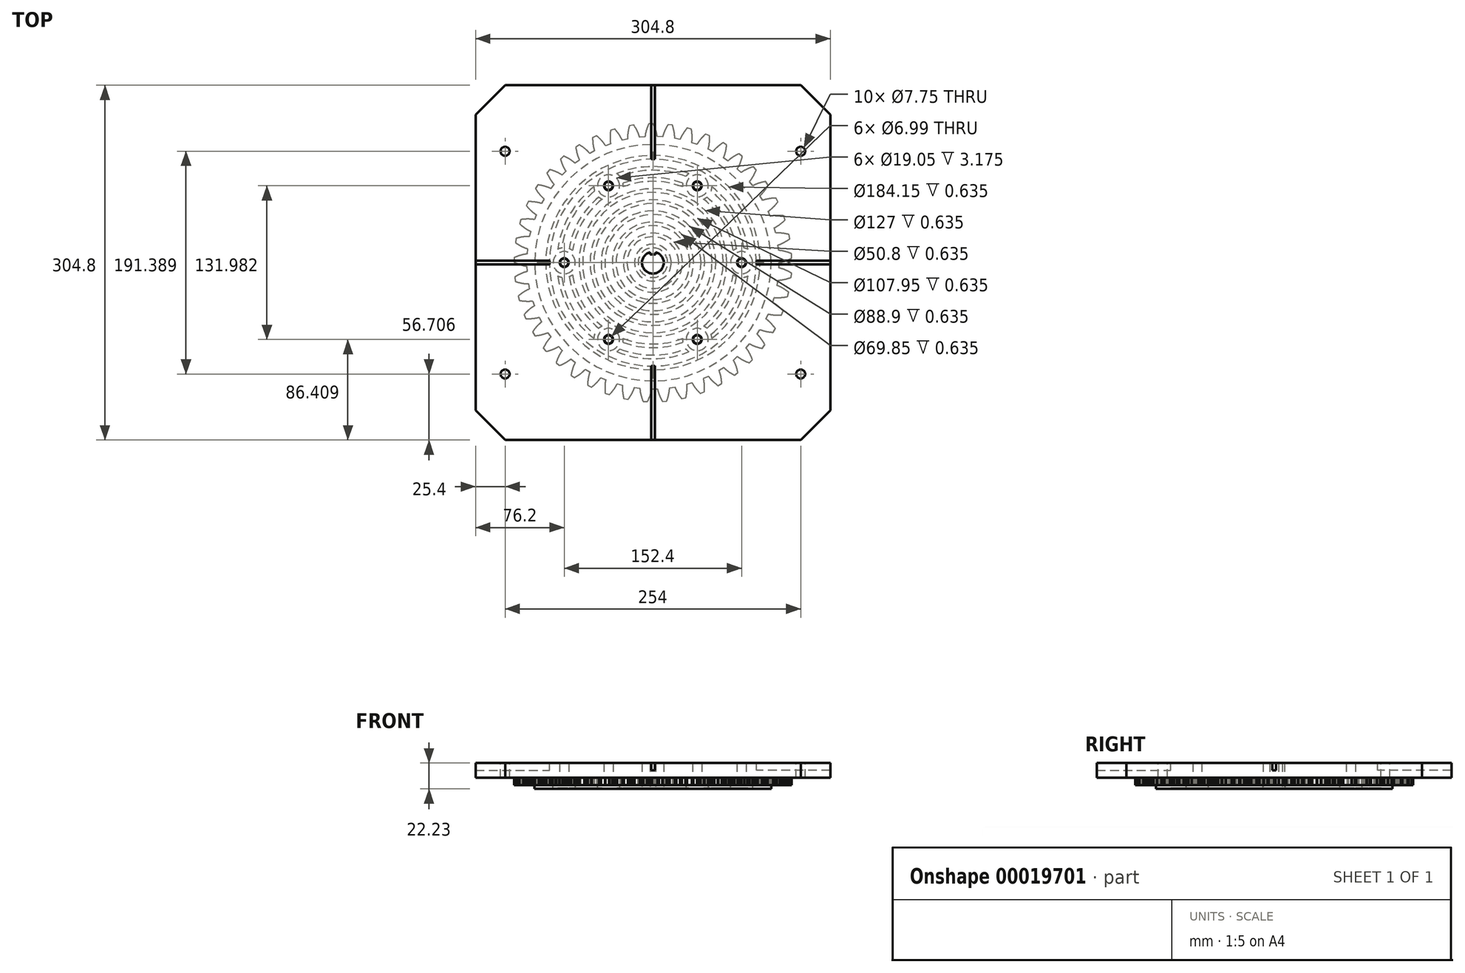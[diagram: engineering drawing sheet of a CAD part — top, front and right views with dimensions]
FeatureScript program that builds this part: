
annotation { "Feature Type Name" : "Feature", "Feature Type Description" : "" }
export const myFeature = defineFeature(function(context is Context, id is Id, definition is map)
    precondition{}
    {
        {
            var Q0;
            Q0=qCreatedBy(makeId("Top.planeOp"),FACE);
            var sketch = newSketch(context, id + "F0", { "sketchPlane" : qUnion([Q0])});
            skLineSegment(sketch, "E0", {"start": v(108.5, -0.05) * mm, "end": v(108.76, 0.09) * mm});
            skLineSegment(sketch, "E1", {"start": v(108.76, 0.09) * mm, "end": v(108.9, 0.11) * mm});
            skLineSegment(sketch, "E2", {"start": v(108.9, 0.11) * mm, "end": v(109.03, 0.13) * mm});
            skLineSegment(sketch, "E3", {"start": v(109.03, 0.13) * mm, "end": v(109.17, 0.16) * mm});
            skLineSegment(sketch, "E4", {"start": v(109.17, 0.16) * mm, "end": v(109.32, 0.19) * mm});
            skLineSegment(sketch, "E5", {"start": v(109.32, 0.19) * mm, "end": v(109.48, 0.22) * mm});
            skLineSegment(sketch, "E6", {"start": v(109.48, 0.22) * mm, "end": v(109.64, 0.25) * mm});
            skLineSegment(sketch, "E7", {"start": v(109.64, 0.25) * mm, "end": v(109.81, 0.29) * mm});
            skLineSegment(sketch, "E8", {"start": v(109.81, 0.29) * mm, "end": v(109.99, 0.33) * mm});
            skLineSegment(sketch, "E9", {"start": v(109.99, 0.33) * mm, "end": v(110.17, 0.37) * mm});
            skLineSegment(sketch, "E10", {"start": v(110.17, 0.37) * mm, "end": v(110.36, 0.41) * mm});
            skLineSegment(sketch, "E11", {"start": v(110.36, 0.41) * mm, "end": v(110.55, 0.46) * mm});
            skLineSegment(sketch, "E12", {"start": v(110.55, 0.46) * mm, "end": v(110.75, 0.5) * mm});
            skLineSegment(sketch, "E13", {"start": v(110.75, 0.5) * mm, "end": v(110.95, 0.56) * mm});
            skLineSegment(sketch, "E14", {"start": v(110.95, 0.56) * mm, "end": v(111.17, 0.62) * mm});
            skLineSegment(sketch, "E15", {"start": v(111.17, 0.62) * mm, "end": v(111.38, 0.68) * mm});
            skLineSegment(sketch, "E16", {"start": v(111.38, 0.68) * mm, "end": v(111.6, 0.74) * mm});
            skLineSegment(sketch, "E17", {"start": v(111.6, 0.74) * mm, "end": v(111.83, 0.8) * mm});
            skLineSegment(sketch, "E18", {"start": v(111.83, 0.8) * mm, "end": v(112.07, 0.88) * mm});
            skLineSegment(sketch, "E19", {"start": v(112.07, 0.88) * mm, "end": v(112.3, 0.95) * mm});
            skLineSegment(sketch, "E20", {"start": v(112.3, 0.95) * mm, "end": v(112.55, 1.03) * mm});
            skLineSegment(sketch, "E21", {"start": v(112.55, 1.03) * mm, "end": v(112.8, 1.11) * mm});
            skLineSegment(sketch, "E22", {"start": v(112.8, 1.11) * mm, "end": v(113.06, 1.2) * mm});
            skLineSegment(sketch, "E23", {"start": v(113.06, 1.2) * mm, "end": v(113.32, 1.29) * mm});
            skLineSegment(sketch, "E24", {"start": v(113.32, 1.29) * mm, "end": v(113.58, 1.38) * mm});
            skLineSegment(sketch, "E25", {"start": v(113.58, 1.38) * mm, "end": v(113.86, 1.48) * mm});
            skLineSegment(sketch, "E26", {"start": v(113.86, 1.48) * mm, "end": v(114.13, 1.58) * mm});
            skLineSegment(sketch, "E27", {"start": v(114.13, 1.58) * mm, "end": v(114.42, 1.69) * mm});
            skLineSegment(sketch, "E28", {"start": v(114.42, 1.69) * mm, "end": v(114.7, 1.8) * mm});
            skLineSegment(sketch, "E29", {"start": v(114.7, 1.8) * mm, "end": v(115, 1.92) * mm});
            skLineSegment(sketch, "E30", {"start": v(115, 1.92) * mm, "end": v(115.3, 2.04) * mm});
            skLineSegment(sketch, "E31", {"start": v(115.3, 2.04) * mm, "end": v(115.6, 2.16) * mm});
            skLineSegment(sketch, "E32", {"start": v(115.6, 2.16) * mm, "end": v(115.9, 2.3) * mm});
            skLineSegment(sketch, "E33", {"start": v(115.9, 2.3) * mm, "end": v(116.22, 2.43) * mm});
            skLineSegment(sketch, "E34", {"start": v(116.22, 2.43) * mm, "end": v(116.54, 2.57) * mm});
            skLineSegment(sketch, "E35", {"start": v(116.54, 2.57) * mm, "end": v(116.86, 2.72) * mm});
            skLineSegment(sketch, "E36", {"start": v(116.86, 2.72) * mm, "end": v(117.18, 2.87) * mm});
            skLineSegment(sketch, "E37", {"start": v(117.18, 2.87) * mm, "end": v(117.52, 3.03) * mm});
            skLineSegment(sketch, "E38", {"start": v(117.52, 3.03) * mm, "end": v(117.85, 3.19) * mm});
            skLineSegment(sketch, "E39", {"start": v(117.85, 3.19) * mm, "end": v(118.2, 3.35) * mm});
            skLineSegment(sketch, "E40", {"start": v(118.2, 3.35) * mm, "end": v(118.54, 3.53) * mm});
            skLineSegment(sketch, "E41", {"start": v(118.54, 3.53) * mm, "end": v(118.89, 3.7) * mm});
            skLineSegment(sketch, "E42", {"start": v(118.89, 3.7) * mm, "end": v(119.24, 3.89) * mm});
            skLineSegment(sketch, "E43", {"start": v(119.24, 3.89) * mm, "end": v(119.34, 4.07) * mm});
            skLineSegment(sketch, "E44", {"start": v(119.34, 4.07) * mm, "end": v(119.17, 7.58) * mm});
            skLineSegment(sketch, "E45", {"start": v(119.17, 7.58) * mm, "end": v(119.05, 7.75) * mm});
            skLineSegment(sketch, "E46", {"start": v(119.05, 7.75) * mm, "end": v(118.68, 7.9) * mm});
            skLineSegment(sketch, "E47", {"start": v(118.68, 7.9) * mm, "end": v(118.32, 8.04) * mm});
            skLineSegment(sketch, "E48", {"start": v(118.32, 8.04) * mm, "end": v(117.96, 8.17) * mm});
            skLineSegment(sketch, "E49", {"start": v(117.96, 8.17) * mm, "end": v(117.6, 8.3) * mm});
            skLineSegment(sketch, "E50", {"start": v(117.6, 8.3) * mm, "end": v(117.25, 8.43) * mm});
            skLineSegment(sketch, "E51", {"start": v(117.25, 8.43) * mm, "end": v(116.9, 8.56) * mm});
            skLineSegment(sketch, "E52", {"start": v(116.9, 8.56) * mm, "end": v(116.56, 8.68) * mm});
            skLineSegment(sketch, "E53", {"start": v(116.56, 8.68) * mm, "end": v(116.23, 8.79) * mm});
            skLineSegment(sketch, "E54", {"start": v(116.23, 8.79) * mm, "end": v(115.9, 8.9) * mm});
            skLineSegment(sketch, "E55", {"start": v(115.9, 8.9) * mm, "end": v(115.57, 9) * mm});
            skLineSegment(sketch, "E56", {"start": v(115.57, 9) * mm, "end": v(115.25, 9.1) * mm});
            skLineSegment(sketch, "E57", {"start": v(115.25, 9.1) * mm, "end": v(114.94, 9.2) * mm});
            skLineSegment(sketch, "E58", {"start": v(114.94, 9.2) * mm, "end": v(114.63, 9.29) * mm});
            skLineSegment(sketch, "E59", {"start": v(114.63, 9.29) * mm, "end": v(114.33, 9.38) * mm});
            skLineSegment(sketch, "E60", {"start": v(114.33, 9.38) * mm, "end": v(114.03, 9.46) * mm});
            skLineSegment(sketch, "E61", {"start": v(114.03, 9.46) * mm, "end": v(113.74, 9.54) * mm});
            skLineSegment(sketch, "E62", {"start": v(113.74, 9.54) * mm, "end": v(113.46, 9.61) * mm});
            skLineSegment(sketch, "E63", {"start": v(113.46, 9.61) * mm, "end": v(113.17, 9.68) * mm});
            skLineSegment(sketch, "E64", {"start": v(113.17, 9.68) * mm, "end": v(112.9, 9.75) * mm});
            skLineSegment(sketch, "E65", {"start": v(112.9, 9.75) * mm, "end": v(112.63, 9.82) * mm});
            skLineSegment(sketch, "E66", {"start": v(112.63, 9.82) * mm, "end": v(112.37, 9.88) * mm});
            skLineSegment(sketch, "E67", {"start": v(112.37, 9.88) * mm, "end": v(112.11, 9.93) * mm});
            skLineSegment(sketch, "E68", {"start": v(112.11, 9.93) * mm, "end": v(111.86, 9.99) * mm});
            skLineSegment(sketch, "E69", {"start": v(111.86, 9.99) * mm, "end": v(111.61, 10.04) * mm});
            skLineSegment(sketch, "E70", {"start": v(111.61, 10.04) * mm, "end": v(111.38, 10.08) * mm});
            skLineSegment(sketch, "E71", {"start": v(111.38, 10.08) * mm, "end": v(111.14, 10.13) * mm});
            skLineSegment(sketch, "E72", {"start": v(111.14, 10.13) * mm, "end": v(110.91, 10.17) * mm});
            skLineSegment(sketch, "E73", {"start": v(110.91, 10.17) * mm, "end": v(110.7, 10.2) * mm});
            skLineSegment(sketch, "E74", {"start": v(110.7, 10.2) * mm, "end": v(110.48, 10.24) * mm});
            skLineSegment(sketch, "E75", {"start": v(110.48, 10.24) * mm, "end": v(110.27, 10.28) * mm});
            skLineSegment(sketch, "E76", {"start": v(110.27, 10.28) * mm, "end": v(110.07, 10.3) * mm});
            skLineSegment(sketch, "E77", {"start": v(110.07, 10.3) * mm, "end": v(109.87, 10.33) * mm});
            skLineSegment(sketch, "E78", {"start": v(109.87, 10.33) * mm, "end": v(109.68, 10.36) * mm});
            skLineSegment(sketch, "E79", {"start": v(109.68, 10.36) * mm, "end": v(109.5, 10.38) * mm});
            skLineSegment(sketch, "E80", {"start": v(109.5, 10.38) * mm, "end": v(109.32, 10.4) * mm});
            skLineSegment(sketch, "E81", {"start": v(109.32, 10.4) * mm, "end": v(109.14, 10.42) * mm});
            skLineSegment(sketch, "E82", {"start": v(109.14, 10.42) * mm, "end": v(108.98, 10.44) * mm});
            skLineSegment(sketch, "E83", {"start": v(108.98, 10.44) * mm, "end": v(108.82, 10.45) * mm});
            skLineSegment(sketch, "E84", {"start": v(108.82, 10.45) * mm, "end": v(108.67, 10.47) * mm});
            skLineSegment(sketch, "E85", {"start": v(108.67, 10.47) * mm, "end": v(108.52, 10.48) * mm});
            skLineSegment(sketch, "E86", {"start": v(108.52, 10.48) * mm, "end": v(108.38, 10.49) * mm});
            skLineSegment(sketch, "E87", {"start": v(108.38, 10.49) * mm, "end": v(108.25, 10.5) * mm});
            skLineSegment(sketch, "E88", {"start": v(108.25, 10.5) * mm, "end": v(107.97, 10.6) * mm});
            skLineSegment(sketch, "E89", {"start": v(107.97, 10.6) * mm, "end": v(107.44, 15.05) * mm});
            skLineSegment(sketch, "E90", {"start": v(107.44, 15.05) * mm, "end": v(107.68, 15.22) * mm});
            skLineSegment(sketch, "E91", {"start": v(107.68, 15.22) * mm, "end": v(107.8, 15.26) * mm});
            skLineSegment(sketch, "E92", {"start": v(107.8, 15.26) * mm, "end": v(107.94, 15.3) * mm});
            skLineSegment(sketch, "E93", {"start": v(107.94, 15.3) * mm, "end": v(108.08, 15.35) * mm});
            skLineSegment(sketch, "E94", {"start": v(108.08, 15.35) * mm, "end": v(108.23, 15.4) * mm});
            skLineSegment(sketch, "E95", {"start": v(108.23, 15.4) * mm, "end": v(108.38, 15.45) * mm});
            skLineSegment(sketch, "E96", {"start": v(108.38, 15.45) * mm, "end": v(108.54, 15.5) * mm});
            skLineSegment(sketch, "E97", {"start": v(108.54, 15.5) * mm, "end": v(108.7, 15.56) * mm});
            skLineSegment(sketch, "E98", {"start": v(108.7, 15.56) * mm, "end": v(108.87, 15.62) * mm});
            skLineSegment(sketch, "E99", {"start": v(108.87, 15.62) * mm, "end": v(109.04, 15.7) * mm});
            skLineSegment(sketch, "E100", {"start": v(109.04, 15.7) * mm, "end": v(109.22, 15.76) * mm});
            skLineSegment(sketch, "E101", {"start": v(109.22, 15.76) * mm, "end": v(109.4, 15.83) * mm});
            skLineSegment(sketch, "E102", {"start": v(109.4, 15.83) * mm, "end": v(109.6, 15.91) * mm});
            skLineSegment(sketch, "E103", {"start": v(109.6, 15.91) * mm, "end": v(109.8, 16) * mm});
            skLineSegment(sketch, "E104", {"start": v(109.8, 16) * mm, "end": v(110, 16.08) * mm});
            skLineSegment(sketch, "E105", {"start": v(110, 16.08) * mm, "end": v(110.2, 16.17) * mm});
            skLineSegment(sketch, "E106", {"start": v(110.2, 16.17) * mm, "end": v(110.4, 16.26) * mm});
            skLineSegment(sketch, "E107", {"start": v(110.4, 16.26) * mm, "end": v(110.63, 16.36) * mm});
            skLineSegment(sketch, "E108", {"start": v(110.63, 16.36) * mm, "end": v(110.85, 16.46) * mm});
            skLineSegment(sketch, "E109", {"start": v(110.85, 16.46) * mm, "end": v(111.07, 16.57) * mm});
            skLineSegment(sketch, "E110", {"start": v(111.07, 16.57) * mm, "end": v(111.3, 16.68) * mm});
            skLineSegment(sketch, "E111", {"start": v(111.3, 16.68) * mm, "end": v(111.54, 16.8) * mm});
            skLineSegment(sketch, "E112", {"start": v(111.54, 16.8) * mm, "end": v(111.78, 16.91) * mm});
            skLineSegment(sketch, "E113", {"start": v(111.78, 16.91) * mm, "end": v(112.03, 17.04) * mm});
            skLineSegment(sketch, "E114", {"start": v(112.03, 17.04) * mm, "end": v(112.28, 17.17) * mm});
            skLineSegment(sketch, "E115", {"start": v(112.28, 17.17) * mm, "end": v(112.54, 17.3) * mm});
            skLineSegment(sketch, "E116", {"start": v(112.54, 17.3) * mm, "end": v(112.8, 17.45) * mm});
            skLineSegment(sketch, "E117", {"start": v(112.8, 17.45) * mm, "end": v(113.06, 17.6) * mm});
            skLineSegment(sketch, "E118", {"start": v(113.06, 17.6) * mm, "end": v(113.33, 17.74) * mm});
            skLineSegment(sketch, "E119", {"start": v(113.33, 17.74) * mm, "end": v(113.6, 17.9) * mm});
            skLineSegment(sketch, "E120", {"start": v(113.6, 17.9) * mm, "end": v(113.88, 18.06) * mm});
            skLineSegment(sketch, "E121", {"start": v(113.88, 18.06) * mm, "end": v(114.16, 18.23) * mm});
            skLineSegment(sketch, "E122", {"start": v(114.16, 18.23) * mm, "end": v(114.45, 18.4) * mm});
            skLineSegment(sketch, "E123", {"start": v(114.45, 18.4) * mm, "end": v(114.74, 18.58) * mm});
            skLineSegment(sketch, "E124", {"start": v(114.74, 18.58) * mm, "end": v(115.04, 18.76) * mm});
            skLineSegment(sketch, "E125", {"start": v(115.04, 18.76) * mm, "end": v(115.34, 18.95) * mm});
            skLineSegment(sketch, "E126", {"start": v(115.34, 18.95) * mm, "end": v(115.64, 19.14) * mm});
            skLineSegment(sketch, "E127", {"start": v(115.64, 19.14) * mm, "end": v(115.95, 19.34) * mm});
            skLineSegment(sketch, "E128", {"start": v(115.95, 19.34) * mm, "end": v(116.26, 19.55) * mm});
            skLineSegment(sketch, "E129", {"start": v(116.26, 19.55) * mm, "end": v(116.57, 19.77) * mm});
            skLineSegment(sketch, "E130", {"start": v(116.57, 19.77) * mm, "end": v(116.89, 19.98) * mm});
            skLineSegment(sketch, "E131", {"start": v(116.89, 19.98) * mm, "end": v(117.2, 20.2) * mm});
            skLineSegment(sketch, "E132", {"start": v(117.2, 20.2) * mm, "end": v(117.53, 20.44) * mm});
            skLineSegment(sketch, "E133", {"start": v(117.53, 20.44) * mm, "end": v(117.6, 20.63) * mm});
            skLineSegment(sketch, "E134", {"start": v(117.6, 20.63) * mm, "end": v(116.95, 24.08) * mm});
            skLineSegment(sketch, "E135", {"start": v(116.95, 24.08) * mm, "end": v(116.8, 24.23) * mm});
            skLineSegment(sketch, "E136", {"start": v(116.8, 24.23) * mm, "end": v(116.42, 24.33) * mm});
            skLineSegment(sketch, "E137", {"start": v(116.42, 24.33) * mm, "end": v(116.04, 24.42) * mm});
            skLineSegment(sketch, "E138", {"start": v(116.04, 24.42) * mm, "end": v(115.66, 24.5) * mm});
            skLineSegment(sketch, "E139", {"start": v(115.66, 24.5) * mm, "end": v(115.3, 24.59) * mm});
            skLineSegment(sketch, "E140", {"start": v(115.3, 24.59) * mm, "end": v(114.93, 24.67) * mm});
            skLineSegment(sketch, "E141", {"start": v(114.93, 24.67) * mm, "end": v(114.57, 24.74) * mm});
            skLineSegment(sketch, "E142", {"start": v(114.57, 24.74) * mm, "end": v(114.21, 24.8) * mm});
            skLineSegment(sketch, "E143", {"start": v(114.21, 24.8) * mm, "end": v(113.87, 24.87) * mm});
            skLineSegment(sketch, "E144", {"start": v(113.87, 24.87) * mm, "end": v(113.53, 24.94) * mm});
            skLineSegment(sketch, "E145", {"start": v(113.53, 24.94) * mm, "end": v(113.19, 25) * mm});
            skLineSegment(sketch, "E146", {"start": v(113.19, 25) * mm, "end": v(112.86, 25.05) * mm});
            skLineSegment(sketch, "E147", {"start": v(112.86, 25.05) * mm, "end": v(112.54, 25.1) * mm});
            skLineSegment(sketch, "E148", {"start": v(112.54, 25.1) * mm, "end": v(112.22, 25.15) * mm});
            skLineSegment(sketch, "E149", {"start": v(112.22, 25.15) * mm, "end": v(111.9, 25.2) * mm});
            skLineSegment(sketch, "E150", {"start": v(111.9, 25.2) * mm, "end": v(111.6, 25.23) * mm});
            skLineSegment(sketch, "E151", {"start": v(111.6, 25.23) * mm, "end": v(111.3, 25.27) * mm});
            skLineSegment(sketch, "E152", {"start": v(111.3, 25.27) * mm, "end": v(111, 25.3) * mm});
            skLineSegment(sketch, "E153", {"start": v(111, 25.3) * mm, "end": v(110.72, 25.34) * mm});
            skLineSegment(sketch, "E154", {"start": v(110.72, 25.34) * mm, "end": v(110.44, 25.36) * mm});
            skLineSegment(sketch, "E155", {"start": v(110.44, 25.36) * mm, "end": v(110.16, 25.39) * mm});
            skLineSegment(sketch, "E156", {"start": v(110.16, 25.39) * mm, "end": v(109.9, 25.41) * mm});
            skLineSegment(sketch, "E157", {"start": v(109.9, 25.41) * mm, "end": v(109.63, 25.43) * mm});
            skLineSegment(sketch, "E158", {"start": v(109.63, 25.43) * mm, "end": v(109.37, 25.45) * mm});
            skLineSegment(sketch, "E159", {"start": v(109.37, 25.45) * mm, "end": v(109.13, 25.47) * mm});
            skLineSegment(sketch, "E160", {"start": v(109.13, 25.47) * mm, "end": v(108.88, 25.48) * mm});
            skLineSegment(sketch, "E161", {"start": v(108.88, 25.48) * mm, "end": v(108.64, 25.5) * mm});
            skLineSegment(sketch, "E162", {"start": v(108.64, 25.5) * mm, "end": v(108.41, 25.5) * mm});
            skLineSegment(sketch, "E163", {"start": v(108.41, 25.5) * mm, "end": v(108.19, 25.5) * mm});
            skLineSegment(sketch, "E164", {"start": v(108.19, 25.5) * mm, "end": v(107.97, 25.51) * mm});
            skLineSegment(sketch, "E165", {"start": v(107.97, 25.51) * mm, "end": v(107.76, 25.52) * mm});
            skLineSegment(sketch, "E166", {"start": v(107.76, 25.52) * mm, "end": v(107.55, 25.52) * mm});
            skLineSegment(sketch, "E167", {"start": v(107.55, 25.52) * mm, "end": v(107.36, 25.52) * mm});
            skLineSegment(sketch, "E168", {"start": v(107.36, 25.52) * mm, "end": v(107.16, 25.52) * mm});
            skLineSegment(sketch, "E169", {"start": v(107.16, 25.52) * mm, "end": v(106.98, 25.51) * mm});
            skLineSegment(sketch, "E170", {"start": v(106.98, 25.51) * mm, "end": v(106.8, 25.5) * mm});
            skLineSegment(sketch, "E171", {"start": v(106.8, 25.5) * mm, "end": v(106.62, 25.5) * mm});
            skLineSegment(sketch, "E172", {"start": v(106.62, 25.5) * mm, "end": v(106.46, 25.5) * mm});
            skLineSegment(sketch, "E173", {"start": v(106.46, 25.5) * mm, "end": v(106.3, 25.5) * mm});
            skLineSegment(sketch, "E174", {"start": v(106.3, 25.5) * mm, "end": v(106.15, 25.48) * mm});
            skLineSegment(sketch, "E175", {"start": v(106.15, 25.48) * mm, "end": v(106, 25.47) * mm});
            skLineSegment(sketch, "E176", {"start": v(106, 25.47) * mm, "end": v(105.86, 25.46) * mm});
            skLineSegment(sketch, "E177", {"start": v(105.86, 25.46) * mm, "end": v(105.72, 25.45) * mm});
            skLineSegment(sketch, "E178", {"start": v(105.72, 25.45) * mm, "end": v(105.43, 25.53) * mm});
            skLineSegment(sketch, "E179", {"start": v(105.43, 25.53) * mm, "end": v(104.3, 29.85) * mm});
            skLineSegment(sketch, "E180", {"start": v(104.3, 29.85) * mm, "end": v(104.5, 30.05) * mm});
            skLineSegment(sketch, "E181", {"start": v(104.5, 30.05) * mm, "end": v(104.63, 30.1) * mm});
            skLineSegment(sketch, "E182", {"start": v(104.63, 30.1) * mm, "end": v(104.76, 30.17) * mm});
            skLineSegment(sketch, "E183", {"start": v(104.76, 30.17) * mm, "end": v(104.89, 30.23) * mm});
            skLineSegment(sketch, "E184", {"start": v(104.89, 30.23) * mm, "end": v(105.03, 30.3) * mm});
            skLineSegment(sketch, "E185", {"start": v(105.03, 30.3) * mm, "end": v(105.17, 30.38) * mm});
            skLineSegment(sketch, "E186", {"start": v(105.17, 30.38) * mm, "end": v(105.32, 30.45) * mm});
            skLineSegment(sketch, "E187", {"start": v(105.32, 30.45) * mm, "end": v(105.47, 30.53) * mm});
            skLineSegment(sketch, "E188", {"start": v(105.47, 30.53) * mm, "end": v(105.63, 30.62) * mm});
            skLineSegment(sketch, "E189", {"start": v(105.63, 30.62) * mm, "end": v(105.79, 30.7) * mm});
            skLineSegment(sketch, "E190", {"start": v(105.79, 30.7) * mm, "end": v(105.96, 30.8) * mm});
            skLineSegment(sketch, "E191", {"start": v(105.96, 30.8) * mm, "end": v(106.13, 30.9) * mm});
            skLineSegment(sketch, "E192", {"start": v(106.13, 30.9) * mm, "end": v(106.3, 31) * mm});
            skLineSegment(sketch, "E193", {"start": v(106.3, 31) * mm, "end": v(106.49, 31.11) * mm});
            skLineSegment(sketch, "E194", {"start": v(106.49, 31.11) * mm, "end": v(106.68, 31.22) * mm});
            skLineSegment(sketch, "E195", {"start": v(106.68, 31.22) * mm, "end": v(106.87, 31.34) * mm});
            skLineSegment(sketch, "E196", {"start": v(106.87, 31.34) * mm, "end": v(107.06, 31.46) * mm});
            skLineSegment(sketch, "E197", {"start": v(107.06, 31.46) * mm, "end": v(107.27, 31.59) * mm});
            skLineSegment(sketch, "E198", {"start": v(107.27, 31.59) * mm, "end": v(107.47, 31.72) * mm});
            skLineSegment(sketch, "E199", {"start": v(107.47, 31.72) * mm, "end": v(107.68, 31.86) * mm});
            skLineSegment(sketch, "E200", {"start": v(107.68, 31.86) * mm, "end": v(107.9, 32) * mm});
            skLineSegment(sketch, "E201", {"start": v(107.9, 32) * mm, "end": v(108.11, 32.15) * mm});
            skLineSegment(sketch, "E202", {"start": v(108.11, 32.15) * mm, "end": v(108.33, 32.3) * mm});
            skLineSegment(sketch, "E203", {"start": v(108.33, 32.3) * mm, "end": v(108.56, 32.46) * mm});
            skLineSegment(sketch, "E204", {"start": v(108.56, 32.46) * mm, "end": v(108.79, 32.62) * mm});
            skLineSegment(sketch, "E205", {"start": v(108.79, 32.62) * mm, "end": v(109.02, 32.8) * mm});
            skLineSegment(sketch, "E206", {"start": v(109.02, 32.8) * mm, "end": v(109.26, 32.97) * mm});
            skLineSegment(sketch, "E207", {"start": v(109.26, 32.97) * mm, "end": v(109.5, 33.15) * mm});
            skLineSegment(sketch, "E208", {"start": v(109.5, 33.15) * mm, "end": v(109.75, 33.34) * mm});
            skLineSegment(sketch, "E209", {"start": v(109.75, 33.34) * mm, "end": v(110, 33.53) * mm});
            skLineSegment(sketch, "E210", {"start": v(110, 33.53) * mm, "end": v(110.25, 33.73) * mm});
            skLineSegment(sketch, "E211", {"start": v(110.25, 33.73) * mm, "end": v(110.5, 33.93) * mm});
            skLineSegment(sketch, "E212", {"start": v(110.5, 33.93) * mm, "end": v(110.77, 34.14) * mm});
            skLineSegment(sketch, "E213", {"start": v(110.77, 34.14) * mm, "end": v(111.03, 34.36) * mm});
            skLineSegment(sketch, "E214", {"start": v(111.03, 34.36) * mm, "end": v(111.3, 34.58) * mm});
            skLineSegment(sketch, "E215", {"start": v(111.3, 34.58) * mm, "end": v(111.57, 34.81) * mm});
            skLineSegment(sketch, "E216", {"start": v(111.57, 34.81) * mm, "end": v(111.84, 35.05) * mm});
            skLineSegment(sketch, "E217", {"start": v(111.84, 35.05) * mm, "end": v(112.12, 35.29) * mm});
            skLineSegment(sketch, "E218", {"start": v(112.12, 35.29) * mm, "end": v(112.4, 35.54) * mm});
            skLineSegment(sketch, "E219", {"start": v(112.4, 35.54) * mm, "end": v(112.68, 35.8) * mm});
            skLineSegment(sketch, "E220", {"start": v(112.68, 35.8) * mm, "end": v(112.96, 36.05) * mm});
            skLineSegment(sketch, "E221", {"start": v(112.96, 36.05) * mm, "end": v(113.25, 36.32) * mm});
            skLineSegment(sketch, "E222", {"start": v(113.25, 36.32) * mm, "end": v(113.54, 36.6) * mm});
            skLineSegment(sketch, "E223", {"start": v(113.54, 36.6) * mm, "end": v(113.59, 36.8) * mm});
            skLineSegment(sketch, "E224", {"start": v(113.59, 36.8) * mm, "end": v(112.45, 40.12) * mm});
            skLineSegment(sketch, "E225", {"start": v(112.45, 40.12) * mm, "end": v(112.3, 40.25) * mm});
            skLineSegment(sketch, "E226", {"start": v(112.3, 40.25) * mm, "end": v(111.9, 40.29) * mm});
            skLineSegment(sketch, "E227", {"start": v(111.9, 40.29) * mm, "end": v(111.5, 40.33) * mm});
            skLineSegment(sketch, "E228", {"start": v(111.5, 40.33) * mm, "end": v(111.12, 40.36) * mm});
            skLineSegment(sketch, "E229", {"start": v(111.12, 40.36) * mm, "end": v(110.74, 40.39) * mm});
            skLineSegment(sketch, "E230", {"start": v(110.74, 40.39) * mm, "end": v(110.37, 40.42) * mm});
            skLineSegment(sketch, "E231", {"start": v(110.37, 40.42) * mm, "end": v(110, 40.44) * mm});
            skLineSegment(sketch, "E232", {"start": v(110, 40.44) * mm, "end": v(109.64, 40.46) * mm});
            skLineSegment(sketch, "E233", {"start": v(109.64, 40.46) * mm, "end": v(109.3, 40.47) * mm});
            skLineSegment(sketch, "E234", {"start": v(109.3, 40.47) * mm, "end": v(108.94, 40.49) * mm});
            skLineSegment(sketch, "E235", {"start": v(108.94, 40.49) * mm, "end": v(108.6, 40.5) * mm});
            skLineSegment(sketch, "E236", {"start": v(108.6, 40.5) * mm, "end": v(108.27, 40.5) * mm});
            skLineSegment(sketch, "E237", {"start": v(108.27, 40.5) * mm, "end": v(107.94, 40.51) * mm});
            skLineSegment(sketch, "E238", {"start": v(107.94, 40.51) * mm, "end": v(107.62, 40.51) * mm});
            skLineSegment(sketch, "E239", {"start": v(107.62, 40.51) * mm, "end": v(107.3, 40.51) * mm});
            skLineSegment(sketch, "E240", {"start": v(107.3, 40.51) * mm, "end": v(107, 40.51) * mm});
            skLineSegment(sketch, "E241", {"start": v(107, 40.51) * mm, "end": v(106.7, 40.5) * mm});
            skLineSegment(sketch, "E242", {"start": v(106.7, 40.5) * mm, "end": v(106.4, 40.5) * mm});
            skLineSegment(sketch, "E243", {"start": v(106.4, 40.5) * mm, "end": v(106.1, 40.5) * mm});
            skLineSegment(sketch, "E244", {"start": v(106.1, 40.5) * mm, "end": v(105.83, 40.48) * mm});
            skLineSegment(sketch, "E245", {"start": v(105.83, 40.48) * mm, "end": v(105.55, 40.47) * mm});
            skLineSegment(sketch, "E246", {"start": v(105.55, 40.47) * mm, "end": v(105.28, 40.45) * mm});
            skLineSegment(sketch, "E247", {"start": v(105.28, 40.45) * mm, "end": v(105.02, 40.44) * mm});
            skLineSegment(sketch, "E248", {"start": v(105.02, 40.44) * mm, "end": v(104.76, 40.42) * mm});
            skLineSegment(sketch, "E249", {"start": v(104.76, 40.42) * mm, "end": v(104.51, 40.4) * mm});
            skLineSegment(sketch, "E250", {"start": v(104.51, 40.4) * mm, "end": v(104.27, 40.38) * mm});
            skLineSegment(sketch, "E251", {"start": v(104.27, 40.38) * mm, "end": v(104.03, 40.36) * mm});
            skLineSegment(sketch, "E252", {"start": v(104.03, 40.36) * mm, "end": v(103.8, 40.34) * mm});
            skLineSegment(sketch, "E253", {"start": v(103.8, 40.34) * mm, "end": v(103.58, 40.31) * mm});
            skLineSegment(sketch, "E254", {"start": v(103.58, 40.31) * mm, "end": v(103.36, 40.29) * mm});
            skLineSegment(sketch, "E255", {"start": v(103.36, 40.29) * mm, "end": v(103.15, 40.26) * mm});
            skLineSegment(sketch, "E256", {"start": v(103.15, 40.26) * mm, "end": v(102.95, 40.23) * mm});
            skLineSegment(sketch, "E257", {"start": v(102.95, 40.23) * mm, "end": v(102.75, 40.2) * mm});
            skLineSegment(sketch, "E258", {"start": v(102.75, 40.2) * mm, "end": v(102.56, 40.18) * mm});
            skLineSegment(sketch, "E259", {"start": v(102.56, 40.18) * mm, "end": v(102.38, 40.15) * mm});
            skLineSegment(sketch, "E260", {"start": v(102.38, 40.15) * mm, "end": v(102.2, 40.12) * mm});
            skLineSegment(sketch, "E261", {"start": v(102.2, 40.12) * mm, "end": v(102.03, 40.1) * mm});
            skLineSegment(sketch, "E262", {"start": v(102.03, 40.1) * mm, "end": v(101.87, 40.06) * mm});
            skLineSegment(sketch, "E263", {"start": v(101.87, 40.06) * mm, "end": v(101.71, 40.03) * mm});
            skLineSegment(sketch, "E264", {"start": v(101.71, 40.03) * mm, "end": v(101.56, 40) * mm});
            skLineSegment(sketch, "E265", {"start": v(101.56, 40) * mm, "end": v(101.42, 39.97) * mm});
            skLineSegment(sketch, "E266", {"start": v(101.42, 39.97) * mm, "end": v(101.28, 39.94) * mm});
            skLineSegment(sketch, "E267", {"start": v(101.28, 39.94) * mm, "end": v(101.15, 39.91) * mm});
            skLineSegment(sketch, "E268", {"start": v(101.15, 39.91) * mm, "end": v(100.85, 39.95) * mm});
            skLineSegment(sketch, "E269", {"start": v(100.85, 39.95) * mm, "end": v(99.12, 44.06) * mm});
            skLineSegment(sketch, "E270", {"start": v(99.12, 44.06) * mm, "end": v(99.3, 44.3) * mm});
            skLineSegment(sketch, "E271", {"start": v(99.3, 44.3) * mm, "end": v(99.41, 44.37) * mm});
            skLineSegment(sketch, "E272", {"start": v(99.41, 44.37) * mm, "end": v(99.53, 44.45) * mm});
            skLineSegment(sketch, "E273", {"start": v(99.53, 44.45) * mm, "end": v(99.65, 44.53) * mm});
            skLineSegment(sketch, "E274", {"start": v(99.65, 44.53) * mm, "end": v(99.78, 44.62) * mm});
            skLineSegment(sketch, "E275", {"start": v(99.78, 44.62) * mm, "end": v(99.91, 44.71) * mm});
            skLineSegment(sketch, "E276", {"start": v(99.91, 44.71) * mm, "end": v(100.05, 44.8) * mm});
            skLineSegment(sketch, "E277", {"start": v(100.05, 44.8) * mm, "end": v(100.19, 44.9) * mm});
            skLineSegment(sketch, "E278", {"start": v(100.19, 44.9) * mm, "end": v(100.33, 45.02) * mm});
            skLineSegment(sketch, "E279", {"start": v(100.33, 45.02) * mm, "end": v(100.48, 45.13) * mm});
            skLineSegment(sketch, "E280", {"start": v(100.48, 45.13) * mm, "end": v(100.63, 45.24) * mm});
            skLineSegment(sketch, "E281", {"start": v(100.63, 45.24) * mm, "end": v(100.79, 45.36) * mm});
            skLineSegment(sketch, "E282", {"start": v(100.79, 45.36) * mm, "end": v(100.95, 45.5) * mm});
            skLineSegment(sketch, "E283", {"start": v(100.95, 45.5) * mm, "end": v(101.12, 45.62) * mm});
            skLineSegment(sketch, "E284", {"start": v(101.12, 45.62) * mm, "end": v(101.29, 45.76) * mm});
            skLineSegment(sketch, "E285", {"start": v(101.29, 45.76) * mm, "end": v(101.46, 45.9) * mm});
            skLineSegment(sketch, "E286", {"start": v(101.46, 45.9) * mm, "end": v(101.64, 46.05) * mm});
            skLineSegment(sketch, "E287", {"start": v(101.64, 46.05) * mm, "end": v(101.82, 46.2) * mm});
            skLineSegment(sketch, "E288", {"start": v(101.82, 46.2) * mm, "end": v(102, 46.36) * mm});
            skLineSegment(sketch, "E289", {"start": v(102, 46.36) * mm, "end": v(102.2, 46.53) * mm});
            skLineSegment(sketch, "E290", {"start": v(102.2, 46.53) * mm, "end": v(102.38, 46.7) * mm});
            skLineSegment(sketch, "E291", {"start": v(102.38, 46.7) * mm, "end": v(102.58, 46.88) * mm});
            skLineSegment(sketch, "E292", {"start": v(102.58, 46.88) * mm, "end": v(102.78, 47.06) * mm});
            skLineSegment(sketch, "E293", {"start": v(102.78, 47.06) * mm, "end": v(102.98, 47.25) * mm});
            skLineSegment(sketch, "E294", {"start": v(102.98, 47.25) * mm, "end": v(103.18, 47.44) * mm});
            skLineSegment(sketch, "E295", {"start": v(103.18, 47.44) * mm, "end": v(103.4, 47.64) * mm});
            skLineSegment(sketch, "E296", {"start": v(103.4, 47.64) * mm, "end": v(103.6, 47.85) * mm});
            skLineSegment(sketch, "E297", {"start": v(103.6, 47.85) * mm, "end": v(103.82, 48.06) * mm});
            skLineSegment(sketch, "E298", {"start": v(103.82, 48.06) * mm, "end": v(104.04, 48.28) * mm});
            skLineSegment(sketch, "E299", {"start": v(104.04, 48.28) * mm, "end": v(104.26, 48.5) * mm});
            skLineSegment(sketch, "E300", {"start": v(104.26, 48.5) * mm, "end": v(104.48, 48.74) * mm});
            skLineSegment(sketch, "E301", {"start": v(104.48, 48.74) * mm, "end": v(104.7, 48.98) * mm});
            skLineSegment(sketch, "E302", {"start": v(104.7, 48.98) * mm, "end": v(104.93, 49.22) * mm});
            skLineSegment(sketch, "E303", {"start": v(104.93, 49.22) * mm, "end": v(105.16, 49.47) * mm});
            skLineSegment(sketch, "E304", {"start": v(105.16, 49.47) * mm, "end": v(105.4, 49.73) * mm});
            skLineSegment(sketch, "E305", {"start": v(105.4, 49.73) * mm, "end": v(105.63, 50) * mm});
            skLineSegment(sketch, "E306", {"start": v(105.63, 50) * mm, "end": v(105.87, 50.27) * mm});
            skLineSegment(sketch, "E307", {"start": v(105.87, 50.27) * mm, "end": v(106.1, 50.54) * mm});
            skLineSegment(sketch, "E308", {"start": v(106.1, 50.54) * mm, "end": v(106.35, 50.83) * mm});
            skLineSegment(sketch, "E309", {"start": v(106.35, 50.83) * mm, "end": v(106.6, 51.12) * mm});
            skLineSegment(sketch, "E310", {"start": v(106.6, 51.12) * mm, "end": v(106.84, 51.42) * mm});
            skLineSegment(sketch, "E311", {"start": v(106.84, 51.42) * mm, "end": v(107.09, 51.72) * mm});
            skLineSegment(sketch, "E312", {"start": v(107.09, 51.72) * mm, "end": v(107.34, 52.03) * mm});
            skLineSegment(sketch, "E313", {"start": v(107.34, 52.03) * mm, "end": v(107.35, 52.24) * mm});
            skLineSegment(sketch, "E314", {"start": v(107.35, 52.24) * mm, "end": v(105.77, 55.37) * mm});
            skLineSegment(sketch, "E315", {"start": v(105.77, 55.37) * mm, "end": v(105.6, 55.48) * mm});
            skLineSegment(sketch, "E316", {"start": v(105.6, 55.48) * mm, "end": v(105.2, 55.47) * mm});
            skLineSegment(sketch, "E317", {"start": v(105.2, 55.47) * mm, "end": v(104.8, 55.45) * mm});
            skLineSegment(sketch, "E318", {"start": v(104.8, 55.45) * mm, "end": v(104.42, 55.43) * mm});
            skLineSegment(sketch, "E319", {"start": v(104.42, 55.43) * mm, "end": v(104.04, 55.4) * mm});
            skLineSegment(sketch, "E320", {"start": v(104.04, 55.4) * mm, "end": v(103.66, 55.38) * mm});
            skLineSegment(sketch, "E321", {"start": v(103.66, 55.38) * mm, "end": v(103.3, 55.35) * mm});
            skLineSegment(sketch, "E322", {"start": v(103.3, 55.35) * mm, "end": v(102.94, 55.32) * mm});
            skLineSegment(sketch, "E323", {"start": v(102.94, 55.32) * mm, "end": v(102.59, 55.29) * mm});
            skLineSegment(sketch, "E324", {"start": v(102.59, 55.29) * mm, "end": v(102.24, 55.25) * mm});
            skLineSegment(sketch, "E325", {"start": v(102.24, 55.25) * mm, "end": v(101.9, 55.21) * mm});
            skLineSegment(sketch, "E326", {"start": v(101.9, 55.21) * mm, "end": v(101.57, 55.18) * mm});
            skLineSegment(sketch, "E327", {"start": v(101.57, 55.18) * mm, "end": v(101.25, 55.14) * mm});
            skLineSegment(sketch, "E328", {"start": v(101.25, 55.14) * mm, "end": v(100.93, 55.1) * mm});
            skLineSegment(sketch, "E329", {"start": v(100.93, 55.1) * mm, "end": v(100.61, 55.05) * mm});
            skLineSegment(sketch, "E330", {"start": v(100.61, 55.05) * mm, "end": v(100.3, 55) * mm});
            skLineSegment(sketch, "E331", {"start": v(100.3, 55) * mm, "end": v(100.01, 54.96) * mm});
            skLineSegment(sketch, "E332", {"start": v(100.01, 54.96) * mm, "end": v(99.72, 54.9) * mm});
            skLineSegment(sketch, "E333", {"start": v(99.72, 54.9) * mm, "end": v(99.43, 54.86) * mm});
            skLineSegment(sketch, "E334", {"start": v(99.43, 54.86) * mm, "end": v(99.16, 54.81) * mm});
            skLineSegment(sketch, "E335", {"start": v(99.16, 54.81) * mm, "end": v(98.88, 54.76) * mm});
            skLineSegment(sketch, "E336", {"start": v(98.88, 54.76) * mm, "end": v(98.62, 54.7) * mm});
            skLineSegment(sketch, "E337", {"start": v(98.62, 54.7) * mm, "end": v(98.36, 54.66) * mm});
            skLineSegment(sketch, "E338", {"start": v(98.36, 54.66) * mm, "end": v(98.11, 54.6) * mm});
            skLineSegment(sketch, "E339", {"start": v(98.11, 54.6) * mm, "end": v(97.87, 54.55) * mm});
            skLineSegment(sketch, "E340", {"start": v(97.87, 54.55) * mm, "end": v(97.63, 54.5) * mm});
            skLineSegment(sketch, "E341", {"start": v(97.63, 54.5) * mm, "end": v(97.4, 54.44) * mm});
            skLineSegment(sketch, "E342", {"start": v(97.4, 54.44) * mm, "end": v(97.17, 54.38) * mm});
            skLineSegment(sketch, "E343", {"start": v(97.17, 54.38) * mm, "end": v(96.95, 54.33) * mm});
            skLineSegment(sketch, "E344", {"start": v(96.95, 54.33) * mm, "end": v(96.74, 54.27) * mm});
            skLineSegment(sketch, "E345", {"start": v(96.74, 54.27) * mm, "end": v(96.54, 54.22) * mm});
            skLineSegment(sketch, "E346", {"start": v(96.54, 54.22) * mm, "end": v(96.34, 54.16) * mm});
            skLineSegment(sketch, "E347", {"start": v(96.34, 54.16) * mm, "end": v(96.15, 54.1) * mm});
            skLineSegment(sketch, "E348", {"start": v(96.15, 54.1) * mm, "end": v(95.97, 54.05) * mm});
            skLineSegment(sketch, "E349", {"start": v(95.97, 54.05) * mm, "end": v(95.79, 54) * mm});
            skLineSegment(sketch, "E350", {"start": v(95.79, 54) * mm, "end": v(95.62, 53.95) * mm});
            skLineSegment(sketch, "E351", {"start": v(95.62, 53.95) * mm, "end": v(95.45, 53.9) * mm});
            skLineSegment(sketch, "E352", {"start": v(95.45, 53.9) * mm, "end": v(95.3, 53.84) * mm});
            skLineSegment(sketch, "E353", {"start": v(95.3, 53.84) * mm, "end": v(95.14, 53.8) * mm});
            skLineSegment(sketch, "E354", {"start": v(95.14, 53.8) * mm, "end": v(95, 53.74) * mm});
            skLineSegment(sketch, "E355", {"start": v(95, 53.74) * mm, "end": v(94.86, 53.7) * mm});
            skLineSegment(sketch, "E356", {"start": v(94.86, 53.7) * mm, "end": v(94.73, 53.64) * mm});
            skLineSegment(sketch, "E357", {"start": v(94.73, 53.64) * mm, "end": v(94.6, 53.6) * mm});
            skLineSegment(sketch, "E358", {"start": v(94.6, 53.6) * mm, "end": v(94.3, 53.59) * mm});
            skLineSegment(sketch, "E359", {"start": v(94.3, 53.59) * mm, "end": v(92.01, 57.42) * mm});
            skLineSegment(sketch, "E360", {"start": v(92.01, 57.42) * mm, "end": v(92.16, 57.68) * mm});
            skLineSegment(sketch, "E361", {"start": v(92.16, 57.68) * mm, "end": v(92.26, 57.77) * mm});
            skLineSegment(sketch, "E362", {"start": v(92.26, 57.77) * mm, "end": v(92.37, 57.86) * mm});
            skLineSegment(sketch, "E363", {"start": v(92.37, 57.86) * mm, "end": v(92.48, 57.96) * mm});
            skLineSegment(sketch, "E364", {"start": v(92.48, 57.96) * mm, "end": v(92.6, 58.07) * mm});
            skLineSegment(sketch, "E365", {"start": v(92.6, 58.07) * mm, "end": v(92.7, 58.18) * mm});
            skLineSegment(sketch, "E366", {"start": v(92.7, 58.18) * mm, "end": v(92.83, 58.3) * mm});
            skLineSegment(sketch, "E367", {"start": v(92.83, 58.3) * mm, "end": v(92.95, 58.41) * mm});
            skLineSegment(sketch, "E368", {"start": v(92.95, 58.41) * mm, "end": v(93.08, 58.54) * mm});
            skLineSegment(sketch, "E369", {"start": v(93.08, 58.54) * mm, "end": v(93.21, 58.67) * mm});
            skLineSegment(sketch, "E370", {"start": v(93.21, 58.67) * mm, "end": v(93.35, 58.8) * mm});
            skLineSegment(sketch, "E371", {"start": v(93.35, 58.8) * mm, "end": v(93.49, 58.95) * mm});
            skLineSegment(sketch, "E372", {"start": v(93.49, 58.95) * mm, "end": v(93.63, 59.1) * mm});
            skLineSegment(sketch, "E373", {"start": v(93.63, 59.1) * mm, "end": v(93.78, 59.25) * mm});
            skLineSegment(sketch, "E374", {"start": v(93.78, 59.25) * mm, "end": v(93.93, 59.4) * mm});
            skLineSegment(sketch, "E375", {"start": v(93.93, 59.4) * mm, "end": v(94.08, 59.57) * mm});
            skLineSegment(sketch, "E376", {"start": v(94.08, 59.57) * mm, "end": v(94.23, 59.74) * mm});
            skLineSegment(sketch, "E377", {"start": v(94.23, 59.74) * mm, "end": v(94.4, 59.92) * mm});
            skLineSegment(sketch, "E378", {"start": v(94.4, 59.92) * mm, "end": v(94.55, 60.1) * mm});
            skLineSegment(sketch, "E379", {"start": v(94.55, 60.1) * mm, "end": v(94.71, 60.3) * mm});
            skLineSegment(sketch, "E380", {"start": v(94.71, 60.3) * mm, "end": v(94.88, 60.49) * mm});
            skLineSegment(sketch, "E381", {"start": v(94.88, 60.49) * mm, "end": v(95.05, 60.7) * mm});
            skLineSegment(sketch, "E382", {"start": v(95.05, 60.7) * mm, "end": v(95.22, 60.9) * mm});
            skLineSegment(sketch, "E383", {"start": v(95.22, 60.9) * mm, "end": v(95.4, 61.11) * mm});
            skLineSegment(sketch, "E384", {"start": v(95.4, 61.11) * mm, "end": v(95.57, 61.34) * mm});
            skLineSegment(sketch, "E385", {"start": v(95.57, 61.34) * mm, "end": v(95.75, 61.56) * mm});
            skLineSegment(sketch, "E386", {"start": v(95.75, 61.56) * mm, "end": v(95.93, 61.8) * mm});
            skLineSegment(sketch, "E387", {"start": v(95.93, 61.8) * mm, "end": v(96.11, 62.04) * mm});
            skLineSegment(sketch, "E388", {"start": v(96.11, 62.04) * mm, "end": v(96.3, 62.29) * mm});
            skLineSegment(sketch, "E389", {"start": v(96.3, 62.29) * mm, "end": v(96.48, 62.54) * mm});
            skLineSegment(sketch, "E390", {"start": v(96.48, 62.54) * mm, "end": v(96.67, 62.8) * mm});
            skLineSegment(sketch, "E391", {"start": v(96.67, 62.8) * mm, "end": v(96.86, 63.07) * mm});
            skLineSegment(sketch, "E392", {"start": v(96.86, 63.07) * mm, "end": v(97.06, 63.34) * mm});
            skLineSegment(sketch, "E393", {"start": v(97.06, 63.34) * mm, "end": v(97.25, 63.62) * mm});
            skLineSegment(sketch, "E394", {"start": v(97.25, 63.62) * mm, "end": v(97.44, 63.9) * mm});
            skLineSegment(sketch, "E395", {"start": v(97.44, 63.9) * mm, "end": v(97.64, 64.2) * mm});
            skLineSegment(sketch, "E396", {"start": v(97.64, 64.2) * mm, "end": v(97.84, 64.5) * mm});
            skLineSegment(sketch, "E397", {"start": v(97.84, 64.5) * mm, "end": v(98.04, 64.81) * mm});
            skLineSegment(sketch, "E398", {"start": v(98.04, 64.81) * mm, "end": v(98.23, 65.13) * mm});
            skLineSegment(sketch, "E399", {"start": v(98.23, 65.13) * mm, "end": v(98.44, 65.45) * mm});
            skLineSegment(sketch, "E400", {"start": v(98.44, 65.45) * mm, "end": v(98.64, 65.78) * mm});
            skLineSegment(sketch, "E401", {"start": v(98.64, 65.78) * mm, "end": v(98.84, 66.12) * mm});
            skLineSegment(sketch, "E402", {"start": v(98.84, 66.12) * mm, "end": v(99.04, 66.46) * mm});
            skLineSegment(sketch, "E403", {"start": v(99.04, 66.46) * mm, "end": v(99.03, 66.67) * mm});
            skLineSegment(sketch, "E404", {"start": v(99.03, 66.67) * mm, "end": v(97.03, 69.55) * mm});
            skLineSegment(sketch, "E405", {"start": v(97.03, 69.55) * mm, "end": v(96.84, 69.63) * mm});
            skLineSegment(sketch, "E406", {"start": v(96.84, 69.63) * mm, "end": v(96.44, 69.56) * mm});
            skLineSegment(sketch, "E407", {"start": v(96.44, 69.56) * mm, "end": v(96.06, 69.49) * mm});
            skLineSegment(sketch, "E408", {"start": v(96.06, 69.49) * mm, "end": v(95.68, 69.41) * mm});
            skLineSegment(sketch, "E409", {"start": v(95.68, 69.41) * mm, "end": v(95.3, 69.34) * mm});
            skLineSegment(sketch, "E410", {"start": v(95.3, 69.34) * mm, "end": v(94.94, 69.26) * mm});
            skLineSegment(sketch, "E411", {"start": v(94.94, 69.26) * mm, "end": v(94.58, 69.18) * mm});
            skLineSegment(sketch, "E412", {"start": v(94.58, 69.18) * mm, "end": v(94.23, 69.1) * mm});
            skLineSegment(sketch, "E413", {"start": v(94.23, 69.1) * mm, "end": v(93.89, 69.02) * mm});
            skLineSegment(sketch, "E414", {"start": v(93.89, 69.02) * mm, "end": v(93.55, 68.94) * mm});
            skLineSegment(sketch, "E415", {"start": v(93.55, 68.94) * mm, "end": v(93.22, 68.85) * mm});
            skLineSegment(sketch, "E416", {"start": v(93.22, 68.85) * mm, "end": v(92.9, 68.77) * mm});
            skLineSegment(sketch, "E417", {"start": v(92.9, 68.77) * mm, "end": v(92.58, 68.68) * mm});
            skLineSegment(sketch, "E418", {"start": v(92.58, 68.68) * mm, "end": v(92.27, 68.6) * mm});
            skLineSegment(sketch, "E419", {"start": v(92.27, 68.6) * mm, "end": v(91.97, 68.51) * mm});
            skLineSegment(sketch, "E420", {"start": v(91.97, 68.51) * mm, "end": v(91.67, 68.42) * mm});
            skLineSegment(sketch, "E421", {"start": v(91.67, 68.42) * mm, "end": v(91.38, 68.34) * mm});
            skLineSegment(sketch, "E422", {"start": v(91.38, 68.34) * mm, "end": v(91.1, 68.25) * mm});
            skLineSegment(sketch, "E423", {"start": v(91.1, 68.25) * mm, "end": v(90.82, 68.16) * mm});
            skLineSegment(sketch, "E424", {"start": v(90.82, 68.16) * mm, "end": v(90.56, 68.07) * mm});
            skLineSegment(sketch, "E425", {"start": v(90.56, 68.07) * mm, "end": v(90.3, 67.98) * mm});
            skLineSegment(sketch, "E426", {"start": v(90.3, 67.98) * mm, "end": v(90.04, 67.9) * mm});
            skLineSegment(sketch, "E427", {"start": v(90.04, 67.9) * mm, "end": v(89.8, 67.8) * mm});
            skLineSegment(sketch, "E428", {"start": v(89.8, 67.8) * mm, "end": v(89.55, 67.72) * mm});
            skLineSegment(sketch, "E429", {"start": v(89.55, 67.72) * mm, "end": v(89.32, 67.63) * mm});
            skLineSegment(sketch, "E430", {"start": v(89.32, 67.63) * mm, "end": v(89.09, 67.55) * mm});
            skLineSegment(sketch, "E431", {"start": v(89.09, 67.55) * mm, "end": v(88.87, 67.46) * mm});
            skLineSegment(sketch, "E432", {"start": v(88.87, 67.46) * mm, "end": v(88.65, 67.37) * mm});
            skLineSegment(sketch, "E433", {"start": v(88.65, 67.37) * mm, "end": v(88.44, 67.29) * mm});
            skLineSegment(sketch, "E434", {"start": v(88.44, 67.29) * mm, "end": v(88.24, 67.2) * mm});
            skLineSegment(sketch, "E435", {"start": v(88.24, 67.2) * mm, "end": v(88.05, 67.12) * mm});
            skLineSegment(sketch, "E436", {"start": v(88.05, 67.12) * mm, "end": v(87.86, 67.04) * mm});
            skLineSegment(sketch, "E437", {"start": v(87.86, 67.04) * mm, "end": v(87.68, 66.96) * mm});
            skLineSegment(sketch, "E438", {"start": v(87.68, 66.96) * mm, "end": v(87.5, 66.88) * mm});
            skLineSegment(sketch, "E439", {"start": v(87.5, 66.88) * mm, "end": v(87.33, 66.8) * mm});
            skLineSegment(sketch, "E440", {"start": v(87.33, 66.8) * mm, "end": v(87.17, 66.72) * mm});
            skLineSegment(sketch, "E441", {"start": v(87.17, 66.72) * mm, "end": v(87.02, 66.65) * mm});
            skLineSegment(sketch, "E442", {"start": v(87.02, 66.65) * mm, "end": v(86.87, 66.58) * mm});
            skLineSegment(sketch, "E443", {"start": v(86.87, 66.58) * mm, "end": v(86.72, 66.5) * mm});
            skLineSegment(sketch, "E444", {"start": v(86.72, 66.5) * mm, "end": v(86.59, 66.43) * mm});
            skLineSegment(sketch, "E445", {"start": v(86.59, 66.43) * mm, "end": v(86.46, 66.37) * mm});
            skLineSegment(sketch, "E446", {"start": v(86.46, 66.37) * mm, "end": v(86.33, 66.3) * mm});
            skLineSegment(sketch, "E447", {"start": v(86.33, 66.3) * mm, "end": v(86.21, 66.24) * mm});
            skLineSegment(sketch, "E448", {"start": v(86.21, 66.24) * mm, "end": v(85.92, 66.18) * mm});
            skLineSegment(sketch, "E449", {"start": v(85.92, 66.18) * mm, "end": v(83.12, 69.67) * mm});
            skLineSegment(sketch, "E450", {"start": v(83.12, 69.67) * mm, "end": v(83.23, 69.94) * mm});
            skLineSegment(sketch, "E451", {"start": v(83.23, 69.94) * mm, "end": v(83.32, 70.04) * mm});
            skLineSegment(sketch, "E452", {"start": v(83.32, 70.04) * mm, "end": v(83.41, 70.15) * mm});
            skLineSegment(sketch, "E453", {"start": v(83.41, 70.15) * mm, "end": v(83.5, 70.26) * mm});
            skLineSegment(sketch, "E454", {"start": v(83.5, 70.26) * mm, "end": v(83.6, 70.38) * mm});
            skLineSegment(sketch, "E455", {"start": v(83.6, 70.38) * mm, "end": v(83.7, 70.5) * mm});
            skLineSegment(sketch, "E456", {"start": v(83.7, 70.5) * mm, "end": v(83.8, 70.64) * mm});
            skLineSegment(sketch, "E457", {"start": v(83.8, 70.64) * mm, "end": v(83.91, 70.77) * mm});
            skLineSegment(sketch, "E458", {"start": v(83.91, 70.77) * mm, "end": v(84.02, 70.92) * mm});
            skLineSegment(sketch, "E459", {"start": v(84.02, 70.92) * mm, "end": v(84.14, 71.06) * mm});
            skLineSegment(sketch, "E460", {"start": v(84.14, 71.06) * mm, "end": v(84.25, 71.22) * mm});
            skLineSegment(sketch, "E461", {"start": v(84.25, 71.22) * mm, "end": v(84.37, 71.38) * mm});
            skLineSegment(sketch, "E462", {"start": v(84.37, 71.38) * mm, "end": v(84.49, 71.54) * mm});
            skLineSegment(sketch, "E463", {"start": v(84.49, 71.54) * mm, "end": v(84.61, 71.72) * mm});
            skLineSegment(sketch, "E464", {"start": v(84.61, 71.72) * mm, "end": v(84.74, 71.9) * mm});
            skLineSegment(sketch, "E465", {"start": v(84.74, 71.9) * mm, "end": v(84.86, 72.08) * mm});
            skLineSegment(sketch, "E466", {"start": v(84.86, 72.08) * mm, "end": v(85, 72.27) * mm});
            skLineSegment(sketch, "E467", {"start": v(85, 72.27) * mm, "end": v(85.13, 72.47) * mm});
            skLineSegment(sketch, "E468", {"start": v(85.13, 72.47) * mm, "end": v(85.26, 72.67) * mm});
            skLineSegment(sketch, "E469", {"start": v(85.26, 72.67) * mm, "end": v(85.4, 72.88) * mm});
            skLineSegment(sketch, "E470", {"start": v(85.4, 72.88) * mm, "end": v(85.53, 73.1) * mm});
            skLineSegment(sketch, "E471", {"start": v(85.53, 73.1) * mm, "end": v(85.67, 73.32) * mm});
            skLineSegment(sketch, "E472", {"start": v(85.67, 73.32) * mm, "end": v(85.81, 73.55) * mm});
            skLineSegment(sketch, "E473", {"start": v(85.81, 73.55) * mm, "end": v(85.95, 73.8) * mm});
            skLineSegment(sketch, "E474", {"start": v(85.95, 73.8) * mm, "end": v(86.1, 74.03) * mm});
            skLineSegment(sketch, "E475", {"start": v(86.1, 74.03) * mm, "end": v(86.24, 74.28) * mm});
            skLineSegment(sketch, "E476", {"start": v(86.24, 74.28) * mm, "end": v(86.39, 74.54) * mm});
            skLineSegment(sketch, "E477", {"start": v(86.39, 74.54) * mm, "end": v(86.54, 74.8) * mm});
            skLineSegment(sketch, "E478", {"start": v(86.54, 74.8) * mm, "end": v(86.69, 75.08) * mm});
            skLineSegment(sketch, "E479", {"start": v(86.69, 75.08) * mm, "end": v(86.84, 75.35) * mm});
            skLineSegment(sketch, "E480", {"start": v(86.84, 75.35) * mm, "end": v(86.99, 75.64) * mm});
            skLineSegment(sketch, "E481", {"start": v(86.99, 75.64) * mm, "end": v(87.14, 75.93) * mm});
            skLineSegment(sketch, "E482", {"start": v(87.14, 75.93) * mm, "end": v(87.29, 76.23) * mm});
            skLineSegment(sketch, "E483", {"start": v(87.29, 76.23) * mm, "end": v(87.44, 76.53) * mm});
            skLineSegment(sketch, "E484", {"start": v(87.44, 76.53) * mm, "end": v(87.6, 76.84) * mm});
            skLineSegment(sketch, "E485", {"start": v(87.6, 76.84) * mm, "end": v(87.75, 77.16) * mm});
            skLineSegment(sketch, "E486", {"start": v(87.75, 77.16) * mm, "end": v(87.9, 77.49) * mm});
            skLineSegment(sketch, "E487", {"start": v(87.9, 77.49) * mm, "end": v(88.05, 77.82) * mm});
            skLineSegment(sketch, "E488", {"start": v(88.05, 77.82) * mm, "end": v(88.2, 78.16) * mm});
            skLineSegment(sketch, "E489", {"start": v(88.2, 78.16) * mm, "end": v(88.36, 78.5) * mm});
            skLineSegment(sketch, "E490", {"start": v(88.36, 78.5) * mm, "end": v(88.52, 78.86) * mm});
            skLineSegment(sketch, "E491", {"start": v(88.52, 78.86) * mm, "end": v(88.67, 79.22) * mm});
            skLineSegment(sketch, "E492", {"start": v(88.67, 79.22) * mm, "end": v(88.82, 79.6) * mm});
            skLineSegment(sketch, "E493", {"start": v(88.82, 79.6) * mm, "end": v(88.78, 79.8) * mm});
            skLineSegment(sketch, "E494", {"start": v(88.78, 79.8) * mm, "end": v(86.4, 82.37) * mm});
            skLineSegment(sketch, "E495", {"start": v(86.4, 82.37) * mm, "end": v(86.2, 82.43) * mm});
            skLineSegment(sketch, "E496", {"start": v(86.2, 82.43) * mm, "end": v(85.82, 82.3) * mm});
            skLineSegment(sketch, "E497", {"start": v(85.82, 82.3) * mm, "end": v(85.45, 82.18) * mm});
            skLineSegment(sketch, "E498", {"start": v(85.45, 82.18) * mm, "end": v(85.08, 82.05) * mm});
            skLineSegment(sketch, "E499", {"start": v(85.08, 82.05) * mm, "end": v(84.72, 81.92) * mm});
            skLineSegment(sketch, "E500", {"start": v(84.72, 81.92) * mm, "end": v(84.37, 81.8) * mm});
            skLineSegment(sketch, "E501", {"start": v(84.37, 81.8) * mm, "end": v(84.03, 81.67) * mm});
            skLineSegment(sketch, "E502", {"start": v(84.03, 81.67) * mm, "end": v(83.7, 81.54) * mm});
            skLineSegment(sketch, "E503", {"start": v(83.7, 81.54) * mm, "end": v(83.36, 81.4) * mm});
            skLineSegment(sketch, "E504", {"start": v(83.36, 81.4) * mm, "end": v(83.04, 81.28) * mm});
            skLineSegment(sketch, "E505", {"start": v(83.04, 81.28) * mm, "end": v(82.72, 81.15) * mm});
            skLineSegment(sketch, "E506", {"start": v(82.72, 81.15) * mm, "end": v(82.42, 81.02) * mm});
            skLineSegment(sketch, "E507", {"start": v(82.42, 81.02) * mm, "end": v(82.11, 80.9) * mm});
            skLineSegment(sketch, "E508", {"start": v(82.11, 80.9) * mm, "end": v(81.82, 80.77) * mm});
            skLineSegment(sketch, "E509", {"start": v(81.82, 80.77) * mm, "end": v(81.53, 80.64) * mm});
            skLineSegment(sketch, "E510", {"start": v(81.53, 80.64) * mm, "end": v(81.25, 80.51) * mm});
            skLineSegment(sketch, "E511", {"start": v(81.25, 80.51) * mm, "end": v(80.98, 80.38) * mm});
            skLineSegment(sketch, "E512", {"start": v(80.98, 80.38) * mm, "end": v(80.7, 80.26) * mm});
            skLineSegment(sketch, "E513", {"start": v(80.7, 80.26) * mm, "end": v(80.45, 80.13) * mm});
            skLineSegment(sketch, "E514", {"start": v(80.45, 80.13) * mm, "end": v(80.2, 80) * mm});
            skLineSegment(sketch, "E515", {"start": v(80.2, 80) * mm, "end": v(79.95, 79.88) * mm});
            skLineSegment(sketch, "E516", {"start": v(79.95, 79.88) * mm, "end": v(79.7, 79.76) * mm});
            skLineSegment(sketch, "E517", {"start": v(79.7, 79.76) * mm, "end": v(79.47, 79.64) * mm});
            skLineSegment(sketch, "E518", {"start": v(79.47, 79.64) * mm, "end": v(79.25, 79.52) * mm});
            skLineSegment(sketch, "E519", {"start": v(79.25, 79.52) * mm, "end": v(79.03, 79.4) * mm});
            skLineSegment(sketch, "E520", {"start": v(79.03, 79.4) * mm, "end": v(78.81, 79.28) * mm});
            skLineSegment(sketch, "E521", {"start": v(78.81, 79.28) * mm, "end": v(78.6, 79.16) * mm});
            skLineSegment(sketch, "E522", {"start": v(78.6, 79.16) * mm, "end": v(78.4, 79.05) * mm});
            skLineSegment(sketch, "E523", {"start": v(78.4, 79.05) * mm, "end": v(78.21, 78.94) * mm});
            skLineSegment(sketch, "E524", {"start": v(78.21, 78.94) * mm, "end": v(78.02, 78.83) * mm});
            skLineSegment(sketch, "E525", {"start": v(78.02, 78.83) * mm, "end": v(77.84, 78.72) * mm});
            skLineSegment(sketch, "E526", {"start": v(77.84, 78.72) * mm, "end": v(77.67, 78.6) * mm});
            skLineSegment(sketch, "E527", {"start": v(77.67, 78.6) * mm, "end": v(77.5, 78.5) * mm});
            skLineSegment(sketch, "E528", {"start": v(77.5, 78.5) * mm, "end": v(77.34, 78.4) * mm});
            skLineSegment(sketch, "E529", {"start": v(77.34, 78.4) * mm, "end": v(77.18, 78.3) * mm});
            skLineSegment(sketch, "E530", {"start": v(77.18, 78.3) * mm, "end": v(77.03, 78.2) * mm});
            skLineSegment(sketch, "E531", {"start": v(77.03, 78.2) * mm, "end": v(76.89, 78.1) * mm});
            skLineSegment(sketch, "E532", {"start": v(76.89, 78.1) * mm, "end": v(76.75, 78.01) * mm});
            skLineSegment(sketch, "E533", {"start": v(76.75, 78.01) * mm, "end": v(76.62, 77.92) * mm});
            skLineSegment(sketch, "E534", {"start": v(76.62, 77.92) * mm, "end": v(76.5, 77.83) * mm});
            skLineSegment(sketch, "E535", {"start": v(76.5, 77.83) * mm, "end": v(76.37, 77.75) * mm});
            skLineSegment(sketch, "E536", {"start": v(76.37, 77.75) * mm, "end": v(76.26, 77.67) * mm});
            skLineSegment(sketch, "E537", {"start": v(76.26, 77.67) * mm, "end": v(76.15, 77.59) * mm});
            skLineSegment(sketch, "E538", {"start": v(76.15, 77.59) * mm, "end": v(75.87, 77.5) * mm});
            skLineSegment(sketch, "E539", {"start": v(75.87, 77.5) * mm, "end": v(72.6, 80.55) * mm});
            skLineSegment(sketch, "E540", {"start": v(72.6, 80.55) * mm, "end": v(72.68, 80.84) * mm});
            skLineSegment(sketch, "E541", {"start": v(72.68, 80.84) * mm, "end": v(72.75, 80.95) * mm});
            skLineSegment(sketch, "E542", {"start": v(72.75, 80.95) * mm, "end": v(72.83, 81.07) * mm});
            skLineSegment(sketch, "E543", {"start": v(72.83, 81.07) * mm, "end": v(72.9, 81.2) * mm});
            skLineSegment(sketch, "E544", {"start": v(72.9, 81.2) * mm, "end": v(72.99, 81.33) * mm});
            skLineSegment(sketch, "E545", {"start": v(72.99, 81.33) * mm, "end": v(73.07, 81.46) * mm});
            skLineSegment(sketch, "E546", {"start": v(73.07, 81.46) * mm, "end": v(73.15, 81.6) * mm});
            skLineSegment(sketch, "E547", {"start": v(73.15, 81.6) * mm, "end": v(73.24, 81.76) * mm});
            skLineSegment(sketch, "E548", {"start": v(73.24, 81.76) * mm, "end": v(73.33, 81.91) * mm});
            skLineSegment(sketch, "E549", {"start": v(73.33, 81.91) * mm, "end": v(73.42, 82.08) * mm});
            skLineSegment(sketch, "E550", {"start": v(73.42, 82.08) * mm, "end": v(73.51, 82.24) * mm});
            skLineSegment(sketch, "E551", {"start": v(73.51, 82.24) * mm, "end": v(73.6, 82.42) * mm});
            skLineSegment(sketch, "E552", {"start": v(73.6, 82.42) * mm, "end": v(73.7, 82.6) * mm});
            skLineSegment(sketch, "E553", {"start": v(73.7, 82.6) * mm, "end": v(73.8, 82.79) * mm});
            skLineSegment(sketch, "E554", {"start": v(73.8, 82.79) * mm, "end": v(73.9, 82.98) * mm});
            skLineSegment(sketch, "E555", {"start": v(73.9, 82.98) * mm, "end": v(74, 83.18) * mm});
            skLineSegment(sketch, "E556", {"start": v(74, 83.18) * mm, "end": v(74.1, 83.4) * mm});
            skLineSegment(sketch, "E557", {"start": v(74.1, 83.4) * mm, "end": v(74.2, 83.6) * mm});
            skLineSegment(sketch, "E558", {"start": v(74.2, 83.6) * mm, "end": v(74.3, 83.83) * mm});
            skLineSegment(sketch, "E559", {"start": v(74.3, 83.83) * mm, "end": v(74.41, 84.05) * mm});
            skLineSegment(sketch, "E560", {"start": v(74.41, 84.05) * mm, "end": v(74.52, 84.29) * mm});
            skLineSegment(sketch, "E561", {"start": v(74.52, 84.29) * mm, "end": v(74.63, 84.53) * mm});
            skLineSegment(sketch, "E562", {"start": v(74.63, 84.53) * mm, "end": v(74.73, 84.78) * mm});
            skLineSegment(sketch, "E563", {"start": v(74.73, 84.78) * mm, "end": v(74.84, 85.03) * mm});
            skLineSegment(sketch, "E564", {"start": v(74.84, 85.03) * mm, "end": v(74.95, 85.3) * mm});
            skLineSegment(sketch, "E565", {"start": v(74.95, 85.3) * mm, "end": v(75.06, 85.56) * mm});
            skLineSegment(sketch, "E566", {"start": v(75.06, 85.56) * mm, "end": v(75.17, 85.83) * mm});
            skLineSegment(sketch, "E567", {"start": v(75.17, 85.83) * mm, "end": v(75.28, 86.12) * mm});
            skLineSegment(sketch, "E568", {"start": v(75.28, 86.12) * mm, "end": v(75.39, 86.4) * mm});
            skLineSegment(sketch, "E569", {"start": v(75.39, 86.4) * mm, "end": v(75.5, 86.7) * mm});
            skLineSegment(sketch, "E570", {"start": v(75.5, 86.7) * mm, "end": v(75.6, 87) * mm});
            skLineSegment(sketch, "E571", {"start": v(75.6, 87) * mm, "end": v(75.72, 87.31) * mm});
            skLineSegment(sketch, "E572", {"start": v(75.72, 87.31) * mm, "end": v(75.82, 87.63) * mm});
            skLineSegment(sketch, "E573", {"start": v(75.82, 87.63) * mm, "end": v(75.93, 87.95) * mm});
            skLineSegment(sketch, "E574", {"start": v(75.93, 87.95) * mm, "end": v(76.04, 88.28) * mm});
            skLineSegment(sketch, "E575", {"start": v(76.04, 88.28) * mm, "end": v(76.15, 88.62) * mm});
            skLineSegment(sketch, "E576", {"start": v(76.15, 88.62) * mm, "end": v(76.25, 88.96) * mm});
            skLineSegment(sketch, "E577", {"start": v(76.25, 88.96) * mm, "end": v(76.36, 89.31) * mm});
            skLineSegment(sketch, "E578", {"start": v(76.36, 89.31) * mm, "end": v(76.47, 89.67) * mm});
            skLineSegment(sketch, "E579", {"start": v(76.47, 89.67) * mm, "end": v(76.57, 90.04) * mm});
            skLineSegment(sketch, "E580", {"start": v(76.57, 90.04) * mm, "end": v(76.67, 90.4) * mm});
            skLineSegment(sketch, "E581", {"start": v(76.67, 90.4) * mm, "end": v(76.77, 90.79) * mm});
            skLineSegment(sketch, "E582", {"start": v(76.77, 90.79) * mm, "end": v(76.87, 91.17) * mm});
            skLineSegment(sketch, "E583", {"start": v(76.87, 91.17) * mm, "end": v(76.8, 91.37) * mm});
            skLineSegment(sketch, "E584", {"start": v(76.8, 91.37) * mm, "end": v(74.09, 93.59) * mm});
            skLineSegment(sketch, "E585", {"start": v(74.09, 93.59) * mm, "end": v(73.88, 93.61) * mm});
            skLineSegment(sketch, "E586", {"start": v(73.88, 93.61) * mm, "end": v(73.52, 93.44) * mm});
            skLineSegment(sketch, "E587", {"start": v(73.52, 93.44) * mm, "end": v(73.17, 93.26) * mm});
            skLineSegment(sketch, "E588", {"start": v(73.17, 93.26) * mm, "end": v(72.83, 93.09) * mm});
            skLineSegment(sketch, "E589", {"start": v(72.83, 93.09) * mm, "end": v(72.5, 92.91) * mm});
            skLineSegment(sketch, "E590", {"start": v(72.5, 92.91) * mm, "end": v(72.16, 92.74) * mm});
            skLineSegment(sketch, "E591", {"start": v(72.16, 92.74) * mm, "end": v(71.84, 92.56) * mm});
            skLineSegment(sketch, "E592", {"start": v(71.84, 92.56) * mm, "end": v(71.52, 92.39) * mm});
            skLineSegment(sketch, "E593", {"start": v(71.52, 92.39) * mm, "end": v(71.21, 92.21) * mm});
            skLineSegment(sketch, "E594", {"start": v(71.21, 92.21) * mm, "end": v(70.91, 92.04) * mm});
            skLineSegment(sketch, "E595", {"start": v(70.91, 92.04) * mm, "end": v(70.62, 91.87) * mm});
            skLineSegment(sketch, "E596", {"start": v(70.62, 91.87) * mm, "end": v(70.33, 91.7) * mm});
            skLineSegment(sketch, "E597", {"start": v(70.33, 91.7) * mm, "end": v(70.05, 91.53) * mm});
            skLineSegment(sketch, "E598", {"start": v(70.05, 91.53) * mm, "end": v(69.78, 91.36) * mm});
            skLineSegment(sketch, "E599", {"start": v(69.78, 91.36) * mm, "end": v(69.5, 91.2) * mm});
            skLineSegment(sketch, "E600", {"start": v(69.5, 91.2) * mm, "end": v(69.25, 91.03) * mm});
            skLineSegment(sketch, "E601", {"start": v(69.25, 91.03) * mm, "end": v(69, 90.87) * mm});
            skLineSegment(sketch, "E602", {"start": v(69, 90.87) * mm, "end": v(68.75, 90.7) * mm});
            skLineSegment(sketch, "E603", {"start": v(68.75, 90.7) * mm, "end": v(68.5, 90.54) * mm});
            skLineSegment(sketch, "E604", {"start": v(68.5, 90.54) * mm, "end": v(68.27, 90.38) * mm});
            skLineSegment(sketch, "E605", {"start": v(68.27, 90.38) * mm, "end": v(68.05, 90.23) * mm});
            skLineSegment(sketch, "E606", {"start": v(68.05, 90.23) * mm, "end": v(67.82, 90.07) * mm});
            skLineSegment(sketch, "E607", {"start": v(67.82, 90.07) * mm, "end": v(67.61, 89.92) * mm});
            skLineSegment(sketch, "E608", {"start": v(67.61, 89.92) * mm, "end": v(67.4, 89.77) * mm});
            skLineSegment(sketch, "E609", {"start": v(67.4, 89.77) * mm, "end": v(67.2, 89.62) * mm});
            skLineSegment(sketch, "E610", {"start": v(67.2, 89.62) * mm, "end": v(67, 89.47) * mm});
            skLineSegment(sketch, "E611", {"start": v(67, 89.47) * mm, "end": v(66.82, 89.33) * mm});
            skLineSegment(sketch, "E612", {"start": v(66.82, 89.33) * mm, "end": v(66.63, 89.19) * mm});
            skLineSegment(sketch, "E613", {"start": v(66.63, 89.19) * mm, "end": v(66.46, 89.05) * mm});
            skLineSegment(sketch, "E614", {"start": v(66.46, 89.05) * mm, "end": v(66.29, 88.91) * mm});
            skLineSegment(sketch, "E615", {"start": v(66.29, 88.91) * mm, "end": v(66.12, 88.78) * mm});
            skLineSegment(sketch, "E616", {"start": v(66.12, 88.78) * mm, "end": v(65.96, 88.65) * mm});
            skLineSegment(sketch, "E617", {"start": v(65.96, 88.65) * mm, "end": v(65.81, 88.52) * mm});
            skLineSegment(sketch, "E618", {"start": v(65.81, 88.52) * mm, "end": v(65.67, 88.4) * mm});
            skLineSegment(sketch, "E619", {"start": v(65.67, 88.4) * mm, "end": v(65.53, 88.27) * mm});
            skLineSegment(sketch, "E620", {"start": v(65.53, 88.27) * mm, "end": v(65.4, 88.16) * mm});
            skLineSegment(sketch, "E621", {"start": v(65.4, 88.16) * mm, "end": v(65.26, 88.04) * mm});
            skLineSegment(sketch, "E622", {"start": v(65.26, 88.04) * mm, "end": v(65.14, 87.93) * mm});
            skLineSegment(sketch, "E623", {"start": v(65.14, 87.93) * mm, "end": v(65.02, 87.82) * mm});
            skLineSegment(sketch, "E624", {"start": v(65.02, 87.82) * mm, "end": v(64.9, 87.72) * mm});
            skLineSegment(sketch, "E625", {"start": v(64.9, 87.72) * mm, "end": v(64.8, 87.61) * mm});
            skLineSegment(sketch, "E626", {"start": v(64.8, 87.61) * mm, "end": v(64.7, 87.52) * mm});
            skLineSegment(sketch, "E627", {"start": v(64.7, 87.52) * mm, "end": v(64.6, 87.42) * mm});
            skLineSegment(sketch, "E628", {"start": v(64.6, 87.42) * mm, "end": v(64.34, 87.3) * mm});
            skLineSegment(sketch, "E629", {"start": v(64.34, 87.3) * mm, "end": v(60.68, 89.87) * mm});
            skLineSegment(sketch, "E630", {"start": v(60.68, 89.87) * mm, "end": v(60.72, 90.16) * mm});
            skLineSegment(sketch, "E631", {"start": v(60.72, 90.16) * mm, "end": v(60.77, 90.29) * mm});
            skLineSegment(sketch, "E632", {"start": v(60.77, 90.29) * mm, "end": v(60.83, 90.41) * mm});
            skLineSegment(sketch, "E633", {"start": v(60.83, 90.41) * mm, "end": v(60.9, 90.55) * mm});
            skLineSegment(sketch, "E634", {"start": v(60.9, 90.55) * mm, "end": v(60.95, 90.69) * mm});
            skLineSegment(sketch, "E635", {"start": v(60.95, 90.69) * mm, "end": v(61.01, 90.84) * mm});
            skLineSegment(sketch, "E636", {"start": v(61.01, 90.84) * mm, "end": v(61.08, 90.99) * mm});
            skLineSegment(sketch, "E637", {"start": v(61.08, 90.99) * mm, "end": v(61.14, 91.15) * mm});
            skLineSegment(sketch, "E638", {"start": v(61.14, 91.15) * mm, "end": v(61.2, 91.32) * mm});
            skLineSegment(sketch, "E639", {"start": v(61.2, 91.32) * mm, "end": v(61.28, 91.49) * mm});
            skLineSegment(sketch, "E640", {"start": v(61.28, 91.49) * mm, "end": v(61.34, 91.67) * mm});
            skLineSegment(sketch, "E641", {"start": v(61.34, 91.67) * mm, "end": v(61.41, 91.86) * mm});
            skLineSegment(sketch, "E642", {"start": v(61.41, 91.86) * mm, "end": v(61.48, 92.05) * mm});
            skLineSegment(sketch, "E643", {"start": v(61.48, 92.05) * mm, "end": v(61.55, 92.25) * mm});
            skLineSegment(sketch, "E644", {"start": v(61.55, 92.25) * mm, "end": v(61.63, 92.45) * mm});
            skLineSegment(sketch, "E645", {"start": v(61.63, 92.45) * mm, "end": v(61.7, 92.67) * mm});
            skLineSegment(sketch, "E646", {"start": v(61.7, 92.67) * mm, "end": v(61.77, 92.89) * mm});
            skLineSegment(sketch, "E647", {"start": v(61.77, 92.89) * mm, "end": v(61.84, 93.11) * mm});
            skLineSegment(sketch, "E648", {"start": v(61.84, 93.11) * mm, "end": v(61.91, 93.35) * mm});
            skLineSegment(sketch, "E649", {"start": v(61.91, 93.35) * mm, "end": v(61.99, 93.59) * mm});
            skLineSegment(sketch, "E650", {"start": v(61.99, 93.59) * mm, "end": v(62.06, 93.83) * mm});
            skLineSegment(sketch, "E651", {"start": v(62.06, 93.83) * mm, "end": v(62.13, 94.09) * mm});
            skLineSegment(sketch, "E652", {"start": v(62.13, 94.09) * mm, "end": v(62.2, 94.35) * mm});
            skLineSegment(sketch, "E653", {"start": v(62.2, 94.35) * mm, "end": v(62.27, 94.61) * mm});
            skLineSegment(sketch, "E654", {"start": v(62.27, 94.61) * mm, "end": v(62.34, 94.89) * mm});
            skLineSegment(sketch, "E655", {"start": v(62.34, 94.89) * mm, "end": v(62.41, 95.17) * mm});
            skLineSegment(sketch, "E656", {"start": v(62.41, 95.17) * mm, "end": v(62.48, 95.45) * mm});
            skLineSegment(sketch, "E657", {"start": v(62.48, 95.45) * mm, "end": v(62.55, 95.75) * mm});
            skLineSegment(sketch, "E658", {"start": v(62.55, 95.75) * mm, "end": v(62.62, 96.05) * mm});
            skLineSegment(sketch, "E659", {"start": v(62.62, 96.05) * mm, "end": v(62.69, 96.36) * mm});
            skLineSegment(sketch, "E660", {"start": v(62.69, 96.36) * mm, "end": v(62.76, 96.67) * mm});
            skLineSegment(sketch, "E661", {"start": v(62.76, 96.67) * mm, "end": v(62.82, 97) * mm});
            skLineSegment(sketch, "E662", {"start": v(62.82, 97) * mm, "end": v(62.88, 97.32) * mm});
            skLineSegment(sketch, "E663", {"start": v(62.88, 97.32) * mm, "end": v(62.95, 97.66) * mm});
            skLineSegment(sketch, "E664", {"start": v(62.95, 97.66) * mm, "end": v(63, 98) * mm});
            skLineSegment(sketch, "E665", {"start": v(63, 98) * mm, "end": v(63.07, 98.35) * mm});
            skLineSegment(sketch, "E666", {"start": v(63.07, 98.35) * mm, "end": v(63.12, 98.7) * mm});
            skLineSegment(sketch, "E667", {"start": v(63.12, 98.7) * mm, "end": v(63.18, 99.07) * mm});
            skLineSegment(sketch, "E668", {"start": v(63.18, 99.07) * mm, "end": v(63.24, 99.44) * mm});
            skLineSegment(sketch, "E669", {"start": v(63.24, 99.44) * mm, "end": v(63.29, 99.81) * mm});
            skLineSegment(sketch, "E670", {"start": v(63.29, 99.81) * mm, "end": v(63.34, 100.2) * mm});
            skLineSegment(sketch, "E671", {"start": v(63.34, 100.2) * mm, "end": v(63.38, 100.58) * mm});
            skLineSegment(sketch, "E672", {"start": v(63.38, 100.58) * mm, "end": v(63.43, 100.98) * mm});
            skLineSegment(sketch, "E673", {"start": v(63.43, 100.98) * mm, "end": v(63.34, 101.17) * mm});
            skLineSegment(sketch, "E674", {"start": v(63.34, 101.17) * mm, "end": v(60.33, 102.98) * mm});
            skLineSegment(sketch, "E675", {"start": v(60.33, 102.98) * mm, "end": v(60.13, 102.98) * mm});
            skLineSegment(sketch, "E676", {"start": v(60.13, 102.98) * mm, "end": v(59.8, 102.76) * mm});
            skLineSegment(sketch, "E677", {"start": v(59.8, 102.76) * mm, "end": v(59.47, 102.53) * mm});
            skLineSegment(sketch, "E678", {"start": v(59.47, 102.53) * mm, "end": v(59.16, 102.31) * mm});
            skLineSegment(sketch, "E679", {"start": v(59.16, 102.31) * mm, "end": v(58.85, 102.09) * mm});
            skLineSegment(sketch, "E680", {"start": v(58.85, 102.09) * mm, "end": v(58.55, 101.87) * mm});
            skLineSegment(sketch, "E681", {"start": v(58.55, 101.87) * mm, "end": v(58.25, 101.65) * mm});
            skLineSegment(sketch, "E682", {"start": v(58.25, 101.65) * mm, "end": v(57.96, 101.44) * mm});
            skLineSegment(sketch, "E683", {"start": v(57.96, 101.44) * mm, "end": v(57.68, 101.22) * mm});
            skLineSegment(sketch, "E684", {"start": v(57.68, 101.22) * mm, "end": v(57.4, 101) * mm});
            skLineSegment(sketch, "E685", {"start": v(57.4, 101) * mm, "end": v(57.14, 100.8) * mm});
            skLineSegment(sketch, "E686", {"start": v(57.14, 100.8) * mm, "end": v(56.88, 100.59) * mm});
            skLineSegment(sketch, "E687", {"start": v(56.88, 100.59) * mm, "end": v(56.62, 100.38) * mm});
            skLineSegment(sketch, "E688", {"start": v(56.62, 100.38) * mm, "end": v(56.37, 100.18) * mm});
            skLineSegment(sketch, "E689", {"start": v(56.37, 100.18) * mm, "end": v(56.13, 99.98) * mm});
            skLineSegment(sketch, "E690", {"start": v(56.13, 99.98) * mm, "end": v(55.9, 99.78) * mm});
            skLineSegment(sketch, "E691", {"start": v(55.9, 99.78) * mm, "end": v(55.67, 99.58) * mm});
            skLineSegment(sketch, "E692", {"start": v(55.67, 99.58) * mm, "end": v(55.45, 99.38) * mm});
            skLineSegment(sketch, "E693", {"start": v(55.45, 99.38) * mm, "end": v(55.23, 99.2) * mm});
            skLineSegment(sketch, "E694", {"start": v(55.23, 99.2) * mm, "end": v(55.02, 99) * mm});
            skLineSegment(sketch, "E695", {"start": v(55.02, 99) * mm, "end": v(54.82, 98.81) * mm});
            skLineSegment(sketch, "E696", {"start": v(54.82, 98.81) * mm, "end": v(54.62, 98.63) * mm});
            skLineSegment(sketch, "E697", {"start": v(54.62, 98.63) * mm, "end": v(54.43, 98.45) * mm});
            skLineSegment(sketch, "E698", {"start": v(54.43, 98.45) * mm, "end": v(54.25, 98.27) * mm});
            skLineSegment(sketch, "E699", {"start": v(54.25, 98.27) * mm, "end": v(54.07, 98.1) * mm});
            skLineSegment(sketch, "E700", {"start": v(54.07, 98.1) * mm, "end": v(53.9, 97.92) * mm});
            skLineSegment(sketch, "E701", {"start": v(53.9, 97.92) * mm, "end": v(53.73, 97.75) * mm});
            skLineSegment(sketch, "E702", {"start": v(53.73, 97.75) * mm, "end": v(53.57, 97.59) * mm});
            skLineSegment(sketch, "E703", {"start": v(53.57, 97.59) * mm, "end": v(53.41, 97.43) * mm});
            skLineSegment(sketch, "E704", {"start": v(53.41, 97.43) * mm, "end": v(53.26, 97.27) * mm});
            skLineSegment(sketch, "E705", {"start": v(53.26, 97.27) * mm, "end": v(53.12, 97.11) * mm});
            skLineSegment(sketch, "E706", {"start": v(53.12, 97.11) * mm, "end": v(52.98, 96.96) * mm});
            skLineSegment(sketch, "E707", {"start": v(52.98, 96.96) * mm, "end": v(52.85, 96.81) * mm});
            skLineSegment(sketch, "E708", {"start": v(52.85, 96.81) * mm, "end": v(52.72, 96.67) * mm});
            skLineSegment(sketch, "E709", {"start": v(52.72, 96.67) * mm, "end": v(52.6, 96.53) * mm});
            skLineSegment(sketch, "E710", {"start": v(52.6, 96.53) * mm, "end": v(52.48, 96.4) * mm});
            skLineSegment(sketch, "E711", {"start": v(52.48, 96.4) * mm, "end": v(52.37, 96.26) * mm});
            skLineSegment(sketch, "E712", {"start": v(52.37, 96.26) * mm, "end": v(52.26, 96.13) * mm});
            skLineSegment(sketch, "E713", {"start": v(52.26, 96.13) * mm, "end": v(52.16, 96.01) * mm});
            skLineSegment(sketch, "E714", {"start": v(52.16, 96.01) * mm, "end": v(52.06, 95.9) * mm});
            skLineSegment(sketch, "E715", {"start": v(52.06, 95.9) * mm, "end": v(51.97, 95.78) * mm});
            skLineSegment(sketch, "E716", {"start": v(51.97, 95.78) * mm, "end": v(51.88, 95.66) * mm});
            skLineSegment(sketch, "E717", {"start": v(51.88, 95.66) * mm, "end": v(51.8, 95.56) * mm});
            skLineSegment(sketch, "E718", {"start": v(51.8, 95.56) * mm, "end": v(51.56, 95.4) * mm});
            skLineSegment(sketch, "E719", {"start": v(51.56, 95.4) * mm, "end": v(47.58, 97.43) * mm});
            skLineSegment(sketch, "E720", {"start": v(47.58, 97.43) * mm, "end": v(47.57, 97.73) * mm});
            skLineSegment(sketch, "E721", {"start": v(47.57, 97.73) * mm, "end": v(47.6, 97.86) * mm});
            skLineSegment(sketch, "E722", {"start": v(47.6, 97.86) * mm, "end": v(47.65, 98) * mm});
            skLineSegment(sketch, "E723", {"start": v(47.65, 98) * mm, "end": v(47.69, 98.14) * mm});
            skLineSegment(sketch, "E724", {"start": v(47.69, 98.14) * mm, "end": v(47.73, 98.28) * mm});
            skLineSegment(sketch, "E725", {"start": v(47.73, 98.28) * mm, "end": v(47.77, 98.44) * mm});
            skLineSegment(sketch, "E726", {"start": v(47.77, 98.44) * mm, "end": v(47.81, 98.6) * mm});
            skLineSegment(sketch, "E727", {"start": v(47.81, 98.6) * mm, "end": v(47.86, 98.77) * mm});
            skLineSegment(sketch, "E728", {"start": v(47.86, 98.77) * mm, "end": v(47.9, 98.94) * mm});
            skLineSegment(sketch, "E729", {"start": v(47.9, 98.94) * mm, "end": v(47.94, 99.12) * mm});
            skLineSegment(sketch, "E730", {"start": v(47.94, 99.12) * mm, "end": v(47.98, 99.3) * mm});
            skLineSegment(sketch, "E731", {"start": v(47.98, 99.3) * mm, "end": v(48.03, 99.5) * mm});
            skLineSegment(sketch, "E732", {"start": v(48.03, 99.5) * mm, "end": v(48.07, 99.7) * mm});
            skLineSegment(sketch, "E733", {"start": v(48.07, 99.7) * mm, "end": v(48.11, 99.91) * mm});
            skLineSegment(sketch, "E734", {"start": v(48.11, 99.91) * mm, "end": v(48.15, 100.13) * mm});
            skLineSegment(sketch, "E735", {"start": v(48.15, 100.13) * mm, "end": v(48.2, 100.35) * mm});
            skLineSegment(sketch, "E736", {"start": v(48.2, 100.35) * mm, "end": v(48.23, 100.57) * mm});
            skLineSegment(sketch, "E737", {"start": v(48.23, 100.57) * mm, "end": v(48.27, 100.8) * mm});
            skLineSegment(sketch, "E738", {"start": v(48.27, 100.8) * mm, "end": v(48.31, 101.05) * mm});
            skLineSegment(sketch, "E739", {"start": v(48.31, 101.05) * mm, "end": v(48.35, 101.3) * mm});
            skLineSegment(sketch, "E740", {"start": v(48.35, 101.3) * mm, "end": v(48.39, 101.55) * mm});
            skLineSegment(sketch, "E741", {"start": v(48.39, 101.55) * mm, "end": v(48.42, 101.81) * mm});
            skLineSegment(sketch, "E742", {"start": v(48.42, 101.81) * mm, "end": v(48.46, 102.08) * mm});
            skLineSegment(sketch, "E743", {"start": v(48.46, 102.08) * mm, "end": v(48.5, 102.35) * mm});
            skLineSegment(sketch, "E744", {"start": v(48.5, 102.35) * mm, "end": v(48.52, 102.64) * mm});
            skLineSegment(sketch, "E745", {"start": v(48.52, 102.64) * mm, "end": v(48.56, 102.92) * mm});
            skLineSegment(sketch, "E746", {"start": v(48.56, 102.92) * mm, "end": v(48.58, 103.22) * mm});
            skLineSegment(sketch, "E747", {"start": v(48.58, 103.22) * mm, "end": v(48.61, 103.52) * mm});
            skLineSegment(sketch, "E748", {"start": v(48.61, 103.52) * mm, "end": v(48.64, 103.83) * mm});
            skLineSegment(sketch, "E749", {"start": v(48.64, 103.83) * mm, "end": v(48.66, 104.14) * mm});
            skLineSegment(sketch, "E750", {"start": v(48.66, 104.14) * mm, "end": v(48.68, 104.46) * mm});
            skLineSegment(sketch, "E751", {"start": v(48.68, 104.46) * mm, "end": v(48.7, 104.79) * mm});
            skLineSegment(sketch, "E752", {"start": v(48.7, 104.79) * mm, "end": v(48.72, 105.12) * mm});
            skLineSegment(sketch, "E753", {"start": v(48.72, 105.12) * mm, "end": v(48.74, 105.46) * mm});
            skLineSegment(sketch, "E754", {"start": v(48.74, 105.46) * mm, "end": v(48.75, 105.8) * mm});
            skLineSegment(sketch, "E755", {"start": v(48.75, 105.8) * mm, "end": v(48.76, 106.16) * mm});
            skLineSegment(sketch, "E756", {"start": v(48.76, 106.16) * mm, "end": v(48.77, 106.52) * mm});
            skLineSegment(sketch, "E757", {"start": v(48.77, 106.52) * mm, "end": v(48.77, 106.89) * mm});
            skLineSegment(sketch, "E758", {"start": v(48.77, 106.89) * mm, "end": v(48.77, 107.26) * mm});
            skLineSegment(sketch, "E759", {"start": v(48.77, 107.26) * mm, "end": v(48.77, 107.64) * mm});
            skLineSegment(sketch, "E760", {"start": v(48.77, 107.64) * mm, "end": v(48.77, 108.03) * mm});
            skLineSegment(sketch, "E761", {"start": v(48.77, 108.03) * mm, "end": v(48.76, 108.42) * mm});
            skLineSegment(sketch, "E762", {"start": v(48.76, 108.42) * mm, "end": v(48.75, 108.82) * mm});
            skLineSegment(sketch, "E763", {"start": v(48.75, 108.82) * mm, "end": v(48.63, 109) * mm});
            skLineSegment(sketch, "E764", {"start": v(48.63, 109) * mm, "end": v(45.4, 110.37) * mm});
            skLineSegment(sketch, "E765", {"start": v(45.4, 110.37) * mm, "end": v(45.2, 110.34) * mm});
            skLineSegment(sketch, "E766", {"start": v(45.2, 110.34) * mm, "end": v(44.9, 110.07) * mm});
            skLineSegment(sketch, "E767", {"start": v(44.9, 110.07) * mm, "end": v(44.62, 109.8) * mm});
            skLineSegment(sketch, "E768", {"start": v(44.62, 109.8) * mm, "end": v(44.34, 109.54) * mm});
            skLineSegment(sketch, "E769", {"start": v(44.34, 109.54) * mm, "end": v(44.06, 109.28) * mm});
            skLineSegment(sketch, "E770", {"start": v(44.06, 109.28) * mm, "end": v(43.8, 109.02) * mm});
            skLineSegment(sketch, "E771", {"start": v(43.8, 109.02) * mm, "end": v(43.53, 108.77) * mm});
            skLineSegment(sketch, "E772", {"start": v(43.53, 108.77) * mm, "end": v(43.28, 108.51) * mm});
            skLineSegment(sketch, "E773", {"start": v(43.28, 108.51) * mm, "end": v(43.03, 108.26) * mm});
            skLineSegment(sketch, "E774", {"start": v(43.03, 108.26) * mm, "end": v(42.78, 108.01) * mm});
            skLineSegment(sketch, "E775", {"start": v(42.78, 108.01) * mm, "end": v(42.55, 107.76) * mm});
            skLineSegment(sketch, "E776", {"start": v(42.55, 107.76) * mm, "end": v(42.32, 107.52) * mm});
            skLineSegment(sketch, "E777", {"start": v(42.32, 107.52) * mm, "end": v(42.1, 107.28) * mm});
            skLineSegment(sketch, "E778", {"start": v(42.1, 107.28) * mm, "end": v(41.88, 107.04) * mm});
            skLineSegment(sketch, "E779", {"start": v(41.88, 107.04) * mm, "end": v(41.67, 106.81) * mm});
            skLineSegment(sketch, "E780", {"start": v(41.67, 106.81) * mm, "end": v(41.46, 106.58) * mm});
            skLineSegment(sketch, "E781", {"start": v(41.46, 106.58) * mm, "end": v(41.26, 106.35) * mm});
            skLineSegment(sketch, "E782", {"start": v(41.26, 106.35) * mm, "end": v(41.07, 106.13) * mm});
            skLineSegment(sketch, "E783", {"start": v(41.07, 106.13) * mm, "end": v(40.88, 105.9) * mm});
            skLineSegment(sketch, "E784", {"start": v(40.88, 105.9) * mm, "end": v(40.7, 105.69) * mm});
            skLineSegment(sketch, "E785", {"start": v(40.7, 105.69) * mm, "end": v(40.53, 105.48) * mm});
            skLineSegment(sketch, "E786", {"start": v(40.53, 105.48) * mm, "end": v(40.36, 105.27) * mm});
            skLineSegment(sketch, "E787", {"start": v(40.36, 105.27) * mm, "end": v(40.2, 105.06) * mm});
            skLineSegment(sketch, "E788", {"start": v(40.2, 105.06) * mm, "end": v(40.04, 104.86) * mm});
            skLineSegment(sketch, "E789", {"start": v(40.04, 104.86) * mm, "end": v(39.88, 104.66) * mm});
            skLineSegment(sketch, "E790", {"start": v(39.88, 104.66) * mm, "end": v(39.74, 104.46) * mm});
            skLineSegment(sketch, "E791", {"start": v(39.74, 104.46) * mm, "end": v(39.6, 104.27) * mm});
            skLineSegment(sketch, "E792", {"start": v(39.6, 104.27) * mm, "end": v(39.46, 104.09) * mm});
            skLineSegment(sketch, "E793", {"start": v(39.46, 104.09) * mm, "end": v(39.33, 103.9) * mm});
            skLineSegment(sketch, "E794", {"start": v(39.33, 103.9) * mm, "end": v(39.2, 103.73) * mm});
            skLineSegment(sketch, "E795", {"start": v(39.2, 103.73) * mm, "end": v(39.08, 103.55) * mm});
            skLineSegment(sketch, "E796", {"start": v(39.08, 103.55) * mm, "end": v(38.96, 103.39) * mm});
            skLineSegment(sketch, "E797", {"start": v(38.96, 103.39) * mm, "end": v(38.85, 103.22) * mm});
            skLineSegment(sketch, "E798", {"start": v(38.85, 103.22) * mm, "end": v(38.74, 103.06) * mm});
            skLineSegment(sketch, "E799", {"start": v(38.74, 103.06) * mm, "end": v(38.64, 102.9) * mm});
            skLineSegment(sketch, "E800", {"start": v(38.64, 102.9) * mm, "end": v(38.55, 102.75) * mm});
            skLineSegment(sketch, "E801", {"start": v(38.55, 102.75) * mm, "end": v(38.45, 102.6) * mm});
            skLineSegment(sketch, "E802", {"start": v(38.45, 102.6) * mm, "end": v(38.37, 102.47) * mm});
            skLineSegment(sketch, "E803", {"start": v(38.37, 102.47) * mm, "end": v(38.28, 102.33) * mm});
            skLineSegment(sketch, "E804", {"start": v(38.28, 102.33) * mm, "end": v(38.2, 102.2) * mm});
            skLineSegment(sketch, "E805", {"start": v(38.2, 102.2) * mm, "end": v(38.13, 102.07) * mm});
            skLineSegment(sketch, "E806", {"start": v(38.13, 102.07) * mm, "end": v(38.06, 101.95) * mm});
            skLineSegment(sketch, "E807", {"start": v(38.06, 101.95) * mm, "end": v(38, 101.83) * mm});
            skLineSegment(sketch, "E808", {"start": v(38, 101.83) * mm, "end": v(37.77, 101.63) * mm});
            skLineSegment(sketch, "E809", {"start": v(37.77, 101.63) * mm, "end": v(33.55, 103.1) * mm});
            skLineSegment(sketch, "E810", {"start": v(33.55, 103.1) * mm, "end": v(33.5, 103.4) * mm});
            skLineSegment(sketch, "E811", {"start": v(33.5, 103.4) * mm, "end": v(33.52, 103.53) * mm});
            skLineSegment(sketch, "E812", {"start": v(33.52, 103.53) * mm, "end": v(33.54, 103.67) * mm});
            skLineSegment(sketch, "E813", {"start": v(33.54, 103.67) * mm, "end": v(33.56, 103.81) * mm});
            skLineSegment(sketch, "E814", {"start": v(33.56, 103.81) * mm, "end": v(33.58, 103.97) * mm});
            skLineSegment(sketch, "E815", {"start": v(33.58, 103.97) * mm, "end": v(33.6, 104.12) * mm});
            skLineSegment(sketch, "E816", {"start": v(33.6, 104.12) * mm, "end": v(33.62, 104.29) * mm});
            skLineSegment(sketch, "E817", {"start": v(33.62, 104.29) * mm, "end": v(33.64, 104.46) * mm});
            skLineSegment(sketch, "E818", {"start": v(33.64, 104.46) * mm, "end": v(33.66, 104.64) * mm});
            skLineSegment(sketch, "E819", {"start": v(33.66, 104.64) * mm, "end": v(33.67, 104.82) * mm});
            skLineSegment(sketch, "E820", {"start": v(33.67, 104.82) * mm, "end": v(33.69, 105.02) * mm});
            skLineSegment(sketch, "E821", {"start": v(33.69, 105.02) * mm, "end": v(33.7, 105.21) * mm});
            skLineSegment(sketch, "E822", {"start": v(33.7, 105.21) * mm, "end": v(33.72, 105.42) * mm});
            skLineSegment(sketch, "E823", {"start": v(33.72, 105.42) * mm, "end": v(33.73, 105.63) * mm});
            skLineSegment(sketch, "E824", {"start": v(33.73, 105.63) * mm, "end": v(33.74, 105.85) * mm});
            skLineSegment(sketch, "E825", {"start": v(33.74, 105.85) * mm, "end": v(33.75, 106.07) * mm});
            skLineSegment(sketch, "E826", {"start": v(33.75, 106.07) * mm, "end": v(33.76, 106.3) * mm});
            skLineSegment(sketch, "E827", {"start": v(33.76, 106.3) * mm, "end": v(33.77, 106.54) * mm});
            skLineSegment(sketch, "E828", {"start": v(33.77, 106.54) * mm, "end": v(33.77, 106.78) * mm});
            skLineSegment(sketch, "E829", {"start": v(33.77, 106.78) * mm, "end": v(33.78, 107.04) * mm});
            skLineSegment(sketch, "E830", {"start": v(33.78, 107.04) * mm, "end": v(33.78, 107.3) * mm});
            skLineSegment(sketch, "E831", {"start": v(33.78, 107.3) * mm, "end": v(33.78, 107.55) * mm});
            skLineSegment(sketch, "E832", {"start": v(33.78, 107.55) * mm, "end": v(33.77, 107.82) * mm});
            skLineSegment(sketch, "E833", {"start": v(33.77, 107.82) * mm, "end": v(33.77, 108.1) * mm});
            skLineSegment(sketch, "E834", {"start": v(33.77, 108.1) * mm, "end": v(33.76, 108.38) * mm});
            skLineSegment(sketch, "E835", {"start": v(33.76, 108.38) * mm, "end": v(33.75, 108.67) * mm});
            skLineSegment(sketch, "E836", {"start": v(33.75, 108.67) * mm, "end": v(33.74, 108.97) * mm});
            skLineSegment(sketch, "E837", {"start": v(33.74, 108.97) * mm, "end": v(33.73, 109.27) * mm});
            skLineSegment(sketch, "E838", {"start": v(33.73, 109.27) * mm, "end": v(33.7, 109.58) * mm});
            skLineSegment(sketch, "E839", {"start": v(33.7, 109.58) * mm, "end": v(33.69, 109.9) * mm});
            skLineSegment(sketch, "E840", {"start": v(33.69, 109.9) * mm, "end": v(33.67, 110.21) * mm});
            skLineSegment(sketch, "E841", {"start": v(33.67, 110.21) * mm, "end": v(33.64, 110.54) * mm});
            skLineSegment(sketch, "E842", {"start": v(33.64, 110.54) * mm, "end": v(33.61, 110.87) * mm});
            skLineSegment(sketch, "E843", {"start": v(33.61, 110.87) * mm, "end": v(33.58, 111.21) * mm});
            skLineSegment(sketch, "E844", {"start": v(33.58, 111.21) * mm, "end": v(33.54, 111.56) * mm});
            skLineSegment(sketch, "E845", {"start": v(33.54, 111.56) * mm, "end": v(33.5, 111.91) * mm});
            skLineSegment(sketch, "E846", {"start": v(33.5, 111.91) * mm, "end": v(33.46, 112.27) * mm});
            skLineSegment(sketch, "E847", {"start": v(33.46, 112.27) * mm, "end": v(33.41, 112.63) * mm});
            skLineSegment(sketch, "E848", {"start": v(33.41, 112.63) * mm, "end": v(33.36, 113) * mm});
            skLineSegment(sketch, "E849", {"start": v(33.36, 113) * mm, "end": v(33.31, 113.38) * mm});
            skLineSegment(sketch, "E850", {"start": v(33.31, 113.38) * mm, "end": v(33.25, 113.76) * mm});
            skLineSegment(sketch, "E851", {"start": v(33.25, 113.76) * mm, "end": v(33.2, 114.15) * mm});
            skLineSegment(sketch, "E852", {"start": v(33.2, 114.15) * mm, "end": v(33.13, 114.54) * mm});
            skLineSegment(sketch, "E853", {"start": v(33.13, 114.54) * mm, "end": v(32.99, 114.7) * mm});
            skLineSegment(sketch, "E854", {"start": v(32.99, 114.7) * mm, "end": v(29.6, 115.61) * mm});
            skLineSegment(sketch, "E855", {"start": v(29.6, 115.61) * mm, "end": v(29.4, 115.55) * mm});
            skLineSegment(sketch, "E856", {"start": v(29.4, 115.55) * mm, "end": v(29.14, 115.25) * mm});
            skLineSegment(sketch, "E857", {"start": v(29.14, 115.25) * mm, "end": v(28.9, 114.94) * mm});
            skLineSegment(sketch, "E858", {"start": v(28.9, 114.94) * mm, "end": v(28.65, 114.64) * mm});
            skLineSegment(sketch, "E859", {"start": v(28.65, 114.64) * mm, "end": v(28.42, 114.34) * mm});
            skLineSegment(sketch, "E860", {"start": v(28.42, 114.34) * mm, "end": v(28.19, 114.05) * mm});
            skLineSegment(sketch, "E861", {"start": v(28.19, 114.05) * mm, "end": v(27.96, 113.76) * mm});
            skLineSegment(sketch, "E862", {"start": v(27.96, 113.76) * mm, "end": v(27.75, 113.47) * mm});
            skLineSegment(sketch, "E863", {"start": v(27.75, 113.47) * mm, "end": v(27.53, 113.19) * mm});
            skLineSegment(sketch, "E864", {"start": v(27.53, 113.19) * mm, "end": v(27.33, 112.9) * mm});
            skLineSegment(sketch, "E865", {"start": v(27.33, 112.9) * mm, "end": v(27.13, 112.63) * mm});
            skLineSegment(sketch, "E866", {"start": v(27.13, 112.63) * mm, "end": v(26.94, 112.36) * mm});
            skLineSegment(sketch, "E867", {"start": v(26.94, 112.36) * mm, "end": v(26.75, 112.1) * mm});
            skLineSegment(sketch, "E868", {"start": v(26.75, 112.1) * mm, "end": v(26.57, 111.83) * mm});
            skLineSegment(sketch, "E869", {"start": v(26.57, 111.83) * mm, "end": v(26.39, 111.56) * mm});
            skLineSegment(sketch, "E870", {"start": v(26.39, 111.56) * mm, "end": v(26.22, 111.3) * mm});
            skLineSegment(sketch, "E871", {"start": v(26.22, 111.3) * mm, "end": v(26.05, 111.05) * mm});
            skLineSegment(sketch, "E872", {"start": v(26.05, 111.05) * mm, "end": v(25.9, 110.8) * mm});
            skLineSegment(sketch, "E873", {"start": v(25.9, 110.8) * mm, "end": v(25.74, 110.56) * mm});
            skLineSegment(sketch, "E874", {"start": v(25.74, 110.56) * mm, "end": v(25.6, 110.32) * mm});
            skLineSegment(sketch, "E875", {"start": v(25.6, 110.32) * mm, "end": v(25.45, 110.08) * mm});
            skLineSegment(sketch, "E876", {"start": v(25.45, 110.08) * mm, "end": v(25.3, 109.85) * mm});
            skLineSegment(sketch, "E877", {"start": v(25.3, 109.85) * mm, "end": v(25.17, 109.63) * mm});
            skLineSegment(sketch, "E878", {"start": v(25.17, 109.63) * mm, "end": v(25.05, 109.4) * mm});
            skLineSegment(sketch, "E879", {"start": v(25.05, 109.4) * mm, "end": v(24.92, 109.19) * mm});
            skLineSegment(sketch, "E880", {"start": v(24.92, 109.19) * mm, "end": v(24.8, 108.97) * mm});
            skLineSegment(sketch, "E881", {"start": v(24.8, 108.97) * mm, "end": v(24.69, 108.76) * mm});
            skLineSegment(sketch, "E882", {"start": v(24.69, 108.76) * mm, "end": v(24.58, 108.56) * mm});
            skLineSegment(sketch, "E883", {"start": v(24.58, 108.56) * mm, "end": v(24.48, 108.36) * mm});
            skLineSegment(sketch, "E884", {"start": v(24.48, 108.36) * mm, "end": v(24.38, 108.17) * mm});
            skLineSegment(sketch, "E885", {"start": v(24.38, 108.17) * mm, "end": v(24.28, 107.98) * mm});
            skLineSegment(sketch, "E886", {"start": v(24.28, 107.98) * mm, "end": v(24.19, 107.8) * mm});
            skLineSegment(sketch, "E887", {"start": v(24.19, 107.8) * mm, "end": v(24.1, 107.62) * mm});
            skLineSegment(sketch, "E888", {"start": v(24.1, 107.62) * mm, "end": v(24.02, 107.44) * mm});
            skLineSegment(sketch, "E889", {"start": v(24.02, 107.44) * mm, "end": v(23.94, 107.28) * mm});
            skLineSegment(sketch, "E890", {"start": v(23.94, 107.28) * mm, "end": v(23.86, 107.11) * mm});
            skLineSegment(sketch, "E891", {"start": v(23.86, 107.11) * mm, "end": v(23.8, 106.96) * mm});
            skLineSegment(sketch, "E892", {"start": v(23.8, 106.96) * mm, "end": v(23.73, 106.8) * mm});
            skLineSegment(sketch, "E893", {"start": v(23.73, 106.8) * mm, "end": v(23.66, 106.66) * mm});
            skLineSegment(sketch, "E894", {"start": v(23.66, 106.66) * mm, "end": v(23.6, 106.51) * mm});
            skLineSegment(sketch, "E895", {"start": v(23.6, 106.51) * mm, "end": v(23.55, 106.38) * mm});
            skLineSegment(sketch, "E896", {"start": v(23.55, 106.38) * mm, "end": v(23.5, 106.25) * mm});
            skLineSegment(sketch, "E897", {"start": v(23.5, 106.25) * mm, "end": v(23.44, 106.12) * mm});
            skLineSegment(sketch, "E898", {"start": v(23.44, 106.12) * mm, "end": v(23.25, 105.9) * mm});
            skLineSegment(sketch, "E899", {"start": v(23.25, 105.9) * mm, "end": v(18.87, 106.76) * mm});
            skLineSegment(sketch, "E900", {"start": v(18.87, 106.76) * mm, "end": v(18.78, 107.05) * mm});
            skLineSegment(sketch, "E901", {"start": v(18.78, 107.05) * mm, "end": v(18.78, 107.18) * mm});
            skLineSegment(sketch, "E902", {"start": v(18.78, 107.18) * mm, "end": v(18.78, 107.32) * mm});
            skLineSegment(sketch, "E903", {"start": v(18.78, 107.32) * mm, "end": v(18.78, 107.47) * mm});
            skLineSegment(sketch, "E904", {"start": v(18.78, 107.47) * mm, "end": v(18.78, 107.62) * mm});
            skLineSegment(sketch, "E905", {"start": v(18.78, 107.62) * mm, "end": v(18.78, 107.78) * mm});
            skLineSegment(sketch, "E906", {"start": v(18.78, 107.78) * mm, "end": v(18.77, 107.95) * mm});
            skLineSegment(sketch, "E907", {"start": v(18.77, 107.95) * mm, "end": v(18.77, 108.12) * mm});
            skLineSegment(sketch, "E908", {"start": v(18.77, 108.12) * mm, "end": v(18.76, 108.3) * mm});
            skLineSegment(sketch, "E909", {"start": v(18.76, 108.3) * mm, "end": v(18.75, 108.49) * mm});
            skLineSegment(sketch, "E910", {"start": v(18.75, 108.49) * mm, "end": v(18.74, 108.68) * mm});
            skLineSegment(sketch, "E911", {"start": v(18.74, 108.68) * mm, "end": v(18.73, 108.88) * mm});
            skLineSegment(sketch, "E912", {"start": v(18.73, 108.88) * mm, "end": v(18.71, 109.08) * mm});
            skLineSegment(sketch, "E913", {"start": v(18.71, 109.08) * mm, "end": v(18.7, 109.3) * mm});
            skLineSegment(sketch, "E914", {"start": v(18.7, 109.3) * mm, "end": v(18.68, 109.5) * mm});
            skLineSegment(sketch, "E915", {"start": v(18.68, 109.5) * mm, "end": v(18.65, 109.73) * mm});
            skLineSegment(sketch, "E916", {"start": v(18.65, 109.73) * mm, "end": v(18.63, 109.96) * mm});
            skLineSegment(sketch, "E917", {"start": v(18.63, 109.96) * mm, "end": v(18.6, 110.2) * mm});
            skLineSegment(sketch, "E918", {"start": v(18.6, 110.2) * mm, "end": v(18.58, 110.44) * mm});
            skLineSegment(sketch, "E919", {"start": v(18.58, 110.44) * mm, "end": v(18.54, 110.69) * mm});
            skLineSegment(sketch, "E920", {"start": v(18.54, 110.69) * mm, "end": v(18.5, 110.94) * mm});
            skLineSegment(sketch, "E921", {"start": v(18.5, 110.94) * mm, "end": v(18.47, 111.2) * mm});
            skLineSegment(sketch, "E922", {"start": v(18.47, 111.2) * mm, "end": v(18.43, 111.47) * mm});
            skLineSegment(sketch, "E923", {"start": v(18.43, 111.47) * mm, "end": v(18.39, 111.74) * mm});
            skLineSegment(sketch, "E924", {"start": v(18.39, 111.74) * mm, "end": v(18.34, 112.02) * mm});
            skLineSegment(sketch, "E925", {"start": v(18.34, 112.02) * mm, "end": v(18.3, 112.3) * mm});
            skLineSegment(sketch, "E926", {"start": v(18.3, 112.3) * mm, "end": v(18.24, 112.6) * mm});
            skLineSegment(sketch, "E927", {"start": v(18.24, 112.6) * mm, "end": v(18.18, 112.9) * mm});
            skLineSegment(sketch, "E928", {"start": v(18.18, 112.9) * mm, "end": v(18.12, 113.2) * mm});
            skLineSegment(sketch, "E929", {"start": v(18.12, 113.2) * mm, "end": v(18.06, 113.5) * mm});
            skLineSegment(sketch, "E930", {"start": v(18.06, 113.5) * mm, "end": v(18, 113.82) * mm});
            skLineSegment(sketch, "E931", {"start": v(18, 113.82) * mm, "end": v(17.92, 114.14) * mm});
            skLineSegment(sketch, "E932", {"start": v(17.92, 114.14) * mm, "end": v(17.85, 114.47) * mm});
            skLineSegment(sketch, "E933", {"start": v(17.85, 114.47) * mm, "end": v(17.77, 114.8) * mm});
            skLineSegment(sketch, "E934", {"start": v(17.77, 114.8) * mm, "end": v(17.68, 115.14) * mm});
            skLineSegment(sketch, "E935", {"start": v(17.68, 115.14) * mm, "end": v(17.6, 115.48) * mm});
            skLineSegment(sketch, "E936", {"start": v(17.6, 115.48) * mm, "end": v(17.5, 115.83) * mm});
            skLineSegment(sketch, "E937", {"start": v(17.5, 115.83) * mm, "end": v(17.4, 116.18) * mm});
            skLineSegment(sketch, "E938", {"start": v(17.4, 116.18) * mm, "end": v(17.3, 116.54) * mm});
            skLineSegment(sketch, "E939", {"start": v(17.3, 116.54) * mm, "end": v(17.2, 116.9) * mm});
            skLineSegment(sketch, "E940", {"start": v(17.2, 116.9) * mm, "end": v(17.1, 117.28) * mm});
            skLineSegment(sketch, "E941", {"start": v(17.1, 117.28) * mm, "end": v(16.98, 117.65) * mm});
            skLineSegment(sketch, "E942", {"start": v(16.98, 117.65) * mm, "end": v(16.86, 118.03) * mm});
            skLineSegment(sketch, "E943", {"start": v(16.86, 118.03) * mm, "end": v(16.7, 118.16) * mm});
            skLineSegment(sketch, "E944", {"start": v(16.7, 118.16) * mm, "end": v(13.21, 118.6) * mm});
            skLineSegment(sketch, "E945", {"start": v(13.21, 118.6) * mm, "end": v(13.03, 118.51) * mm});
            skLineSegment(sketch, "E946", {"start": v(13.03, 118.51) * mm, "end": v(12.82, 118.18) * mm});
            skLineSegment(sketch, "E947", {"start": v(12.82, 118.18) * mm, "end": v(12.61, 117.84) * mm});
            skLineSegment(sketch, "E948", {"start": v(12.61, 117.84) * mm, "end": v(12.41, 117.5) * mm});
            skLineSegment(sketch, "E949", {"start": v(12.41, 117.5) * mm, "end": v(12.22, 117.18) * mm});
            skLineSegment(sketch, "E950", {"start": v(12.22, 117.18) * mm, "end": v(12.03, 116.86) * mm});
            skLineSegment(sketch, "E951", {"start": v(12.03, 116.86) * mm, "end": v(11.85, 116.54) * mm});
            skLineSegment(sketch, "E952", {"start": v(11.85, 116.54) * mm, "end": v(11.68, 116.22) * mm});
            skLineSegment(sketch, "E953", {"start": v(11.68, 116.22) * mm, "end": v(11.5, 115.91) * mm});
            skLineSegment(sketch, "E954", {"start": v(11.5, 115.91) * mm, "end": v(11.34, 115.6) * mm});
            skLineSegment(sketch, "E955", {"start": v(11.34, 115.6) * mm, "end": v(11.18, 115.3) * mm});
            skLineSegment(sketch, "E956", {"start": v(11.18, 115.3) * mm, "end": v(11.03, 115) * mm});
            skLineSegment(sketch, "E957", {"start": v(11.03, 115) * mm, "end": v(10.88, 114.72) * mm});
            skLineSegment(sketch, "E958", {"start": v(10.88, 114.72) * mm, "end": v(10.74, 114.43) * mm});
            skLineSegment(sketch, "E959", {"start": v(10.74, 114.43) * mm, "end": v(10.6, 114.15) * mm});
            skLineSegment(sketch, "E960", {"start": v(10.6, 114.15) * mm, "end": v(10.47, 113.87) * mm});
            skLineSegment(sketch, "E961", {"start": v(10.47, 113.87) * mm, "end": v(10.34, 113.6) * mm});
            skLineSegment(sketch, "E962", {"start": v(10.34, 113.6) * mm, "end": v(10.21, 113.33) * mm});
            skLineSegment(sketch, "E963", {"start": v(10.21, 113.33) * mm, "end": v(10.1, 113.06) * mm});
            skLineSegment(sketch, "E964", {"start": v(10.1, 113.06) * mm, "end": v(9.98, 112.8) * mm});
            skLineSegment(sketch, "E965", {"start": v(9.98, 112.8) * mm, "end": v(9.87, 112.55) * mm});
            skLineSegment(sketch, "E966", {"start": v(9.87, 112.55) * mm, "end": v(9.77, 112.3) * mm});
            skLineSegment(sketch, "E967", {"start": v(9.77, 112.3) * mm, "end": v(9.67, 112.06) * mm});
            skLineSegment(sketch, "E968", {"start": v(9.67, 112.06) * mm, "end": v(9.57, 111.82) * mm});
            skLineSegment(sketch, "E969", {"start": v(9.57, 111.82) * mm, "end": v(9.48, 111.59) * mm});
            skLineSegment(sketch, "E970", {"start": v(9.48, 111.59) * mm, "end": v(9.39, 111.36) * mm});
            skLineSegment(sketch, "E971", {"start": v(9.39, 111.36) * mm, "end": v(9.3, 111.14) * mm});
            skLineSegment(sketch, "E972", {"start": v(9.3, 111.14) * mm, "end": v(9.23, 110.92) * mm});
            skLineSegment(sketch, "E973", {"start": v(9.23, 110.92) * mm, "end": v(9.15, 110.7) * mm});
            skLineSegment(sketch, "E974", {"start": v(9.15, 110.7) * mm, "end": v(9.08, 110.5) * mm});
            skLineSegment(sketch, "E975", {"start": v(9.08, 110.5) * mm, "end": v(9, 110.3) * mm});
            skLineSegment(sketch, "E976", {"start": v(9, 110.3) * mm, "end": v(8.94, 110.1) * mm});
            skLineSegment(sketch, "E977", {"start": v(8.94, 110.1) * mm, "end": v(8.88, 109.92) * mm});
            skLineSegment(sketch, "E978", {"start": v(8.88, 109.92) * mm, "end": v(8.82, 109.74) * mm});
            skLineSegment(sketch, "E979", {"start": v(8.82, 109.74) * mm, "end": v(8.77, 109.56) * mm});
            skLineSegment(sketch, "E980", {"start": v(8.77, 109.56) * mm, "end": v(8.72, 109.39) * mm});
            skLineSegment(sketch, "E981", {"start": v(8.72, 109.39) * mm, "end": v(8.67, 109.22) * mm});
            skLineSegment(sketch, "E982", {"start": v(8.67, 109.22) * mm, "end": v(8.62, 109.06) * mm});
            skLineSegment(sketch, "E983", {"start": v(8.62, 109.06) * mm, "end": v(8.58, 108.9) * mm});
            skLineSegment(sketch, "E984", {"start": v(8.58, 108.9) * mm, "end": v(8.54, 108.76) * mm});
            skLineSegment(sketch, "E985", {"start": v(8.54, 108.76) * mm, "end": v(8.5, 108.62) * mm});
            skLineSegment(sketch, "E986", {"start": v(8.5, 108.62) * mm, "end": v(8.47, 108.48) * mm});
            skLineSegment(sketch, "E987", {"start": v(8.47, 108.48) * mm, "end": v(8.44, 108.35) * mm});
            skLineSegment(sketch, "E988", {"start": v(8.44, 108.35) * mm, "end": v(8.28, 108.1) * mm});
            skLineSegment(sketch, "E989", {"start": v(8.28, 108.1) * mm, "end": v(3.82, 108.34) * mm});
            skLineSegment(sketch, "E990", {"start": v(3.82, 108.34) * mm, "end": v(3.7, 108.61) * mm});
            skLineSegment(sketch, "E991", {"start": v(3.7, 108.61) * mm, "end": v(3.67, 108.75) * mm});
            skLineSegment(sketch, "E992", {"start": v(3.67, 108.75) * mm, "end": v(3.66, 108.89) * mm});
            skLineSegment(sketch, "E993", {"start": v(3.66, 108.89) * mm, "end": v(3.63, 109.03) * mm});
            skLineSegment(sketch, "E994", {"start": v(3.63, 109.03) * mm, "end": v(3.61, 109.18) * mm});
            skLineSegment(sketch, "E995", {"start": v(3.61, 109.18) * mm, "end": v(3.59, 109.34) * mm});
            skLineSegment(sketch, "E996", {"start": v(3.59, 109.34) * mm, "end": v(3.56, 109.5) * mm});
            skLineSegment(sketch, "E997", {"start": v(3.56, 109.5) * mm, "end": v(3.53, 109.67) * mm});
            skLineSegment(sketch, "E998", {"start": v(3.53, 109.67) * mm, "end": v(3.5, 109.85) * mm});
            skLineSegment(sketch, "E999", {"start": v(3.5, 109.85) * mm, "end": v(3.46, 110.03) * mm});
            skLineSegment(sketch, "E1000", {"start": v(3.46, 110.03) * mm, "end": v(3.43, 110.22) * mm});
            skLineSegment(sketch, "E1001", {"start": v(3.43, 110.22) * mm, "end": v(3.39, 110.42) * mm});
            skLineSegment(sketch, "E1002", {"start": v(3.39, 110.42) * mm, "end": v(3.34, 110.62) * mm});
            skLineSegment(sketch, "E1003", {"start": v(3.34, 110.62) * mm, "end": v(3.3, 110.82) * mm});
            skLineSegment(sketch, "E1004", {"start": v(3.3, 110.82) * mm, "end": v(3.25, 111.04) * mm});
            skLineSegment(sketch, "E1005", {"start": v(3.25, 111.04) * mm, "end": v(3.2, 111.26) * mm});
            skLineSegment(sketch, "E1006", {"start": v(3.2, 111.26) * mm, "end": v(3.14, 111.48) * mm});
            skLineSegment(sketch, "E1007", {"start": v(3.14, 111.48) * mm, "end": v(3.08, 111.7) * mm});
            skLineSegment(sketch, "E1008", {"start": v(3.08, 111.7) * mm, "end": v(3.02, 111.95) * mm});
            skLineSegment(sketch, "E1009", {"start": v(3.02, 111.95) * mm, "end": v(2.95, 112.19) * mm});
            skLineSegment(sketch, "E1010", {"start": v(2.95, 112.19) * mm, "end": v(2.88, 112.43) * mm});
            skLineSegment(sketch, "E1011", {"start": v(2.88, 112.43) * mm, "end": v(2.81, 112.69) * mm});
            skLineSegment(sketch, "E1012", {"start": v(2.81, 112.69) * mm, "end": v(2.73, 112.95) * mm});
            skLineSegment(sketch, "E1013", {"start": v(2.73, 112.95) * mm, "end": v(2.65, 113.21) * mm});
            skLineSegment(sketch, "E1014", {"start": v(2.65, 113.21) * mm, "end": v(2.57, 113.48) * mm});
            skLineSegment(sketch, "E1015", {"start": v(2.57, 113.48) * mm, "end": v(2.48, 113.76) * mm});
            skLineSegment(sketch, "E1016", {"start": v(2.48, 113.76) * mm, "end": v(2.39, 114.04) * mm});
            skLineSegment(sketch, "E1017", {"start": v(2.39, 114.04) * mm, "end": v(2.29, 114.32) * mm});
            skLineSegment(sketch, "E1018", {"start": v(2.29, 114.32) * mm, "end": v(2.19, 114.61) * mm});
            skLineSegment(sketch, "E1019", {"start": v(2.19, 114.61) * mm, "end": v(2.08, 114.91) * mm});
            skLineSegment(sketch, "E1020", {"start": v(2.08, 114.91) * mm, "end": v(1.97, 115.21) * mm});
            skLineSegment(sketch, "E1021", {"start": v(1.97, 115.21) * mm, "end": v(1.86, 115.52) * mm});
            skLineSegment(sketch, "E1022", {"start": v(1.86, 115.52) * mm, "end": v(1.73, 115.83) * mm});
            skLineSegment(sketch, "E1023", {"start": v(1.73, 115.83) * mm, "end": v(1.61, 116.15) * mm});
            skLineSegment(sketch, "E1024", {"start": v(1.61, 116.15) * mm, "end": v(1.48, 116.47) * mm});
            skLineSegment(sketch, "E1025", {"start": v(1.48, 116.47) * mm, "end": v(1.35, 116.8) * mm});
            skLineSegment(sketch, "E1026", {"start": v(1.35, 116.8) * mm, "end": v(1.2, 117.13) * mm});
            skLineSegment(sketch, "E1027", {"start": v(1.2, 117.13) * mm, "end": v(1.06, 117.47) * mm});
            skLineSegment(sketch, "E1028", {"start": v(1.06, 117.47) * mm, "end": v(0.91, 117.8) * mm});
            skLineSegment(sketch, "E1029", {"start": v(0.91, 117.8) * mm, "end": v(0.76, 118.16) * mm});
            skLineSegment(sketch, "E1030", {"start": v(0.76, 118.16) * mm, "end": v(0.6, 118.5) * mm});
            skLineSegment(sketch, "E1031", {"start": v(0.6, 118.5) * mm, "end": v(0.43, 118.86) * mm});
            skLineSegment(sketch, "E1032", {"start": v(0.43, 118.86) * mm, "end": v(0.26, 119.22) * mm});
            skLineSegment(sketch, "E1033", {"start": v(0.26, 119.22) * mm, "end": v(0.08, 119.33) * mm});
            skLineSegment(sketch, "E1034", {"start": v(0.08, 119.33) * mm, "end": v(-3.43, 119.28) * mm});
            skLineSegment(sketch, "E1035", {"start": v(-3.43, 119.28) * mm, "end": v(-3.6, 119.17) * mm});
            skLineSegment(sketch, "E1036", {"start": v(-3.6, 119.17) * mm, "end": v(-3.76, 118.8) * mm});
            skLineSegment(sketch, "E1037", {"start": v(-3.76, 118.8) * mm, "end": v(-3.92, 118.44) * mm});
            skLineSegment(sketch, "E1038", {"start": v(-3.92, 118.44) * mm, "end": v(-4.07, 118.09) * mm});
            skLineSegment(sketch, "E1039", {"start": v(-4.07, 118.09) * mm, "end": v(-4.21, 117.74) * mm});
            skLineSegment(sketch, "E1040", {"start": v(-4.21, 117.74) * mm, "end": v(-4.35, 117.4) * mm});
            skLineSegment(sketch, "E1041", {"start": v(-4.35, 117.4) * mm, "end": v(-4.49, 117.05) * mm});
            skLineSegment(sketch, "E1042", {"start": v(-4.49, 117.05) * mm, "end": v(-4.62, 116.71) * mm});
            skLineSegment(sketch, "E1043", {"start": v(-4.62, 116.71) * mm, "end": v(-4.74, 116.38) * mm});
            skLineSegment(sketch, "E1044", {"start": v(-4.74, 116.38) * mm, "end": v(-4.86, 116.06) * mm});
            skLineSegment(sketch, "E1045", {"start": v(-4.86, 116.06) * mm, "end": v(-4.98, 115.74) * mm});
            skLineSegment(sketch, "E1046", {"start": v(-4.98, 115.74) * mm, "end": v(-5.1, 115.42) * mm});
            skLineSegment(sketch, "E1047", {"start": v(-5.1, 115.42) * mm, "end": v(-5.2, 115.1) * mm});
            skLineSegment(sketch, "E1048", {"start": v(-5.2, 115.1) * mm, "end": v(-5.3, 114.8) * mm});
            skLineSegment(sketch, "E1049", {"start": v(-5.3, 114.8) * mm, "end": v(-5.4, 114.5) * mm});
            skLineSegment(sketch, "E1050", {"start": v(-5.4, 114.5) * mm, "end": v(-5.49, 114.21) * mm});
            skLineSegment(sketch, "E1051", {"start": v(-5.49, 114.21) * mm, "end": v(-5.58, 113.92) * mm});
            skLineSegment(sketch, "E1052", {"start": v(-5.58, 113.92) * mm, "end": v(-5.66, 113.64) * mm});
            skLineSegment(sketch, "E1053", {"start": v(-5.66, 113.64) * mm, "end": v(-5.74, 113.36) * mm});
            skLineSegment(sketch, "E1054", {"start": v(-5.74, 113.36) * mm, "end": v(-5.82, 113.09) * mm});
            skLineSegment(sketch, "E1055", {"start": v(-5.82, 113.09) * mm, "end": v(-5.9, 112.82) * mm});
            skLineSegment(sketch, "E1056", {"start": v(-5.9, 112.82) * mm, "end": v(-5.96, 112.56) * mm});
            skLineSegment(sketch, "E1057", {"start": v(-5.96, 112.56) * mm, "end": v(-6.03, 112.3) * mm});
            skLineSegment(sketch, "E1058", {"start": v(-6.03, 112.3) * mm, "end": v(-6.1, 112.06) * mm});
            skLineSegment(sketch, "E1059", {"start": v(-6.1, 112.06) * mm, "end": v(-6.15, 111.81) * mm});
            skLineSegment(sketch, "E1060", {"start": v(-6.15, 111.81) * mm, "end": v(-6.2, 111.58) * mm});
            skLineSegment(sketch, "E1061", {"start": v(-6.2, 111.58) * mm, "end": v(-6.26, 111.34) * mm});
            skLineSegment(sketch, "E1062", {"start": v(-6.26, 111.34) * mm, "end": v(-6.3, 111.12) * mm});
            skLineSegment(sketch, "E1063", {"start": v(-6.3, 111.12) * mm, "end": v(-6.35, 110.9) * mm});
            skLineSegment(sketch, "E1064", {"start": v(-6.35, 110.9) * mm, "end": v(-6.4, 110.69) * mm});
            skLineSegment(sketch, "E1065", {"start": v(-6.4, 110.69) * mm, "end": v(-6.44, 110.48) * mm});
            skLineSegment(sketch, "E1066", {"start": v(-6.44, 110.48) * mm, "end": v(-6.47, 110.28) * mm});
            skLineSegment(sketch, "E1067", {"start": v(-6.47, 110.28) * mm, "end": v(-6.5, 110.08) * mm});
            skLineSegment(sketch, "E1068", {"start": v(-6.5, 110.08) * mm, "end": v(-6.54, 109.9) * mm});
            skLineSegment(sketch, "E1069", {"start": v(-6.54, 109.9) * mm, "end": v(-6.57, 109.7) * mm});
            skLineSegment(sketch, "E1070", {"start": v(-6.57, 109.7) * mm, "end": v(-6.6, 109.53) * mm});
            skLineSegment(sketch, "E1071", {"start": v(-6.6, 109.53) * mm, "end": v(-6.62, 109.36) * mm});
            skLineSegment(sketch, "E1072", {"start": v(-6.62, 109.36) * mm, "end": v(-6.64, 109.2) * mm});
            skLineSegment(sketch, "E1073", {"start": v(-6.64, 109.2) * mm, "end": v(-6.66, 109.04) * mm});
            skLineSegment(sketch, "E1074", {"start": v(-6.66, 109.04) * mm, "end": v(-6.68, 108.88) * mm});
            skLineSegment(sketch, "E1075", {"start": v(-6.68, 108.88) * mm, "end": v(-6.7, 108.74) * mm});
            skLineSegment(sketch, "E1076", {"start": v(-6.7, 108.74) * mm, "end": v(-6.71, 108.6) * mm});
            skLineSegment(sketch, "E1077", {"start": v(-6.71, 108.6) * mm, "end": v(-6.73, 108.46) * mm});
            skLineSegment(sketch, "E1078", {"start": v(-6.73, 108.46) * mm, "end": v(-6.85, 108.19) * mm});
            skLineSegment(sketch, "E1079", {"start": v(-6.85, 108.19) * mm, "end": v(-11.3, 107.81) * mm});
            skLineSegment(sketch, "E1080", {"start": v(-11.3, 107.81) * mm, "end": v(-11.47, 108.06) * mm});
            skLineSegment(sketch, "E1081", {"start": v(-11.47, 108.06) * mm, "end": v(-11.5, 108.2) * mm});
            skLineSegment(sketch, "E1082", {"start": v(-11.5, 108.2) * mm, "end": v(-11.54, 108.33) * mm});
            skLineSegment(sketch, "E1083", {"start": v(-11.54, 108.33) * mm, "end": v(-11.58, 108.47) * mm});
            skLineSegment(sketch, "E1084", {"start": v(-11.58, 108.47) * mm, "end": v(-11.63, 108.62) * mm});
            skLineSegment(sketch, "E1085", {"start": v(-11.63, 108.62) * mm, "end": v(-11.67, 108.77) * mm});
            skLineSegment(sketch, "E1086", {"start": v(-11.67, 108.77) * mm, "end": v(-11.72, 108.93) * mm});
            skLineSegment(sketch, "E1087", {"start": v(-11.72, 108.93) * mm, "end": v(-11.78, 109.1) * mm});
            skLineSegment(sketch, "E1088", {"start": v(-11.78, 109.1) * mm, "end": v(-11.83, 109.26) * mm});
            skLineSegment(sketch, "E1089", {"start": v(-11.83, 109.26) * mm, "end": v(-11.9, 109.44) * mm});
            skLineSegment(sketch, "E1090", {"start": v(-11.9, 109.44) * mm, "end": v(-11.95, 109.62) * mm});
            skLineSegment(sketch, "E1091", {"start": v(-11.95, 109.62) * mm, "end": v(-12.02, 109.8) * mm});
            skLineSegment(sketch, "E1092", {"start": v(-12.02, 109.8) * mm, "end": v(-12.1, 110) * mm});
            skLineSegment(sketch, "E1093", {"start": v(-12.1, 110) * mm, "end": v(-12.17, 110.2) * mm});
            skLineSegment(sketch, "E1094", {"start": v(-12.17, 110.2) * mm, "end": v(-12.24, 110.4) * mm});
            skLineSegment(sketch, "E1095", {"start": v(-12.24, 110.4) * mm, "end": v(-12.33, 110.61) * mm});
            skLineSegment(sketch, "E1096", {"start": v(-12.33, 110.61) * mm, "end": v(-12.41, 110.83) * mm});
            skLineSegment(sketch, "E1097", {"start": v(-12.41, 110.83) * mm, "end": v(-12.5, 111.05) * mm});
            skLineSegment(sketch, "E1098", {"start": v(-12.5, 111.05) * mm, "end": v(-12.6, 111.27) * mm});
            skLineSegment(sketch, "E1099", {"start": v(-12.6, 111.27) * mm, "end": v(-12.7, 111.5) * mm});
            skLineSegment(sketch, "E1100", {"start": v(-12.7, 111.5) * mm, "end": v(-12.8, 111.74) * mm});
            skLineSegment(sketch, "E1101", {"start": v(-12.8, 111.74) * mm, "end": v(-12.9, 111.98) * mm});
            skLineSegment(sketch, "E1102", {"start": v(-12.9, 111.98) * mm, "end": v(-13.02, 112.22) * mm});
            skLineSegment(sketch, "E1103", {"start": v(-13.02, 112.22) * mm, "end": v(-13.14, 112.47) * mm});
            skLineSegment(sketch, "E1104", {"start": v(-13.14, 112.47) * mm, "end": v(-13.26, 112.73) * mm});
            skLineSegment(sketch, "E1105", {"start": v(-13.26, 112.73) * mm, "end": v(-13.38, 112.99) * mm});
            skLineSegment(sketch, "E1106", {"start": v(-13.38, 112.99) * mm, "end": v(-13.51, 113.25) * mm});
            skLineSegment(sketch, "E1107", {"start": v(-13.51, 113.25) * mm, "end": v(-13.65, 113.52) * mm});
            skLineSegment(sketch, "E1108", {"start": v(-13.65, 113.52) * mm, "end": v(-13.8, 113.8) * mm});
            skLineSegment(sketch, "E1109", {"start": v(-13.8, 113.8) * mm, "end": v(-13.94, 114.08) * mm});
            skLineSegment(sketch, "E1110", {"start": v(-13.94, 114.08) * mm, "end": v(-14.09, 114.36) * mm});
            skLineSegment(sketch, "E1111", {"start": v(-14.09, 114.36) * mm, "end": v(-14.25, 114.65) * mm});
            skLineSegment(sketch, "E1112", {"start": v(-14.25, 114.65) * mm, "end": v(-14.4, 114.94) * mm});
            skLineSegment(sketch, "E1113", {"start": v(-14.4, 114.94) * mm, "end": v(-14.58, 115.24) * mm});
            skLineSegment(sketch, "E1114", {"start": v(-14.58, 115.24) * mm, "end": v(-14.75, 115.54) * mm});
            skLineSegment(sketch, "E1115", {"start": v(-14.75, 115.54) * mm, "end": v(-14.93, 115.84) * mm});
            skLineSegment(sketch, "E1116", {"start": v(-14.93, 115.84) * mm, "end": v(-15.11, 116.15) * mm});
            skLineSegment(sketch, "E1117", {"start": v(-15.11, 116.15) * mm, "end": v(-15.3, 116.47) * mm});
            skLineSegment(sketch, "E1118", {"start": v(-15.3, 116.47) * mm, "end": v(-15.5, 116.78) * mm});
            skLineSegment(sketch, "E1119", {"start": v(-15.5, 116.78) * mm, "end": v(-15.7, 117.1) * mm});
            skLineSegment(sketch, "E1120", {"start": v(-15.7, 117.1) * mm, "end": v(-15.9, 117.43) * mm});
            skLineSegment(sketch, "E1121", {"start": v(-15.9, 117.43) * mm, "end": v(-16.12, 117.76) * mm});
            skLineSegment(sketch, "E1122", {"start": v(-16.12, 117.76) * mm, "end": v(-16.34, 118.1) * mm});
            skLineSegment(sketch, "E1123", {"start": v(-16.34, 118.1) * mm, "end": v(-16.53, 118.18) * mm});
            skLineSegment(sketch, "E1124", {"start": v(-16.53, 118.18) * mm, "end": v(-20, 117.64) * mm});
            skLineSegment(sketch, "E1125", {"start": v(-20, 117.64) * mm, "end": v(-20.16, 117.5) * mm});
            skLineSegment(sketch, "E1126", {"start": v(-20.16, 117.5) * mm, "end": v(-20.27, 117.12) * mm});
            skLineSegment(sketch, "E1127", {"start": v(-20.27, 117.12) * mm, "end": v(-20.37, 116.74) * mm});
            skLineSegment(sketch, "E1128", {"start": v(-20.37, 116.74) * mm, "end": v(-20.47, 116.37) * mm});
            skLineSegment(sketch, "E1129", {"start": v(-20.47, 116.37) * mm, "end": v(-20.56, 116) * mm});
            skLineSegment(sketch, "E1130", {"start": v(-20.56, 116) * mm, "end": v(-20.66, 115.64) * mm});
            skLineSegment(sketch, "E1131", {"start": v(-20.66, 115.64) * mm, "end": v(-20.74, 115.28) * mm});
            skLineSegment(sketch, "E1132", {"start": v(-20.74, 115.28) * mm, "end": v(-20.82, 114.93) * mm});
            skLineSegment(sketch, "E1133", {"start": v(-20.82, 114.93) * mm, "end": v(-20.9, 114.58) * mm});
            skLineSegment(sketch, "E1134", {"start": v(-20.9, 114.58) * mm, "end": v(-20.98, 114.24) * mm});
            skLineSegment(sketch, "E1135", {"start": v(-20.98, 114.24) * mm, "end": v(-21.04, 113.91) * mm});
            skLineSegment(sketch, "E1136", {"start": v(-21.04, 113.91) * mm, "end": v(-21.11, 113.58) * mm});
            skLineSegment(sketch, "E1137", {"start": v(-21.11, 113.58) * mm, "end": v(-21.17, 113.26) * mm});
            skLineSegment(sketch, "E1138", {"start": v(-21.17, 113.26) * mm, "end": v(-21.23, 112.95) * mm});
            skLineSegment(sketch, "E1139", {"start": v(-21.23, 112.95) * mm, "end": v(-21.29, 112.63) * mm});
            skLineSegment(sketch, "E1140", {"start": v(-21.29, 112.63) * mm, "end": v(-21.34, 112.33) * mm});
            skLineSegment(sketch, "E1141", {"start": v(-21.34, 112.33) * mm, "end": v(-21.39, 112.03) * mm});
            skLineSegment(sketch, "E1142", {"start": v(-21.39, 112.03) * mm, "end": v(-21.43, 111.74) * mm});
            skLineSegment(sketch, "E1143", {"start": v(-21.43, 111.74) * mm, "end": v(-21.47, 111.45) * mm});
            skLineSegment(sketch, "E1144", {"start": v(-21.47, 111.45) * mm, "end": v(-21.5, 111.17) * mm});
            skLineSegment(sketch, "E1145", {"start": v(-21.5, 111.17) * mm, "end": v(-21.55, 110.9) * mm});
            skLineSegment(sketch, "E1146", {"start": v(-21.55, 110.9) * mm, "end": v(-21.58, 110.63) * mm});
            skLineSegment(sketch, "E1147", {"start": v(-21.58, 110.63) * mm, "end": v(-21.6, 110.37) * mm});
            skLineSegment(sketch, "E1148", {"start": v(-21.6, 110.37) * mm, "end": v(-21.63, 110.11) * mm});
            skLineSegment(sketch, "E1149", {"start": v(-21.63, 110.11) * mm, "end": v(-21.66, 109.86) * mm});
            skLineSegment(sketch, "E1150", {"start": v(-21.66, 109.86) * mm, "end": v(-21.68, 109.62) * mm});
            skLineSegment(sketch, "E1151", {"start": v(-21.68, 109.62) * mm, "end": v(-21.7, 109.39) * mm});
            skLineSegment(sketch, "E1152", {"start": v(-21.7, 109.39) * mm, "end": v(-21.72, 109.15) * mm});
            skLineSegment(sketch, "E1153", {"start": v(-21.72, 109.15) * mm, "end": v(-21.73, 108.93) * mm});
            skLineSegment(sketch, "E1154", {"start": v(-21.73, 108.93) * mm, "end": v(-21.75, 108.71) * mm});
            skLineSegment(sketch, "E1155", {"start": v(-21.75, 108.71) * mm, "end": v(-21.76, 108.5) * mm});
            skLineSegment(sketch, "E1156", {"start": v(-21.76, 108.5) * mm, "end": v(-21.77, 108.3) * mm});
            skLineSegment(sketch, "E1157", {"start": v(-21.77, 108.3) * mm, "end": v(-21.77, 108.1) * mm});
            skLineSegment(sketch, "E1158", {"start": v(-21.77, 108.1) * mm, "end": v(-21.78, 107.9) * mm});
            skLineSegment(sketch, "E1159", {"start": v(-21.78, 107.9) * mm, "end": v(-21.78, 107.72) * mm});
            skLineSegment(sketch, "E1160", {"start": v(-21.78, 107.72) * mm, "end": v(-21.78, 107.54) * mm});
            skLineSegment(sketch, "E1161", {"start": v(-21.78, 107.54) * mm, "end": v(-21.78, 107.37) * mm});
            skLineSegment(sketch, "E1162", {"start": v(-21.78, 107.37) * mm, "end": v(-21.78, 107.2) * mm});
            skLineSegment(sketch, "E1163", {"start": v(-21.78, 107.2) * mm, "end": v(-21.78, 107.04) * mm});
            skLineSegment(sketch, "E1164", {"start": v(-21.78, 107.04) * mm, "end": v(-21.78, 106.89) * mm});
            skLineSegment(sketch, "E1165", {"start": v(-21.78, 106.89) * mm, "end": v(-21.77, 106.74) * mm});
            skLineSegment(sketch, "E1166", {"start": v(-21.77, 106.74) * mm, "end": v(-21.77, 106.6) * mm});
            skLineSegment(sketch, "E1167", {"start": v(-21.77, 106.6) * mm, "end": v(-21.76, 106.47) * mm});
            skLineSegment(sketch, "E1168", {"start": v(-21.76, 106.47) * mm, "end": v(-21.85, 106.18) * mm});
            skLineSegment(sketch, "E1169", {"start": v(-21.85, 106.18) * mm, "end": v(-26.2, 105.19) * mm});
            skLineSegment(sketch, "E1170", {"start": v(-26.2, 105.19) * mm, "end": v(-26.4, 105.41) * mm});
            skLineSegment(sketch, "E1171", {"start": v(-26.4, 105.41) * mm, "end": v(-26.45, 105.53) * mm});
            skLineSegment(sketch, "E1172", {"start": v(-26.45, 105.53) * mm, "end": v(-26.51, 105.66) * mm});
            skLineSegment(sketch, "E1173", {"start": v(-26.51, 105.66) * mm, "end": v(-26.57, 105.8) * mm});
            skLineSegment(sketch, "E1174", {"start": v(-26.57, 105.8) * mm, "end": v(-26.64, 105.94) * mm});
            skLineSegment(sketch, "E1175", {"start": v(-26.64, 105.94) * mm, "end": v(-26.7, 106.08) * mm});
            skLineSegment(sketch, "E1176", {"start": v(-26.7, 106.08) * mm, "end": v(-26.77, 106.23) * mm});
            skLineSegment(sketch, "E1177", {"start": v(-26.77, 106.23) * mm, "end": v(-26.85, 106.39) * mm});
            skLineSegment(sketch, "E1178", {"start": v(-26.85, 106.39) * mm, "end": v(-26.93, 106.55) * mm});
            skLineSegment(sketch, "E1179", {"start": v(-26.93, 106.55) * mm, "end": v(-27.01, 106.71) * mm});
            skLineSegment(sketch, "E1180", {"start": v(-27.01, 106.71) * mm, "end": v(-27.1, 106.89) * mm});
            skLineSegment(sketch, "E1181", {"start": v(-27.1, 106.89) * mm, "end": v(-27.2, 107.06) * mm});
            skLineSegment(sketch, "E1182", {"start": v(-27.2, 107.06) * mm, "end": v(-27.29, 107.24) * mm});
            skLineSegment(sketch, "E1183", {"start": v(-27.29, 107.24) * mm, "end": v(-27.4, 107.43) * mm});
            skLineSegment(sketch, "E1184", {"start": v(-27.4, 107.43) * mm, "end": v(-27.5, 107.62) * mm});
            skLineSegment(sketch, "E1185", {"start": v(-27.5, 107.62) * mm, "end": v(-27.6, 107.81) * mm});
            skLineSegment(sketch, "E1186", {"start": v(-27.6, 107.81) * mm, "end": v(-27.72, 108.01) * mm});
            skLineSegment(sketch, "E1187", {"start": v(-27.72, 108.01) * mm, "end": v(-27.84, 108.22) * mm});
            skLineSegment(sketch, "E1188", {"start": v(-27.84, 108.22) * mm, "end": v(-27.97, 108.43) * mm});
            skLineSegment(sketch, "E1189", {"start": v(-27.97, 108.43) * mm, "end": v(-28.1, 108.64) * mm});
            skLineSegment(sketch, "E1190", {"start": v(-28.1, 108.64) * mm, "end": v(-28.23, 108.86) * mm});
            skLineSegment(sketch, "E1191", {"start": v(-28.23, 108.86) * mm, "end": v(-28.37, 109.08) * mm});
            skLineSegment(sketch, "E1192", {"start": v(-28.37, 109.08) * mm, "end": v(-28.52, 109.31) * mm});
            skLineSegment(sketch, "E1193", {"start": v(-28.52, 109.31) * mm, "end": v(-28.67, 109.54) * mm});
            skLineSegment(sketch, "E1194", {"start": v(-28.67, 109.54) * mm, "end": v(-28.82, 109.78) * mm});
            skLineSegment(sketch, "E1195", {"start": v(-28.82, 109.78) * mm, "end": v(-28.98, 110.02) * mm});
            skLineSegment(sketch, "E1196", {"start": v(-28.98, 110.02) * mm, "end": v(-29.15, 110.26) * mm});
            skLineSegment(sketch, "E1197", {"start": v(-29.15, 110.26) * mm, "end": v(-29.32, 110.51) * mm});
            skLineSegment(sketch, "E1198", {"start": v(-29.32, 110.51) * mm, "end": v(-29.5, 110.77) * mm});
            skLineSegment(sketch, "E1199", {"start": v(-29.5, 110.77) * mm, "end": v(-29.69, 111.02) * mm});
            skLineSegment(sketch, "E1200", {"start": v(-29.69, 111.02) * mm, "end": v(-29.87, 111.28) * mm});
            skLineSegment(sketch, "E1201", {"start": v(-29.87, 111.28) * mm, "end": v(-30.07, 111.54) * mm});
            skLineSegment(sketch, "E1202", {"start": v(-30.07, 111.54) * mm, "end": v(-30.27, 111.81) * mm});
            skLineSegment(sketch, "E1203", {"start": v(-30.27, 111.81) * mm, "end": v(-30.48, 112.08) * mm});
            skLineSegment(sketch, "E1204", {"start": v(-30.48, 112.08) * mm, "end": v(-30.7, 112.36) * mm});
            skLineSegment(sketch, "E1205", {"start": v(-30.7, 112.36) * mm, "end": v(-30.91, 112.63) * mm});
            skLineSegment(sketch, "E1206", {"start": v(-30.91, 112.63) * mm, "end": v(-31.14, 112.91) * mm});
            skLineSegment(sketch, "E1207", {"start": v(-31.14, 112.91) * mm, "end": v(-31.37, 113.2) * mm});
            skLineSegment(sketch, "E1208", {"start": v(-31.37, 113.2) * mm, "end": v(-31.6, 113.49) * mm});
            skLineSegment(sketch, "E1209", {"start": v(-31.6, 113.49) * mm, "end": v(-31.85, 113.78) * mm});
            skLineSegment(sketch, "E1210", {"start": v(-31.85, 113.78) * mm, "end": v(-32.1, 114.07) * mm});
            skLineSegment(sketch, "E1211", {"start": v(-32.1, 114.07) * mm, "end": v(-32.36, 114.37) * mm});
            skLineSegment(sketch, "E1212", {"start": v(-32.36, 114.37) * mm, "end": v(-32.62, 114.66) * mm});
            skLineSegment(sketch, "E1213", {"start": v(-32.62, 114.66) * mm, "end": v(-32.82, 114.72) * mm});
            skLineSegment(sketch, "E1214", {"start": v(-32.82, 114.72) * mm, "end": v(-36.18, 113.7) * mm});
            skLineSegment(sketch, "E1215", {"start": v(-36.18, 113.7) * mm, "end": v(-36.32, 113.55) * mm});
            skLineSegment(sketch, "E1216", {"start": v(-36.32, 113.55) * mm, "end": v(-36.38, 113.15) * mm});
            skLineSegment(sketch, "E1217", {"start": v(-36.38, 113.15) * mm, "end": v(-36.43, 112.76) * mm});
            skLineSegment(sketch, "E1218", {"start": v(-36.43, 112.76) * mm, "end": v(-36.47, 112.38) * mm});
            skLineSegment(sketch, "E1219", {"start": v(-36.47, 112.38) * mm, "end": v(-36.52, 112) * mm});
            skLineSegment(sketch, "E1220", {"start": v(-36.52, 112) * mm, "end": v(-36.55, 111.63) * mm});
            skLineSegment(sketch, "E1221", {"start": v(-36.55, 111.63) * mm, "end": v(-36.6, 111.27) * mm});
            skLineSegment(sketch, "E1222", {"start": v(-36.6, 111.27) * mm, "end": v(-36.62, 110.9) * mm});
            skLineSegment(sketch, "E1223", {"start": v(-36.62, 110.9) * mm, "end": v(-36.65, 110.55) * mm});
            skLineSegment(sketch, "E1224", {"start": v(-36.65, 110.55) * mm, "end": v(-36.68, 110.2) * mm});
            skLineSegment(sketch, "E1225", {"start": v(-36.68, 110.2) * mm, "end": v(-36.7, 109.87) * mm});
            skLineSegment(sketch, "E1226", {"start": v(-36.7, 109.87) * mm, "end": v(-36.72, 109.53) * mm});
            skLineSegment(sketch, "E1227", {"start": v(-36.72, 109.53) * mm, "end": v(-36.74, 109.2) * mm});
            skLineSegment(sketch, "E1228", {"start": v(-36.74, 109.2) * mm, "end": v(-36.75, 108.89) * mm});
            skLineSegment(sketch, "E1229", {"start": v(-36.75, 108.89) * mm, "end": v(-36.76, 108.57) * mm});
            skLineSegment(sketch, "E1230", {"start": v(-36.76, 108.57) * mm, "end": v(-36.77, 108.26) * mm});
            skLineSegment(sketch, "E1231", {"start": v(-36.77, 108.26) * mm, "end": v(-36.78, 107.96) * mm});
            skLineSegment(sketch, "E1232", {"start": v(-36.78, 107.96) * mm, "end": v(-36.78, 107.66) * mm});
            skLineSegment(sketch, "E1233", {"start": v(-36.78, 107.66) * mm, "end": v(-36.78, 107.38) * mm});
            skLineSegment(sketch, "E1234", {"start": v(-36.78, 107.38) * mm, "end": v(-36.78, 107.1) * mm});
            skLineSegment(sketch, "E1235", {"start": v(-36.78, 107.1) * mm, "end": v(-36.78, 106.82) * mm});
            skLineSegment(sketch, "E1236", {"start": v(-36.78, 106.82) * mm, "end": v(-36.77, 106.55) * mm});
            skLineSegment(sketch, "E1237", {"start": v(-36.77, 106.55) * mm, "end": v(-36.76, 106.28) * mm});
            skLineSegment(sketch, "E1238", {"start": v(-36.76, 106.28) * mm, "end": v(-36.76, 106.03) * mm});
            skLineSegment(sketch, "E1239", {"start": v(-36.76, 106.03) * mm, "end": v(-36.74, 105.78) * mm});
            skLineSegment(sketch, "E1240", {"start": v(-36.74, 105.78) * mm, "end": v(-36.73, 105.53) * mm});
            skLineSegment(sketch, "E1241", {"start": v(-36.73, 105.53) * mm, "end": v(-36.72, 105.3) * mm});
            skLineSegment(sketch, "E1242", {"start": v(-36.72, 105.3) * mm, "end": v(-36.7, 105.07) * mm});
            skLineSegment(sketch, "E1243", {"start": v(-36.7, 105.07) * mm, "end": v(-36.69, 104.84) * mm});
            skLineSegment(sketch, "E1244", {"start": v(-36.69, 104.84) * mm, "end": v(-36.67, 104.62) * mm});
            skLineSegment(sketch, "E1245", {"start": v(-36.67, 104.62) * mm, "end": v(-36.65, 104.41) * mm});
            skLineSegment(sketch, "E1246", {"start": v(-36.65, 104.41) * mm, "end": v(-36.63, 104.2) * mm});
            skLineSegment(sketch, "E1247", {"start": v(-36.63, 104.2) * mm, "end": v(-36.61, 104.01) * mm});
            skLineSegment(sketch, "E1248", {"start": v(-36.61, 104.01) * mm, "end": v(-36.59, 103.82) * mm});
            skLineSegment(sketch, "E1249", {"start": v(-36.59, 103.82) * mm, "end": v(-36.57, 103.64) * mm});
            skLineSegment(sketch, "E1250", {"start": v(-36.57, 103.64) * mm, "end": v(-36.54, 103.46) * mm});
            skLineSegment(sketch, "E1251", {"start": v(-36.54, 103.46) * mm, "end": v(-36.52, 103.29) * mm});
            skLineSegment(sketch, "E1252", {"start": v(-36.52, 103.29) * mm, "end": v(-36.5, 103.12) * mm});
            skLineSegment(sketch, "E1253", {"start": v(-36.5, 103.12) * mm, "end": v(-36.47, 102.96) * mm});
            skLineSegment(sketch, "E1254", {"start": v(-36.47, 102.96) * mm, "end": v(-36.45, 102.81) * mm});
            skLineSegment(sketch, "E1255", {"start": v(-36.45, 102.81) * mm, "end": v(-36.42, 102.67) * mm});
            skLineSegment(sketch, "E1256", {"start": v(-36.42, 102.67) * mm, "end": v(-36.4, 102.53) * mm});
            skLineSegment(sketch, "E1257", {"start": v(-36.4, 102.53) * mm, "end": v(-36.38, 102.4) * mm});
            skLineSegment(sketch, "E1258", {"start": v(-36.38, 102.4) * mm, "end": v(-36.42, 102.1) * mm});
            skLineSegment(sketch, "E1259", {"start": v(-36.42, 102.1) * mm, "end": v(-40.6, 100.51) * mm});
            skLineSegment(sketch, "E1260", {"start": v(-40.6, 100.51) * mm, "end": v(-40.82, 100.7) * mm});
            skLineSegment(sketch, "E1261", {"start": v(-40.82, 100.7) * mm, "end": v(-40.9, 100.82) * mm});
            skLineSegment(sketch, "E1262", {"start": v(-40.9, 100.82) * mm, "end": v(-40.97, 100.94) * mm});
            skLineSegment(sketch, "E1263", {"start": v(-40.97, 100.94) * mm, "end": v(-41.04, 101.06) * mm});
            skLineSegment(sketch, "E1264", {"start": v(-41.04, 101.06) * mm, "end": v(-41.13, 101.2) * mm});
            skLineSegment(sketch, "E1265", {"start": v(-41.13, 101.2) * mm, "end": v(-41.21, 101.33) * mm});
            skLineSegment(sketch, "E1266", {"start": v(-41.21, 101.33) * mm, "end": v(-41.3, 101.47) * mm});
            skLineSegment(sketch, "E1267", {"start": v(-41.3, 101.47) * mm, "end": v(-41.4, 101.61) * mm});
            skLineSegment(sketch, "E1268", {"start": v(-41.4, 101.61) * mm, "end": v(-41.5, 101.76) * mm});
            skLineSegment(sketch, "E1269", {"start": v(-41.5, 101.76) * mm, "end": v(-41.6, 101.91) * mm});
            skLineSegment(sketch, "E1270", {"start": v(-41.6, 101.91) * mm, "end": v(-41.72, 102.07) * mm});
            skLineSegment(sketch, "E1271", {"start": v(-41.72, 102.07) * mm, "end": v(-41.84, 102.23) * mm});
            skLineSegment(sketch, "E1272", {"start": v(-41.84, 102.23) * mm, "end": v(-41.96, 102.4) * mm});
            skLineSegment(sketch, "E1273", {"start": v(-41.96, 102.4) * mm, "end": v(-42.08, 102.57) * mm});
            skLineSegment(sketch, "E1274", {"start": v(-42.08, 102.57) * mm, "end": v(-42.21, 102.74) * mm});
            skLineSegment(sketch, "E1275", {"start": v(-42.21, 102.74) * mm, "end": v(-42.35, 102.92) * mm});
            skLineSegment(sketch, "E1276", {"start": v(-42.35, 102.92) * mm, "end": v(-42.5, 103.1) * mm});
            skLineSegment(sketch, "E1277", {"start": v(-42.5, 103.1) * mm, "end": v(-42.64, 103.29) * mm});
            skLineSegment(sketch, "E1278", {"start": v(-42.64, 103.29) * mm, "end": v(-42.8, 103.48) * mm});
            skLineSegment(sketch, "E1279", {"start": v(-42.8, 103.48) * mm, "end": v(-42.95, 103.67) * mm});
            skLineSegment(sketch, "E1280", {"start": v(-42.95, 103.67) * mm, "end": v(-43.12, 103.87) * mm});
            skLineSegment(sketch, "E1281", {"start": v(-43.12, 103.87) * mm, "end": v(-43.28, 104.07) * mm});
            skLineSegment(sketch, "E1282", {"start": v(-43.28, 104.07) * mm, "end": v(-43.46, 104.27) * mm});
            skLineSegment(sketch, "E1283", {"start": v(-43.46, 104.27) * mm, "end": v(-43.64, 104.48) * mm});
            skLineSegment(sketch, "E1284", {"start": v(-43.64, 104.48) * mm, "end": v(-43.83, 104.7) * mm});
            skLineSegment(sketch, "E1285", {"start": v(-43.83, 104.7) * mm, "end": v(-44.02, 104.91) * mm});
            skLineSegment(sketch, "E1286", {"start": v(-44.02, 104.91) * mm, "end": v(-44.22, 105.13) * mm});
            skLineSegment(sketch, "E1287", {"start": v(-44.22, 105.13) * mm, "end": v(-44.43, 105.35) * mm});
            skLineSegment(sketch, "E1288", {"start": v(-44.43, 105.35) * mm, "end": v(-44.64, 105.58) * mm});
            skLineSegment(sketch, "E1289", {"start": v(-44.64, 105.58) * mm, "end": v(-44.85, 105.8) * mm});
            skLineSegment(sketch, "E1290", {"start": v(-44.85, 105.8) * mm, "end": v(-45.08, 106.03) * mm});
            skLineSegment(sketch, "E1291", {"start": v(-45.08, 106.03) * mm, "end": v(-45.3, 106.27) * mm});
            skLineSegment(sketch, "E1292", {"start": v(-45.3, 106.27) * mm, "end": v(-45.54, 106.5) * mm});
            skLineSegment(sketch, "E1293", {"start": v(-45.54, 106.5) * mm, "end": v(-45.79, 106.74) * mm});
            skLineSegment(sketch, "E1294", {"start": v(-45.79, 106.74) * mm, "end": v(-46.04, 106.99) * mm});
            skLineSegment(sketch, "E1295", {"start": v(-46.04, 106.99) * mm, "end": v(-46.3, 107.23) * mm});
            skLineSegment(sketch, "E1296", {"start": v(-46.3, 107.23) * mm, "end": v(-46.56, 107.48) * mm});
            skLineSegment(sketch, "E1297", {"start": v(-46.56, 107.48) * mm, "end": v(-46.83, 107.73) * mm});
            skLineSegment(sketch, "E1298", {"start": v(-46.83, 107.73) * mm, "end": v(-47.1, 107.98) * mm});
            skLineSegment(sketch, "E1299", {"start": v(-47.1, 107.98) * mm, "end": v(-47.38, 108.23) * mm});
            skLineSegment(sketch, "E1300", {"start": v(-47.38, 108.23) * mm, "end": v(-47.67, 108.49) * mm});
            skLineSegment(sketch, "E1301", {"start": v(-47.67, 108.49) * mm, "end": v(-47.97, 108.74) * mm});
            skLineSegment(sketch, "E1302", {"start": v(-47.97, 108.74) * mm, "end": v(-48.27, 109) * mm});
            skLineSegment(sketch, "E1303", {"start": v(-48.27, 109) * mm, "end": v(-48.48, 109.03) * mm});
            skLineSegment(sketch, "E1304", {"start": v(-48.48, 109.03) * mm, "end": v(-51.66, 107.55) * mm});
            skLineSegment(sketch, "E1305", {"start": v(-51.66, 107.55) * mm, "end": v(-51.78, 107.38) * mm});
            skLineSegment(sketch, "E1306", {"start": v(-51.78, 107.38) * mm, "end": v(-51.78, 106.98) * mm});
            skLineSegment(sketch, "E1307", {"start": v(-51.78, 106.98) * mm, "end": v(-51.77, 106.6) * mm});
            skLineSegment(sketch, "E1308", {"start": v(-51.77, 106.6) * mm, "end": v(-51.76, 106.2) * mm});
            skLineSegment(sketch, "E1309", {"start": v(-51.76, 106.2) * mm, "end": v(-51.75, 105.82) * mm});
            skLineSegment(sketch, "E1310", {"start": v(-51.75, 105.82) * mm, "end": v(-51.74, 105.45) * mm});
            skLineSegment(sketch, "E1311", {"start": v(-51.74, 105.45) * mm, "end": v(-51.73, 105.09) * mm});
            skLineSegment(sketch, "E1312", {"start": v(-51.73, 105.09) * mm, "end": v(-51.7, 104.73) * mm});
            skLineSegment(sketch, "E1313", {"start": v(-51.7, 104.73) * mm, "end": v(-51.69, 104.37) * mm});
            skLineSegment(sketch, "E1314", {"start": v(-51.69, 104.37) * mm, "end": v(-51.67, 104.03) * mm});
            skLineSegment(sketch, "E1315", {"start": v(-51.67, 104.03) * mm, "end": v(-51.64, 103.69) * mm});
            skLineSegment(sketch, "E1316", {"start": v(-51.64, 103.69) * mm, "end": v(-51.61, 103.35) * mm});
            skLineSegment(sketch, "E1317", {"start": v(-51.61, 103.35) * mm, "end": v(-51.58, 103.03) * mm});
            skLineSegment(sketch, "E1318", {"start": v(-51.58, 103.03) * mm, "end": v(-51.55, 102.7) * mm});
            skLineSegment(sketch, "E1319", {"start": v(-51.55, 102.7) * mm, "end": v(-51.52, 102.4) * mm});
            skLineSegment(sketch, "E1320", {"start": v(-51.52, 102.4) * mm, "end": v(-51.49, 102.09) * mm});
            skLineSegment(sketch, "E1321", {"start": v(-51.49, 102.09) * mm, "end": v(-51.45, 101.79) * mm});
            skLineSegment(sketch, "E1322", {"start": v(-51.45, 101.79) * mm, "end": v(-51.41, 101.5) * mm});
            skLineSegment(sketch, "E1323", {"start": v(-51.41, 101.5) * mm, "end": v(-51.37, 101.2) * mm});
            skLineSegment(sketch, "E1324", {"start": v(-51.37, 101.2) * mm, "end": v(-51.33, 100.93) * mm});
            skLineSegment(sketch, "E1325", {"start": v(-51.33, 100.93) * mm, "end": v(-51.3, 100.65) * mm});
            skLineSegment(sketch, "E1326", {"start": v(-51.3, 100.65) * mm, "end": v(-51.25, 100.39) * mm});
            skLineSegment(sketch, "E1327", {"start": v(-51.25, 100.39) * mm, "end": v(-51.2, 100.13) * mm});
            skLineSegment(sketch, "E1328", {"start": v(-51.2, 100.13) * mm, "end": v(-51.16, 99.87) * mm});
            skLineSegment(sketch, "E1329", {"start": v(-51.16, 99.87) * mm, "end": v(-51.12, 99.63) * mm});
            skLineSegment(sketch, "E1330", {"start": v(-51.12, 99.63) * mm, "end": v(-51.07, 99.39) * mm});
            skLineSegment(sketch, "E1331", {"start": v(-51.07, 99.39) * mm, "end": v(-51.02, 99.16) * mm});
            skLineSegment(sketch, "E1332", {"start": v(-51.02, 99.16) * mm, "end": v(-50.98, 98.93) * mm});
            skLineSegment(sketch, "E1333", {"start": v(-50.98, 98.93) * mm, "end": v(-50.93, 98.7) * mm});
            skLineSegment(sketch, "E1334", {"start": v(-50.93, 98.7) * mm, "end": v(-50.88, 98.5) * mm});
            skLineSegment(sketch, "E1335", {"start": v(-50.88, 98.5) * mm, "end": v(-50.83, 98.3) * mm});
            skLineSegment(sketch, "E1336", {"start": v(-50.83, 98.3) * mm, "end": v(-50.78, 98.1) * mm});
            skLineSegment(sketch, "E1337", {"start": v(-50.78, 98.1) * mm, "end": v(-50.74, 97.9) * mm});
            skLineSegment(sketch, "E1338", {"start": v(-50.74, 97.9) * mm, "end": v(-50.69, 97.71) * mm});
            skLineSegment(sketch, "E1339", {"start": v(-50.69, 97.71) * mm, "end": v(-50.64, 97.53) * mm});
            skLineSegment(sketch, "E1340", {"start": v(-50.64, 97.53) * mm, "end": v(-50.6, 97.36) * mm});
            skLineSegment(sketch, "E1341", {"start": v(-50.6, 97.36) * mm, "end": v(-50.55, 97.2) * mm});
            skLineSegment(sketch, "E1342", {"start": v(-50.55, 97.2) * mm, "end": v(-50.5, 97.03) * mm});
            skLineSegment(sketch, "E1343", {"start": v(-50.5, 97.03) * mm, "end": v(-50.45, 96.88) * mm});
            skLineSegment(sketch, "E1344", {"start": v(-50.45, 96.88) * mm, "end": v(-50.4, 96.73) * mm});
            skLineSegment(sketch, "E1345", {"start": v(-50.4, 96.73) * mm, "end": v(-50.37, 96.6) * mm});
            skLineSegment(sketch, "E1346", {"start": v(-50.37, 96.6) * mm, "end": v(-50.32, 96.46) * mm});
            skLineSegment(sketch, "E1347", {"start": v(-50.32, 96.46) * mm, "end": v(-50.28, 96.33) * mm});
            skLineSegment(sketch, "E1348", {"start": v(-50.28, 96.33) * mm, "end": v(-50.28, 96.03) * mm});
            skLineSegment(sketch, "E1349", {"start": v(-50.28, 96.03) * mm, "end": v(-54.2, 93.88) * mm});
            skLineSegment(sketch, "E1350", {"start": v(-54.2, 93.88) * mm, "end": v(-54.45, 94.04) * mm});
            skLineSegment(sketch, "E1351", {"start": v(-54.45, 94.04) * mm, "end": v(-54.53, 94.14) * mm});
            skLineSegment(sketch, "E1352", {"start": v(-54.53, 94.14) * mm, "end": v(-54.62, 94.25) * mm});
            skLineSegment(sketch, "E1353", {"start": v(-54.62, 94.25) * mm, "end": v(-54.72, 94.36) * mm});
            skLineSegment(sketch, "E1354", {"start": v(-54.72, 94.36) * mm, "end": v(-54.82, 94.48) * mm});
            skLineSegment(sketch, "E1355", {"start": v(-54.82, 94.48) * mm, "end": v(-54.92, 94.6) * mm});
            skLineSegment(sketch, "E1356", {"start": v(-54.92, 94.6) * mm, "end": v(-55.03, 94.73) * mm});
            skLineSegment(sketch, "E1357", {"start": v(-55.03, 94.73) * mm, "end": v(-55.15, 94.85) * mm});
            skLineSegment(sketch, "E1358", {"start": v(-55.15, 94.85) * mm, "end": v(-55.27, 94.99) * mm});
            skLineSegment(sketch, "E1359", {"start": v(-55.27, 94.99) * mm, "end": v(-55.4, 95.12) * mm});
            skLineSegment(sketch, "E1360", {"start": v(-55.4, 95.12) * mm, "end": v(-55.53, 95.26) * mm});
            skLineSegment(sketch, "E1361", {"start": v(-55.53, 95.26) * mm, "end": v(-55.66, 95.4) * mm});
            skLineSegment(sketch, "E1362", {"start": v(-55.66, 95.4) * mm, "end": v(-55.8, 95.55) * mm});
            skLineSegment(sketch, "E1363", {"start": v(-55.8, 95.55) * mm, "end": v(-55.95, 95.7) * mm});
            skLineSegment(sketch, "E1364", {"start": v(-55.95, 95.7) * mm, "end": v(-56.1, 95.86) * mm});
            skLineSegment(sketch, "E1365", {"start": v(-56.1, 95.86) * mm, "end": v(-56.27, 96.02) * mm});
            skLineSegment(sketch, "E1366", {"start": v(-56.27, 96.02) * mm, "end": v(-56.43, 96.18) * mm});
            skLineSegment(sketch, "E1367", {"start": v(-56.43, 96.18) * mm, "end": v(-56.6, 96.34) * mm});
            skLineSegment(sketch, "E1368", {"start": v(-56.6, 96.34) * mm, "end": v(-56.78, 96.5) * mm});
            skLineSegment(sketch, "E1369", {"start": v(-56.78, 96.5) * mm, "end": v(-56.97, 96.68) * mm});
            skLineSegment(sketch, "E1370", {"start": v(-56.97, 96.68) * mm, "end": v(-57.16, 96.85) * mm});
            skLineSegment(sketch, "E1371", {"start": v(-57.16, 96.85) * mm, "end": v(-57.35, 97.03) * mm});
            skLineSegment(sketch, "E1372", {"start": v(-57.35, 97.03) * mm, "end": v(-57.56, 97.2) * mm});
            skLineSegment(sketch, "E1373", {"start": v(-57.56, 97.2) * mm, "end": v(-57.76, 97.39) * mm});
            skLineSegment(sketch, "E1374", {"start": v(-57.76, 97.39) * mm, "end": v(-57.98, 97.57) * mm});
            skLineSegment(sketch, "E1375", {"start": v(-57.98, 97.57) * mm, "end": v(-58.2, 97.76) * mm});
            skLineSegment(sketch, "E1376", {"start": v(-58.2, 97.76) * mm, "end": v(-58.43, 97.95) * mm});
            skLineSegment(sketch, "E1377", {"start": v(-58.43, 97.95) * mm, "end": v(-58.66, 98.14) * mm});
            skLineSegment(sketch, "E1378", {"start": v(-58.66, 98.14) * mm, "end": v(-58.9, 98.33) * mm});
            skLineSegment(sketch, "E1379", {"start": v(-58.9, 98.33) * mm, "end": v(-59.15, 98.53) * mm});
            skLineSegment(sketch, "E1380", {"start": v(-59.15, 98.53) * mm, "end": v(-59.4, 98.72) * mm});
            skLineSegment(sketch, "E1381", {"start": v(-59.4, 98.72) * mm, "end": v(-59.66, 98.92) * mm});
            skLineSegment(sketch, "E1382", {"start": v(-59.66, 98.92) * mm, "end": v(-59.93, 99.12) * mm});
            skLineSegment(sketch, "E1383", {"start": v(-59.93, 99.12) * mm, "end": v(-60.2, 99.33) * mm});
            skLineSegment(sketch, "E1384", {"start": v(-60.2, 99.33) * mm, "end": v(-60.49, 99.53) * mm});
            skLineSegment(sketch, "E1385", {"start": v(-60.49, 99.53) * mm, "end": v(-60.77, 99.74) * mm});
            skLineSegment(sketch, "E1386", {"start": v(-60.77, 99.74) * mm, "end": v(-61.07, 99.95) * mm});
            skLineSegment(sketch, "E1387", {"start": v(-61.07, 99.95) * mm, "end": v(-61.37, 100.16) * mm});
            skLineSegment(sketch, "E1388", {"start": v(-61.37, 100.16) * mm, "end": v(-61.68, 100.37) * mm});
            skLineSegment(sketch, "E1389", {"start": v(-61.68, 100.37) * mm, "end": v(-62, 100.58) * mm});
            skLineSegment(sketch, "E1390", {"start": v(-62, 100.58) * mm, "end": v(-62.31, 100.8) * mm});
            skLineSegment(sketch, "E1391", {"start": v(-62.31, 100.8) * mm, "end": v(-62.64, 101) * mm});
            skLineSegment(sketch, "E1392", {"start": v(-62.64, 101) * mm, "end": v(-62.98, 101.22) * mm});
            skLineSegment(sketch, "E1393", {"start": v(-62.98, 101.22) * mm, "end": v(-63.19, 101.22) * mm});
            skLineSegment(sketch, "E1394", {"start": v(-63.19, 101.22) * mm, "end": v(-66.14, 99.31) * mm});
            skLineSegment(sketch, "E1395", {"start": v(-66.14, 99.31) * mm, "end": v(-66.23, 99.13) * mm});
            skLineSegment(sketch, "E1396", {"start": v(-66.23, 99.13) * mm, "end": v(-66.17, 98.73) * mm});
            skLineSegment(sketch, "E1397", {"start": v(-66.17, 98.73) * mm, "end": v(-66.1, 98.34) * mm});
            skLineSegment(sketch, "E1398", {"start": v(-66.1, 98.34) * mm, "end": v(-66.05, 97.96) * mm});
            skLineSegment(sketch, "E1399", {"start": v(-66.05, 97.96) * mm, "end": v(-65.99, 97.59) * mm});
            skLineSegment(sketch, "E1400", {"start": v(-65.99, 97.59) * mm, "end": v(-65.92, 97.22) * mm});
            skLineSegment(sketch, "E1401", {"start": v(-65.92, 97.22) * mm, "end": v(-65.85, 96.86) * mm});
            skLineSegment(sketch, "E1402", {"start": v(-65.85, 96.86) * mm, "end": v(-65.79, 96.5) * mm});
            skLineSegment(sketch, "E1403", {"start": v(-65.79, 96.5) * mm, "end": v(-65.72, 96.16) * mm});
            skLineSegment(sketch, "E1404", {"start": v(-65.72, 96.16) * mm, "end": v(-65.65, 95.82) * mm});
            skLineSegment(sketch, "E1405", {"start": v(-65.65, 95.82) * mm, "end": v(-65.57, 95.48) * mm});
            skLineSegment(sketch, "E1406", {"start": v(-65.57, 95.48) * mm, "end": v(-65.5, 95.16) * mm});
            skLineSegment(sketch, "E1407", {"start": v(-65.5, 95.16) * mm, "end": v(-65.43, 94.84) * mm});
            skLineSegment(sketch, "E1408", {"start": v(-65.43, 94.84) * mm, "end": v(-65.35, 94.53) * mm});
            skLineSegment(sketch, "E1409", {"start": v(-65.35, 94.53) * mm, "end": v(-65.28, 94.22) * mm});
            skLineSegment(sketch, "E1410", {"start": v(-65.28, 94.22) * mm, "end": v(-65.2, 93.92) * mm});
            skLineSegment(sketch, "E1411", {"start": v(-65.2, 93.92) * mm, "end": v(-65.12, 93.63) * mm});
            skLineSegment(sketch, "E1412", {"start": v(-65.12, 93.63) * mm, "end": v(-65.04, 93.34) * mm});
            skLineSegment(sketch, "E1413", {"start": v(-65.04, 93.34) * mm, "end": v(-64.96, 93.07) * mm});
            skLineSegment(sketch, "E1414", {"start": v(-64.96, 93.07) * mm, "end": v(-64.89, 92.8) * mm});
            skLineSegment(sketch, "E1415", {"start": v(-64.89, 92.8) * mm, "end": v(-64.8, 92.53) * mm});
            skLineSegment(sketch, "E1416", {"start": v(-64.8, 92.53) * mm, "end": v(-64.73, 92.27) * mm});
            skLineSegment(sketch, "E1417", {"start": v(-64.73, 92.27) * mm, "end": v(-64.65, 92.02) * mm});
            skLineSegment(sketch, "E1418", {"start": v(-64.65, 92.02) * mm, "end": v(-64.57, 91.78) * mm});
            skLineSegment(sketch, "E1419", {"start": v(-64.57, 91.78) * mm, "end": v(-64.49, 91.54) * mm});
            skLineSegment(sketch, "E1420", {"start": v(-64.49, 91.54) * mm, "end": v(-64.41, 91.3) * mm});
            skLineSegment(sketch, "E1421", {"start": v(-64.41, 91.3) * mm, "end": v(-64.33, 91.08) * mm});
            skLineSegment(sketch, "E1422", {"start": v(-64.33, 91.08) * mm, "end": v(-64.25, 90.87) * mm});
            skLineSegment(sketch, "E1423", {"start": v(-64.25, 90.87) * mm, "end": v(-64.18, 90.65) * mm});
            skLineSegment(sketch, "E1424", {"start": v(-64.18, 90.65) * mm, "end": v(-64.1, 90.45) * mm});
            skLineSegment(sketch, "E1425", {"start": v(-64.1, 90.45) * mm, "end": v(-64.02, 90.25) * mm});
            skLineSegment(sketch, "E1426", {"start": v(-64.02, 90.25) * mm, "end": v(-63.95, 90.06) * mm});
            skLineSegment(sketch, "E1427", {"start": v(-63.95, 90.06) * mm, "end": v(-63.87, 89.88) * mm});
            skLineSegment(sketch, "E1428", {"start": v(-63.87, 89.88) * mm, "end": v(-63.8, 89.7) * mm});
            skLineSegment(sketch, "E1429", {"start": v(-63.8, 89.7) * mm, "end": v(-63.73, 89.53) * mm});
            skLineSegment(sketch, "E1430", {"start": v(-63.73, 89.53) * mm, "end": v(-63.66, 89.37) * mm});
            skLineSegment(sketch, "E1431", {"start": v(-63.66, 89.37) * mm, "end": v(-63.59, 89.2) * mm});
            skLineSegment(sketch, "E1432", {"start": v(-63.59, 89.2) * mm, "end": v(-63.52, 89.06) * mm});
            skLineSegment(sketch, "E1433", {"start": v(-63.52, 89.06) * mm, "end": v(-63.45, 88.9) * mm});
            skLineSegment(sketch, "E1434", {"start": v(-63.45, 88.9) * mm, "end": v(-63.39, 88.77) * mm});
            skLineSegment(sketch, "E1435", {"start": v(-63.39, 88.77) * mm, "end": v(-63.32, 88.64) * mm});
            skLineSegment(sketch, "E1436", {"start": v(-63.32, 88.64) * mm, "end": v(-63.26, 88.51) * mm});
            skLineSegment(sketch, "E1437", {"start": v(-63.26, 88.51) * mm, "end": v(-63.2, 88.4) * mm});
            skLineSegment(sketch, "E1438", {"start": v(-63.2, 88.4) * mm, "end": v(-63.16, 88.1) * mm});
            skLineSegment(sketch, "E1439", {"start": v(-63.16, 88.1) * mm, "end": v(-66.74, 85.42) * mm});
            skLineSegment(sketch, "E1440", {"start": v(-66.74, 85.42) * mm, "end": v(-67.01, 85.54) * mm});
            skLineSegment(sketch, "E1441", {"start": v(-67.01, 85.54) * mm, "end": v(-67.1, 85.63) * mm});
            skLineSegment(sketch, "E1442", {"start": v(-67.1, 85.63) * mm, "end": v(-67.21, 85.73) * mm});
            skLineSegment(sketch, "E1443", {"start": v(-67.21, 85.73) * mm, "end": v(-67.32, 85.82) * mm});
            skLineSegment(sketch, "E1444", {"start": v(-67.32, 85.82) * mm, "end": v(-67.44, 85.93) * mm});
            skLineSegment(sketch, "E1445", {"start": v(-67.44, 85.93) * mm, "end": v(-67.56, 86.03) * mm});
            skLineSegment(sketch, "E1446", {"start": v(-67.56, 86.03) * mm, "end": v(-67.69, 86.14) * mm});
            skLineSegment(sketch, "E1447", {"start": v(-67.69, 86.14) * mm, "end": v(-67.82, 86.25) * mm});
            skLineSegment(sketch, "E1448", {"start": v(-67.82, 86.25) * mm, "end": v(-67.96, 86.37) * mm});
            skLineSegment(sketch, "E1449", {"start": v(-67.96, 86.37) * mm, "end": v(-68.1, 86.48) * mm});
            skLineSegment(sketch, "E1450", {"start": v(-68.1, 86.48) * mm, "end": v(-68.25, 86.6) * mm});
            skLineSegment(sketch, "E1451", {"start": v(-68.25, 86.6) * mm, "end": v(-68.4, 86.73) * mm});
            skLineSegment(sketch, "E1452", {"start": v(-68.4, 86.73) * mm, "end": v(-68.57, 86.85) * mm});
            skLineSegment(sketch, "E1453", {"start": v(-68.57, 86.85) * mm, "end": v(-68.74, 86.98) * mm});
            skLineSegment(sketch, "E1454", {"start": v(-68.74, 86.98) * mm, "end": v(-68.9, 87.11) * mm});
            skLineSegment(sketch, "E1455", {"start": v(-68.9, 87.11) * mm, "end": v(-69.1, 87.25) * mm});
            skLineSegment(sketch, "E1456", {"start": v(-69.1, 87.25) * mm, "end": v(-69.28, 87.38) * mm});
            skLineSegment(sketch, "E1457", {"start": v(-69.28, 87.38) * mm, "end": v(-69.47, 87.52) * mm});
            skLineSegment(sketch, "E1458", {"start": v(-69.47, 87.52) * mm, "end": v(-69.67, 87.66) * mm});
            skLineSegment(sketch, "E1459", {"start": v(-69.67, 87.66) * mm, "end": v(-69.87, 87.8) * mm});
            skLineSegment(sketch, "E1460", {"start": v(-69.87, 87.8) * mm, "end": v(-70.09, 87.95) * mm});
            skLineSegment(sketch, "E1461", {"start": v(-70.09, 87.95) * mm, "end": v(-70.3, 88.1) * mm});
            skLineSegment(sketch, "E1462", {"start": v(-70.3, 88.1) * mm, "end": v(-70.53, 88.25) * mm});
            skLineSegment(sketch, "E1463", {"start": v(-70.53, 88.25) * mm, "end": v(-70.76, 88.4) * mm});
            skLineSegment(sketch, "E1464", {"start": v(-70.76, 88.4) * mm, "end": v(-71, 88.55) * mm});
            skLineSegment(sketch, "E1465", {"start": v(-71, 88.55) * mm, "end": v(-71.25, 88.7) * mm});
            skLineSegment(sketch, "E1466", {"start": v(-71.25, 88.7) * mm, "end": v(-71.5, 88.86) * mm});
            skLineSegment(sketch, "E1467", {"start": v(-71.5, 88.86) * mm, "end": v(-71.76, 89.01) * mm});
            skLineSegment(sketch, "E1468", {"start": v(-71.76, 89.01) * mm, "end": v(-72.02, 89.17) * mm});
            skLineSegment(sketch, "E1469", {"start": v(-72.02, 89.17) * mm, "end": v(-72.3, 89.33) * mm});
            skLineSegment(sketch, "E1470", {"start": v(-72.3, 89.33) * mm, "end": v(-72.57, 89.49) * mm});
            skLineSegment(sketch, "E1471", {"start": v(-72.57, 89.49) * mm, "end": v(-72.86, 89.65) * mm});
            skLineSegment(sketch, "E1472", {"start": v(-72.86, 89.65) * mm, "end": v(-73.15, 89.81) * mm});
            skLineSegment(sketch, "E1473", {"start": v(-73.15, 89.81) * mm, "end": v(-73.45, 89.98) * mm});
            skLineSegment(sketch, "E1474", {"start": v(-73.45, 89.98) * mm, "end": v(-73.76, 90.14) * mm});
            skLineSegment(sketch, "E1475", {"start": v(-73.76, 90.14) * mm, "end": v(-74.07, 90.3) * mm});
            skLineSegment(sketch, "E1476", {"start": v(-74.07, 90.3) * mm, "end": v(-74.39, 90.47) * mm});
            skLineSegment(sketch, "E1477", {"start": v(-74.39, 90.47) * mm, "end": v(-74.72, 90.63) * mm});
            skLineSegment(sketch, "E1478", {"start": v(-74.72, 90.63) * mm, "end": v(-75.05, 90.8) * mm});
            skLineSegment(sketch, "E1479", {"start": v(-75.05, 90.8) * mm, "end": v(-75.4, 90.97) * mm});
            skLineSegment(sketch, "E1480", {"start": v(-75.4, 90.97) * mm, "end": v(-75.74, 91.13) * mm});
            skLineSegment(sketch, "E1481", {"start": v(-75.74, 91.13) * mm, "end": v(-76.1, 91.3) * mm});
            skLineSegment(sketch, "E1482", {"start": v(-76.1, 91.3) * mm, "end": v(-76.46, 91.46) * mm});
            skLineSegment(sketch, "E1483", {"start": v(-76.46, 91.46) * mm, "end": v(-76.66, 91.43) * mm});
            skLineSegment(sketch, "E1484", {"start": v(-76.66, 91.43) * mm, "end": v(-79.32, 89.14) * mm});
            skLineSegment(sketch, "E1485", {"start": v(-79.32, 89.14) * mm, "end": v(-79.38, 88.94) * mm});
            skLineSegment(sketch, "E1486", {"start": v(-79.38, 88.94) * mm, "end": v(-79.27, 88.56) * mm});
            skLineSegment(sketch, "E1487", {"start": v(-79.27, 88.56) * mm, "end": v(-79.16, 88.18) * mm});
            skLineSegment(sketch, "E1488", {"start": v(-79.16, 88.18) * mm, "end": v(-79.05, 87.81) * mm});
            skLineSegment(sketch, "E1489", {"start": v(-79.05, 87.81) * mm, "end": v(-78.93, 87.45) * mm});
            skLineSegment(sketch, "E1490", {"start": v(-78.93, 87.45) * mm, "end": v(-78.82, 87.1) * mm});
            skLineSegment(sketch, "E1491", {"start": v(-78.82, 87.1) * mm, "end": v(-78.7, 86.75) * mm});
            skLineSegment(sketch, "E1492", {"start": v(-78.7, 86.75) * mm, "end": v(-78.58, 86.4) * mm});
            skLineSegment(sketch, "E1493", {"start": v(-78.58, 86.4) * mm, "end": v(-78.47, 86.07) * mm});
            skLineSegment(sketch, "E1494", {"start": v(-78.47, 86.07) * mm, "end": v(-78.35, 85.74) * mm});
            skLineSegment(sketch, "E1495", {"start": v(-78.35, 85.74) * mm, "end": v(-78.23, 85.42) * mm});
            skLineSegment(sketch, "E1496", {"start": v(-78.23, 85.42) * mm, "end": v(-78.11, 85.11) * mm});
            skLineSegment(sketch, "E1497", {"start": v(-78.11, 85.11) * mm, "end": v(-78, 84.8) * mm});
            skLineSegment(sketch, "E1498", {"start": v(-78, 84.8) * mm, "end": v(-77.88, 84.5) * mm});
            skLineSegment(sketch, "E1499", {"start": v(-77.88, 84.5) * mm, "end": v(-77.76, 84.21) * mm});
            skLineSegment(sketch, "E1500", {"start": v(-77.76, 84.21) * mm, "end": v(-77.64, 83.93) * mm});
            skLineSegment(sketch, "E1501", {"start": v(-77.64, 83.93) * mm, "end": v(-77.52, 83.65) * mm});
            skLineSegment(sketch, "E1502", {"start": v(-77.52, 83.65) * mm, "end": v(-77.4, 83.38) * mm});
            skLineSegment(sketch, "E1503", {"start": v(-77.4, 83.38) * mm, "end": v(-77.3, 83.11) * mm});
            skLineSegment(sketch, "E1504", {"start": v(-77.3, 83.11) * mm, "end": v(-77.18, 82.86) * mm});
            skLineSegment(sketch, "E1505", {"start": v(-77.18, 82.86) * mm, "end": v(-77.06, 82.6) * mm});
            skLineSegment(sketch, "E1506", {"start": v(-77.06, 82.6) * mm, "end": v(-76.95, 82.36) * mm});
            skLineSegment(sketch, "E1507", {"start": v(-76.95, 82.36) * mm, "end": v(-76.83, 82.12) * mm});
            skLineSegment(sketch, "E1508", {"start": v(-76.83, 82.12) * mm, "end": v(-76.72, 81.9) * mm});
            skLineSegment(sketch, "E1509", {"start": v(-76.72, 81.9) * mm, "end": v(-76.6, 81.67) * mm});
            skLineSegment(sketch, "E1510", {"start": v(-76.6, 81.67) * mm, "end": v(-76.5, 81.45) * mm});
            skLineSegment(sketch, "E1511", {"start": v(-76.5, 81.45) * mm, "end": v(-76.39, 81.24) * mm});
            skLineSegment(sketch, "E1512", {"start": v(-76.39, 81.24) * mm, "end": v(-76.28, 81.03) * mm});
            skLineSegment(sketch, "E1513", {"start": v(-76.28, 81.03) * mm, "end": v(-76.18, 80.84) * mm});
            skLineSegment(sketch, "E1514", {"start": v(-76.18, 80.84) * mm, "end": v(-76.07, 80.64) * mm});
            skLineSegment(sketch, "E1515", {"start": v(-76.07, 80.64) * mm, "end": v(-75.97, 80.46) * mm});
            skLineSegment(sketch, "E1516", {"start": v(-75.97, 80.46) * mm, "end": v(-75.87, 80.28) * mm});
            skLineSegment(sketch, "E1517", {"start": v(-75.87, 80.28) * mm, "end": v(-75.77, 80.1) * mm});
            skLineSegment(sketch, "E1518", {"start": v(-75.77, 80.1) * mm, "end": v(-75.67, 79.94) * mm});
            skLineSegment(sketch, "E1519", {"start": v(-75.67, 79.94) * mm, "end": v(-75.58, 79.78) * mm});
            skLineSegment(sketch, "E1520", {"start": v(-75.58, 79.78) * mm, "end": v(-75.48, 79.63) * mm});
            skLineSegment(sketch, "E1521", {"start": v(-75.48, 79.63) * mm, "end": v(-75.4, 79.48) * mm});
            skLineSegment(sketch, "E1522", {"start": v(-75.4, 79.48) * mm, "end": v(-75.3, 79.34) * mm});
            skLineSegment(sketch, "E1523", {"start": v(-75.3, 79.34) * mm, "end": v(-75.22, 79.2) * mm});
            skLineSegment(sketch, "E1524", {"start": v(-75.22, 79.2) * mm, "end": v(-75.13, 79.08) * mm});
            skLineSegment(sketch, "E1525", {"start": v(-75.13, 79.08) * mm, "end": v(-75.05, 78.96) * mm});
            skLineSegment(sketch, "E1526", {"start": v(-75.05, 78.96) * mm, "end": v(-74.97, 78.84) * mm});
            skLineSegment(sketch, "E1527", {"start": v(-74.97, 78.84) * mm, "end": v(-74.9, 78.73) * mm});
            skLineSegment(sketch, "E1528", {"start": v(-74.9, 78.73) * mm, "end": v(-74.81, 78.44) * mm});
            skLineSegment(sketch, "E1529", {"start": v(-74.81, 78.44) * mm, "end": v(-77.98, 75.3) * mm});
            skLineSegment(sketch, "E1530", {"start": v(-77.98, 75.3) * mm, "end": v(-78.27, 75.38) * mm});
            skLineSegment(sketch, "E1531", {"start": v(-78.27, 75.38) * mm, "end": v(-78.38, 75.45) * mm});
            skLineSegment(sketch, "E1532", {"start": v(-78.38, 75.45) * mm, "end": v(-78.5, 75.53) * mm});
            skLineSegment(sketch, "E1533", {"start": v(-78.5, 75.53) * mm, "end": v(-78.62, 75.61) * mm});
            skLineSegment(sketch, "E1534", {"start": v(-78.62, 75.61) * mm, "end": v(-78.75, 75.7) * mm});
            skLineSegment(sketch, "E1535", {"start": v(-78.75, 75.7) * mm, "end": v(-78.88, 75.79) * mm});
            skLineSegment(sketch, "E1536", {"start": v(-78.88, 75.79) * mm, "end": v(-79.02, 75.88) * mm});
            skLineSegment(sketch, "E1537", {"start": v(-79.02, 75.88) * mm, "end": v(-79.17, 75.97) * mm});
            skLineSegment(sketch, "E1538", {"start": v(-79.17, 75.97) * mm, "end": v(-79.32, 76.06) * mm});
            skLineSegment(sketch, "E1539", {"start": v(-79.32, 76.06) * mm, "end": v(-79.48, 76.16) * mm});
            skLineSegment(sketch, "E1540", {"start": v(-79.48, 76.16) * mm, "end": v(-79.64, 76.26) * mm});
            skLineSegment(sketch, "E1541", {"start": v(-79.64, 76.26) * mm, "end": v(-79.82, 76.36) * mm});
            skLineSegment(sketch, "E1542", {"start": v(-79.82, 76.36) * mm, "end": v(-80, 76.46) * mm});
            skLineSegment(sketch, "E1543", {"start": v(-80, 76.46) * mm, "end": v(-80.18, 76.56) * mm});
            skLineSegment(sketch, "E1544", {"start": v(-80.18, 76.56) * mm, "end": v(-80.37, 76.67) * mm});
            skLineSegment(sketch, "E1545", {"start": v(-80.37, 76.67) * mm, "end": v(-80.57, 76.78) * mm});
            skLineSegment(sketch, "E1546", {"start": v(-80.57, 76.78) * mm, "end": v(-80.77, 76.89) * mm});
            skLineSegment(sketch, "E1547", {"start": v(-80.77, 76.89) * mm, "end": v(-80.98, 77) * mm});
            skLineSegment(sketch, "E1548", {"start": v(-80.98, 77) * mm, "end": v(-81.2, 77.1) * mm});
            skLineSegment(sketch, "E1549", {"start": v(-81.2, 77.1) * mm, "end": v(-81.42, 77.22) * mm});
            skLineSegment(sketch, "E1550", {"start": v(-81.42, 77.22) * mm, "end": v(-81.65, 77.33) * mm});
            skLineSegment(sketch, "E1551", {"start": v(-81.65, 77.33) * mm, "end": v(-81.89, 77.45) * mm});
            skLineSegment(sketch, "E1552", {"start": v(-81.89, 77.45) * mm, "end": v(-82.13, 77.56) * mm});
            skLineSegment(sketch, "E1553", {"start": v(-82.13, 77.56) * mm, "end": v(-82.38, 77.68) * mm});
            skLineSegment(sketch, "E1554", {"start": v(-82.38, 77.68) * mm, "end": v(-82.64, 77.8) * mm});
            skLineSegment(sketch, "E1555", {"start": v(-82.64, 77.8) * mm, "end": v(-82.9, 77.92) * mm});
            skLineSegment(sketch, "E1556", {"start": v(-82.9, 77.92) * mm, "end": v(-83.17, 78.04) * mm});
            skLineSegment(sketch, "E1557", {"start": v(-83.17, 78.04) * mm, "end": v(-83.45, 78.15) * mm});
            skLineSegment(sketch, "E1558", {"start": v(-83.45, 78.15) * mm, "end": v(-83.74, 78.27) * mm});
            skLineSegment(sketch, "E1559", {"start": v(-83.74, 78.27) * mm, "end": v(-84.03, 78.4) * mm});
            skLineSegment(sketch, "E1560", {"start": v(-84.03, 78.4) * mm, "end": v(-84.33, 78.51) * mm});
            skLineSegment(sketch, "E1561", {"start": v(-84.33, 78.51) * mm, "end": v(-84.63, 78.63) * mm});
            skLineSegment(sketch, "E1562", {"start": v(-84.63, 78.63) * mm, "end": v(-84.94, 78.75) * mm});
            skLineSegment(sketch, "E1563", {"start": v(-84.94, 78.75) * mm, "end": v(-85.26, 78.87) * mm});
            skLineSegment(sketch, "E1564", {"start": v(-85.26, 78.87) * mm, "end": v(-85.59, 79) * mm});
            skLineSegment(sketch, "E1565", {"start": v(-85.59, 79) * mm, "end": v(-85.92, 79.11) * mm});
            skLineSegment(sketch, "E1566", {"start": v(-85.92, 79.11) * mm, "end": v(-86.26, 79.23) * mm});
            skLineSegment(sketch, "E1567", {"start": v(-86.26, 79.23) * mm, "end": v(-86.61, 79.35) * mm});
            skLineSegment(sketch, "E1568", {"start": v(-86.61, 79.35) * mm, "end": v(-86.96, 79.47) * mm});
            skLineSegment(sketch, "E1569", {"start": v(-86.96, 79.47) * mm, "end": v(-87.33, 79.58) * mm});
            skLineSegment(sketch, "E1570", {"start": v(-87.33, 79.58) * mm, "end": v(-87.7, 79.7) * mm});
            skLineSegment(sketch, "E1571", {"start": v(-87.7, 79.7) * mm, "end": v(-88.07, 79.81) * mm});
            skLineSegment(sketch, "E1572", {"start": v(-88.07, 79.81) * mm, "end": v(-88.45, 79.93) * mm});
            skLineSegment(sketch, "E1573", {"start": v(-88.45, 79.93) * mm, "end": v(-88.65, 79.87) * mm});
            skLineSegment(sketch, "E1574", {"start": v(-88.65, 79.87) * mm, "end": v(-90.96, 77.22) * mm});
            skLineSegment(sketch, "E1575", {"start": v(-90.96, 77.22) * mm, "end": v(-91, 77.02) * mm});
            skLineSegment(sketch, "E1576", {"start": v(-91, 77.02) * mm, "end": v(-90.83, 76.66) * mm});
            skLineSegment(sketch, "E1577", {"start": v(-90.83, 76.66) * mm, "end": v(-90.67, 76.3) * mm});
            skLineSegment(sketch, "E1578", {"start": v(-90.67, 76.3) * mm, "end": v(-90.5, 75.95) * mm});
            skLineSegment(sketch, "E1579", {"start": v(-90.5, 75.95) * mm, "end": v(-90.34, 75.6) * mm});
            skLineSegment(sketch, "E1580", {"start": v(-90.34, 75.6) * mm, "end": v(-90.18, 75.27) * mm});
            skLineSegment(sketch, "E1581", {"start": v(-90.18, 75.27) * mm, "end": v(-90.01, 74.94) * mm});
            skLineSegment(sketch, "E1582", {"start": v(-90.01, 74.94) * mm, "end": v(-89.85, 74.62) * mm});
            skLineSegment(sketch, "E1583", {"start": v(-89.85, 74.62) * mm, "end": v(-89.69, 74.3) * mm});
            skLineSegment(sketch, "E1584", {"start": v(-89.69, 74.3) * mm, "end": v(-89.53, 74) * mm});
            skLineSegment(sketch, "E1585", {"start": v(-89.53, 74) * mm, "end": v(-89.37, 73.7) * mm});
            skLineSegment(sketch, "E1586", {"start": v(-89.37, 73.7) * mm, "end": v(-89.2, 73.4) * mm});
            skLineSegment(sketch, "E1587", {"start": v(-89.2, 73.4) * mm, "end": v(-89.05, 73.12) * mm});
            skLineSegment(sketch, "E1588", {"start": v(-89.05, 73.12) * mm, "end": v(-88.89, 72.84) * mm});
            skLineSegment(sketch, "E1589", {"start": v(-88.89, 72.84) * mm, "end": v(-88.73, 72.57) * mm});
            skLineSegment(sketch, "E1590", {"start": v(-88.73, 72.57) * mm, "end": v(-88.57, 72.3) * mm});
            skLineSegment(sketch, "E1591", {"start": v(-88.57, 72.3) * mm, "end": v(-88.42, 72.04) * mm});
            skLineSegment(sketch, "E1592", {"start": v(-88.42, 72.04) * mm, "end": v(-88.26, 71.79) * mm});
            skLineSegment(sketch, "E1593", {"start": v(-88.26, 71.79) * mm, "end": v(-88.11, 71.54) * mm});
            skLineSegment(sketch, "E1594", {"start": v(-88.11, 71.54) * mm, "end": v(-87.96, 71.3) * mm});
            skLineSegment(sketch, "E1595", {"start": v(-87.96, 71.3) * mm, "end": v(-87.81, 71.07) * mm});
            skLineSegment(sketch, "E1596", {"start": v(-87.81, 71.07) * mm, "end": v(-87.67, 70.84) * mm});
            skLineSegment(sketch, "E1597", {"start": v(-87.67, 70.84) * mm, "end": v(-87.52, 70.63) * mm});
            skLineSegment(sketch, "E1598", {"start": v(-87.52, 70.63) * mm, "end": v(-87.38, 70.41) * mm});
            skLineSegment(sketch, "E1599", {"start": v(-87.38, 70.41) * mm, "end": v(-87.24, 70.2) * mm});
            skLineSegment(sketch, "E1600", {"start": v(-87.24, 70.2) * mm, "end": v(-87.1, 70) * mm});
            skLineSegment(sketch, "E1601", {"start": v(-87.1, 70) * mm, "end": v(-86.96, 69.81) * mm});
            skLineSegment(sketch, "E1602", {"start": v(-86.96, 69.81) * mm, "end": v(-86.82, 69.62) * mm});
            skLineSegment(sketch, "E1603", {"start": v(-86.82, 69.62) * mm, "end": v(-86.7, 69.44) * mm});
            skLineSegment(sketch, "E1604", {"start": v(-86.7, 69.44) * mm, "end": v(-86.56, 69.27) * mm});
            skLineSegment(sketch, "E1605", {"start": v(-86.56, 69.27) * mm, "end": v(-86.43, 69.1) * mm});
            skLineSegment(sketch, "E1606", {"start": v(-86.43, 69.1) * mm, "end": v(-86.3, 68.94) * mm});
            skLineSegment(sketch, "E1607", {"start": v(-86.3, 68.94) * mm, "end": v(-86.19, 68.78) * mm});
            skLineSegment(sketch, "E1608", {"start": v(-86.19, 68.78) * mm, "end": v(-86.07, 68.63) * mm});
            skLineSegment(sketch, "E1609", {"start": v(-86.07, 68.63) * mm, "end": v(-85.95, 68.48) * mm});
            skLineSegment(sketch, "E1610", {"start": v(-85.95, 68.48) * mm, "end": v(-85.84, 68.35) * mm});
            skLineSegment(sketch, "E1611", {"start": v(-85.84, 68.35) * mm, "end": v(-85.73, 68.21) * mm});
            skLineSegment(sketch, "E1612", {"start": v(-85.73, 68.21) * mm, "end": v(-85.62, 68.09) * mm});
            skLineSegment(sketch, "E1613", {"start": v(-85.62, 68.09) * mm, "end": v(-85.51, 67.96) * mm});
            skLineSegment(sketch, "E1614", {"start": v(-85.51, 67.96) * mm, "end": v(-85.41, 67.85) * mm});
            skLineSegment(sketch, "E1615", {"start": v(-85.41, 67.85) * mm, "end": v(-85.32, 67.74) * mm});
            skLineSegment(sketch, "E1616", {"start": v(-85.32, 67.74) * mm, "end": v(-85.22, 67.63) * mm});
            skLineSegment(sketch, "E1617", {"start": v(-85.22, 67.63) * mm, "end": v(-85.13, 67.53) * mm});
            skLineSegment(sketch, "E1618", {"start": v(-85.13, 67.53) * mm, "end": v(-85, 67.26) * mm});
            skLineSegment(sketch, "E1619", {"start": v(-85, 67.26) * mm, "end": v(-87.7, 63.7) * mm});
            skLineSegment(sketch, "E1620", {"start": v(-87.7, 63.7) * mm, "end": v(-88, 63.74) * mm});
            skLineSegment(sketch, "E1621", {"start": v(-88, 63.74) * mm, "end": v(-88.13, 63.8) * mm});
            skLineSegment(sketch, "E1622", {"start": v(-88.13, 63.8) * mm, "end": v(-88.25, 63.87) * mm});
            skLineSegment(sketch, "E1623", {"start": v(-88.25, 63.87) * mm, "end": v(-88.38, 63.93) * mm});
            skLineSegment(sketch, "E1624", {"start": v(-88.38, 63.93) * mm, "end": v(-88.52, 64) * mm});
            skLineSegment(sketch, "E1625", {"start": v(-88.52, 64) * mm, "end": v(-88.67, 64.07) * mm});
            skLineSegment(sketch, "E1626", {"start": v(-88.67, 64.07) * mm, "end": v(-88.82, 64.13) * mm});
            skLineSegment(sketch, "E1627", {"start": v(-88.82, 64.13) * mm, "end": v(-88.98, 64.2) * mm});
            skLineSegment(sketch, "E1628", {"start": v(-88.98, 64.2) * mm, "end": v(-89.14, 64.28) * mm});
            skLineSegment(sketch, "E1629", {"start": v(-89.14, 64.28) * mm, "end": v(-89.31, 64.35) * mm});
            skLineSegment(sketch, "E1630", {"start": v(-89.31, 64.35) * mm, "end": v(-89.49, 64.42) * mm});
            skLineSegment(sketch, "E1631", {"start": v(-89.49, 64.42) * mm, "end": v(-89.67, 64.5) * mm});
            skLineSegment(sketch, "E1632", {"start": v(-89.67, 64.5) * mm, "end": v(-89.86, 64.58) * mm});
            skLineSegment(sketch, "E1633", {"start": v(-89.86, 64.58) * mm, "end": v(-90.06, 64.65) * mm});
            skLineSegment(sketch, "E1634", {"start": v(-90.06, 64.65) * mm, "end": v(-90.26, 64.73) * mm});
            skLineSegment(sketch, "E1635", {"start": v(-90.26, 64.73) * mm, "end": v(-90.47, 64.81) * mm});
            skLineSegment(sketch, "E1636", {"start": v(-90.47, 64.81) * mm, "end": v(-90.7, 64.9) * mm});
            skLineSegment(sketch, "E1637", {"start": v(-90.7, 64.9) * mm, "end": v(-90.92, 64.97) * mm});
            skLineSegment(sketch, "E1638", {"start": v(-90.92, 64.97) * mm, "end": v(-91.15, 65.05) * mm});
            skLineSegment(sketch, "E1639", {"start": v(-91.15, 65.05) * mm, "end": v(-91.38, 65.13) * mm});
            skLineSegment(sketch, "E1640", {"start": v(-91.38, 65.13) * mm, "end": v(-91.63, 65.21) * mm});
            skLineSegment(sketch, "E1641", {"start": v(-91.63, 65.21) * mm, "end": v(-91.88, 65.3) * mm});
            skLineSegment(sketch, "E1642", {"start": v(-91.88, 65.3) * mm, "end": v(-92.13, 65.37) * mm});
            skLineSegment(sketch, "E1643", {"start": v(-92.13, 65.37) * mm, "end": v(-92.4, 65.45) * mm});
            skLineSegment(sketch, "E1644", {"start": v(-92.4, 65.45) * mm, "end": v(-92.67, 65.54) * mm});
            skLineSegment(sketch, "E1645", {"start": v(-92.67, 65.54) * mm, "end": v(-92.95, 65.62) * mm});
            skLineSegment(sketch, "E1646", {"start": v(-92.95, 65.62) * mm, "end": v(-93.23, 65.7) * mm});
            skLineSegment(sketch, "E1647", {"start": v(-93.23, 65.7) * mm, "end": v(-93.52, 65.77) * mm});
            skLineSegment(sketch, "E1648", {"start": v(-93.52, 65.77) * mm, "end": v(-93.82, 65.85) * mm});
            skLineSegment(sketch, "E1649", {"start": v(-93.82, 65.85) * mm, "end": v(-94.13, 65.93) * mm});
            skLineSegment(sketch, "E1650", {"start": v(-94.13, 65.93) * mm, "end": v(-94.44, 66) * mm});
            skLineSegment(sketch, "E1651", {"start": v(-94.44, 66) * mm, "end": v(-94.76, 66.08) * mm});
            skLineSegment(sketch, "E1652", {"start": v(-94.76, 66.08) * mm, "end": v(-95.08, 66.16) * mm});
            skLineSegment(sketch, "E1653", {"start": v(-95.08, 66.16) * mm, "end": v(-95.42, 66.23) * mm});
            skLineSegment(sketch, "E1654", {"start": v(-95.42, 66.23) * mm, "end": v(-95.76, 66.3) * mm});
            skLineSegment(sketch, "E1655", {"start": v(-95.76, 66.3) * mm, "end": v(-96.1, 66.38) * mm});
            skLineSegment(sketch, "E1656", {"start": v(-96.1, 66.38) * mm, "end": v(-96.46, 66.45) * mm});
            skLineSegment(sketch, "E1657", {"start": v(-96.46, 66.45) * mm, "end": v(-96.82, 66.52) * mm});
            skLineSegment(sketch, "E1658", {"start": v(-96.82, 66.52) * mm, "end": v(-97.18, 66.58) * mm});
            skLineSegment(sketch, "E1659", {"start": v(-97.18, 66.58) * mm, "end": v(-97.56, 66.65) * mm});
            skLineSegment(sketch, "E1660", {"start": v(-97.56, 66.65) * mm, "end": v(-97.94, 66.71) * mm});
            skLineSegment(sketch, "E1661", {"start": v(-97.94, 66.71) * mm, "end": v(-98.33, 66.77) * mm});
            skLineSegment(sketch, "E1662", {"start": v(-98.33, 66.77) * mm, "end": v(-98.72, 66.83) * mm});
            skLineSegment(sketch, "E1663", {"start": v(-98.72, 66.83) * mm, "end": v(-98.9, 66.75) * mm});
            skLineSegment(sketch, "E1664", {"start": v(-98.9, 66.75) * mm, "end": v(-100.83, 63.8) * mm});
            skLineSegment(sketch, "E1665", {"start": v(-100.83, 63.8) * mm, "end": v(-100.83, 63.6) * mm});
            skLineSegment(sketch, "E1666", {"start": v(-100.83, 63.6) * mm, "end": v(-100.62, 63.26) * mm});
            skLineSegment(sketch, "E1667", {"start": v(-100.62, 63.26) * mm, "end": v(-100.41, 62.93) * mm});
            skLineSegment(sketch, "E1668", {"start": v(-100.41, 62.93) * mm, "end": v(-100.2, 62.6) * mm});
            skLineSegment(sketch, "E1669", {"start": v(-100.2, 62.6) * mm, "end": v(-99.99, 62.3) * mm});
            skLineSegment(sketch, "E1670", {"start": v(-99.99, 62.3) * mm, "end": v(-99.78, 61.98) * mm});
            skLineSegment(sketch, "E1671", {"start": v(-99.78, 61.98) * mm, "end": v(-99.57, 61.68) * mm});
            skLineSegment(sketch, "E1672", {"start": v(-99.57, 61.68) * mm, "end": v(-99.37, 61.39) * mm});
            skLineSegment(sketch, "E1673", {"start": v(-99.37, 61.39) * mm, "end": v(-99.16, 61.1) * mm});
            skLineSegment(sketch, "E1674", {"start": v(-99.16, 61.1) * mm, "end": v(-98.96, 60.81) * mm});
            skLineSegment(sketch, "E1675", {"start": v(-98.96, 60.81) * mm, "end": v(-98.76, 60.54) * mm});
            skLineSegment(sketch, "E1676", {"start": v(-98.76, 60.54) * mm, "end": v(-98.56, 60.27) * mm});
            skLineSegment(sketch, "E1677", {"start": v(-98.56, 60.27) * mm, "end": v(-98.36, 60.01) * mm});
            skLineSegment(sketch, "E1678", {"start": v(-98.36, 60.01) * mm, "end": v(-98.17, 59.75) * mm});
            skLineSegment(sketch, "E1679", {"start": v(-98.17, 59.75) * mm, "end": v(-97.97, 59.5) * mm});
            skLineSegment(sketch, "E1680", {"start": v(-97.97, 59.5) * mm, "end": v(-97.78, 59.26) * mm});
            skLineSegment(sketch, "E1681", {"start": v(-97.78, 59.26) * mm, "end": v(-97.6, 59.03) * mm});
            skLineSegment(sketch, "E1682", {"start": v(-97.6, 59.03) * mm, "end": v(-97.4, 58.8) * mm});
            skLineSegment(sketch, "E1683", {"start": v(-97.4, 58.8) * mm, "end": v(-97.22, 58.58) * mm});
            skLineSegment(sketch, "E1684", {"start": v(-97.22, 58.58) * mm, "end": v(-97.04, 58.36) * mm});
            skLineSegment(sketch, "E1685", {"start": v(-97.04, 58.36) * mm, "end": v(-96.86, 58.15) * mm});
            skLineSegment(sketch, "E1686", {"start": v(-96.86, 58.15) * mm, "end": v(-96.68, 57.95) * mm});
            skLineSegment(sketch, "E1687", {"start": v(-96.68, 57.95) * mm, "end": v(-96.5, 57.75) * mm});
            skLineSegment(sketch, "E1688", {"start": v(-96.5, 57.75) * mm, "end": v(-96.33, 57.56) * mm});
            skLineSegment(sketch, "E1689", {"start": v(-96.33, 57.56) * mm, "end": v(-96.16, 57.38) * mm});
            skLineSegment(sketch, "E1690", {"start": v(-96.16, 57.38) * mm, "end": v(-96, 57.2) * mm});
            skLineSegment(sketch, "E1691", {"start": v(-96, 57.2) * mm, "end": v(-95.83, 57.02) * mm});
            skLineSegment(sketch, "E1692", {"start": v(-95.83, 57.02) * mm, "end": v(-95.68, 56.86) * mm});
            skLineSegment(sketch, "E1693", {"start": v(-95.68, 56.86) * mm, "end": v(-95.52, 56.7) * mm});
            skLineSegment(sketch, "E1694", {"start": v(-95.52, 56.7) * mm, "end": v(-95.36, 56.54) * mm});
            skLineSegment(sketch, "E1695", {"start": v(-95.36, 56.54) * mm, "end": v(-95.21, 56.4) * mm});
            skLineSegment(sketch, "E1696", {"start": v(-95.21, 56.4) * mm, "end": v(-95.07, 56.25) * mm});
            skLineSegment(sketch, "E1697", {"start": v(-95.07, 56.25) * mm, "end": v(-94.93, 56.1) * mm});
            skLineSegment(sketch, "E1698", {"start": v(-94.93, 56.1) * mm, "end": v(-94.79, 55.98) * mm});
            skLineSegment(sketch, "E1699", {"start": v(-94.79, 55.98) * mm, "end": v(-94.65, 55.85) * mm});
            skLineSegment(sketch, "E1700", {"start": v(-94.65, 55.85) * mm, "end": v(-94.52, 55.73) * mm});
            skLineSegment(sketch, "E1701", {"start": v(-94.52, 55.73) * mm, "end": v(-94.4, 55.61) * mm});
            skLineSegment(sketch, "E1702", {"start": v(-94.4, 55.61) * mm, "end": v(-94.27, 55.5) * mm});
            skLineSegment(sketch, "E1703", {"start": v(-94.27, 55.5) * mm, "end": v(-94.15, 55.4) * mm});
            skLineSegment(sketch, "E1704", {"start": v(-94.15, 55.4) * mm, "end": v(-94.03, 55.3) * mm});
            skLineSegment(sketch, "E1705", {"start": v(-94.03, 55.3) * mm, "end": v(-93.92, 55.2) * mm});
            skLineSegment(sketch, "E1706", {"start": v(-93.92, 55.2) * mm, "end": v(-93.81, 55.1) * mm});
            skLineSegment(sketch, "E1707", {"start": v(-93.81, 55.1) * mm, "end": v(-93.7, 55.02) * mm});
            skLineSegment(sketch, "E1708", {"start": v(-93.7, 55.02) * mm, "end": v(-93.55, 54.77) * mm});
            skLineSegment(sketch, "E1709", {"start": v(-93.55, 54.77) * mm, "end": v(-95.73, 50.87) * mm});
            skLineSegment(sketch, "E1710", {"start": v(-95.73, 50.87) * mm, "end": v(-96.03, 50.87) * mm});
            skLineSegment(sketch, "E1711", {"start": v(-96.03, 50.87) * mm, "end": v(-96.15, 50.91) * mm});
            skLineSegment(sketch, "E1712", {"start": v(-96.15, 50.91) * mm, "end": v(-96.29, 50.96) * mm});
            skLineSegment(sketch, "E1713", {"start": v(-96.29, 50.96) * mm, "end": v(-96.43, 51) * mm});
            skLineSegment(sketch, "E1714", {"start": v(-96.43, 51) * mm, "end": v(-96.57, 51.05) * mm});
            skLineSegment(sketch, "E1715", {"start": v(-96.57, 51.05) * mm, "end": v(-96.73, 51.1) * mm});
            skLineSegment(sketch, "E1716", {"start": v(-96.73, 51.1) * mm, "end": v(-96.89, 51.14) * mm});
            skLineSegment(sketch, "E1717", {"start": v(-96.89, 51.14) * mm, "end": v(-97.05, 51.2) * mm});
            skLineSegment(sketch, "E1718", {"start": v(-97.05, 51.2) * mm, "end": v(-97.23, 51.24) * mm});
            skLineSegment(sketch, "E1719", {"start": v(-97.23, 51.24) * mm, "end": v(-97.4, 51.29) * mm});
            skLineSegment(sketch, "E1720", {"start": v(-97.4, 51.29) * mm, "end": v(-97.6, 51.34) * mm});
            skLineSegment(sketch, "E1721", {"start": v(-97.6, 51.34) * mm, "end": v(-97.78, 51.39) * mm});
            skLineSegment(sketch, "E1722", {"start": v(-97.78, 51.39) * mm, "end": v(-97.98, 51.44) * mm});
            skLineSegment(sketch, "E1723", {"start": v(-97.98, 51.44) * mm, "end": v(-98.19, 51.49) * mm});
            skLineSegment(sketch, "E1724", {"start": v(-98.19, 51.49) * mm, "end": v(-98.4, 51.53) * mm});
            skLineSegment(sketch, "E1725", {"start": v(-98.4, 51.53) * mm, "end": v(-98.62, 51.58) * mm});
            skLineSegment(sketch, "E1726", {"start": v(-98.62, 51.58) * mm, "end": v(-98.85, 51.63) * mm});
            skLineSegment(sketch, "E1727", {"start": v(-98.85, 51.63) * mm, "end": v(-99.08, 51.68) * mm});
            skLineSegment(sketch, "E1728", {"start": v(-99.08, 51.68) * mm, "end": v(-99.32, 51.73) * mm});
            skLineSegment(sketch, "E1729", {"start": v(-99.32, 51.73) * mm, "end": v(-99.56, 51.77) * mm});
            skLineSegment(sketch, "E1730", {"start": v(-99.56, 51.77) * mm, "end": v(-99.82, 51.82) * mm});
            skLineSegment(sketch, "E1731", {"start": v(-99.82, 51.82) * mm, "end": v(-100.08, 51.87) * mm});
            skLineSegment(sketch, "E1732", {"start": v(-100.08, 51.87) * mm, "end": v(-100.34, 51.91) * mm});
            skLineSegment(sketch, "E1733", {"start": v(-100.34, 51.91) * mm, "end": v(-100.62, 51.95) * mm});
            skLineSegment(sketch, "E1734", {"start": v(-100.62, 51.95) * mm, "end": v(-100.9, 52) * mm});
            skLineSegment(sketch, "E1735", {"start": v(-100.9, 52) * mm, "end": v(-101.18, 52.04) * mm});
            skLineSegment(sketch, "E1736", {"start": v(-101.18, 52.04) * mm, "end": v(-101.47, 52.08) * mm});
            skLineSegment(sketch, "E1737", {"start": v(-101.47, 52.08) * mm, "end": v(-101.77, 52.11) * mm});
            skLineSegment(sketch, "E1738", {"start": v(-101.77, 52.11) * mm, "end": v(-102.08, 52.15) * mm});
            skLineSegment(sketch, "E1739", {"start": v(-102.08, 52.15) * mm, "end": v(-102.4, 52.18) * mm});
            skLineSegment(sketch, "E1740", {"start": v(-102.4, 52.18) * mm, "end": v(-102.71, 52.22) * mm});
            skLineSegment(sketch, "E1741", {"start": v(-102.71, 52.22) * mm, "end": v(-103.04, 52.25) * mm});
            skLineSegment(sketch, "E1742", {"start": v(-103.04, 52.25) * mm, "end": v(-103.37, 52.28) * mm});
            skLineSegment(sketch, "E1743", {"start": v(-103.37, 52.28) * mm, "end": v(-103.71, 52.3) * mm});
            skLineSegment(sketch, "E1744", {"start": v(-103.71, 52.3) * mm, "end": v(-104.06, 52.33) * mm});
            skLineSegment(sketch, "E1745", {"start": v(-104.06, 52.33) * mm, "end": v(-104.41, 52.35) * mm});
            skLineSegment(sketch, "E1746", {"start": v(-104.41, 52.35) * mm, "end": v(-104.77, 52.37) * mm});
            skLineSegment(sketch, "E1747", {"start": v(-104.77, 52.37) * mm, "end": v(-105.14, 52.4) * mm});
            skLineSegment(sketch, "E1748", {"start": v(-105.14, 52.4) * mm, "end": v(-105.51, 52.4) * mm});
            skLineSegment(sketch, "E1749", {"start": v(-105.51, 52.4) * mm, "end": v(-105.9, 52.42) * mm});
            skLineSegment(sketch, "E1750", {"start": v(-105.9, 52.42) * mm, "end": v(-106.28, 52.43) * mm});
            skLineSegment(sketch, "E1751", {"start": v(-106.28, 52.43) * mm, "end": v(-106.67, 52.44) * mm});
            skLineSegment(sketch, "E1752", {"start": v(-106.67, 52.44) * mm, "end": v(-107.07, 52.44) * mm});
            skLineSegment(sketch, "E1753", {"start": v(-107.07, 52.44) * mm, "end": v(-107.24, 52.33) * mm});
            skLineSegment(sketch, "E1754", {"start": v(-107.24, 52.33) * mm, "end": v(-108.74, 49.15) * mm});
            skLineSegment(sketch, "E1755", {"start": v(-108.74, 49.15) * mm, "end": v(-108.71, 48.94) * mm});
            skLineSegment(sketch, "E1756", {"start": v(-108.71, 48.94) * mm, "end": v(-108.45, 48.64) * mm});
            skLineSegment(sketch, "E1757", {"start": v(-108.45, 48.64) * mm, "end": v(-108.2, 48.34) * mm});
            skLineSegment(sketch, "E1758", {"start": v(-108.2, 48.34) * mm, "end": v(-107.94, 48.05) * mm});
            skLineSegment(sketch, "E1759", {"start": v(-107.94, 48.05) * mm, "end": v(-107.7, 47.77) * mm});
            skLineSegment(sketch, "E1760", {"start": v(-107.7, 47.77) * mm, "end": v(-107.44, 47.49) * mm});
            skLineSegment(sketch, "E1761", {"start": v(-107.44, 47.49) * mm, "end": v(-107.2, 47.22) * mm});
            skLineSegment(sketch, "E1762", {"start": v(-107.2, 47.22) * mm, "end": v(-106.95, 46.95) * mm});
            skLineSegment(sketch, "E1763", {"start": v(-106.95, 46.95) * mm, "end": v(-106.7, 46.7) * mm});
            skLineSegment(sketch, "E1764", {"start": v(-106.7, 46.7) * mm, "end": v(-106.47, 46.45) * mm});
            skLineSegment(sketch, "E1765", {"start": v(-106.47, 46.45) * mm, "end": v(-106.23, 46.2) * mm});
            skLineSegment(sketch, "E1766", {"start": v(-106.23, 46.2) * mm, "end": v(-106, 45.96) * mm});
            skLineSegment(sketch, "E1767", {"start": v(-106, 45.96) * mm, "end": v(-105.76, 45.73) * mm});
            skLineSegment(sketch, "E1768", {"start": v(-105.76, 45.73) * mm, "end": v(-105.53, 45.5) * mm});
            skLineSegment(sketch, "E1769", {"start": v(-105.53, 45.5) * mm, "end": v(-105.3, 45.29) * mm});
            skLineSegment(sketch, "E1770", {"start": v(-105.3, 45.29) * mm, "end": v(-105.08, 45.07) * mm});
            skLineSegment(sketch, "E1771", {"start": v(-105.08, 45.07) * mm, "end": v(-104.86, 44.87) * mm});
            skLineSegment(sketch, "E1772", {"start": v(-104.86, 44.87) * mm, "end": v(-104.65, 44.67) * mm});
            skLineSegment(sketch, "E1773", {"start": v(-104.65, 44.67) * mm, "end": v(-104.43, 44.47) * mm});
            skLineSegment(sketch, "E1774", {"start": v(-104.43, 44.47) * mm, "end": v(-104.22, 44.28) * mm});
            skLineSegment(sketch, "E1775", {"start": v(-104.22, 44.28) * mm, "end": v(-104.01, 44.1) * mm});
            skLineSegment(sketch, "E1776", {"start": v(-104.01, 44.1) * mm, "end": v(-103.8, 43.92) * mm});
            skLineSegment(sketch, "E1777", {"start": v(-103.8, 43.92) * mm, "end": v(-103.6, 43.75) * mm});
            skLineSegment(sketch, "E1778", {"start": v(-103.6, 43.75) * mm, "end": v(-103.41, 43.59) * mm});
            skLineSegment(sketch, "E1779", {"start": v(-103.41, 43.59) * mm, "end": v(-103.22, 43.43) * mm});
            skLineSegment(sketch, "E1780", {"start": v(-103.22, 43.43) * mm, "end": v(-103.03, 43.28) * mm});
            skLineSegment(sketch, "E1781", {"start": v(-103.03, 43.28) * mm, "end": v(-102.84, 43.13) * mm});
            skLineSegment(sketch, "E1782", {"start": v(-102.84, 43.13) * mm, "end": v(-102.66, 42.98) * mm});
            skLineSegment(sketch, "E1783", {"start": v(-102.66, 42.98) * mm, "end": v(-102.49, 42.85) * mm});
            skLineSegment(sketch, "E1784", {"start": v(-102.49, 42.85) * mm, "end": v(-102.31, 42.71) * mm});
            skLineSegment(sketch, "E1785", {"start": v(-102.31, 42.71) * mm, "end": v(-102.14, 42.59) * mm});
            skLineSegment(sketch, "E1786", {"start": v(-102.14, 42.59) * mm, "end": v(-101.98, 42.46) * mm});
            skLineSegment(sketch, "E1787", {"start": v(-101.98, 42.46) * mm, "end": v(-101.82, 42.35) * mm});
            skLineSegment(sketch, "E1788", {"start": v(-101.82, 42.35) * mm, "end": v(-101.66, 42.24) * mm});
            skLineSegment(sketch, "E1789", {"start": v(-101.66, 42.24) * mm, "end": v(-101.5, 42.13) * mm});
            skLineSegment(sketch, "E1790", {"start": v(-101.5, 42.13) * mm, "end": v(-101.36, 42.03) * mm});
            skLineSegment(sketch, "E1791", {"start": v(-101.36, 42.03) * mm, "end": v(-101.22, 41.93) * mm});
            skLineSegment(sketch, "E1792", {"start": v(-101.22, 41.93) * mm, "end": v(-101.08, 41.84) * mm});
            skLineSegment(sketch, "E1793", {"start": v(-101.08, 41.84) * mm, "end": v(-100.95, 41.75) * mm});
            skLineSegment(sketch, "E1794", {"start": v(-100.95, 41.75) * mm, "end": v(-100.82, 41.67) * mm});
            skLineSegment(sketch, "E1795", {"start": v(-100.82, 41.67) * mm, "end": v(-100.7, 41.59) * mm});
            skLineSegment(sketch, "E1796", {"start": v(-100.7, 41.59) * mm, "end": v(-100.58, 41.51) * mm});
            skLineSegment(sketch, "E1797", {"start": v(-100.58, 41.51) * mm, "end": v(-100.46, 41.44) * mm});
            skLineSegment(sketch, "E1798", {"start": v(-100.46, 41.44) * mm, "end": v(-100.27, 41.21) * mm});
            skLineSegment(sketch, "E1799", {"start": v(-100.27, 41.21) * mm, "end": v(-101.88, 37.05) * mm});
            skLineSegment(sketch, "E1800", {"start": v(-101.88, 37.05) * mm, "end": v(-102.18, 37) * mm});
            skLineSegment(sketch, "E1801", {"start": v(-102.18, 37) * mm, "end": v(-102.31, 37.03) * mm});
            skLineSegment(sketch, "E1802", {"start": v(-102.31, 37.03) * mm, "end": v(-102.45, 37.06) * mm});
            skLineSegment(sketch, "E1803", {"start": v(-102.45, 37.06) * mm, "end": v(-102.6, 37.08) * mm});
            skLineSegment(sketch, "E1804", {"start": v(-102.6, 37.08) * mm, "end": v(-102.75, 37.1) * mm});
            skLineSegment(sketch, "E1805", {"start": v(-102.75, 37.1) * mm, "end": v(-102.9, 37.13) * mm});
            skLineSegment(sketch, "E1806", {"start": v(-102.9, 37.13) * mm, "end": v(-103.07, 37.16) * mm});
            skLineSegment(sketch, "E1807", {"start": v(-103.07, 37.16) * mm, "end": v(-103.24, 37.18) * mm});
            skLineSegment(sketch, "E1808", {"start": v(-103.24, 37.18) * mm, "end": v(-103.42, 37.2) * mm});
            skLineSegment(sketch, "E1809", {"start": v(-103.42, 37.2) * mm, "end": v(-103.6, 37.23) * mm});
            skLineSegment(sketch, "E1810", {"start": v(-103.6, 37.23) * mm, "end": v(-103.8, 37.25) * mm});
            skLineSegment(sketch, "E1811", {"start": v(-103.8, 37.25) * mm, "end": v(-103.99, 37.27) * mm});
            skLineSegment(sketch, "E1812", {"start": v(-103.99, 37.27) * mm, "end": v(-104.2, 37.3) * mm});
            skLineSegment(sketch, "E1813", {"start": v(-104.2, 37.3) * mm, "end": v(-104.4, 37.31) * mm});
            skLineSegment(sketch, "E1814", {"start": v(-104.4, 37.31) * mm, "end": v(-104.62, 37.33) * mm});
            skLineSegment(sketch, "E1815", {"start": v(-104.62, 37.33) * mm, "end": v(-104.85, 37.35) * mm});
            skLineSegment(sketch, "E1816", {"start": v(-104.85, 37.35) * mm, "end": v(-105.08, 37.37) * mm});
            skLineSegment(sketch, "E1817", {"start": v(-105.08, 37.37) * mm, "end": v(-105.31, 37.38) * mm});
            skLineSegment(sketch, "E1818", {"start": v(-105.31, 37.38) * mm, "end": v(-105.56, 37.4) * mm});
            skLineSegment(sketch, "E1819", {"start": v(-105.56, 37.4) * mm, "end": v(-105.8, 37.4) * mm});
            skLineSegment(sketch, "E1820", {"start": v(-105.8, 37.4) * mm, "end": v(-106.06, 37.42) * mm});
            skLineSegment(sketch, "E1821", {"start": v(-106.06, 37.42) * mm, "end": v(-106.33, 37.43) * mm});
            skLineSegment(sketch, "E1822", {"start": v(-106.33, 37.43) * mm, "end": v(-106.6, 37.43) * mm});
            skLineSegment(sketch, "E1823", {"start": v(-106.6, 37.43) * mm, "end": v(-106.87, 37.44) * mm});
            skLineSegment(sketch, "E1824", {"start": v(-106.87, 37.44) * mm, "end": v(-107.16, 37.44) * mm});
            skLineSegment(sketch, "E1825", {"start": v(-107.16, 37.44) * mm, "end": v(-107.44, 37.44) * mm});
            skLineSegment(sketch, "E1826", {"start": v(-107.44, 37.44) * mm, "end": v(-107.74, 37.44) * mm});
            skLineSegment(sketch, "E1827", {"start": v(-107.74, 37.44) * mm, "end": v(-108.04, 37.44) * mm});
            skLineSegment(sketch, "E1828", {"start": v(-108.04, 37.44) * mm, "end": v(-108.35, 37.43) * mm});
            skLineSegment(sketch, "E1829", {"start": v(-108.35, 37.43) * mm, "end": v(-108.67, 37.42) * mm});
            skLineSegment(sketch, "E1830", {"start": v(-108.67, 37.42) * mm, "end": v(-108.99, 37.4) * mm});
            skLineSegment(sketch, "E1831", {"start": v(-108.99, 37.4) * mm, "end": v(-109.31, 37.4) * mm});
            skLineSegment(sketch, "E1832", {"start": v(-109.31, 37.4) * mm, "end": v(-109.65, 37.38) * mm});
            skLineSegment(sketch, "E1833", {"start": v(-109.65, 37.38) * mm, "end": v(-109.99, 37.36) * mm});
            skLineSegment(sketch, "E1834", {"start": v(-109.99, 37.36) * mm, "end": v(-110.34, 37.33) * mm});
            skLineSegment(sketch, "E1835", {"start": v(-110.34, 37.33) * mm, "end": v(-110.69, 37.3) * mm});
            skLineSegment(sketch, "E1836", {"start": v(-110.69, 37.3) * mm, "end": v(-111.05, 37.28) * mm});
            skLineSegment(sketch, "E1837", {"start": v(-111.05, 37.28) * mm, "end": v(-111.41, 37.24) * mm});
            skLineSegment(sketch, "E1838", {"start": v(-111.41, 37.24) * mm, "end": v(-111.78, 37.2) * mm});
            skLineSegment(sketch, "E1839", {"start": v(-111.78, 37.2) * mm, "end": v(-112.16, 37.17) * mm});
            skLineSegment(sketch, "E1840", {"start": v(-112.16, 37.17) * mm, "end": v(-112.55, 37.12) * mm});
            skLineSegment(sketch, "E1841", {"start": v(-112.55, 37.12) * mm, "end": v(-112.94, 37.07) * mm});
            skLineSegment(sketch, "E1842", {"start": v(-112.94, 37.07) * mm, "end": v(-113.33, 37.02) * mm});
            skLineSegment(sketch, "E1843", {"start": v(-113.33, 37.02) * mm, "end": v(-113.49, 36.89) * mm});
            skLineSegment(sketch, "E1844", {"start": v(-113.49, 36.89) * mm, "end": v(-114.52, 33.53) * mm});
            skLineSegment(sketch, "E1845", {"start": v(-114.52, 33.53) * mm, "end": v(-114.47, 33.33) * mm});
            skLineSegment(sketch, "E1846", {"start": v(-114.47, 33.33) * mm, "end": v(-114.17, 33.07) * mm});
            skLineSegment(sketch, "E1847", {"start": v(-114.17, 33.07) * mm, "end": v(-113.88, 32.8) * mm});
            skLineSegment(sketch, "E1848", {"start": v(-113.88, 32.8) * mm, "end": v(-113.59, 32.55) * mm});
            skLineSegment(sketch, "E1849", {"start": v(-113.59, 32.55) * mm, "end": v(-113.3, 32.3) * mm});
            skLineSegment(sketch, "E1850", {"start": v(-113.3, 32.3) * mm, "end": v(-113.01, 32.07) * mm});
            skLineSegment(sketch, "E1851", {"start": v(-113.01, 32.07) * mm, "end": v(-112.73, 31.83) * mm});
            skLineSegment(sketch, "E1852", {"start": v(-112.73, 31.83) * mm, "end": v(-112.45, 31.6) * mm});
            skLineSegment(sketch, "E1853", {"start": v(-112.45, 31.6) * mm, "end": v(-112.18, 31.38) * mm});
            skLineSegment(sketch, "E1854", {"start": v(-112.18, 31.38) * mm, "end": v(-111.9, 31.17) * mm});
            skLineSegment(sketch, "E1855", {"start": v(-111.9, 31.17) * mm, "end": v(-111.63, 30.96) * mm});
            skLineSegment(sketch, "E1856", {"start": v(-111.63, 30.96) * mm, "end": v(-111.37, 30.76) * mm});
            skLineSegment(sketch, "E1857", {"start": v(-111.37, 30.76) * mm, "end": v(-111.1, 30.56) * mm});
            skLineSegment(sketch, "E1858", {"start": v(-111.1, 30.56) * mm, "end": v(-110.85, 30.37) * mm});
            skLineSegment(sketch, "E1859", {"start": v(-110.85, 30.37) * mm, "end": v(-110.6, 30.18) * mm});
            skLineSegment(sketch, "E1860", {"start": v(-110.6, 30.18) * mm, "end": v(-110.34, 30) * mm});
            skLineSegment(sketch, "E1861", {"start": v(-110.34, 30) * mm, "end": v(-110.1, 29.83) * mm});
            skLineSegment(sketch, "E1862", {"start": v(-110.1, 29.83) * mm, "end": v(-109.85, 29.66) * mm});
            skLineSegment(sketch, "E1863", {"start": v(-109.85, 29.66) * mm, "end": v(-109.61, 29.5) * mm});
            skLineSegment(sketch, "E1864", {"start": v(-109.61, 29.5) * mm, "end": v(-109.38, 29.34) * mm});
            skLineSegment(sketch, "E1865", {"start": v(-109.38, 29.34) * mm, "end": v(-109.15, 29.2) * mm});
            skLineSegment(sketch, "E1866", {"start": v(-109.15, 29.2) * mm, "end": v(-108.92, 29.04) * mm});
            skLineSegment(sketch, "E1867", {"start": v(-108.92, 29.04) * mm, "end": v(-108.7, 28.9) * mm});
            skLineSegment(sketch, "E1868", {"start": v(-108.7, 28.9) * mm, "end": v(-108.48, 28.77) * mm});
            skLineSegment(sketch, "E1869", {"start": v(-108.48, 28.77) * mm, "end": v(-108.27, 28.64) * mm});
            skLineSegment(sketch, "E1870", {"start": v(-108.27, 28.64) * mm, "end": v(-108.06, 28.5) * mm});
            skLineSegment(sketch, "E1871", {"start": v(-108.06, 28.5) * mm, "end": v(-107.85, 28.39) * mm});
            skLineSegment(sketch, "E1872", {"start": v(-107.85, 28.39) * mm, "end": v(-107.65, 28.27) * mm});
            skLineSegment(sketch, "E1873", {"start": v(-107.65, 28.27) * mm, "end": v(-107.46, 28.16) * mm});
            skLineSegment(sketch, "E1874", {"start": v(-107.46, 28.16) * mm, "end": v(-107.27, 28.05) * mm});
            skLineSegment(sketch, "E1875", {"start": v(-107.27, 28.05) * mm, "end": v(-107.08, 27.95) * mm});
            skLineSegment(sketch, "E1876", {"start": v(-107.08, 27.95) * mm, "end": v(-106.9, 27.85) * mm});
            skLineSegment(sketch, "E1877", {"start": v(-106.9, 27.85) * mm, "end": v(-106.73, 27.76) * mm});
            skLineSegment(sketch, "E1878", {"start": v(-106.73, 27.76) * mm, "end": v(-106.56, 27.67) * mm});
            skLineSegment(sketch, "E1879", {"start": v(-106.56, 27.67) * mm, "end": v(-106.4, 27.59) * mm});
            skLineSegment(sketch, "E1880", {"start": v(-106.4, 27.59) * mm, "end": v(-106.23, 27.5) * mm});
            skLineSegment(sketch, "E1881", {"start": v(-106.23, 27.5) * mm, "end": v(-106.08, 27.43) * mm});
            skLineSegment(sketch, "E1882", {"start": v(-106.08, 27.43) * mm, "end": v(-105.93, 27.36) * mm});
            skLineSegment(sketch, "E1883", {"start": v(-105.93, 27.36) * mm, "end": v(-105.78, 27.29) * mm});
            skLineSegment(sketch, "E1884", {"start": v(-105.78, 27.29) * mm, "end": v(-105.64, 27.22) * mm});
            skLineSegment(sketch, "E1885", {"start": v(-105.64, 27.22) * mm, "end": v(-105.5, 27.16) * mm});
            skLineSegment(sketch, "E1886", {"start": v(-105.5, 27.16) * mm, "end": v(-105.38, 27.1) * mm});
            skLineSegment(sketch, "E1887", {"start": v(-105.38, 27.1) * mm, "end": v(-105.26, 27.05) * mm});
            skLineSegment(sketch, "E1888", {"start": v(-105.26, 27.05) * mm, "end": v(-105.03, 26.85) * mm});
            skLineSegment(sketch, "E1889", {"start": v(-105.03, 26.85) * mm, "end": v(-106.05, 22.5) * mm});
            skLineSegment(sketch, "E1890", {"start": v(-106.05, 22.5) * mm, "end": v(-106.34, 22.42) * mm});
            skLineSegment(sketch, "E1891", {"start": v(-106.34, 22.42) * mm, "end": v(-106.48, 22.43) * mm});
            skLineSegment(sketch, "E1892", {"start": v(-106.48, 22.43) * mm, "end": v(-106.62, 22.43) * mm});
            skLineSegment(sketch, "E1893", {"start": v(-106.62, 22.43) * mm, "end": v(-106.76, 22.44) * mm});
            skLineSegment(sketch, "E1894", {"start": v(-106.76, 22.44) * mm, "end": v(-106.92, 22.44) * mm});
            skLineSegment(sketch, "E1895", {"start": v(-106.92, 22.44) * mm, "end": v(-107.08, 22.44) * mm});
            skLineSegment(sketch, "E1896", {"start": v(-107.08, 22.44) * mm, "end": v(-107.24, 22.45) * mm});
            skLineSegment(sketch, "E1897", {"start": v(-107.24, 22.45) * mm, "end": v(-107.42, 22.45) * mm});
            skLineSegment(sketch, "E1898", {"start": v(-107.42, 22.45) * mm, "end": v(-107.6, 22.44) * mm});
            skLineSegment(sketch, "E1899", {"start": v(-107.6, 22.44) * mm, "end": v(-107.78, 22.44) * mm});
            skLineSegment(sketch, "E1900", {"start": v(-107.78, 22.44) * mm, "end": v(-107.97, 22.44) * mm});
            skLineSegment(sketch, "E1901", {"start": v(-107.97, 22.44) * mm, "end": v(-108.17, 22.43) * mm});
            skLineSegment(sketch, "E1902", {"start": v(-108.17, 22.43) * mm, "end": v(-108.38, 22.42) * mm});
            skLineSegment(sketch, "E1903", {"start": v(-108.38, 22.42) * mm, "end": v(-108.59, 22.42) * mm});
            skLineSegment(sketch, "E1904", {"start": v(-108.59, 22.42) * mm, "end": v(-108.8, 22.4) * mm});
            skLineSegment(sketch, "E1905", {"start": v(-108.8, 22.4) * mm, "end": v(-109.03, 22.4) * mm});
            skLineSegment(sketch, "E1906", {"start": v(-109.03, 22.4) * mm, "end": v(-109.26, 22.37) * mm});
            skLineSegment(sketch, "E1907", {"start": v(-109.26, 22.37) * mm, "end": v(-109.5, 22.36) * mm});
            skLineSegment(sketch, "E1908", {"start": v(-109.5, 22.36) * mm, "end": v(-109.74, 22.34) * mm});
            skLineSegment(sketch, "E1909", {"start": v(-109.74, 22.34) * mm, "end": v(-109.99, 22.31) * mm});
            skLineSegment(sketch, "E1910", {"start": v(-109.99, 22.31) * mm, "end": v(-110.25, 22.29) * mm});
            skLineSegment(sketch, "E1911", {"start": v(-110.25, 22.29) * mm, "end": v(-110.5, 22.26) * mm});
            skLineSegment(sketch, "E1912", {"start": v(-110.5, 22.26) * mm, "end": v(-110.78, 22.23) * mm});
            skLineSegment(sketch, "E1913", {"start": v(-110.78, 22.23) * mm, "end": v(-111.05, 22.2) * mm});
            skLineSegment(sketch, "E1914", {"start": v(-111.05, 22.2) * mm, "end": v(-111.33, 22.16) * mm});
            skLineSegment(sketch, "E1915", {"start": v(-111.33, 22.16) * mm, "end": v(-111.62, 22.12) * mm});
            skLineSegment(sketch, "E1916", {"start": v(-111.62, 22.12) * mm, "end": v(-111.9, 22.08) * mm});
            skLineSegment(sketch, "E1917", {"start": v(-111.9, 22.08) * mm, "end": v(-112.2, 22.03) * mm});
            skLineSegment(sketch, "E1918", {"start": v(-112.2, 22.03) * mm, "end": v(-112.51, 21.98) * mm});
            skLineSegment(sketch, "E1919", {"start": v(-112.51, 21.98) * mm, "end": v(-112.82, 21.93) * mm});
            skLineSegment(sketch, "E1920", {"start": v(-112.82, 21.93) * mm, "end": v(-113.14, 21.87) * mm});
            skLineSegment(sketch, "E1921", {"start": v(-113.14, 21.87) * mm, "end": v(-113.46, 21.81) * mm});
            skLineSegment(sketch, "E1922", {"start": v(-113.46, 21.81) * mm, "end": v(-113.8, 21.75) * mm});
            skLineSegment(sketch, "E1923", {"start": v(-113.8, 21.75) * mm, "end": v(-114.12, 21.68) * mm});
            skLineSegment(sketch, "E1924", {"start": v(-114.12, 21.68) * mm, "end": v(-114.46, 21.6) * mm});
            skLineSegment(sketch, "E1925", {"start": v(-114.46, 21.6) * mm, "end": v(-114.81, 21.53) * mm});
            skLineSegment(sketch, "E1926", {"start": v(-114.81, 21.53) * mm, "end": v(-115.16, 21.45) * mm});
            skLineSegment(sketch, "E1927", {"start": v(-115.16, 21.45) * mm, "end": v(-115.52, 21.37) * mm});
            skLineSegment(sketch, "E1928", {"start": v(-115.52, 21.37) * mm, "end": v(-115.88, 21.28) * mm});
            skLineSegment(sketch, "E1929", {"start": v(-115.88, 21.28) * mm, "end": v(-116.25, 21.19) * mm});
            skLineSegment(sketch, "E1930", {"start": v(-116.25, 21.19) * mm, "end": v(-116.62, 21.1) * mm});
            skLineSegment(sketch, "E1931", {"start": v(-116.62, 21.1) * mm, "end": v(-117, 20.99) * mm});
            skLineSegment(sketch, "E1932", {"start": v(-117, 20.99) * mm, "end": v(-117.39, 20.88) * mm});
            skLineSegment(sketch, "E1933", {"start": v(-117.39, 20.88) * mm, "end": v(-117.52, 20.73) * mm});
            skLineSegment(sketch, "E1934", {"start": v(-117.52, 20.73) * mm, "end": v(-118.08, 17.26) * mm});
            skLineSegment(sketch, "E1935", {"start": v(-118.08, 17.26) * mm, "end": v(-118, 17.07) * mm});
            skLineSegment(sketch, "E1936", {"start": v(-118, 17.07) * mm, "end": v(-117.67, 16.85) * mm});
            skLineSegment(sketch, "E1937", {"start": v(-117.67, 16.85) * mm, "end": v(-117.34, 16.63) * mm});
            skLineSegment(sketch, "E1938", {"start": v(-117.34, 16.63) * mm, "end": v(-117.02, 16.42) * mm});
            skLineSegment(sketch, "E1939", {"start": v(-117.02, 16.42) * mm, "end": v(-116.7, 16.22) * mm});
            skLineSegment(sketch, "E1940", {"start": v(-116.7, 16.22) * mm, "end": v(-116.38, 16.02) * mm});
            skLineSegment(sketch, "E1941", {"start": v(-116.38, 16.02) * mm, "end": v(-116.07, 15.83) * mm});
            skLineSegment(sketch, "E1942", {"start": v(-116.07, 15.83) * mm, "end": v(-115.76, 15.64) * mm});
            skLineSegment(sketch, "E1943", {"start": v(-115.76, 15.64) * mm, "end": v(-115.46, 15.46) * mm});
            skLineSegment(sketch, "E1944", {"start": v(-115.46, 15.46) * mm, "end": v(-115.16, 15.29) * mm});
            skLineSegment(sketch, "E1945", {"start": v(-115.16, 15.29) * mm, "end": v(-114.86, 15.12) * mm});
            skLineSegment(sketch, "E1946", {"start": v(-114.86, 15.12) * mm, "end": v(-114.57, 14.95) * mm});
            skLineSegment(sketch, "E1947", {"start": v(-114.57, 14.95) * mm, "end": v(-114.28, 14.8) * mm});
            skLineSegment(sketch, "E1948", {"start": v(-114.28, 14.8) * mm, "end": v(-114, 14.64) * mm});
            skLineSegment(sketch, "E1949", {"start": v(-114, 14.64) * mm, "end": v(-113.72, 14.5) * mm});
            skLineSegment(sketch, "E1950", {"start": v(-113.72, 14.5) * mm, "end": v(-113.45, 14.35) * mm});
            skLineSegment(sketch, "E1951", {"start": v(-113.45, 14.35) * mm, "end": v(-113.18, 14.21) * mm});
            skLineSegment(sketch, "E1952", {"start": v(-113.18, 14.21) * mm, "end": v(-112.92, 14.08) * mm});
            skLineSegment(sketch, "E1953", {"start": v(-112.92, 14.08) * mm, "end": v(-112.66, 13.95) * mm});
            skLineSegment(sketch, "E1954", {"start": v(-112.66, 13.95) * mm, "end": v(-112.4, 13.83) * mm});
            skLineSegment(sketch, "E1955", {"start": v(-112.4, 13.83) * mm, "end": v(-112.15, 13.71) * mm});
            skLineSegment(sketch, "E1956", {"start": v(-112.15, 13.71) * mm, "end": v(-111.9, 13.6) * mm});
            skLineSegment(sketch, "E1957", {"start": v(-111.9, 13.6) * mm, "end": v(-111.67, 13.49) * mm});
            skLineSegment(sketch, "E1958", {"start": v(-111.67, 13.49) * mm, "end": v(-111.43, 13.38) * mm});
            skLineSegment(sketch, "E1959", {"start": v(-111.43, 13.38) * mm, "end": v(-111.2, 13.28) * mm});
            skLineSegment(sketch, "E1960", {"start": v(-111.2, 13.28) * mm, "end": v(-110.98, 13.19) * mm});
            skLineSegment(sketch, "E1961", {"start": v(-110.98, 13.19) * mm, "end": v(-110.76, 13.1) * mm});
            skLineSegment(sketch, "E1962", {"start": v(-110.76, 13.1) * mm, "end": v(-110.55, 13) * mm});
            skLineSegment(sketch, "E1963", {"start": v(-110.55, 13) * mm, "end": v(-110.34, 12.93) * mm});
            skLineSegment(sketch, "E1964", {"start": v(-110.34, 12.93) * mm, "end": v(-110.13, 12.85) * mm});
            skLineSegment(sketch, "E1965", {"start": v(-110.13, 12.85) * mm, "end": v(-109.94, 12.77) * mm});
            skLineSegment(sketch, "E1966", {"start": v(-109.94, 12.77) * mm, "end": v(-109.74, 12.7) * mm});
            skLineSegment(sketch, "E1967", {"start": v(-109.74, 12.7) * mm, "end": v(-109.56, 12.63) * mm});
            skLineSegment(sketch, "E1968", {"start": v(-109.56, 12.63) * mm, "end": v(-109.38, 12.57) * mm});
            skLineSegment(sketch, "E1969", {"start": v(-109.38, 12.57) * mm, "end": v(-109.2, 12.5) * mm});
            skLineSegment(sketch, "E1970", {"start": v(-109.2, 12.5) * mm, "end": v(-109.03, 12.45) * mm});
            skLineSegment(sketch, "E1971", {"start": v(-109.03, 12.45) * mm, "end": v(-108.87, 12.4) * mm});
            skLineSegment(sketch, "E1972", {"start": v(-108.87, 12.4) * mm, "end": v(-108.7, 12.34) * mm});
            skLineSegment(sketch, "E1973", {"start": v(-108.7, 12.34) * mm, "end": v(-108.56, 12.3) * mm});
            skLineSegment(sketch, "E1974", {"start": v(-108.56, 12.3) * mm, "end": v(-108.4, 12.25) * mm});
            skLineSegment(sketch, "E1975", {"start": v(-108.4, 12.25) * mm, "end": v(-108.27, 12.2) * mm});
            skLineSegment(sketch, "E1976", {"start": v(-108.27, 12.2) * mm, "end": v(-108.13, 12.17) * mm});
            skLineSegment(sketch, "E1977", {"start": v(-108.13, 12.17) * mm, "end": v(-108, 12.13) * mm});
            skLineSegment(sketch, "E1978", {"start": v(-108, 12.13) * mm, "end": v(-107.76, 11.97) * mm});
            skLineSegment(sketch, "E1979", {"start": v(-107.76, 11.97) * mm, "end": v(-108.16, 7.52) * mm});
            skLineSegment(sketch, "E1980", {"start": v(-108.16, 7.52) * mm, "end": v(-108.43, 7.4) * mm});
            skLineSegment(sketch, "E1981", {"start": v(-108.43, 7.4) * mm, "end": v(-108.57, 7.38) * mm});
            skLineSegment(sketch, "E1982", {"start": v(-108.57, 7.38) * mm, "end": v(-108.7, 7.37) * mm});
            skLineSegment(sketch, "E1983", {"start": v(-108.7, 7.37) * mm, "end": v(-108.85, 7.35) * mm});
            skLineSegment(sketch, "E1984", {"start": v(-108.85, 7.35) * mm, "end": v(-109, 7.34) * mm});
            skLineSegment(sketch, "E1985", {"start": v(-109, 7.34) * mm, "end": v(-109.16, 7.32) * mm});
            skLineSegment(sketch, "E1986", {"start": v(-109.16, 7.32) * mm, "end": v(-109.33, 7.3) * mm});
            skLineSegment(sketch, "E1987", {"start": v(-109.33, 7.3) * mm, "end": v(-109.5, 7.27) * mm});
            skLineSegment(sketch, "E1988", {"start": v(-109.5, 7.27) * mm, "end": v(-109.68, 7.25) * mm});
            skLineSegment(sketch, "E1989", {"start": v(-109.68, 7.25) * mm, "end": v(-109.86, 7.22) * mm});
            skLineSegment(sketch, "E1990", {"start": v(-109.86, 7.22) * mm, "end": v(-110.05, 7.19) * mm});
            skLineSegment(sketch, "E1991", {"start": v(-110.05, 7.19) * mm, "end": v(-110.25, 7.15) * mm});
            skLineSegment(sketch, "E1992", {"start": v(-110.25, 7.15) * mm, "end": v(-110.45, 7.12) * mm});
            skLineSegment(sketch, "E1993", {"start": v(-110.45, 7.12) * mm, "end": v(-110.66, 7.08) * mm});
            skLineSegment(sketch, "E1994", {"start": v(-110.66, 7.08) * mm, "end": v(-110.87, 7.04) * mm});
            skLineSegment(sketch, "E1995", {"start": v(-110.87, 7.04) * mm, "end": v(-111.1, 7) * mm});
            skLineSegment(sketch, "E1996", {"start": v(-111.1, 7) * mm, "end": v(-111.32, 6.95) * mm});
            skLineSegment(sketch, "E1997", {"start": v(-111.32, 6.95) * mm, "end": v(-111.55, 6.9) * mm});
            skLineSegment(sketch, "E1998", {"start": v(-111.55, 6.9) * mm, "end": v(-111.79, 6.84) * mm});
            skLineSegment(sketch, "E1999", {"start": v(-111.79, 6.84) * mm, "end": v(-112.03, 6.78) * mm});
            skLineSegment(sketch, "E2000", {"start": v(-112.03, 6.78) * mm, "end": v(-112.28, 6.72) * mm});
            skLineSegment(sketch, "E2001", {"start": v(-112.28, 6.72) * mm, "end": v(-112.54, 6.66) * mm});
            skLineSegment(sketch, "E2002", {"start": v(-112.54, 6.66) * mm, "end": v(-112.8, 6.6) * mm});
            skLineSegment(sketch, "E2003", {"start": v(-112.8, 6.6) * mm, "end": v(-113.07, 6.52) * mm});
            skLineSegment(sketch, "E2004", {"start": v(-113.07, 6.52) * mm, "end": v(-113.34, 6.44) * mm});
            skLineSegment(sketch, "E2005", {"start": v(-113.34, 6.44) * mm, "end": v(-113.62, 6.36) * mm});
            skLineSegment(sketch, "E2006", {"start": v(-113.62, 6.36) * mm, "end": v(-113.9, 6.28) * mm});
            skLineSegment(sketch, "E2007", {"start": v(-113.9, 6.28) * mm, "end": v(-114.19, 6.2) * mm});
            skLineSegment(sketch, "E2008", {"start": v(-114.19, 6.2) * mm, "end": v(-114.48, 6.1) * mm});
            skLineSegment(sketch, "E2009", {"start": v(-114.48, 6.1) * mm, "end": v(-114.78, 6) * mm});
            skLineSegment(sketch, "E2010", {"start": v(-114.78, 6) * mm, "end": v(-115.09, 5.9) * mm});
            skLineSegment(sketch, "E2011", {"start": v(-115.09, 5.9) * mm, "end": v(-115.4, 5.8) * mm});
            skLineSegment(sketch, "E2012", {"start": v(-115.4, 5.8) * mm, "end": v(-115.72, 5.7) * mm});
            skLineSegment(sketch, "E2013", {"start": v(-115.72, 5.7) * mm, "end": v(-116.04, 5.58) * mm});
            skLineSegment(sketch, "E2014", {"start": v(-116.04, 5.58) * mm, "end": v(-116.36, 5.46) * mm});
            skLineSegment(sketch, "E2015", {"start": v(-116.36, 5.46) * mm, "end": v(-116.7, 5.34) * mm});
            skLineSegment(sketch, "E2016", {"start": v(-116.7, 5.34) * mm, "end": v(-117.03, 5.21) * mm});
            skLineSegment(sketch, "E2017", {"start": v(-117.03, 5.21) * mm, "end": v(-117.38, 5.08) * mm});
            skLineSegment(sketch, "E2018", {"start": v(-117.38, 5.08) * mm, "end": v(-117.72, 4.94) * mm});
            skLineSegment(sketch, "E2019", {"start": v(-117.72, 4.94) * mm, "end": v(-118.07, 4.8) * mm});
            skLineSegment(sketch, "E2020", {"start": v(-118.07, 4.8) * mm, "end": v(-118.43, 4.65) * mm});
            skLineSegment(sketch, "E2021", {"start": v(-118.43, 4.65) * mm, "end": v(-118.8, 4.5) * mm});
            skLineSegment(sketch, "E2022", {"start": v(-118.8, 4.5) * mm, "end": v(-119.16, 4.34) * mm});
            skLineSegment(sketch, "E2023", {"start": v(-119.16, 4.34) * mm, "end": v(-119.27, 4.16) * mm});
            skLineSegment(sketch, "E2024", {"start": v(-119.27, 4.16) * mm, "end": v(-119.34, 0.66) * mm});
            skLineSegment(sketch, "E2025", {"start": v(-119.34, 0.66) * mm, "end": v(-119.24, 0.48) * mm});
            skLineSegment(sketch, "E2026", {"start": v(-119.24, 0.48) * mm, "end": v(-118.88, 0.3) * mm});
            skLineSegment(sketch, "E2027", {"start": v(-118.88, 0.3) * mm, "end": v(-118.52, 0.14) * mm});
            skLineSegment(sketch, "E2028", {"start": v(-118.52, 0.14) * mm, "end": v(-118.17, -0.03) * mm});
            skLineSegment(sketch, "E2029", {"start": v(-118.17, -0.03) * mm, "end": v(-117.83, -0.18) * mm});
            skLineSegment(sketch, "E2030", {"start": v(-117.83, -0.18) * mm, "end": v(-117.49, -0.34) * mm});
            skLineSegment(sketch, "E2031", {"start": v(-117.49, -0.34) * mm, "end": v(-117.15, -0.48) * mm});
            skLineSegment(sketch, "E2032", {"start": v(-117.15, -0.48) * mm, "end": v(-116.82, -0.62) * mm});
            skLineSegment(sketch, "E2033", {"start": v(-116.82, -0.62) * mm, "end": v(-116.5, -0.76) * mm});
            skLineSegment(sketch, "E2034", {"start": v(-116.5, -0.76) * mm, "end": v(-116.17, -0.9) * mm});
            skLineSegment(sketch, "E2035", {"start": v(-116.17, -0.9) * mm, "end": v(-115.85, -1.02) * mm});
            skLineSegment(sketch, "E2036", {"start": v(-115.85, -1.02) * mm, "end": v(-115.54, -1.14) * mm});
            skLineSegment(sketch, "E2037", {"start": v(-115.54, -1.14) * mm, "end": v(-115.24, -1.26) * mm});
            skLineSegment(sketch, "E2038", {"start": v(-115.24, -1.26) * mm, "end": v(-114.94, -1.37) * mm});
            skLineSegment(sketch, "E2039", {"start": v(-114.94, -1.37) * mm, "end": v(-114.64, -1.48) * mm});
            skLineSegment(sketch, "E2040", {"start": v(-114.64, -1.48) * mm, "end": v(-114.35, -1.58) * mm});
            skLineSegment(sketch, "E2041", {"start": v(-114.35, -1.58) * mm, "end": v(-114.06, -1.68) * mm});
            skLineSegment(sketch, "E2042", {"start": v(-114.06, -1.68) * mm, "end": v(-113.78, -1.78) * mm});
            skLineSegment(sketch, "E2043", {"start": v(-113.78, -1.78) * mm, "end": v(-113.5, -1.87) * mm});
            skLineSegment(sketch, "E2044", {"start": v(-113.5, -1.87) * mm, "end": v(-113.24, -1.95) * mm});
            skLineSegment(sketch, "E2045", {"start": v(-113.24, -1.95) * mm, "end": v(-112.98, -2.04) * mm});
            skLineSegment(sketch, "E2046", {"start": v(-112.98, -2.04) * mm, "end": v(-112.72, -2.11) * mm});
            skLineSegment(sketch, "E2047", {"start": v(-112.72, -2.11) * mm, "end": v(-112.47, -2.19) * mm});
            skLineSegment(sketch, "E2048", {"start": v(-112.47, -2.19) * mm, "end": v(-112.22, -2.26) * mm});
            skLineSegment(sketch, "E2049", {"start": v(-112.22, -2.26) * mm, "end": v(-111.98, -2.33) * mm});
            skLineSegment(sketch, "E2050", {"start": v(-111.98, -2.33) * mm, "end": v(-111.74, -2.4) * mm});
            skLineSegment(sketch, "E2051", {"start": v(-111.74, -2.4) * mm, "end": v(-111.51, -2.45) * mm});
            skLineSegment(sketch, "E2052", {"start": v(-111.51, -2.45) * mm, "end": v(-111.29, -2.5) * mm});
            skLineSegment(sketch, "E2053", {"start": v(-111.29, -2.5) * mm, "end": v(-111.07, -2.56) * mm});
            skLineSegment(sketch, "E2054", {"start": v(-111.07, -2.56) * mm, "end": v(-110.86, -2.61) * mm});
            skLineSegment(sketch, "E2055", {"start": v(-110.86, -2.61) * mm, "end": v(-110.65, -2.66) * mm});
            skLineSegment(sketch, "E2056", {"start": v(-110.65, -2.66) * mm, "end": v(-110.45, -2.7) * mm});
            skLineSegment(sketch, "E2057", {"start": v(-110.45, -2.7) * mm, "end": v(-110.26, -2.75) * mm});
            skLineSegment(sketch, "E2058", {"start": v(-110.26, -2.75) * mm, "end": v(-110.07, -2.78) * mm});
            skLineSegment(sketch, "E2059", {"start": v(-110.07, -2.78) * mm, "end": v(-109.89, -2.82) * mm});
            skLineSegment(sketch, "E2060", {"start": v(-109.89, -2.82) * mm, "end": v(-109.7, -2.85) * mm});
            skLineSegment(sketch, "E2061", {"start": v(-109.7, -2.85) * mm, "end": v(-109.54, -2.88) * mm});
            skLineSegment(sketch, "E2062", {"start": v(-109.54, -2.88) * mm, "end": v(-109.38, -2.91) * mm});
            skLineSegment(sketch, "E2063", {"start": v(-109.38, -2.91) * mm, "end": v(-109.22, -2.94) * mm});
            skLineSegment(sketch, "E2064", {"start": v(-109.22, -2.94) * mm, "end": v(-109.07, -2.96) * mm});
            skLineSegment(sketch, "E2065", {"start": v(-109.07, -2.96) * mm, "end": v(-108.92, -2.98) * mm});
            skLineSegment(sketch, "E2066", {"start": v(-108.92, -2.98) * mm, "end": v(-108.78, -3) * mm});
            skLineSegment(sketch, "E2067", {"start": v(-108.78, -3) * mm, "end": v(-108.65, -3.02) * mm});
            skLineSegment(sketch, "E2068", {"start": v(-108.65, -3.02) * mm, "end": v(-108.38, -3.15) * mm});
            skLineSegment(sketch, "E2069", {"start": v(-108.38, -3.15) * mm, "end": v(-108.16, -7.62) * mm});
            skLineSegment(sketch, "E2070", {"start": v(-108.16, -7.62) * mm, "end": v(-108.41, -7.77) * mm});
            skLineSegment(sketch, "E2071", {"start": v(-108.41, -7.77) * mm, "end": v(-108.54, -7.8) * mm});
            skLineSegment(sketch, "E2072", {"start": v(-108.54, -7.8) * mm, "end": v(-108.68, -7.84) * mm});
            skLineSegment(sketch, "E2073", {"start": v(-108.68, -7.84) * mm, "end": v(-108.82, -7.87) * mm});
            skLineSegment(sketch, "E2074", {"start": v(-108.82, -7.87) * mm, "end": v(-108.97, -7.9) * mm});
            skLineSegment(sketch, "E2075", {"start": v(-108.97, -7.9) * mm, "end": v(-109.13, -7.95) * mm});
            skLineSegment(sketch, "E2076", {"start": v(-109.13, -7.95) * mm, "end": v(-109.29, -8) * mm});
            skLineSegment(sketch, "E2077", {"start": v(-109.29, -8) * mm, "end": v(-109.45, -8.04) * mm});
            skLineSegment(sketch, "E2078", {"start": v(-109.45, -8.04) * mm, "end": v(-109.63, -8.1) * mm});
            skLineSegment(sketch, "E2079", {"start": v(-109.63, -8.1) * mm, "end": v(-109.8, -8.15) * mm});
            skLineSegment(sketch, "E2080", {"start": v(-109.8, -8.15) * mm, "end": v(-109.99, -8.2) * mm});
            skLineSegment(sketch, "E2081", {"start": v(-109.99, -8.2) * mm, "end": v(-110.18, -8.26) * mm});
            skLineSegment(sketch, "E2082", {"start": v(-110.18, -8.26) * mm, "end": v(-110.37, -8.33) * mm});
            skLineSegment(sketch, "E2083", {"start": v(-110.37, -8.33) * mm, "end": v(-110.57, -8.4) * mm});
            skLineSegment(sketch, "E2084", {"start": v(-110.57, -8.4) * mm, "end": v(-110.78, -8.47) * mm});
            skLineSegment(sketch, "E2085", {"start": v(-110.78, -8.47) * mm, "end": v(-111, -8.54) * mm});
            skLineSegment(sketch, "E2086", {"start": v(-111, -8.54) * mm, "end": v(-111.2, -8.62) * mm});
            skLineSegment(sketch, "E2087", {"start": v(-111.2, -8.62) * mm, "end": v(-111.43, -8.7) * mm});
            skLineSegment(sketch, "E2088", {"start": v(-111.43, -8.7) * mm, "end": v(-111.66, -8.79) * mm});
            skLineSegment(sketch, "E2089", {"start": v(-111.66, -8.79) * mm, "end": v(-111.9, -8.88) * mm});
            skLineSegment(sketch, "E2090", {"start": v(-111.9, -8.88) * mm, "end": v(-112.13, -8.97) * mm});
            skLineSegment(sketch, "E2091", {"start": v(-112.13, -8.97) * mm, "end": v(-112.38, -9.07) * mm});
            skLineSegment(sketch, "E2092", {"start": v(-112.38, -9.07) * mm, "end": v(-112.62, -9.18) * mm});
            skLineSegment(sketch, "E2093", {"start": v(-112.62, -9.18) * mm, "end": v(-112.88, -9.28) * mm});
            skLineSegment(sketch, "E2094", {"start": v(-112.88, -9.28) * mm, "end": v(-113.14, -9.4) * mm});
            skLineSegment(sketch, "E2095", {"start": v(-113.14, -9.4) * mm, "end": v(-113.4, -9.51) * mm});
            skLineSegment(sketch, "E2096", {"start": v(-113.4, -9.51) * mm, "end": v(-113.67, -9.64) * mm});
            skLineSegment(sketch, "E2097", {"start": v(-113.67, -9.64) * mm, "end": v(-113.95, -9.76) * mm});
            skLineSegment(sketch, "E2098", {"start": v(-113.95, -9.76) * mm, "end": v(-114.22, -9.9) * mm});
            skLineSegment(sketch, "E2099", {"start": v(-114.22, -9.9) * mm, "end": v(-114.5, -10.03) * mm});
            skLineSegment(sketch, "E2100", {"start": v(-114.5, -10.03) * mm, "end": v(-114.8, -10.17) * mm});
            skLineSegment(sketch, "E2101", {"start": v(-114.8, -10.17) * mm, "end": v(-115.1, -10.32) * mm});
            skLineSegment(sketch, "E2102", {"start": v(-115.1, -10.32) * mm, "end": v(-115.39, -10.47) * mm});
            skLineSegment(sketch, "E2103", {"start": v(-115.39, -10.47) * mm, "end": v(-115.7, -10.63) * mm});
            skLineSegment(sketch, "E2104", {"start": v(-115.7, -10.63) * mm, "end": v(-116, -10.8) * mm});
            skLineSegment(sketch, "E2105", {"start": v(-116, -10.8) * mm, "end": v(-116.3, -10.96) * mm});
            skLineSegment(sketch, "E2106", {"start": v(-116.3, -10.96) * mm, "end": v(-116.63, -11.13) * mm});
            skLineSegment(sketch, "E2107", {"start": v(-116.63, -11.13) * mm, "end": v(-116.95, -11.31) * mm});
            skLineSegment(sketch, "E2108", {"start": v(-116.95, -11.31) * mm, "end": v(-117.27, -11.5) * mm});
            skLineSegment(sketch, "E2109", {"start": v(-117.27, -11.5) * mm, "end": v(-117.6, -11.69) * mm});
            skLineSegment(sketch, "E2110", {"start": v(-117.6, -11.69) * mm, "end": v(-117.93, -11.88) * mm});
            skLineSegment(sketch, "E2111", {"start": v(-117.93, -11.88) * mm, "end": v(-118.27, -12.09) * mm});
            skLineSegment(sketch, "E2112", {"start": v(-118.27, -12.09) * mm, "end": v(-118.6, -12.3) * mm});
            skLineSegment(sketch, "E2113", {"start": v(-118.6, -12.3) * mm, "end": v(-118.7, -12.48) * mm});
            skLineSegment(sketch, "E2114", {"start": v(-118.7, -12.48) * mm, "end": v(-118.28, -15.97) * mm});
            skLineSegment(sketch, "E2115", {"start": v(-118.28, -15.97) * mm, "end": v(-118.15, -16.13) * mm});
            skLineSegment(sketch, "E2116", {"start": v(-118.15, -16.13) * mm, "end": v(-117.77, -16.25) * mm});
            skLineSegment(sketch, "E2117", {"start": v(-117.77, -16.25) * mm, "end": v(-117.4, -16.37) * mm});
            skLineSegment(sketch, "E2118", {"start": v(-117.4, -16.37) * mm, "end": v(-117.03, -16.48) * mm});
            skLineSegment(sketch, "E2119", {"start": v(-117.03, -16.48) * mm, "end": v(-116.66, -16.59) * mm});
            skLineSegment(sketch, "E2120", {"start": v(-116.66, -16.59) * mm, "end": v(-116.3, -16.7) * mm});
            skLineSegment(sketch, "E2121", {"start": v(-116.3, -16.7) * mm, "end": v(-115.95, -16.79) * mm});
            skLineSegment(sketch, "E2122", {"start": v(-115.95, -16.79) * mm, "end": v(-115.6, -16.88) * mm});
            skLineSegment(sketch, "E2123", {"start": v(-115.6, -16.88) * mm, "end": v(-115.26, -16.97) * mm});
            skLineSegment(sketch, "E2124", {"start": v(-115.26, -16.97) * mm, "end": v(-114.92, -17.06) * mm});
            skLineSegment(sketch, "E2125", {"start": v(-114.92, -17.06) * mm, "end": v(-114.6, -17.14) * mm});
            skLineSegment(sketch, "E2126", {"start": v(-114.6, -17.14) * mm, "end": v(-114.27, -17.22) * mm});
            skLineSegment(sketch, "E2127", {"start": v(-114.27, -17.22) * mm, "end": v(-113.95, -17.29) * mm});
            skLineSegment(sketch, "E2128", {"start": v(-113.95, -17.29) * mm, "end": v(-113.63, -17.36) * mm});
            skLineSegment(sketch, "E2129", {"start": v(-113.63, -17.36) * mm, "end": v(-113.32, -17.42) * mm});
            skLineSegment(sketch, "E2130", {"start": v(-113.32, -17.42) * mm, "end": v(-113.02, -17.49) * mm});
            skLineSegment(sketch, "E2131", {"start": v(-113.02, -17.49) * mm, "end": v(-112.73, -17.55) * mm});
            skLineSegment(sketch, "E2132", {"start": v(-112.73, -17.55) * mm, "end": v(-112.44, -17.6) * mm});
            skLineSegment(sketch, "E2133", {"start": v(-112.44, -17.6) * mm, "end": v(-112.15, -17.65) * mm});
            skLineSegment(sketch, "E2134", {"start": v(-112.15, -17.65) * mm, "end": v(-111.87, -17.7) * mm});
            skLineSegment(sketch, "E2135", {"start": v(-111.87, -17.7) * mm, "end": v(-111.6, -17.74) * mm});
            skLineSegment(sketch, "E2136", {"start": v(-111.6, -17.74) * mm, "end": v(-111.33, -17.79) * mm});
            skLineSegment(sketch, "E2137", {"start": v(-111.33, -17.79) * mm, "end": v(-111.07, -17.82) * mm});
            skLineSegment(sketch, "E2138", {"start": v(-111.07, -17.82) * mm, "end": v(-110.82, -17.86) * mm});
            skLineSegment(sketch, "E2139", {"start": v(-110.82, -17.86) * mm, "end": v(-110.57, -17.9) * mm});
            skLineSegment(sketch, "E2140", {"start": v(-110.57, -17.9) * mm, "end": v(-110.33, -17.92) * mm});
            skLineSegment(sketch, "E2141", {"start": v(-110.33, -17.92) * mm, "end": v(-110.1, -17.95) * mm});
            skLineSegment(sketch, "E2142", {"start": v(-110.1, -17.95) * mm, "end": v(-109.86, -17.98) * mm});
            skLineSegment(sketch, "E2143", {"start": v(-109.86, -17.98) * mm, "end": v(-109.64, -18) * mm});
            skLineSegment(sketch, "E2144", {"start": v(-109.64, -18) * mm, "end": v(-109.42, -18.02) * mm});
            skLineSegment(sketch, "E2145", {"start": v(-109.42, -18.02) * mm, "end": v(-109.21, -18.04) * mm});
            skLineSegment(sketch, "E2146", {"start": v(-109.21, -18.04) * mm, "end": v(-109, -18.05) * mm});
            skLineSegment(sketch, "E2147", {"start": v(-109, -18.05) * mm, "end": v(-108.8, -18.07) * mm});
            skLineSegment(sketch, "E2148", {"start": v(-108.8, -18.07) * mm, "end": v(-108.62, -18.08) * mm});
            skLineSegment(sketch, "E2149", {"start": v(-108.62, -18.08) * mm, "end": v(-108.43, -18.1) * mm});
            skLineSegment(sketch, "E2150", {"start": v(-108.43, -18.1) * mm, "end": v(-108.25, -18.1) * mm});
            skLineSegment(sketch, "E2151", {"start": v(-108.25, -18.1) * mm, "end": v(-108.08, -18.1) * mm});
            skLineSegment(sketch, "E2152", {"start": v(-108.08, -18.1) * mm, "end": v(-107.91, -18.11) * mm});
            skLineSegment(sketch, "E2153", {"start": v(-107.91, -18.11) * mm, "end": v(-107.75, -18.12) * mm});
            skLineSegment(sketch, "E2154", {"start": v(-107.75, -18.12) * mm, "end": v(-107.6, -18.12) * mm});
            skLineSegment(sketch, "E2155", {"start": v(-107.6, -18.12) * mm, "end": v(-107.45, -18.12) * mm});
            skLineSegment(sketch, "E2156", {"start": v(-107.45, -18.12) * mm, "end": v(-107.31, -18.12) * mm});
            skLineSegment(sketch, "E2157", {"start": v(-107.31, -18.12) * mm, "end": v(-107.18, -18.12) * mm});
            skLineSegment(sketch, "E2158", {"start": v(-107.18, -18.12) * mm, "end": v(-106.9, -18.2) * mm});
            skLineSegment(sketch, "E2159", {"start": v(-106.9, -18.2) * mm, "end": v(-106.05, -22.6) * mm});
            skLineSegment(sketch, "E2160", {"start": v(-106.05, -22.6) * mm, "end": v(-106.28, -22.79) * mm});
            skLineSegment(sketch, "E2161", {"start": v(-106.28, -22.79) * mm, "end": v(-106.4, -22.84) * mm});
            skLineSegment(sketch, "E2162", {"start": v(-106.4, -22.84) * mm, "end": v(-106.54, -22.9) * mm});
            skLineSegment(sketch, "E2163", {"start": v(-106.54, -22.9) * mm, "end": v(-106.68, -22.95) * mm});
            skLineSegment(sketch, "E2164", {"start": v(-106.68, -22.95) * mm, "end": v(-106.82, -23) * mm});
            skLineSegment(sketch, "E2165", {"start": v(-106.82, -23) * mm, "end": v(-106.97, -23.07) * mm});
            skLineSegment(sketch, "E2166", {"start": v(-106.97, -23.07) * mm, "end": v(-107.12, -23.13) * mm});
            skLineSegment(sketch, "E2167", {"start": v(-107.12, -23.13) * mm, "end": v(-107.28, -23.2) * mm});
            skLineSegment(sketch, "E2168", {"start": v(-107.28, -23.2) * mm, "end": v(-107.44, -23.28) * mm});
            skLineSegment(sketch, "E2169", {"start": v(-107.44, -23.28) * mm, "end": v(-107.6, -23.35) * mm});
            skLineSegment(sketch, "E2170", {"start": v(-107.6, -23.35) * mm, "end": v(-107.78, -23.44) * mm});
            skLineSegment(sketch, "E2171", {"start": v(-107.78, -23.44) * mm, "end": v(-107.96, -23.52) * mm});
            skLineSegment(sketch, "E2172", {"start": v(-107.96, -23.52) * mm, "end": v(-108.14, -23.61) * mm});
            skLineSegment(sketch, "E2173", {"start": v(-108.14, -23.61) * mm, "end": v(-108.33, -23.7) * mm});
            skLineSegment(sketch, "E2174", {"start": v(-108.33, -23.7) * mm, "end": v(-108.53, -23.8) * mm});
            skLineSegment(sketch, "E2175", {"start": v(-108.53, -23.8) * mm, "end": v(-108.73, -23.91) * mm});
            skLineSegment(sketch, "E2176", {"start": v(-108.73, -23.91) * mm, "end": v(-108.93, -24.02) * mm});
            skLineSegment(sketch, "E2177", {"start": v(-108.93, -24.02) * mm, "end": v(-109.14, -24.13) * mm});
            skLineSegment(sketch, "E2178", {"start": v(-109.14, -24.13) * mm, "end": v(-109.35, -24.25) * mm});
            skLineSegment(sketch, "E2179", {"start": v(-109.35, -24.25) * mm, "end": v(-109.57, -24.37) * mm});
            skLineSegment(sketch, "E2180", {"start": v(-109.57, -24.37) * mm, "end": v(-109.8, -24.5) * mm});
            skLineSegment(sketch, "E2181", {"start": v(-109.8, -24.5) * mm, "end": v(-110.02, -24.63) * mm});
            skLineSegment(sketch, "E2182", {"start": v(-110.02, -24.63) * mm, "end": v(-110.26, -24.77) * mm});
            skLineSegment(sketch, "E2183", {"start": v(-110.26, -24.77) * mm, "end": v(-110.5, -24.9) * mm});
            skLineSegment(sketch, "E2184", {"start": v(-110.5, -24.9) * mm, "end": v(-110.74, -25.06) * mm});
            skLineSegment(sketch, "E2185", {"start": v(-110.74, -25.06) * mm, "end": v(-110.98, -25.21) * mm});
            skLineSegment(sketch, "E2186", {"start": v(-110.98, -25.21) * mm, "end": v(-111.23, -25.37) * mm});
            skLineSegment(sketch, "E2187", {"start": v(-111.23, -25.37) * mm, "end": v(-111.49, -25.53) * mm});
            skLineSegment(sketch, "E2188", {"start": v(-111.49, -25.53) * mm, "end": v(-111.74, -25.7) * mm});
            skLineSegment(sketch, "E2189", {"start": v(-111.74, -25.7) * mm, "end": v(-112, -25.88) * mm});
            skLineSegment(sketch, "E2190", {"start": v(-112, -25.88) * mm, "end": v(-112.27, -26.06) * mm});
            skLineSegment(sketch, "E2191", {"start": v(-112.27, -26.06) * mm, "end": v(-112.54, -26.24) * mm});
            skLineSegment(sketch, "E2192", {"start": v(-112.54, -26.24) * mm, "end": v(-112.82, -26.43) * mm});
            skLineSegment(sketch, "E2193", {"start": v(-112.82, -26.43) * mm, "end": v(-113.1, -26.63) * mm});
            skLineSegment(sketch, "E2194", {"start": v(-113.1, -26.63) * mm, "end": v(-113.37, -26.84) * mm});
            skLineSegment(sketch, "E2195", {"start": v(-113.37, -26.84) * mm, "end": v(-113.66, -27.04) * mm});
            skLineSegment(sketch, "E2196", {"start": v(-113.66, -27.04) * mm, "end": v(-113.95, -27.26) * mm});
            skLineSegment(sketch, "E2197", {"start": v(-113.95, -27.26) * mm, "end": v(-114.24, -27.48) * mm});
            skLineSegment(sketch, "E2198", {"start": v(-114.24, -27.48) * mm, "end": v(-114.54, -27.71) * mm});
            skLineSegment(sketch, "E2199", {"start": v(-114.54, -27.71) * mm, "end": v(-114.83, -27.94) * mm});
            skLineSegment(sketch, "E2200", {"start": v(-114.83, -27.94) * mm, "end": v(-115.14, -28.19) * mm});
            skLineSegment(sketch, "E2201", {"start": v(-115.14, -28.19) * mm, "end": v(-115.44, -28.43) * mm});
            skLineSegment(sketch, "E2202", {"start": v(-115.44, -28.43) * mm, "end": v(-115.75, -28.69) * mm});
            skLineSegment(sketch, "E2203", {"start": v(-115.75, -28.69) * mm, "end": v(-115.81, -28.88) * mm});
            skLineSegment(sketch, "E2204", {"start": v(-115.81, -28.88) * mm, "end": v(-114.91, -32.28) * mm});
            skLineSegment(sketch, "E2205", {"start": v(-114.91, -32.28) * mm, "end": v(-114.76, -32.42) * mm});
            skLineSegment(sketch, "E2206", {"start": v(-114.76, -32.42) * mm, "end": v(-114.37, -32.49) * mm});
            skLineSegment(sketch, "E2207", {"start": v(-114.37, -32.49) * mm, "end": v(-113.98, -32.55) * mm});
            skLineSegment(sketch, "E2208", {"start": v(-113.98, -32.55) * mm, "end": v(-113.6, -32.61) * mm});
            skLineSegment(sketch, "E2209", {"start": v(-113.6, -32.61) * mm, "end": v(-113.22, -32.67) * mm});
            skLineSegment(sketch, "E2210", {"start": v(-113.22, -32.67) * mm, "end": v(-112.85, -32.72) * mm});
            skLineSegment(sketch, "E2211", {"start": v(-112.85, -32.72) * mm, "end": v(-112.5, -32.77) * mm});
            skLineSegment(sketch, "E2212", {"start": v(-112.5, -32.77) * mm, "end": v(-112.13, -32.81) * mm});
            skLineSegment(sketch, "E2213", {"start": v(-112.13, -32.81) * mm, "end": v(-111.78, -32.85) * mm});
            skLineSegment(sketch, "E2214", {"start": v(-111.78, -32.85) * mm, "end": v(-111.44, -32.9) * mm});
            skLineSegment(sketch, "E2215", {"start": v(-111.44, -32.9) * mm, "end": v(-111.1, -32.93) * mm});
            skLineSegment(sketch, "E2216", {"start": v(-111.1, -32.93) * mm, "end": v(-110.76, -32.96) * mm});
            skLineSegment(sketch, "E2217", {"start": v(-110.76, -32.96) * mm, "end": v(-110.44, -32.99) * mm});
            skLineSegment(sketch, "E2218", {"start": v(-110.44, -32.99) * mm, "end": v(-110.12, -33.01) * mm});
            skLineSegment(sketch, "E2219", {"start": v(-110.12, -33.01) * mm, "end": v(-109.8, -33.03) * mm});
            skLineSegment(sketch, "E2220", {"start": v(-109.8, -33.03) * mm, "end": v(-109.5, -33.05) * mm});
            skLineSegment(sketch, "E2221", {"start": v(-109.5, -33.05) * mm, "end": v(-109.2, -33.07) * mm});
            skLineSegment(sketch, "E2222", {"start": v(-109.2, -33.07) * mm, "end": v(-108.9, -33.08) * mm});
            skLineSegment(sketch, "E2223", {"start": v(-108.9, -33.08) * mm, "end": v(-108.6, -33.1) * mm});
            skLineSegment(sketch, "E2224", {"start": v(-108.6, -33.1) * mm, "end": v(-108.33, -33.1) * mm});
            skLineSegment(sketch, "E2225", {"start": v(-108.33, -33.1) * mm, "end": v(-108.05, -33.1) * mm});
            skLineSegment(sketch, "E2226", {"start": v(-108.05, -33.1) * mm, "end": v(-107.78, -33.11) * mm});
            skLineSegment(sketch, "E2227", {"start": v(-107.78, -33.11) * mm, "end": v(-107.52, -33.12) * mm});
            skLineSegment(sketch, "E2228", {"start": v(-107.52, -33.12) * mm, "end": v(-107.26, -33.12) * mm});
            skLineSegment(sketch, "E2229", {"start": v(-107.26, -33.12) * mm, "end": v(-107.01, -33.11) * mm});
            skLineSegment(sketch, "E2230", {"start": v(-107.01, -33.11) * mm, "end": v(-106.77, -33.11) * mm});
            skLineSegment(sketch, "E2231", {"start": v(-106.77, -33.11) * mm, "end": v(-106.53, -33.1) * mm});
            skLineSegment(sketch, "E2232", {"start": v(-106.53, -33.1) * mm, "end": v(-106.3, -33.1) * mm});
            skLineSegment(sketch, "E2233", {"start": v(-106.3, -33.1) * mm, "end": v(-106.07, -33.09) * mm});
            skLineSegment(sketch, "E2234", {"start": v(-106.07, -33.09) * mm, "end": v(-105.86, -33.08) * mm});
            skLineSegment(sketch, "E2235", {"start": v(-105.86, -33.08) * mm, "end": v(-105.64, -33.07) * mm});
            skLineSegment(sketch, "E2236", {"start": v(-105.64, -33.07) * mm, "end": v(-105.44, -33.06) * mm});
            skLineSegment(sketch, "E2237", {"start": v(-105.44, -33.06) * mm, "end": v(-105.24, -33.04) * mm});
            skLineSegment(sketch, "E2238", {"start": v(-105.24, -33.04) * mm, "end": v(-105.05, -33.03) * mm});
            skLineSegment(sketch, "E2239", {"start": v(-105.05, -33.03) * mm, "end": v(-104.86, -33.01) * mm});
            skLineSegment(sketch, "E2240", {"start": v(-104.86, -33.01) * mm, "end": v(-104.69, -33) * mm});
            skLineSegment(sketch, "E2241", {"start": v(-104.69, -33) * mm, "end": v(-104.51, -32.98) * mm});
            skLineSegment(sketch, "E2242", {"start": v(-104.51, -32.98) * mm, "end": v(-104.35, -32.96) * mm});
            skLineSegment(sketch, "E2243", {"start": v(-104.35, -32.96) * mm, "end": v(-104.19, -32.94) * mm});
            skLineSegment(sketch, "E2244", {"start": v(-104.19, -32.94) * mm, "end": v(-104.04, -32.92) * mm});
            skLineSegment(sketch, "E2245", {"start": v(-104.04, -32.92) * mm, "end": v(-103.9, -32.9) * mm});
            skLineSegment(sketch, "E2246", {"start": v(-103.9, -32.9) * mm, "end": v(-103.75, -32.88) * mm});
            skLineSegment(sketch, "E2247", {"start": v(-103.75, -32.88) * mm, "end": v(-103.62, -32.86) * mm});
            skLineSegment(sketch, "E2248", {"start": v(-103.62, -32.86) * mm, "end": v(-103.32, -32.91) * mm});
            skLineSegment(sketch, "E2249", {"start": v(-103.32, -32.91) * mm, "end": v(-101.88, -37.14) * mm});
            skLineSegment(sketch, "E2250", {"start": v(-101.88, -37.14) * mm, "end": v(-102.09, -37.37) * mm});
            skLineSegment(sketch, "E2251", {"start": v(-102.09, -37.37) * mm, "end": v(-102.2, -37.43) * mm});
            skLineSegment(sketch, "E2252", {"start": v(-102.2, -37.43) * mm, "end": v(-102.32, -37.5) * mm});
            skLineSegment(sketch, "E2253", {"start": v(-102.32, -37.5) * mm, "end": v(-102.45, -37.57) * mm});
            skLineSegment(sketch, "E2254", {"start": v(-102.45, -37.57) * mm, "end": v(-102.58, -37.65) * mm});
            skLineSegment(sketch, "E2255", {"start": v(-102.58, -37.65) * mm, "end": v(-102.72, -37.73) * mm});
            skLineSegment(sketch, "E2256", {"start": v(-102.72, -37.73) * mm, "end": v(-102.86, -37.82) * mm});
            skLineSegment(sketch, "E2257", {"start": v(-102.86, -37.82) * mm, "end": v(-103, -37.91) * mm});
            skLineSegment(sketch, "E2258", {"start": v(-103, -37.91) * mm, "end": v(-103.16, -38) * mm});
            skLineSegment(sketch, "E2259", {"start": v(-103.16, -38) * mm, "end": v(-103.32, -38.1) * mm});
            skLineSegment(sketch, "E2260", {"start": v(-103.32, -38.1) * mm, "end": v(-103.48, -38.22) * mm});
            skLineSegment(sketch, "E2261", {"start": v(-103.48, -38.22) * mm, "end": v(-103.64, -38.32) * mm});
            skLineSegment(sketch, "E2262", {"start": v(-103.64, -38.32) * mm, "end": v(-103.81, -38.44) * mm});
            skLineSegment(sketch, "E2263", {"start": v(-103.81, -38.44) * mm, "end": v(-103.99, -38.56) * mm});
            skLineSegment(sketch, "E2264", {"start": v(-103.99, -38.56) * mm, "end": v(-104.17, -38.69) * mm});
            skLineSegment(sketch, "E2265", {"start": v(-104.17, -38.69) * mm, "end": v(-104.35, -38.82) * mm});
            skLineSegment(sketch, "E2266", {"start": v(-104.35, -38.82) * mm, "end": v(-104.54, -38.95) * mm});
            skLineSegment(sketch, "E2267", {"start": v(-104.54, -38.95) * mm, "end": v(-104.73, -39.1) * mm});
            skLineSegment(sketch, "E2268", {"start": v(-104.73, -39.1) * mm, "end": v(-104.92, -39.24) * mm});
            skLineSegment(sketch, "E2269", {"start": v(-104.92, -39.24) * mm, "end": v(-105.12, -39.39) * mm});
            skLineSegment(sketch, "E2270", {"start": v(-105.12, -39.39) * mm, "end": v(-105.33, -39.55) * mm});
            skLineSegment(sketch, "E2271", {"start": v(-105.33, -39.55) * mm, "end": v(-105.53, -39.7) * mm});
            skLineSegment(sketch, "E2272", {"start": v(-105.53, -39.7) * mm, "end": v(-105.74, -39.88) * mm});
            skLineSegment(sketch, "E2273", {"start": v(-105.74, -39.88) * mm, "end": v(-105.96, -40.05) * mm});
            skLineSegment(sketch, "E2274", {"start": v(-105.96, -40.05) * mm, "end": v(-106.18, -40.23) * mm});
            skLineSegment(sketch, "E2275", {"start": v(-106.18, -40.23) * mm, "end": v(-106.4, -40.42) * mm});
            skLineSegment(sketch, "E2276", {"start": v(-106.4, -40.42) * mm, "end": v(-106.62, -40.6) * mm});
            skLineSegment(sketch, "E2277", {"start": v(-106.62, -40.6) * mm, "end": v(-106.85, -40.8) * mm});
            skLineSegment(sketch, "E2278", {"start": v(-106.85, -40.8) * mm, "end": v(-107.08, -41) * mm});
            skLineSegment(sketch, "E2279", {"start": v(-107.08, -41) * mm, "end": v(-107.32, -41.22) * mm});
            skLineSegment(sketch, "E2280", {"start": v(-107.32, -41.22) * mm, "end": v(-107.56, -41.43) * mm});
            skLineSegment(sketch, "E2281", {"start": v(-107.56, -41.43) * mm, "end": v(-107.8, -41.66) * mm});
            skLineSegment(sketch, "E2282", {"start": v(-107.8, -41.66) * mm, "end": v(-108.04, -41.88) * mm});
            skLineSegment(sketch, "E2283", {"start": v(-108.04, -41.88) * mm, "end": v(-108.3, -42.12) * mm});
            skLineSegment(sketch, "E2284", {"start": v(-108.3, -42.12) * mm, "end": v(-108.54, -42.36) * mm});
            skLineSegment(sketch, "E2285", {"start": v(-108.54, -42.36) * mm, "end": v(-108.8, -42.6) * mm});
            skLineSegment(sketch, "E2286", {"start": v(-108.8, -42.6) * mm, "end": v(-109.05, -42.86) * mm});
            skLineSegment(sketch, "E2287", {"start": v(-109.05, -42.86) * mm, "end": v(-109.3, -43.12) * mm});
            skLineSegment(sketch, "E2288", {"start": v(-109.3, -43.12) * mm, "end": v(-109.57, -43.39) * mm});
            skLineSegment(sketch, "E2289", {"start": v(-109.57, -43.39) * mm, "end": v(-109.83, -43.66) * mm});
            skLineSegment(sketch, "E2290", {"start": v(-109.83, -43.66) * mm, "end": v(-110.1, -43.94) * mm});
            skLineSegment(sketch, "E2291", {"start": v(-110.1, -43.94) * mm, "end": v(-110.37, -44.23) * mm});
            skLineSegment(sketch, "E2292", {"start": v(-110.37, -44.23) * mm, "end": v(-110.64, -44.52) * mm});
            skLineSegment(sketch, "E2293", {"start": v(-110.64, -44.52) * mm, "end": v(-110.67, -44.73) * mm});
            skLineSegment(sketch, "E2294", {"start": v(-110.67, -44.73) * mm, "end": v(-109.3, -47.96) * mm});
            skLineSegment(sketch, "E2295", {"start": v(-109.3, -47.96) * mm, "end": v(-109.14, -48.08) * mm});
            skLineSegment(sketch, "E2296", {"start": v(-109.14, -48.08) * mm, "end": v(-108.74, -48.1) * mm});
            skLineSegment(sketch, "E2297", {"start": v(-108.74, -48.1) * mm, "end": v(-108.35, -48.1) * mm});
            skLineSegment(sketch, "E2298", {"start": v(-108.35, -48.1) * mm, "end": v(-107.96, -48.1) * mm});
            skLineSegment(sketch, "E2299", {"start": v(-107.96, -48.1) * mm, "end": v(-107.58, -48.11) * mm});
            skLineSegment(sketch, "E2300", {"start": v(-107.58, -48.11) * mm, "end": v(-107.2, -48.11) * mm});
            skLineSegment(sketch, "E2301", {"start": v(-107.2, -48.11) * mm, "end": v(-106.84, -48.1) * mm});
            skLineSegment(sketch, "E2302", {"start": v(-106.84, -48.1) * mm, "end": v(-106.48, -48.1) * mm});
            skLineSegment(sketch, "E2303", {"start": v(-106.48, -48.1) * mm, "end": v(-106.13, -48.1) * mm});
            skLineSegment(sketch, "E2304", {"start": v(-106.13, -48.1) * mm, "end": v(-105.78, -48.09) * mm});
            skLineSegment(sketch, "E2305", {"start": v(-105.78, -48.09) * mm, "end": v(-105.44, -48.07) * mm});
            skLineSegment(sketch, "E2306", {"start": v(-105.44, -48.07) * mm, "end": v(-105.1, -48.06) * mm});
            skLineSegment(sketch, "E2307", {"start": v(-105.1, -48.06) * mm, "end": v(-104.78, -48.04) * mm});
            skLineSegment(sketch, "E2308", {"start": v(-104.78, -48.04) * mm, "end": v(-104.46, -48.02) * mm});
            skLineSegment(sketch, "E2309", {"start": v(-104.46, -48.02) * mm, "end": v(-104.14, -48) * mm});
            skLineSegment(sketch, "E2310", {"start": v(-104.14, -48) * mm, "end": v(-103.84, -47.97) * mm});
            skLineSegment(sketch, "E2311", {"start": v(-103.84, -47.97) * mm, "end": v(-103.54, -47.95) * mm});
            skLineSegment(sketch, "E2312", {"start": v(-103.54, -47.95) * mm, "end": v(-103.24, -47.92) * mm});
            skLineSegment(sketch, "E2313", {"start": v(-103.24, -47.92) * mm, "end": v(-102.95, -47.9) * mm});
            skLineSegment(sketch, "E2314", {"start": v(-102.95, -47.9) * mm, "end": v(-102.67, -47.86) * mm});
            skLineSegment(sketch, "E2315", {"start": v(-102.67, -47.86) * mm, "end": v(-102.4, -47.83) * mm});
            skLineSegment(sketch, "E2316", {"start": v(-102.4, -47.83) * mm, "end": v(-102.13, -47.8) * mm});
            skLineSegment(sketch, "E2317", {"start": v(-102.13, -47.8) * mm, "end": v(-101.87, -47.76) * mm});
            skLineSegment(sketch, "E2318", {"start": v(-101.87, -47.76) * mm, "end": v(-101.61, -47.73) * mm});
            skLineSegment(sketch, "E2319", {"start": v(-101.61, -47.73) * mm, "end": v(-101.37, -47.7) * mm});
            skLineSegment(sketch, "E2320", {"start": v(-101.37, -47.7) * mm, "end": v(-101.13, -47.65) * mm});
            skLineSegment(sketch, "E2321", {"start": v(-101.13, -47.65) * mm, "end": v(-100.9, -47.61) * mm});
            skLineSegment(sketch, "E2322", {"start": v(-100.9, -47.61) * mm, "end": v(-100.66, -47.57) * mm});
            skLineSegment(sketch, "E2323", {"start": v(-100.66, -47.57) * mm, "end": v(-100.44, -47.53) * mm});
            skLineSegment(sketch, "E2324", {"start": v(-100.44, -47.53) * mm, "end": v(-100.23, -47.5) * mm});
            skLineSegment(sketch, "E2325", {"start": v(-100.23, -47.5) * mm, "end": v(-100.02, -47.45) * mm});
            skLineSegment(sketch, "E2326", {"start": v(-100.02, -47.45) * mm, "end": v(-99.82, -47.41) * mm});
            skLineSegment(sketch, "E2327", {"start": v(-99.82, -47.41) * mm, "end": v(-99.62, -47.37) * mm});
            skLineSegment(sketch, "E2328", {"start": v(-99.62, -47.37) * mm, "end": v(-99.44, -47.33) * mm});
            skLineSegment(sketch, "E2329", {"start": v(-99.44, -47.33) * mm, "end": v(-99.26, -47.29) * mm});
            skLineSegment(sketch, "E2330", {"start": v(-99.26, -47.29) * mm, "end": v(-99.08, -47.25) * mm});
            skLineSegment(sketch, "E2331", {"start": v(-99.08, -47.25) * mm, "end": v(-98.91, -47.2) * mm});
            skLineSegment(sketch, "E2332", {"start": v(-98.91, -47.2) * mm, "end": v(-98.75, -47.17) * mm});
            skLineSegment(sketch, "E2333", {"start": v(-98.75, -47.17) * mm, "end": v(-98.6, -47.12) * mm});
            skLineSegment(sketch, "E2334", {"start": v(-98.6, -47.12) * mm, "end": v(-98.45, -47.09) * mm});
            skLineSegment(sketch, "E2335", {"start": v(-98.45, -47.09) * mm, "end": v(-98.3, -47.05) * mm});
            skLineSegment(sketch, "E2336", {"start": v(-98.3, -47.05) * mm, "end": v(-98.17, -47) * mm});
            skLineSegment(sketch, "E2337", {"start": v(-98.17, -47) * mm, "end": v(-98.04, -46.97) * mm});
            skLineSegment(sketch, "E2338", {"start": v(-98.04, -46.97) * mm, "end": v(-97.74, -46.98) * mm});
            skLineSegment(sketch, "E2339", {"start": v(-97.74, -46.98) * mm, "end": v(-95.73, -50.97) * mm});
            skLineSegment(sketch, "E2340", {"start": v(-95.73, -50.97) * mm, "end": v(-95.9, -51.21) * mm});
            skLineSegment(sketch, "E2341", {"start": v(-95.9, -51.21) * mm, "end": v(-96, -51.3) * mm});
            skLineSegment(sketch, "E2342", {"start": v(-96, -51.3) * mm, "end": v(-96.12, -51.38) * mm});
            skLineSegment(sketch, "E2343", {"start": v(-96.12, -51.38) * mm, "end": v(-96.23, -51.47) * mm});
            skLineSegment(sketch, "E2344", {"start": v(-96.23, -51.47) * mm, "end": v(-96.35, -51.57) * mm});
            skLineSegment(sketch, "E2345", {"start": v(-96.35, -51.57) * mm, "end": v(-96.48, -51.67) * mm});
            skLineSegment(sketch, "E2346", {"start": v(-96.48, -51.67) * mm, "end": v(-96.6, -51.77) * mm});
            skLineSegment(sketch, "E2347", {"start": v(-96.6, -51.77) * mm, "end": v(-96.74, -51.89) * mm});
            skLineSegment(sketch, "E2348", {"start": v(-96.74, -51.89) * mm, "end": v(-96.87, -52) * mm});
            skLineSegment(sketch, "E2349", {"start": v(-96.87, -52) * mm, "end": v(-97.01, -52.12) * mm});
            skLineSegment(sketch, "E2350", {"start": v(-97.01, -52.12) * mm, "end": v(-97.16, -52.25) * mm});
            skLineSegment(sketch, "E2351", {"start": v(-97.16, -52.25) * mm, "end": v(-97.3, -52.38) * mm});
            skLineSegment(sketch, "E2352", {"start": v(-97.3, -52.38) * mm, "end": v(-97.46, -52.52) * mm});
            skLineSegment(sketch, "E2353", {"start": v(-97.46, -52.52) * mm, "end": v(-97.62, -52.66) * mm});
            skLineSegment(sketch, "E2354", {"start": v(-97.62, -52.66) * mm, "end": v(-97.77, -52.81) * mm});
            skLineSegment(sketch, "E2355", {"start": v(-97.77, -52.81) * mm, "end": v(-97.94, -52.96) * mm});
            skLineSegment(sketch, "E2356", {"start": v(-97.94, -52.96) * mm, "end": v(-98.1, -53.13) * mm});
            skLineSegment(sketch, "E2357", {"start": v(-98.1, -53.13) * mm, "end": v(-98.27, -53.3) * mm});
            skLineSegment(sketch, "E2358", {"start": v(-98.27, -53.3) * mm, "end": v(-98.45, -53.46) * mm});
            skLineSegment(sketch, "E2359", {"start": v(-98.45, -53.46) * mm, "end": v(-98.62, -53.64) * mm});
            skLineSegment(sketch, "E2360", {"start": v(-98.62, -53.64) * mm, "end": v(-98.8, -53.82) * mm});
            skLineSegment(sketch, "E2361", {"start": v(-98.8, -53.82) * mm, "end": v(-98.99, -54.01) * mm});
            skLineSegment(sketch, "E2362", {"start": v(-98.99, -54.01) * mm, "end": v(-99.17, -54.2) * mm});
            skLineSegment(sketch, "E2363", {"start": v(-99.17, -54.2) * mm, "end": v(-99.36, -54.41) * mm});
            skLineSegment(sketch, "E2364", {"start": v(-99.36, -54.41) * mm, "end": v(-99.55, -54.62) * mm});
            skLineSegment(sketch, "E2365", {"start": v(-99.55, -54.62) * mm, "end": v(-99.75, -54.84) * mm});
            skLineSegment(sketch, "E2366", {"start": v(-99.75, -54.84) * mm, "end": v(-99.94, -55.06) * mm});
            skLineSegment(sketch, "E2367", {"start": v(-99.94, -55.06) * mm, "end": v(-100.14, -55.28) * mm});
            skLineSegment(sketch, "E2368", {"start": v(-100.14, -55.28) * mm, "end": v(-100.34, -55.52) * mm});
            skLineSegment(sketch, "E2369", {"start": v(-100.34, -55.52) * mm, "end": v(-100.55, -55.76) * mm});
            skLineSegment(sketch, "E2370", {"start": v(-100.55, -55.76) * mm, "end": v(-100.75, -56) * mm});
            skLineSegment(sketch, "E2371", {"start": v(-100.75, -56) * mm, "end": v(-100.96, -56.26) * mm});
            skLineSegment(sketch, "E2372", {"start": v(-100.96, -56.26) * mm, "end": v(-101.17, -56.52) * mm});
            skLineSegment(sketch, "E2373", {"start": v(-101.17, -56.52) * mm, "end": v(-101.38, -56.78) * mm});
            skLineSegment(sketch, "E2374", {"start": v(-101.38, -56.78) * mm, "end": v(-101.6, -57.06) * mm});
            skLineSegment(sketch, "E2375", {"start": v(-101.6, -57.06) * mm, "end": v(-101.81, -57.34) * mm});
            skLineSegment(sketch, "E2376", {"start": v(-101.81, -57.34) * mm, "end": v(-102.03, -57.62) * mm});
            skLineSegment(sketch, "E2377", {"start": v(-102.03, -57.62) * mm, "end": v(-102.25, -57.92) * mm});
            skLineSegment(sketch, "E2378", {"start": v(-102.25, -57.92) * mm, "end": v(-102.47, -58.22) * mm});
            skLineSegment(sketch, "E2379", {"start": v(-102.47, -58.22) * mm, "end": v(-102.7, -58.53) * mm});
            skLineSegment(sketch, "E2380", {"start": v(-102.7, -58.53) * mm, "end": v(-102.92, -58.84) * mm});
            skLineSegment(sketch, "E2381", {"start": v(-102.92, -58.84) * mm, "end": v(-103.14, -59.16) * mm});
            skLineSegment(sketch, "E2382", {"start": v(-103.14, -59.16) * mm, "end": v(-103.37, -59.5) * mm});
            skLineSegment(sketch, "E2383", {"start": v(-103.37, -59.5) * mm, "end": v(-103.38, -59.7) * mm});
            skLineSegment(sketch, "E2384", {"start": v(-103.38, -59.7) * mm, "end": v(-101.58, -62.71) * mm});
            skLineSegment(sketch, "E2385", {"start": v(-101.58, -62.71) * mm, "end": v(-101.4, -62.8) * mm});
            skLineSegment(sketch, "E2386", {"start": v(-101.4, -62.8) * mm, "end": v(-101, -62.76) * mm});
            skLineSegment(sketch, "E2387", {"start": v(-101, -62.76) * mm, "end": v(-100.6, -62.72) * mm});
            skLineSegment(sketch, "E2388", {"start": v(-100.6, -62.72) * mm, "end": v(-100.22, -62.67) * mm});
            skLineSegment(sketch, "E2389", {"start": v(-100.22, -62.67) * mm, "end": v(-99.85, -62.62) * mm});
            skLineSegment(sketch, "E2390", {"start": v(-99.85, -62.62) * mm, "end": v(-99.48, -62.57) * mm});
            skLineSegment(sketch, "E2391", {"start": v(-99.48, -62.57) * mm, "end": v(-99.11, -62.52) * mm});
            skLineSegment(sketch, "E2392", {"start": v(-99.11, -62.52) * mm, "end": v(-98.76, -62.46) * mm});
            skLineSegment(sketch, "E2393", {"start": v(-98.76, -62.46) * mm, "end": v(-98.4, -62.4) * mm});
            skLineSegment(sketch, "E2394", {"start": v(-98.4, -62.4) * mm, "end": v(-98.07, -62.35) * mm});
            skLineSegment(sketch, "E2395", {"start": v(-98.07, -62.35) * mm, "end": v(-97.73, -62.28) * mm});
            skLineSegment(sketch, "E2396", {"start": v(-97.73, -62.28) * mm, "end": v(-97.4, -62.22) * mm});
            skLineSegment(sketch, "E2397", {"start": v(-97.4, -62.22) * mm, "end": v(-97.08, -62.16) * mm});
            skLineSegment(sketch, "E2398", {"start": v(-97.08, -62.16) * mm, "end": v(-96.77, -62.1) * mm});
            skLineSegment(sketch, "E2399", {"start": v(-96.77, -62.1) * mm, "end": v(-96.46, -62.03) * mm});
            skLineSegment(sketch, "E2400", {"start": v(-96.46, -62.03) * mm, "end": v(-96.16, -61.96) * mm});
            skLineSegment(sketch, "E2401", {"start": v(-96.16, -61.96) * mm, "end": v(-95.86, -61.9) * mm});
            skLineSegment(sketch, "E2402", {"start": v(-95.86, -61.9) * mm, "end": v(-95.57, -61.83) * mm});
            skLineSegment(sketch, "E2403", {"start": v(-95.57, -61.83) * mm, "end": v(-95.3, -61.76) * mm});
            skLineSegment(sketch, "E2404", {"start": v(-95.3, -61.76) * mm, "end": v(-95.02, -61.7) * mm});
            skLineSegment(sketch, "E2405", {"start": v(-95.02, -61.7) * mm, "end": v(-94.75, -61.62) * mm});
            skLineSegment(sketch, "E2406", {"start": v(-94.75, -61.62) * mm, "end": v(-94.5, -61.55) * mm});
            skLineSegment(sketch, "E2407", {"start": v(-94.5, -61.55) * mm, "end": v(-94.24, -61.48) * mm});
            skLineSegment(sketch, "E2408", {"start": v(-94.24, -61.48) * mm, "end": v(-93.99, -61.4) * mm});
            skLineSegment(sketch, "E2409", {"start": v(-93.99, -61.4) * mm, "end": v(-93.75, -61.34) * mm});
            skLineSegment(sketch, "E2410", {"start": v(-93.75, -61.34) * mm, "end": v(-93.52, -61.27) * mm});
            skLineSegment(sketch, "E2411", {"start": v(-93.52, -61.27) * mm, "end": v(-93.29, -61.2) * mm});
            skLineSegment(sketch, "E2412", {"start": v(-93.29, -61.2) * mm, "end": v(-93.07, -61.13) * mm});
            skLineSegment(sketch, "E2413", {"start": v(-93.07, -61.13) * mm, "end": v(-92.86, -61.06) * mm});
            skLineSegment(sketch, "E2414", {"start": v(-92.86, -61.06) * mm, "end": v(-92.65, -60.99) * mm});
            skLineSegment(sketch, "E2415", {"start": v(-92.65, -60.99) * mm, "end": v(-92.45, -60.92) * mm});
            skLineSegment(sketch, "E2416", {"start": v(-92.45, -60.92) * mm, "end": v(-92.26, -60.85) * mm});
            skLineSegment(sketch, "E2417", {"start": v(-92.26, -60.85) * mm, "end": v(-92.07, -60.78) * mm});
            skLineSegment(sketch, "E2418", {"start": v(-92.07, -60.78) * mm, "end": v(-91.89, -60.71) * mm});
            skLineSegment(sketch, "E2419", {"start": v(-91.89, -60.71) * mm, "end": v(-91.71, -60.65) * mm});
            skLineSegment(sketch, "E2420", {"start": v(-91.71, -60.65) * mm, "end": v(-91.55, -60.58) * mm});
            skLineSegment(sketch, "E2421", {"start": v(-91.55, -60.58) * mm, "end": v(-91.39, -60.52) * mm});
            skLineSegment(sketch, "E2422", {"start": v(-91.39, -60.52) * mm, "end": v(-91.23, -60.46) * mm});
            skLineSegment(sketch, "E2423", {"start": v(-91.23, -60.46) * mm, "end": v(-91.09, -60.4) * mm});
            skLineSegment(sketch, "E2424", {"start": v(-91.09, -60.4) * mm, "end": v(-90.94, -60.33) * mm});
            skLineSegment(sketch, "E2425", {"start": v(-90.94, -60.33) * mm, "end": v(-90.8, -60.28) * mm});
            skLineSegment(sketch, "E2426", {"start": v(-90.8, -60.28) * mm, "end": v(-90.68, -60.22) * mm});
            skLineSegment(sketch, "E2427", {"start": v(-90.68, -60.22) * mm, "end": v(-90.56, -60.16) * mm});
            skLineSegment(sketch, "E2428", {"start": v(-90.56, -60.16) * mm, "end": v(-90.26, -60.13) * mm});
            skLineSegment(sketch, "E2429", {"start": v(-90.26, -60.13) * mm, "end": v(-87.7, -63.8) * mm});
            skLineSegment(sketch, "E2430", {"start": v(-87.7, -63.8) * mm, "end": v(-87.84, -64.07) * mm});
            skLineSegment(sketch, "E2431", {"start": v(-87.84, -64.07) * mm, "end": v(-87.94, -64.16) * mm});
            skLineSegment(sketch, "E2432", {"start": v(-87.94, -64.16) * mm, "end": v(-88.04, -64.26) * mm});
            skLineSegment(sketch, "E2433", {"start": v(-88.04, -64.26) * mm, "end": v(-88.14, -64.37) * mm});
            skLineSegment(sketch, "E2434", {"start": v(-88.14, -64.37) * mm, "end": v(-88.24, -64.48) * mm});
            skLineSegment(sketch, "E2435", {"start": v(-88.24, -64.48) * mm, "end": v(-88.35, -64.6) * mm});
            skLineSegment(sketch, "E2436", {"start": v(-88.35, -64.6) * mm, "end": v(-88.47, -64.72) * mm});
            skLineSegment(sketch, "E2437", {"start": v(-88.47, -64.72) * mm, "end": v(-88.58, -64.85) * mm});
            skLineSegment(sketch, "E2438", {"start": v(-88.58, -64.85) * mm, "end": v(-88.7, -64.98) * mm});
            skLineSegment(sketch, "E2439", {"start": v(-88.7, -64.98) * mm, "end": v(-88.82, -65.12) * mm});
            skLineSegment(sketch, "E2440", {"start": v(-88.82, -65.12) * mm, "end": v(-88.95, -65.27) * mm});
            skLineSegment(sketch, "E2441", {"start": v(-88.95, -65.27) * mm, "end": v(-89.08, -65.42) * mm});
            skLineSegment(sketch, "E2442", {"start": v(-89.08, -65.42) * mm, "end": v(-89.2, -65.58) * mm});
            skLineSegment(sketch, "E2443", {"start": v(-89.2, -65.58) * mm, "end": v(-89.34, -65.74) * mm});
            skLineSegment(sketch, "E2444", {"start": v(-89.34, -65.74) * mm, "end": v(-89.48, -65.9) * mm});
            skLineSegment(sketch, "E2445", {"start": v(-89.48, -65.9) * mm, "end": v(-89.62, -66.09) * mm});
            skLineSegment(sketch, "E2446", {"start": v(-89.62, -66.09) * mm, "end": v(-89.76, -66.27) * mm});
            skLineSegment(sketch, "E2447", {"start": v(-89.76, -66.27) * mm, "end": v(-89.9, -66.46) * mm});
            skLineSegment(sketch, "E2448", {"start": v(-89.9, -66.46) * mm, "end": v(-90.06, -66.65) * mm});
            skLineSegment(sketch, "E2449", {"start": v(-90.06, -66.65) * mm, "end": v(-90.2, -66.85) * mm});
            skLineSegment(sketch, "E2450", {"start": v(-90.2, -66.85) * mm, "end": v(-90.36, -67.06) * mm});
            skLineSegment(sketch, "E2451", {"start": v(-90.36, -67.06) * mm, "end": v(-90.51, -67.27) * mm});
            skLineSegment(sketch, "E2452", {"start": v(-90.51, -67.27) * mm, "end": v(-90.67, -67.5) * mm});
            skLineSegment(sketch, "E2453", {"start": v(-90.67, -67.5) * mm, "end": v(-90.83, -67.72) * mm});
            skLineSegment(sketch, "E2454", {"start": v(-90.83, -67.72) * mm, "end": v(-90.99, -67.95) * mm});
            skLineSegment(sketch, "E2455", {"start": v(-90.99, -67.95) * mm, "end": v(-91.15, -68.19) * mm});
            skLineSegment(sketch, "E2456", {"start": v(-91.15, -68.19) * mm, "end": v(-91.31, -68.43) * mm});
            skLineSegment(sketch, "E2457", {"start": v(-91.31, -68.43) * mm, "end": v(-91.48, -68.69) * mm});
            skLineSegment(sketch, "E2458", {"start": v(-91.48, -68.69) * mm, "end": v(-91.65, -68.95) * mm});
            skLineSegment(sketch, "E2459", {"start": v(-91.65, -68.95) * mm, "end": v(-91.81, -69.21) * mm});
            skLineSegment(sketch, "E2460", {"start": v(-91.81, -69.21) * mm, "end": v(-91.98, -69.49) * mm});
            skLineSegment(sketch, "E2461", {"start": v(-91.98, -69.49) * mm, "end": v(-92.15, -69.77) * mm});
            skLineSegment(sketch, "E2462", {"start": v(-92.15, -69.77) * mm, "end": v(-92.33, -70.05) * mm});
            skLineSegment(sketch, "E2463", {"start": v(-92.33, -70.05) * mm, "end": v(-92.5, -70.35) * mm});
            skLineSegment(sketch, "E2464", {"start": v(-92.5, -70.35) * mm, "end": v(-92.67, -70.65) * mm});
            skLineSegment(sketch, "E2465", {"start": v(-92.67, -70.65) * mm, "end": v(-92.85, -70.95) * mm});
            skLineSegment(sketch, "E2466", {"start": v(-92.85, -70.95) * mm, "end": v(-93.03, -71.27) * mm});
            skLineSegment(sketch, "E2467", {"start": v(-93.03, -71.27) * mm, "end": v(-93.2, -71.6) * mm});
            skLineSegment(sketch, "E2468", {"start": v(-93.2, -71.6) * mm, "end": v(-93.38, -71.92) * mm});
            skLineSegment(sketch, "E2469", {"start": v(-93.38, -71.92) * mm, "end": v(-93.56, -72.26) * mm});
            skLineSegment(sketch, "E2470", {"start": v(-93.56, -72.26) * mm, "end": v(-93.74, -72.6) * mm});
            skLineSegment(sketch, "E2471", {"start": v(-93.74, -72.6) * mm, "end": v(-93.91, -72.95) * mm});
            skLineSegment(sketch, "E2472", {"start": v(-93.91, -72.95) * mm, "end": v(-94.1, -73.3) * mm});
            skLineSegment(sketch, "E2473", {"start": v(-94.1, -73.3) * mm, "end": v(-94.07, -73.5) * mm});
            skLineSegment(sketch, "E2474", {"start": v(-94.07, -73.5) * mm, "end": v(-91.87, -76.24) * mm});
            skLineSegment(sketch, "E2475", {"start": v(-91.87, -76.24) * mm, "end": v(-91.67, -76.31) * mm});
            skLineSegment(sketch, "E2476", {"start": v(-91.67, -76.31) * mm, "end": v(-91.28, -76.21) * mm});
            skLineSegment(sketch, "E2477", {"start": v(-91.28, -76.21) * mm, "end": v(-90.9, -76.12) * mm});
            skLineSegment(sketch, "E2478", {"start": v(-90.9, -76.12) * mm, "end": v(-90.53, -76.02) * mm});
            skLineSegment(sketch, "E2479", {"start": v(-90.53, -76.02) * mm, "end": v(-90.17, -75.91) * mm});
            skLineSegment(sketch, "E2480", {"start": v(-90.17, -75.91) * mm, "end": v(-89.8, -75.81) * mm});
            skLineSegment(sketch, "E2481", {"start": v(-89.8, -75.81) * mm, "end": v(-89.46, -75.7) * mm});
            skLineSegment(sketch, "E2482", {"start": v(-89.46, -75.7) * mm, "end": v(-89.11, -75.6) * mm});
            skLineSegment(sketch, "E2483", {"start": v(-89.11, -75.6) * mm, "end": v(-88.77, -75.5) * mm});
            skLineSegment(sketch, "E2484", {"start": v(-88.77, -75.5) * mm, "end": v(-88.44, -75.4) * mm});
            skLineSegment(sketch, "E2485", {"start": v(-88.44, -75.4) * mm, "end": v(-88.12, -75.28) * mm});
            skLineSegment(sketch, "E2486", {"start": v(-88.12, -75.28) * mm, "end": v(-87.8, -75.18) * mm});
            skLineSegment(sketch, "E2487", {"start": v(-87.8, -75.18) * mm, "end": v(-87.5, -75.07) * mm});
            skLineSegment(sketch, "E2488", {"start": v(-87.5, -75.07) * mm, "end": v(-87.19, -74.96) * mm});
            skLineSegment(sketch, "E2489", {"start": v(-87.19, -74.96) * mm, "end": v(-86.9, -74.86) * mm});
            skLineSegment(sketch, "E2490", {"start": v(-86.9, -74.86) * mm, "end": v(-86.6, -74.75) * mm});
            skLineSegment(sketch, "E2491", {"start": v(-86.6, -74.75) * mm, "end": v(-86.32, -74.64) * mm});
            skLineSegment(sketch, "E2492", {"start": v(-86.32, -74.64) * mm, "end": v(-86.04, -74.53) * mm});
            skLineSegment(sketch, "E2493", {"start": v(-86.04, -74.53) * mm, "end": v(-85.78, -74.43) * mm});
            skLineSegment(sketch, "E2494", {"start": v(-85.78, -74.43) * mm, "end": v(-85.51, -74.32) * mm});
            skLineSegment(sketch, "E2495", {"start": v(-85.51, -74.32) * mm, "end": v(-85.26, -74.21) * mm});
            skLineSegment(sketch, "E2496", {"start": v(-85.26, -74.21) * mm, "end": v(-85.01, -74.1) * mm});
            skLineSegment(sketch, "E2497", {"start": v(-85.01, -74.1) * mm, "end": v(-84.77, -74) * mm});
            skLineSegment(sketch, "E2498", {"start": v(-84.77, -74) * mm, "end": v(-84.54, -73.9) * mm});
            skLineSegment(sketch, "E2499", {"start": v(-84.54, -73.9) * mm, "end": v(-84.3, -73.8) * mm});
            skLineSegment(sketch, "E2500", {"start": v(-84.3, -73.8) * mm, "end": v(-84.09, -73.7) * mm});
            skLineSegment(sketch, "E2501", {"start": v(-84.09, -73.7) * mm, "end": v(-83.87, -73.59) * mm});
            skLineSegment(sketch, "E2502", {"start": v(-83.87, -73.59) * mm, "end": v(-83.66, -73.5) * mm});
            skLineSegment(sketch, "E2503", {"start": v(-83.66, -73.5) * mm, "end": v(-83.46, -73.4) * mm});
            skLineSegment(sketch, "E2504", {"start": v(-83.46, -73.4) * mm, "end": v(-83.27, -73.3) * mm});
            skLineSegment(sketch, "E2505", {"start": v(-83.27, -73.3) * mm, "end": v(-83.08, -73.2) * mm});
            skLineSegment(sketch, "E2506", {"start": v(-83.08, -73.2) * mm, "end": v(-82.9, -73.1) * mm});
            skLineSegment(sketch, "E2507", {"start": v(-82.9, -73.1) * mm, "end": v(-82.72, -73) * mm});
            skLineSegment(sketch, "E2508", {"start": v(-82.72, -73) * mm, "end": v(-82.55, -72.92) * mm});
            skLineSegment(sketch, "E2509", {"start": v(-82.55, -72.92) * mm, "end": v(-82.39, -72.83) * mm});
            skLineSegment(sketch, "E2510", {"start": v(-82.39, -72.83) * mm, "end": v(-82.23, -72.74) * mm});
            skLineSegment(sketch, "E2511", {"start": v(-82.23, -72.74) * mm, "end": v(-82.08, -72.65) * mm});
            skLineSegment(sketch, "E2512", {"start": v(-82.08, -72.65) * mm, "end": v(-81.94, -72.57) * mm});
            skLineSegment(sketch, "E2513", {"start": v(-81.94, -72.57) * mm, "end": v(-81.8, -72.49) * mm});
            skLineSegment(sketch, "E2514", {"start": v(-81.8, -72.49) * mm, "end": v(-81.67, -72.4) * mm});
            skLineSegment(sketch, "E2515", {"start": v(-81.67, -72.4) * mm, "end": v(-81.54, -72.33) * mm});
            skLineSegment(sketch, "E2516", {"start": v(-81.54, -72.33) * mm, "end": v(-81.42, -72.26) * mm});
            skLineSegment(sketch, "E2517", {"start": v(-81.42, -72.26) * mm, "end": v(-81.31, -72.19) * mm});
            skLineSegment(sketch, "E2518", {"start": v(-81.31, -72.19) * mm, "end": v(-81.02, -72.11) * mm});
            skLineSegment(sketch, "E2519", {"start": v(-81.02, -72.11) * mm, "end": v(-77.98, -75.4) * mm});
            skLineSegment(sketch, "E2520", {"start": v(-77.98, -75.4) * mm, "end": v(-78.08, -75.67) * mm});
            skLineSegment(sketch, "E2521", {"start": v(-78.08, -75.67) * mm, "end": v(-78.16, -75.78) * mm});
            skLineSegment(sketch, "E2522", {"start": v(-78.16, -75.78) * mm, "end": v(-78.24, -75.9) * mm});
            skLineSegment(sketch, "E2523", {"start": v(-78.24, -75.9) * mm, "end": v(-78.33, -76.02) * mm});
            skLineSegment(sketch, "E2524", {"start": v(-78.33, -76.02) * mm, "end": v(-78.42, -76.14) * mm});
            skLineSegment(sketch, "E2525", {"start": v(-78.42, -76.14) * mm, "end": v(-78.5, -76.27) * mm});
            skLineSegment(sketch, "E2526", {"start": v(-78.5, -76.27) * mm, "end": v(-78.6, -76.4) * mm});
            skLineSegment(sketch, "E2527", {"start": v(-78.6, -76.4) * mm, "end": v(-78.7, -76.55) * mm});
            skLineSegment(sketch, "E2528", {"start": v(-78.7, -76.55) * mm, "end": v(-78.8, -76.7) * mm});
            skLineSegment(sketch, "E2529", {"start": v(-78.8, -76.7) * mm, "end": v(-78.9, -76.86) * mm});
            skLineSegment(sketch, "E2530", {"start": v(-78.9, -76.86) * mm, "end": v(-79, -77.02) * mm});
            skLineSegment(sketch, "E2531", {"start": v(-79, -77.02) * mm, "end": v(-79.11, -77.19) * mm});
            skLineSegment(sketch, "E2532", {"start": v(-79.11, -77.19) * mm, "end": v(-79.22, -77.36) * mm});
            skLineSegment(sketch, "E2533", {"start": v(-79.22, -77.36) * mm, "end": v(-79.33, -77.54) * mm});
            skLineSegment(sketch, "E2534", {"start": v(-79.33, -77.54) * mm, "end": v(-79.44, -77.73) * mm});
            skLineSegment(sketch, "E2535", {"start": v(-79.44, -77.73) * mm, "end": v(-79.56, -77.92) * mm});
            skLineSegment(sketch, "E2536", {"start": v(-79.56, -77.92) * mm, "end": v(-79.67, -78.12) * mm});
            skLineSegment(sketch, "E2537", {"start": v(-79.67, -78.12) * mm, "end": v(-79.8, -78.33) * mm});
            skLineSegment(sketch, "E2538", {"start": v(-79.8, -78.33) * mm, "end": v(-79.9, -78.54) * mm});
            skLineSegment(sketch, "E2539", {"start": v(-79.9, -78.54) * mm, "end": v(-80.03, -78.76) * mm});
            skLineSegment(sketch, "E2540", {"start": v(-80.03, -78.76) * mm, "end": v(-80.15, -78.99) * mm});
            skLineSegment(sketch, "E2541", {"start": v(-80.15, -78.99) * mm, "end": v(-80.28, -79.22) * mm});
            skLineSegment(sketch, "E2542", {"start": v(-80.28, -79.22) * mm, "end": v(-80.4, -79.46) * mm});
            skLineSegment(sketch, "E2543", {"start": v(-80.4, -79.46) * mm, "end": v(-80.53, -79.7) * mm});
            skLineSegment(sketch, "E2544", {"start": v(-80.53, -79.7) * mm, "end": v(-80.65, -79.96) * mm});
            skLineSegment(sketch, "E2545", {"start": v(-80.65, -79.96) * mm, "end": v(-80.78, -80.22) * mm});
            skLineSegment(sketch, "E2546", {"start": v(-80.78, -80.22) * mm, "end": v(-80.9, -80.48) * mm});
            skLineSegment(sketch, "E2547", {"start": v(-80.9, -80.48) * mm, "end": v(-81.04, -80.76) * mm});
            skLineSegment(sketch, "E2548", {"start": v(-81.04, -80.76) * mm, "end": v(-81.16, -81.04) * mm});
            skLineSegment(sketch, "E2549", {"start": v(-81.16, -81.04) * mm, "end": v(-81.3, -81.32) * mm});
            skLineSegment(sketch, "E2550", {"start": v(-81.3, -81.32) * mm, "end": v(-81.43, -81.62) * mm});
            skLineSegment(sketch, "E2551", {"start": v(-81.43, -81.62) * mm, "end": v(-81.56, -81.92) * mm});
            skLineSegment(sketch, "E2552", {"start": v(-81.56, -81.92) * mm, "end": v(-81.69, -82.23) * mm});
            skLineSegment(sketch, "E2553", {"start": v(-81.69, -82.23) * mm, "end": v(-81.82, -82.54) * mm});
            skLineSegment(sketch, "E2554", {"start": v(-81.82, -82.54) * mm, "end": v(-81.95, -82.86) * mm});
            skLineSegment(sketch, "E2555", {"start": v(-81.95, -82.86) * mm, "end": v(-82.08, -83.2) * mm});
            skLineSegment(sketch, "E2556", {"start": v(-82.08, -83.2) * mm, "end": v(-82.2, -83.53) * mm});
            skLineSegment(sketch, "E2557", {"start": v(-82.2, -83.53) * mm, "end": v(-82.34, -83.87) * mm});
            skLineSegment(sketch, "E2558", {"start": v(-82.34, -83.87) * mm, "end": v(-82.47, -84.22) * mm});
            skLineSegment(sketch, "E2559", {"start": v(-82.47, -84.22) * mm, "end": v(-82.6, -84.58) * mm});
            skLineSegment(sketch, "E2560", {"start": v(-82.6, -84.58) * mm, "end": v(-82.73, -84.94) * mm});
            skLineSegment(sketch, "E2561", {"start": v(-82.73, -84.94) * mm, "end": v(-82.85, -85.31) * mm});
            skLineSegment(sketch, "E2562", {"start": v(-82.85, -85.31) * mm, "end": v(-82.98, -85.7) * mm});
            skLineSegment(sketch, "E2563", {"start": v(-82.98, -85.7) * mm, "end": v(-82.93, -85.9) * mm});
            skLineSegment(sketch, "E2564", {"start": v(-82.93, -85.9) * mm, "end": v(-80.37, -88.3) * mm});
            skLineSegment(sketch, "E2565", {"start": v(-80.37, -88.3) * mm, "end": v(-80.16, -88.33) * mm});
            skLineSegment(sketch, "E2566", {"start": v(-80.16, -88.33) * mm, "end": v(-79.8, -88.18) * mm});
            skLineSegment(sketch, "E2567", {"start": v(-79.8, -88.18) * mm, "end": v(-79.43, -88.03) * mm});
            skLineSegment(sketch, "E2568", {"start": v(-79.43, -88.03) * mm, "end": v(-79.08, -87.88) * mm});
            skLineSegment(sketch, "E2569", {"start": v(-79.08, -87.88) * mm, "end": v(-78.73, -87.73) * mm});
            skLineSegment(sketch, "E2570", {"start": v(-78.73, -87.73) * mm, "end": v(-78.39, -87.58) * mm});
            skLineSegment(sketch, "E2571", {"start": v(-78.39, -87.58) * mm, "end": v(-78.05, -87.43) * mm});
            skLineSegment(sketch, "E2572", {"start": v(-78.05, -87.43) * mm, "end": v(-77.73, -87.27) * mm});
            skLineSegment(sketch, "E2573", {"start": v(-77.73, -87.27) * mm, "end": v(-77.4, -87.12) * mm});
            skLineSegment(sketch, "E2574", {"start": v(-77.4, -87.12) * mm, "end": v(-77.1, -86.97) * mm});
            skLineSegment(sketch, "E2575", {"start": v(-77.1, -86.97) * mm, "end": v(-76.79, -86.82) * mm});
            skLineSegment(sketch, "E2576", {"start": v(-76.79, -86.82) * mm, "end": v(-76.5, -86.67) * mm});
            skLineSegment(sketch, "E2577", {"start": v(-76.5, -86.67) * mm, "end": v(-76.2, -86.52) * mm});
            skLineSegment(sketch, "E2578", {"start": v(-76.2, -86.52) * mm, "end": v(-75.91, -86.37) * mm});
            skLineSegment(sketch, "E2579", {"start": v(-75.91, -86.37) * mm, "end": v(-75.64, -86.23) * mm});
            skLineSegment(sketch, "E2580", {"start": v(-75.64, -86.23) * mm, "end": v(-75.36, -86.08) * mm});
            skLineSegment(sketch, "E2581", {"start": v(-75.36, -86.08) * mm, "end": v(-75.1, -85.93) * mm});
            skLineSegment(sketch, "E2582", {"start": v(-75.1, -85.93) * mm, "end": v(-74.84, -85.79) * mm});
            skLineSegment(sketch, "E2583", {"start": v(-74.84, -85.79) * mm, "end": v(-74.59, -85.65) * mm});
            skLineSegment(sketch, "E2584", {"start": v(-74.59, -85.65) * mm, "end": v(-74.35, -85.5) * mm});
            skLineSegment(sketch, "E2585", {"start": v(-74.35, -85.5) * mm, "end": v(-74.1, -85.36) * mm});
            skLineSegment(sketch, "E2586", {"start": v(-74.1, -85.36) * mm, "end": v(-73.88, -85.22) * mm});
            skLineSegment(sketch, "E2587", {"start": v(-73.88, -85.22) * mm, "end": v(-73.65, -85.08) * mm});
            skLineSegment(sketch, "E2588", {"start": v(-73.65, -85.08) * mm, "end": v(-73.43, -84.95) * mm});
            skLineSegment(sketch, "E2589", {"start": v(-73.43, -84.95) * mm, "end": v(-73.22, -84.81) * mm});
            skLineSegment(sketch, "E2590", {"start": v(-73.22, -84.81) * mm, "end": v(-73.02, -84.68) * mm});
            skLineSegment(sketch, "E2591", {"start": v(-73.02, -84.68) * mm, "end": v(-72.82, -84.55) * mm});
            skLineSegment(sketch, "E2592", {"start": v(-72.82, -84.55) * mm, "end": v(-72.63, -84.42) * mm});
            skLineSegment(sketch, "E2593", {"start": v(-72.63, -84.42) * mm, "end": v(-72.44, -84.3) * mm});
            skLineSegment(sketch, "E2594", {"start": v(-72.44, -84.3) * mm, "end": v(-72.26, -84.17) * mm});
            skLineSegment(sketch, "E2595", {"start": v(-72.26, -84.17) * mm, "end": v(-72.09, -84.05) * mm});
            skLineSegment(sketch, "E2596", {"start": v(-72.09, -84.05) * mm, "end": v(-71.92, -83.93) * mm});
            skLineSegment(sketch, "E2597", {"start": v(-71.92, -83.93) * mm, "end": v(-71.76, -83.82) * mm});
            skLineSegment(sketch, "E2598", {"start": v(-71.76, -83.82) * mm, "end": v(-71.6, -83.7) * mm});
            skLineSegment(sketch, "E2599", {"start": v(-71.6, -83.7) * mm, "end": v(-71.46, -83.59) * mm});
            skLineSegment(sketch, "E2600", {"start": v(-71.46, -83.59) * mm, "end": v(-71.32, -83.48) * mm});
            skLineSegment(sketch, "E2601", {"start": v(-71.32, -83.48) * mm, "end": v(-71.18, -83.38) * mm});
            skLineSegment(sketch, "E2602", {"start": v(-71.18, -83.38) * mm, "end": v(-71.05, -83.27) * mm});
            skLineSegment(sketch, "E2603", {"start": v(-71.05, -83.27) * mm, "end": v(-70.92, -83.17) * mm});
            skLineSegment(sketch, "E2604", {"start": v(-70.92, -83.17) * mm, "end": v(-70.8, -83.08) * mm});
            skLineSegment(sketch, "E2605", {"start": v(-70.8, -83.08) * mm, "end": v(-70.7, -82.98) * mm});
            skLineSegment(sketch, "E2606", {"start": v(-70.7, -82.98) * mm, "end": v(-70.58, -82.9) * mm});
            skLineSegment(sketch, "E2607", {"start": v(-70.58, -82.9) * mm, "end": v(-70.48, -82.8) * mm});
            skLineSegment(sketch, "E2608", {"start": v(-70.48, -82.8) * mm, "end": v(-70.2, -82.7) * mm});
            skLineSegment(sketch, "E2609", {"start": v(-70.2, -82.7) * mm, "end": v(-66.74, -85.52) * mm});
            skLineSegment(sketch, "E2610", {"start": v(-66.74, -85.52) * mm, "end": v(-66.8, -85.8) * mm});
            skLineSegment(sketch, "E2611", {"start": v(-66.8, -85.8) * mm, "end": v(-66.86, -85.93) * mm});
            skLineSegment(sketch, "E2612", {"start": v(-66.86, -85.93) * mm, "end": v(-66.92, -86.05) * mm});
            skLineSegment(sketch, "E2613", {"start": v(-66.92, -86.05) * mm, "end": v(-67, -86.18) * mm});
            skLineSegment(sketch, "E2614", {"start": v(-67, -86.18) * mm, "end": v(-67.06, -86.32) * mm});
            skLineSegment(sketch, "E2615", {"start": v(-67.06, -86.32) * mm, "end": v(-67.14, -86.46) * mm});
            skLineSegment(sketch, "E2616", {"start": v(-67.14, -86.46) * mm, "end": v(-67.21, -86.6) * mm});
            skLineSegment(sketch, "E2617", {"start": v(-67.21, -86.6) * mm, "end": v(-67.29, -86.76) * mm});
            skLineSegment(sketch, "E2618", {"start": v(-67.29, -86.76) * mm, "end": v(-67.37, -86.93) * mm});
            skLineSegment(sketch, "E2619", {"start": v(-67.37, -86.93) * mm, "end": v(-67.44, -87.1) * mm});
            skLineSegment(sketch, "E2620", {"start": v(-67.44, -87.1) * mm, "end": v(-67.52, -87.27) * mm});
            skLineSegment(sketch, "E2621", {"start": v(-67.52, -87.27) * mm, "end": v(-67.6, -87.45) * mm});
            skLineSegment(sketch, "E2622", {"start": v(-67.6, -87.45) * mm, "end": v(-67.69, -87.64) * mm});
            skLineSegment(sketch, "E2623", {"start": v(-67.69, -87.64) * mm, "end": v(-67.77, -87.83) * mm});
            skLineSegment(sketch, "E2624", {"start": v(-67.77, -87.83) * mm, "end": v(-67.86, -88.03) * mm});
            skLineSegment(sketch, "E2625", {"start": v(-67.86, -88.03) * mm, "end": v(-67.94, -88.24) * mm});
            skLineSegment(sketch, "E2626", {"start": v(-67.94, -88.24) * mm, "end": v(-68.03, -88.45) * mm});
            skLineSegment(sketch, "E2627", {"start": v(-68.03, -88.45) * mm, "end": v(-68.12, -88.67) * mm});
            skLineSegment(sketch, "E2628", {"start": v(-68.12, -88.67) * mm, "end": v(-68.2, -88.9) * mm});
            skLineSegment(sketch, "E2629", {"start": v(-68.2, -88.9) * mm, "end": v(-68.3, -89.14) * mm});
            skLineSegment(sketch, "E2630", {"start": v(-68.3, -89.14) * mm, "end": v(-68.39, -89.38) * mm});
            skLineSegment(sketch, "E2631", {"start": v(-68.39, -89.38) * mm, "end": v(-68.48, -89.62) * mm});
            skLineSegment(sketch, "E2632", {"start": v(-68.48, -89.62) * mm, "end": v(-68.57, -89.88) * mm});
            skLineSegment(sketch, "E2633", {"start": v(-68.57, -89.88) * mm, "end": v(-68.66, -90.14) * mm});
            skLineSegment(sketch, "E2634", {"start": v(-68.66, -90.14) * mm, "end": v(-68.75, -90.4) * mm});
            skLineSegment(sketch, "E2635", {"start": v(-68.75, -90.4) * mm, "end": v(-68.84, -90.68) * mm});
            skLineSegment(sketch, "E2636", {"start": v(-68.84, -90.68) * mm, "end": v(-68.92, -90.96) * mm});
            skLineSegment(sketch, "E2637", {"start": v(-68.92, -90.96) * mm, "end": v(-69.01, -91.25) * mm});
            skLineSegment(sketch, "E2638", {"start": v(-69.01, -91.25) * mm, "end": v(-69.1, -91.55) * mm});
            skLineSegment(sketch, "E2639", {"start": v(-69.1, -91.55) * mm, "end": v(-69.2, -91.85) * mm});
            skLineSegment(sketch, "E2640", {"start": v(-69.2, -91.85) * mm, "end": v(-69.28, -92.16) * mm});
            skLineSegment(sketch, "E2641", {"start": v(-69.28, -92.16) * mm, "end": v(-69.37, -92.48) * mm});
            skLineSegment(sketch, "E2642", {"start": v(-69.37, -92.48) * mm, "end": v(-69.45, -92.8) * mm});
            skLineSegment(sketch, "E2643", {"start": v(-69.45, -92.8) * mm, "end": v(-69.54, -93.13) * mm});
            skLineSegment(sketch, "E2644", {"start": v(-69.54, -93.13) * mm, "end": v(-69.62, -93.47) * mm});
            skLineSegment(sketch, "E2645", {"start": v(-69.62, -93.47) * mm, "end": v(-69.7, -93.81) * mm});
            skLineSegment(sketch, "E2646", {"start": v(-69.7, -93.81) * mm, "end": v(-69.8, -94.16) * mm});
            skLineSegment(sketch, "E2647", {"start": v(-69.8, -94.16) * mm, "end": v(-69.87, -94.52) * mm});
            skLineSegment(sketch, "E2648", {"start": v(-69.87, -94.52) * mm, "end": v(-69.95, -94.88) * mm});
            skLineSegment(sketch, "E2649", {"start": v(-69.95, -94.88) * mm, "end": v(-70.03, -95.26) * mm});
            skLineSegment(sketch, "E2650", {"start": v(-70.03, -95.26) * mm, "end": v(-70.1, -95.63) * mm});
            skLineSegment(sketch, "E2651", {"start": v(-70.1, -95.63) * mm, "end": v(-70.18, -96.02) * mm});
            skLineSegment(sketch, "E2652", {"start": v(-70.18, -96.02) * mm, "end": v(-70.25, -96.41) * mm});
            skLineSegment(sketch, "E2653", {"start": v(-70.25, -96.41) * mm, "end": v(-70.17, -96.6) * mm});
            skLineSegment(sketch, "E2654", {"start": v(-70.17, -96.6) * mm, "end": v(-67.3, -98.62) * mm});
            skLineSegment(sketch, "E2655", {"start": v(-67.3, -98.62) * mm, "end": v(-67.1, -98.64) * mm});
            skLineSegment(sketch, "E2656", {"start": v(-67.1, -98.64) * mm, "end": v(-66.75, -98.44) * mm});
            skLineSegment(sketch, "E2657", {"start": v(-66.75, -98.44) * mm, "end": v(-66.42, -98.23) * mm});
            skLineSegment(sketch, "E2658", {"start": v(-66.42, -98.23) * mm, "end": v(-66.08, -98.04) * mm});
            skLineSegment(sketch, "E2659", {"start": v(-66.08, -98.04) * mm, "end": v(-65.76, -97.84) * mm});
            skLineSegment(sketch, "E2660", {"start": v(-65.76, -97.84) * mm, "end": v(-65.44, -97.64) * mm});
            skLineSegment(sketch, "E2661", {"start": v(-65.44, -97.64) * mm, "end": v(-65.13, -97.44) * mm});
            skLineSegment(sketch, "E2662", {"start": v(-65.13, -97.44) * mm, "end": v(-64.83, -97.25) * mm});
            skLineSegment(sketch, "E2663", {"start": v(-64.83, -97.25) * mm, "end": v(-64.54, -97.05) * mm});
            skLineSegment(sketch, "E2664", {"start": v(-64.54, -97.05) * mm, "end": v(-64.25, -96.86) * mm});
            skLineSegment(sketch, "E2665", {"start": v(-64.25, -96.86) * mm, "end": v(-63.97, -96.67) * mm});
            skLineSegment(sketch, "E2666", {"start": v(-63.97, -96.67) * mm, "end": v(-63.7, -96.48) * mm});
            skLineSegment(sketch, "E2667", {"start": v(-63.7, -96.48) * mm, "end": v(-63.42, -96.29) * mm});
            skLineSegment(sketch, "E2668", {"start": v(-63.42, -96.29) * mm, "end": v(-63.16, -96.1) * mm});
            skLineSegment(sketch, "E2669", {"start": v(-63.16, -96.1) * mm, "end": v(-62.9, -95.92) * mm});
            skLineSegment(sketch, "E2670", {"start": v(-62.9, -95.92) * mm, "end": v(-62.66, -95.74) * mm});
            skLineSegment(sketch, "E2671", {"start": v(-62.66, -95.74) * mm, "end": v(-62.42, -95.55) * mm});
            skLineSegment(sketch, "E2672", {"start": v(-62.42, -95.55) * mm, "end": v(-62.18, -95.37) * mm});
            skLineSegment(sketch, "E2673", {"start": v(-62.18, -95.37) * mm, "end": v(-61.95, -95.2) * mm});
            skLineSegment(sketch, "E2674", {"start": v(-61.95, -95.2) * mm, "end": v(-61.73, -95.02) * mm});
            skLineSegment(sketch, "E2675", {"start": v(-61.73, -95.02) * mm, "end": v(-61.51, -94.85) * mm});
            skLineSegment(sketch, "E2676", {"start": v(-61.51, -94.85) * mm, "end": v(-61.3, -94.68) * mm});
            skLineSegment(sketch, "E2677", {"start": v(-61.3, -94.68) * mm, "end": v(-61.1, -94.51) * mm});
            skLineSegment(sketch, "E2678", {"start": v(-61.1, -94.51) * mm, "end": v(-60.9, -94.35) * mm});
            skLineSegment(sketch, "E2679", {"start": v(-60.9, -94.35) * mm, "end": v(-60.71, -94.19) * mm});
            skLineSegment(sketch, "E2680", {"start": v(-60.71, -94.19) * mm, "end": v(-60.53, -94.03) * mm});
            skLineSegment(sketch, "E2681", {"start": v(-60.53, -94.03) * mm, "end": v(-60.35, -93.87) * mm});
            skLineSegment(sketch, "E2682", {"start": v(-60.35, -93.87) * mm, "end": v(-60.18, -93.71) * mm});
            skLineSegment(sketch, "E2683", {"start": v(-60.18, -93.71) * mm, "end": v(-60.01, -93.56) * mm});
            skLineSegment(sketch, "E2684", {"start": v(-60.01, -93.56) * mm, "end": v(-59.85, -93.42) * mm});
            skLineSegment(sketch, "E2685", {"start": v(-59.85, -93.42) * mm, "end": v(-59.7, -93.27) * mm});
            skLineSegment(sketch, "E2686", {"start": v(-59.7, -93.27) * mm, "end": v(-59.55, -93.13) * mm});
            skLineSegment(sketch, "E2687", {"start": v(-59.55, -93.13) * mm, "end": v(-59.4, -93) * mm});
            skLineSegment(sketch, "E2688", {"start": v(-59.4, -93) * mm, "end": v(-59.27, -92.86) * mm});
            skLineSegment(sketch, "E2689", {"start": v(-59.27, -92.86) * mm, "end": v(-59.14, -92.73) * mm});
            skLineSegment(sketch, "E2690", {"start": v(-59.14, -92.73) * mm, "end": v(-59, -92.6) * mm});
            skLineSegment(sketch, "E2691", {"start": v(-59, -92.6) * mm, "end": v(-58.89, -92.48) * mm});
            skLineSegment(sketch, "E2692", {"start": v(-58.89, -92.48) * mm, "end": v(-58.77, -92.36) * mm});
            skLineSegment(sketch, "E2693", {"start": v(-58.77, -92.36) * mm, "end": v(-58.66, -92.24) * mm});
            skLineSegment(sketch, "E2694", {"start": v(-58.66, -92.24) * mm, "end": v(-58.56, -92.13) * mm});
            skLineSegment(sketch, "E2695", {"start": v(-58.56, -92.13) * mm, "end": v(-58.46, -92.02) * mm});
            skLineSegment(sketch, "E2696", {"start": v(-58.46, -92.02) * mm, "end": v(-58.37, -91.91) * mm});
            skLineSegment(sketch, "E2697", {"start": v(-58.37, -91.91) * mm, "end": v(-58.28, -91.81) * mm});
            skLineSegment(sketch, "E2698", {"start": v(-58.28, -91.81) * mm, "end": v(-58.02, -91.66) * mm});
            skLineSegment(sketch, "E2699", {"start": v(-58.02, -91.66) * mm, "end": v(-54.2, -93.98) * mm});
            skLineSegment(sketch, "E2700", {"start": v(-54.2, -93.98) * mm, "end": v(-54.2, -94.28) * mm});
            skLineSegment(sketch, "E2701", {"start": v(-54.2, -94.28) * mm, "end": v(-54.25, -94.4) * mm});
            skLineSegment(sketch, "E2702", {"start": v(-54.25, -94.4) * mm, "end": v(-54.3, -94.53) * mm});
            skLineSegment(sketch, "E2703", {"start": v(-54.3, -94.53) * mm, "end": v(-54.35, -94.67) * mm});
            skLineSegment(sketch, "E2704", {"start": v(-54.35, -94.67) * mm, "end": v(-54.4, -94.82) * mm});
            skLineSegment(sketch, "E2705", {"start": v(-54.4, -94.82) * mm, "end": v(-54.46, -94.97) * mm});
            skLineSegment(sketch, "E2706", {"start": v(-54.46, -94.97) * mm, "end": v(-54.5, -95.13) * mm});
            skLineSegment(sketch, "E2707", {"start": v(-54.5, -95.13) * mm, "end": v(-54.56, -95.29) * mm});
            skLineSegment(sketch, "E2708", {"start": v(-54.56, -95.29) * mm, "end": v(-54.62, -95.46) * mm});
            skLineSegment(sketch, "E2709", {"start": v(-54.62, -95.46) * mm, "end": v(-54.67, -95.64) * mm});
            skLineSegment(sketch, "E2710", {"start": v(-54.67, -95.64) * mm, "end": v(-54.73, -95.82) * mm});
            skLineSegment(sketch, "E2711", {"start": v(-54.73, -95.82) * mm, "end": v(-54.78, -96.01) * mm});
            skLineSegment(sketch, "E2712", {"start": v(-54.78, -96.01) * mm, "end": v(-54.84, -96.2) * mm});
            skLineSegment(sketch, "E2713", {"start": v(-54.84, -96.2) * mm, "end": v(-54.9, -96.41) * mm});
            skLineSegment(sketch, "E2714", {"start": v(-54.9, -96.41) * mm, "end": v(-54.95, -96.63) * mm});
            skLineSegment(sketch, "E2715", {"start": v(-54.95, -96.63) * mm, "end": v(-55, -96.84) * mm});
            skLineSegment(sketch, "E2716", {"start": v(-55, -96.84) * mm, "end": v(-55.07, -97.07) * mm});
            skLineSegment(sketch, "E2717", {"start": v(-55.07, -97.07) * mm, "end": v(-55.12, -97.3) * mm});
            skLineSegment(sketch, "E2718", {"start": v(-55.12, -97.3) * mm, "end": v(-55.18, -97.53) * mm});
            skLineSegment(sketch, "E2719", {"start": v(-55.18, -97.53) * mm, "end": v(-55.23, -97.78) * mm});
            skLineSegment(sketch, "E2720", {"start": v(-55.23, -97.78) * mm, "end": v(-55.29, -98.03) * mm});
            skLineSegment(sketch, "E2721", {"start": v(-55.29, -98.03) * mm, "end": v(-55.34, -98.29) * mm});
            skLineSegment(sketch, "E2722", {"start": v(-55.34, -98.29) * mm, "end": v(-55.4, -98.55) * mm});
            skLineSegment(sketch, "E2723", {"start": v(-55.4, -98.55) * mm, "end": v(-55.45, -98.82) * mm});
            skLineSegment(sketch, "E2724", {"start": v(-55.45, -98.82) * mm, "end": v(-55.5, -99.1) * mm});
            skLineSegment(sketch, "E2725", {"start": v(-55.5, -99.1) * mm, "end": v(-55.55, -99.39) * mm});
            skLineSegment(sketch, "E2726", {"start": v(-55.55, -99.39) * mm, "end": v(-55.6, -99.68) * mm});
            skLineSegment(sketch, "E2727", {"start": v(-55.6, -99.68) * mm, "end": v(-55.65, -99.98) * mm});
            skLineSegment(sketch, "E2728", {"start": v(-55.65, -99.98) * mm, "end": v(-55.7, -100.28) * mm});
            skLineSegment(sketch, "E2729", {"start": v(-55.7, -100.28) * mm, "end": v(-55.74, -100.6) * mm});
            skLineSegment(sketch, "E2730", {"start": v(-55.74, -100.6) * mm, "end": v(-55.79, -100.91) * mm});
            skLineSegment(sketch, "E2731", {"start": v(-55.79, -100.91) * mm, "end": v(-55.83, -101.24) * mm});
            skLineSegment(sketch, "E2732", {"start": v(-55.83, -101.24) * mm, "end": v(-55.87, -101.57) * mm});
            skLineSegment(sketch, "E2733", {"start": v(-55.87, -101.57) * mm, "end": v(-55.9, -101.9) * mm});
            skLineSegment(sketch, "E2734", {"start": v(-55.9, -101.9) * mm, "end": v(-55.95, -102.25) * mm});
            skLineSegment(sketch, "E2735", {"start": v(-55.95, -102.25) * mm, "end": v(-55.98, -102.6) * mm});
            skLineSegment(sketch, "E2736", {"start": v(-55.98, -102.6) * mm, "end": v(-56.01, -102.96) * mm});
            skLineSegment(sketch, "E2737", {"start": v(-56.01, -102.96) * mm, "end": v(-56.04, -103.33) * mm});
            skLineSegment(sketch, "E2738", {"start": v(-56.04, -103.33) * mm, "end": v(-56.07, -103.7) * mm});
            skLineSegment(sketch, "E2739", {"start": v(-56.07, -103.7) * mm, "end": v(-56.1, -104.08) * mm});
            skLineSegment(sketch, "E2740", {"start": v(-56.1, -104.08) * mm, "end": v(-56.12, -104.46) * mm});
            skLineSegment(sketch, "E2741", {"start": v(-56.12, -104.46) * mm, "end": v(-56.14, -104.86) * mm});
            skLineSegment(sketch, "E2742", {"start": v(-56.14, -104.86) * mm, "end": v(-56.16, -105.26) * mm});
            skLineSegment(sketch, "E2743", {"start": v(-56.16, -105.26) * mm, "end": v(-56.05, -105.43) * mm});
            skLineSegment(sketch, "E2744", {"start": v(-56.05, -105.43) * mm, "end": v(-52.93, -107.04) * mm});
            skLineSegment(sketch, "E2745", {"start": v(-52.93, -107.04) * mm, "end": v(-52.72, -107.02) * mm});
            skLineSegment(sketch, "E2746", {"start": v(-52.72, -107.02) * mm, "end": v(-52.41, -106.77) * mm});
            skLineSegment(sketch, "E2747", {"start": v(-52.41, -106.77) * mm, "end": v(-52.1, -106.53) * mm});
            skLineSegment(sketch, "E2748", {"start": v(-52.1, -106.53) * mm, "end": v(-51.8, -106.28) * mm});
            skLineSegment(sketch, "E2749", {"start": v(-51.8, -106.28) * mm, "end": v(-51.51, -106.04) * mm});
            skLineSegment(sketch, "E2750", {"start": v(-51.51, -106.04) * mm, "end": v(-51.23, -105.8) * mm});
            skLineSegment(sketch, "E2751", {"start": v(-51.23, -105.8) * mm, "end": v(-50.95, -105.56) * mm});
            skLineSegment(sketch, "E2752", {"start": v(-50.95, -105.56) * mm, "end": v(-50.67, -105.33) * mm});
            skLineSegment(sketch, "E2753", {"start": v(-50.67, -105.33) * mm, "end": v(-50.4, -105.1) * mm});
            skLineSegment(sketch, "E2754", {"start": v(-50.4, -105.1) * mm, "end": v(-50.15, -104.86) * mm});
            skLineSegment(sketch, "E2755", {"start": v(-50.15, -104.86) * mm, "end": v(-49.9, -104.64) * mm});
            skLineSegment(sketch, "E2756", {"start": v(-49.9, -104.64) * mm, "end": v(-49.65, -104.4) * mm});
            skLineSegment(sketch, "E2757", {"start": v(-49.65, -104.4) * mm, "end": v(-49.41, -104.18) * mm});
            skLineSegment(sketch, "E2758", {"start": v(-49.41, -104.18) * mm, "end": v(-49.18, -103.96) * mm});
            skLineSegment(sketch, "E2759", {"start": v(-49.18, -103.96) * mm, "end": v(-48.95, -103.74) * mm});
            skLineSegment(sketch, "E2760", {"start": v(-48.95, -103.74) * mm, "end": v(-48.73, -103.53) * mm});
            skLineSegment(sketch, "E2761", {"start": v(-48.73, -103.53) * mm, "end": v(-48.52, -103.32) * mm});
            skLineSegment(sketch, "E2762", {"start": v(-48.52, -103.32) * mm, "end": v(-48.3, -103.1) * mm});
            skLineSegment(sketch, "E2763", {"start": v(-48.3, -103.1) * mm, "end": v(-48.1, -102.9) * mm});
            skLineSegment(sketch, "E2764", {"start": v(-48.1, -102.9) * mm, "end": v(-47.91, -102.7) * mm});
            skLineSegment(sketch, "E2765", {"start": v(-47.91, -102.7) * mm, "end": v(-47.72, -102.5) * mm});
            skLineSegment(sketch, "E2766", {"start": v(-47.72, -102.5) * mm, "end": v(-47.54, -102.3) * mm});
            skLineSegment(sketch, "E2767", {"start": v(-47.54, -102.3) * mm, "end": v(-47.36, -102.1) * mm});
            skLineSegment(sketch, "E2768", {"start": v(-47.36, -102.1) * mm, "end": v(-47.19, -101.91) * mm});
            skLineSegment(sketch, "E2769", {"start": v(-47.19, -101.91) * mm, "end": v(-47.02, -101.72) * mm});
            skLineSegment(sketch, "E2770", {"start": v(-47.02, -101.72) * mm, "end": v(-46.86, -101.54) * mm});
            skLineSegment(sketch, "E2771", {"start": v(-46.86, -101.54) * mm, "end": v(-46.7, -101.36) * mm});
            skLineSegment(sketch, "E2772", {"start": v(-46.7, -101.36) * mm, "end": v(-46.56, -101.18) * mm});
            skLineSegment(sketch, "E2773", {"start": v(-46.56, -101.18) * mm, "end": v(-46.41, -101.01) * mm});
            skLineSegment(sketch, "E2774", {"start": v(-46.41, -101.01) * mm, "end": v(-46.27, -100.84) * mm});
            skLineSegment(sketch, "E2775", {"start": v(-46.27, -100.84) * mm, "end": v(-46.14, -100.68) * mm});
            skLineSegment(sketch, "E2776", {"start": v(-46.14, -100.68) * mm, "end": v(-46.01, -100.52) * mm});
            skLineSegment(sketch, "E2777", {"start": v(-46.01, -100.52) * mm, "end": v(-45.9, -100.36) * mm});
            skLineSegment(sketch, "E2778", {"start": v(-45.9, -100.36) * mm, "end": v(-45.77, -100.2) * mm});
            skLineSegment(sketch, "E2779", {"start": v(-45.77, -100.2) * mm, "end": v(-45.66, -100.06) * mm});
            skLineSegment(sketch, "E2780", {"start": v(-45.66, -100.06) * mm, "end": v(-45.55, -99.92) * mm});
            skLineSegment(sketch, "E2781", {"start": v(-45.55, -99.92) * mm, "end": v(-45.45, -99.78) * mm});
            skLineSegment(sketch, "E2782", {"start": v(-45.45, -99.78) * mm, "end": v(-45.35, -99.64) * mm});
            skLineSegment(sketch, "E2783", {"start": v(-45.35, -99.64) * mm, "end": v(-45.26, -99.51) * mm});
            skLineSegment(sketch, "E2784", {"start": v(-45.26, -99.51) * mm, "end": v(-45.17, -99.38) * mm});
            skLineSegment(sketch, "E2785", {"start": v(-45.17, -99.38) * mm, "end": v(-45.1, -99.26) * mm});
            skLineSegment(sketch, "E2786", {"start": v(-45.1, -99.26) * mm, "end": v(-45.01, -99.15) * mm});
            skLineSegment(sketch, "E2787", {"start": v(-45.01, -99.15) * mm, "end": v(-44.94, -99.04) * mm});
            skLineSegment(sketch, "E2788", {"start": v(-44.94, -99.04) * mm, "end": v(-44.7, -98.85) * mm});
            skLineSegment(sketch, "E2789", {"start": v(-44.7, -98.85) * mm, "end": v(-40.6, -100.6) * mm});
            skLineSegment(sketch, "E2790", {"start": v(-40.6, -100.6) * mm, "end": v(-40.57, -100.9) * mm});
            skLineSegment(sketch, "E2791", {"start": v(-40.57, -100.9) * mm, "end": v(-40.6, -101.04) * mm});
            skLineSegment(sketch, "E2792", {"start": v(-40.6, -101.04) * mm, "end": v(-40.63, -101.18) * mm});
            skLineSegment(sketch, "E2793", {"start": v(-40.63, -101.18) * mm, "end": v(-40.66, -101.32) * mm});
            skLineSegment(sketch, "E2794", {"start": v(-40.66, -101.32) * mm, "end": v(-40.69, -101.47) * mm});
            skLineSegment(sketch, "E2795", {"start": v(-40.69, -101.47) * mm, "end": v(-40.72, -101.63) * mm});
            skLineSegment(sketch, "E2796", {"start": v(-40.72, -101.63) * mm, "end": v(-40.75, -101.8) * mm});
            skLineSegment(sketch, "E2797", {"start": v(-40.75, -101.8) * mm, "end": v(-40.78, -101.96) * mm});
            skLineSegment(sketch, "E2798", {"start": v(-40.78, -101.96) * mm, "end": v(-40.8, -102.14) * mm});
            skLineSegment(sketch, "E2799", {"start": v(-40.8, -102.14) * mm, "end": v(-40.84, -102.32) * mm});
            skLineSegment(sketch, "E2800", {"start": v(-40.84, -102.32) * mm, "end": v(-40.87, -102.51) * mm});
            skLineSegment(sketch, "E2801", {"start": v(-40.87, -102.51) * mm, "end": v(-40.9, -102.7) * mm});
            skLineSegment(sketch, "E2802", {"start": v(-40.9, -102.7) * mm, "end": v(-40.92, -102.91) * mm});
            skLineSegment(sketch, "E2803", {"start": v(-40.92, -102.91) * mm, "end": v(-40.95, -103.12) * mm});
            skLineSegment(sketch, "E2804", {"start": v(-40.95, -103.12) * mm, "end": v(-40.98, -103.34) * mm});
            skLineSegment(sketch, "E2805", {"start": v(-40.98, -103.34) * mm, "end": v(-41, -103.56) * mm});
            skLineSegment(sketch, "E2806", {"start": v(-41, -103.56) * mm, "end": v(-41.03, -103.8) * mm});
            skLineSegment(sketch, "E2807", {"start": v(-41.03, -103.8) * mm, "end": v(-41.05, -104.03) * mm});
            skLineSegment(sketch, "E2808", {"start": v(-41.05, -104.03) * mm, "end": v(-41.07, -104.27) * mm});
            skLineSegment(sketch, "E2809", {"start": v(-41.07, -104.27) * mm, "end": v(-41.1, -104.52) * mm});
            skLineSegment(sketch, "E2810", {"start": v(-41.1, -104.52) * mm, "end": v(-41.11, -104.78) * mm});
            skLineSegment(sketch, "E2811", {"start": v(-41.11, -104.78) * mm, "end": v(-41.13, -105.04) * mm});
            skLineSegment(sketch, "E2812", {"start": v(-41.13, -105.04) * mm, "end": v(-41.15, -105.3) * mm});
            skLineSegment(sketch, "E2813", {"start": v(-41.15, -105.3) * mm, "end": v(-41.16, -105.58) * mm});
            skLineSegment(sketch, "E2814", {"start": v(-41.16, -105.58) * mm, "end": v(-41.17, -105.87) * mm});
            skLineSegment(sketch, "E2815", {"start": v(-41.17, -105.87) * mm, "end": v(-41.19, -106.16) * mm});
            skLineSegment(sketch, "E2816", {"start": v(-41.19, -106.16) * mm, "end": v(-41.2, -106.45) * mm});
            skLineSegment(sketch, "E2817", {"start": v(-41.2, -106.45) * mm, "end": v(-41.2, -106.75) * mm});
            skLineSegment(sketch, "E2818", {"start": v(-41.2, -106.75) * mm, "end": v(-41.2, -107.06) * mm});
            skLineSegment(sketch, "E2819", {"start": v(-41.2, -107.06) * mm, "end": v(-41.2, -107.38) * mm});
            skLineSegment(sketch, "E2820", {"start": v(-41.2, -107.38) * mm, "end": v(-41.2, -107.7) * mm});
            skLineSegment(sketch, "E2821", {"start": v(-41.2, -107.7) * mm, "end": v(-41.2, -108.03) * mm});
            skLineSegment(sketch, "E2822", {"start": v(-41.2, -108.03) * mm, "end": v(-41.2, -108.36) * mm});
            skLineSegment(sketch, "E2823", {"start": v(-41.2, -108.36) * mm, "end": v(-41.19, -108.7) * mm});
            skLineSegment(sketch, "E2824", {"start": v(-41.19, -108.7) * mm, "end": v(-41.18, -109.05) * mm});
            skLineSegment(sketch, "E2825", {"start": v(-41.18, -109.05) * mm, "end": v(-41.16, -109.4) * mm});
            skLineSegment(sketch, "E2826", {"start": v(-41.16, -109.4) * mm, "end": v(-41.15, -109.76) * mm});
            skLineSegment(sketch, "E2827", {"start": v(-41.15, -109.76) * mm, "end": v(-41.12, -110.13) * mm});
            skLineSegment(sketch, "E2828", {"start": v(-41.12, -110.13) * mm, "end": v(-41.1, -110.5) * mm});
            skLineSegment(sketch, "E2829", {"start": v(-41.1, -110.5) * mm, "end": v(-41.07, -110.88) * mm});
            skLineSegment(sketch, "E2830", {"start": v(-41.07, -110.88) * mm, "end": v(-41.04, -111.26) * mm});
            skLineSegment(sketch, "E2831", {"start": v(-41.04, -111.26) * mm, "end": v(-41, -111.66) * mm});
            skLineSegment(sketch, "E2832", {"start": v(-41, -111.66) * mm, "end": v(-40.97, -112.05) * mm});
            skLineSegment(sketch, "E2833", {"start": v(-40.97, -112.05) * mm, "end": v(-40.84, -112.21) * mm});
            skLineSegment(sketch, "E2834", {"start": v(-40.84, -112.21) * mm, "end": v(-37.52, -113.37) * mm});
            skLineSegment(sketch, "E2835", {"start": v(-37.52, -113.37) * mm, "end": v(-37.32, -113.32) * mm});
            skLineSegment(sketch, "E2836", {"start": v(-37.32, -113.32) * mm, "end": v(-37.05, -113.03) * mm});
            skLineSegment(sketch, "E2837", {"start": v(-37.05, -113.03) * mm, "end": v(-36.78, -112.75) * mm});
            skLineSegment(sketch, "E2838", {"start": v(-36.78, -112.75) * mm, "end": v(-36.51, -112.47) * mm});
            skLineSegment(sketch, "E2839", {"start": v(-36.51, -112.47) * mm, "end": v(-36.26, -112.18) * mm});
            skLineSegment(sketch, "E2840", {"start": v(-36.26, -112.18) * mm, "end": v(-36, -111.9) * mm});
            skLineSegment(sketch, "E2841", {"start": v(-36, -111.9) * mm, "end": v(-35.76, -111.63) * mm});
            skLineSegment(sketch, "E2842", {"start": v(-35.76, -111.63) * mm, "end": v(-35.53, -111.36) * mm});
            skLineSegment(sketch, "E2843", {"start": v(-35.53, -111.36) * mm, "end": v(-35.3, -111.1) * mm});
            skLineSegment(sketch, "E2844", {"start": v(-35.3, -111.1) * mm, "end": v(-35.07, -110.83) * mm});
            skLineSegment(sketch, "E2845", {"start": v(-35.07, -110.83) * mm, "end": v(-34.85, -110.57) * mm});
            skLineSegment(sketch, "E2846", {"start": v(-34.85, -110.57) * mm, "end": v(-34.64, -110.3) * mm});
            skLineSegment(sketch, "E2847", {"start": v(-34.64, -110.3) * mm, "end": v(-34.44, -110.05) * mm});
            skLineSegment(sketch, "E2848", {"start": v(-34.44, -110.05) * mm, "end": v(-34.24, -109.8) * mm});
            skLineSegment(sketch, "E2849", {"start": v(-34.24, -109.8) * mm, "end": v(-34.04, -109.55) * mm});
            skLineSegment(sketch, "E2850", {"start": v(-34.04, -109.55) * mm, "end": v(-33.85, -109.3) * mm});
            skLineSegment(sketch, "E2851", {"start": v(-33.85, -109.3) * mm, "end": v(-33.67, -109.07) * mm});
            skLineSegment(sketch, "E2852", {"start": v(-33.67, -109.07) * mm, "end": v(-33.5, -108.83) * mm});
            skLineSegment(sketch, "E2853", {"start": v(-33.5, -108.83) * mm, "end": v(-33.32, -108.6) * mm});
            skLineSegment(sketch, "E2854", {"start": v(-33.32, -108.6) * mm, "end": v(-33.16, -108.37) * mm});
            skLineSegment(sketch, "E2855", {"start": v(-33.16, -108.37) * mm, "end": v(-33, -108.14) * mm});
            skLineSegment(sketch, "E2856", {"start": v(-33, -108.14) * mm, "end": v(-32.84, -107.92) * mm});
            skLineSegment(sketch, "E2857", {"start": v(-32.84, -107.92) * mm, "end": v(-32.7, -107.7) * mm});
            skLineSegment(sketch, "E2858", {"start": v(-32.7, -107.7) * mm, "end": v(-32.55, -107.5) * mm});
            skLineSegment(sketch, "E2859", {"start": v(-32.55, -107.5) * mm, "end": v(-32.41, -107.28) * mm});
            skLineSegment(sketch, "E2860", {"start": v(-32.41, -107.28) * mm, "end": v(-32.28, -107.08) * mm});
            skLineSegment(sketch, "E2861", {"start": v(-32.28, -107.08) * mm, "end": v(-32.15, -106.88) * mm});
            skLineSegment(sketch, "E2862", {"start": v(-32.15, -106.88) * mm, "end": v(-32.03, -106.68) * mm});
            skLineSegment(sketch, "E2863", {"start": v(-32.03, -106.68) * mm, "end": v(-31.9, -106.5) * mm});
            skLineSegment(sketch, "E2864", {"start": v(-31.9, -106.5) * mm, "end": v(-31.8, -106.3) * mm});
            skLineSegment(sketch, "E2865", {"start": v(-31.8, -106.3) * mm, "end": v(-31.69, -106.12) * mm});
            skLineSegment(sketch, "E2866", {"start": v(-31.69, -106.12) * mm, "end": v(-31.58, -105.95) * mm});
            skLineSegment(sketch, "E2867", {"start": v(-31.58, -105.95) * mm, "end": v(-31.48, -105.78) * mm});
            skLineSegment(sketch, "E2868", {"start": v(-31.48, -105.78) * mm, "end": v(-31.39, -105.6) * mm});
            skLineSegment(sketch, "E2869", {"start": v(-31.39, -105.6) * mm, "end": v(-31.3, -105.45) * mm});
            skLineSegment(sketch, "E2870", {"start": v(-31.3, -105.45) * mm, "end": v(-31.21, -105.29) * mm});
            skLineSegment(sketch, "E2871", {"start": v(-31.21, -105.29) * mm, "end": v(-31.13, -105.14) * mm});
            skLineSegment(sketch, "E2872", {"start": v(-31.13, -105.14) * mm, "end": v(-31.05, -104.99) * mm});
            skLineSegment(sketch, "E2873", {"start": v(-31.05, -104.99) * mm, "end": v(-30.98, -104.85) * mm});
            skLineSegment(sketch, "E2874", {"start": v(-30.98, -104.85) * mm, "end": v(-30.9, -104.71) * mm});
            skLineSegment(sketch, "E2875", {"start": v(-30.9, -104.71) * mm, "end": v(-30.84, -104.58) * mm});
            skLineSegment(sketch, "E2876", {"start": v(-30.84, -104.58) * mm, "end": v(-30.78, -104.45) * mm});
            skLineSegment(sketch, "E2877", {"start": v(-30.78, -104.45) * mm, "end": v(-30.72, -104.33) * mm});
            skLineSegment(sketch, "E2878", {"start": v(-30.72, -104.33) * mm, "end": v(-30.52, -104.12) * mm});
            skLineSegment(sketch, "E2879", {"start": v(-30.52, -104.12) * mm, "end": v(-26.2, -105.29) * mm});
            skLineSegment(sketch, "E2880", {"start": v(-26.2, -105.29) * mm, "end": v(-26.13, -105.58) * mm});
            skLineSegment(sketch, "E2881", {"start": v(-26.13, -105.58) * mm, "end": v(-26.14, -105.71) * mm});
            skLineSegment(sketch, "E2882", {"start": v(-26.14, -105.71) * mm, "end": v(-26.16, -105.85) * mm});
            skLineSegment(sketch, "E2883", {"start": v(-26.16, -105.85) * mm, "end": v(-26.17, -106) * mm});
            skLineSegment(sketch, "E2884", {"start": v(-26.17, -106) * mm, "end": v(-26.17, -106.15) * mm});
            skLineSegment(sketch, "E2885", {"start": v(-26.17, -106.15) * mm, "end": v(-26.18, -106.31) * mm});
            skLineSegment(sketch, "E2886", {"start": v(-26.18, -106.31) * mm, "end": v(-26.19, -106.48) * mm});
            skLineSegment(sketch, "E2887", {"start": v(-26.19, -106.48) * mm, "end": v(-26.2, -106.65) * mm});
            skLineSegment(sketch, "E2888", {"start": v(-26.2, -106.65) * mm, "end": v(-26.2, -106.83) * mm});
            skLineSegment(sketch, "E2889", {"start": v(-26.2, -106.83) * mm, "end": v(-26.2, -107.02) * mm});
            skLineSegment(sketch, "E2890", {"start": v(-26.2, -107.02) * mm, "end": v(-26.2, -107.2) * mm});
            skLineSegment(sketch, "E2891", {"start": v(-26.2, -107.2) * mm, "end": v(-26.2, -107.4) * mm});
            skLineSegment(sketch, "E2892", {"start": v(-26.2, -107.4) * mm, "end": v(-26.2, -107.61) * mm});
            skLineSegment(sketch, "E2893", {"start": v(-26.2, -107.61) * mm, "end": v(-26.2, -107.82) * mm});
            skLineSegment(sketch, "E2894", {"start": v(-26.2, -107.82) * mm, "end": v(-26.2, -108.04) * mm});
            skLineSegment(sketch, "E2895", {"start": v(-26.2, -108.04) * mm, "end": v(-26.2, -108.27) * mm});
            skLineSegment(sketch, "E2896", {"start": v(-26.2, -108.27) * mm, "end": v(-26.19, -108.5) * mm});
            skLineSegment(sketch, "E2897", {"start": v(-26.19, -108.5) * mm, "end": v(-26.18, -108.73) * mm});
            skLineSegment(sketch, "E2898", {"start": v(-26.18, -108.73) * mm, "end": v(-26.17, -108.98) * mm});
            skLineSegment(sketch, "E2899", {"start": v(-26.17, -108.98) * mm, "end": v(-26.15, -109.23) * mm});
            skLineSegment(sketch, "E2900", {"start": v(-26.15, -109.23) * mm, "end": v(-26.14, -109.48) * mm});
            skLineSegment(sketch, "E2901", {"start": v(-26.14, -109.48) * mm, "end": v(-26.12, -109.75) * mm});
            skLineSegment(sketch, "E2902", {"start": v(-26.12, -109.75) * mm, "end": v(-26.1, -110.01) * mm});
            skLineSegment(sketch, "E2903", {"start": v(-26.1, -110.01) * mm, "end": v(-26.07, -110.29) * mm});
            skLineSegment(sketch, "E2904", {"start": v(-26.07, -110.29) * mm, "end": v(-26.05, -110.57) * mm});
            skLineSegment(sketch, "E2905", {"start": v(-26.05, -110.57) * mm, "end": v(-26.02, -110.86) * mm});
            skLineSegment(sketch, "E2906", {"start": v(-26.02, -110.86) * mm, "end": v(-25.98, -111.15) * mm});
            skLineSegment(sketch, "E2907", {"start": v(-25.98, -111.15) * mm, "end": v(-25.95, -111.45) * mm});
            skLineSegment(sketch, "E2908", {"start": v(-25.95, -111.45) * mm, "end": v(-25.91, -111.76) * mm});
            skLineSegment(sketch, "E2909", {"start": v(-25.91, -111.76) * mm, "end": v(-25.87, -112.07) * mm});
            skLineSegment(sketch, "E2910", {"start": v(-25.87, -112.07) * mm, "end": v(-25.82, -112.4) * mm});
            skLineSegment(sketch, "E2911", {"start": v(-25.82, -112.4) * mm, "end": v(-25.77, -112.71) * mm});
            skLineSegment(sketch, "E2912", {"start": v(-25.77, -112.71) * mm, "end": v(-25.72, -113.05) * mm});
            skLineSegment(sketch, "E2913", {"start": v(-25.72, -113.05) * mm, "end": v(-25.67, -113.38) * mm});
            skLineSegment(sketch, "E2914", {"start": v(-25.67, -113.38) * mm, "end": v(-25.6, -113.72) * mm});
            skLineSegment(sketch, "E2915", {"start": v(-25.6, -113.72) * mm, "end": v(-25.54, -114.07) * mm});
            skLineSegment(sketch, "E2916", {"start": v(-25.54, -114.07) * mm, "end": v(-25.48, -114.43) * mm});
            skLineSegment(sketch, "E2917", {"start": v(-25.48, -114.43) * mm, "end": v(-25.4, -114.79) * mm});
            skLineSegment(sketch, "E2918", {"start": v(-25.4, -114.79) * mm, "end": v(-25.33, -115.15) * mm});
            skLineSegment(sketch, "E2919", {"start": v(-25.33, -115.15) * mm, "end": v(-25.25, -115.52) * mm});
            skLineSegment(sketch, "E2920", {"start": v(-25.25, -115.52) * mm, "end": v(-25.16, -115.9) * mm});
            skLineSegment(sketch, "E2921", {"start": v(-25.16, -115.9) * mm, "end": v(-25.08, -116.28) * mm});
            skLineSegment(sketch, "E2922", {"start": v(-25.08, -116.28) * mm, "end": v(-24.98, -116.67) * mm});
            skLineSegment(sketch, "E2923", {"start": v(-24.98, -116.67) * mm, "end": v(-24.83, -116.81) * mm});
            skLineSegment(sketch, "E2924", {"start": v(-24.83, -116.81) * mm, "end": v(-21.39, -117.5) * mm});
            skLineSegment(sketch, "E2925", {"start": v(-21.39, -117.5) * mm, "end": v(-21.2, -117.42) * mm});
            skLineSegment(sketch, "E2926", {"start": v(-21.2, -117.42) * mm, "end": v(-20.96, -117.1) * mm});
            skLineSegment(sketch, "E2927", {"start": v(-20.96, -117.1) * mm, "end": v(-20.73, -116.77) * mm});
            skLineSegment(sketch, "E2928", {"start": v(-20.73, -116.77) * mm, "end": v(-20.51, -116.46) * mm});
            skLineSegment(sketch, "E2929", {"start": v(-20.51, -116.46) * mm, "end": v(-20.3, -116.15) * mm});
            skLineSegment(sketch, "E2930", {"start": v(-20.3, -116.15) * mm, "end": v(-20.09, -115.84) * mm});
            skLineSegment(sketch, "E2931", {"start": v(-20.09, -115.84) * mm, "end": v(-19.89, -115.53) * mm});
            skLineSegment(sketch, "E2932", {"start": v(-19.89, -115.53) * mm, "end": v(-19.69, -115.23) * mm});
            skLineSegment(sketch, "E2933", {"start": v(-19.69, -115.23) * mm, "end": v(-19.5, -114.93) * mm});
            skLineSegment(sketch, "E2934", {"start": v(-19.5, -114.93) * mm, "end": v(-19.31, -114.64) * mm});
            skLineSegment(sketch, "E2935", {"start": v(-19.31, -114.64) * mm, "end": v(-19.13, -114.35) * mm});
            skLineSegment(sketch, "E2936", {"start": v(-19.13, -114.35) * mm, "end": v(-18.96, -114.06) * mm});
            skLineSegment(sketch, "E2937", {"start": v(-18.96, -114.06) * mm, "end": v(-18.8, -113.78) * mm});
            skLineSegment(sketch, "E2938", {"start": v(-18.8, -113.78) * mm, "end": v(-18.63, -113.5) * mm});
            skLineSegment(sketch, "E2939", {"start": v(-18.63, -113.5) * mm, "end": v(-18.47, -113.23) * mm});
            skLineSegment(sketch, "E2940", {"start": v(-18.47, -113.23) * mm, "end": v(-18.32, -112.96) * mm});
            skLineSegment(sketch, "E2941", {"start": v(-18.32, -112.96) * mm, "end": v(-18.17, -112.7) * mm});
            skLineSegment(sketch, "E2942", {"start": v(-18.17, -112.7) * mm, "end": v(-18.03, -112.44) * mm});
            skLineSegment(sketch, "E2943", {"start": v(-18.03, -112.44) * mm, "end": v(-17.9, -112.18) * mm});
            skLineSegment(sketch, "E2944", {"start": v(-17.9, -112.18) * mm, "end": v(-17.76, -111.93) * mm});
            skLineSegment(sketch, "E2945", {"start": v(-17.76, -111.93) * mm, "end": v(-17.63, -111.69) * mm});
            skLineSegment(sketch, "E2946", {"start": v(-17.63, -111.69) * mm, "end": v(-17.51, -111.45) * mm});
            skLineSegment(sketch, "E2947", {"start": v(-17.51, -111.45) * mm, "end": v(-17.4, -111.21) * mm});
            skLineSegment(sketch, "E2948", {"start": v(-17.4, -111.21) * mm, "end": v(-17.28, -110.98) * mm});
            skLineSegment(sketch, "E2949", {"start": v(-17.28, -110.98) * mm, "end": v(-17.17, -110.75) * mm});
            skLineSegment(sketch, "E2950", {"start": v(-17.17, -110.75) * mm, "end": v(-17.07, -110.53) * mm});
            skLineSegment(sketch, "E2951", {"start": v(-17.07, -110.53) * mm, "end": v(-16.97, -110.32) * mm});
            skLineSegment(sketch, "E2952", {"start": v(-16.97, -110.32) * mm, "end": v(-16.88, -110.1) * mm});
            skLineSegment(sketch, "E2953", {"start": v(-16.88, -110.1) * mm, "end": v(-16.78, -109.9) * mm});
            skLineSegment(sketch, "E2954", {"start": v(-16.78, -109.9) * mm, "end": v(-16.7, -109.7) * mm});
            skLineSegment(sketch, "E2955", {"start": v(-16.7, -109.7) * mm, "end": v(-16.62, -109.5) * mm});
            skLineSegment(sketch, "E2956", {"start": v(-16.62, -109.5) * mm, "end": v(-16.54, -109.32) * mm});
            skLineSegment(sketch, "E2957", {"start": v(-16.54, -109.32) * mm, "end": v(-16.46, -109.13) * mm});
            skLineSegment(sketch, "E2958", {"start": v(-16.46, -109.13) * mm, "end": v(-16.4, -108.95) * mm});
            skLineSegment(sketch, "E2959", {"start": v(-16.4, -108.95) * mm, "end": v(-16.32, -108.78) * mm});
            skLineSegment(sketch, "E2960", {"start": v(-16.32, -108.78) * mm, "end": v(-16.26, -108.61) * mm});
            skLineSegment(sketch, "E2961", {"start": v(-16.26, -108.61) * mm, "end": v(-16.2, -108.45) * mm});
            skLineSegment(sketch, "E2962", {"start": v(-16.2, -108.45) * mm, "end": v(-16.15, -108.3) * mm});
            skLineSegment(sketch, "E2963", {"start": v(-16.15, -108.3) * mm, "end": v(-16.1, -108.14) * mm});
            skLineSegment(sketch, "E2964", {"start": v(-16.1, -108.14) * mm, "end": v(-16.04, -108) * mm});
            skLineSegment(sketch, "E2965", {"start": v(-16.04, -108) * mm, "end": v(-16, -107.86) * mm});
            skLineSegment(sketch, "E2966", {"start": v(-16, -107.86) * mm, "end": v(-15.95, -107.73) * mm});
            skLineSegment(sketch, "E2967", {"start": v(-15.95, -107.73) * mm, "end": v(-15.91, -107.6) * mm});
            skLineSegment(sketch, "E2968", {"start": v(-15.91, -107.6) * mm, "end": v(-15.74, -107.36) * mm});
            skLineSegment(sketch, "E2969", {"start": v(-15.74, -107.36) * mm, "end": v(-11.3, -107.91) * mm});
            skLineSegment(sketch, "E2970", {"start": v(-11.3, -107.91) * mm, "end": v(-11.2, -108.2) * mm});
            skLineSegment(sketch, "E2971", {"start": v(-11.2, -108.2) * mm, "end": v(-11.18, -108.33) * mm});
            skLineSegment(sketch, "E2972", {"start": v(-11.18, -108.33) * mm, "end": v(-11.18, -108.47) * mm});
            skLineSegment(sketch, "E2973", {"start": v(-11.18, -108.47) * mm, "end": v(-11.17, -108.61) * mm});
            skLineSegment(sketch, "E2974", {"start": v(-11.17, -108.61) * mm, "end": v(-11.15, -108.77) * mm});
            skLineSegment(sketch, "E2975", {"start": v(-11.15, -108.77) * mm, "end": v(-11.14, -108.93) * mm});
            skLineSegment(sketch, "E2976", {"start": v(-11.14, -108.93) * mm, "end": v(-11.12, -109.1) * mm});
            skLineSegment(sketch, "E2977", {"start": v(-11.12, -109.1) * mm, "end": v(-11.1, -109.26) * mm});
            skLineSegment(sketch, "E2978", {"start": v(-11.1, -109.26) * mm, "end": v(-11.09, -109.44) * mm});
            skLineSegment(sketch, "E2979", {"start": v(-11.09, -109.44) * mm, "end": v(-11.06, -109.63) * mm});
            skLineSegment(sketch, "E2980", {"start": v(-11.06, -109.63) * mm, "end": v(-11.04, -109.82) * mm});
            skLineSegment(sketch, "E2981", {"start": v(-11.04, -109.82) * mm, "end": v(-11.01, -110.01) * mm});
            skLineSegment(sketch, "E2982", {"start": v(-11.01, -110.01) * mm, "end": v(-10.98, -110.22) * mm});
            skLineSegment(sketch, "E2983", {"start": v(-10.98, -110.22) * mm, "end": v(-10.95, -110.43) * mm});
            skLineSegment(sketch, "E2984", {"start": v(-10.95, -110.43) * mm, "end": v(-10.92, -110.64) * mm});
            skLineSegment(sketch, "E2985", {"start": v(-10.92, -110.64) * mm, "end": v(-10.88, -110.86) * mm});
            skLineSegment(sketch, "E2986", {"start": v(-10.88, -110.86) * mm, "end": v(-10.84, -111.1) * mm});
            skLineSegment(sketch, "E2987", {"start": v(-10.84, -111.1) * mm, "end": v(-10.8, -111.32) * mm});
            skLineSegment(sketch, "E2988", {"start": v(-10.8, -111.32) * mm, "end": v(-10.75, -111.56) * mm});
            skLineSegment(sketch, "E2989", {"start": v(-10.75, -111.56) * mm, "end": v(-10.7, -111.8) * mm});
            skLineSegment(sketch, "E2990", {"start": v(-10.7, -111.8) * mm, "end": v(-10.65, -112.06) * mm});
            skLineSegment(sketch, "E2991", {"start": v(-10.65, -112.06) * mm, "end": v(-10.6, -112.32) * mm});
            skLineSegment(sketch, "E2992", {"start": v(-10.6, -112.32) * mm, "end": v(-10.54, -112.58) * mm});
            skLineSegment(sketch, "E2993", {"start": v(-10.54, -112.58) * mm, "end": v(-10.48, -112.85) * mm});
            skLineSegment(sketch, "E2994", {"start": v(-10.48, -112.85) * mm, "end": v(-10.41, -113.13) * mm});
            skLineSegment(sketch, "E2995", {"start": v(-10.41, -113.13) * mm, "end": v(-10.34, -113.4) * mm});
            skLineSegment(sketch, "E2996", {"start": v(-10.34, -113.4) * mm, "end": v(-10.27, -113.7) * mm});
            skLineSegment(sketch, "E2997", {"start": v(-10.27, -113.7) * mm, "end": v(-10.2, -113.99) * mm});
            skLineSegment(sketch, "E2998", {"start": v(-10.2, -113.99) * mm, "end": v(-10.11, -114.28) * mm});
            skLineSegment(sketch, "E2999", {"start": v(-10.11, -114.28) * mm, "end": v(-10.03, -114.59) * mm});
            skLineSegment(sketch, "E3000", {"start": v(-10.03, -114.59) * mm, "end": v(-9.94, -114.9) * mm});
            skLineSegment(sketch, "E3001", {"start": v(-9.94, -114.9) * mm, "end": v(-9.84, -115.2) * mm});
            skLineSegment(sketch, "E3002", {"start": v(-9.84, -115.2) * mm, "end": v(-9.75, -115.53) * mm});
            skLineSegment(sketch, "E3003", {"start": v(-9.75, -115.53) * mm, "end": v(-9.64, -115.86) * mm});
            skLineSegment(sketch, "E3004", {"start": v(-9.64, -115.86) * mm, "end": v(-9.54, -116.19) * mm});
            skLineSegment(sketch, "E3005", {"start": v(-9.54, -116.19) * mm, "end": v(-9.42, -116.52) * mm});
            skLineSegment(sketch, "E3006", {"start": v(-9.42, -116.52) * mm, "end": v(-9.3, -116.86) * mm});
            skLineSegment(sketch, "E3007", {"start": v(-9.3, -116.86) * mm, "end": v(-9.19, -117.2) * mm});
            skLineSegment(sketch, "E3008", {"start": v(-9.19, -117.2) * mm, "end": v(-9.06, -117.56) * mm});
            skLineSegment(sketch, "E3009", {"start": v(-9.06, -117.56) * mm, "end": v(-8.93, -117.92) * mm});
            skLineSegment(sketch, "E3010", {"start": v(-8.93, -117.92) * mm, "end": v(-8.8, -118.28) * mm});
            skLineSegment(sketch, "E3011", {"start": v(-8.8, -118.28) * mm, "end": v(-8.66, -118.65) * mm});
            skLineSegment(sketch, "E3012", {"start": v(-8.66, -118.65) * mm, "end": v(-8.51, -119.02) * mm});
            skLineSegment(sketch, "E3013", {"start": v(-8.51, -119.02) * mm, "end": v(-8.34, -119.14) * mm});
            skLineSegment(sketch, "E3014", {"start": v(-8.34, -119.14) * mm, "end": v(-4.84, -119.33) * mm});
            skLineSegment(sketch, "E3015", {"start": v(-4.84, -119.33) * mm, "end": v(-4.65, -119.23) * mm});
            skLineSegment(sketch, "E3016", {"start": v(-4.65, -119.23) * mm, "end": v(-4.47, -118.88) * mm});
            skLineSegment(sketch, "E3017", {"start": v(-4.47, -118.88) * mm, "end": v(-4.29, -118.53) * mm});
            skLineSegment(sketch, "E3018", {"start": v(-4.29, -118.53) * mm, "end": v(-4.11, -118.18) * mm});
            skLineSegment(sketch, "E3019", {"start": v(-4.11, -118.18) * mm, "end": v(-3.94, -117.85) * mm});
            skLineSegment(sketch, "E3020", {"start": v(-3.94, -117.85) * mm, "end": v(-3.78, -117.51) * mm});
            skLineSegment(sketch, "E3021", {"start": v(-3.78, -117.51) * mm, "end": v(-3.62, -117.18) * mm});
            skLineSegment(sketch, "E3022", {"start": v(-3.62, -117.18) * mm, "end": v(-3.47, -116.85) * mm});
            skLineSegment(sketch, "E3023", {"start": v(-3.47, -116.85) * mm, "end": v(-3.32, -116.53) * mm});
            skLineSegment(sketch, "E3024", {"start": v(-3.32, -116.53) * mm, "end": v(-3.18, -116.21) * mm});
            skLineSegment(sketch, "E3025", {"start": v(-3.18, -116.21) * mm, "end": v(-3.04, -115.9) * mm});
            skLineSegment(sketch, "E3026", {"start": v(-3.04, -115.9) * mm, "end": v(-2.9, -115.6) * mm});
            skLineSegment(sketch, "E3027", {"start": v(-2.9, -115.6) * mm, "end": v(-2.78, -115.3) * mm});
            skLineSegment(sketch, "E3028", {"start": v(-2.78, -115.3) * mm, "end": v(-2.66, -115) * mm});
            skLineSegment(sketch, "E3029", {"start": v(-2.66, -115) * mm, "end": v(-2.54, -114.7) * mm});
            skLineSegment(sketch, "E3030", {"start": v(-2.54, -114.7) * mm, "end": v(-2.43, -114.42) * mm});
            skLineSegment(sketch, "E3031", {"start": v(-2.43, -114.42) * mm, "end": v(-2.32, -114.14) * mm});
            skLineSegment(sketch, "E3032", {"start": v(-2.32, -114.14) * mm, "end": v(-2.21, -113.86) * mm});
            skLineSegment(sketch, "E3033", {"start": v(-2.21, -113.86) * mm, "end": v(-2.11, -113.59) * mm});
            skLineSegment(sketch, "E3034", {"start": v(-2.11, -113.59) * mm, "end": v(-2.02, -113.32) * mm});
            skLineSegment(sketch, "E3035", {"start": v(-2.02, -113.32) * mm, "end": v(-1.92, -113.06) * mm});
            skLineSegment(sketch, "E3036", {"start": v(-1.92, -113.06) * mm, "end": v(-1.84, -112.8) * mm});
            skLineSegment(sketch, "E3037", {"start": v(-1.84, -112.8) * mm, "end": v(-1.75, -112.56) * mm});
            skLineSegment(sketch, "E3038", {"start": v(-1.75, -112.56) * mm, "end": v(-1.67, -112.31) * mm});
            skLineSegment(sketch, "E3039", {"start": v(-1.67, -112.31) * mm, "end": v(-1.6, -112.07) * mm});
            skLineSegment(sketch, "E3040", {"start": v(-1.6, -112.07) * mm, "end": v(-1.53, -111.84) * mm});
            skLineSegment(sketch, "E3041", {"start": v(-1.53, -111.84) * mm, "end": v(-1.46, -111.61) * mm});
            skLineSegment(sketch, "E3042", {"start": v(-1.46, -111.61) * mm, "end": v(-1.4, -111.4) * mm});
            skLineSegment(sketch, "E3043", {"start": v(-1.4, -111.4) * mm, "end": v(-1.33, -111.17) * mm});
            skLineSegment(sketch, "E3044", {"start": v(-1.33, -111.17) * mm, "end": v(-1.27, -110.96) * mm});
            skLineSegment(sketch, "E3045", {"start": v(-1.27, -110.96) * mm, "end": v(-1.22, -110.76) * mm});
            skLineSegment(sketch, "E3046", {"start": v(-1.22, -110.76) * mm, "end": v(-1.17, -110.56) * mm});
            skLineSegment(sketch, "E3047", {"start": v(-1.17, -110.56) * mm, "end": v(-1.12, -110.37) * mm});
            skLineSegment(sketch, "E3048", {"start": v(-1.12, -110.37) * mm, "end": v(-1.08, -110.18) * mm});
            skLineSegment(sketch, "E3049", {"start": v(-1.08, -110.18) * mm, "end": v(-1.03, -110) * mm});
            skLineSegment(sketch, "E3050", {"start": v(-1.03, -110) * mm, "end": v(-1, -109.83) * mm});
            skLineSegment(sketch, "E3051", {"start": v(-1, -109.83) * mm, "end": v(-0.96, -109.66) * mm});
            skLineSegment(sketch, "E3052", {"start": v(-0.96, -109.66) * mm, "end": v(-0.92, -109.5) * mm});
            skLineSegment(sketch, "E3053", {"start": v(-0.92, -109.5) * mm, "end": v(-0.9, -109.34) * mm});
            skLineSegment(sketch, "E3054", {"start": v(-0.9, -109.34) * mm, "end": v(-0.86, -109.19) * mm});
            skLineSegment(sketch, "E3055", {"start": v(-0.86, -109.19) * mm, "end": v(-0.84, -109.04) * mm});
            skLineSegment(sketch, "E3056", {"start": v(-0.84, -109.04) * mm, "end": v(-0.81, -108.9) * mm});
            skLineSegment(sketch, "E3057", {"start": v(-0.81, -108.9) * mm, "end": v(-0.79, -108.77) * mm});
            skLineSegment(sketch, "E3058", {"start": v(-0.79, -108.77) * mm, "end": v(-0.65, -108.5) * mm});
            skLineSegment(sketch, "E3059", {"start": v(-0.65, -108.5) * mm, "end": v(3.82, -108.44) * mm});
            skLineSegment(sketch, "E3060", {"start": v(3.82, -108.44) * mm, "end": v(3.97, -108.7) * mm});
            skLineSegment(sketch, "E3061", {"start": v(3.97, -108.7) * mm, "end": v(4, -108.83) * mm});
            skLineSegment(sketch, "E3062", {"start": v(4, -108.83) * mm, "end": v(4.02, -108.97) * mm});
            skLineSegment(sketch, "E3063", {"start": v(4.02, -108.97) * mm, "end": v(4.05, -109.12) * mm});
            skLineSegment(sketch, "E3064", {"start": v(4.05, -109.12) * mm, "end": v(4.09, -109.27) * mm});
            skLineSegment(sketch, "E3065", {"start": v(4.09, -109.27) * mm, "end": v(4.12, -109.42) * mm});
            skLineSegment(sketch, "E3066", {"start": v(4.12, -109.42) * mm, "end": v(4.16, -109.58) * mm});
            skLineSegment(sketch, "E3067", {"start": v(4.16, -109.58) * mm, "end": v(4.2, -109.75) * mm});
            skLineSegment(sketch, "E3068", {"start": v(4.2, -109.75) * mm, "end": v(4.25, -109.92) * mm});
            skLineSegment(sketch, "E3069", {"start": v(4.25, -109.92) * mm, "end": v(4.3, -110.1) * mm});
            skLineSegment(sketch, "E3070", {"start": v(4.3, -110.1) * mm, "end": v(4.34, -110.29) * mm});
            skLineSegment(sketch, "E3071", {"start": v(4.34, -110.29) * mm, "end": v(4.4, -110.48) * mm});
            skLineSegment(sketch, "E3072", {"start": v(4.4, -110.48) * mm, "end": v(4.45, -110.68) * mm});
            skLineSegment(sketch, "E3073", {"start": v(4.45, -110.68) * mm, "end": v(4.52, -110.88) * mm});
            skLineSegment(sketch, "E3074", {"start": v(4.52, -110.88) * mm, "end": v(4.58, -111.09) * mm});
            skLineSegment(sketch, "E3075", {"start": v(4.58, -111.09) * mm, "end": v(4.65, -111.3) * mm});
            skLineSegment(sketch, "E3076", {"start": v(4.65, -111.3) * mm, "end": v(4.72, -111.52) * mm});
            skLineSegment(sketch, "E3077", {"start": v(4.72, -111.52) * mm, "end": v(4.8, -111.75) * mm});
            skLineSegment(sketch, "E3078", {"start": v(4.8, -111.75) * mm, "end": v(4.87, -111.98) * mm});
            skLineSegment(sketch, "E3079", {"start": v(4.87, -111.98) * mm, "end": v(4.95, -112.22) * mm});
            skLineSegment(sketch, "E3080", {"start": v(4.95, -112.22) * mm, "end": v(5.04, -112.46) * mm});
            skLineSegment(sketch, "E3081", {"start": v(5.04, -112.46) * mm, "end": v(5.13, -112.7) * mm});
            skLineSegment(sketch, "E3082", {"start": v(5.13, -112.7) * mm, "end": v(5.23, -112.96) * mm});
            skLineSegment(sketch, "E3083", {"start": v(5.23, -112.96) * mm, "end": v(5.32, -113.22) * mm});
            skLineSegment(sketch, "E3084", {"start": v(5.32, -113.22) * mm, "end": v(5.43, -113.48) * mm});
            skLineSegment(sketch, "E3085", {"start": v(5.43, -113.48) * mm, "end": v(5.54, -113.75) * mm});
            skLineSegment(sketch, "E3086", {"start": v(5.54, -113.75) * mm, "end": v(5.65, -114.02) * mm});
            skLineSegment(sketch, "E3087", {"start": v(5.65, -114.02) * mm, "end": v(5.76, -114.3) * mm});
            skLineSegment(sketch, "E3088", {"start": v(5.76, -114.3) * mm, "end": v(5.89, -114.58) * mm});
            skLineSegment(sketch, "E3089", {"start": v(5.89, -114.58) * mm, "end": v(6.01, -114.87) * mm});
            skLineSegment(sketch, "E3090", {"start": v(6.01, -114.87) * mm, "end": v(6.14, -115.17) * mm});
            skLineSegment(sketch, "E3091", {"start": v(6.14, -115.17) * mm, "end": v(6.28, -115.46) * mm});
            skLineSegment(sketch, "E3092", {"start": v(6.28, -115.46) * mm, "end": v(6.42, -115.77) * mm});
            skLineSegment(sketch, "E3093", {"start": v(6.42, -115.77) * mm, "end": v(6.57, -116.07) * mm});
            skLineSegment(sketch, "E3094", {"start": v(6.57, -116.07) * mm, "end": v(6.72, -116.39) * mm});
            skLineSegment(sketch, "E3095", {"start": v(6.72, -116.39) * mm, "end": v(6.88, -116.7) * mm});
            skLineSegment(sketch, "E3096", {"start": v(6.88, -116.7) * mm, "end": v(7.04, -117.03) * mm});
            skLineSegment(sketch, "E3097", {"start": v(7.04, -117.03) * mm, "end": v(7.2, -117.35) * mm});
            skLineSegment(sketch, "E3098", {"start": v(7.2, -117.35) * mm, "end": v(7.38, -117.68) * mm});
            skLineSegment(sketch, "E3099", {"start": v(7.38, -117.68) * mm, "end": v(7.56, -118.02) * mm});
            skLineSegment(sketch, "E3100", {"start": v(7.56, -118.02) * mm, "end": v(7.74, -118.36) * mm});
            skLineSegment(sketch, "E3101", {"start": v(7.74, -118.36) * mm, "end": v(7.93, -118.7) * mm});
            skLineSegment(sketch, "E3102", {"start": v(7.93, -118.7) * mm, "end": v(8.13, -119.05) * mm});
            skLineSegment(sketch, "E3103", {"start": v(8.13, -119.05) * mm, "end": v(8.31, -119.14) * mm});
            skLineSegment(sketch, "E3104", {"start": v(8.31, -119.14) * mm, "end": v(11.81, -118.85) * mm});
            skLineSegment(sketch, "E3105", {"start": v(11.81, -118.85) * mm, "end": v(11.98, -118.72) * mm});
            skLineSegment(sketch, "E3106", {"start": v(11.98, -118.72) * mm, "end": v(12.11, -118.35) * mm});
            skLineSegment(sketch, "E3107", {"start": v(12.11, -118.35) * mm, "end": v(12.24, -117.98) * mm});
            skLineSegment(sketch, "E3108", {"start": v(12.24, -117.98) * mm, "end": v(12.37, -117.61) * mm});
            skLineSegment(sketch, "E3109", {"start": v(12.37, -117.61) * mm, "end": v(12.49, -117.25) * mm});
            skLineSegment(sketch, "E3110", {"start": v(12.49, -117.25) * mm, "end": v(12.6, -116.9) * mm});
            skLineSegment(sketch, "E3111", {"start": v(12.6, -116.9) * mm, "end": v(12.72, -116.55) * mm});
            skLineSegment(sketch, "E3112", {"start": v(12.72, -116.55) * mm, "end": v(12.82, -116.2) * mm});
            skLineSegment(sketch, "E3113", {"start": v(12.82, -116.2) * mm, "end": v(12.92, -115.86) * mm});
            skLineSegment(sketch, "E3114", {"start": v(12.92, -115.86) * mm, "end": v(13.02, -115.53) * mm});
            skLineSegment(sketch, "E3115", {"start": v(13.02, -115.53) * mm, "end": v(13.11, -115.2) * mm});
            skLineSegment(sketch, "E3116", {"start": v(13.11, -115.2) * mm, "end": v(13.2, -114.88) * mm});
            skLineSegment(sketch, "E3117", {"start": v(13.2, -114.88) * mm, "end": v(13.29, -114.56) * mm});
            skLineSegment(sketch, "E3118", {"start": v(13.29, -114.56) * mm, "end": v(13.37, -114.25) * mm});
            skLineSegment(sketch, "E3119", {"start": v(13.37, -114.25) * mm, "end": v(13.44, -113.95) * mm});
            skLineSegment(sketch, "E3120", {"start": v(13.44, -113.95) * mm, "end": v(13.52, -113.65) * mm});
            skLineSegment(sketch, "E3121", {"start": v(13.52, -113.65) * mm, "end": v(13.58, -113.35) * mm});
            skLineSegment(sketch, "E3122", {"start": v(13.58, -113.35) * mm, "end": v(13.65, -113.06) * mm});
            skLineSegment(sketch, "E3123", {"start": v(13.65, -113.06) * mm, "end": v(13.71, -112.78) * mm});
            skLineSegment(sketch, "E3124", {"start": v(13.71, -112.78) * mm, "end": v(13.77, -112.5) * mm});
            skLineSegment(sketch, "E3125", {"start": v(13.77, -112.5) * mm, "end": v(13.82, -112.23) * mm});
            skLineSegment(sketch, "E3126", {"start": v(13.82, -112.23) * mm, "end": v(13.87, -111.97) * mm});
            skLineSegment(sketch, "E3127", {"start": v(13.87, -111.97) * mm, "end": v(13.92, -111.7) * mm});
            skLineSegment(sketch, "E3128", {"start": v(13.92, -111.7) * mm, "end": v(13.97, -111.46) * mm});
            skLineSegment(sketch, "E3129", {"start": v(13.97, -111.46) * mm, "end": v(14, -111.2) * mm});
            skLineSegment(sketch, "E3130", {"start": v(14, -111.2) * mm, "end": v(14.05, -110.97) * mm});
            skLineSegment(sketch, "E3131", {"start": v(14.05, -110.97) * mm, "end": v(14.08, -110.73) * mm});
            skLineSegment(sketch, "E3132", {"start": v(14.08, -110.73) * mm, "end": v(14.12, -110.5) * mm});
            skLineSegment(sketch, "E3133", {"start": v(14.12, -110.5) * mm, "end": v(14.15, -110.28) * mm});
            skLineSegment(sketch, "E3134", {"start": v(14.15, -110.28) * mm, "end": v(14.17, -110.07) * mm});
            skLineSegment(sketch, "E3135", {"start": v(14.17, -110.07) * mm, "end": v(14.2, -109.86) * mm});
            skLineSegment(sketch, "E3136", {"start": v(14.2, -109.86) * mm, "end": v(14.22, -109.65) * mm});
            skLineSegment(sketch, "E3137", {"start": v(14.22, -109.65) * mm, "end": v(14.24, -109.45) * mm});
            skLineSegment(sketch, "E3138", {"start": v(14.24, -109.45) * mm, "end": v(14.26, -109.26) * mm});
            skLineSegment(sketch, "E3139", {"start": v(14.26, -109.26) * mm, "end": v(14.28, -109.08) * mm});
            skLineSegment(sketch, "E3140", {"start": v(14.28, -109.08) * mm, "end": v(14.3, -108.9) * mm});
            skLineSegment(sketch, "E3141", {"start": v(14.3, -108.9) * mm, "end": v(14.3, -108.73) * mm});
            skLineSegment(sketch, "E3142", {"start": v(14.3, -108.73) * mm, "end": v(14.32, -108.56) * mm});
            skLineSegment(sketch, "E3143", {"start": v(14.32, -108.56) * mm, "end": v(14.33, -108.4) * mm});
            skLineSegment(sketch, "E3144", {"start": v(14.33, -108.4) * mm, "end": v(14.34, -108.25) * mm});
            skLineSegment(sketch, "E3145", {"start": v(14.34, -108.25) * mm, "end": v(14.34, -108.1) * mm});
            skLineSegment(sketch, "E3146", {"start": v(14.34, -108.1) * mm, "end": v(14.35, -107.96) * mm});
            skLineSegment(sketch, "E3147", {"start": v(14.35, -107.96) * mm, "end": v(14.35, -107.83) * mm});
            skLineSegment(sketch, "E3148", {"start": v(14.35, -107.83) * mm, "end": v(14.45, -107.54) * mm});
            skLineSegment(sketch, "E3149", {"start": v(14.45, -107.54) * mm, "end": v(18.87, -106.86) * mm});
            skLineSegment(sketch, "E3150", {"start": v(18.87, -106.86) * mm, "end": v(19.05, -107.1) * mm});
            skLineSegment(sketch, "E3151", {"start": v(19.05, -107.1) * mm, "end": v(19.1, -107.22) * mm});
            skLineSegment(sketch, "E3152", {"start": v(19.1, -107.22) * mm, "end": v(19.14, -107.36) * mm});
            skLineSegment(sketch, "E3153", {"start": v(19.14, -107.36) * mm, "end": v(19.2, -107.5) * mm});
            skLineSegment(sketch, "E3154", {"start": v(19.2, -107.5) * mm, "end": v(19.25, -107.64) * mm});
            skLineSegment(sketch, "E3155", {"start": v(19.25, -107.64) * mm, "end": v(19.3, -107.79) * mm});
            skLineSegment(sketch, "E3156", {"start": v(19.3, -107.79) * mm, "end": v(19.36, -107.94) * mm});
            skLineSegment(sketch, "E3157", {"start": v(19.36, -107.94) * mm, "end": v(19.43, -108.1) * mm});
            skLineSegment(sketch, "E3158", {"start": v(19.43, -108.1) * mm, "end": v(19.5, -108.27) * mm});
            skLineSegment(sketch, "E3159", {"start": v(19.5, -108.27) * mm, "end": v(19.57, -108.44) * mm});
            skLineSegment(sketch, "E3160", {"start": v(19.57, -108.44) * mm, "end": v(19.65, -108.62) * mm});
            skLineSegment(sketch, "E3161", {"start": v(19.65, -108.62) * mm, "end": v(19.72, -108.8) * mm});
            skLineSegment(sketch, "E3162", {"start": v(19.72, -108.8) * mm, "end": v(19.8, -108.99) * mm});
            skLineSegment(sketch, "E3163", {"start": v(19.8, -108.99) * mm, "end": v(19.9, -109.18) * mm});
            skLineSegment(sketch, "E3164", {"start": v(19.9, -109.18) * mm, "end": v(19.99, -109.38) * mm});
            skLineSegment(sketch, "E3165", {"start": v(19.99, -109.38) * mm, "end": v(20.09, -109.58) * mm});
            skLineSegment(sketch, "E3166", {"start": v(20.09, -109.58) * mm, "end": v(20.19, -109.79) * mm});
            skLineSegment(sketch, "E3167", {"start": v(20.19, -109.79) * mm, "end": v(20.3, -110) * mm});
            skLineSegment(sketch, "E3168", {"start": v(20.3, -110) * mm, "end": v(20.4, -110.22) * mm});
            skLineSegment(sketch, "E3169", {"start": v(20.4, -110.22) * mm, "end": v(20.52, -110.44) * mm});
            skLineSegment(sketch, "E3170", {"start": v(20.52, -110.44) * mm, "end": v(20.64, -110.67) * mm});
            skLineSegment(sketch, "E3171", {"start": v(20.64, -110.67) * mm, "end": v(20.76, -110.9) * mm});
            skLineSegment(sketch, "E3172", {"start": v(20.76, -110.9) * mm, "end": v(20.89, -111.14) * mm});
            skLineSegment(sketch, "E3173", {"start": v(20.89, -111.14) * mm, "end": v(21.02, -111.38) * mm});
            skLineSegment(sketch, "E3174", {"start": v(21.02, -111.38) * mm, "end": v(21.16, -111.63) * mm});
            skLineSegment(sketch, "E3175", {"start": v(21.16, -111.63) * mm, "end": v(21.3, -111.88) * mm});
            skLineSegment(sketch, "E3176", {"start": v(21.3, -111.88) * mm, "end": v(21.45, -112.13) * mm});
            skLineSegment(sketch, "E3177", {"start": v(21.45, -112.13) * mm, "end": v(21.6, -112.4) * mm});
            skLineSegment(sketch, "E3178", {"start": v(21.6, -112.4) * mm, "end": v(21.77, -112.65) * mm});
            skLineSegment(sketch, "E3179", {"start": v(21.77, -112.65) * mm, "end": v(21.93, -112.92) * mm});
            skLineSegment(sketch, "E3180", {"start": v(21.93, -112.92) * mm, "end": v(22.1, -113.2) * mm});
            skLineSegment(sketch, "E3181", {"start": v(22.1, -113.2) * mm, "end": v(22.28, -113.47) * mm});
            skLineSegment(sketch, "E3182", {"start": v(22.28, -113.47) * mm, "end": v(22.46, -113.75) * mm});
            skLineSegment(sketch, "E3183", {"start": v(22.46, -113.75) * mm, "end": v(22.65, -114.04) * mm});
            skLineSegment(sketch, "E3184", {"start": v(22.65, -114.04) * mm, "end": v(22.85, -114.32) * mm});
            skLineSegment(sketch, "E3185", {"start": v(22.85, -114.32) * mm, "end": v(23.05, -114.62) * mm});
            skLineSegment(sketch, "E3186", {"start": v(23.05, -114.62) * mm, "end": v(23.25, -114.91) * mm});
            skLineSegment(sketch, "E3187", {"start": v(23.25, -114.91) * mm, "end": v(23.46, -115.21) * mm});
            skLineSegment(sketch, "E3188", {"start": v(23.46, -115.21) * mm, "end": v(23.68, -115.52) * mm});
            skLineSegment(sketch, "E3189", {"start": v(23.68, -115.52) * mm, "end": v(23.9, -115.82) * mm});
            skLineSegment(sketch, "E3190", {"start": v(23.9, -115.82) * mm, "end": v(24.13, -116.13) * mm});
            skLineSegment(sketch, "E3191", {"start": v(24.13, -116.13) * mm, "end": v(24.37, -116.45) * mm});
            skLineSegment(sketch, "E3192", {"start": v(24.37, -116.45) * mm, "end": v(24.61, -116.76) * mm});
            skLineSegment(sketch, "E3193", {"start": v(24.61, -116.76) * mm, "end": v(24.8, -116.83) * mm});
            skLineSegment(sketch, "E3194", {"start": v(24.8, -116.83) * mm, "end": v(28.23, -116.05) * mm});
            skLineSegment(sketch, "E3195", {"start": v(28.23, -116.05) * mm, "end": v(28.38, -115.9) * mm});
            skLineSegment(sketch, "E3196", {"start": v(28.38, -115.9) * mm, "end": v(28.46, -115.52) * mm});
            skLineSegment(sketch, "E3197", {"start": v(28.46, -115.52) * mm, "end": v(28.54, -115.13) * mm});
            skLineSegment(sketch, "E3198", {"start": v(28.54, -115.13) * mm, "end": v(28.61, -114.75) * mm});
            skLineSegment(sketch, "E3199", {"start": v(28.61, -114.75) * mm, "end": v(28.68, -114.38) * mm});
            skLineSegment(sketch, "E3200", {"start": v(28.68, -114.38) * mm, "end": v(28.74, -114.01) * mm});
            skLineSegment(sketch, "E3201", {"start": v(28.74, -114.01) * mm, "end": v(28.8, -113.65) * mm});
            skLineSegment(sketch, "E3202", {"start": v(28.8, -113.65) * mm, "end": v(28.86, -113.3) * mm});
            skLineSegment(sketch, "E3203", {"start": v(28.86, -113.3) * mm, "end": v(28.92, -112.94) * mm});
            skLineSegment(sketch, "E3204", {"start": v(28.92, -112.94) * mm, "end": v(28.97, -112.6) * mm});
            skLineSegment(sketch, "E3205", {"start": v(28.97, -112.6) * mm, "end": v(29.01, -112.26) * mm});
            skLineSegment(sketch, "E3206", {"start": v(29.01, -112.26) * mm, "end": v(29.05, -111.93) * mm});
            skLineSegment(sketch, "E3207", {"start": v(29.05, -111.93) * mm, "end": v(29.1, -111.6) * mm});
            skLineSegment(sketch, "E3208", {"start": v(29.1, -111.6) * mm, "end": v(29.13, -111.28) * mm});
            skLineSegment(sketch, "E3209", {"start": v(29.13, -111.28) * mm, "end": v(29.16, -110.97) * mm});
            skLineSegment(sketch, "E3210", {"start": v(29.16, -110.97) * mm, "end": v(29.2, -110.66) * mm});
            skLineSegment(sketch, "E3211", {"start": v(29.2, -110.66) * mm, "end": v(29.22, -110.36) * mm});
            skLineSegment(sketch, "E3212", {"start": v(29.22, -110.36) * mm, "end": v(29.25, -110.07) * mm});
            skLineSegment(sketch, "E3213", {"start": v(29.25, -110.07) * mm, "end": v(29.27, -109.78) * mm});
            skLineSegment(sketch, "E3214", {"start": v(29.27, -109.78) * mm, "end": v(29.29, -109.5) * mm});
            skLineSegment(sketch, "E3215", {"start": v(29.29, -109.5) * mm, "end": v(29.3, -109.22) * mm});
            skLineSegment(sketch, "E3216", {"start": v(29.3, -109.22) * mm, "end": v(29.32, -108.95) * mm});
            skLineSegment(sketch, "E3217", {"start": v(29.32, -108.95) * mm, "end": v(29.33, -108.7) * mm});
            skLineSegment(sketch, "E3218", {"start": v(29.33, -108.7) * mm, "end": v(29.34, -108.43) * mm});
            skLineSegment(sketch, "E3219", {"start": v(29.34, -108.43) * mm, "end": v(29.34, -108.18) * mm});
            skLineSegment(sketch, "E3220", {"start": v(29.34, -108.18) * mm, "end": v(29.35, -107.94) * mm});
            skLineSegment(sketch, "E3221", {"start": v(29.35, -107.94) * mm, "end": v(29.35, -107.7) * mm});
            skLineSegment(sketch, "E3222", {"start": v(29.35, -107.7) * mm, "end": v(29.35, -107.47) * mm});
            skLineSegment(sketch, "E3223", {"start": v(29.35, -107.47) * mm, "end": v(29.35, -107.25) * mm});
            skLineSegment(sketch, "E3224", {"start": v(29.35, -107.25) * mm, "end": v(29.35, -107.03) * mm});
            skLineSegment(sketch, "E3225", {"start": v(29.35, -107.03) * mm, "end": v(29.34, -106.82) * mm});
            skLineSegment(sketch, "E3226", {"start": v(29.34, -106.82) * mm, "end": v(29.34, -106.61) * mm});
            skLineSegment(sketch, "E3227", {"start": v(29.34, -106.61) * mm, "end": v(29.33, -106.41) * mm});
            skLineSegment(sketch, "E3228", {"start": v(29.33, -106.41) * mm, "end": v(29.32, -106.22) * mm});
            skLineSegment(sketch, "E3229", {"start": v(29.32, -106.22) * mm, "end": v(29.31, -106.03) * mm});
            skLineSegment(sketch, "E3230", {"start": v(29.31, -106.03) * mm, "end": v(29.3, -105.86) * mm});
            skLineSegment(sketch, "E3231", {"start": v(29.3, -105.86) * mm, "end": v(29.3, -105.68) * mm});
            skLineSegment(sketch, "E3232", {"start": v(29.3, -105.68) * mm, "end": v(29.28, -105.52) * mm});
            skLineSegment(sketch, "E3233", {"start": v(29.28, -105.52) * mm, "end": v(29.27, -105.36) * mm});
            skLineSegment(sketch, "E3234", {"start": v(29.27, -105.36) * mm, "end": v(29.25, -105.2) * mm});
            skLineSegment(sketch, "E3235", {"start": v(29.25, -105.2) * mm, "end": v(29.24, -105.06) * mm});
            skLineSegment(sketch, "E3236", {"start": v(29.24, -105.06) * mm, "end": v(29.23, -104.92) * mm});
            skLineSegment(sketch, "E3237", {"start": v(29.23, -104.92) * mm, "end": v(29.21, -104.79) * mm});
            skLineSegment(sketch, "E3238", {"start": v(29.21, -104.79) * mm, "end": v(29.27, -104.5) * mm});
            skLineSegment(sketch, "E3239", {"start": v(29.27, -104.5) * mm, "end": v(33.55, -103.2) * mm});
            skLineSegment(sketch, "E3240", {"start": v(33.55, -103.2) * mm, "end": v(33.76, -103.4) * mm});
            skLineSegment(sketch, "E3241", {"start": v(33.76, -103.4) * mm, "end": v(33.82, -103.53) * mm});
            skLineSegment(sketch, "E3242", {"start": v(33.82, -103.53) * mm, "end": v(33.9, -103.65) * mm});
            skLineSegment(sketch, "E3243", {"start": v(33.9, -103.65) * mm, "end": v(33.96, -103.78) * mm});
            skLineSegment(sketch, "E3244", {"start": v(33.96, -103.78) * mm, "end": v(34.03, -103.92) * mm});
            skLineSegment(sketch, "E3245", {"start": v(34.03, -103.92) * mm, "end": v(34.11, -104.06) * mm});
            skLineSegment(sketch, "E3246", {"start": v(34.11, -104.06) * mm, "end": v(34.2, -104.2) * mm});
            skLineSegment(sketch, "E3247", {"start": v(34.2, -104.2) * mm, "end": v(34.28, -104.35) * mm});
            skLineSegment(sketch, "E3248", {"start": v(34.28, -104.35) * mm, "end": v(34.37, -104.5) * mm});
            skLineSegment(sketch, "E3249", {"start": v(34.37, -104.5) * mm, "end": v(34.46, -104.67) * mm});
            skLineSegment(sketch, "E3250", {"start": v(34.46, -104.67) * mm, "end": v(34.56, -104.83) * mm});
            skLineSegment(sketch, "E3251", {"start": v(34.56, -104.83) * mm, "end": v(34.67, -105) * mm});
            skLineSegment(sketch, "E3252", {"start": v(34.67, -105) * mm, "end": v(34.78, -105.17) * mm});
            skLineSegment(sketch, "E3253", {"start": v(34.78, -105.17) * mm, "end": v(34.9, -105.35) * mm});
            skLineSegment(sketch, "E3254", {"start": v(34.9, -105.35) * mm, "end": v(35, -105.53) * mm});
            skLineSegment(sketch, "E3255", {"start": v(35, -105.53) * mm, "end": v(35.13, -105.72) * mm});
            skLineSegment(sketch, "E3256", {"start": v(35.13, -105.72) * mm, "end": v(35.26, -105.91) * mm});
            skLineSegment(sketch, "E3257", {"start": v(35.26, -105.91) * mm, "end": v(35.4, -106.11) * mm});
            skLineSegment(sketch, "E3258", {"start": v(35.4, -106.11) * mm, "end": v(35.54, -106.31) * mm});
            skLineSegment(sketch, "E3259", {"start": v(35.54, -106.31) * mm, "end": v(35.68, -106.52) * mm});
            skLineSegment(sketch, "E3260", {"start": v(35.68, -106.52) * mm, "end": v(35.83, -106.72) * mm});
            skLineSegment(sketch, "E3261", {"start": v(35.83, -106.72) * mm, "end": v(35.98, -106.94) * mm});
            skLineSegment(sketch, "E3262", {"start": v(35.98, -106.94) * mm, "end": v(36.15, -107.15) * mm});
            skLineSegment(sketch, "E3263", {"start": v(36.15, -107.15) * mm, "end": v(36.31, -107.37) * mm});
            skLineSegment(sketch, "E3264", {"start": v(36.31, -107.37) * mm, "end": v(36.48, -107.6) * mm});
            skLineSegment(sketch, "E3265", {"start": v(36.48, -107.6) * mm, "end": v(36.66, -107.83) * mm});
            skLineSegment(sketch, "E3266", {"start": v(36.66, -107.83) * mm, "end": v(36.84, -108.06) * mm});
            skLineSegment(sketch, "E3267", {"start": v(36.84, -108.06) * mm, "end": v(37.03, -108.3) * mm});
            skLineSegment(sketch, "E3268", {"start": v(37.03, -108.3) * mm, "end": v(37.23, -108.53) * mm});
            skLineSegment(sketch, "E3269", {"start": v(37.23, -108.53) * mm, "end": v(37.43, -108.78) * mm});
            skLineSegment(sketch, "E3270", {"start": v(37.43, -108.78) * mm, "end": v(37.64, -109.02) * mm});
            skLineSegment(sketch, "E3271", {"start": v(37.64, -109.02) * mm, "end": v(37.85, -109.27) * mm});
            skLineSegment(sketch, "E3272", {"start": v(37.85, -109.27) * mm, "end": v(38.07, -109.52) * mm});
            skLineSegment(sketch, "E3273", {"start": v(38.07, -109.52) * mm, "end": v(38.3, -109.78) * mm});
            skLineSegment(sketch, "E3274", {"start": v(38.3, -109.78) * mm, "end": v(38.53, -110.04) * mm});
            skLineSegment(sketch, "E3275", {"start": v(38.53, -110.04) * mm, "end": v(38.77, -110.3) * mm});
            skLineSegment(sketch, "E3276", {"start": v(38.77, -110.3) * mm, "end": v(39.01, -110.56) * mm});
            skLineSegment(sketch, "E3277", {"start": v(39.01, -110.56) * mm, "end": v(39.26, -110.83) * mm});
            skLineSegment(sketch, "E3278", {"start": v(39.26, -110.83) * mm, "end": v(39.52, -111.1) * mm});
            skLineSegment(sketch, "E3279", {"start": v(39.52, -111.1) * mm, "end": v(39.78, -111.37) * mm});
            skLineSegment(sketch, "E3280", {"start": v(39.78, -111.37) * mm, "end": v(40.06, -111.65) * mm});
            skLineSegment(sketch, "E3281", {"start": v(40.06, -111.65) * mm, "end": v(40.33, -111.93) * mm});
            skLineSegment(sketch, "E3282", {"start": v(40.33, -111.93) * mm, "end": v(40.62, -112.2) * mm});
            skLineSegment(sketch, "E3283", {"start": v(40.62, -112.2) * mm, "end": v(40.82, -112.25) * mm});
            skLineSegment(sketch, "E3284", {"start": v(40.82, -112.25) * mm, "end": v(44.1, -111) * mm});
            skLineSegment(sketch, "E3285", {"start": v(44.1, -111) * mm, "end": v(44.23, -110.83) * mm});
            skLineSegment(sketch, "E3286", {"start": v(44.23, -110.83) * mm, "end": v(44.25, -110.44) * mm});
            skLineSegment(sketch, "E3287", {"start": v(44.25, -110.44) * mm, "end": v(44.28, -110.04) * mm});
            skLineSegment(sketch, "E3288", {"start": v(44.28, -110.04) * mm, "end": v(44.3, -109.66) * mm});
            skLineSegment(sketch, "E3289", {"start": v(44.3, -109.66) * mm, "end": v(44.31, -109.28) * mm});
            skLineSegment(sketch, "E3290", {"start": v(44.31, -109.28) * mm, "end": v(44.32, -108.9) * mm});
            skLineSegment(sketch, "E3291", {"start": v(44.32, -108.9) * mm, "end": v(44.34, -108.54) * mm});
            skLineSegment(sketch, "E3292", {"start": v(44.34, -108.54) * mm, "end": v(44.34, -108.18) * mm});
            skLineSegment(sketch, "E3293", {"start": v(44.34, -108.18) * mm, "end": v(44.35, -107.83) * mm});
            skLineSegment(sketch, "E3294", {"start": v(44.35, -107.83) * mm, "end": v(44.35, -107.48) * mm});
            skLineSegment(sketch, "E3295", {"start": v(44.35, -107.48) * mm, "end": v(44.35, -107.14) * mm});
            skLineSegment(sketch, "E3296", {"start": v(44.35, -107.14) * mm, "end": v(44.34, -106.8) * mm});
            skLineSegment(sketch, "E3297", {"start": v(44.34, -106.8) * mm, "end": v(44.34, -106.47) * mm});
            skLineSegment(sketch, "E3298", {"start": v(44.34, -106.47) * mm, "end": v(44.33, -106.15) * mm});
            skLineSegment(sketch, "E3299", {"start": v(44.33, -106.15) * mm, "end": v(44.32, -105.84) * mm});
            skLineSegment(sketch, "E3300", {"start": v(44.32, -105.84) * mm, "end": v(44.3, -105.53) * mm});
            skLineSegment(sketch, "E3301", {"start": v(44.3, -105.53) * mm, "end": v(44.29, -105.23) * mm});
            skLineSegment(sketch, "E3302", {"start": v(44.29, -105.23) * mm, "end": v(44.27, -104.93) * mm});
            skLineSegment(sketch, "E3303", {"start": v(44.27, -104.93) * mm, "end": v(44.25, -104.64) * mm});
            skLineSegment(sketch, "E3304", {"start": v(44.25, -104.64) * mm, "end": v(44.23, -104.36) * mm});
            skLineSegment(sketch, "E3305", {"start": v(44.23, -104.36) * mm, "end": v(44.21, -104.09) * mm});
            skLineSegment(sketch, "E3306", {"start": v(44.21, -104.09) * mm, "end": v(44.19, -103.82) * mm});
            skLineSegment(sketch, "E3307", {"start": v(44.19, -103.82) * mm, "end": v(44.16, -103.56) * mm});
            skLineSegment(sketch, "E3308", {"start": v(44.16, -103.56) * mm, "end": v(44.14, -103.3) * mm});
            skLineSegment(sketch, "E3309", {"start": v(44.14, -103.3) * mm, "end": v(44.1, -103.05) * mm});
            skLineSegment(sketch, "E3310", {"start": v(44.1, -103.05) * mm, "end": v(44.08, -102.8) * mm});
            skLineSegment(sketch, "E3311", {"start": v(44.08, -102.8) * mm, "end": v(44.05, -102.57) * mm});
            skLineSegment(sketch, "E3312", {"start": v(44.05, -102.57) * mm, "end": v(44.02, -102.34) * mm});
            skLineSegment(sketch, "E3313", {"start": v(44.02, -102.34) * mm, "end": v(43.98, -102.12) * mm});
            skLineSegment(sketch, "E3314", {"start": v(43.98, -102.12) * mm, "end": v(43.95, -101.9) * mm});
            skLineSegment(sketch, "E3315", {"start": v(43.95, -101.9) * mm, "end": v(43.92, -101.7) * mm});
            skLineSegment(sketch, "E3316", {"start": v(43.92, -101.7) * mm, "end": v(43.88, -101.5) * mm});
            skLineSegment(sketch, "E3317", {"start": v(43.88, -101.5) * mm, "end": v(43.85, -101.3) * mm});
            skLineSegment(sketch, "E3318", {"start": v(43.85, -101.3) * mm, "end": v(43.82, -101.11) * mm});
            skLineSegment(sketch, "E3319", {"start": v(43.82, -101.11) * mm, "end": v(43.78, -100.93) * mm});
            skLineSegment(sketch, "E3320", {"start": v(43.78, -100.93) * mm, "end": v(43.75, -100.75) * mm});
            skLineSegment(sketch, "E3321", {"start": v(43.75, -100.75) * mm, "end": v(43.71, -100.58) * mm});
            skLineSegment(sketch, "E3322", {"start": v(43.71, -100.58) * mm, "end": v(43.67, -100.42) * mm});
            skLineSegment(sketch, "E3323", {"start": v(43.67, -100.42) * mm, "end": v(43.64, -100.26) * mm});
            skLineSegment(sketch, "E3324", {"start": v(43.64, -100.26) * mm, "end": v(43.6, -100.12) * mm});
            skLineSegment(sketch, "E3325", {"start": v(43.6, -100.12) * mm, "end": v(43.57, -99.97) * mm});
            skLineSegment(sketch, "E3326", {"start": v(43.57, -99.97) * mm, "end": v(43.54, -99.84) * mm});
            skLineSegment(sketch, "E3327", {"start": v(43.54, -99.84) * mm, "end": v(43.5, -99.7) * mm});
            skLineSegment(sketch, "E3328", {"start": v(43.5, -99.7) * mm, "end": v(43.52, -99.4) * mm});
            skLineSegment(sketch, "E3329", {"start": v(43.52, -99.4) * mm, "end": v(47.58, -97.53) * mm});
            skLineSegment(sketch, "E3330", {"start": v(47.58, -97.53) * mm, "end": v(47.82, -97.7) * mm});
            skLineSegment(sketch, "E3331", {"start": v(47.82, -97.7) * mm, "end": v(47.9, -97.82) * mm});
            skLineSegment(sketch, "E3332", {"start": v(47.9, -97.82) * mm, "end": v(47.98, -97.93) * mm});
            skLineSegment(sketch, "E3333", {"start": v(47.98, -97.93) * mm, "end": v(48.07, -98.05) * mm});
            skLineSegment(sketch, "E3334", {"start": v(48.07, -98.05) * mm, "end": v(48.16, -98.17) * mm});
            skLineSegment(sketch, "E3335", {"start": v(48.16, -98.17) * mm, "end": v(48.25, -98.3) * mm});
            skLineSegment(sketch, "E3336", {"start": v(48.25, -98.3) * mm, "end": v(48.36, -98.43) * mm});
            skLineSegment(sketch, "E3337", {"start": v(48.36, -98.43) * mm, "end": v(48.46, -98.57) * mm});
            skLineSegment(sketch, "E3338", {"start": v(48.46, -98.57) * mm, "end": v(48.57, -98.71) * mm});
            skLineSegment(sketch, "E3339", {"start": v(48.57, -98.71) * mm, "end": v(48.69, -98.86) * mm});
            skLineSegment(sketch, "E3340", {"start": v(48.69, -98.86) * mm, "end": v(48.81, -99) * mm});
            skLineSegment(sketch, "E3341", {"start": v(48.81, -99) * mm, "end": v(48.94, -99.16) * mm});
            skLineSegment(sketch, "E3342", {"start": v(48.94, -99.16) * mm, "end": v(49.07, -99.32) * mm});
            skLineSegment(sketch, "E3343", {"start": v(49.07, -99.32) * mm, "end": v(49.2, -99.48) * mm});
            skLineSegment(sketch, "E3344", {"start": v(49.2, -99.48) * mm, "end": v(49.35, -99.64) * mm});
            skLineSegment(sketch, "E3345", {"start": v(49.35, -99.64) * mm, "end": v(49.5, -99.8) * mm});
            skLineSegment(sketch, "E3346", {"start": v(49.5, -99.8) * mm, "end": v(49.65, -99.98) * mm});
            skLineSegment(sketch, "E3347", {"start": v(49.65, -99.98) * mm, "end": v(49.81, -100.16) * mm});
            skLineSegment(sketch, "E3348", {"start": v(49.81, -100.16) * mm, "end": v(49.98, -100.34) * mm});
            skLineSegment(sketch, "E3349", {"start": v(49.98, -100.34) * mm, "end": v(50.15, -100.52) * mm});
            skLineSegment(sketch, "E3350", {"start": v(50.15, -100.52) * mm, "end": v(50.33, -100.7) * mm});
            skLineSegment(sketch, "E3351", {"start": v(50.33, -100.7) * mm, "end": v(50.51, -100.9) * mm});
            skLineSegment(sketch, "E3352", {"start": v(50.51, -100.9) * mm, "end": v(50.7, -101.09) * mm});
            skLineSegment(sketch, "E3353", {"start": v(50.7, -101.09) * mm, "end": v(50.9, -101.28) * mm});
            skLineSegment(sketch, "E3354", {"start": v(50.9, -101.28) * mm, "end": v(51.1, -101.48) * mm});
            skLineSegment(sketch, "E3355", {"start": v(51.1, -101.48) * mm, "end": v(51.3, -101.68) * mm});
            skLineSegment(sketch, "E3356", {"start": v(51.3, -101.68) * mm, "end": v(51.52, -101.89) * mm});
            skLineSegment(sketch, "E3357", {"start": v(51.52, -101.89) * mm, "end": v(51.74, -102.1) * mm});
            skLineSegment(sketch, "E3358", {"start": v(51.74, -102.1) * mm, "end": v(51.97, -102.3) * mm});
            skLineSegment(sketch, "E3359", {"start": v(51.97, -102.3) * mm, "end": v(52.2, -102.51) * mm});
            skLineSegment(sketch, "E3360", {"start": v(52.2, -102.51) * mm, "end": v(52.44, -102.73) * mm});
            skLineSegment(sketch, "E3361", {"start": v(52.44, -102.73) * mm, "end": v(52.68, -102.95) * mm});
            skLineSegment(sketch, "E3362", {"start": v(52.68, -102.95) * mm, "end": v(52.94, -103.17) * mm});
            skLineSegment(sketch, "E3363", {"start": v(52.94, -103.17) * mm, "end": v(53.2, -103.39) * mm});
            skLineSegment(sketch, "E3364", {"start": v(53.2, -103.39) * mm, "end": v(53.46, -103.6) * mm});
            skLineSegment(sketch, "E3365", {"start": v(53.46, -103.6) * mm, "end": v(53.73, -103.84) * mm});
            skLineSegment(sketch, "E3366", {"start": v(53.73, -103.84) * mm, "end": v(54.01, -104.06) * mm});
            skLineSegment(sketch, "E3367", {"start": v(54.01, -104.06) * mm, "end": v(54.3, -104.3) * mm});
            skLineSegment(sketch, "E3368", {"start": v(54.3, -104.3) * mm, "end": v(54.6, -104.52) * mm});
            skLineSegment(sketch, "E3369", {"start": v(54.6, -104.52) * mm, "end": v(54.9, -104.76) * mm});
            skLineSegment(sketch, "E3370", {"start": v(54.9, -104.76) * mm, "end": v(55.2, -105) * mm});
            skLineSegment(sketch, "E3371", {"start": v(55.2, -105) * mm, "end": v(55.51, -105.23) * mm});
            skLineSegment(sketch, "E3372", {"start": v(55.51, -105.23) * mm, "end": v(55.83, -105.47) * mm});
            skLineSegment(sketch, "E3373", {"start": v(55.83, -105.47) * mm, "end": v(56.04, -105.48) * mm});
            skLineSegment(sketch, "E3374", {"start": v(56.04, -105.48) * mm, "end": v(59.11, -103.79) * mm});
            skLineSegment(sketch, "E3375", {"start": v(59.11, -103.79) * mm, "end": v(59.21, -103.6) * mm});
            skLineSegment(sketch, "E3376", {"start": v(59.21, -103.6) * mm, "end": v(59.19, -103.2) * mm});
            skLineSegment(sketch, "E3377", {"start": v(59.19, -103.2) * mm, "end": v(59.15, -102.82) * mm});
            skLineSegment(sketch, "E3378", {"start": v(59.15, -102.82) * mm, "end": v(59.12, -102.43) * mm});
            skLineSegment(sketch, "E3379", {"start": v(59.12, -102.43) * mm, "end": v(59.08, -102.05) * mm});
            skLineSegment(sketch, "E3380", {"start": v(59.08, -102.05) * mm, "end": v(59.04, -101.68) * mm});
            skLineSegment(sketch, "E3381", {"start": v(59.04, -101.68) * mm, "end": v(59, -101.32) * mm});
            skLineSegment(sketch, "E3382", {"start": v(59, -101.32) * mm, "end": v(58.96, -100.96) * mm});
            skLineSegment(sketch, "E3383", {"start": v(58.96, -100.96) * mm, "end": v(58.92, -100.6) * mm});
            skLineSegment(sketch, "E3384", {"start": v(58.92, -100.6) * mm, "end": v(58.87, -100.27) * mm});
            skLineSegment(sketch, "E3385", {"start": v(58.87, -100.27) * mm, "end": v(58.82, -99.93) * mm});
            skLineSegment(sketch, "E3386", {"start": v(58.82, -99.93) * mm, "end": v(58.77, -99.6) * mm});
            skLineSegment(sketch, "E3387", {"start": v(58.77, -99.6) * mm, "end": v(58.72, -99.27) * mm});
            skLineSegment(sketch, "E3388", {"start": v(58.72, -99.27) * mm, "end": v(58.66, -98.96) * mm});
            skLineSegment(sketch, "E3389", {"start": v(58.66, -98.96) * mm, "end": v(58.61, -98.65) * mm});
            skLineSegment(sketch, "E3390", {"start": v(58.61, -98.65) * mm, "end": v(58.55, -98.34) * mm});
            skLineSegment(sketch, "E3391", {"start": v(58.55, -98.34) * mm, "end": v(58.5, -98.05) * mm});
            skLineSegment(sketch, "E3392", {"start": v(58.5, -98.05) * mm, "end": v(58.44, -97.76) * mm});
            skLineSegment(sketch, "E3393", {"start": v(58.44, -97.76) * mm, "end": v(58.38, -97.47) * mm});
            skLineSegment(sketch, "E3394", {"start": v(58.38, -97.47) * mm, "end": v(58.32, -97.2) * mm});
            skLineSegment(sketch, "E3395", {"start": v(58.32, -97.2) * mm, "end": v(58.26, -96.93) * mm});
            skLineSegment(sketch, "E3396", {"start": v(58.26, -96.93) * mm, "end": v(58.2, -96.66) * mm});
            skLineSegment(sketch, "E3397", {"start": v(58.2, -96.66) * mm, "end": v(58.14, -96.4) * mm});
            skLineSegment(sketch, "E3398", {"start": v(58.14, -96.4) * mm, "end": v(58.08, -96.16) * mm});
            skLineSegment(sketch, "E3399", {"start": v(58.08, -96.16) * mm, "end": v(58.01, -95.92) * mm});
            skLineSegment(sketch, "E3400", {"start": v(58.01, -95.92) * mm, "end": v(57.95, -95.68) * mm});
            skLineSegment(sketch, "E3401", {"start": v(57.95, -95.68) * mm, "end": v(57.89, -95.45) * mm});
            skLineSegment(sketch, "E3402", {"start": v(57.89, -95.45) * mm, "end": v(57.83, -95.23) * mm});
            skLineSegment(sketch, "E3403", {"start": v(57.83, -95.23) * mm, "end": v(57.76, -95.01) * mm});
            skLineSegment(sketch, "E3404", {"start": v(57.76, -95.01) * mm, "end": v(57.7, -94.8) * mm});
            skLineSegment(sketch, "E3405", {"start": v(57.7, -94.8) * mm, "end": v(57.64, -94.6) * mm});
            skLineSegment(sketch, "E3406", {"start": v(57.64, -94.6) * mm, "end": v(57.58, -94.4) * mm});
            skLineSegment(sketch, "E3407", {"start": v(57.58, -94.4) * mm, "end": v(57.51, -94.22) * mm});
            skLineSegment(sketch, "E3408", {"start": v(57.51, -94.22) * mm, "end": v(57.45, -94.03) * mm});
            skLineSegment(sketch, "E3409", {"start": v(57.45, -94.03) * mm, "end": v(57.4, -93.86) * mm});
            skLineSegment(sketch, "E3410", {"start": v(57.4, -93.86) * mm, "end": v(57.33, -93.69) * mm});
            skLineSegment(sketch, "E3411", {"start": v(57.33, -93.69) * mm, "end": v(57.28, -93.53) * mm});
            skLineSegment(sketch, "E3412", {"start": v(57.28, -93.53) * mm, "end": v(57.22, -93.37) * mm});
            skLineSegment(sketch, "E3413", {"start": v(57.22, -93.37) * mm, "end": v(57.16, -93.22) * mm});
            skLineSegment(sketch, "E3414", {"start": v(57.16, -93.22) * mm, "end": v(57.1, -93.08) * mm});
            skLineSegment(sketch, "E3415", {"start": v(57.1, -93.08) * mm, "end": v(57.05, -92.94) * mm});
            skLineSegment(sketch, "E3416", {"start": v(57.05, -92.94) * mm, "end": v(57, -92.81) * mm});
            skLineSegment(sketch, "E3417", {"start": v(57, -92.81) * mm, "end": v(56.95, -92.69) * mm});
            skLineSegment(sketch, "E3418", {"start": v(56.95, -92.69) * mm, "end": v(56.93, -92.39) * mm});
            skLineSegment(sketch, "E3419", {"start": v(56.93, -92.39) * mm, "end": v(60.68, -89.97) * mm});
            skLineSegment(sketch, "E3420", {"start": v(60.68, -89.97) * mm, "end": v(60.95, -90.1) * mm});
            skLineSegment(sketch, "E3421", {"start": v(60.95, -90.1) * mm, "end": v(61.04, -90.2) * mm});
            skLineSegment(sketch, "E3422", {"start": v(61.04, -90.2) * mm, "end": v(61.14, -90.3) * mm});
            skLineSegment(sketch, "E3423", {"start": v(61.14, -90.3) * mm, "end": v(61.24, -90.41) * mm});
            skLineSegment(sketch, "E3424", {"start": v(61.24, -90.41) * mm, "end": v(61.35, -90.52) * mm});
            skLineSegment(sketch, "E3425", {"start": v(61.35, -90.52) * mm, "end": v(61.46, -90.64) * mm});
            skLineSegment(sketch, "E3426", {"start": v(61.46, -90.64) * mm, "end": v(61.58, -90.75) * mm});
            skLineSegment(sketch, "E3427", {"start": v(61.58, -90.75) * mm, "end": v(61.7, -90.87) * mm});
            skLineSegment(sketch, "E3428", {"start": v(61.7, -90.87) * mm, "end": v(61.83, -91) * mm});
            skLineSegment(sketch, "E3429", {"start": v(61.83, -91) * mm, "end": v(61.97, -91.12) * mm});
            skLineSegment(sketch, "E3430", {"start": v(61.97, -91.12) * mm, "end": v(62.1, -91.25) * mm});
            skLineSegment(sketch, "E3431", {"start": v(62.1, -91.25) * mm, "end": v(62.25, -91.39) * mm});
            skLineSegment(sketch, "E3432", {"start": v(62.25, -91.39) * mm, "end": v(62.4, -91.53) * mm});
            skLineSegment(sketch, "E3433", {"start": v(62.4, -91.53) * mm, "end": v(62.57, -91.67) * mm});
            skLineSegment(sketch, "E3434", {"start": v(62.57, -91.67) * mm, "end": v(62.73, -91.8) * mm});
            skLineSegment(sketch, "E3435", {"start": v(62.73, -91.8) * mm, "end": v(62.9, -91.95) * mm});
            skLineSegment(sketch, "E3436", {"start": v(62.9, -91.95) * mm, "end": v(63.08, -92.1) * mm});
            skLineSegment(sketch, "E3437", {"start": v(63.08, -92.1) * mm, "end": v(63.26, -92.25) * mm});
            skLineSegment(sketch, "E3438", {"start": v(63.26, -92.25) * mm, "end": v(63.45, -92.4) * mm});
            skLineSegment(sketch, "E3439", {"start": v(63.45, -92.4) * mm, "end": v(63.65, -92.57) * mm});
            skLineSegment(sketch, "E3440", {"start": v(63.65, -92.57) * mm, "end": v(63.85, -92.72) * mm});
            skLineSegment(sketch, "E3441", {"start": v(63.85, -92.72) * mm, "end": v(64.05, -92.89) * mm});
            skLineSegment(sketch, "E3442", {"start": v(64.05, -92.89) * mm, "end": v(64.27, -93.05) * mm});
            skLineSegment(sketch, "E3443", {"start": v(64.27, -93.05) * mm, "end": v(64.49, -93.22) * mm});
            skLineSegment(sketch, "E3444", {"start": v(64.49, -93.22) * mm, "end": v(64.72, -93.39) * mm});
            skLineSegment(sketch, "E3445", {"start": v(64.72, -93.39) * mm, "end": v(64.95, -93.56) * mm});
            skLineSegment(sketch, "E3446", {"start": v(64.95, -93.56) * mm, "end": v(65.2, -93.73) * mm});
            skLineSegment(sketch, "E3447", {"start": v(65.2, -93.73) * mm, "end": v(65.44, -93.9) * mm});
            skLineSegment(sketch, "E3448", {"start": v(65.44, -93.9) * mm, "end": v(65.7, -94.08) * mm});
            skLineSegment(sketch, "E3449", {"start": v(65.7, -94.08) * mm, "end": v(65.95, -94.26) * mm});
            skLineSegment(sketch, "E3450", {"start": v(65.95, -94.26) * mm, "end": v(66.22, -94.44) * mm});
            skLineSegment(sketch, "E3451", {"start": v(66.22, -94.44) * mm, "end": v(66.5, -94.62) * mm});
            skLineSegment(sketch, "E3452", {"start": v(66.5, -94.62) * mm, "end": v(66.77, -94.8) * mm});
            skLineSegment(sketch, "E3453", {"start": v(66.77, -94.8) * mm, "end": v(67.06, -94.98) * mm});
            skLineSegment(sketch, "E3454", {"start": v(67.06, -94.98) * mm, "end": v(67.35, -95.17) * mm});
            skLineSegment(sketch, "E3455", {"start": v(67.35, -95.17) * mm, "end": v(67.65, -95.35) * mm});
            skLineSegment(sketch, "E3456", {"start": v(67.65, -95.35) * mm, "end": v(67.96, -95.54) * mm});
            skLineSegment(sketch, "E3457", {"start": v(67.96, -95.54) * mm, "end": v(68.28, -95.73) * mm});
            skLineSegment(sketch, "E3458", {"start": v(68.28, -95.73) * mm, "end": v(68.6, -95.92) * mm});
            skLineSegment(sketch, "E3459", {"start": v(68.6, -95.92) * mm, "end": v(68.93, -96.1) * mm});
            skLineSegment(sketch, "E3460", {"start": v(68.93, -96.1) * mm, "end": v(69.27, -96.3) * mm});
            skLineSegment(sketch, "E3461", {"start": v(69.27, -96.3) * mm, "end": v(69.6, -96.48) * mm});
            skLineSegment(sketch, "E3462", {"start": v(69.6, -96.48) * mm, "end": v(69.96, -96.68) * mm});
            skLineSegment(sketch, "E3463", {"start": v(69.96, -96.68) * mm, "end": v(70.17, -96.66) * mm});
            skLineSegment(sketch, "E3464", {"start": v(70.17, -96.66) * mm, "end": v(72.98, -94.55) * mm});
            skLineSegment(sketch, "E3465", {"start": v(72.98, -94.55) * mm, "end": v(73.05, -94.36) * mm});
            skLineSegment(sketch, "E3466", {"start": v(73.05, -94.36) * mm, "end": v(72.97, -93.97) * mm});
            skLineSegment(sketch, "E3467", {"start": v(72.97, -93.97) * mm, "end": v(72.88, -93.59) * mm});
            skLineSegment(sketch, "E3468", {"start": v(72.88, -93.59) * mm, "end": v(72.8, -93.21) * mm});
            skLineSegment(sketch, "E3469", {"start": v(72.8, -93.21) * mm, "end": v(72.7, -92.84) * mm});
            skLineSegment(sketch, "E3470", {"start": v(72.7, -92.84) * mm, "end": v(72.61, -92.48) * mm});
            skLineSegment(sketch, "E3471", {"start": v(72.61, -92.48) * mm, "end": v(72.52, -92.13) * mm});
            skLineSegment(sketch, "E3472", {"start": v(72.52, -92.13) * mm, "end": v(72.43, -91.78) * mm});
            skLineSegment(sketch, "E3473", {"start": v(72.43, -91.78) * mm, "end": v(72.34, -91.44) * mm});
            skLineSegment(sketch, "E3474", {"start": v(72.34, -91.44) * mm, "end": v(72.24, -91.1) * mm});
            skLineSegment(sketch, "E3475", {"start": v(72.24, -91.1) * mm, "end": v(72.15, -90.77) * mm});
            skLineSegment(sketch, "E3476", {"start": v(72.15, -90.77) * mm, "end": v(72.05, -90.45) * mm});
            skLineSegment(sketch, "E3477", {"start": v(72.05, -90.45) * mm, "end": v(71.96, -90.14) * mm});
            skLineSegment(sketch, "E3478", {"start": v(71.96, -90.14) * mm, "end": v(71.86, -89.83) * mm});
            skLineSegment(sketch, "E3479", {"start": v(71.86, -89.83) * mm, "end": v(71.76, -89.53) * mm});
            skLineSegment(sketch, "E3480", {"start": v(71.76, -89.53) * mm, "end": v(71.66, -89.24) * mm});
            skLineSegment(sketch, "E3481", {"start": v(71.66, -89.24) * mm, "end": v(71.57, -88.96) * mm});
            skLineSegment(sketch, "E3482", {"start": v(71.57, -88.96) * mm, "end": v(71.47, -88.68) * mm});
            skLineSegment(sketch, "E3483", {"start": v(71.47, -88.68) * mm, "end": v(71.37, -88.4) * mm});
            skLineSegment(sketch, "E3484", {"start": v(71.37, -88.4) * mm, "end": v(71.27, -88.14) * mm});
            skLineSegment(sketch, "E3485", {"start": v(71.27, -88.14) * mm, "end": v(71.18, -87.88) * mm});
            skLineSegment(sketch, "E3486", {"start": v(71.18, -87.88) * mm, "end": v(71.08, -87.63) * mm});
            skLineSegment(sketch, "E3487", {"start": v(71.08, -87.63) * mm, "end": v(70.98, -87.38) * mm});
            skLineSegment(sketch, "E3488", {"start": v(70.98, -87.38) * mm, "end": v(70.89, -87.15) * mm});
            skLineSegment(sketch, "E3489", {"start": v(70.89, -87.15) * mm, "end": v(70.8, -86.91) * mm});
            skLineSegment(sketch, "E3490", {"start": v(70.8, -86.91) * mm, "end": v(70.7, -86.69) * mm});
            skLineSegment(sketch, "E3491", {"start": v(70.7, -86.69) * mm, "end": v(70.6, -86.47) * mm});
            skLineSegment(sketch, "E3492", {"start": v(70.6, -86.47) * mm, "end": v(70.5, -86.26) * mm});
            skLineSegment(sketch, "E3493", {"start": v(70.5, -86.26) * mm, "end": v(70.42, -86.05) * mm});
            skLineSegment(sketch, "E3494", {"start": v(70.42, -86.05) * mm, "end": v(70.33, -85.86) * mm});
            skLineSegment(sketch, "E3495", {"start": v(70.33, -85.86) * mm, "end": v(70.24, -85.66) * mm});
            skLineSegment(sketch, "E3496", {"start": v(70.24, -85.66) * mm, "end": v(70.15, -85.48) * mm});
            skLineSegment(sketch, "E3497", {"start": v(70.15, -85.48) * mm, "end": v(70.06, -85.3) * mm});
            skLineSegment(sketch, "E3498", {"start": v(70.06, -85.3) * mm, "end": v(69.98, -85.13) * mm});
            skLineSegment(sketch, "E3499", {"start": v(69.98, -85.13) * mm, "end": v(69.9, -84.96) * mm});
            skLineSegment(sketch, "E3500", {"start": v(69.9, -84.96) * mm, "end": v(69.8, -84.8) * mm});
            skLineSegment(sketch, "E3501", {"start": v(69.8, -84.8) * mm, "end": v(69.73, -84.65) * mm});
            skLineSegment(sketch, "E3502", {"start": v(69.73, -84.65) * mm, "end": v(69.65, -84.5) * mm});
            skLineSegment(sketch, "E3503", {"start": v(69.65, -84.5) * mm, "end": v(69.57, -84.36) * mm});
            skLineSegment(sketch, "E3504", {"start": v(69.57, -84.36) * mm, "end": v(69.5, -84.23) * mm});
            skLineSegment(sketch, "E3505", {"start": v(69.5, -84.23) * mm, "end": v(69.43, -84.1) * mm});
            skLineSegment(sketch, "E3506", {"start": v(69.43, -84.1) * mm, "end": v(69.36, -83.98) * mm});
            skLineSegment(sketch, "E3507", {"start": v(69.36, -83.98) * mm, "end": v(69.29, -83.86) * mm});
            skLineSegment(sketch, "E3508", {"start": v(69.29, -83.86) * mm, "end": v(69.23, -83.57) * mm});
            skLineSegment(sketch, "E3509", {"start": v(69.23, -83.57) * mm, "end": v(72.6, -80.65) * mm});
            skLineSegment(sketch, "E3510", {"start": v(72.6, -80.65) * mm, "end": v(72.89, -80.75) * mm});
            skLineSegment(sketch, "E3511", {"start": v(72.89, -80.75) * mm, "end": v(73, -80.84) * mm});
            skLineSegment(sketch, "E3512", {"start": v(73, -80.84) * mm, "end": v(73.1, -80.93) * mm});
            skLineSegment(sketch, "E3513", {"start": v(73.1, -80.93) * mm, "end": v(73.22, -81.02) * mm});
            skLineSegment(sketch, "E3514", {"start": v(73.22, -81.02) * mm, "end": v(73.34, -81.1) * mm});
            skLineSegment(sketch, "E3515", {"start": v(73.34, -81.1) * mm, "end": v(73.47, -81.2) * mm});
            skLineSegment(sketch, "E3516", {"start": v(73.47, -81.2) * mm, "end": v(73.6, -81.3) * mm});
            skLineSegment(sketch, "E3517", {"start": v(73.6, -81.3) * mm, "end": v(73.74, -81.4) * mm});
            skLineSegment(sketch, "E3518", {"start": v(73.74, -81.4) * mm, "end": v(73.89, -81.51) * mm});
            skLineSegment(sketch, "E3519", {"start": v(73.89, -81.51) * mm, "end": v(74.04, -81.62) * mm});
            skLineSegment(sketch, "E3520", {"start": v(74.04, -81.62) * mm, "end": v(74.2, -81.73) * mm});
            skLineSegment(sketch, "E3521", {"start": v(74.2, -81.73) * mm, "end": v(74.36, -81.84) * mm});
            skLineSegment(sketch, "E3522", {"start": v(74.36, -81.84) * mm, "end": v(74.53, -81.95) * mm});
            skLineSegment(sketch, "E3523", {"start": v(74.53, -81.95) * mm, "end": v(74.7, -82.07) * mm});
            skLineSegment(sketch, "E3524", {"start": v(74.7, -82.07) * mm, "end": v(74.9, -82.19) * mm});
            skLineSegment(sketch, "E3525", {"start": v(74.9, -82.19) * mm, "end": v(75.08, -82.31) * mm});
            skLineSegment(sketch, "E3526", {"start": v(75.08, -82.31) * mm, "end": v(75.28, -82.43) * mm});
            skLineSegment(sketch, "E3527", {"start": v(75.28, -82.43) * mm, "end": v(75.48, -82.56) * mm});
            skLineSegment(sketch, "E3528", {"start": v(75.48, -82.56) * mm, "end": v(75.69, -82.68) * mm});
            skLineSegment(sketch, "E3529", {"start": v(75.69, -82.68) * mm, "end": v(75.9, -82.81) * mm});
            skLineSegment(sketch, "E3530", {"start": v(75.9, -82.81) * mm, "end": v(76.12, -82.94) * mm});
            skLineSegment(sketch, "E3531", {"start": v(76.12, -82.94) * mm, "end": v(76.35, -83.07) * mm});
            skLineSegment(sketch, "E3532", {"start": v(76.35, -83.07) * mm, "end": v(76.59, -83.2) * mm});
            skLineSegment(sketch, "E3533", {"start": v(76.59, -83.2) * mm, "end": v(76.83, -83.34) * mm});
            skLineSegment(sketch, "E3534", {"start": v(76.83, -83.34) * mm, "end": v(77.08, -83.48) * mm});
            skLineSegment(sketch, "E3535", {"start": v(77.08, -83.48) * mm, "end": v(77.33, -83.61) * mm});
            skLineSegment(sketch, "E3536", {"start": v(77.33, -83.61) * mm, "end": v(77.6, -83.75) * mm});
            skLineSegment(sketch, "E3537", {"start": v(77.6, -83.75) * mm, "end": v(77.86, -83.89) * mm});
            skLineSegment(sketch, "E3538", {"start": v(77.86, -83.89) * mm, "end": v(78.14, -84.03) * mm});
            skLineSegment(sketch, "E3539", {"start": v(78.14, -84.03) * mm, "end": v(78.42, -84.17) * mm});
            skLineSegment(sketch, "E3540", {"start": v(78.42, -84.17) * mm, "end": v(78.7, -84.3) * mm});
            skLineSegment(sketch, "E3541", {"start": v(78.7, -84.3) * mm, "end": v(79, -84.45) * mm});
            skLineSegment(sketch, "E3542", {"start": v(79, -84.45) * mm, "end": v(79.3, -84.59) * mm});
            skLineSegment(sketch, "E3543", {"start": v(79.3, -84.59) * mm, "end": v(79.62, -84.73) * mm});
            skLineSegment(sketch, "E3544", {"start": v(79.62, -84.73) * mm, "end": v(79.94, -84.87) * mm});
            skLineSegment(sketch, "E3545", {"start": v(79.94, -84.87) * mm, "end": v(80.26, -85.01) * mm});
            skLineSegment(sketch, "E3546", {"start": v(80.26, -85.01) * mm, "end": v(80.6, -85.16) * mm});
            skLineSegment(sketch, "E3547", {"start": v(80.6, -85.16) * mm, "end": v(80.93, -85.3) * mm});
            skLineSegment(sketch, "E3548", {"start": v(80.93, -85.3) * mm, "end": v(81.27, -85.44) * mm});
            skLineSegment(sketch, "E3549", {"start": v(81.27, -85.44) * mm, "end": v(81.63, -85.58) * mm});
            skLineSegment(sketch, "E3550", {"start": v(81.63, -85.58) * mm, "end": v(81.99, -85.72) * mm});
            skLineSegment(sketch, "E3551", {"start": v(81.99, -85.72) * mm, "end": v(82.35, -85.86) * mm});
            skLineSegment(sketch, "E3552", {"start": v(82.35, -85.86) * mm, "end": v(82.73, -86) * mm});
            skLineSegment(sketch, "E3553", {"start": v(82.73, -86) * mm, "end": v(82.93, -85.96) * mm});
            skLineSegment(sketch, "E3554", {"start": v(82.93, -85.96) * mm, "end": v(85.42, -83.48) * mm});
            skLineSegment(sketch, "E3555", {"start": v(85.42, -83.48) * mm, "end": v(85.47, -83.28) * mm});
            skLineSegment(sketch, "E3556", {"start": v(85.47, -83.28) * mm, "end": v(85.33, -82.9) * mm});
            skLineSegment(sketch, "E3557", {"start": v(85.33, -82.9) * mm, "end": v(85.19, -82.54) * mm});
            skLineSegment(sketch, "E3558", {"start": v(85.19, -82.54) * mm, "end": v(85.05, -82.18) * mm});
            skLineSegment(sketch, "E3559", {"start": v(85.05, -82.18) * mm, "end": v(84.91, -81.83) * mm});
            skLineSegment(sketch, "E3560", {"start": v(84.91, -81.83) * mm, "end": v(84.77, -81.48) * mm});
            skLineSegment(sketch, "E3561", {"start": v(84.77, -81.48) * mm, "end": v(84.63, -81.14) * mm});
            skLineSegment(sketch, "E3562", {"start": v(84.63, -81.14) * mm, "end": v(84.5, -80.8) * mm});
            skLineSegment(sketch, "E3563", {"start": v(84.5, -80.8) * mm, "end": v(84.35, -80.48) * mm});
            skLineSegment(sketch, "E3564", {"start": v(84.35, -80.48) * mm, "end": v(84.21, -80.17) * mm});
            skLineSegment(sketch, "E3565", {"start": v(84.21, -80.17) * mm, "end": v(84.07, -79.85) * mm});
            skLineSegment(sketch, "E3566", {"start": v(84.07, -79.85) * mm, "end": v(83.93, -79.55) * mm});
            skLineSegment(sketch, "E3567", {"start": v(83.93, -79.55) * mm, "end": v(83.8, -79.25) * mm});
            skLineSegment(sketch, "E3568", {"start": v(83.8, -79.25) * mm, "end": v(83.66, -78.96) * mm});
            skLineSegment(sketch, "E3569", {"start": v(83.66, -78.96) * mm, "end": v(83.52, -78.68) * mm});
            skLineSegment(sketch, "E3570", {"start": v(83.52, -78.68) * mm, "end": v(83.38, -78.4) * mm});
            skLineSegment(sketch, "E3571", {"start": v(83.38, -78.4) * mm, "end": v(83.24, -78.13) * mm});
            skLineSegment(sketch, "E3572", {"start": v(83.24, -78.13) * mm, "end": v(83.1, -77.87) * mm});
            skLineSegment(sketch, "E3573", {"start": v(83.1, -77.87) * mm, "end": v(82.97, -77.62) * mm});
            skLineSegment(sketch, "E3574", {"start": v(82.97, -77.62) * mm, "end": v(82.84, -77.37) * mm});
            skLineSegment(sketch, "E3575", {"start": v(82.84, -77.37) * mm, "end": v(82.7, -77.12) * mm});
            skLineSegment(sketch, "E3576", {"start": v(82.7, -77.12) * mm, "end": v(82.58, -76.89) * mm});
            skLineSegment(sketch, "E3577", {"start": v(82.58, -76.89) * mm, "end": v(82.45, -76.66) * mm});
            skLineSegment(sketch, "E3578", {"start": v(82.45, -76.66) * mm, "end": v(82.32, -76.44) * mm});
            skLineSegment(sketch, "E3579", {"start": v(82.32, -76.44) * mm, "end": v(82.2, -76.22) * mm});
            skLineSegment(sketch, "E3580", {"start": v(82.2, -76.22) * mm, "end": v(82.07, -76.01) * mm});
            skLineSegment(sketch, "E3581", {"start": v(82.07, -76.01) * mm, "end": v(81.94, -75.8) * mm});
            skLineSegment(sketch, "E3582", {"start": v(81.94, -75.8) * mm, "end": v(81.82, -75.61) * mm});
            skLineSegment(sketch, "E3583", {"start": v(81.82, -75.61) * mm, "end": v(81.7, -75.42) * mm});
            skLineSegment(sketch, "E3584", {"start": v(81.7, -75.42) * mm, "end": v(81.58, -75.24) * mm});
            skLineSegment(sketch, "E3585", {"start": v(81.58, -75.24) * mm, "end": v(81.47, -75.06) * mm});
            skLineSegment(sketch, "E3586", {"start": v(81.47, -75.06) * mm, "end": v(81.35, -74.9) * mm});
            skLineSegment(sketch, "E3587", {"start": v(81.35, -74.9) * mm, "end": v(81.24, -74.73) * mm});
            skLineSegment(sketch, "E3588", {"start": v(81.24, -74.73) * mm, "end": v(81.14, -74.57) * mm});
            skLineSegment(sketch, "E3589", {"start": v(81.14, -74.57) * mm, "end": v(81.03, -74.41) * mm});
            skLineSegment(sketch, "E3590", {"start": v(81.03, -74.41) * mm, "end": v(80.93, -74.27) * mm});
            skLineSegment(sketch, "E3591", {"start": v(80.93, -74.27) * mm, "end": v(80.82, -74.13) * mm});
            skLineSegment(sketch, "E3592", {"start": v(80.82, -74.13) * mm, "end": v(80.73, -74) * mm});
            skLineSegment(sketch, "E3593", {"start": v(80.73, -74) * mm, "end": v(80.63, -73.86) * mm});
            skLineSegment(sketch, "E3594", {"start": v(80.63, -73.86) * mm, "end": v(80.54, -73.74) * mm});
            skLineSegment(sketch, "E3595", {"start": v(80.54, -73.74) * mm, "end": v(80.45, -73.63) * mm});
            skLineSegment(sketch, "E3596", {"start": v(80.45, -73.63) * mm, "end": v(80.36, -73.51) * mm});
            skLineSegment(sketch, "E3597", {"start": v(80.36, -73.51) * mm, "end": v(80.28, -73.4) * mm});
            skLineSegment(sketch, "E3598", {"start": v(80.28, -73.4) * mm, "end": v(80.18, -73.13) * mm});
            skLineSegment(sketch, "E3599", {"start": v(80.18, -73.13) * mm, "end": v(83.12, -69.76) * mm});
            skLineSegment(sketch, "E3600", {"start": v(83.12, -69.76) * mm, "end": v(83.41, -69.83) * mm});
            skLineSegment(sketch, "E3601", {"start": v(83.41, -69.83) * mm, "end": v(83.53, -69.9) * mm});
            skLineSegment(sketch, "E3602", {"start": v(83.53, -69.9) * mm, "end": v(83.65, -69.97) * mm});
            skLineSegment(sketch, "E3603", {"start": v(83.65, -69.97) * mm, "end": v(83.77, -70.04) * mm});
            skLineSegment(sketch, "E3604", {"start": v(83.77, -70.04) * mm, "end": v(83.9, -70.12) * mm});
            skLineSegment(sketch, "E3605", {"start": v(83.9, -70.12) * mm, "end": v(84.05, -70.2) * mm});
            skLineSegment(sketch, "E3606", {"start": v(84.05, -70.2) * mm, "end": v(84.2, -70.28) * mm});
            skLineSegment(sketch, "E3607", {"start": v(84.2, -70.28) * mm, "end": v(84.35, -70.36) * mm});
            skLineSegment(sketch, "E3608", {"start": v(84.35, -70.36) * mm, "end": v(84.5, -70.44) * mm});
            skLineSegment(sketch, "E3609", {"start": v(84.5, -70.44) * mm, "end": v(84.67, -70.52) * mm});
            skLineSegment(sketch, "E3610", {"start": v(84.67, -70.52) * mm, "end": v(84.84, -70.61) * mm});
            skLineSegment(sketch, "E3611", {"start": v(84.84, -70.61) * mm, "end": v(85.02, -70.7) * mm});
            skLineSegment(sketch, "E3612", {"start": v(85.02, -70.7) * mm, "end": v(85.2, -70.79) * mm});
            skLineSegment(sketch, "E3613", {"start": v(85.2, -70.79) * mm, "end": v(85.4, -70.88) * mm});
            skLineSegment(sketch, "E3614", {"start": v(85.4, -70.88) * mm, "end": v(85.6, -70.97) * mm});
            skLineSegment(sketch, "E3615", {"start": v(85.6, -70.97) * mm, "end": v(85.8, -71.07) * mm});
            skLineSegment(sketch, "E3616", {"start": v(85.8, -71.07) * mm, "end": v(86, -71.16) * mm});
            skLineSegment(sketch, "E3617", {"start": v(86, -71.16) * mm, "end": v(86.23, -71.26) * mm});
            skLineSegment(sketch, "E3618", {"start": v(86.23, -71.26) * mm, "end": v(86.45, -71.35) * mm});
            skLineSegment(sketch, "E3619", {"start": v(86.45, -71.35) * mm, "end": v(86.68, -71.45) * mm});
            skLineSegment(sketch, "E3620", {"start": v(86.68, -71.45) * mm, "end": v(86.92, -71.55) * mm});
            skLineSegment(sketch, "E3621", {"start": v(86.92, -71.55) * mm, "end": v(87.16, -71.64) * mm});
            skLineSegment(sketch, "E3622", {"start": v(87.16, -71.64) * mm, "end": v(87.42, -71.74) * mm});
            skLineSegment(sketch, "E3623", {"start": v(87.42, -71.74) * mm, "end": v(87.67, -71.84) * mm});
            skLineSegment(sketch, "E3624", {"start": v(87.67, -71.84) * mm, "end": v(87.94, -71.94) * mm});
            skLineSegment(sketch, "E3625", {"start": v(87.94, -71.94) * mm, "end": v(88.2, -72.04) * mm});
            skLineSegment(sketch, "E3626", {"start": v(88.2, -72.04) * mm, "end": v(88.49, -72.14) * mm});
            skLineSegment(sketch, "E3627", {"start": v(88.49, -72.14) * mm, "end": v(88.77, -72.24) * mm});
            skLineSegment(sketch, "E3628", {"start": v(88.77, -72.24) * mm, "end": v(89.07, -72.34) * mm});
            skLineSegment(sketch, "E3629", {"start": v(89.07, -72.34) * mm, "end": v(89.36, -72.44) * mm});
            skLineSegment(sketch, "E3630", {"start": v(89.36, -72.44) * mm, "end": v(89.67, -72.54) * mm});
            skLineSegment(sketch, "E3631", {"start": v(89.67, -72.54) * mm, "end": v(89.98, -72.64) * mm});
            skLineSegment(sketch, "E3632", {"start": v(89.98, -72.64) * mm, "end": v(90.3, -72.73) * mm});
            skLineSegment(sketch, "E3633", {"start": v(90.3, -72.73) * mm, "end": v(90.63, -72.83) * mm});
            skLineSegment(sketch, "E3634", {"start": v(90.63, -72.83) * mm, "end": v(90.96, -72.93) * mm});
            skLineSegment(sketch, "E3635", {"start": v(90.96, -72.93) * mm, "end": v(91.3, -73.02) * mm});
            skLineSegment(sketch, "E3636", {"start": v(91.3, -73.02) * mm, "end": v(91.65, -73.12) * mm});
            skLineSegment(sketch, "E3637", {"start": v(91.65, -73.12) * mm, "end": v(92, -73.21) * mm});
            skLineSegment(sketch, "E3638", {"start": v(92, -73.21) * mm, "end": v(92.37, -73.3) * mm});
            skLineSegment(sketch, "E3639", {"start": v(92.37, -73.3) * mm, "end": v(92.74, -73.4) * mm});
            skLineSegment(sketch, "E3640", {"start": v(92.74, -73.4) * mm, "end": v(93.11, -73.48) * mm});
            skLineSegment(sketch, "E3641", {"start": v(93.11, -73.48) * mm, "end": v(93.5, -73.57) * mm});
            skLineSegment(sketch, "E3642", {"start": v(93.5, -73.57) * mm, "end": v(93.88, -73.66) * mm});
            skLineSegment(sketch, "E3643", {"start": v(93.88, -73.66) * mm, "end": v(94.08, -73.58) * mm});
            skLineSegment(sketch, "E3644", {"start": v(94.08, -73.58) * mm, "end": v(96.2, -70.79) * mm});
            skLineSegment(sketch, "E3645", {"start": v(96.2, -70.79) * mm, "end": v(96.22, -70.58) * mm});
            skLineSegment(sketch, "E3646", {"start": v(96.22, -70.58) * mm, "end": v(96.03, -70.23) * mm});
            skLineSegment(sketch, "E3647", {"start": v(96.03, -70.23) * mm, "end": v(95.84, -69.89) * mm});
            skLineSegment(sketch, "E3648", {"start": v(95.84, -69.89) * mm, "end": v(95.65, -69.55) * mm});
            skLineSegment(sketch, "E3649", {"start": v(95.65, -69.55) * mm, "end": v(95.47, -69.22) * mm});
            skLineSegment(sketch, "E3650", {"start": v(95.47, -69.22) * mm, "end": v(95.28, -68.9) * mm});
            skLineSegment(sketch, "E3651", {"start": v(95.28, -68.9) * mm, "end": v(95.1, -68.58) * mm});
            skLineSegment(sketch, "E3652", {"start": v(95.1, -68.58) * mm, "end": v(94.9, -68.27) * mm});
            skLineSegment(sketch, "E3653", {"start": v(94.9, -68.27) * mm, "end": v(94.73, -67.97) * mm});
            skLineSegment(sketch, "E3654", {"start": v(94.73, -67.97) * mm, "end": v(94.54, -67.67) * mm});
            skLineSegment(sketch, "E3655", {"start": v(94.54, -67.67) * mm, "end": v(94.36, -67.38) * mm});
            skLineSegment(sketch, "E3656", {"start": v(94.36, -67.38) * mm, "end": v(94.18, -67.1) * mm});
            skLineSegment(sketch, "E3657", {"start": v(94.18, -67.1) * mm, "end": v(94, -66.83) * mm});
            skLineSegment(sketch, "E3658", {"start": v(94, -66.83) * mm, "end": v(93.82, -66.56) * mm});
            skLineSegment(sketch, "E3659", {"start": v(93.82, -66.56) * mm, "end": v(93.65, -66.3) * mm});
            skLineSegment(sketch, "E3660", {"start": v(93.65, -66.3) * mm, "end": v(93.47, -66.04) * mm});
            skLineSegment(sketch, "E3661", {"start": v(93.47, -66.04) * mm, "end": v(93.3, -65.8) * mm});
            skLineSegment(sketch, "E3662", {"start": v(93.3, -65.8) * mm, "end": v(93.13, -65.55) * mm});
            skLineSegment(sketch, "E3663", {"start": v(93.13, -65.55) * mm, "end": v(92.96, -65.32) * mm});
            skLineSegment(sketch, "E3664", {"start": v(92.96, -65.32) * mm, "end": v(92.8, -65.1) * mm});
            skLineSegment(sketch, "E3665", {"start": v(92.8, -65.1) * mm, "end": v(92.63, -64.87) * mm});
            skLineSegment(sketch, "E3666", {"start": v(92.63, -64.87) * mm, "end": v(92.47, -64.65) * mm});
            skLineSegment(sketch, "E3667", {"start": v(92.47, -64.65) * mm, "end": v(92.3, -64.44) * mm});
            skLineSegment(sketch, "E3668", {"start": v(92.3, -64.44) * mm, "end": v(92.15, -64.24) * mm});
            skLineSegment(sketch, "E3669", {"start": v(92.15, -64.24) * mm, "end": v(92, -64.05) * mm});
            skLineSegment(sketch, "E3670", {"start": v(92, -64.05) * mm, "end": v(91.84, -63.86) * mm});
            skLineSegment(sketch, "E3671", {"start": v(91.84, -63.86) * mm, "end": v(91.69, -63.67) * mm});
            skLineSegment(sketch, "E3672", {"start": v(91.69, -63.67) * mm, "end": v(91.54, -63.5) * mm});
            skLineSegment(sketch, "E3673", {"start": v(91.54, -63.5) * mm, "end": v(91.4, -63.32) * mm});
            skLineSegment(sketch, "E3674", {"start": v(91.4, -63.32) * mm, "end": v(91.25, -63.16) * mm});
            skLineSegment(sketch, "E3675", {"start": v(91.25, -63.16) * mm, "end": v(91.12, -63) * mm});
            skLineSegment(sketch, "E3676", {"start": v(91.12, -63) * mm, "end": v(90.98, -62.84) * mm});
            skLineSegment(sketch, "E3677", {"start": v(90.98, -62.84) * mm, "end": v(90.85, -62.7) * mm});
            skLineSegment(sketch, "E3678", {"start": v(90.85, -62.7) * mm, "end": v(90.72, -62.55) * mm});
            skLineSegment(sketch, "E3679", {"start": v(90.72, -62.55) * mm, "end": v(90.6, -62.42) * mm});
            skLineSegment(sketch, "E3680", {"start": v(90.6, -62.42) * mm, "end": v(90.47, -62.29) * mm});
            skLineSegment(sketch, "E3681", {"start": v(90.47, -62.29) * mm, "end": v(90.35, -62.16) * mm});
            skLineSegment(sketch, "E3682", {"start": v(90.35, -62.16) * mm, "end": v(90.23, -62.04) * mm});
            skLineSegment(sketch, "E3683", {"start": v(90.23, -62.04) * mm, "end": v(90.12, -61.93) * mm});
            skLineSegment(sketch, "E3684", {"start": v(90.12, -61.93) * mm, "end": v(90.01, -61.82) * mm});
            skLineSegment(sketch, "E3685", {"start": v(90.01, -61.82) * mm, "end": v(89.9, -61.72) * mm});
            skLineSegment(sketch, "E3686", {"start": v(89.9, -61.72) * mm, "end": v(89.8, -61.62) * mm});
            skLineSegment(sketch, "E3687", {"start": v(89.8, -61.62) * mm, "end": v(89.7, -61.53) * mm});
            skLineSegment(sketch, "E3688", {"start": v(89.7, -61.53) * mm, "end": v(89.57, -61.26) * mm});
            skLineSegment(sketch, "E3689", {"start": v(89.57, -61.26) * mm, "end": v(92.01, -57.52) * mm});
            skLineSegment(sketch, "E3690", {"start": v(92.01, -57.52) * mm, "end": v(92.31, -57.55) * mm});
            skLineSegment(sketch, "E3691", {"start": v(92.31, -57.55) * mm, "end": v(92.43, -57.6) * mm});
            skLineSegment(sketch, "E3692", {"start": v(92.43, -57.6) * mm, "end": v(92.56, -57.65) * mm});
            skLineSegment(sketch, "E3693", {"start": v(92.56, -57.65) * mm, "end": v(92.7, -57.7) * mm});
            skLineSegment(sketch, "E3694", {"start": v(92.7, -57.7) * mm, "end": v(92.84, -57.76) * mm});
            skLineSegment(sketch, "E3695", {"start": v(92.84, -57.76) * mm, "end": v(93, -57.82) * mm});
            skLineSegment(sketch, "E3696", {"start": v(93, -57.82) * mm, "end": v(93.15, -57.88) * mm});
            skLineSegment(sketch, "E3697", {"start": v(93.15, -57.88) * mm, "end": v(93.31, -57.94) * mm});
            skLineSegment(sketch, "E3698", {"start": v(93.31, -57.94) * mm, "end": v(93.48, -58) * mm});
            skLineSegment(sketch, "E3699", {"start": v(93.48, -58) * mm, "end": v(93.66, -58.06) * mm});
            skLineSegment(sketch, "E3700", {"start": v(93.66, -58.06) * mm, "end": v(93.84, -58.12) * mm});
            skLineSegment(sketch, "E3701", {"start": v(93.84, -58.12) * mm, "end": v(94.03, -58.18) * mm});
            skLineSegment(sketch, "E3702", {"start": v(94.03, -58.18) * mm, "end": v(94.22, -58.25) * mm});
            skLineSegment(sketch, "E3703", {"start": v(94.22, -58.25) * mm, "end": v(94.42, -58.31) * mm});
            skLineSegment(sketch, "E3704", {"start": v(94.42, -58.31) * mm, "end": v(94.63, -58.37) * mm});
            skLineSegment(sketch, "E3705", {"start": v(94.63, -58.37) * mm, "end": v(94.85, -58.44) * mm});
            skLineSegment(sketch, "E3706", {"start": v(94.85, -58.44) * mm, "end": v(95.07, -58.5) * mm});
            skLineSegment(sketch, "E3707", {"start": v(95.07, -58.5) * mm, "end": v(95.3, -58.57) * mm});
            skLineSegment(sketch, "E3708", {"start": v(95.3, -58.57) * mm, "end": v(95.53, -58.63) * mm});
            skLineSegment(sketch, "E3709", {"start": v(95.53, -58.63) * mm, "end": v(95.78, -58.7) * mm});
            skLineSegment(sketch, "E3710", {"start": v(95.78, -58.7) * mm, "end": v(96.02, -58.76) * mm});
            skLineSegment(sketch, "E3711", {"start": v(96.02, -58.76) * mm, "end": v(96.28, -58.82) * mm});
            skLineSegment(sketch, "E3712", {"start": v(96.28, -58.82) * mm, "end": v(96.54, -58.88) * mm});
            skLineSegment(sketch, "E3713", {"start": v(96.54, -58.88) * mm, "end": v(96.81, -58.95) * mm});
            skLineSegment(sketch, "E3714", {"start": v(96.81, -58.95) * mm, "end": v(97.09, -59) * mm});
            skLineSegment(sketch, "E3715", {"start": v(97.09, -59) * mm, "end": v(97.37, -59.07) * mm});
            skLineSegment(sketch, "E3716", {"start": v(97.37, -59.07) * mm, "end": v(97.66, -59.13) * mm});
            skLineSegment(sketch, "E3717", {"start": v(97.66, -59.13) * mm, "end": v(97.96, -59.19) * mm});
            skLineSegment(sketch, "E3718", {"start": v(97.96, -59.19) * mm, "end": v(98.26, -59.25) * mm});
            skLineSegment(sketch, "E3719", {"start": v(98.26, -59.25) * mm, "end": v(98.57, -59.3) * mm});
            skLineSegment(sketch, "E3720", {"start": v(98.57, -59.3) * mm, "end": v(98.89, -59.36) * mm});
            skLineSegment(sketch, "E3721", {"start": v(98.89, -59.36) * mm, "end": v(99.2, -59.4) * mm});
            skLineSegment(sketch, "E3722", {"start": v(99.2, -59.4) * mm, "end": v(99.54, -59.46) * mm});
            skLineSegment(sketch, "E3723", {"start": v(99.54, -59.46) * mm, "end": v(99.88, -59.51) * mm});
            skLineSegment(sketch, "E3724", {"start": v(99.88, -59.51) * mm, "end": v(100.22, -59.56) * mm});
            skLineSegment(sketch, "E3725", {"start": v(100.22, -59.56) * mm, "end": v(100.57, -59.6) * mm});
            skLineSegment(sketch, "E3726", {"start": v(100.57, -59.6) * mm, "end": v(100.93, -59.66) * mm});
            skLineSegment(sketch, "E3727", {"start": v(100.93, -59.66) * mm, "end": v(101.3, -59.7) * mm});
            skLineSegment(sketch, "E3728", {"start": v(101.3, -59.7) * mm, "end": v(101.66, -59.74) * mm});
            skLineSegment(sketch, "E3729", {"start": v(101.66, -59.74) * mm, "end": v(102.04, -59.78) * mm});
            skLineSegment(sketch, "E3730", {"start": v(102.04, -59.78) * mm, "end": v(102.43, -59.81) * mm});
            skLineSegment(sketch, "E3731", {"start": v(102.43, -59.81) * mm, "end": v(102.82, -59.85) * mm});
            skLineSegment(sketch, "E3732", {"start": v(102.82, -59.85) * mm, "end": v(103.22, -59.88) * mm});
            skLineSegment(sketch, "E3733", {"start": v(103.22, -59.88) * mm, "end": v(103.4, -59.78) * mm});
            skLineSegment(sketch, "E3734", {"start": v(103.4, -59.78) * mm, "end": v(105.1, -56.72) * mm});
            skLineSegment(sketch, "E3735", {"start": v(105.1, -56.72) * mm, "end": v(105.1, -56.5) * mm});
            skLineSegment(sketch, "E3736", {"start": v(105.1, -56.5) * mm, "end": v(104.86, -56.19) * mm});
            skLineSegment(sketch, "E3737", {"start": v(104.86, -56.19) * mm, "end": v(104.63, -55.87) * mm});
            skLineSegment(sketch, "E3738", {"start": v(104.63, -55.87) * mm, "end": v(104.4, -55.56) * mm});
            skLineSegment(sketch, "E3739", {"start": v(104.4, -55.56) * mm, "end": v(104.16, -55.26) * mm});
            skLineSegment(sketch, "E3740", {"start": v(104.16, -55.26) * mm, "end": v(103.93, -54.97) * mm});
            skLineSegment(sketch, "E3741", {"start": v(103.93, -54.97) * mm, "end": v(103.7, -54.68) * mm});
            skLineSegment(sketch, "E3742", {"start": v(103.7, -54.68) * mm, "end": v(103.48, -54.4) * mm});
            skLineSegment(sketch, "E3743", {"start": v(103.48, -54.4) * mm, "end": v(103.26, -54.13) * mm});
            skLineSegment(sketch, "E3744", {"start": v(103.26, -54.13) * mm, "end": v(103.03, -53.86) * mm});
            skLineSegment(sketch, "E3745", {"start": v(103.03, -53.86) * mm, "end": v(102.81, -53.6) * mm});
            skLineSegment(sketch, "E3746", {"start": v(102.81, -53.6) * mm, "end": v(102.6, -53.35) * mm});
            skLineSegment(sketch, "E3747", {"start": v(102.6, -53.35) * mm, "end": v(102.38, -53.1) * mm});
            skLineSegment(sketch, "E3748", {"start": v(102.38, -53.1) * mm, "end": v(102.17, -52.86) * mm});
            skLineSegment(sketch, "E3749", {"start": v(102.17, -52.86) * mm, "end": v(101.96, -52.62) * mm});
            skLineSegment(sketch, "E3750", {"start": v(101.96, -52.62) * mm, "end": v(101.75, -52.4) * mm});
            skLineSegment(sketch, "E3751", {"start": v(101.75, -52.4) * mm, "end": v(101.54, -52.17) * mm});
            skLineSegment(sketch, "E3752", {"start": v(101.54, -52.17) * mm, "end": v(101.34, -51.96) * mm});
            skLineSegment(sketch, "E3753", {"start": v(101.34, -51.96) * mm, "end": v(101.14, -51.75) * mm});
            skLineSegment(sketch, "E3754", {"start": v(101.14, -51.75) * mm, "end": v(100.94, -51.55) * mm});
            skLineSegment(sketch, "E3755", {"start": v(100.94, -51.55) * mm, "end": v(100.75, -51.35) * mm});
            skLineSegment(sketch, "E3756", {"start": v(100.75, -51.35) * mm, "end": v(100.56, -51.16) * mm});
            skLineSegment(sketch, "E3757", {"start": v(100.56, -51.16) * mm, "end": v(100.37, -50.98) * mm});
            skLineSegment(sketch, "E3758", {"start": v(100.37, -50.98) * mm, "end": v(100.19, -50.8) * mm});
            skLineSegment(sketch, "E3759", {"start": v(100.19, -50.8) * mm, "end": v(100, -50.62) * mm});
            skLineSegment(sketch, "E3760", {"start": v(100, -50.62) * mm, "end": v(99.83, -50.46) * mm});
            skLineSegment(sketch, "E3761", {"start": v(99.83, -50.46) * mm, "end": v(99.65, -50.3) * mm});
            skLineSegment(sketch, "E3762", {"start": v(99.65, -50.3) * mm, "end": v(99.48, -50.14) * mm});
            skLineSegment(sketch, "E3763", {"start": v(99.48, -50.14) * mm, "end": v(99.31, -50) * mm});
            skLineSegment(sketch, "E3764", {"start": v(99.31, -50) * mm, "end": v(99.15, -49.85) * mm});
            skLineSegment(sketch, "E3765", {"start": v(99.15, -49.85) * mm, "end": v(98.99, -49.7) * mm});
            skLineSegment(sketch, "E3766", {"start": v(98.99, -49.7) * mm, "end": v(98.83, -49.58) * mm});
            skLineSegment(sketch, "E3767", {"start": v(98.83, -49.58) * mm, "end": v(98.68, -49.45) * mm});
            skLineSegment(sketch, "E3768", {"start": v(98.68, -49.45) * mm, "end": v(98.53, -49.33) * mm});
            skLineSegment(sketch, "E3769", {"start": v(98.53, -49.33) * mm, "end": v(98.39, -49.2) * mm});
            skLineSegment(sketch, "E3770", {"start": v(98.39, -49.2) * mm, "end": v(98.25, -49.1) * mm});
            skLineSegment(sketch, "E3771", {"start": v(98.25, -49.1) * mm, "end": v(98.11, -48.99) * mm});
            skLineSegment(sketch, "E3772", {"start": v(98.11, -48.99) * mm, "end": v(97.98, -48.89) * mm});
            skLineSegment(sketch, "E3773", {"start": v(97.98, -48.89) * mm, "end": v(97.85, -48.8) * mm});
            skLineSegment(sketch, "E3774", {"start": v(97.85, -48.8) * mm, "end": v(97.73, -48.7) * mm});
            skLineSegment(sketch, "E3775", {"start": v(97.73, -48.7) * mm, "end": v(97.61, -48.61) * mm});
            skLineSegment(sketch, "E3776", {"start": v(97.61, -48.61) * mm, "end": v(97.5, -48.53) * mm});
            skLineSegment(sketch, "E3777", {"start": v(97.5, -48.53) * mm, "end": v(97.4, -48.45) * mm});
            skLineSegment(sketch, "E3778", {"start": v(97.4, -48.45) * mm, "end": v(97.21, -48.2) * mm});
            skLineSegment(sketch, "E3779", {"start": v(97.21, -48.2) * mm, "end": v(99.12, -44.16) * mm});
            skLineSegment(sketch, "E3780", {"start": v(99.12, -44.16) * mm, "end": v(99.41, -44.15) * mm});
            skLineSegment(sketch, "E3781", {"start": v(99.41, -44.15) * mm, "end": v(99.54, -44.18) * mm});
            skLineSegment(sketch, "E3782", {"start": v(99.54, -44.18) * mm, "end": v(99.68, -44.21) * mm});
            skLineSegment(sketch, "E3783", {"start": v(99.68, -44.21) * mm, "end": v(99.82, -44.25) * mm});
            skLineSegment(sketch, "E3784", {"start": v(99.82, -44.25) * mm, "end": v(99.97, -44.29) * mm});
            skLineSegment(sketch, "E3785", {"start": v(99.97, -44.29) * mm, "end": v(100.13, -44.32) * mm});
            skLineSegment(sketch, "E3786", {"start": v(100.13, -44.32) * mm, "end": v(100.3, -44.36) * mm});
            skLineSegment(sketch, "E3787", {"start": v(100.3, -44.36) * mm, "end": v(100.46, -44.4) * mm});
            skLineSegment(sketch, "E3788", {"start": v(100.46, -44.4) * mm, "end": v(100.64, -44.43) * mm});
            skLineSegment(sketch, "E3789", {"start": v(100.64, -44.43) * mm, "end": v(100.82, -44.47) * mm});
            skLineSegment(sketch, "E3790", {"start": v(100.82, -44.47) * mm, "end": v(101, -44.5) * mm});
            skLineSegment(sketch, "E3791", {"start": v(101, -44.5) * mm, "end": v(101.2, -44.54) * mm});
            skLineSegment(sketch, "E3792", {"start": v(101.2, -44.54) * mm, "end": v(101.4, -44.57) * mm});
            skLineSegment(sketch, "E3793", {"start": v(101.4, -44.57) * mm, "end": v(101.61, -44.6) * mm});
            skLineSegment(sketch, "E3794", {"start": v(101.61, -44.6) * mm, "end": v(101.83, -44.64) * mm});
            skLineSegment(sketch, "E3795", {"start": v(101.83, -44.64) * mm, "end": v(102.05, -44.67) * mm});
            skLineSegment(sketch, "E3796", {"start": v(102.05, -44.67) * mm, "end": v(102.28, -44.7) * mm});
            skLineSegment(sketch, "E3797", {"start": v(102.28, -44.7) * mm, "end": v(102.51, -44.74) * mm});
            skLineSegment(sketch, "E3798", {"start": v(102.51, -44.74) * mm, "end": v(102.76, -44.77) * mm});
            skLineSegment(sketch, "E3799", {"start": v(102.76, -44.77) * mm, "end": v(103, -44.8) * mm});
            skLineSegment(sketch, "E3800", {"start": v(103, -44.8) * mm, "end": v(103.26, -44.83) * mm});
            skLineSegment(sketch, "E3801", {"start": v(103.26, -44.83) * mm, "end": v(103.52, -44.86) * mm});
            skLineSegment(sketch, "E3802", {"start": v(103.52, -44.86) * mm, "end": v(103.8, -44.88) * mm});
            skLineSegment(sketch, "E3803", {"start": v(103.8, -44.88) * mm, "end": v(104.07, -44.9) * mm});
            skLineSegment(sketch, "E3804", {"start": v(104.07, -44.9) * mm, "end": v(104.35, -44.93) * mm});
            skLineSegment(sketch, "E3805", {"start": v(104.35, -44.93) * mm, "end": v(104.64, -44.95) * mm});
            skLineSegment(sketch, "E3806", {"start": v(104.64, -44.95) * mm, "end": v(104.93, -44.97) * mm});
            skLineSegment(sketch, "E3807", {"start": v(104.93, -44.97) * mm, "end": v(105.23, -44.98) * mm});
            skLineSegment(sketch, "E3808", {"start": v(105.23, -44.98) * mm, "end": v(105.54, -45) * mm});
            skLineSegment(sketch, "E3809", {"start": v(105.54, -45) * mm, "end": v(105.86, -45.01) * mm});
            skLineSegment(sketch, "E3810", {"start": v(105.86, -45.01) * mm, "end": v(106.18, -45.02) * mm});
            skLineSegment(sketch, "E3811", {"start": v(106.18, -45.02) * mm, "end": v(106.5, -45.03) * mm});
            skLineSegment(sketch, "E3812", {"start": v(106.5, -45.03) * mm, "end": v(106.84, -45.04) * mm});
            skLineSegment(sketch, "E3813", {"start": v(106.84, -45.04) * mm, "end": v(107.18, -45.04) * mm});
            skLineSegment(sketch, "E3814", {"start": v(107.18, -45.04) * mm, "end": v(107.53, -45.04) * mm});
            skLineSegment(sketch, "E3815", {"start": v(107.53, -45.04) * mm, "end": v(107.88, -45.04) * mm});
            skLineSegment(sketch, "E3816", {"start": v(107.88, -45.04) * mm, "end": v(108.24, -45.03) * mm});
            skLineSegment(sketch, "E3817", {"start": v(108.24, -45.03) * mm, "end": v(108.6, -45.03) * mm});
            skLineSegment(sketch, "E3818", {"start": v(108.6, -45.03) * mm, "end": v(108.98, -45.01) * mm});
            skLineSegment(sketch, "E3819", {"start": v(108.98, -45.01) * mm, "end": v(109.36, -45) * mm});
            skLineSegment(sketch, "E3820", {"start": v(109.36, -45) * mm, "end": v(109.75, -44.98) * mm});
            skLineSegment(sketch, "E3821", {"start": v(109.75, -44.98) * mm, "end": v(110.14, -44.96) * mm});
            skLineSegment(sketch, "E3822", {"start": v(110.14, -44.96) * mm, "end": v(110.54, -44.94) * mm});
            skLineSegment(sketch, "E3823", {"start": v(110.54, -44.94) * mm, "end": v(110.7, -44.81) * mm});
            skLineSegment(sketch, "E3824", {"start": v(110.7, -44.81) * mm, "end": v(111.97, -41.54) * mm});
            skLineSegment(sketch, "E3825", {"start": v(111.97, -41.54) * mm, "end": v(111.93, -41.34) * mm});
            skLineSegment(sketch, "E3826", {"start": v(111.93, -41.34) * mm, "end": v(111.66, -41.05) * mm});
            skLineSegment(sketch, "E3827", {"start": v(111.66, -41.05) * mm, "end": v(111.38, -40.77) * mm});
            skLineSegment(sketch, "E3828", {"start": v(111.38, -40.77) * mm, "end": v(111.1, -40.5) * mm});
            skLineSegment(sketch, "E3829", {"start": v(111.1, -40.5) * mm, "end": v(110.83, -40.23) * mm});
            skLineSegment(sketch, "E3830", {"start": v(110.83, -40.23) * mm, "end": v(110.57, -39.97) * mm});
            skLineSegment(sketch, "E3831", {"start": v(110.57, -39.97) * mm, "end": v(110.3, -39.72) * mm});
            skLineSegment(sketch, "E3832", {"start": v(110.3, -39.72) * mm, "end": v(110.04, -39.48) * mm});
            skLineSegment(sketch, "E3833", {"start": v(110.04, -39.48) * mm, "end": v(109.78, -39.24) * mm});
            skLineSegment(sketch, "E3834", {"start": v(109.78, -39.24) * mm, "end": v(109.52, -39) * mm});
            skLineSegment(sketch, "E3835", {"start": v(109.52, -39) * mm, "end": v(109.27, -38.77) * mm});
            skLineSegment(sketch, "E3836", {"start": v(109.27, -38.77) * mm, "end": v(109.02, -38.55) * mm});
            skLineSegment(sketch, "E3837", {"start": v(109.02, -38.55) * mm, "end": v(108.77, -38.34) * mm});
            skLineSegment(sketch, "E3838", {"start": v(108.77, -38.34) * mm, "end": v(108.52, -38.13) * mm});
            skLineSegment(sketch, "E3839", {"start": v(108.52, -38.13) * mm, "end": v(108.28, -37.93) * mm});
            skLineSegment(sketch, "E3840", {"start": v(108.28, -37.93) * mm, "end": v(108.04, -37.73) * mm});
            skLineSegment(sketch, "E3841", {"start": v(108.04, -37.73) * mm, "end": v(107.81, -37.54) * mm});
            skLineSegment(sketch, "E3842", {"start": v(107.81, -37.54) * mm, "end": v(107.58, -37.36) * mm});
            skLineSegment(sketch, "E3843", {"start": v(107.58, -37.36) * mm, "end": v(107.35, -37.18) * mm});
            skLineSegment(sketch, "E3844", {"start": v(107.35, -37.18) * mm, "end": v(107.13, -37) * mm});
            skLineSegment(sketch, "E3845", {"start": v(107.13, -37) * mm, "end": v(106.9, -36.83) * mm});
            skLineSegment(sketch, "E3846", {"start": v(106.9, -36.83) * mm, "end": v(106.7, -36.67) * mm});
            skLineSegment(sketch, "E3847", {"start": v(106.7, -36.67) * mm, "end": v(106.48, -36.52) * mm});
            skLineSegment(sketch, "E3848", {"start": v(106.48, -36.52) * mm, "end": v(106.27, -36.37) * mm});
            skLineSegment(sketch, "E3849", {"start": v(106.27, -36.37) * mm, "end": v(106.07, -36.22) * mm});
            skLineSegment(sketch, "E3850", {"start": v(106.07, -36.22) * mm, "end": v(105.87, -36.08) * mm});
            skLineSegment(sketch, "E3851", {"start": v(105.87, -36.08) * mm, "end": v(105.67, -35.94) * mm});
            skLineSegment(sketch, "E3852", {"start": v(105.67, -35.94) * mm, "end": v(105.48, -35.81) * mm});
            skLineSegment(sketch, "E3853", {"start": v(105.48, -35.81) * mm, "end": v(105.3, -35.69) * mm});
            skLineSegment(sketch, "E3854", {"start": v(105.3, -35.69) * mm, "end": v(105.12, -35.57) * mm});
            skLineSegment(sketch, "E3855", {"start": v(105.12, -35.57) * mm, "end": v(104.94, -35.45) * mm});
            skLineSegment(sketch, "E3856", {"start": v(104.94, -35.45) * mm, "end": v(104.76, -35.34) * mm});
            skLineSegment(sketch, "E3857", {"start": v(104.76, -35.34) * mm, "end": v(104.6, -35.24) * mm});
            skLineSegment(sketch, "E3858", {"start": v(104.6, -35.24) * mm, "end": v(104.43, -35.14) * mm});
            skLineSegment(sketch, "E3859", {"start": v(104.43, -35.14) * mm, "end": v(104.27, -35.04) * mm});
            skLineSegment(sketch, "E3860", {"start": v(104.27, -35.04) * mm, "end": v(104.12, -34.95) * mm});
            skLineSegment(sketch, "E3861", {"start": v(104.12, -34.95) * mm, "end": v(103.97, -34.86) * mm});
            skLineSegment(sketch, "E3862", {"start": v(103.97, -34.86) * mm, "end": v(103.83, -34.78) * mm});
            skLineSegment(sketch, "E3863", {"start": v(103.83, -34.78) * mm, "end": v(103.69, -34.7) * mm});
            skLineSegment(sketch, "E3864", {"start": v(103.69, -34.7) * mm, "end": v(103.55, -34.63) * mm});
            skLineSegment(sketch, "E3865", {"start": v(103.55, -34.63) * mm, "end": v(103.42, -34.56) * mm});
            skLineSegment(sketch, "E3866", {"start": v(103.42, -34.56) * mm, "end": v(103.3, -34.5) * mm});
            skLineSegment(sketch, "E3867", {"start": v(103.3, -34.5) * mm, "end": v(103.18, -34.43) * mm});
            skLineSegment(sketch, "E3868", {"start": v(103.18, -34.43) * mm, "end": v(102.97, -34.21) * mm});
            skLineSegment(sketch, "E3869", {"start": v(102.97, -34.21) * mm, "end": v(104.3, -29.94) * mm});
            skLineSegment(sketch, "E3870", {"start": v(104.3, -29.94) * mm, "end": v(104.58, -29.88) * mm});
            skLineSegment(sketch, "E3871", {"start": v(104.58, -29.88) * mm, "end": v(104.72, -29.9) * mm});
            skLineSegment(sketch, "E3872", {"start": v(104.72, -29.9) * mm, "end": v(104.86, -29.92) * mm});
            skLineSegment(sketch, "E3873", {"start": v(104.86, -29.92) * mm, "end": v(105, -29.93) * mm});
            skLineSegment(sketch, "E3874", {"start": v(105, -29.93) * mm, "end": v(105.16, -29.95) * mm});
            skLineSegment(sketch, "E3875", {"start": v(105.16, -29.95) * mm, "end": v(105.32, -29.96) * mm});
            skLineSegment(sketch, "E3876", {"start": v(105.32, -29.96) * mm, "end": v(105.48, -29.97) * mm});
            skLineSegment(sketch, "E3877", {"start": v(105.48, -29.97) * mm, "end": v(105.65, -29.99) * mm});
            skLineSegment(sketch, "E3878", {"start": v(105.65, -29.99) * mm, "end": v(105.83, -30) * mm});
            skLineSegment(sketch, "E3879", {"start": v(105.83, -30) * mm, "end": v(106.02, -30) * mm});
            skLineSegment(sketch, "E3880", {"start": v(106.02, -30) * mm, "end": v(106.21, -30.02) * mm});
            skLineSegment(sketch, "E3881", {"start": v(106.21, -30.02) * mm, "end": v(106.4, -30.02) * mm});
            skLineSegment(sketch, "E3882", {"start": v(106.4, -30.02) * mm, "end": v(106.61, -30.03) * mm});
            skLineSegment(sketch, "E3883", {"start": v(106.61, -30.03) * mm, "end": v(106.83, -30.04) * mm});
            skLineSegment(sketch, "E3884", {"start": v(106.83, -30.04) * mm, "end": v(107.04, -30.04) * mm});
            skLineSegment(sketch, "E3885", {"start": v(107.04, -30.04) * mm, "end": v(107.27, -30.04) * mm});
            skLineSegment(sketch, "E3886", {"start": v(107.27, -30.04) * mm, "end": v(107.5, -30.04) * mm});
            skLineSegment(sketch, "E3887", {"start": v(107.5, -30.04) * mm, "end": v(107.74, -30.04) * mm});
            skLineSegment(sketch, "E3888", {"start": v(107.74, -30.04) * mm, "end": v(107.98, -30.04) * mm});
            skLineSegment(sketch, "E3889", {"start": v(107.98, -30.04) * mm, "end": v(108.23, -30.03) * mm});
            skLineSegment(sketch, "E3890", {"start": v(108.23, -30.03) * mm, "end": v(108.49, -30.03) * mm});
            skLineSegment(sketch, "E3891", {"start": v(108.49, -30.03) * mm, "end": v(108.75, -30.02) * mm});
            skLineSegment(sketch, "E3892", {"start": v(108.75, -30.02) * mm, "end": v(109.02, -30) * mm});
            skLineSegment(sketch, "E3893", {"start": v(109.02, -30) * mm, "end": v(109.3, -29.99) * mm});
            skLineSegment(sketch, "E3894", {"start": v(109.3, -29.99) * mm, "end": v(109.58, -29.97) * mm});
            skLineSegment(sketch, "E3895", {"start": v(109.58, -29.97) * mm, "end": v(109.87, -29.95) * mm});
            skLineSegment(sketch, "E3896", {"start": v(109.87, -29.95) * mm, "end": v(110.16, -29.93) * mm});
            skLineSegment(sketch, "E3897", {"start": v(110.16, -29.93) * mm, "end": v(110.46, -29.9) * mm});
            skLineSegment(sketch, "E3898", {"start": v(110.46, -29.9) * mm, "end": v(110.77, -29.88) * mm});
            skLineSegment(sketch, "E3899", {"start": v(110.77, -29.88) * mm, "end": v(111.08, -29.85) * mm});
            skLineSegment(sketch, "E3900", {"start": v(111.08, -29.85) * mm, "end": v(111.4, -29.81) * mm});
            skLineSegment(sketch, "E3901", {"start": v(111.4, -29.81) * mm, "end": v(111.73, -29.77) * mm});
            skLineSegment(sketch, "E3902", {"start": v(111.73, -29.77) * mm, "end": v(112.06, -29.73) * mm});
            skLineSegment(sketch, "E3903", {"start": v(112.06, -29.73) * mm, "end": v(112.4, -29.69) * mm});
            skLineSegment(sketch, "E3904", {"start": v(112.4, -29.69) * mm, "end": v(112.74, -29.64) * mm});
            skLineSegment(sketch, "E3905", {"start": v(112.74, -29.64) * mm, "end": v(113.1, -29.6) * mm});
            skLineSegment(sketch, "E3906", {"start": v(113.1, -29.6) * mm, "end": v(113.45, -29.54) * mm});
            skLineSegment(sketch, "E3907", {"start": v(113.45, -29.54) * mm, "end": v(113.81, -29.48) * mm});
            skLineSegment(sketch, "E3908", {"start": v(113.81, -29.48) * mm, "end": v(114.18, -29.41) * mm});
            skLineSegment(sketch, "E3909", {"start": v(114.18, -29.41) * mm, "end": v(114.55, -29.35) * mm});
            skLineSegment(sketch, "E3910", {"start": v(114.55, -29.35) * mm, "end": v(114.93, -29.28) * mm});
            skLineSegment(sketch, "E3911", {"start": v(114.93, -29.28) * mm, "end": v(115.32, -29.2) * mm});
            skLineSegment(sketch, "E3912", {"start": v(115.32, -29.2) * mm, "end": v(115.71, -29.12) * mm});
            skLineSegment(sketch, "E3913", {"start": v(115.71, -29.12) * mm, "end": v(115.86, -28.98) * mm});
            skLineSegment(sketch, "E3914", {"start": v(115.86, -28.98) * mm, "end": v(116.66, -25.56) * mm});
            skLineSegment(sketch, "E3915", {"start": v(116.66, -25.56) * mm, "end": v(116.6, -25.36) * mm});
            skLineSegment(sketch, "E3916", {"start": v(116.6, -25.36) * mm, "end": v(116.28, -25.12) * mm});
            skLineSegment(sketch, "E3917", {"start": v(116.28, -25.12) * mm, "end": v(115.96, -24.88) * mm});
            skLineSegment(sketch, "E3918", {"start": v(115.96, -24.88) * mm, "end": v(115.65, -24.65) * mm});
            skLineSegment(sketch, "E3919", {"start": v(115.65, -24.65) * mm, "end": v(115.35, -24.42) * mm});
            skLineSegment(sketch, "E3920", {"start": v(115.35, -24.42) * mm, "end": v(115.05, -24.2) * mm});
            skLineSegment(sketch, "E3921", {"start": v(115.05, -24.2) * mm, "end": v(114.75, -23.99) * mm});
            skLineSegment(sketch, "E3922", {"start": v(114.75, -23.99) * mm, "end": v(114.46, -23.78) * mm});
            skLineSegment(sketch, "E3923", {"start": v(114.46, -23.78) * mm, "end": v(114.16, -23.58) * mm});
            skLineSegment(sketch, "E3924", {"start": v(114.16, -23.58) * mm, "end": v(113.88, -23.38) * mm});
            skLineSegment(sketch, "E3925", {"start": v(113.88, -23.38) * mm, "end": v(113.6, -23.2) * mm});
            skLineSegment(sketch, "E3926", {"start": v(113.6, -23.2) * mm, "end": v(113.31, -23.01) * mm});
            skLineSegment(sketch, "E3927", {"start": v(113.31, -23.01) * mm, "end": v(113.04, -22.83) * mm});
            skLineSegment(sketch, "E3928", {"start": v(113.04, -22.83) * mm, "end": v(112.77, -22.66) * mm});
            skLineSegment(sketch, "E3929", {"start": v(112.77, -22.66) * mm, "end": v(112.5, -22.5) * mm});
            skLineSegment(sketch, "E3930", {"start": v(112.5, -22.5) * mm, "end": v(112.24, -22.33) * mm});
            skLineSegment(sketch, "E3931", {"start": v(112.24, -22.33) * mm, "end": v(111.98, -22.18) * mm});
            skLineSegment(sketch, "E3932", {"start": v(111.98, -22.18) * mm, "end": v(111.72, -22.02) * mm});
            skLineSegment(sketch, "E3933", {"start": v(111.72, -22.02) * mm, "end": v(111.48, -21.88) * mm});
            skLineSegment(sketch, "E3934", {"start": v(111.48, -21.88) * mm, "end": v(111.23, -21.74) * mm});
            skLineSegment(sketch, "E3935", {"start": v(111.23, -21.74) * mm, "end": v(110.99, -21.6) * mm});
            skLineSegment(sketch, "E3936", {"start": v(110.99, -21.6) * mm, "end": v(110.75, -21.47) * mm});
            skLineSegment(sketch, "E3937", {"start": v(110.75, -21.47) * mm, "end": v(110.52, -21.35) * mm});
            skLineSegment(sketch, "E3938", {"start": v(110.52, -21.35) * mm, "end": v(110.3, -21.23) * mm});
            skLineSegment(sketch, "E3939", {"start": v(110.3, -21.23) * mm, "end": v(110.07, -21.1) * mm});
            skLineSegment(sketch, "E3940", {"start": v(110.07, -21.1) * mm, "end": v(109.85, -21) * mm});
            skLineSegment(sketch, "E3941", {"start": v(109.85, -21) * mm, "end": v(109.64, -20.9) * mm});
            skLineSegment(sketch, "E3942", {"start": v(109.64, -20.9) * mm, "end": v(109.44, -20.8) * mm});
            skLineSegment(sketch, "E3943", {"start": v(109.44, -20.8) * mm, "end": v(109.23, -20.7) * mm});
            skLineSegment(sketch, "E3944", {"start": v(109.23, -20.7) * mm, "end": v(109.04, -20.6) * mm});
            skLineSegment(sketch, "E3945", {"start": v(109.04, -20.6) * mm, "end": v(108.84, -20.5) * mm});
            skLineSegment(sketch, "E3946", {"start": v(108.84, -20.5) * mm, "end": v(108.66, -20.42) * mm});
            skLineSegment(sketch, "E3947", {"start": v(108.66, -20.42) * mm, "end": v(108.48, -20.34) * mm});
            skLineSegment(sketch, "E3948", {"start": v(108.48, -20.34) * mm, "end": v(108.3, -20.27) * mm});
            skLineSegment(sketch, "E3949", {"start": v(108.3, -20.27) * mm, "end": v(108.13, -20.2) * mm});
            skLineSegment(sketch, "E3950", {"start": v(108.13, -20.2) * mm, "end": v(107.96, -20.12) * mm});
            skLineSegment(sketch, "E3951", {"start": v(107.96, -20.12) * mm, "end": v(107.8, -20.06) * mm});
            skLineSegment(sketch, "E3952", {"start": v(107.8, -20.06) * mm, "end": v(107.65, -20) * mm});
            skLineSegment(sketch, "E3953", {"start": v(107.65, -20) * mm, "end": v(107.5, -19.94) * mm});
            skLineSegment(sketch, "E3954", {"start": v(107.5, -19.94) * mm, "end": v(107.36, -19.88) * mm});
            skLineSegment(sketch, "E3955", {"start": v(107.36, -19.88) * mm, "end": v(107.22, -19.83) * mm});
            skLineSegment(sketch, "E3956", {"start": v(107.22, -19.83) * mm, "end": v(107.09, -19.78) * mm});
            skLineSegment(sketch, "E3957", {"start": v(107.09, -19.78) * mm, "end": v(106.96, -19.74) * mm});
            skLineSegment(sketch, "E3958", {"start": v(106.96, -19.74) * mm, "end": v(106.72, -19.56) * mm});
            skLineSegment(sketch, "E3959", {"start": v(106.72, -19.56) * mm, "end": v(107.44, -15.14) * mm});
            skLineSegment(sketch, "E3960", {"start": v(107.44, -15.14) * mm, "end": v(107.72, -15.04) * mm});
            skLineSegment(sketch, "E3961", {"start": v(107.72, -15.04) * mm, "end": v(107.85, -15.04) * mm});
            skLineSegment(sketch, "E3962", {"start": v(107.85, -15.04) * mm, "end": v(108, -15.04) * mm});
            skLineSegment(sketch, "E3963", {"start": v(108, -15.04) * mm, "end": v(108.14, -15.03) * mm});
            skLineSegment(sketch, "E3964", {"start": v(108.14, -15.03) * mm, "end": v(108.3, -15.02) * mm});
            skLineSegment(sketch, "E3965", {"start": v(108.3, -15.02) * mm, "end": v(108.45, -15.02) * mm});
            skLineSegment(sketch, "E3966", {"start": v(108.45, -15.02) * mm, "end": v(108.62, -15) * mm});
            skLineSegment(sketch, "E3967", {"start": v(108.62, -15) * mm, "end": v(108.8, -15) * mm});
            skLineSegment(sketch, "E3968", {"start": v(108.8, -15) * mm, "end": v(108.97, -14.98) * mm});
            skLineSegment(sketch, "E3969", {"start": v(108.97, -14.98) * mm, "end": v(109.16, -14.97) * mm});
            skLineSegment(sketch, "E3970", {"start": v(109.16, -14.97) * mm, "end": v(109.35, -14.95) * mm});
            skLineSegment(sketch, "E3971", {"start": v(109.35, -14.95) * mm, "end": v(109.55, -14.93) * mm});
            skLineSegment(sketch, "E3972", {"start": v(109.55, -14.93) * mm, "end": v(109.75, -14.9) * mm});
            skLineSegment(sketch, "E3973", {"start": v(109.75, -14.9) * mm, "end": v(109.96, -14.88) * mm});
            skLineSegment(sketch, "E3974", {"start": v(109.96, -14.88) * mm, "end": v(110.18, -14.86) * mm});
            skLineSegment(sketch, "E3975", {"start": v(110.18, -14.86) * mm, "end": v(110.4, -14.83) * mm});
            skLineSegment(sketch, "E3976", {"start": v(110.4, -14.83) * mm, "end": v(110.63, -14.8) * mm});
            skLineSegment(sketch, "E3977", {"start": v(110.63, -14.8) * mm, "end": v(110.86, -14.76) * mm});
            skLineSegment(sketch, "E3978", {"start": v(110.86, -14.76) * mm, "end": v(111.1, -14.72) * mm});
            skLineSegment(sketch, "E3979", {"start": v(111.1, -14.72) * mm, "end": v(111.35, -14.68) * mm});
            skLineSegment(sketch, "E3980", {"start": v(111.35, -14.68) * mm, "end": v(111.6, -14.64) * mm});
            skLineSegment(sketch, "E3981", {"start": v(111.6, -14.64) * mm, "end": v(111.86, -14.6) * mm});
            skLineSegment(sketch, "E3982", {"start": v(111.86, -14.6) * mm, "end": v(112.13, -14.54) * mm});
            skLineSegment(sketch, "E3983", {"start": v(112.13, -14.54) * mm, "end": v(112.4, -14.5) * mm});
            skLineSegment(sketch, "E3984", {"start": v(112.4, -14.5) * mm, "end": v(112.68, -14.44) * mm});
            skLineSegment(sketch, "E3985", {"start": v(112.68, -14.44) * mm, "end": v(112.96, -14.38) * mm});
            skLineSegment(sketch, "E3986", {"start": v(112.96, -14.38) * mm, "end": v(113.25, -14.31) * mm});
            skLineSegment(sketch, "E3987", {"start": v(113.25, -14.31) * mm, "end": v(113.54, -14.25) * mm});
            skLineSegment(sketch, "E3988", {"start": v(113.54, -14.25) * mm, "end": v(113.84, -14.17) * mm});
            skLineSegment(sketch, "E3989", {"start": v(113.84, -14.17) * mm, "end": v(114.15, -14.1) * mm});
            skLineSegment(sketch, "E3990", {"start": v(114.15, -14.1) * mm, "end": v(114.46, -14.02) * mm});
            skLineSegment(sketch, "E3991", {"start": v(114.46, -14.02) * mm, "end": v(114.78, -13.94) * mm});
            skLineSegment(sketch, "E3992", {"start": v(114.78, -13.94) * mm, "end": v(115.1, -13.85) * mm});
            skLineSegment(sketch, "E3993", {"start": v(115.1, -13.85) * mm, "end": v(115.43, -13.76) * mm});
            skLineSegment(sketch, "E3994", {"start": v(115.43, -13.76) * mm, "end": v(115.77, -13.67) * mm});
            skLineSegment(sketch, "E3995", {"start": v(115.77, -13.67) * mm, "end": v(116.1, -13.57) * mm});
            skLineSegment(sketch, "E3996", {"start": v(116.1, -13.57) * mm, "end": v(116.45, -13.46) * mm});
            skLineSegment(sketch, "E3997", {"start": v(116.45, -13.46) * mm, "end": v(116.8, -13.36) * mm});
            skLineSegment(sketch, "E3998", {"start": v(116.8, -13.36) * mm, "end": v(117.16, -13.24) * mm});
            skLineSegment(sketch, "E3999", {"start": v(117.16, -13.24) * mm, "end": v(117.52, -13.12) * mm});
            skLineSegment(sketch, "E4000", {"start": v(117.52, -13.12) * mm, "end": v(117.88, -13) * mm});
            skLineSegment(sketch, "E4001", {"start": v(117.88, -13) * mm, "end": v(118.25, -12.87) * mm});
            skLineSegment(sketch, "E4002", {"start": v(118.25, -12.87) * mm, "end": v(118.63, -12.74) * mm});
            skLineSegment(sketch, "E4003", {"start": v(118.63, -12.74) * mm, "end": v(118.76, -12.58) * mm});
            skLineSegment(sketch, "E4004", {"start": v(118.76, -12.58) * mm, "end": v(119.07, -9.08) * mm});
            skLineSegment(sketch, "E4005", {"start": v(119.07, -9.08) * mm, "end": v(118.98, -8.9) * mm});
            skLineSegment(sketch, "E4006", {"start": v(118.98, -8.9) * mm, "end": v(118.63, -8.7) * mm});
            skLineSegment(sketch, "E4007", {"start": v(118.63, -8.7) * mm, "end": v(118.3, -8.5) * mm});
            skLineSegment(sketch, "E4008", {"start": v(118.3, -8.5) * mm, "end": v(117.95, -8.32) * mm});
            skLineSegment(sketch, "E4009", {"start": v(117.95, -8.32) * mm, "end": v(117.62, -8.14) * mm});
            skLineSegment(sketch, "E4010", {"start": v(117.62, -8.14) * mm, "end": v(117.29, -7.96) * mm});
            skLineSegment(sketch, "E4011", {"start": v(117.29, -7.96) * mm, "end": v(116.96, -7.8) * mm});
            skLineSegment(sketch, "E4012", {"start": v(116.96, -7.8) * mm, "end": v(116.64, -7.63) * mm});
            skLineSegment(sketch, "E4013", {"start": v(116.64, -7.63) * mm, "end": v(116.33, -7.47) * mm});
            skLineSegment(sketch, "E4014", {"start": v(116.33, -7.47) * mm, "end": v(116.02, -7.31) * mm});
            skLineSegment(sketch, "E4015", {"start": v(116.02, -7.31) * mm, "end": v(115.7, -7.17) * mm});
            skLineSegment(sketch, "E4016", {"start": v(115.7, -7.17) * mm, "end": v(115.4, -7.02) * mm});
            skLineSegment(sketch, "E4017", {"start": v(115.4, -7.02) * mm, "end": v(115.1, -6.88) * mm});
            skLineSegment(sketch, "E4018", {"start": v(115.1, -6.88) * mm, "end": v(114.82, -6.75) * mm});
            skLineSegment(sketch, "E4019", {"start": v(114.82, -6.75) * mm, "end": v(114.53, -6.62) * mm});
            skLineSegment(sketch, "E4020", {"start": v(114.53, -6.62) * mm, "end": v(114.25, -6.5) * mm});
            skLineSegment(sketch, "E4021", {"start": v(114.25, -6.5) * mm, "end": v(113.97, -6.38) * mm});
            skLineSegment(sketch, "E4022", {"start": v(113.97, -6.38) * mm, "end": v(113.7, -6.27) * mm});
            skLineSegment(sketch, "E4023", {"start": v(113.7, -6.27) * mm, "end": v(113.43, -6.16) * mm});
            skLineSegment(sketch, "E4024", {"start": v(113.43, -6.16) * mm, "end": v(113.17, -6.05) * mm});
            skLineSegment(sketch, "E4025", {"start": v(113.17, -6.05) * mm, "end": v(112.9, -5.95) * mm});
            skLineSegment(sketch, "E4026", {"start": v(112.9, -5.95) * mm, "end": v(112.66, -5.85) * mm});
            skLineSegment(sketch, "E4027", {"start": v(112.66, -5.85) * mm, "end": v(112.41, -5.76) * mm});
            skLineSegment(sketch, "E4028", {"start": v(112.41, -5.76) * mm, "end": v(112.17, -5.68) * mm});
            skLineSegment(sketch, "E4029", {"start": v(112.17, -5.68) * mm, "end": v(111.93, -5.6) * mm});
            skLineSegment(sketch, "E4030", {"start": v(111.93, -5.6) * mm, "end": v(111.7, -5.51) * mm});
            skLineSegment(sketch, "E4031", {"start": v(111.7, -5.51) * mm, "end": v(111.48, -5.43) * mm});
            skLineSegment(sketch, "E4032", {"start": v(111.48, -5.43) * mm, "end": v(111.26, -5.36) * mm});
            skLineSegment(sketch, "E4033", {"start": v(111.26, -5.36) * mm, "end": v(111.04, -5.3) * mm});
            skLineSegment(sketch, "E4034", {"start": v(111.04, -5.3) * mm, "end": v(110.83, -5.23) * mm});
            skLineSegment(sketch, "E4035", {"start": v(110.83, -5.23) * mm, "end": v(110.63, -5.17) * mm});
            skLineSegment(sketch, "E4036", {"start": v(110.63, -5.17) * mm, "end": v(110.44, -5.1) * mm});
            skLineSegment(sketch, "E4037", {"start": v(110.44, -5.1) * mm, "end": v(110.25, -5.05) * mm});
            skLineSegment(sketch, "E4038", {"start": v(110.25, -5.05) * mm, "end": v(110.06, -5) * mm});
            skLineSegment(sketch, "E4039", {"start": v(110.06, -5) * mm, "end": v(109.88, -4.95) * mm});
            skLineSegment(sketch, "E4040", {"start": v(109.88, -4.95) * mm, "end": v(109.7, -4.9) * mm});
            skLineSegment(sketch, "E4041", {"start": v(109.7, -4.9) * mm, "end": v(109.54, -4.87) * mm});
            skLineSegment(sketch, "E4042", {"start": v(109.54, -4.87) * mm, "end": v(109.38, -4.83) * mm});
            skLineSegment(sketch, "E4043", {"start": v(109.38, -4.83) * mm, "end": v(109.22, -4.79) * mm});
            skLineSegment(sketch, "E4044", {"start": v(109.22, -4.79) * mm, "end": v(109.07, -4.75) * mm});
            skLineSegment(sketch, "E4045", {"start": v(109.07, -4.75) * mm, "end": v(108.93, -4.72) * mm});
            skLineSegment(sketch, "E4046", {"start": v(108.93, -4.72) * mm, "end": v(108.8, -4.7) * mm});
            skLineSegment(sketch, "E4047", {"start": v(108.8, -4.7) * mm, "end": v(108.66, -4.67) * mm});
            skLineSegment(sketch, "E4048", {"start": v(108.66, -4.67) * mm, "end": v(108.4, -4.52) * mm});
            skLineSegment(sketch, "E4049", {"start": v(108.4, -4.52) * mm, "end": v(108.5, -0.05) * mm});
            skSolve(sketch);
        }
        {
            var Q0;
            Q0 = qSketchRegion(id + "F0", true);
            extrude(context, id + "F1", {"entities" : qUnion([Q0]), "depth" : 6.35 * mm});
        }
        {
            var Q0;
            Q0=qCreatedBy(makeId("Top.planeOp"),FACE);
            var sketch = newSketch(context, id + "F2", { "sketchPlane" : qUnion([Q0])});
            skCircle(sketch, "E4050", {"center": v(0, 0) * mm, "radius": 9.33 * mm, "construction": true});
            skLineSegment(sketch, "E4051.bottom", {"start": v(-2.29, 9.05) * mm, "end": v(2.29, 9.05) * mm, "construction": true});
            skLineSegment(sketch, "E4051.top", {"start": v(-2.29, 7.05) * mm, "end": v(2.29, 7.05) * mm});
            skLineSegment(sketch, "E4051.left", {"start": v(-2.29, 9.05) * mm, "end": v(-2.29, 7.05) * mm});
            skLineSegment(sketch, "E4051.right", {"start": v(2.29, 9.05) * mm, "end": v(2.29, 7.05) * mm});
            skArc(sketch, "E4052", {"start": v(-2.29, 9.05) * mm, "mid": v(0, -9.33) * mm, "end": v(2.29, 9.05) * mm});
            skSolve(sketch);
        }
        {
            var Q0;
            Q0 = qSketchRegion(id + "F2", true);
            extrude(context, id + "F3", {"entities" : qUnion([Q0]), "operationType" : NewBodyOperationType.REMOVE, "endBound" : BoundingType.THROUGH_ALL, "depth" : 25.4 * mm});
        }
        {
            var Q0;
            Q0=qCreatedBy(makeId("Top.planeOp"),FACE);
            var sketch = newSketch(context, id + "F4", { "sketchPlane" : qUnion([Q0])});
            skCircle(sketch, "E4053", {"center": v(0, 0) * mm, "radius": 76.2 * mm, "construction": true});
            skCircle(sketch, "E4054", {"center": v(-76.2, 0) * mm, "radius": 3.5 * mm});
            skCircle(sketch, "E4055", {"center": v(76.2, 0) * mm, "radius": 3.5 * mm});
            skCircle(sketch, "E4056", {"center": v(-38.1, 66) * mm, "radius": 3.5 * mm});
            skCircle(sketch, "E4057", {"center": v(38.1, 66) * mm, "radius": 3.5 * mm});
            skCircle(sketch, "E4058", {"center": v(-38.1, -66) * mm, "radius": 3.5 * mm});
            skCircle(sketch, "E4059", {"center": v(38.1, -66) * mm, "radius": 3.5 * mm});
            skLineSegment(sketch, "E4060", {"start": v(-76.2, 0) * mm, "end": v(-38.1, 66) * mm, "construction": true});
            skLineSegment(sketch, "E4061", {"start": v(-38.1, 66) * mm, "end": v(38.1, 66) * mm, "construction": true});
            skLineSegment(sketch, "E4062", {"start": v(38.1, 66) * mm, "end": v(76.2, 0) * mm, "construction": true});
            skLineSegment(sketch, "E4063", {"start": v(76.2, 0) * mm, "end": v(38.1, -66) * mm, "construction": true});
            skLineSegment(sketch, "E4064", {"start": v(38.1, -66) * mm, "end": v(-38.1, -66) * mm, "construction": true});
            skLineSegment(sketch, "E4065", {"start": v(-38.1, -66) * mm, "end": v(-76.2, 0) * mm, "construction": true});
            skSolve(sketch);
        }
        {
            var Q0;
            Q0 = qSketchRegion(id + "F4", true);
            extrude(context, id + "F5", {"entities" : qUnion([Q0]), "operationType" : NewBodyOperationType.REMOVE, "endBound" : BoundingType.THROUGH_ALL, "depth" : 25.4 * mm});
        }
        {
            var Q0;
            Q0=qCreatedBy(makeId("Top.planeOp"),FACE);
            var sketch = newSketch(context, id + "F6", { "sketchPlane" : qUnion([Q0])});
            skCircle(sketch, "E4066", {"center": v(0, 0) * mm, "radius": 101.6 * mm});
            skSolve(sketch);
        }
        {
            var Q0;
            Q0 = qSketchRegion(id + "F6", true);
            extrude(context, id + "F7", {"entities" : qUnion([Q0]), "oppositeDirection" : true, "depth" : 3.17 * mm});
        }
        {
            var Q0;
            Q0 = qSketchRegion(id + "F2", true);
            extrude(context, id + "F8", {"entities" : qUnion([Q0]), "operationType" : NewBodyOperationType.REMOVE, "oppositeDirection" : true, "depth" : 25.4 * mm});
        }
        {
            var Q0;
            Q0=makeQuery(id+"F1.opExtrude","CAP_FACE",FACE,{"disambiguationData":[OSD([sQuery(id+"F0.wireOp",EDGE,"E0"),sQuery(id+"F0.wireOp",EDGE,"E1"),sQuery(id+"F0.wireOp",EDGE,"E2"),sQuery(id+"F0.wireOp",EDGE,"E3"),sQuery(id+"F0.wireOp",EDGE,"E4"),sQuery(id+"F0.wireOp",EDGE,"E5"),sQuery(id+"F0.wireOp",EDGE,"E6"),sQuery(id+"F0.wireOp",EDGE,"E7"),sQuery(id+"F0.wireOp",EDGE,"E8"),sQuery(id+"F0.wireOp",EDGE,"E9"),sQuery(id+"F0.wireOp",EDGE,"E10"),sQuery(id+"F0.wireOp",EDGE,"E11"),sQuery(id+"F0.wireOp",EDGE,"E12"),sQuery(id+"F0.wireOp",EDGE,"E13"),sQuery(id+"F0.wireOp",EDGE,"E14"),sQuery(id+"F0.wireOp",EDGE,"E15"),sQuery(id+"F0.wireOp",EDGE,"E16"),sQuery(id+"F0.wireOp",EDGE,"E17"),sQuery(id+"F0.wireOp",EDGE,"E18"),sQuery(id+"F0.wireOp",EDGE,"E19"),sQuery(id+"F0.wireOp",EDGE,"E20"),sQuery(id+"F0.wireOp",EDGE,"E21"),sQuery(id+"F0.wireOp",EDGE,"E22"),sQuery(id+"F0.wireOp",EDGE,"E23"),sQuery(id+"F0.wireOp",EDGE,"E24"),sQuery(id+"F0.wireOp",EDGE,"E25"),sQuery(id+"F0.wireOp",EDGE,"E26"),sQuery(id+"F0.wireOp",EDGE,"E27"),sQuery(id+"F0.wireOp",EDGE,"E28"),sQuery(id+"F0.wireOp",EDGE,"E29"),sQuery(id+"F0.wireOp",EDGE,"E30"),sQuery(id+"F0.wireOp",EDGE,"E31"),sQuery(id+"F0.wireOp",EDGE,"E32"),sQuery(id+"F0.wireOp",EDGE,"E33"),sQuery(id+"F0.wireOp",EDGE,"E34"),sQuery(id+"F0.wireOp",EDGE,"E35"),sQuery(id+"F0.wireOp",EDGE,"E36"),sQuery(id+"F0.wireOp",EDGE,"E37"),sQuery(id+"F0.wireOp",EDGE,"E38"),sQuery(id+"F0.wireOp",EDGE,"E39"),sQuery(id+"F0.wireOp",EDGE,"E40"),sQuery(id+"F0.wireOp",EDGE,"E41"),sQuery(id+"F0.wireOp",EDGE,"E42"),sQuery(id+"F0.wireOp",EDGE,"E43"),sQuery(id+"F0.wireOp",EDGE,"E44"),sQuery(id+"F0.wireOp",EDGE,"E45"),sQuery(id+"F0.wireOp",EDGE,"E46"),sQuery(id+"F0.wireOp",EDGE,"E47"),sQuery(id+"F0.wireOp",EDGE,"E48"),sQuery(id+"F0.wireOp",EDGE,"E49"),sQuery(id+"F0.wireOp",EDGE,"E50"),sQuery(id+"F0.wireOp",EDGE,"E51"),sQuery(id+"F0.wireOp",EDGE,"E52"),sQuery(id+"F0.wireOp",EDGE,"E53"),sQuery(id+"F0.wireOp",EDGE,"E54"),sQuery(id+"F0.wireOp",EDGE,"E55"),sQuery(id+"F0.wireOp",EDGE,"E56"),sQuery(id+"F0.wireOp",EDGE,"E57"),sQuery(id+"F0.wireOp",EDGE,"E58"),sQuery(id+"F0.wireOp",EDGE,"E59"),sQuery(id+"F0.wireOp",EDGE,"E60"),sQuery(id+"F0.wireOp",EDGE,"E61"),sQuery(id+"F0.wireOp",EDGE,"E62"),sQuery(id+"F0.wireOp",EDGE,"E63"),sQuery(id+"F0.wireOp",EDGE,"E64"),sQuery(id+"F0.wireOp",EDGE,"E65"),sQuery(id+"F0.wireOp",EDGE,"E66"),sQuery(id+"F0.wireOp",EDGE,"E67"),sQuery(id+"F0.wireOp",EDGE,"E68"),sQuery(id+"F0.wireOp",EDGE,"E69"),sQuery(id+"F0.wireOp",EDGE,"E70"),sQuery(id+"F0.wireOp",EDGE,"E71"),sQuery(id+"F0.wireOp",EDGE,"E72"),sQuery(id+"F0.wireOp",EDGE,"E73"),sQuery(id+"F0.wireOp",EDGE,"E74"),sQuery(id+"F0.wireOp",EDGE,"E75"),sQuery(id+"F0.wireOp",EDGE,"E76"),sQuery(id+"F0.wireOp",EDGE,"E77"),sQuery(id+"F0.wireOp",EDGE,"E78"),sQuery(id+"F0.wireOp",EDGE,"E79"),sQuery(id+"F0.wireOp",EDGE,"E80"),sQuery(id+"F0.wireOp",EDGE,"E81"),sQuery(id+"F0.wireOp",EDGE,"E82"),sQuery(id+"F0.wireOp",EDGE,"E83"),sQuery(id+"F0.wireOp",EDGE,"E84"),sQuery(id+"F0.wireOp",EDGE,"E85"),sQuery(id+"F0.wireOp",EDGE,"E86"),sQuery(id+"F0.wireOp",EDGE,"E87"),sQuery(id+"F0.wireOp",EDGE,"E88"),sQuery(id+"F0.wireOp",EDGE,"E89"),sQuery(id+"F0.wireOp",EDGE,"E90"),sQuery(id+"F0.wireOp",EDGE,"E91"),sQuery(id+"F0.wireOp",EDGE,"E92"),sQuery(id+"F0.wireOp",EDGE,"E93"),sQuery(id+"F0.wireOp",EDGE,"E94"),sQuery(id+"F0.wireOp",EDGE,"E95"),sQuery(id+"F0.wireOp",EDGE,"E96"),sQuery(id+"F0.wireOp",EDGE,"E97"),sQuery(id+"F0.wireOp",EDGE,"E98"),sQuery(id+"F0.wireOp",EDGE,"E99"),sQuery(id+"F0.wireOp",EDGE,"E100"),sQuery(id+"F0.wireOp",EDGE,"E101"),sQuery(id+"F0.wireOp",EDGE,"E102"),sQuery(id+"F0.wireOp",EDGE,"E103"),sQuery(id+"F0.wireOp",EDGE,"E104"),sQuery(id+"F0.wireOp",EDGE,"E105"),sQuery(id+"F0.wireOp",EDGE,"E106"),sQuery(id+"F0.wireOp",EDGE,"E107"),sQuery(id+"F0.wireOp",EDGE,"E108"),sQuery(id+"F0.wireOp",EDGE,"E109"),sQuery(id+"F0.wireOp",EDGE,"E110"),sQuery(id+"F0.wireOp",EDGE,"E111"),sQuery(id+"F0.wireOp",EDGE,"E112"),sQuery(id+"F0.wireOp",EDGE,"E113"),sQuery(id+"F0.wireOp",EDGE,"E114"),sQuery(id+"F0.wireOp",EDGE,"E115"),sQuery(id+"F0.wireOp",EDGE,"E116"),sQuery(id+"F0.wireOp",EDGE,"E117"),sQuery(id+"F0.wireOp",EDGE,"E118"),sQuery(id+"F0.wireOp",EDGE,"E119"),sQuery(id+"F0.wireOp",EDGE,"E120"),sQuery(id+"F0.wireOp",EDGE,"E121"),sQuery(id+"F0.wireOp",EDGE,"E122"),sQuery(id+"F0.wireOp",EDGE,"E123"),sQuery(id+"F0.wireOp",EDGE,"E124"),sQuery(id+"F0.wireOp",EDGE,"E125"),sQuery(id+"F0.wireOp",EDGE,"E126"),sQuery(id+"F0.wireOp",EDGE,"E127"),sQuery(id+"F0.wireOp",EDGE,"E128"),sQuery(id+"F0.wireOp",EDGE,"E129"),sQuery(id+"F0.wireOp",EDGE,"E130"),sQuery(id+"F0.wireOp",EDGE,"E131"),sQuery(id+"F0.wireOp",EDGE,"E132"),sQuery(id+"F0.wireOp",EDGE,"E133"),sQuery(id+"F0.wireOp",EDGE,"E134"),sQuery(id+"F0.wireOp",EDGE,"E135"),sQuery(id+"F0.wireOp",EDGE,"E136"),sQuery(id+"F0.wireOp",EDGE,"E137"),sQuery(id+"F0.wireOp",EDGE,"E138"),sQuery(id+"F0.wireOp",EDGE,"E139"),sQuery(id+"F0.wireOp",EDGE,"E140"),sQuery(id+"F0.wireOp",EDGE,"E141"),sQuery(id+"F0.wireOp",EDGE,"E142"),sQuery(id+"F0.wireOp",EDGE,"E143"),sQuery(id+"F0.wireOp",EDGE,"E144"),sQuery(id+"F0.wireOp",EDGE,"E145"),sQuery(id+"F0.wireOp",EDGE,"E146"),sQuery(id+"F0.wireOp",EDGE,"E147"),sQuery(id+"F0.wireOp",EDGE,"E148"),sQuery(id+"F0.wireOp",EDGE,"E149"),sQuery(id+"F0.wireOp",EDGE,"E150"),sQuery(id+"F0.wireOp",EDGE,"E151"),sQuery(id+"F0.wireOp",EDGE,"E152"),sQuery(id+"F0.wireOp",EDGE,"E153"),sQuery(id+"F0.wireOp",EDGE,"E154"),sQuery(id+"F0.wireOp",EDGE,"E155"),sQuery(id+"F0.wireOp",EDGE,"E156"),sQuery(id+"F0.wireOp",EDGE,"E157"),sQuery(id+"F0.wireOp",EDGE,"E158"),sQuery(id+"F0.wireOp",EDGE,"E159"),sQuery(id+"F0.wireOp",EDGE,"E160"),sQuery(id+"F0.wireOp",EDGE,"E161"),sQuery(id+"F0.wireOp",EDGE,"E162"),sQuery(id+"F0.wireOp",EDGE,"E163"),sQuery(id+"F0.wireOp",EDGE,"E164"),sQuery(id+"F0.wireOp",EDGE,"E165"),sQuery(id+"F0.wireOp",EDGE,"E166"),sQuery(id+"F0.wireOp",EDGE,"E167"),sQuery(id+"F0.wireOp",EDGE,"E168"),sQuery(id+"F0.wireOp",EDGE,"E169"),sQuery(id+"F0.wireOp",EDGE,"E170"),sQuery(id+"F0.wireOp",EDGE,"E171"),sQuery(id+"F0.wireOp",EDGE,"E172"),sQuery(id+"F0.wireOp",EDGE,"E173"),sQuery(id+"F0.wireOp",EDGE,"E174"),sQuery(id+"F0.wireOp",EDGE,"E175"),sQuery(id+"F0.wireOp",EDGE,"E176"),sQuery(id+"F0.wireOp",EDGE,"E177"),sQuery(id+"F0.wireOp",EDGE,"E178"),sQuery(id+"F0.wireOp",EDGE,"E179"),sQuery(id+"F0.wireOp",EDGE,"E180"),sQuery(id+"F0.wireOp",EDGE,"E181"),sQuery(id+"F0.wireOp",EDGE,"E182"),sQuery(id+"F0.wireOp",EDGE,"E183"),sQuery(id+"F0.wireOp",EDGE,"E184"),sQuery(id+"F0.wireOp",EDGE,"E185"),sQuery(id+"F0.wireOp",EDGE,"E186"),sQuery(id+"F0.wireOp",EDGE,"E187"),sQuery(id+"F0.wireOp",EDGE,"E188"),sQuery(id+"F0.wireOp",EDGE,"E189"),sQuery(id+"F0.wireOp",EDGE,"E190"),sQuery(id+"F0.wireOp",EDGE,"E191"),sQuery(id+"F0.wireOp",EDGE,"E192"),sQuery(id+"F0.wireOp",EDGE,"E193"),sQuery(id+"F0.wireOp",EDGE,"E194"),sQuery(id+"F0.wireOp",EDGE,"E195"),sQuery(id+"F0.wireOp",EDGE,"E196"),sQuery(id+"F0.wireOp",EDGE,"E197"),sQuery(id+"F0.wireOp",EDGE,"E198"),sQuery(id+"F0.wireOp",EDGE,"E199"),sQuery(id+"F0.wireOp",EDGE,"E200"),sQuery(id+"F0.wireOp",EDGE,"E201"),sQuery(id+"F0.wireOp",EDGE,"E202"),sQuery(id+"F0.wireOp",EDGE,"E203"),sQuery(id+"F0.wireOp",EDGE,"E204"),sQuery(id+"F0.wireOp",EDGE,"E205"),sQuery(id+"F0.wireOp",EDGE,"E206"),sQuery(id+"F0.wireOp",EDGE,"E207"),sQuery(id+"F0.wireOp",EDGE,"E208"),sQuery(id+"F0.wireOp",EDGE,"E209"),sQuery(id+"F0.wireOp",EDGE,"E210"),sQuery(id+"F0.wireOp",EDGE,"E211"),sQuery(id+"F0.wireOp",EDGE,"E212"),sQuery(id+"F0.wireOp",EDGE,"E213"),sQuery(id+"F0.wireOp",EDGE,"E214"),sQuery(id+"F0.wireOp",EDGE,"E215"),sQuery(id+"F0.wireOp",EDGE,"E216"),sQuery(id+"F0.wireOp",EDGE,"E217"),sQuery(id+"F0.wireOp",EDGE,"E218"),sQuery(id+"F0.wireOp",EDGE,"E219"),sQuery(id+"F0.wireOp",EDGE,"E220"),sQuery(id+"F0.wireOp",EDGE,"E221"),sQuery(id+"F0.wireOp",EDGE,"E222"),sQuery(id+"F0.wireOp",EDGE,"E223"),sQuery(id+"F0.wireOp",EDGE,"E224"),sQuery(id+"F0.wireOp",EDGE,"E225"),sQuery(id+"F0.wireOp",EDGE,"E226"),sQuery(id+"F0.wireOp",EDGE,"E227"),sQuery(id+"F0.wireOp",EDGE,"E228"),sQuery(id+"F0.wireOp",EDGE,"E229"),sQuery(id+"F0.wireOp",EDGE,"E230"),sQuery(id+"F0.wireOp",EDGE,"E231"),sQuery(id+"F0.wireOp",EDGE,"E232"),sQuery(id+"F0.wireOp",EDGE,"E233"),sQuery(id+"F0.wireOp",EDGE,"E234"),sQuery(id+"F0.wireOp",EDGE,"E235"),sQuery(id+"F0.wireOp",EDGE,"E236"),sQuery(id+"F0.wireOp",EDGE,"E237"),sQuery(id+"F0.wireOp",EDGE,"E238"),sQuery(id+"F0.wireOp",EDGE,"E239"),sQuery(id+"F0.wireOp",EDGE,"E240"),sQuery(id+"F0.wireOp",EDGE,"E241"),sQuery(id+"F0.wireOp",EDGE,"E242"),sQuery(id+"F0.wireOp",EDGE,"E243"),sQuery(id+"F0.wireOp",EDGE,"E244"),sQuery(id+"F0.wireOp",EDGE,"E245"),sQuery(id+"F0.wireOp",EDGE,"E246"),sQuery(id+"F0.wireOp",EDGE,"E247"),sQuery(id+"F0.wireOp",EDGE,"E248"),sQuery(id+"F0.wireOp",EDGE,"E249"),sQuery(id+"F0.wireOp",EDGE,"E250"),sQuery(id+"F0.wireOp",EDGE,"E251"),sQuery(id+"F0.wireOp",EDGE,"E252"),sQuery(id+"F0.wireOp",EDGE,"E253"),sQuery(id+"F0.wireOp",EDGE,"E254"),sQuery(id+"F0.wireOp",EDGE,"E255"),sQuery(id+"F0.wireOp",EDGE,"E256"),sQuery(id+"F0.wireOp",EDGE,"E257"),sQuery(id+"F0.wireOp",EDGE,"E258"),sQuery(id+"F0.wireOp",EDGE,"E259"),sQuery(id+"F0.wireOp",EDGE,"E260"),sQuery(id+"F0.wireOp",EDGE,"E261"),sQuery(id+"F0.wireOp",EDGE,"E262"),sQuery(id+"F0.wireOp",EDGE,"E263"),sQuery(id+"F0.wireOp",EDGE,"E264"),sQuery(id+"F0.wireOp",EDGE,"E265"),sQuery(id+"F0.wireOp",EDGE,"E266"),sQuery(id+"F0.wireOp",EDGE,"E267"),sQuery(id+"F0.wireOp",EDGE,"E268"),sQuery(id+"F0.wireOp",EDGE,"E269"),sQuery(id+"F0.wireOp",EDGE,"E270"),sQuery(id+"F0.wireOp",EDGE,"E271"),sQuery(id+"F0.wireOp",EDGE,"E272"),sQuery(id+"F0.wireOp",EDGE,"E273"),sQuery(id+"F0.wireOp",EDGE,"E274"),sQuery(id+"F0.wireOp",EDGE,"E275"),sQuery(id+"F0.wireOp",EDGE,"E276"),sQuery(id+"F0.wireOp",EDGE,"E277"),sQuery(id+"F0.wireOp",EDGE,"E278"),sQuery(id+"F0.wireOp",EDGE,"E279"),sQuery(id+"F0.wireOp",EDGE,"E280"),sQuery(id+"F0.wireOp",EDGE,"E281"),sQuery(id+"F0.wireOp",EDGE,"E282"),sQuery(id+"F0.wireOp",EDGE,"E283"),sQuery(id+"F0.wireOp",EDGE,"E284"),sQuery(id+"F0.wireOp",EDGE,"E285"),sQuery(id+"F0.wireOp",EDGE,"E286"),sQuery(id+"F0.wireOp",EDGE,"E287"),sQuery(id+"F0.wireOp",EDGE,"E288"),sQuery(id+"F0.wireOp",EDGE,"E289"),sQuery(id+"F0.wireOp",EDGE,"E290"),sQuery(id+"F0.wireOp",EDGE,"E291"),sQuery(id+"F0.wireOp",EDGE,"E292"),sQuery(id+"F0.wireOp",EDGE,"E293"),sQuery(id+"F0.wireOp",EDGE,"E294"),sQuery(id+"F0.wireOp",EDGE,"E295"),sQuery(id+"F0.wireOp",EDGE,"E296"),sQuery(id+"F0.wireOp",EDGE,"E297"),sQuery(id+"F0.wireOp",EDGE,"E298"),sQuery(id+"F0.wireOp",EDGE,"E299"),sQuery(id+"F0.wireOp",EDGE,"E300"),sQuery(id+"F0.wireOp",EDGE,"E301"),sQuery(id+"F0.wireOp",EDGE,"E302"),sQuery(id+"F0.wireOp",EDGE,"E303"),sQuery(id+"F0.wireOp",EDGE,"E304"),sQuery(id+"F0.wireOp",EDGE,"E305"),sQuery(id+"F0.wireOp",EDGE,"E306"),sQuery(id+"F0.wireOp",EDGE,"E307"),sQuery(id+"F0.wireOp",EDGE,"E308"),sQuery(id+"F0.wireOp",EDGE,"E309"),sQuery(id+"F0.wireOp",EDGE,"E310"),sQuery(id+"F0.wireOp",EDGE,"E311"),sQuery(id+"F0.wireOp",EDGE,"E312"),sQuery(id+"F0.wireOp",EDGE,"E313"),sQuery(id+"F0.wireOp",EDGE,"E314"),sQuery(id+"F0.wireOp",EDGE,"E315"),sQuery(id+"F0.wireOp",EDGE,"E316"),sQuery(id+"F0.wireOp",EDGE,"E317"),sQuery(id+"F0.wireOp",EDGE,"E318"),sQuery(id+"F0.wireOp",EDGE,"E319"),sQuery(id+"F0.wireOp",EDGE,"E320"),sQuery(id+"F0.wireOp",EDGE,"E321"),sQuery(id+"F0.wireOp",EDGE,"E322"),sQuery(id+"F0.wireOp",EDGE,"E323"),sQuery(id+"F0.wireOp",EDGE,"E324"),sQuery(id+"F0.wireOp",EDGE,"E325"),sQuery(id+"F0.wireOp",EDGE,"E326"),sQuery(id+"F0.wireOp",EDGE,"E327"),sQuery(id+"F0.wireOp",EDGE,"E328"),sQuery(id+"F0.wireOp",EDGE,"E329"),sQuery(id+"F0.wireOp",EDGE,"E330"),sQuery(id+"F0.wireOp",EDGE,"E331"),sQuery(id+"F0.wireOp",EDGE,"E332"),sQuery(id+"F0.wireOp",EDGE,"E333"),sQuery(id+"F0.wireOp",EDGE,"E334"),sQuery(id+"F0.wireOp",EDGE,"E335"),sQuery(id+"F0.wireOp",EDGE,"E336"),sQuery(id+"F0.wireOp",EDGE,"E337"),sQuery(id+"F0.wireOp",EDGE,"E338"),sQuery(id+"F0.wireOp",EDGE,"E339"),sQuery(id+"F0.wireOp",EDGE,"E340"),sQuery(id+"F0.wireOp",EDGE,"E341"),sQuery(id+"F0.wireOp",EDGE,"E342"),sQuery(id+"F0.wireOp",EDGE,"E343"),sQuery(id+"F0.wireOp",EDGE,"E344"),sQuery(id+"F0.wireOp",EDGE,"E345"),sQuery(id+"F0.wireOp",EDGE,"E346"),sQuery(id+"F0.wireOp",EDGE,"E347"),sQuery(id+"F0.wireOp",EDGE,"E348"),sQuery(id+"F0.wireOp",EDGE,"E349"),sQuery(id+"F0.wireOp",EDGE,"E350"),sQuery(id+"F0.wireOp",EDGE,"E351"),sQuery(id+"F0.wireOp",EDGE,"E352"),sQuery(id+"F0.wireOp",EDGE,"E353"),sQuery(id+"F0.wireOp",EDGE,"E354"),sQuery(id+"F0.wireOp",EDGE,"E355"),sQuery(id+"F0.wireOp",EDGE,"E356"),sQuery(id+"F0.wireOp",EDGE,"E357"),sQuery(id+"F0.wireOp",EDGE,"E358"),sQuery(id+"F0.wireOp",EDGE,"E359"),sQuery(id+"F0.wireOp",EDGE,"E360"),sQuery(id+"F0.wireOp",EDGE,"E361"),sQuery(id+"F0.wireOp",EDGE,"E362"),sQuery(id+"F0.wireOp",EDGE,"E363"),sQuery(id+"F0.wireOp",EDGE,"E364"),sQuery(id+"F0.wireOp",EDGE,"E365"),sQuery(id+"F0.wireOp",EDGE,"E366"),sQuery(id+"F0.wireOp",EDGE,"E367"),sQuery(id+"F0.wireOp",EDGE,"E368"),sQuery(id+"F0.wireOp",EDGE,"E369"),sQuery(id+"F0.wireOp",EDGE,"E370"),sQuery(id+"F0.wireOp",EDGE,"E371"),sQuery(id+"F0.wireOp",EDGE,"E372"),sQuery(id+"F0.wireOp",EDGE,"E373"),sQuery(id+"F0.wireOp",EDGE,"E374"),sQuery(id+"F0.wireOp",EDGE,"E375"),sQuery(id+"F0.wireOp",EDGE,"E376"),sQuery(id+"F0.wireOp",EDGE,"E377"),sQuery(id+"F0.wireOp",EDGE,"E378"),sQuery(id+"F0.wireOp",EDGE,"E379"),sQuery(id+"F0.wireOp",EDGE,"E380"),sQuery(id+"F0.wireOp",EDGE,"E381"),sQuery(id+"F0.wireOp",EDGE,"E382"),sQuery(id+"F0.wireOp",EDGE,"E383"),sQuery(id+"F0.wireOp",EDGE,"E384"),sQuery(id+"F0.wireOp",EDGE,"E385"),sQuery(id+"F0.wireOp",EDGE,"E386"),sQuery(id+"F0.wireOp",EDGE,"E387"),sQuery(id+"F0.wireOp",EDGE,"E388"),sQuery(id+"F0.wireOp",EDGE,"E389"),sQuery(id+"F0.wireOp",EDGE,"E390"),sQuery(id+"F0.wireOp",EDGE,"E391"),sQuery(id+"F0.wireOp",EDGE,"E392"),sQuery(id+"F0.wireOp",EDGE,"E393"),sQuery(id+"F0.wireOp",EDGE,"E394"),sQuery(id+"F0.wireOp",EDGE,"E395"),sQuery(id+"F0.wireOp",EDGE,"E396"),sQuery(id+"F0.wireOp",EDGE,"E397"),sQuery(id+"F0.wireOp",EDGE,"E398"),sQuery(id+"F0.wireOp",EDGE,"E399"),sQuery(id+"F0.wireOp",EDGE,"E400"),sQuery(id+"F0.wireOp",EDGE,"E401"),sQuery(id+"F0.wireOp",EDGE,"E402"),sQuery(id+"F0.wireOp",EDGE,"E403"),sQuery(id+"F0.wireOp",EDGE,"E404"),sQuery(id+"F0.wireOp",EDGE,"E405"),sQuery(id+"F0.wireOp",EDGE,"E406"),sQuery(id+"F0.wireOp",EDGE,"E407"),sQuery(id+"F0.wireOp",EDGE,"E408"),sQuery(id+"F0.wireOp",EDGE,"E409"),sQuery(id+"F0.wireOp",EDGE,"E410"),sQuery(id+"F0.wireOp",EDGE,"E411"),sQuery(id+"F0.wireOp",EDGE,"E412"),sQuery(id+"F0.wireOp",EDGE,"E413"),sQuery(id+"F0.wireOp",EDGE,"E414"),sQuery(id+"F0.wireOp",EDGE,"E415"),sQuery(id+"F0.wireOp",EDGE,"E416"),sQuery(id+"F0.wireOp",EDGE,"E417"),sQuery(id+"F0.wireOp",EDGE,"E418"),sQuery(id+"F0.wireOp",EDGE,"E419"),sQuery(id+"F0.wireOp",EDGE,"E420"),sQuery(id+"F0.wireOp",EDGE,"E421"),sQuery(id+"F0.wireOp",EDGE,"E422"),sQuery(id+"F0.wireOp",EDGE,"E423"),sQuery(id+"F0.wireOp",EDGE,"E424"),sQuery(id+"F0.wireOp",EDGE,"E425"),sQuery(id+"F0.wireOp",EDGE,"E426"),sQuery(id+"F0.wireOp",EDGE,"E427"),sQuery(id+"F0.wireOp",EDGE,"E428"),sQuery(id+"F0.wireOp",EDGE,"E429"),sQuery(id+"F0.wireOp",EDGE,"E430"),sQuery(id+"F0.wireOp",EDGE,"E431"),sQuery(id+"F0.wireOp",EDGE,"E432"),sQuery(id+"F0.wireOp",EDGE,"E433"),sQuery(id+"F0.wireOp",EDGE,"E434"),sQuery(id+"F0.wireOp",EDGE,"E435"),sQuery(id+"F0.wireOp",EDGE,"E436"),sQuery(id+"F0.wireOp",EDGE,"E437"),sQuery(id+"F0.wireOp",EDGE,"E438"),sQuery(id+"F0.wireOp",EDGE,"E439"),sQuery(id+"F0.wireOp",EDGE,"E440"),sQuery(id+"F0.wireOp",EDGE,"E441"),sQuery(id+"F0.wireOp",EDGE,"E442"),sQuery(id+"F0.wireOp",EDGE,"E443"),sQuery(id+"F0.wireOp",EDGE,"E444"),sQuery(id+"F0.wireOp",EDGE,"E445"),sQuery(id+"F0.wireOp",EDGE,"E446"),sQuery(id+"F0.wireOp",EDGE,"E447"),sQuery(id+"F0.wireOp",EDGE,"E448"),sQuery(id+"F0.wireOp",EDGE,"E449"),sQuery(id+"F0.wireOp",EDGE,"E450"),sQuery(id+"F0.wireOp",EDGE,"E451"),sQuery(id+"F0.wireOp",EDGE,"E452"),sQuery(id+"F0.wireOp",EDGE,"E453"),sQuery(id+"F0.wireOp",EDGE,"E454"),sQuery(id+"F0.wireOp",EDGE,"E455"),sQuery(id+"F0.wireOp",EDGE,"E456"),sQuery(id+"F0.wireOp",EDGE,"E457"),sQuery(id+"F0.wireOp",EDGE,"E458"),sQuery(id+"F0.wireOp",EDGE,"E459"),sQuery(id+"F0.wireOp",EDGE,"E460"),sQuery(id+"F0.wireOp",EDGE,"E461"),sQuery(id+"F0.wireOp",EDGE,"E462"),sQuery(id+"F0.wireOp",EDGE,"E463"),sQuery(id+"F0.wireOp",EDGE,"E464"),sQuery(id+"F0.wireOp",EDGE,"E465"),sQuery(id+"F0.wireOp",EDGE,"E466"),sQuery(id+"F0.wireOp",EDGE,"E467"),sQuery(id+"F0.wireOp",EDGE,"E468"),sQuery(id+"F0.wireOp",EDGE,"E469"),sQuery(id+"F0.wireOp",EDGE,"E470"),sQuery(id+"F0.wireOp",EDGE,"E471"),sQuery(id+"F0.wireOp",EDGE,"E472"),sQuery(id+"F0.wireOp",EDGE,"E473"),sQuery(id+"F0.wireOp",EDGE,"E474"),sQuery(id+"F0.wireOp",EDGE,"E475"),sQuery(id+"F0.wireOp",EDGE,"E476"),sQuery(id+"F0.wireOp",EDGE,"E477"),sQuery(id+"F0.wireOp",EDGE,"E478"),sQuery(id+"F0.wireOp",EDGE,"E479"),sQuery(id+"F0.wireOp",EDGE,"E480"),sQuery(id+"F0.wireOp",EDGE,"E481"),sQuery(id+"F0.wireOp",EDGE,"E482"),sQuery(id+"F0.wireOp",EDGE,"E483"),sQuery(id+"F0.wireOp",EDGE,"E484"),sQuery(id+"F0.wireOp",EDGE,"E485"),sQuery(id+"F0.wireOp",EDGE,"E486"),sQuery(id+"F0.wireOp",EDGE,"E487"),sQuery(id+"F0.wireOp",EDGE,"E488"),sQuery(id+"F0.wireOp",EDGE,"E489"),sQuery(id+"F0.wireOp",EDGE,"E490"),sQuery(id+"F0.wireOp",EDGE,"E491"),sQuery(id+"F0.wireOp",EDGE,"E492"),sQuery(id+"F0.wireOp",EDGE,"E493"),sQuery(id+"F0.wireOp",EDGE,"E494"),sQuery(id+"F0.wireOp",EDGE,"E495"),sQuery(id+"F0.wireOp",EDGE,"E496"),sQuery(id+"F0.wireOp",EDGE,"E497"),sQuery(id+"F0.wireOp",EDGE,"E498"),sQuery(id+"F0.wireOp",EDGE,"E499"),sQuery(id+"F0.wireOp",EDGE,"E500"),sQuery(id+"F0.wireOp",EDGE,"E501"),sQuery(id+"F0.wireOp",EDGE,"E502"),sQuery(id+"F0.wireOp",EDGE,"E503"),sQuery(id+"F0.wireOp",EDGE,"E504"),sQuery(id+"F0.wireOp",EDGE,"E505"),sQuery(id+"F0.wireOp",EDGE,"E506"),sQuery(id+"F0.wireOp",EDGE,"E507"),sQuery(id+"F0.wireOp",EDGE,"E508"),sQuery(id+"F0.wireOp",EDGE,"E509"),sQuery(id+"F0.wireOp",EDGE,"E510"),sQuery(id+"F0.wireOp",EDGE,"E511"),sQuery(id+"F0.wireOp",EDGE,"E512"),sQuery(id+"F0.wireOp",EDGE,"E513"),sQuery(id+"F0.wireOp",EDGE,"E514"),sQuery(id+"F0.wireOp",EDGE,"E515"),sQuery(id+"F0.wireOp",EDGE,"E516"),sQuery(id+"F0.wireOp",EDGE,"E517"),sQuery(id+"F0.wireOp",EDGE,"E518"),sQuery(id+"F0.wireOp",EDGE,"E519"),sQuery(id+"F0.wireOp",EDGE,"E520"),sQuery(id+"F0.wireOp",EDGE,"E521"),sQuery(id+"F0.wireOp",EDGE,"E522"),sQuery(id+"F0.wireOp",EDGE,"E523"),sQuery(id+"F0.wireOp",EDGE,"E524"),sQuery(id+"F0.wireOp",EDGE,"E525"),sQuery(id+"F0.wireOp",EDGE,"E526"),sQuery(id+"F0.wireOp",EDGE,"E527"),sQuery(id+"F0.wireOp",EDGE,"E528"),sQuery(id+"F0.wireOp",EDGE,"E529"),sQuery(id+"F0.wireOp",EDGE,"E530"),sQuery(id+"F0.wireOp",EDGE,"E531"),sQuery(id+"F0.wireOp",EDGE,"E532"),sQuery(id+"F0.wireOp",EDGE,"E533"),sQuery(id+"F0.wireOp",EDGE,"E534"),sQuery(id+"F0.wireOp",EDGE,"E535"),sQuery(id+"F0.wireOp",EDGE,"E536"),sQuery(id+"F0.wireOp",EDGE,"E537"),sQuery(id+"F0.wireOp",EDGE,"E538"),sQuery(id+"F0.wireOp",EDGE,"E539"),sQuery(id+"F0.wireOp",EDGE,"E540"),sQuery(id+"F0.wireOp",EDGE,"E541"),sQuery(id+"F0.wireOp",EDGE,"E542"),sQuery(id+"F0.wireOp",EDGE,"E543"),sQuery(id+"F0.wireOp",EDGE,"E544"),sQuery(id+"F0.wireOp",EDGE,"E545"),sQuery(id+"F0.wireOp",EDGE,"E546"),sQuery(id+"F0.wireOp",EDGE,"E547"),sQuery(id+"F0.wireOp",EDGE,"E548"),sQuery(id+"F0.wireOp",EDGE,"E549"),sQuery(id+"F0.wireOp",EDGE,"E550"),sQuery(id+"F0.wireOp",EDGE,"E551"),sQuery(id+"F0.wireOp",EDGE,"E552"),sQuery(id+"F0.wireOp",EDGE,"E553"),sQuery(id+"F0.wireOp",EDGE,"E554"),sQuery(id+"F0.wireOp",EDGE,"E555"),sQuery(id+"F0.wireOp",EDGE,"E556"),sQuery(id+"F0.wireOp",EDGE,"E557"),sQuery(id+"F0.wireOp",EDGE,"E558"),sQuery(id+"F0.wireOp",EDGE,"E559"),sQuery(id+"F0.wireOp",EDGE,"E560"),sQuery(id+"F0.wireOp",EDGE,"E561"),sQuery(id+"F0.wireOp",EDGE,"E562"),sQuery(id+"F0.wireOp",EDGE,"E563"),sQuery(id+"F0.wireOp",EDGE,"E564"),sQuery(id+"F0.wireOp",EDGE,"E565"),sQuery(id+"F0.wireOp",EDGE,"E566"),sQuery(id+"F0.wireOp",EDGE,"E567"),sQuery(id+"F0.wireOp",EDGE,"E568"),sQuery(id+"F0.wireOp",EDGE,"E569"),sQuery(id+"F0.wireOp",EDGE,"E570"),sQuery(id+"F0.wireOp",EDGE,"E571"),sQuery(id+"F0.wireOp",EDGE,"E572"),sQuery(id+"F0.wireOp",EDGE,"E573"),sQuery(id+"F0.wireOp",EDGE,"E574"),sQuery(id+"F0.wireOp",EDGE,"E575"),sQuery(id+"F0.wireOp",EDGE,"E576"),sQuery(id+"F0.wireOp",EDGE,"E577"),sQuery(id+"F0.wireOp",EDGE,"E578"),sQuery(id+"F0.wireOp",EDGE,"E579"),sQuery(id+"F0.wireOp",EDGE,"E580"),sQuery(id+"F0.wireOp",EDGE,"E581"),sQuery(id+"F0.wireOp",EDGE,"E582"),sQuery(id+"F0.wireOp",EDGE,"E583"),sQuery(id+"F0.wireOp",EDGE,"E584"),sQuery(id+"F0.wireOp",EDGE,"E585"),sQuery(id+"F0.wireOp",EDGE,"E586"),sQuery(id+"F0.wireOp",EDGE,"E587"),sQuery(id+"F0.wireOp",EDGE,"E588"),sQuery(id+"F0.wireOp",EDGE,"E589"),sQuery(id+"F0.wireOp",EDGE,"E590"),sQuery(id+"F0.wireOp",EDGE,"E591"),sQuery(id+"F0.wireOp",EDGE,"E592"),sQuery(id+"F0.wireOp",EDGE,"E593"),sQuery(id+"F0.wireOp",EDGE,"E594"),sQuery(id+"F0.wireOp",EDGE,"E595"),sQuery(id+"F0.wireOp",EDGE,"E596"),sQuery(id+"F0.wireOp",EDGE,"E597"),sQuery(id+"F0.wireOp",EDGE,"E598"),sQuery(id+"F0.wireOp",EDGE,"E599"),sQuery(id+"F0.wireOp",EDGE,"E600"),sQuery(id+"F0.wireOp",EDGE,"E601"),sQuery(id+"F0.wireOp",EDGE,"E602"),sQuery(id+"F0.wireOp",EDGE,"E603"),sQuery(id+"F0.wireOp",EDGE,"E604"),sQuery(id+"F0.wireOp",EDGE,"E605"),sQuery(id+"F0.wireOp",EDGE,"E606"),sQuery(id+"F0.wireOp",EDGE,"E607"),sQuery(id+"F0.wireOp",EDGE,"E608"),sQuery(id+"F0.wireOp",EDGE,"E609"),sQuery(id+"F0.wireOp",EDGE,"E610"),sQuery(id+"F0.wireOp",EDGE,"E611"),sQuery(id+"F0.wireOp",EDGE,"E612"),sQuery(id+"F0.wireOp",EDGE,"E613"),sQuery(id+"F0.wireOp",EDGE,"E614"),sQuery(id+"F0.wireOp",EDGE,"E615"),sQuery(id+"F0.wireOp",EDGE,"E616"),sQuery(id+"F0.wireOp",EDGE,"E617"),sQuery(id+"F0.wireOp",EDGE,"E618"),sQuery(id+"F0.wireOp",EDGE,"E619"),sQuery(id+"F0.wireOp",EDGE,"E620"),sQuery(id+"F0.wireOp",EDGE,"E621"),sQuery(id+"F0.wireOp",EDGE,"E622"),sQuery(id+"F0.wireOp",EDGE,"E623"),sQuery(id+"F0.wireOp",EDGE,"E624"),sQuery(id+"F0.wireOp",EDGE,"E625"),sQuery(id+"F0.wireOp",EDGE,"E626"),sQuery(id+"F0.wireOp",EDGE,"E627"),sQuery(id+"F0.wireOp",EDGE,"E628"),sQuery(id+"F0.wireOp",EDGE,"E629"),sQuery(id+"F0.wireOp",EDGE,"E630"),sQuery(id+"F0.wireOp",EDGE,"E631"),sQuery(id+"F0.wireOp",EDGE,"E632"),sQuery(id+"F0.wireOp",EDGE,"E633"),sQuery(id+"F0.wireOp",EDGE,"E634"),sQuery(id+"F0.wireOp",EDGE,"E635"),sQuery(id+"F0.wireOp",EDGE,"E636"),sQuery(id+"F0.wireOp",EDGE,"E637"),sQuery(id+"F0.wireOp",EDGE,"E638"),sQuery(id+"F0.wireOp",EDGE,"E639"),sQuery(id+"F0.wireOp",EDGE,"E640"),sQuery(id+"F0.wireOp",EDGE,"E641"),sQuery(id+"F0.wireOp",EDGE,"E642"),sQuery(id+"F0.wireOp",EDGE,"E643"),sQuery(id+"F0.wireOp",EDGE,"E644"),sQuery(id+"F0.wireOp",EDGE,"E645"),sQuery(id+"F0.wireOp",EDGE,"E646"),sQuery(id+"F0.wireOp",EDGE,"E647"),sQuery(id+"F0.wireOp",EDGE,"E648"),sQuery(id+"F0.wireOp",EDGE,"E649"),sQuery(id+"F0.wireOp",EDGE,"E650"),sQuery(id+"F0.wireOp",EDGE,"E651"),sQuery(id+"F0.wireOp",EDGE,"E652"),sQuery(id+"F0.wireOp",EDGE,"E653"),sQuery(id+"F0.wireOp",EDGE,"E654"),sQuery(id+"F0.wireOp",EDGE,"E655"),sQuery(id+"F0.wireOp",EDGE,"E656"),sQuery(id+"F0.wireOp",EDGE,"E657"),sQuery(id+"F0.wireOp",EDGE,"E658"),sQuery(id+"F0.wireOp",EDGE,"E659"),sQuery(id+"F0.wireOp",EDGE,"E660"),sQuery(id+"F0.wireOp",EDGE,"E661"),sQuery(id+"F0.wireOp",EDGE,"E662"),sQuery(id+"F0.wireOp",EDGE,"E663"),sQuery(id+"F0.wireOp",EDGE,"E664"),sQuery(id+"F0.wireOp",EDGE,"E665"),sQuery(id+"F0.wireOp",EDGE,"E666"),sQuery(id+"F0.wireOp",EDGE,"E667"),sQuery(id+"F0.wireOp",EDGE,"E668"),sQuery(id+"F0.wireOp",EDGE,"E669"),sQuery(id+"F0.wireOp",EDGE,"E670"),sQuery(id+"F0.wireOp",EDGE,"E671"),sQuery(id+"F0.wireOp",EDGE,"E672"),sQuery(id+"F0.wireOp",EDGE,"E673"),sQuery(id+"F0.wireOp",EDGE,"E674"),sQuery(id+"F0.wireOp",EDGE,"E675"),sQuery(id+"F0.wireOp",EDGE,"E676"),sQuery(id+"F0.wireOp",EDGE,"E677"),sQuery(id+"F0.wireOp",EDGE,"E678"),sQuery(id+"F0.wireOp",EDGE,"E679"),sQuery(id+"F0.wireOp",EDGE,"E680"),sQuery(id+"F0.wireOp",EDGE,"E681"),sQuery(id+"F0.wireOp",EDGE,"E682"),sQuery(id+"F0.wireOp",EDGE,"E683"),sQuery(id+"F0.wireOp",EDGE,"E684"),sQuery(id+"F0.wireOp",EDGE,"E685"),sQuery(id+"F0.wireOp",EDGE,"E686"),sQuery(id+"F0.wireOp",EDGE,"E687"),sQuery(id+"F0.wireOp",EDGE,"E688"),sQuery(id+"F0.wireOp",EDGE,"E689"),sQuery(id+"F0.wireOp",EDGE,"E690"),sQuery(id+"F0.wireOp",EDGE,"E691"),sQuery(id+"F0.wireOp",EDGE,"E692"),sQuery(id+"F0.wireOp",EDGE,"E693"),sQuery(id+"F0.wireOp",EDGE,"E694"),sQuery(id+"F0.wireOp",EDGE,"E695"),sQuery(id+"F0.wireOp",EDGE,"E696"),sQuery(id+"F0.wireOp",EDGE,"E697"),sQuery(id+"F0.wireOp",EDGE,"E698"),sQuery(id+"F0.wireOp",EDGE,"E699"),sQuery(id+"F0.wireOp",EDGE,"E700"),sQuery(id+"F0.wireOp",EDGE,"E701"),sQuery(id+"F0.wireOp",EDGE,"E702"),sQuery(id+"F0.wireOp",EDGE,"E703"),sQuery(id+"F0.wireOp",EDGE,"E704"),sQuery(id+"F0.wireOp",EDGE,"E705"),sQuery(id+"F0.wireOp",EDGE,"E706"),sQuery(id+"F0.wireOp",EDGE,"E707"),sQuery(id+"F0.wireOp",EDGE,"E708"),sQuery(id+"F0.wireOp",EDGE,"E709"),sQuery(id+"F0.wireOp",EDGE,"E710"),sQuery(id+"F0.wireOp",EDGE,"E711"),sQuery(id+"F0.wireOp",EDGE,"E712"),sQuery(id+"F0.wireOp",EDGE,"E713"),sQuery(id+"F0.wireOp",EDGE,"E714"),sQuery(id+"F0.wireOp",EDGE,"E715"),sQuery(id+"F0.wireOp",EDGE,"E716"),sQuery(id+"F0.wireOp",EDGE,"E717"),sQuery(id+"F0.wireOp",EDGE,"E718"),sQuery(id+"F0.wireOp",EDGE,"E719"),sQuery(id+"F0.wireOp",EDGE,"E720"),sQuery(id+"F0.wireOp",EDGE,"E721"),sQuery(id+"F0.wireOp",EDGE,"E722"),sQuery(id+"F0.wireOp",EDGE,"E723"),sQuery(id+"F0.wireOp",EDGE,"E724"),sQuery(id+"F0.wireOp",EDGE,"E725"),sQuery(id+"F0.wireOp",EDGE,"E726"),sQuery(id+"F0.wireOp",EDGE,"E727"),sQuery(id+"F0.wireOp",EDGE,"E728"),sQuery(id+"F0.wireOp",EDGE,"E729"),sQuery(id+"F0.wireOp",EDGE,"E730"),sQuery(id+"F0.wireOp",EDGE,"E731"),sQuery(id+"F0.wireOp",EDGE,"E732"),sQuery(id+"F0.wireOp",EDGE,"E733"),sQuery(id+"F0.wireOp",EDGE,"E734"),sQuery(id+"F0.wireOp",EDGE,"E735"),sQuery(id+"F0.wireOp",EDGE,"E736"),sQuery(id+"F0.wireOp",EDGE,"E737"),sQuery(id+"F0.wireOp",EDGE,"E738"),sQuery(id+"F0.wireOp",EDGE,"E739"),sQuery(id+"F0.wireOp",EDGE,"E740"),sQuery(id+"F0.wireOp",EDGE,"E741"),sQuery(id+"F0.wireOp",EDGE,"E742"),sQuery(id+"F0.wireOp",EDGE,"E743"),sQuery(id+"F0.wireOp",EDGE,"E744"),sQuery(id+"F0.wireOp",EDGE,"E745"),sQuery(id+"F0.wireOp",EDGE,"E746"),sQuery(id+"F0.wireOp",EDGE,"E747"),sQuery(id+"F0.wireOp",EDGE,"E748"),sQuery(id+"F0.wireOp",EDGE,"E749"),sQuery(id+"F0.wireOp",EDGE,"E750"),sQuery(id+"F0.wireOp",EDGE,"E751"),sQuery(id+"F0.wireOp",EDGE,"E752"),sQuery(id+"F0.wireOp",EDGE,"E753"),sQuery(id+"F0.wireOp",EDGE,"E754"),sQuery(id+"F0.wireOp",EDGE,"E755"),sQuery(id+"F0.wireOp",EDGE,"E756"),sQuery(id+"F0.wireOp",EDGE,"E757"),sQuery(id+"F0.wireOp",EDGE,"E758"),sQuery(id+"F0.wireOp",EDGE,"E759"),sQuery(id+"F0.wireOp",EDGE,"E760"),sQuery(id+"F0.wireOp",EDGE,"E761"),sQuery(id+"F0.wireOp",EDGE,"E762"),sQuery(id+"F0.wireOp",EDGE,"E763"),sQuery(id+"F0.wireOp",EDGE,"E764"),sQuery(id+"F0.wireOp",EDGE,"E765"),sQuery(id+"F0.wireOp",EDGE,"E766"),sQuery(id+"F0.wireOp",EDGE,"E767"),sQuery(id+"F0.wireOp",EDGE,"E768"),sQuery(id+"F0.wireOp",EDGE,"E769"),sQuery(id+"F0.wireOp",EDGE,"E770"),sQuery(id+"F0.wireOp",EDGE,"E771"),sQuery(id+"F0.wireOp",EDGE,"E772"),sQuery(id+"F0.wireOp",EDGE,"E773"),sQuery(id+"F0.wireOp",EDGE,"E774"),sQuery(id+"F0.wireOp",EDGE,"E775"),sQuery(id+"F0.wireOp",EDGE,"E776"),sQuery(id+"F0.wireOp",EDGE,"E777"),sQuery(id+"F0.wireOp",EDGE,"E778"),sQuery(id+"F0.wireOp",EDGE,"E779"),sQuery(id+"F0.wireOp",EDGE,"E780"),sQuery(id+"F0.wireOp",EDGE,"E781"),sQuery(id+"F0.wireOp",EDGE,"E782"),sQuery(id+"F0.wireOp",EDGE,"E783"),sQuery(id+"F0.wireOp",EDGE,"E784"),sQuery(id+"F0.wireOp",EDGE,"E785"),sQuery(id+"F0.wireOp",EDGE,"E786"),sQuery(id+"F0.wireOp",EDGE,"E787"),sQuery(id+"F0.wireOp",EDGE,"E788"),sQuery(id+"F0.wireOp",EDGE,"E789"),sQuery(id+"F0.wireOp",EDGE,"E790"),sQuery(id+"F0.wireOp",EDGE,"E791"),sQuery(id+"F0.wireOp",EDGE,"E792"),sQuery(id+"F0.wireOp",EDGE,"E793"),sQuery(id+"F0.wireOp",EDGE,"E794"),sQuery(id+"F0.wireOp",EDGE,"E795"),sQuery(id+"F0.wireOp",EDGE,"E796"),sQuery(id+"F0.wireOp",EDGE,"E797"),sQuery(id+"F0.wireOp",EDGE,"E798"),sQuery(id+"F0.wireOp",EDGE,"E799"),sQuery(id+"F0.wireOp",EDGE,"E800"),sQuery(id+"F0.wireOp",EDGE,"E801"),sQuery(id+"F0.wireOp",EDGE,"E802"),sQuery(id+"F0.wireOp",EDGE,"E803"),sQuery(id+"F0.wireOp",EDGE,"E804"),sQuery(id+"F0.wireOp",EDGE,"E805"),sQuery(id+"F0.wireOp",EDGE,"E806"),sQuery(id+"F0.wireOp",EDGE,"E807"),sQuery(id+"F0.wireOp",EDGE,"E808"),sQuery(id+"F0.wireOp",EDGE,"E809"),sQuery(id+"F0.wireOp",EDGE,"E810"),sQuery(id+"F0.wireOp",EDGE,"E811"),sQuery(id+"F0.wireOp",EDGE,"E812"),sQuery(id+"F0.wireOp",EDGE,"E813"),sQuery(id+"F0.wireOp",EDGE,"E814"),sQuery(id+"F0.wireOp",EDGE,"E815"),sQuery(id+"F0.wireOp",EDGE,"E816"),sQuery(id+"F0.wireOp",EDGE,"E817"),sQuery(id+"F0.wireOp",EDGE,"E818"),sQuery(id+"F0.wireOp",EDGE,"E819"),sQuery(id+"F0.wireOp",EDGE,"E820"),sQuery(id+"F0.wireOp",EDGE,"E821"),sQuery(id+"F0.wireOp",EDGE,"E822"),sQuery(id+"F0.wireOp",EDGE,"E823"),sQuery(id+"F0.wireOp",EDGE,"E824"),sQuery(id+"F0.wireOp",EDGE,"E825"),sQuery(id+"F0.wireOp",EDGE,"E826"),sQuery(id+"F0.wireOp",EDGE,"E827"),sQuery(id+"F0.wireOp",EDGE,"E828"),sQuery(id+"F0.wireOp",EDGE,"E829"),sQuery(id+"F0.wireOp",EDGE,"E830"),sQuery(id+"F0.wireOp",EDGE,"E831"),sQuery(id+"F0.wireOp",EDGE,"E832"),sQuery(id+"F0.wireOp",EDGE,"E833"),sQuery(id+"F0.wireOp",EDGE,"E834"),sQuery(id+"F0.wireOp",EDGE,"E835"),sQuery(id+"F0.wireOp",EDGE,"E836"),sQuery(id+"F0.wireOp",EDGE,"E837"),sQuery(id+"F0.wireOp",EDGE,"E838"),sQuery(id+"F0.wireOp",EDGE,"E839"),sQuery(id+"F0.wireOp",EDGE,"E840"),sQuery(id+"F0.wireOp",EDGE,"E841"),sQuery(id+"F0.wireOp",EDGE,"E842"),sQuery(id+"F0.wireOp",EDGE,"E843"),sQuery(id+"F0.wireOp",EDGE,"E844"),sQuery(id+"F0.wireOp",EDGE,"E845"),sQuery(id+"F0.wireOp",EDGE,"E846"),sQuery(id+"F0.wireOp",EDGE,"E847"),sQuery(id+"F0.wireOp",EDGE,"E848"),sQuery(id+"F0.wireOp",EDGE,"E849"),sQuery(id+"F0.wireOp",EDGE,"E850"),sQuery(id+"F0.wireOp",EDGE,"E851"),sQuery(id+"F0.wireOp",EDGE,"E852"),sQuery(id+"F0.wireOp",EDGE,"E853"),sQuery(id+"F0.wireOp",EDGE,"E854"),sQuery(id+"F0.wireOp",EDGE,"E855"),sQuery(id+"F0.wireOp",EDGE,"E856"),sQuery(id+"F0.wireOp",EDGE,"E857"),sQuery(id+"F0.wireOp",EDGE,"E858"),sQuery(id+"F0.wireOp",EDGE,"E859"),sQuery(id+"F0.wireOp",EDGE,"E860"),sQuery(id+"F0.wireOp",EDGE,"E861"),sQuery(id+"F0.wireOp",EDGE,"E862"),sQuery(id+"F0.wireOp",EDGE,"E863"),sQuery(id+"F0.wireOp",EDGE,"E864"),sQuery(id+"F0.wireOp",EDGE,"E865"),sQuery(id+"F0.wireOp",EDGE,"E866"),sQuery(id+"F0.wireOp",EDGE,"E867"),sQuery(id+"F0.wireOp",EDGE,"E868"),sQuery(id+"F0.wireOp",EDGE,"E869"),sQuery(id+"F0.wireOp",EDGE,"E870"),sQuery(id+"F0.wireOp",EDGE,"E871"),sQuery(id+"F0.wireOp",EDGE,"E872"),sQuery(id+"F0.wireOp",EDGE,"E873"),sQuery(id+"F0.wireOp",EDGE,"E874"),sQuery(id+"F0.wireOp",EDGE,"E875"),sQuery(id+"F0.wireOp",EDGE,"E876"),sQuery(id+"F0.wireOp",EDGE,"E877"),sQuery(id+"F0.wireOp",EDGE,"E878"),sQuery(id+"F0.wireOp",EDGE,"E879"),sQuery(id+"F0.wireOp",EDGE,"E880"),sQuery(id+"F0.wireOp",EDGE,"E881"),sQuery(id+"F0.wireOp",EDGE,"E882"),sQuery(id+"F0.wireOp",EDGE,"E883"),sQuery(id+"F0.wireOp",EDGE,"E884"),sQuery(id+"F0.wireOp",EDGE,"E885"),sQuery(id+"F0.wireOp",EDGE,"E886"),sQuery(id+"F0.wireOp",EDGE,"E887"),sQuery(id+"F0.wireOp",EDGE,"E888"),sQuery(id+"F0.wireOp",EDGE,"E889"),sQuery(id+"F0.wireOp",EDGE,"E890"),sQuery(id+"F0.wireOp",EDGE,"E891"),sQuery(id+"F0.wireOp",EDGE,"E892"),sQuery(id+"F0.wireOp",EDGE,"E893"),sQuery(id+"F0.wireOp",EDGE,"E894"),sQuery(id+"F0.wireOp",EDGE,"E895"),sQuery(id+"F0.wireOp",EDGE,"E896"),sQuery(id+"F0.wireOp",EDGE,"E897"),sQuery(id+"F0.wireOp",EDGE,"E898"),sQuery(id+"F0.wireOp",EDGE,"E899"),sQuery(id+"F0.wireOp",EDGE,"E900"),sQuery(id+"F0.wireOp",EDGE,"E901"),sQuery(id+"F0.wireOp",EDGE,"E902"),sQuery(id+"F0.wireOp",EDGE,"E903"),sQuery(id+"F0.wireOp",EDGE,"E904"),sQuery(id+"F0.wireOp",EDGE,"E905"),sQuery(id+"F0.wireOp",EDGE,"E906"),sQuery(id+"F0.wireOp",EDGE,"E907"),sQuery(id+"F0.wireOp",EDGE,"E908"),sQuery(id+"F0.wireOp",EDGE,"E909"),sQuery(id+"F0.wireOp",EDGE,"E910"),sQuery(id+"F0.wireOp",EDGE,"E911"),sQuery(id+"F0.wireOp",EDGE,"E912"),sQuery(id+"F0.wireOp",EDGE,"E913"),sQuery(id+"F0.wireOp",EDGE,"E914"),sQuery(id+"F0.wireOp",EDGE,"E915"),sQuery(id+"F0.wireOp",EDGE,"E916"),sQuery(id+"F0.wireOp",EDGE,"E917"),sQuery(id+"F0.wireOp",EDGE,"E918"),sQuery(id+"F0.wireOp",EDGE,"E919"),sQuery(id+"F0.wireOp",EDGE,"E920"),sQuery(id+"F0.wireOp",EDGE,"E921"),sQuery(id+"F0.wireOp",EDGE,"E922"),sQuery(id+"F0.wireOp",EDGE,"E923"),sQuery(id+"F0.wireOp",EDGE,"E924"),sQuery(id+"F0.wireOp",EDGE,"E925"),sQuery(id+"F0.wireOp",EDGE,"E926"),sQuery(id+"F0.wireOp",EDGE,"E927"),sQuery(id+"F0.wireOp",EDGE,"E928"),sQuery(id+"F0.wireOp",EDGE,"E929"),sQuery(id+"F0.wireOp",EDGE,"E930"),sQuery(id+"F0.wireOp",EDGE,"E931"),sQuery(id+"F0.wireOp",EDGE,"E932"),sQuery(id+"F0.wireOp",EDGE,"E933"),sQuery(id+"F0.wireOp",EDGE,"E934"),sQuery(id+"F0.wireOp",EDGE,"E935"),sQuery(id+"F0.wireOp",EDGE,"E936"),sQuery(id+"F0.wireOp",EDGE,"E937"),sQuery(id+"F0.wireOp",EDGE,"E938"),sQuery(id+"F0.wireOp",EDGE,"E939"),sQuery(id+"F0.wireOp",EDGE,"E940"),sQuery(id+"F0.wireOp",EDGE,"E941"),sQuery(id+"F0.wireOp",EDGE,"E942"),sQuery(id+"F0.wireOp",EDGE,"E943"),sQuery(id+"F0.wireOp",EDGE,"E944"),sQuery(id+"F0.wireOp",EDGE,"E945"),sQuery(id+"F0.wireOp",EDGE,"E946"),sQuery(id+"F0.wireOp",EDGE,"E947"),sQuery(id+"F0.wireOp",EDGE,"E948"),sQuery(id+"F0.wireOp",EDGE,"E949"),sQuery(id+"F0.wireOp",EDGE,"E950"),sQuery(id+"F0.wireOp",EDGE,"E951"),sQuery(id+"F0.wireOp",EDGE,"E952"),sQuery(id+"F0.wireOp",EDGE,"E953"),sQuery(id+"F0.wireOp",EDGE,"E954"),sQuery(id+"F0.wireOp",EDGE,"E955"),sQuery(id+"F0.wireOp",EDGE,"E956"),sQuery(id+"F0.wireOp",EDGE,"E957"),sQuery(id+"F0.wireOp",EDGE,"E958"),sQuery(id+"F0.wireOp",EDGE,"E959"),sQuery(id+"F0.wireOp",EDGE,"E960"),sQuery(id+"F0.wireOp",EDGE,"E961"),sQuery(id+"F0.wireOp",EDGE,"E962"),sQuery(id+"F0.wireOp",EDGE,"E963"),sQuery(id+"F0.wireOp",EDGE,"E964"),sQuery(id+"F0.wireOp",EDGE,"E965"),sQuery(id+"F0.wireOp",EDGE,"E966"),sQuery(id+"F0.wireOp",EDGE,"E967"),sQuery(id+"F0.wireOp",EDGE,"E968"),sQuery(id+"F0.wireOp",EDGE,"E969"),sQuery(id+"F0.wireOp",EDGE,"E970"),sQuery(id+"F0.wireOp",EDGE,"E971"),sQuery(id+"F0.wireOp",EDGE,"E972"),sQuery(id+"F0.wireOp",EDGE,"E973"),sQuery(id+"F0.wireOp",EDGE,"E974"),sQuery(id+"F0.wireOp",EDGE,"E975"),sQuery(id+"F0.wireOp",EDGE,"E976"),sQuery(id+"F0.wireOp",EDGE,"E977"),sQuery(id+"F0.wireOp",EDGE,"E978"),sQuery(id+"F0.wireOp",EDGE,"E979"),sQuery(id+"F0.wireOp",EDGE,"E980"),sQuery(id+"F0.wireOp",EDGE,"E981"),sQuery(id+"F0.wireOp",EDGE,"E982"),sQuery(id+"F0.wireOp",EDGE,"E983"),sQuery(id+"F0.wireOp",EDGE,"E984"),sQuery(id+"F0.wireOp",EDGE,"E985"),sQuery(id+"F0.wireOp",EDGE,"E986"),sQuery(id+"F0.wireOp",EDGE,"E987"),sQuery(id+"F0.wireOp",EDGE,"E988"),sQuery(id+"F0.wireOp",EDGE,"E989"),sQuery(id+"F0.wireOp",EDGE,"E990"),sQuery(id+"F0.wireOp",EDGE,"E991"),sQuery(id+"F0.wireOp",EDGE,"E992"),sQuery(id+"F0.wireOp",EDGE,"E993"),sQuery(id+"F0.wireOp",EDGE,"E994"),sQuery(id+"F0.wireOp",EDGE,"E995"),sQuery(id+"F0.wireOp",EDGE,"E996"),sQuery(id+"F0.wireOp",EDGE,"E997"),sQuery(id+"F0.wireOp",EDGE,"E998"),sQuery(id+"F0.wireOp",EDGE,"E999"),sQuery(id+"F0.wireOp",EDGE,"E1000"),sQuery(id+"F0.wireOp",EDGE,"E1001"),sQuery(id+"F0.wireOp",EDGE,"E1002"),sQuery(id+"F0.wireOp",EDGE,"E1003"),sQuery(id+"F0.wireOp",EDGE,"E1004"),sQuery(id+"F0.wireOp",EDGE,"E1005"),sQuery(id+"F0.wireOp",EDGE,"E1006"),sQuery(id+"F0.wireOp",EDGE,"E1007"),sQuery(id+"F0.wireOp",EDGE,"E1008"),sQuery(id+"F0.wireOp",EDGE,"E1009"),sQuery(id+"F0.wireOp",EDGE,"E1010"),sQuery(id+"F0.wireOp",EDGE,"E1011"),sQuery(id+"F0.wireOp",EDGE,"E1012"),sQuery(id+"F0.wireOp",EDGE,"E1013"),sQuery(id+"F0.wireOp",EDGE,"E1014"),sQuery(id+"F0.wireOp",EDGE,"E1015"),sQuery(id+"F0.wireOp",EDGE,"E1016"),sQuery(id+"F0.wireOp",EDGE,"E1017"),sQuery(id+"F0.wireOp",EDGE,"E1018"),sQuery(id+"F0.wireOp",EDGE,"E1019"),sQuery(id+"F0.wireOp",EDGE,"E1020"),sQuery(id+"F0.wireOp",EDGE,"E1021"),sQuery(id+"F0.wireOp",EDGE,"E1022"),sQuery(id+"F0.wireOp",EDGE,"E1023"),sQuery(id+"F0.wireOp",EDGE,"E1024"),sQuery(id+"F0.wireOp",EDGE,"E1025"),sQuery(id+"F0.wireOp",EDGE,"E1026"),sQuery(id+"F0.wireOp",EDGE,"E1027"),sQuery(id+"F0.wireOp",EDGE,"E1028"),sQuery(id+"F0.wireOp",EDGE,"E1029"),sQuery(id+"F0.wireOp",EDGE,"E1030"),sQuery(id+"F0.wireOp",EDGE,"E1031"),sQuery(id+"F0.wireOp",EDGE,"E1032"),sQuery(id+"F0.wireOp",EDGE,"E1033"),sQuery(id+"F0.wireOp",EDGE,"E1034"),sQuery(id+"F0.wireOp",EDGE,"E1035"),sQuery(id+"F0.wireOp",EDGE,"E1036"),sQuery(id+"F0.wireOp",EDGE,"E1037"),sQuery(id+"F0.wireOp",EDGE,"E1038"),sQuery(id+"F0.wireOp",EDGE,"E1039"),sQuery(id+"F0.wireOp",EDGE,"E1040"),sQuery(id+"F0.wireOp",EDGE,"E1041"),sQuery(id+"F0.wireOp",EDGE,"E1042"),sQuery(id+"F0.wireOp",EDGE,"E1043"),sQuery(id+"F0.wireOp",EDGE,"E1044"),sQuery(id+"F0.wireOp",EDGE,"E1045"),sQuery(id+"F0.wireOp",EDGE,"E1046"),sQuery(id+"F0.wireOp",EDGE,"E1047"),sQuery(id+"F0.wireOp",EDGE,"E1048"),sQuery(id+"F0.wireOp",EDGE,"E1049"),sQuery(id+"F0.wireOp",EDGE,"E1050"),sQuery(id+"F0.wireOp",EDGE,"E1051"),sQuery(id+"F0.wireOp",EDGE,"E1052"),sQuery(id+"F0.wireOp",EDGE,"E1053"),sQuery(id+"F0.wireOp",EDGE,"E1054"),sQuery(id+"F0.wireOp",EDGE,"E1055"),sQuery(id+"F0.wireOp",EDGE,"E1056"),sQuery(id+"F0.wireOp",EDGE,"E1057"),sQuery(id+"F0.wireOp",EDGE,"E1058"),sQuery(id+"F0.wireOp",EDGE,"E1059"),sQuery(id+"F0.wireOp",EDGE,"E1060"),sQuery(id+"F0.wireOp",EDGE,"E1061"),sQuery(id+"F0.wireOp",EDGE,"E1062"),sQuery(id+"F0.wireOp",EDGE,"E1063"),sQuery(id+"F0.wireOp",EDGE,"E1064"),sQuery(id+"F0.wireOp",EDGE,"E1065"),sQuery(id+"F0.wireOp",EDGE,"E1066"),sQuery(id+"F0.wireOp",EDGE,"E1067"),sQuery(id+"F0.wireOp",EDGE,"E1068"),sQuery(id+"F0.wireOp",EDGE,"E1069"),sQuery(id+"F0.wireOp",EDGE,"E1070"),sQuery(id+"F0.wireOp",EDGE,"E1071"),sQuery(id+"F0.wireOp",EDGE,"E1072"),sQuery(id+"F0.wireOp",EDGE,"E1073"),sQuery(id+"F0.wireOp",EDGE,"E1074"),sQuery(id+"F0.wireOp",EDGE,"E1075"),sQuery(id+"F0.wireOp",EDGE,"E1076"),sQuery(id+"F0.wireOp",EDGE,"E1077"),sQuery(id+"F0.wireOp",EDGE,"E1078"),sQuery(id+"F0.wireOp",EDGE,"E1079"),sQuery(id+"F0.wireOp",EDGE,"E1080"),sQuery(id+"F0.wireOp",EDGE,"E1081"),sQuery(id+"F0.wireOp",EDGE,"E1082"),sQuery(id+"F0.wireOp",EDGE,"E1083"),sQuery(id+"F0.wireOp",EDGE,"E1084"),sQuery(id+"F0.wireOp",EDGE,"E1085"),sQuery(id+"F0.wireOp",EDGE,"E1086"),sQuery(id+"F0.wireOp",EDGE,"E1087"),sQuery(id+"F0.wireOp",EDGE,"E1088"),sQuery(id+"F0.wireOp",EDGE,"E1089"),sQuery(id+"F0.wireOp",EDGE,"E1090"),sQuery(id+"F0.wireOp",EDGE,"E1091"),sQuery(id+"F0.wireOp",EDGE,"E1092"),sQuery(id+"F0.wireOp",EDGE,"E1093"),sQuery(id+"F0.wireOp",EDGE,"E1094"),sQuery(id+"F0.wireOp",EDGE,"E1095"),sQuery(id+"F0.wireOp",EDGE,"E1096"),sQuery(id+"F0.wireOp",EDGE,"E1097"),sQuery(id+"F0.wireOp",EDGE,"E1098"),sQuery(id+"F0.wireOp",EDGE,"E1099"),sQuery(id+"F0.wireOp",EDGE,"E1100"),sQuery(id+"F0.wireOp",EDGE,"E1101"),sQuery(id+"F0.wireOp",EDGE,"E1102"),sQuery(id+"F0.wireOp",EDGE,"E1103"),sQuery(id+"F0.wireOp",EDGE,"E1104"),sQuery(id+"F0.wireOp",EDGE,"E1105"),sQuery(id+"F0.wireOp",EDGE,"E1106"),sQuery(id+"F0.wireOp",EDGE,"E1107"),sQuery(id+"F0.wireOp",EDGE,"E1108"),sQuery(id+"F0.wireOp",EDGE,"E1109"),sQuery(id+"F0.wireOp",EDGE,"E1110"),sQuery(id+"F0.wireOp",EDGE,"E1111"),sQuery(id+"F0.wireOp",EDGE,"E1112"),sQuery(id+"F0.wireOp",EDGE,"E1113"),sQuery(id+"F0.wireOp",EDGE,"E1114"),sQuery(id+"F0.wireOp",EDGE,"E1115"),sQuery(id+"F0.wireOp",EDGE,"E1116"),sQuery(id+"F0.wireOp",EDGE,"E1117"),sQuery(id+"F0.wireOp",EDGE,"E1118"),sQuery(id+"F0.wireOp",EDGE,"E1119"),sQuery(id+"F0.wireOp",EDGE,"E1120"),sQuery(id+"F0.wireOp",EDGE,"E1121"),sQuery(id+"F0.wireOp",EDGE,"E1122"),sQuery(id+"F0.wireOp",EDGE,"E1123"),sQuery(id+"F0.wireOp",EDGE,"E1124"),sQuery(id+"F0.wireOp",EDGE,"E1125"),sQuery(id+"F0.wireOp",EDGE,"E1126"),sQuery(id+"F0.wireOp",EDGE,"E1127"),sQuery(id+"F0.wireOp",EDGE,"E1128"),sQuery(id+"F0.wireOp",EDGE,"E1129"),sQuery(id+"F0.wireOp",EDGE,"E1130"),sQuery(id+"F0.wireOp",EDGE,"E1131"),sQuery(id+"F0.wireOp",EDGE,"E1132"),sQuery(id+"F0.wireOp",EDGE,"E1133"),sQuery(id+"F0.wireOp",EDGE,"E1134"),sQuery(id+"F0.wireOp",EDGE,"E1135"),sQuery(id+"F0.wireOp",EDGE,"E1136"),sQuery(id+"F0.wireOp",EDGE,"E1137"),sQuery(id+"F0.wireOp",EDGE,"E1138"),sQuery(id+"F0.wireOp",EDGE,"E1139"),sQuery(id+"F0.wireOp",EDGE,"E1140"),sQuery(id+"F0.wireOp",EDGE,"E1141"),sQuery(id+"F0.wireOp",EDGE,"E1142"),sQuery(id+"F0.wireOp",EDGE,"E1143"),sQuery(id+"F0.wireOp",EDGE,"E1144"),sQuery(id+"F0.wireOp",EDGE,"E1145"),sQuery(id+"F0.wireOp",EDGE,"E1146"),sQuery(id+"F0.wireOp",EDGE,"E1147"),sQuery(id+"F0.wireOp",EDGE,"E1148"),sQuery(id+"F0.wireOp",EDGE,"E1149"),sQuery(id+"F0.wireOp",EDGE,"E1150"),sQuery(id+"F0.wireOp",EDGE,"E1151"),sQuery(id+"F0.wireOp",EDGE,"E1152"),sQuery(id+"F0.wireOp",EDGE,"E1153"),sQuery(id+"F0.wireOp",EDGE,"E1154"),sQuery(id+"F0.wireOp",EDGE,"E1155"),sQuery(id+"F0.wireOp",EDGE,"E1156"),sQuery(id+"F0.wireOp",EDGE,"E1157"),sQuery(id+"F0.wireOp",EDGE,"E1158"),sQuery(id+"F0.wireOp",EDGE,"E1159"),sQuery(id+"F0.wireOp",EDGE,"E1160"),sQuery(id+"F0.wireOp",EDGE,"E1161"),sQuery(id+"F0.wireOp",EDGE,"E1162"),sQuery(id+"F0.wireOp",EDGE,"E1163"),sQuery(id+"F0.wireOp",EDGE,"E1164"),sQuery(id+"F0.wireOp",EDGE,"E1165"),sQuery(id+"F0.wireOp",EDGE,"E1166"),sQuery(id+"F0.wireOp",EDGE,"E1167"),sQuery(id+"F0.wireOp",EDGE,"E1168"),sQuery(id+"F0.wireOp",EDGE,"E1169"),sQuery(id+"F0.wireOp",EDGE,"E1170"),sQuery(id+"F0.wireOp",EDGE,"E1171"),sQuery(id+"F0.wireOp",EDGE,"E1172"),sQuery(id+"F0.wireOp",EDGE,"E1173"),sQuery(id+"F0.wireOp",EDGE,"E1174"),sQuery(id+"F0.wireOp",EDGE,"E1175"),sQuery(id+"F0.wireOp",EDGE,"E1176"),sQuery(id+"F0.wireOp",EDGE,"E1177"),sQuery(id+"F0.wireOp",EDGE,"E1178"),sQuery(id+"F0.wireOp",EDGE,"E1179"),sQuery(id+"F0.wireOp",EDGE,"E1180"),sQuery(id+"F0.wireOp",EDGE,"E1181"),sQuery(id+"F0.wireOp",EDGE,"E1182"),sQuery(id+"F0.wireOp",EDGE,"E1183"),sQuery(id+"F0.wireOp",EDGE,"E1184"),sQuery(id+"F0.wireOp",EDGE,"E1185"),sQuery(id+"F0.wireOp",EDGE,"E1186"),sQuery(id+"F0.wireOp",EDGE,"E1187"),sQuery(id+"F0.wireOp",EDGE,"E1188"),sQuery(id+"F0.wireOp",EDGE,"E1189"),sQuery(id+"F0.wireOp",EDGE,"E1190"),sQuery(id+"F0.wireOp",EDGE,"E1191"),sQuery(id+"F0.wireOp",EDGE,"E1192"),sQuery(id+"F0.wireOp",EDGE,"E1193"),sQuery(id+"F0.wireOp",EDGE,"E1194"),sQuery(id+"F0.wireOp",EDGE,"E1195"),sQuery(id+"F0.wireOp",EDGE,"E1196"),sQuery(id+"F0.wireOp",EDGE,"E1197"),sQuery(id+"F0.wireOp",EDGE,"E1198"),sQuery(id+"F0.wireOp",EDGE,"E1199"),sQuery(id+"F0.wireOp",EDGE,"E1200"),sQuery(id+"F0.wireOp",EDGE,"E1201"),sQuery(id+"F0.wireOp",EDGE,"E1202"),sQuery(id+"F0.wireOp",EDGE,"E1203"),sQuery(id+"F0.wireOp",EDGE,"E1204"),sQuery(id+"F0.wireOp",EDGE,"E1205"),sQuery(id+"F0.wireOp",EDGE,"E1206"),sQuery(id+"F0.wireOp",EDGE,"E1207"),sQuery(id+"F0.wireOp",EDGE,"E1208"),sQuery(id+"F0.wireOp",EDGE,"E1209"),sQuery(id+"F0.wireOp",EDGE,"E1210"),sQuery(id+"F0.wireOp",EDGE,"E1211"),sQuery(id+"F0.wireOp",EDGE,"E1212"),sQuery(id+"F0.wireOp",EDGE,"E1213"),sQuery(id+"F0.wireOp",EDGE,"E1214"),sQuery(id+"F0.wireOp",EDGE,"E1215"),sQuery(id+"F0.wireOp",EDGE,"E1216"),sQuery(id+"F0.wireOp",EDGE,"E1217"),sQuery(id+"F0.wireOp",EDGE,"E1218"),sQuery(id+"F0.wireOp",EDGE,"E1219"),sQuery(id+"F0.wireOp",EDGE,"E1220"),sQuery(id+"F0.wireOp",EDGE,"E1221"),sQuery(id+"F0.wireOp",EDGE,"E1222"),sQuery(id+"F0.wireOp",EDGE,"E1223"),sQuery(id+"F0.wireOp",EDGE,"E1224"),sQuery(id+"F0.wireOp",EDGE,"E1225"),sQuery(id+"F0.wireOp",EDGE,"E1226"),sQuery(id+"F0.wireOp",EDGE,"E1227"),sQuery(id+"F0.wireOp",EDGE,"E1228"),sQuery(id+"F0.wireOp",EDGE,"E1229"),sQuery(id+"F0.wireOp",EDGE,"E1230"),sQuery(id+"F0.wireOp",EDGE,"E1231"),sQuery(id+"F0.wireOp",EDGE,"E1232"),sQuery(id+"F0.wireOp",EDGE,"E1233"),sQuery(id+"F0.wireOp",EDGE,"E1234"),sQuery(id+"F0.wireOp",EDGE,"E1235"),sQuery(id+"F0.wireOp",EDGE,"E1236"),sQuery(id+"F0.wireOp",EDGE,"E1237"),sQuery(id+"F0.wireOp",EDGE,"E1238"),sQuery(id+"F0.wireOp",EDGE,"E1239"),sQuery(id+"F0.wireOp",EDGE,"E1240"),sQuery(id+"F0.wireOp",EDGE,"E1241"),sQuery(id+"F0.wireOp",EDGE,"E1242"),sQuery(id+"F0.wireOp",EDGE,"E1243"),sQuery(id+"F0.wireOp",EDGE,"E1244"),sQuery(id+"F0.wireOp",EDGE,"E1245"),sQuery(id+"F0.wireOp",EDGE,"E1246"),sQuery(id+"F0.wireOp",EDGE,"E1247"),sQuery(id+"F0.wireOp",EDGE,"E1248"),sQuery(id+"F0.wireOp",EDGE,"E1249"),sQuery(id+"F0.wireOp",EDGE,"E1250"),sQuery(id+"F0.wireOp",EDGE,"E1251"),sQuery(id+"F0.wireOp",EDGE,"E1252"),sQuery(id+"F0.wireOp",EDGE,"E1253"),sQuery(id+"F0.wireOp",EDGE,"E1254"),sQuery(id+"F0.wireOp",EDGE,"E1255"),sQuery(id+"F0.wireOp",EDGE,"E1256"),sQuery(id+"F0.wireOp",EDGE,"E1257"),sQuery(id+"F0.wireOp",EDGE,"E1258"),sQuery(id+"F0.wireOp",EDGE,"E1259"),sQuery(id+"F0.wireOp",EDGE,"E1260"),sQuery(id+"F0.wireOp",EDGE,"E1261"),sQuery(id+"F0.wireOp",EDGE,"E1262"),sQuery(id+"F0.wireOp",EDGE,"E1263"),sQuery(id+"F0.wireOp",EDGE,"E1264"),sQuery(id+"F0.wireOp",EDGE,"E1265"),sQuery(id+"F0.wireOp",EDGE,"E1266"),sQuery(id+"F0.wireOp",EDGE,"E1267"),sQuery(id+"F0.wireOp",EDGE,"E1268"),sQuery(id+"F0.wireOp",EDGE,"E1269"),sQuery(id+"F0.wireOp",EDGE,"E1270"),sQuery(id+"F0.wireOp",EDGE,"E1271"),sQuery(id+"F0.wireOp",EDGE,"E1272"),sQuery(id+"F0.wireOp",EDGE,"E1273"),sQuery(id+"F0.wireOp",EDGE,"E1274"),sQuery(id+"F0.wireOp",EDGE,"E1275"),sQuery(id+"F0.wireOp",EDGE,"E1276"),sQuery(id+"F0.wireOp",EDGE,"E1277"),sQuery(id+"F0.wireOp",EDGE,"E1278"),sQuery(id+"F0.wireOp",EDGE,"E1279"),sQuery(id+"F0.wireOp",EDGE,"E1280"),sQuery(id+"F0.wireOp",EDGE,"E1281"),sQuery(id+"F0.wireOp",EDGE,"E1282"),sQuery(id+"F0.wireOp",EDGE,"E1283"),sQuery(id+"F0.wireOp",EDGE,"E1284"),sQuery(id+"F0.wireOp",EDGE,"E1285"),sQuery(id+"F0.wireOp",EDGE,"E1286"),sQuery(id+"F0.wireOp",EDGE,"E1287"),sQuery(id+"F0.wireOp",EDGE,"E1288"),sQuery(id+"F0.wireOp",EDGE,"E1289"),sQuery(id+"F0.wireOp",EDGE,"E1290"),sQuery(id+"F0.wireOp",EDGE,"E1291"),sQuery(id+"F0.wireOp",EDGE,"E1292"),sQuery(id+"F0.wireOp",EDGE,"E1293"),sQuery(id+"F0.wireOp",EDGE,"E1294"),sQuery(id+"F0.wireOp",EDGE,"E1295"),sQuery(id+"F0.wireOp",EDGE,"E1296"),sQuery(id+"F0.wireOp",EDGE,"E1297"),sQuery(id+"F0.wireOp",EDGE,"E1298"),sQuery(id+"F0.wireOp",EDGE,"E1299"),sQuery(id+"F0.wireOp",EDGE,"E1300"),sQuery(id+"F0.wireOp",EDGE,"E1301"),sQuery(id+"F0.wireOp",EDGE,"E1302"),sQuery(id+"F0.wireOp",EDGE,"E1303"),sQuery(id+"F0.wireOp",EDGE,"E1304"),sQuery(id+"F0.wireOp",EDGE,"E1305"),sQuery(id+"F0.wireOp",EDGE,"E1306"),sQuery(id+"F0.wireOp",EDGE,"E1307"),sQuery(id+"F0.wireOp",EDGE,"E1308"),sQuery(id+"F0.wireOp",EDGE,"E1309"),sQuery(id+"F0.wireOp",EDGE,"E1310"),sQuery(id+"F0.wireOp",EDGE,"E1311"),sQuery(id+"F0.wireOp",EDGE,"E1312"),sQuery(id+"F0.wireOp",EDGE,"E1313"),sQuery(id+"F0.wireOp",EDGE,"E1314"),sQuery(id+"F0.wireOp",EDGE,"E1315"),sQuery(id+"F0.wireOp",EDGE,"E1316"),sQuery(id+"F0.wireOp",EDGE,"E1317"),sQuery(id+"F0.wireOp",EDGE,"E1318"),sQuery(id+"F0.wireOp",EDGE,"E1319"),sQuery(id+"F0.wireOp",EDGE,"E1320"),sQuery(id+"F0.wireOp",EDGE,"E1321"),sQuery(id+"F0.wireOp",EDGE,"E1322"),sQuery(id+"F0.wireOp",EDGE,"E1323"),sQuery(id+"F0.wireOp",EDGE,"E1324"),sQuery(id+"F0.wireOp",EDGE,"E1325"),sQuery(id+"F0.wireOp",EDGE,"E1326"),sQuery(id+"F0.wireOp",EDGE,"E1327"),sQuery(id+"F0.wireOp",EDGE,"E1328"),sQuery(id+"F0.wireOp",EDGE,"E1329"),sQuery(id+"F0.wireOp",EDGE,"E1330"),sQuery(id+"F0.wireOp",EDGE,"E1331"),sQuery(id+"F0.wireOp",EDGE,"E1332"),sQuery(id+"F0.wireOp",EDGE,"E1333"),sQuery(id+"F0.wireOp",EDGE,"E1334"),sQuery(id+"F0.wireOp",EDGE,"E1335"),sQuery(id+"F0.wireOp",EDGE,"E1336"),sQuery(id+"F0.wireOp",EDGE,"E1337"),sQuery(id+"F0.wireOp",EDGE,"E1338"),sQuery(id+"F0.wireOp",EDGE,"E1339"),sQuery(id+"F0.wireOp",EDGE,"E1340"),sQuery(id+"F0.wireOp",EDGE,"E1341"),sQuery(id+"F0.wireOp",EDGE,"E1342"),sQuery(id+"F0.wireOp",EDGE,"E1343"),sQuery(id+"F0.wireOp",EDGE,"E1344"),sQuery(id+"F0.wireOp",EDGE,"E1345"),sQuery(id+"F0.wireOp",EDGE,"E1346"),sQuery(id+"F0.wireOp",EDGE,"E1347"),sQuery(id+"F0.wireOp",EDGE,"E1348"),sQuery(id+"F0.wireOp",EDGE,"E1349"),sQuery(id+"F0.wireOp",EDGE,"E1350"),sQuery(id+"F0.wireOp",EDGE,"E1351"),sQuery(id+"F0.wireOp",EDGE,"E1352"),sQuery(id+"F0.wireOp",EDGE,"E1353"),sQuery(id+"F0.wireOp",EDGE,"E1354"),sQuery(id+"F0.wireOp",EDGE,"E1355"),sQuery(id+"F0.wireOp",EDGE,"E1356"),sQuery(id+"F0.wireOp",EDGE,"E1357"),sQuery(id+"F0.wireOp",EDGE,"E1358"),sQuery(id+"F0.wireOp",EDGE,"E1359"),sQuery(id+"F0.wireOp",EDGE,"E1360"),sQuery(id+"F0.wireOp",EDGE,"E1361"),sQuery(id+"F0.wireOp",EDGE,"E1362"),sQuery(id+"F0.wireOp",EDGE,"E1363"),sQuery(id+"F0.wireOp",EDGE,"E1364"),sQuery(id+"F0.wireOp",EDGE,"E1365"),sQuery(id+"F0.wireOp",EDGE,"E1366"),sQuery(id+"F0.wireOp",EDGE,"E1367"),sQuery(id+"F0.wireOp",EDGE,"E1368"),sQuery(id+"F0.wireOp",EDGE,"E1369"),sQuery(id+"F0.wireOp",EDGE,"E1370"),sQuery(id+"F0.wireOp",EDGE,"E1371"),sQuery(id+"F0.wireOp",EDGE,"E1372"),sQuery(id+"F0.wireOp",EDGE,"E1373"),sQuery(id+"F0.wireOp",EDGE,"E1374"),sQuery(id+"F0.wireOp",EDGE,"E1375"),sQuery(id+"F0.wireOp",EDGE,"E1376"),sQuery(id+"F0.wireOp",EDGE,"E1377"),sQuery(id+"F0.wireOp",EDGE,"E1378"),sQuery(id+"F0.wireOp",EDGE,"E1379"),sQuery(id+"F0.wireOp",EDGE,"E1380"),sQuery(id+"F0.wireOp",EDGE,"E1381"),sQuery(id+"F0.wireOp",EDGE,"E1382"),sQuery(id+"F0.wireOp",EDGE,"E1383"),sQuery(id+"F0.wireOp",EDGE,"E1384"),sQuery(id+"F0.wireOp",EDGE,"E1385"),sQuery(id+"F0.wireOp",EDGE,"E1386"),sQuery(id+"F0.wireOp",EDGE,"E1387"),sQuery(id+"F0.wireOp",EDGE,"E1388"),sQuery(id+"F0.wireOp",EDGE,"E1389"),sQuery(id+"F0.wireOp",EDGE,"E1390"),sQuery(id+"F0.wireOp",EDGE,"E1391"),sQuery(id+"F0.wireOp",EDGE,"E1392"),sQuery(id+"F0.wireOp",EDGE,"E1393"),sQuery(id+"F0.wireOp",EDGE,"E1394"),sQuery(id+"F0.wireOp",EDGE,"E1395"),sQuery(id+"F0.wireOp",EDGE,"E1396"),sQuery(id+"F0.wireOp",EDGE,"E1397"),sQuery(id+"F0.wireOp",EDGE,"E1398"),sQuery(id+"F0.wireOp",EDGE,"E1399"),sQuery(id+"F0.wireOp",EDGE,"E1400"),sQuery(id+"F0.wireOp",EDGE,"E1401"),sQuery(id+"F0.wireOp",EDGE,"E1402"),sQuery(id+"F0.wireOp",EDGE,"E1403"),sQuery(id+"F0.wireOp",EDGE,"E1404"),sQuery(id+"F0.wireOp",EDGE,"E1405"),sQuery(id+"F0.wireOp",EDGE,"E1406"),sQuery(id+"F0.wireOp",EDGE,"E1407"),sQuery(id+"F0.wireOp",EDGE,"E1408"),sQuery(id+"F0.wireOp",EDGE,"E1409"),sQuery(id+"F0.wireOp",EDGE,"E1410"),sQuery(id+"F0.wireOp",EDGE,"E1411"),sQuery(id+"F0.wireOp",EDGE,"E1412"),sQuery(id+"F0.wireOp",EDGE,"E1413"),sQuery(id+"F0.wireOp",EDGE,"E1414"),sQuery(id+"F0.wireOp",EDGE,"E1415"),sQuery(id+"F0.wireOp",EDGE,"E1416"),sQuery(id+"F0.wireOp",EDGE,"E1417"),sQuery(id+"F0.wireOp",EDGE,"E1418"),sQuery(id+"F0.wireOp",EDGE,"E1419"),sQuery(id+"F0.wireOp",EDGE,"E1420"),sQuery(id+"F0.wireOp",EDGE,"E1421"),sQuery(id+"F0.wireOp",EDGE,"E1422"),sQuery(id+"F0.wireOp",EDGE,"E1423"),sQuery(id+"F0.wireOp",EDGE,"E1424"),sQuery(id+"F0.wireOp",EDGE,"E1425"),sQuery(id+"F0.wireOp",EDGE,"E1426"),sQuery(id+"F0.wireOp",EDGE,"E1427"),sQuery(id+"F0.wireOp",EDGE,"E1428"),sQuery(id+"F0.wireOp",EDGE,"E1429"),sQuery(id+"F0.wireOp",EDGE,"E1430"),sQuery(id+"F0.wireOp",EDGE,"E1431"),sQuery(id+"F0.wireOp",EDGE,"E1432"),sQuery(id+"F0.wireOp",EDGE,"E1433"),sQuery(id+"F0.wireOp",EDGE,"E1434"),sQuery(id+"F0.wireOp",EDGE,"E1435"),sQuery(id+"F0.wireOp",EDGE,"E1436"),sQuery(id+"F0.wireOp",EDGE,"E1437"),sQuery(id+"F0.wireOp",EDGE,"E1438"),sQuery(id+"F0.wireOp",EDGE,"E1439"),sQuery(id+"F0.wireOp",EDGE,"E1440"),sQuery(id+"F0.wireOp",EDGE,"E1441"),sQuery(id+"F0.wireOp",EDGE,"E1442"),sQuery(id+"F0.wireOp",EDGE,"E1443"),sQuery(id+"F0.wireOp",EDGE,"E1444"),sQuery(id+"F0.wireOp",EDGE,"E1445"),sQuery(id+"F0.wireOp",EDGE,"E1446"),sQuery(id+"F0.wireOp",EDGE,"E1447"),sQuery(id+"F0.wireOp",EDGE,"E1448"),sQuery(id+"F0.wireOp",EDGE,"E1449"),sQuery(id+"F0.wireOp",EDGE,"E1450"),sQuery(id+"F0.wireOp",EDGE,"E1451"),sQuery(id+"F0.wireOp",EDGE,"E1452"),sQuery(id+"F0.wireOp",EDGE,"E1453"),sQuery(id+"F0.wireOp",EDGE,"E1454"),sQuery(id+"F0.wireOp",EDGE,"E1455"),sQuery(id+"F0.wireOp",EDGE,"E1456"),sQuery(id+"F0.wireOp",EDGE,"E1457"),sQuery(id+"F0.wireOp",EDGE,"E1458"),sQuery(id+"F0.wireOp",EDGE,"E1459"),sQuery(id+"F0.wireOp",EDGE,"E1460"),sQuery(id+"F0.wireOp",EDGE,"E1461"),sQuery(id+"F0.wireOp",EDGE,"E1462"),sQuery(id+"F0.wireOp",EDGE,"E1463"),sQuery(id+"F0.wireOp",EDGE,"E1464"),sQuery(id+"F0.wireOp",EDGE,"E1465"),sQuery(id+"F0.wireOp",EDGE,"E1466"),sQuery(id+"F0.wireOp",EDGE,"E1467"),sQuery(id+"F0.wireOp",EDGE,"E1468"),sQuery(id+"F0.wireOp",EDGE,"E1469"),sQuery(id+"F0.wireOp",EDGE,"E1470"),sQuery(id+"F0.wireOp",EDGE,"E1471"),sQuery(id+"F0.wireOp",EDGE,"E1472"),sQuery(id+"F0.wireOp",EDGE,"E1473"),sQuery(id+"F0.wireOp",EDGE,"E1474"),sQuery(id+"F0.wireOp",EDGE,"E1475"),sQuery(id+"F0.wireOp",EDGE,"E1476"),sQuery(id+"F0.wireOp",EDGE,"E1477"),sQuery(id+"F0.wireOp",EDGE,"E1478"),sQuery(id+"F0.wireOp",EDGE,"E1479"),sQuery(id+"F0.wireOp",EDGE,"E1480"),sQuery(id+"F0.wireOp",EDGE,"E1481"),sQuery(id+"F0.wireOp",EDGE,"E1482"),sQuery(id+"F0.wireOp",EDGE,"E1483"),sQuery(id+"F0.wireOp",EDGE,"E1484"),sQuery(id+"F0.wireOp",EDGE,"E1485"),sQuery(id+"F0.wireOp",EDGE,"E1486"),sQuery(id+"F0.wireOp",EDGE,"E1487"),sQuery(id+"F0.wireOp",EDGE,"E1488"),sQuery(id+"F0.wireOp",EDGE,"E1489"),sQuery(id+"F0.wireOp",EDGE,"E1490"),sQuery(id+"F0.wireOp",EDGE,"E1491"),sQuery(id+"F0.wireOp",EDGE,"E1492"),sQuery(id+"F0.wireOp",EDGE,"E1493"),sQuery(id+"F0.wireOp",EDGE,"E1494"),sQuery(id+"F0.wireOp",EDGE,"E1495"),sQuery(id+"F0.wireOp",EDGE,"E1496"),sQuery(id+"F0.wireOp",EDGE,"E1497"),sQuery(id+"F0.wireOp",EDGE,"E1498"),sQuery(id+"F0.wireOp",EDGE,"E1499"),sQuery(id+"F0.wireOp",EDGE,"E1500"),sQuery(id+"F0.wireOp",EDGE,"E1501"),sQuery(id+"F0.wireOp",EDGE,"E1502"),sQuery(id+"F0.wireOp",EDGE,"E1503"),sQuery(id+"F0.wireOp",EDGE,"E1504"),sQuery(id+"F0.wireOp",EDGE,"E1505"),sQuery(id+"F0.wireOp",EDGE,"E1506"),sQuery(id+"F0.wireOp",EDGE,"E1507"),sQuery(id+"F0.wireOp",EDGE,"E1508"),sQuery(id+"F0.wireOp",EDGE,"E1509"),sQuery(id+"F0.wireOp",EDGE,"E1510"),sQuery(id+"F0.wireOp",EDGE,"E1511"),sQuery(id+"F0.wireOp",EDGE,"E1512"),sQuery(id+"F0.wireOp",EDGE,"E1513"),sQuery(id+"F0.wireOp",EDGE,"E1514"),sQuery(id+"F0.wireOp",EDGE,"E1515"),sQuery(id+"F0.wireOp",EDGE,"E1516"),sQuery(id+"F0.wireOp",EDGE,"E1517"),sQuery(id+"F0.wireOp",EDGE,"E1518"),sQuery(id+"F0.wireOp",EDGE,"E1519"),sQuery(id+"F0.wireOp",EDGE,"E1520"),sQuery(id+"F0.wireOp",EDGE,"E1521"),sQuery(id+"F0.wireOp",EDGE,"E1522"),sQuery(id+"F0.wireOp",EDGE,"E1523"),sQuery(id+"F0.wireOp",EDGE,"E1524"),sQuery(id+"F0.wireOp",EDGE,"E1525"),sQuery(id+"F0.wireOp",EDGE,"E1526"),sQuery(id+"F0.wireOp",EDGE,"E1527"),sQuery(id+"F0.wireOp",EDGE,"E1528"),sQuery(id+"F0.wireOp",EDGE,"E1529"),sQuery(id+"F0.wireOp",EDGE,"E1530"),sQuery(id+"F0.wireOp",EDGE,"E1531"),sQuery(id+"F0.wireOp",EDGE,"E1532"),sQuery(id+"F0.wireOp",EDGE,"E1533"),sQuery(id+"F0.wireOp",EDGE,"E1534"),sQuery(id+"F0.wireOp",EDGE,"E1535"),sQuery(id+"F0.wireOp",EDGE,"E1536"),sQuery(id+"F0.wireOp",EDGE,"E1537"),sQuery(id+"F0.wireOp",EDGE,"E1538"),sQuery(id+"F0.wireOp",EDGE,"E1539"),sQuery(id+"F0.wireOp",EDGE,"E1540"),sQuery(id+"F0.wireOp",EDGE,"E1541"),sQuery(id+"F0.wireOp",EDGE,"E1542"),sQuery(id+"F0.wireOp",EDGE,"E1543"),sQuery(id+"F0.wireOp",EDGE,"E1544"),sQuery(id+"F0.wireOp",EDGE,"E1545"),sQuery(id+"F0.wireOp",EDGE,"E1546"),sQuery(id+"F0.wireOp",EDGE,"E1547"),sQuery(id+"F0.wireOp",EDGE,"E1548"),sQuery(id+"F0.wireOp",EDGE,"E1549"),sQuery(id+"F0.wireOp",EDGE,"E1550"),sQuery(id+"F0.wireOp",EDGE,"E1551"),sQuery(id+"F0.wireOp",EDGE,"E1552"),sQuery(id+"F0.wireOp",EDGE,"E1553"),sQuery(id+"F0.wireOp",EDGE,"E1554"),sQuery(id+"F0.wireOp",EDGE,"E1555"),sQuery(id+"F0.wireOp",EDGE,"E1556"),sQuery(id+"F0.wireOp",EDGE,"E1557"),sQuery(id+"F0.wireOp",EDGE,"E1558"),sQuery(id+"F0.wireOp",EDGE,"E1559"),sQuery(id+"F0.wireOp",EDGE,"E1560"),sQuery(id+"F0.wireOp",EDGE,"E1561"),sQuery(id+"F0.wireOp",EDGE,"E1562"),sQuery(id+"F0.wireOp",EDGE,"E1563"),sQuery(id+"F0.wireOp",EDGE,"E1564"),sQuery(id+"F0.wireOp",EDGE,"E1565"),sQuery(id+"F0.wireOp",EDGE,"E1566"),sQuery(id+"F0.wireOp",EDGE,"E1567"),sQuery(id+"F0.wireOp",EDGE,"E1568"),sQuery(id+"F0.wireOp",EDGE,"E1569"),sQuery(id+"F0.wireOp",EDGE,"E1570"),sQuery(id+"F0.wireOp",EDGE,"E1571"),sQuery(id+"F0.wireOp",EDGE,"E1572"),sQuery(id+"F0.wireOp",EDGE,"E1573"),sQuery(id+"F0.wireOp",EDGE,"E1574"),sQuery(id+"F0.wireOp",EDGE,"E1575"),sQuery(id+"F0.wireOp",EDGE,"E1576"),sQuery(id+"F0.wireOp",EDGE,"E1577"),sQuery(id+"F0.wireOp",EDGE,"E1578"),sQuery(id+"F0.wireOp",EDGE,"E1579"),sQuery(id+"F0.wireOp",EDGE,"E1580"),sQuery(id+"F0.wireOp",EDGE,"E1581"),sQuery(id+"F0.wireOp",EDGE,"E1582"),sQuery(id+"F0.wireOp",EDGE,"E1583"),sQuery(id+"F0.wireOp",EDGE,"E1584"),sQuery(id+"F0.wireOp",EDGE,"E1585"),sQuery(id+"F0.wireOp",EDGE,"E1586"),sQuery(id+"F0.wireOp",EDGE,"E1587"),sQuery(id+"F0.wireOp",EDGE,"E1588"),sQuery(id+"F0.wireOp",EDGE,"E1589"),sQuery(id+"F0.wireOp",EDGE,"E1590"),sQuery(id+"F0.wireOp",EDGE,"E1591"),sQuery(id+"F0.wireOp",EDGE,"E1592"),sQuery(id+"F0.wireOp",EDGE,"E1593"),sQuery(id+"F0.wireOp",EDGE,"E1594"),sQuery(id+"F0.wireOp",EDGE,"E1595"),sQuery(id+"F0.wireOp",EDGE,"E1596"),sQuery(id+"F0.wireOp",EDGE,"E1597"),sQuery(id+"F0.wireOp",EDGE,"E1598"),sQuery(id+"F0.wireOp",EDGE,"E1599"),sQuery(id+"F0.wireOp",EDGE,"E1600"),sQuery(id+"F0.wireOp",EDGE,"E1601"),sQuery(id+"F0.wireOp",EDGE,"E1602"),sQuery(id+"F0.wireOp",EDGE,"E1603"),sQuery(id+"F0.wireOp",EDGE,"E1604"),sQuery(id+"F0.wireOp",EDGE,"E1605"),sQuery(id+"F0.wireOp",EDGE,"E1606"),sQuery(id+"F0.wireOp",EDGE,"E1607"),sQuery(id+"F0.wireOp",EDGE,"E1608"),sQuery(id+"F0.wireOp",EDGE,"E1609"),sQuery(id+"F0.wireOp",EDGE,"E1610"),sQuery(id+"F0.wireOp",EDGE,"E1611"),sQuery(id+"F0.wireOp",EDGE,"E1612"),sQuery(id+"F0.wireOp",EDGE,"E1613"),sQuery(id+"F0.wireOp",EDGE,"E1614"),sQuery(id+"F0.wireOp",EDGE,"E1615"),sQuery(id+"F0.wireOp",EDGE,"E1616"),sQuery(id+"F0.wireOp",EDGE,"E1617"),sQuery(id+"F0.wireOp",EDGE,"E1618"),sQuery(id+"F0.wireOp",EDGE,"E1619"),sQuery(id+"F0.wireOp",EDGE,"E1620"),sQuery(id+"F0.wireOp",EDGE,"E1621"),sQuery(id+"F0.wireOp",EDGE,"E1622"),sQuery(id+"F0.wireOp",EDGE,"E1623"),sQuery(id+"F0.wireOp",EDGE,"E1624"),sQuery(id+"F0.wireOp",EDGE,"E1625"),sQuery(id+"F0.wireOp",EDGE,"E1626"),sQuery(id+"F0.wireOp",EDGE,"E1627"),sQuery(id+"F0.wireOp",EDGE,"E1628"),sQuery(id+"F0.wireOp",EDGE,"E1629"),sQuery(id+"F0.wireOp",EDGE,"E1630"),sQuery(id+"F0.wireOp",EDGE,"E1631"),sQuery(id+"F0.wireOp",EDGE,"E1632"),sQuery(id+"F0.wireOp",EDGE,"E1633"),sQuery(id+"F0.wireOp",EDGE,"E1634"),sQuery(id+"F0.wireOp",EDGE,"E1635"),sQuery(id+"F0.wireOp",EDGE,"E1636"),sQuery(id+"F0.wireOp",EDGE,"E1637"),sQuery(id+"F0.wireOp",EDGE,"E1638"),sQuery(id+"F0.wireOp",EDGE,"E1639"),sQuery(id+"F0.wireOp",EDGE,"E1640"),sQuery(id+"F0.wireOp",EDGE,"E1641"),sQuery(id+"F0.wireOp",EDGE,"E1642"),sQuery(id+"F0.wireOp",EDGE,"E1643"),sQuery(id+"F0.wireOp",EDGE,"E1644"),sQuery(id+"F0.wireOp",EDGE,"E1645"),sQuery(id+"F0.wireOp",EDGE,"E1646"),sQuery(id+"F0.wireOp",EDGE,"E1647"),sQuery(id+"F0.wireOp",EDGE,"E1648"),sQuery(id+"F0.wireOp",EDGE,"E1649"),sQuery(id+"F0.wireOp",EDGE,"E1650"),sQuery(id+"F0.wireOp",EDGE,"E1651"),sQuery(id+"F0.wireOp",EDGE,"E1652"),sQuery(id+"F0.wireOp",EDGE,"E1653"),sQuery(id+"F0.wireOp",EDGE,"E1654"),sQuery(id+"F0.wireOp",EDGE,"E1655"),sQuery(id+"F0.wireOp",EDGE,"E1656"),sQuery(id+"F0.wireOp",EDGE,"E1657"),sQuery(id+"F0.wireOp",EDGE,"E1658"),sQuery(id+"F0.wireOp",EDGE,"E1659"),sQuery(id+"F0.wireOp",EDGE,"E1660"),sQuery(id+"F0.wireOp",EDGE,"E1661"),sQuery(id+"F0.wireOp",EDGE,"E1662"),sQuery(id+"F0.wireOp",EDGE,"E1663"),sQuery(id+"F0.wireOp",EDGE,"E1664"),sQuery(id+"F0.wireOp",EDGE,"E1665"),sQuery(id+"F0.wireOp",EDGE,"E1666"),sQuery(id+"F0.wireOp",EDGE,"E1667"),sQuery(id+"F0.wireOp",EDGE,"E1668"),sQuery(id+"F0.wireOp",EDGE,"E1669"),sQuery(id+"F0.wireOp",EDGE,"E1670"),sQuery(id+"F0.wireOp",EDGE,"E1671"),sQuery(id+"F0.wireOp",EDGE,"E1672"),sQuery(id+"F0.wireOp",EDGE,"E1673"),sQuery(id+"F0.wireOp",EDGE,"E1674"),sQuery(id+"F0.wireOp",EDGE,"E1675"),sQuery(id+"F0.wireOp",EDGE,"E1676"),sQuery(id+"F0.wireOp",EDGE,"E1677"),sQuery(id+"F0.wireOp",EDGE,"E1678"),sQuery(id+"F0.wireOp",EDGE,"E1679"),sQuery(id+"F0.wireOp",EDGE,"E1680"),sQuery(id+"F0.wireOp",EDGE,"E1681"),sQuery(id+"F0.wireOp",EDGE,"E1682"),sQuery(id+"F0.wireOp",EDGE,"E1683"),sQuery(id+"F0.wireOp",EDGE,"E1684"),sQuery(id+"F0.wireOp",EDGE,"E1685"),sQuery(id+"F0.wireOp",EDGE,"E1686"),sQuery(id+"F0.wireOp",EDGE,"E1687"),sQuery(id+"F0.wireOp",EDGE,"E1688"),sQuery(id+"F0.wireOp",EDGE,"E1689"),sQuery(id+"F0.wireOp",EDGE,"E1690"),sQuery(id+"F0.wireOp",EDGE,"E1691"),sQuery(id+"F0.wireOp",EDGE,"E1692"),sQuery(id+"F0.wireOp",EDGE,"E1693"),sQuery(id+"F0.wireOp",EDGE,"E1694"),sQuery(id+"F0.wireOp",EDGE,"E1695"),sQuery(id+"F0.wireOp",EDGE,"E1696"),sQuery(id+"F0.wireOp",EDGE,"E1697"),sQuery(id+"F0.wireOp",EDGE,"E1698"),sQuery(id+"F0.wireOp",EDGE,"E1699"),sQuery(id+"F0.wireOp",EDGE,"E1700"),sQuery(id+"F0.wireOp",EDGE,"E1701"),sQuery(id+"F0.wireOp",EDGE,"E1702"),sQuery(id+"F0.wireOp",EDGE,"E1703"),sQuery(id+"F0.wireOp",EDGE,"E1704"),sQuery(id+"F0.wireOp",EDGE,"E1705"),sQuery(id+"F0.wireOp",EDGE,"E1706"),sQuery(id+"F0.wireOp",EDGE,"E1707"),sQuery(id+"F0.wireOp",EDGE,"E1708"),sQuery(id+"F0.wireOp",EDGE,"E1709"),sQuery(id+"F0.wireOp",EDGE,"E1710"),sQuery(id+"F0.wireOp",EDGE,"E1711"),sQuery(id+"F0.wireOp",EDGE,"E1712"),sQuery(id+"F0.wireOp",EDGE,"E1713"),sQuery(id+"F0.wireOp",EDGE,"E1714"),sQuery(id+"F0.wireOp",EDGE,"E1715"),sQuery(id+"F0.wireOp",EDGE,"E1716"),sQuery(id+"F0.wireOp",EDGE,"E1717"),sQuery(id+"F0.wireOp",EDGE,"E1718"),sQuery(id+"F0.wireOp",EDGE,"E1719"),sQuery(id+"F0.wireOp",EDGE,"E1720"),sQuery(id+"F0.wireOp",EDGE,"E1721"),sQuery(id+"F0.wireOp",EDGE,"E1722"),sQuery(id+"F0.wireOp",EDGE,"E1723"),sQuery(id+"F0.wireOp",EDGE,"E1724"),sQuery(id+"F0.wireOp",EDGE,"E1725"),sQuery(id+"F0.wireOp",EDGE,"E1726"),sQuery(id+"F0.wireOp",EDGE,"E1727"),sQuery(id+"F0.wireOp",EDGE,"E1728"),sQuery(id+"F0.wireOp",EDGE,"E1729"),sQuery(id+"F0.wireOp",EDGE,"E1730"),sQuery(id+"F0.wireOp",EDGE,"E1731"),sQuery(id+"F0.wireOp",EDGE,"E1732"),sQuery(id+"F0.wireOp",EDGE,"E1733"),sQuery(id+"F0.wireOp",EDGE,"E1734"),sQuery(id+"F0.wireOp",EDGE,"E1735"),sQuery(id+"F0.wireOp",EDGE,"E1736"),sQuery(id+"F0.wireOp",EDGE,"E1737"),sQuery(id+"F0.wireOp",EDGE,"E1738"),sQuery(id+"F0.wireOp",EDGE,"E1739"),sQuery(id+"F0.wireOp",EDGE,"E1740"),sQuery(id+"F0.wireOp",EDGE,"E1741"),sQuery(id+"F0.wireOp",EDGE,"E1742"),sQuery(id+"F0.wireOp",EDGE,"E1743"),sQuery(id+"F0.wireOp",EDGE,"E1744"),sQuery(id+"F0.wireOp",EDGE,"E1745"),sQuery(id+"F0.wireOp",EDGE,"E1746"),sQuery(id+"F0.wireOp",EDGE,"E1747"),sQuery(id+"F0.wireOp",EDGE,"E1748"),sQuery(id+"F0.wireOp",EDGE,"E1749"),sQuery(id+"F0.wireOp",EDGE,"E1750"),sQuery(id+"F0.wireOp",EDGE,"E1751"),sQuery(id+"F0.wireOp",EDGE,"E1752"),sQuery(id+"F0.wireOp",EDGE,"E1753"),sQuery(id+"F0.wireOp",EDGE,"E1754"),sQuery(id+"F0.wireOp",EDGE,"E1755"),sQuery(id+"F0.wireOp",EDGE,"E1756"),sQuery(id+"F0.wireOp",EDGE,"E1757"),sQuery(id+"F0.wireOp",EDGE,"E1758"),sQuery(id+"F0.wireOp",EDGE,"E1759"),sQuery(id+"F0.wireOp",EDGE,"E1760"),sQuery(id+"F0.wireOp",EDGE,"E1761"),sQuery(id+"F0.wireOp",EDGE,"E1762"),sQuery(id+"F0.wireOp",EDGE,"E1763"),sQuery(id+"F0.wireOp",EDGE,"E1764"),sQuery(id+"F0.wireOp",EDGE,"E1765"),sQuery(id+"F0.wireOp",EDGE,"E1766"),sQuery(id+"F0.wireOp",EDGE,"E1767"),sQuery(id+"F0.wireOp",EDGE,"E1768"),sQuery(id+"F0.wireOp",EDGE,"E1769"),sQuery(id+"F0.wireOp",EDGE,"E1770"),sQuery(id+"F0.wireOp",EDGE,"E1771"),sQuery(id+"F0.wireOp",EDGE,"E1772"),sQuery(id+"F0.wireOp",EDGE,"E1773"),sQuery(id+"F0.wireOp",EDGE,"E1774"),sQuery(id+"F0.wireOp",EDGE,"E1775"),sQuery(id+"F0.wireOp",EDGE,"E1776"),sQuery(id+"F0.wireOp",EDGE,"E1777"),sQuery(id+"F0.wireOp",EDGE,"E1778"),sQuery(id+"F0.wireOp",EDGE,"E1779"),sQuery(id+"F0.wireOp",EDGE,"E1780"),sQuery(id+"F0.wireOp",EDGE,"E1781"),sQuery(id+"F0.wireOp",EDGE,"E1782"),sQuery(id+"F0.wireOp",EDGE,"E1783"),sQuery(id+"F0.wireOp",EDGE,"E1784"),sQuery(id+"F0.wireOp",EDGE,"E1785"),sQuery(id+"F0.wireOp",EDGE,"E1786"),sQuery(id+"F0.wireOp",EDGE,"E1787"),sQuery(id+"F0.wireOp",EDGE,"E1788"),sQuery(id+"F0.wireOp",EDGE,"E1789"),sQuery(id+"F0.wireOp",EDGE,"E1790"),sQuery(id+"F0.wireOp",EDGE,"E1791"),sQuery(id+"F0.wireOp",EDGE,"E1792"),sQuery(id+"F0.wireOp",EDGE,"E1793"),sQuery(id+"F0.wireOp",EDGE,"E1794"),sQuery(id+"F0.wireOp",EDGE,"E1795"),sQuery(id+"F0.wireOp",EDGE,"E1796"),sQuery(id+"F0.wireOp",EDGE,"E1797"),sQuery(id+"F0.wireOp",EDGE,"E1798"),sQuery(id+"F0.wireOp",EDGE,"E1799"),sQuery(id+"F0.wireOp",EDGE,"E1800"),sQuery(id+"F0.wireOp",EDGE,"E1801"),sQuery(id+"F0.wireOp",EDGE,"E1802"),sQuery(id+"F0.wireOp",EDGE,"E1803"),sQuery(id+"F0.wireOp",EDGE,"E1804"),sQuery(id+"F0.wireOp",EDGE,"E1805"),sQuery(id+"F0.wireOp",EDGE,"E1806"),sQuery(id+"F0.wireOp",EDGE,"E1807"),sQuery(id+"F0.wireOp",EDGE,"E1808"),sQuery(id+"F0.wireOp",EDGE,"E1809"),sQuery(id+"F0.wireOp",EDGE,"E1810"),sQuery(id+"F0.wireOp",EDGE,"E1811"),sQuery(id+"F0.wireOp",EDGE,"E1812"),sQuery(id+"F0.wireOp",EDGE,"E1813"),sQuery(id+"F0.wireOp",EDGE,"E1814"),sQuery(id+"F0.wireOp",EDGE,"E1815"),sQuery(id+"F0.wireOp",EDGE,"E1816"),sQuery(id+"F0.wireOp",EDGE,"E1817"),sQuery(id+"F0.wireOp",EDGE,"E1818"),sQuery(id+"F0.wireOp",EDGE,"E1819"),sQuery(id+"F0.wireOp",EDGE,"E1820"),sQuery(id+"F0.wireOp",EDGE,"E1821"),sQuery(id+"F0.wireOp",EDGE,"E1822"),sQuery(id+"F0.wireOp",EDGE,"E1823"),sQuery(id+"F0.wireOp",EDGE,"E1824"),sQuery(id+"F0.wireOp",EDGE,"E1825"),sQuery(id+"F0.wireOp",EDGE,"E1826"),sQuery(id+"F0.wireOp",EDGE,"E1827"),sQuery(id+"F0.wireOp",EDGE,"E1828"),sQuery(id+"F0.wireOp",EDGE,"E1829"),sQuery(id+"F0.wireOp",EDGE,"E1830"),sQuery(id+"F0.wireOp",EDGE,"E1831"),sQuery(id+"F0.wireOp",EDGE,"E1832"),sQuery(id+"F0.wireOp",EDGE,"E1833"),sQuery(id+"F0.wireOp",EDGE,"E1834"),sQuery(id+"F0.wireOp",EDGE,"E1835"),sQuery(id+"F0.wireOp",EDGE,"E1836"),sQuery(id+"F0.wireOp",EDGE,"E1837"),sQuery(id+"F0.wireOp",EDGE,"E1838"),sQuery(id+"F0.wireOp",EDGE,"E1839"),sQuery(id+"F0.wireOp",EDGE,"E1840"),sQuery(id+"F0.wireOp",EDGE,"E1841"),sQuery(id+"F0.wireOp",EDGE,"E1842"),sQuery(id+"F0.wireOp",EDGE,"E1843"),sQuery(id+"F0.wireOp",EDGE,"E1844"),sQuery(id+"F0.wireOp",EDGE,"E1845"),sQuery(id+"F0.wireOp",EDGE,"E1846"),sQuery(id+"F0.wireOp",EDGE,"E1847"),sQuery(id+"F0.wireOp",EDGE,"E1848"),sQuery(id+"F0.wireOp",EDGE,"E1849"),sQuery(id+"F0.wireOp",EDGE,"E1850"),sQuery(id+"F0.wireOp",EDGE,"E1851"),sQuery(id+"F0.wireOp",EDGE,"E1852"),sQuery(id+"F0.wireOp",EDGE,"E1853"),sQuery(id+"F0.wireOp",EDGE,"E1854"),sQuery(id+"F0.wireOp",EDGE,"E1855"),sQuery(id+"F0.wireOp",EDGE,"E1856"),sQuery(id+"F0.wireOp",EDGE,"E1857"),sQuery(id+"F0.wireOp",EDGE,"E1858"),sQuery(id+"F0.wireOp",EDGE,"E1859"),sQuery(id+"F0.wireOp",EDGE,"E1860"),sQuery(id+"F0.wireOp",EDGE,"E1861"),sQuery(id+"F0.wireOp",EDGE,"E1862"),sQuery(id+"F0.wireOp",EDGE,"E1863"),sQuery(id+"F0.wireOp",EDGE,"E1864"),sQuery(id+"F0.wireOp",EDGE,"E1865"),sQuery(id+"F0.wireOp",EDGE,"E1866"),sQuery(id+"F0.wireOp",EDGE,"E1867"),sQuery(id+"F0.wireOp",EDGE,"E1868"),sQuery(id+"F0.wireOp",EDGE,"E1869"),sQuery(id+"F0.wireOp",EDGE,"E1870"),sQuery(id+"F0.wireOp",EDGE,"E1871"),sQuery(id+"F0.wireOp",EDGE,"E1872"),sQuery(id+"F0.wireOp",EDGE,"E1873"),sQuery(id+"F0.wireOp",EDGE,"E1874"),sQuery(id+"F0.wireOp",EDGE,"E1875"),sQuery(id+"F0.wireOp",EDGE,"E1876"),sQuery(id+"F0.wireOp",EDGE,"E1877"),sQuery(id+"F0.wireOp",EDGE,"E1878"),sQuery(id+"F0.wireOp",EDGE,"E1879"),sQuery(id+"F0.wireOp",EDGE,"E1880"),sQuery(id+"F0.wireOp",EDGE,"E1881"),sQuery(id+"F0.wireOp",EDGE,"E1882"),sQuery(id+"F0.wireOp",EDGE,"E1883"),sQuery(id+"F0.wireOp",EDGE,"E1884"),sQuery(id+"F0.wireOp",EDGE,"E1885"),sQuery(id+"F0.wireOp",EDGE,"E1886"),sQuery(id+"F0.wireOp",EDGE,"E1887"),sQuery(id+"F0.wireOp",EDGE,"E1888"),sQuery(id+"F0.wireOp",EDGE,"E1889"),sQuery(id+"F0.wireOp",EDGE,"E1890"),sQuery(id+"F0.wireOp",EDGE,"E1891"),sQuery(id+"F0.wireOp",EDGE,"E1892"),sQuery(id+"F0.wireOp",EDGE,"E1893"),sQuery(id+"F0.wireOp",EDGE,"E1894"),sQuery(id+"F0.wireOp",EDGE,"E1895"),sQuery(id+"F0.wireOp",EDGE,"E1896"),sQuery(id+"F0.wireOp",EDGE,"E1897"),sQuery(id+"F0.wireOp",EDGE,"E1898"),sQuery(id+"F0.wireOp",EDGE,"E1899"),sQuery(id+"F0.wireOp",EDGE,"E1900"),sQuery(id+"F0.wireOp",EDGE,"E1901"),sQuery(id+"F0.wireOp",EDGE,"E1902"),sQuery(id+"F0.wireOp",EDGE,"E1903"),sQuery(id+"F0.wireOp",EDGE,"E1904"),sQuery(id+"F0.wireOp",EDGE,"E1905"),sQuery(id+"F0.wireOp",EDGE,"E1906"),sQuery(id+"F0.wireOp",EDGE,"E1907"),sQuery(id+"F0.wireOp",EDGE,"E1908"),sQuery(id+"F0.wireOp",EDGE,"E1909"),sQuery(id+"F0.wireOp",EDGE,"E1910"),sQuery(id+"F0.wireOp",EDGE,"E1911"),sQuery(id+"F0.wireOp",EDGE,"E1912"),sQuery(id+"F0.wireOp",EDGE,"E1913"),sQuery(id+"F0.wireOp",EDGE,"E1914"),sQuery(id+"F0.wireOp",EDGE,"E1915"),sQuery(id+"F0.wireOp",EDGE,"E1916"),sQuery(id+"F0.wireOp",EDGE,"E1917"),sQuery(id+"F0.wireOp",EDGE,"E1918"),sQuery(id+"F0.wireOp",EDGE,"E1919"),sQuery(id+"F0.wireOp",EDGE,"E1920"),sQuery(id+"F0.wireOp",EDGE,"E1921"),sQuery(id+"F0.wireOp",EDGE,"E1922"),sQuery(id+"F0.wireOp",EDGE,"E1923"),sQuery(id+"F0.wireOp",EDGE,"E1924"),sQuery(id+"F0.wireOp",EDGE,"E1925"),sQuery(id+"F0.wireOp",EDGE,"E1926"),sQuery(id+"F0.wireOp",EDGE,"E1927"),sQuery(id+"F0.wireOp",EDGE,"E1928"),sQuery(id+"F0.wireOp",EDGE,"E1929"),sQuery(id+"F0.wireOp",EDGE,"E1930"),sQuery(id+"F0.wireOp",EDGE,"E1931"),sQuery(id+"F0.wireOp",EDGE,"E1932"),sQuery(id+"F0.wireOp",EDGE,"E1933"),sQuery(id+"F0.wireOp",EDGE,"E1934"),sQuery(id+"F0.wireOp",EDGE,"E1935"),sQuery(id+"F0.wireOp",EDGE,"E1936"),sQuery(id+"F0.wireOp",EDGE,"E1937"),sQuery(id+"F0.wireOp",EDGE,"E1938"),sQuery(id+"F0.wireOp",EDGE,"E1939"),sQuery(id+"F0.wireOp",EDGE,"E1940"),sQuery(id+"F0.wireOp",EDGE,"E1941"),sQuery(id+"F0.wireOp",EDGE,"E1942"),sQuery(id+"F0.wireOp",EDGE,"E1943"),sQuery(id+"F0.wireOp",EDGE,"E1944"),sQuery(id+"F0.wireOp",EDGE,"E1945"),sQuery(id+"F0.wireOp",EDGE,"E1946"),sQuery(id+"F0.wireOp",EDGE,"E1947"),sQuery(id+"F0.wireOp",EDGE,"E1948"),sQuery(id+"F0.wireOp",EDGE,"E1949"),sQuery(id+"F0.wireOp",EDGE,"E1950"),sQuery(id+"F0.wireOp",EDGE,"E1951"),sQuery(id+"F0.wireOp",EDGE,"E1952"),sQuery(id+"F0.wireOp",EDGE,"E1953"),sQuery(id+"F0.wireOp",EDGE,"E1954"),sQuery(id+"F0.wireOp",EDGE,"E1955"),sQuery(id+"F0.wireOp",EDGE,"E1956"),sQuery(id+"F0.wireOp",EDGE,"E1957"),sQuery(id+"F0.wireOp",EDGE,"E1958"),sQuery(id+"F0.wireOp",EDGE,"E1959"),sQuery(id+"F0.wireOp",EDGE,"E1960"),sQuery(id+"F0.wireOp",EDGE,"E1961"),sQuery(id+"F0.wireOp",EDGE,"E1962"),sQuery(id+"F0.wireOp",EDGE,"E1963"),sQuery(id+"F0.wireOp",EDGE,"E1964"),sQuery(id+"F0.wireOp",EDGE,"E1965"),sQuery(id+"F0.wireOp",EDGE,"E1966"),sQuery(id+"F0.wireOp",EDGE,"E1967"),sQuery(id+"F0.wireOp",EDGE,"E1968"),sQuery(id+"F0.wireOp",EDGE,"E1969"),sQuery(id+"F0.wireOp",EDGE,"E1970"),sQuery(id+"F0.wireOp",EDGE,"E1971"),sQuery(id+"F0.wireOp",EDGE,"E1972"),sQuery(id+"F0.wireOp",EDGE,"E1973"),sQuery(id+"F0.wireOp",EDGE,"E1974"),sQuery(id+"F0.wireOp",EDGE,"E1975"),sQuery(id+"F0.wireOp",EDGE,"E1976"),sQuery(id+"F0.wireOp",EDGE,"E1977"),sQuery(id+"F0.wireOp",EDGE,"E1978"),sQuery(id+"F0.wireOp",EDGE,"E1979"),sQuery(id+"F0.wireOp",EDGE,"E1980"),sQuery(id+"F0.wireOp",EDGE,"E1981"),sQuery(id+"F0.wireOp",EDGE,"E1982"),sQuery(id+"F0.wireOp",EDGE,"E1983"),sQuery(id+"F0.wireOp",EDGE,"E1984"),sQuery(id+"F0.wireOp",EDGE,"E1985"),sQuery(id+"F0.wireOp",EDGE,"E1986"),sQuery(id+"F0.wireOp",EDGE,"E1987"),sQuery(id+"F0.wireOp",EDGE,"E1988"),sQuery(id+"F0.wireOp",EDGE,"E1989"),sQuery(id+"F0.wireOp",EDGE,"E1990"),sQuery(id+"F0.wireOp",EDGE,"E1991"),sQuery(id+"F0.wireOp",EDGE,"E1992"),sQuery(id+"F0.wireOp",EDGE,"E1993"),sQuery(id+"F0.wireOp",EDGE,"E1994"),sQuery(id+"F0.wireOp",EDGE,"E1995"),sQuery(id+"F0.wireOp",EDGE,"E1996"),sQuery(id+"F0.wireOp",EDGE,"E1997"),sQuery(id+"F0.wireOp",EDGE,"E1998"),sQuery(id+"F0.wireOp",EDGE,"E1999"),sQuery(id+"F0.wireOp",EDGE,"E2000"),sQuery(id+"F0.wireOp",EDGE,"E2001"),sQuery(id+"F0.wireOp",EDGE,"E2002"),sQuery(id+"F0.wireOp",EDGE,"E2003"),sQuery(id+"F0.wireOp",EDGE,"E2004"),sQuery(id+"F0.wireOp",EDGE,"E2005"),sQuery(id+"F0.wireOp",EDGE,"E2006"),sQuery(id+"F0.wireOp",EDGE,"E2007"),sQuery(id+"F0.wireOp",EDGE,"E2008"),sQuery(id+"F0.wireOp",EDGE,"E2009"),sQuery(id+"F0.wireOp",EDGE,"E2010"),sQuery(id+"F0.wireOp",EDGE,"E2011"),sQuery(id+"F0.wireOp",EDGE,"E2012"),sQuery(id+"F0.wireOp",EDGE,"E2013"),sQuery(id+"F0.wireOp",EDGE,"E2014"),sQuery(id+"F0.wireOp",EDGE,"E2015"),sQuery(id+"F0.wireOp",EDGE,"E2016"),sQuery(id+"F0.wireOp",EDGE,"E2017"),sQuery(id+"F0.wireOp",EDGE,"E2018"),sQuery(id+"F0.wireOp",EDGE,"E2019"),sQuery(id+"F0.wireOp",EDGE,"E2020"),sQuery(id+"F0.wireOp",EDGE,"E2021"),sQuery(id+"F0.wireOp",EDGE,"E2022"),sQuery(id+"F0.wireOp",EDGE,"E2023"),sQuery(id+"F0.wireOp",EDGE,"E2024"),sQuery(id+"F0.wireOp",EDGE,"E2025"),sQuery(id+"F0.wireOp",EDGE,"E2026"),sQuery(id+"F0.wireOp",EDGE,"E2027"),sQuery(id+"F0.wireOp",EDGE,"E2028"),sQuery(id+"F0.wireOp",EDGE,"E2029"),sQuery(id+"F0.wireOp",EDGE,"E2030"),sQuery(id+"F0.wireOp",EDGE,"E2031"),sQuery(id+"F0.wireOp",EDGE,"E2032"),sQuery(id+"F0.wireOp",EDGE,"E2033"),sQuery(id+"F0.wireOp",EDGE,"E2034"),sQuery(id+"F0.wireOp",EDGE,"E2035"),sQuery(id+"F0.wireOp",EDGE,"E2036"),sQuery(id+"F0.wireOp",EDGE,"E2037"),sQuery(id+"F0.wireOp",EDGE,"E2038"),sQuery(id+"F0.wireOp",EDGE,"E2039"),sQuery(id+"F0.wireOp",EDGE,"E2040"),sQuery(id+"F0.wireOp",EDGE,"E2041"),sQuery(id+"F0.wireOp",EDGE,"E2042"),sQuery(id+"F0.wireOp",EDGE,"E2043"),sQuery(id+"F0.wireOp",EDGE,"E2044"),sQuery(id+"F0.wireOp",EDGE,"E2045"),sQuery(id+"F0.wireOp",EDGE,"E2046"),sQuery(id+"F0.wireOp",EDGE,"E2047"),sQuery(id+"F0.wireOp",EDGE,"E2048"),sQuery(id+"F0.wireOp",EDGE,"E2049"),sQuery(id+"F0.wireOp",EDGE,"E2050"),sQuery(id+"F0.wireOp",EDGE,"E2051"),sQuery(id+"F0.wireOp",EDGE,"E2052"),sQuery(id+"F0.wireOp",EDGE,"E2053"),sQuery(id+"F0.wireOp",EDGE,"E2054"),sQuery(id+"F0.wireOp",EDGE,"E2055"),sQuery(id+"F0.wireOp",EDGE,"E2056"),sQuery(id+"F0.wireOp",EDGE,"E2057"),sQuery(id+"F0.wireOp",EDGE,"E2058"),sQuery(id+"F0.wireOp",EDGE,"E2059"),sQuery(id+"F0.wireOp",EDGE,"E2060"),sQuery(id+"F0.wireOp",EDGE,"E2061"),sQuery(id+"F0.wireOp",EDGE,"E2062"),sQuery(id+"F0.wireOp",EDGE,"E2063"),sQuery(id+"F0.wireOp",EDGE,"E2064"),sQuery(id+"F0.wireOp",EDGE,"E2065"),sQuery(id+"F0.wireOp",EDGE,"E2066"),sQuery(id+"F0.wireOp",EDGE,"E2067"),sQuery(id+"F0.wireOp",EDGE,"E2068"),sQuery(id+"F0.wireOp",EDGE,"E2069"),sQuery(id+"F0.wireOp",EDGE,"E2070"),sQuery(id+"F0.wireOp",EDGE,"E2071"),sQuery(id+"F0.wireOp",EDGE,"E2072"),sQuery(id+"F0.wireOp",EDGE,"E2073"),sQuery(id+"F0.wireOp",EDGE,"E2074"),sQuery(id+"F0.wireOp",EDGE,"E2075"),sQuery(id+"F0.wireOp",EDGE,"E2076"),sQuery(id+"F0.wireOp",EDGE,"E2077"),sQuery(id+"F0.wireOp",EDGE,"E2078"),sQuery(id+"F0.wireOp",EDGE,"E2079"),sQuery(id+"F0.wireOp",EDGE,"E2080"),sQuery(id+"F0.wireOp",EDGE,"E2081"),sQuery(id+"F0.wireOp",EDGE,"E2082"),sQuery(id+"F0.wireOp",EDGE,"E2083"),sQuery(id+"F0.wireOp",EDGE,"E2084"),sQuery(id+"F0.wireOp",EDGE,"E2085"),sQuery(id+"F0.wireOp",EDGE,"E2086"),sQuery(id+"F0.wireOp",EDGE,"E2087"),sQuery(id+"F0.wireOp",EDGE,"E2088"),sQuery(id+"F0.wireOp",EDGE,"E2089"),sQuery(id+"F0.wireOp",EDGE,"E2090"),sQuery(id+"F0.wireOp",EDGE,"E2091"),sQuery(id+"F0.wireOp",EDGE,"E2092"),sQuery(id+"F0.wireOp",EDGE,"E2093"),sQuery(id+"F0.wireOp",EDGE,"E2094"),sQuery(id+"F0.wireOp",EDGE,"E2095"),sQuery(id+"F0.wireOp",EDGE,"E2096"),sQuery(id+"F0.wireOp",EDGE,"E2097"),sQuery(id+"F0.wireOp",EDGE,"E2098"),sQuery(id+"F0.wireOp",EDGE,"E2099"),sQuery(id+"F0.wireOp",EDGE,"E2100"),sQuery(id+"F0.wireOp",EDGE,"E2101"),sQuery(id+"F0.wireOp",EDGE,"E2102"),sQuery(id+"F0.wireOp",EDGE,"E2103"),sQuery(id+"F0.wireOp",EDGE,"E2104"),sQuery(id+"F0.wireOp",EDGE,"E2105"),sQuery(id+"F0.wireOp",EDGE,"E2106"),sQuery(id+"F0.wireOp",EDGE,"E2107"),sQuery(id+"F0.wireOp",EDGE,"E2108"),sQuery(id+"F0.wireOp",EDGE,"E2109"),sQuery(id+"F0.wireOp",EDGE,"E2110"),sQuery(id+"F0.wireOp",EDGE,"E2111"),sQuery(id+"F0.wireOp",EDGE,"E2112"),sQuery(id+"F0.wireOp",EDGE,"E2113"),sQuery(id+"F0.wireOp",EDGE,"E2114"),sQuery(id+"F0.wireOp",EDGE,"E2115"),sQuery(id+"F0.wireOp",EDGE,"E2116"),sQuery(id+"F0.wireOp",EDGE,"E2117"),sQuery(id+"F0.wireOp",EDGE,"E2118"),sQuery(id+"F0.wireOp",EDGE,"E2119"),sQuery(id+"F0.wireOp",EDGE,"E2120"),sQuery(id+"F0.wireOp",EDGE,"E2121"),sQuery(id+"F0.wireOp",EDGE,"E2122"),sQuery(id+"F0.wireOp",EDGE,"E2123"),sQuery(id+"F0.wireOp",EDGE,"E2124"),sQuery(id+"F0.wireOp",EDGE,"E2125"),sQuery(id+"F0.wireOp",EDGE,"E2126"),sQuery(id+"F0.wireOp",EDGE,"E2127"),sQuery(id+"F0.wireOp",EDGE,"E2128"),sQuery(id+"F0.wireOp",EDGE,"E2129"),sQuery(id+"F0.wireOp",EDGE,"E2130"),sQuery(id+"F0.wireOp",EDGE,"E2131"),sQuery(id+"F0.wireOp",EDGE,"E2132"),sQuery(id+"F0.wireOp",EDGE,"E2133"),sQuery(id+"F0.wireOp",EDGE,"E2134"),sQuery(id+"F0.wireOp",EDGE,"E2135"),sQuery(id+"F0.wireOp",EDGE,"E2136"),sQuery(id+"F0.wireOp",EDGE,"E2137"),sQuery(id+"F0.wireOp",EDGE,"E2138"),sQuery(id+"F0.wireOp",EDGE,"E2139"),sQuery(id+"F0.wireOp",EDGE,"E2140"),sQuery(id+"F0.wireOp",EDGE,"E2141"),sQuery(id+"F0.wireOp",EDGE,"E2142"),sQuery(id+"F0.wireOp",EDGE,"E2143"),sQuery(id+"F0.wireOp",EDGE,"E2144"),sQuery(id+"F0.wireOp",EDGE,"E2145"),sQuery(id+"F0.wireOp",EDGE,"E2146"),sQuery(id+"F0.wireOp",EDGE,"E2147"),sQuery(id+"F0.wireOp",EDGE,"E2148"),sQuery(id+"F0.wireOp",EDGE,"E2149"),sQuery(id+"F0.wireOp",EDGE,"E2150"),sQuery(id+"F0.wireOp",EDGE,"E2151"),sQuery(id+"F0.wireOp",EDGE,"E2152"),sQuery(id+"F0.wireOp",EDGE,"E2153"),sQuery(id+"F0.wireOp",EDGE,"E2154"),sQuery(id+"F0.wireOp",EDGE,"E2155"),sQuery(id+"F0.wireOp",EDGE,"E2156"),sQuery(id+"F0.wireOp",EDGE,"E2157"),sQuery(id+"F0.wireOp",EDGE,"E2158"),sQuery(id+"F0.wireOp",EDGE,"E2159"),sQuery(id+"F0.wireOp",EDGE,"E2160"),sQuery(id+"F0.wireOp",EDGE,"E2161"),sQuery(id+"F0.wireOp",EDGE,"E2162"),sQuery(id+"F0.wireOp",EDGE,"E2163"),sQuery(id+"F0.wireOp",EDGE,"E2164"),sQuery(id+"F0.wireOp",EDGE,"E2165"),sQuery(id+"F0.wireOp",EDGE,"E2166"),sQuery(id+"F0.wireOp",EDGE,"E2167"),sQuery(id+"F0.wireOp",EDGE,"E2168"),sQuery(id+"F0.wireOp",EDGE,"E2169"),sQuery(id+"F0.wireOp",EDGE,"E2170"),sQuery(id+"F0.wireOp",EDGE,"E2171"),sQuery(id+"F0.wireOp",EDGE,"E2172"),sQuery(id+"F0.wireOp",EDGE,"E2173"),sQuery(id+"F0.wireOp",EDGE,"E2174"),sQuery(id+"F0.wireOp",EDGE,"E2175"),sQuery(id+"F0.wireOp",EDGE,"E2176"),sQuery(id+"F0.wireOp",EDGE,"E2177"),sQuery(id+"F0.wireOp",EDGE,"E2178"),sQuery(id+"F0.wireOp",EDGE,"E2179"),sQuery(id+"F0.wireOp",EDGE,"E2180"),sQuery(id+"F0.wireOp",EDGE,"E2181"),sQuery(id+"F0.wireOp",EDGE,"E2182"),sQuery(id+"F0.wireOp",EDGE,"E2183"),sQuery(id+"F0.wireOp",EDGE,"E2184"),sQuery(id+"F0.wireOp",EDGE,"E2185"),sQuery(id+"F0.wireOp",EDGE,"E2186"),sQuery(id+"F0.wireOp",EDGE,"E2187"),sQuery(id+"F0.wireOp",EDGE,"E2188"),sQuery(id+"F0.wireOp",EDGE,"E2189"),sQuery(id+"F0.wireOp",EDGE,"E2190"),sQuery(id+"F0.wireOp",EDGE,"E2191"),sQuery(id+"F0.wireOp",EDGE,"E2192"),sQuery(id+"F0.wireOp",EDGE,"E2193"),sQuery(id+"F0.wireOp",EDGE,"E2194"),sQuery(id+"F0.wireOp",EDGE,"E2195"),sQuery(id+"F0.wireOp",EDGE,"E2196"),sQuery(id+"F0.wireOp",EDGE,"E2197"),sQuery(id+"F0.wireOp",EDGE,"E2198"),sQuery(id+"F0.wireOp",EDGE,"E2199"),sQuery(id+"F0.wireOp",EDGE,"E2200"),sQuery(id+"F0.wireOp",EDGE,"E2201"),sQuery(id+"F0.wireOp",EDGE,"E2202"),sQuery(id+"F0.wireOp",EDGE,"E2203"),sQuery(id+"F0.wireOp",EDGE,"E2204"),sQuery(id+"F0.wireOp",EDGE,"E2205"),sQuery(id+"F0.wireOp",EDGE,"E2206"),sQuery(id+"F0.wireOp",EDGE,"E2207"),sQuery(id+"F0.wireOp",EDGE,"E2208"),sQuery(id+"F0.wireOp",EDGE,"E2209"),sQuery(id+"F0.wireOp",EDGE,"E2210"),sQuery(id+"F0.wireOp",EDGE,"E2211"),sQuery(id+"F0.wireOp",EDGE,"E2212"),sQuery(id+"F0.wireOp",EDGE,"E2213"),sQuery(id+"F0.wireOp",EDGE,"E2214"),sQuery(id+"F0.wireOp",EDGE,"E2215"),sQuery(id+"F0.wireOp",EDGE,"E2216"),sQuery(id+"F0.wireOp",EDGE,"E2217"),sQuery(id+"F0.wireOp",EDGE,"E2218"),sQuery(id+"F0.wireOp",EDGE,"E2219"),sQuery(id+"F0.wireOp",EDGE,"E2220"),sQuery(id+"F0.wireOp",EDGE,"E2221"),sQuery(id+"F0.wireOp",EDGE,"E2222"),sQuery(id+"F0.wireOp",EDGE,"E2223"),sQuery(id+"F0.wireOp",EDGE,"E2224"),sQuery(id+"F0.wireOp",EDGE,"E2225"),sQuery(id+"F0.wireOp",EDGE,"E2226"),sQuery(id+"F0.wireOp",EDGE,"E2227"),sQuery(id+"F0.wireOp",EDGE,"E2228"),sQuery(id+"F0.wireOp",EDGE,"E2229"),sQuery(id+"F0.wireOp",EDGE,"E2230"),sQuery(id+"F0.wireOp",EDGE,"E2231"),sQuery(id+"F0.wireOp",EDGE,"E2232"),sQuery(id+"F0.wireOp",EDGE,"E2233"),sQuery(id+"F0.wireOp",EDGE,"E2234"),sQuery(id+"F0.wireOp",EDGE,"E2235"),sQuery(id+"F0.wireOp",EDGE,"E2236"),sQuery(id+"F0.wireOp",EDGE,"E2237"),sQuery(id+"F0.wireOp",EDGE,"E2238"),sQuery(id+"F0.wireOp",EDGE,"E2239"),sQuery(id+"F0.wireOp",EDGE,"E2240"),sQuery(id+"F0.wireOp",EDGE,"E2241"),sQuery(id+"F0.wireOp",EDGE,"E2242"),sQuery(id+"F0.wireOp",EDGE,"E2243"),sQuery(id+"F0.wireOp",EDGE,"E2244"),sQuery(id+"F0.wireOp",EDGE,"E2245"),sQuery(id+"F0.wireOp",EDGE,"E2246"),sQuery(id+"F0.wireOp",EDGE,"E2247"),sQuery(id+"F0.wireOp",EDGE,"E2248"),sQuery(id+"F0.wireOp",EDGE,"E2249"),sQuery(id+"F0.wireOp",EDGE,"E2250"),sQuery(id+"F0.wireOp",EDGE,"E2251"),sQuery(id+"F0.wireOp",EDGE,"E2252"),sQuery(id+"F0.wireOp",EDGE,"E2253"),sQuery(id+"F0.wireOp",EDGE,"E2254"),sQuery(id+"F0.wireOp",EDGE,"E2255"),sQuery(id+"F0.wireOp",EDGE,"E2256"),sQuery(id+"F0.wireOp",EDGE,"E2257"),sQuery(id+"F0.wireOp",EDGE,"E2258"),sQuery(id+"F0.wireOp",EDGE,"E2259"),sQuery(id+"F0.wireOp",EDGE,"E2260"),sQuery(id+"F0.wireOp",EDGE,"E2261"),sQuery(id+"F0.wireOp",EDGE,"E2262"),sQuery(id+"F0.wireOp",EDGE,"E2263"),sQuery(id+"F0.wireOp",EDGE,"E2264"),sQuery(id+"F0.wireOp",EDGE,"E2265"),sQuery(id+"F0.wireOp",EDGE,"E2266"),sQuery(id+"F0.wireOp",EDGE,"E2267"),sQuery(id+"F0.wireOp",EDGE,"E2268"),sQuery(id+"F0.wireOp",EDGE,"E2269"),sQuery(id+"F0.wireOp",EDGE,"E2270"),sQuery(id+"F0.wireOp",EDGE,"E2271"),sQuery(id+"F0.wireOp",EDGE,"E2272"),sQuery(id+"F0.wireOp",EDGE,"E2273"),sQuery(id+"F0.wireOp",EDGE,"E2274"),sQuery(id+"F0.wireOp",EDGE,"E2275"),sQuery(id+"F0.wireOp",EDGE,"E2276"),sQuery(id+"F0.wireOp",EDGE,"E2277"),sQuery(id+"F0.wireOp",EDGE,"E2278"),sQuery(id+"F0.wireOp",EDGE,"E2279"),sQuery(id+"F0.wireOp",EDGE,"E2280"),sQuery(id+"F0.wireOp",EDGE,"E2281"),sQuery(id+"F0.wireOp",EDGE,"E2282"),sQuery(id+"F0.wireOp",EDGE,"E2283"),sQuery(id+"F0.wireOp",EDGE,"E2284"),sQuery(id+"F0.wireOp",EDGE,"E2285"),sQuery(id+"F0.wireOp",EDGE,"E2286"),sQuery(id+"F0.wireOp",EDGE,"E2287"),sQuery(id+"F0.wireOp",EDGE,"E2288"),sQuery(id+"F0.wireOp",EDGE,"E2289"),sQuery(id+"F0.wireOp",EDGE,"E2290"),sQuery(id+"F0.wireOp",EDGE,"E2291"),sQuery(id+"F0.wireOp",EDGE,"E2292"),sQuery(id+"F0.wireOp",EDGE,"E2293"),sQuery(id+"F0.wireOp",EDGE,"E2294"),sQuery(id+"F0.wireOp",EDGE,"E2295"),sQuery(id+"F0.wireOp",EDGE,"E2296"),sQuery(id+"F0.wireOp",EDGE,"E2297"),sQuery(id+"F0.wireOp",EDGE,"E2298"),sQuery(id+"F0.wireOp",EDGE,"E2299"),sQuery(id+"F0.wireOp",EDGE,"E2300"),sQuery(id+"F0.wireOp",EDGE,"E2301"),sQuery(id+"F0.wireOp",EDGE,"E2302"),sQuery(id+"F0.wireOp",EDGE,"E2303"),sQuery(id+"F0.wireOp",EDGE,"E2304"),sQuery(id+"F0.wireOp",EDGE,"E2305"),sQuery(id+"F0.wireOp",EDGE,"E2306"),sQuery(id+"F0.wireOp",EDGE,"E2307"),sQuery(id+"F0.wireOp",EDGE,"E2308"),sQuery(id+"F0.wireOp",EDGE,"E2309"),sQuery(id+"F0.wireOp",EDGE,"E2310"),sQuery(id+"F0.wireOp",EDGE,"E2311"),sQuery(id+"F0.wireOp",EDGE,"E2312"),sQuery(id+"F0.wireOp",EDGE,"E2313"),sQuery(id+"F0.wireOp",EDGE,"E2314"),sQuery(id+"F0.wireOp",EDGE,"E2315"),sQuery(id+"F0.wireOp",EDGE,"E2316"),sQuery(id+"F0.wireOp",EDGE,"E2317"),sQuery(id+"F0.wireOp",EDGE,"E2318"),sQuery(id+"F0.wireOp",EDGE,"E2319"),sQuery(id+"F0.wireOp",EDGE,"E2320"),sQuery(id+"F0.wireOp",EDGE,"E2321"),sQuery(id+"F0.wireOp",EDGE,"E2322"),sQuery(id+"F0.wireOp",EDGE,"E2323"),sQuery(id+"F0.wireOp",EDGE,"E2324"),sQuery(id+"F0.wireOp",EDGE,"E2325"),sQuery(id+"F0.wireOp",EDGE,"E2326"),sQuery(id+"F0.wireOp",EDGE,"E2327"),sQuery(id+"F0.wireOp",EDGE,"E2328"),sQuery(id+"F0.wireOp",EDGE,"E2329"),sQuery(id+"F0.wireOp",EDGE,"E2330"),sQuery(id+"F0.wireOp",EDGE,"E2331"),sQuery(id+"F0.wireOp",EDGE,"E2332"),sQuery(id+"F0.wireOp",EDGE,"E2333"),sQuery(id+"F0.wireOp",EDGE,"E2334"),sQuery(id+"F0.wireOp",EDGE,"E2335"),sQuery(id+"F0.wireOp",EDGE,"E2336"),sQuery(id+"F0.wireOp",EDGE,"E2337"),sQuery(id+"F0.wireOp",EDGE,"E2338"),sQuery(id+"F0.wireOp",EDGE,"E2339"),sQuery(id+"F0.wireOp",EDGE,"E2340"),sQuery(id+"F0.wireOp",EDGE,"E2341"),sQuery(id+"F0.wireOp",EDGE,"E2342"),sQuery(id+"F0.wireOp",EDGE,"E2343"),sQuery(id+"F0.wireOp",EDGE,"E2344"),sQuery(id+"F0.wireOp",EDGE,"E2345"),sQuery(id+"F0.wireOp",EDGE,"E2346"),sQuery(id+"F0.wireOp",EDGE,"E2347"),sQuery(id+"F0.wireOp",EDGE,"E2348"),sQuery(id+"F0.wireOp",EDGE,"E2349"),sQuery(id+"F0.wireOp",EDGE,"E2350"),sQuery(id+"F0.wireOp",EDGE,"E2351"),sQuery(id+"F0.wireOp",EDGE,"E2352"),sQuery(id+"F0.wireOp",EDGE,"E2353"),sQuery(id+"F0.wireOp",EDGE,"E2354"),sQuery(id+"F0.wireOp",EDGE,"E2355"),sQuery(id+"F0.wireOp",EDGE,"E2356"),sQuery(id+"F0.wireOp",EDGE,"E2357"),sQuery(id+"F0.wireOp",EDGE,"E2358"),sQuery(id+"F0.wireOp",EDGE,"E2359"),sQuery(id+"F0.wireOp",EDGE,"E2360"),sQuery(id+"F0.wireOp",EDGE,"E2361"),sQuery(id+"F0.wireOp",EDGE,"E2362"),sQuery(id+"F0.wireOp",EDGE,"E2363"),sQuery(id+"F0.wireOp",EDGE,"E2364"),sQuery(id+"F0.wireOp",EDGE,"E2365"),sQuery(id+"F0.wireOp",EDGE,"E2366"),sQuery(id+"F0.wireOp",EDGE,"E2367"),sQuery(id+"F0.wireOp",EDGE,"E2368"),sQuery(id+"F0.wireOp",EDGE,"E2369"),sQuery(id+"F0.wireOp",EDGE,"E2370"),sQuery(id+"F0.wireOp",EDGE,"E2371"),sQuery(id+"F0.wireOp",EDGE,"E2372"),sQuery(id+"F0.wireOp",EDGE,"E2373"),sQuery(id+"F0.wireOp",EDGE,"E2374"),sQuery(id+"F0.wireOp",EDGE,"E2375"),sQuery(id+"F0.wireOp",EDGE,"E2376"),sQuery(id+"F0.wireOp",EDGE,"E2377"),sQuery(id+"F0.wireOp",EDGE,"E2378"),sQuery(id+"F0.wireOp",EDGE,"E2379"),sQuery(id+"F0.wireOp",EDGE,"E2380"),sQuery(id+"F0.wireOp",EDGE,"E2381"),sQuery(id+"F0.wireOp",EDGE,"E2382"),sQuery(id+"F0.wireOp",EDGE,"E2383"),sQuery(id+"F0.wireOp",EDGE,"E2384"),sQuery(id+"F0.wireOp",EDGE,"E2385"),sQuery(id+"F0.wireOp",EDGE,"E2386"),sQuery(id+"F0.wireOp",EDGE,"E2387"),sQuery(id+"F0.wireOp",EDGE,"E2388"),sQuery(id+"F0.wireOp",EDGE,"E2389"),sQuery(id+"F0.wireOp",EDGE,"E2390"),sQuery(id+"F0.wireOp",EDGE,"E2391"),sQuery(id+"F0.wireOp",EDGE,"E2392"),sQuery(id+"F0.wireOp",EDGE,"E2393"),sQuery(id+"F0.wireOp",EDGE,"E2394"),sQuery(id+"F0.wireOp",EDGE,"E2395"),sQuery(id+"F0.wireOp",EDGE,"E2396"),sQuery(id+"F0.wireOp",EDGE,"E2397"),sQuery(id+"F0.wireOp",EDGE,"E2398"),sQuery(id+"F0.wireOp",EDGE,"E2399"),sQuery(id+"F0.wireOp",EDGE,"E2400"),sQuery(id+"F0.wireOp",EDGE,"E2401"),sQuery(id+"F0.wireOp",EDGE,"E2402"),sQuery(id+"F0.wireOp",EDGE,"E2403"),sQuery(id+"F0.wireOp",EDGE,"E2404"),sQuery(id+"F0.wireOp",EDGE,"E2405"),sQuery(id+"F0.wireOp",EDGE,"E2406"),sQuery(id+"F0.wireOp",EDGE,"E2407"),sQuery(id+"F0.wireOp",EDGE,"E2408"),sQuery(id+"F0.wireOp",EDGE,"E2409"),sQuery(id+"F0.wireOp",EDGE,"E2410"),sQuery(id+"F0.wireOp",EDGE,"E2411"),sQuery(id+"F0.wireOp",EDGE,"E2412"),sQuery(id+"F0.wireOp",EDGE,"E2413"),sQuery(id+"F0.wireOp",EDGE,"E2414"),sQuery(id+"F0.wireOp",EDGE,"E2415"),sQuery(id+"F0.wireOp",EDGE,"E2416"),sQuery(id+"F0.wireOp",EDGE,"E2417"),sQuery(id+"F0.wireOp",EDGE,"E2418"),sQuery(id+"F0.wireOp",EDGE,"E2419"),sQuery(id+"F0.wireOp",EDGE,"E2420"),sQuery(id+"F0.wireOp",EDGE,"E2421"),sQuery(id+"F0.wireOp",EDGE,"E2422"),sQuery(id+"F0.wireOp",EDGE,"E2423"),sQuery(id+"F0.wireOp",EDGE,"E2424"),sQuery(id+"F0.wireOp",EDGE,"E2425"),sQuery(id+"F0.wireOp",EDGE,"E2426"),sQuery(id+"F0.wireOp",EDGE,"E2427"),sQuery(id+"F0.wireOp",EDGE,"E2428"),sQuery(id+"F0.wireOp",EDGE,"E2429"),sQuery(id+"F0.wireOp",EDGE,"E2430"),sQuery(id+"F0.wireOp",EDGE,"E2431"),sQuery(id+"F0.wireOp",EDGE,"E2432"),sQuery(id+"F0.wireOp",EDGE,"E2433"),sQuery(id+"F0.wireOp",EDGE,"E2434"),sQuery(id+"F0.wireOp",EDGE,"E2435"),sQuery(id+"F0.wireOp",EDGE,"E2436"),sQuery(id+"F0.wireOp",EDGE,"E2437"),sQuery(id+"F0.wireOp",EDGE,"E2438"),sQuery(id+"F0.wireOp",EDGE,"E2439"),sQuery(id+"F0.wireOp",EDGE,"E2440"),sQuery(id+"F0.wireOp",EDGE,"E2441"),sQuery(id+"F0.wireOp",EDGE,"E2442"),sQuery(id+"F0.wireOp",EDGE,"E2443"),sQuery(id+"F0.wireOp",EDGE,"E2444"),sQuery(id+"F0.wireOp",EDGE,"E2445"),sQuery(id+"F0.wireOp",EDGE,"E2446"),sQuery(id+"F0.wireOp",EDGE,"E2447"),sQuery(id+"F0.wireOp",EDGE,"E2448"),sQuery(id+"F0.wireOp",EDGE,"E2449"),sQuery(id+"F0.wireOp",EDGE,"E2450"),sQuery(id+"F0.wireOp",EDGE,"E2451"),sQuery(id+"F0.wireOp",EDGE,"E2452"),sQuery(id+"F0.wireOp",EDGE,"E2453"),sQuery(id+"F0.wireOp",EDGE,"E2454"),sQuery(id+"F0.wireOp",EDGE,"E2455"),sQuery(id+"F0.wireOp",EDGE,"E2456"),sQuery(id+"F0.wireOp",EDGE,"E2457"),sQuery(id+"F0.wireOp",EDGE,"E2458"),sQuery(id+"F0.wireOp",EDGE,"E2459"),sQuery(id+"F0.wireOp",EDGE,"E2460"),sQuery(id+"F0.wireOp",EDGE,"E2461"),sQuery(id+"F0.wireOp",EDGE,"E2462"),sQuery(id+"F0.wireOp",EDGE,"E2463"),sQuery(id+"F0.wireOp",EDGE,"E2464"),sQuery(id+"F0.wireOp",EDGE,"E2465"),sQuery(id+"F0.wireOp",EDGE,"E2466"),sQuery(id+"F0.wireOp",EDGE,"E2467"),sQuery(id+"F0.wireOp",EDGE,"E2468"),sQuery(id+"F0.wireOp",EDGE,"E2469"),sQuery(id+"F0.wireOp",EDGE,"E2470"),sQuery(id+"F0.wireOp",EDGE,"E2471"),sQuery(id+"F0.wireOp",EDGE,"E2472"),sQuery(id+"F0.wireOp",EDGE,"E2473"),sQuery(id+"F0.wireOp",EDGE,"E2474"),sQuery(id+"F0.wireOp",EDGE,"E2475"),sQuery(id+"F0.wireOp",EDGE,"E2476"),sQuery(id+"F0.wireOp",EDGE,"E2477"),sQuery(id+"F0.wireOp",EDGE,"E2478"),sQuery(id+"F0.wireOp",EDGE,"E2479"),sQuery(id+"F0.wireOp",EDGE,"E2480"),sQuery(id+"F0.wireOp",EDGE,"E2481"),sQuery(id+"F0.wireOp",EDGE,"E2482"),sQuery(id+"F0.wireOp",EDGE,"E2483"),sQuery(id+"F0.wireOp",EDGE,"E2484"),sQuery(id+"F0.wireOp",EDGE,"E2485"),sQuery(id+"F0.wireOp",EDGE,"E2486"),sQuery(id+"F0.wireOp",EDGE,"E2487"),sQuery(id+"F0.wireOp",EDGE,"E2488"),sQuery(id+"F0.wireOp",EDGE,"E2489"),sQuery(id+"F0.wireOp",EDGE,"E2490"),sQuery(id+"F0.wireOp",EDGE,"E2491"),sQuery(id+"F0.wireOp",EDGE,"E2492"),sQuery(id+"F0.wireOp",EDGE,"E2493"),sQuery(id+"F0.wireOp",EDGE,"E2494"),sQuery(id+"F0.wireOp",EDGE,"E2495"),sQuery(id+"F0.wireOp",EDGE,"E2496"),sQuery(id+"F0.wireOp",EDGE,"E2497"),sQuery(id+"F0.wireOp",EDGE,"E2498"),sQuery(id+"F0.wireOp",EDGE,"E2499"),sQuery(id+"F0.wireOp",EDGE,"E2500"),sQuery(id+"F0.wireOp",EDGE,"E2501"),sQuery(id+"F0.wireOp",EDGE,"E2502"),sQuery(id+"F0.wireOp",EDGE,"E2503"),sQuery(id+"F0.wireOp",EDGE,"E2504"),sQuery(id+"F0.wireOp",EDGE,"E2505"),sQuery(id+"F0.wireOp",EDGE,"E2506"),sQuery(id+"F0.wireOp",EDGE,"E2507"),sQuery(id+"F0.wireOp",EDGE,"E2508"),sQuery(id+"F0.wireOp",EDGE,"E2509"),sQuery(id+"F0.wireOp",EDGE,"E2510"),sQuery(id+"F0.wireOp",EDGE,"E2511"),sQuery(id+"F0.wireOp",EDGE,"E2512"),sQuery(id+"F0.wireOp",EDGE,"E2513"),sQuery(id+"F0.wireOp",EDGE,"E2514"),sQuery(id+"F0.wireOp",EDGE,"E2515"),sQuery(id+"F0.wireOp",EDGE,"E2516"),sQuery(id+"F0.wireOp",EDGE,"E2517"),sQuery(id+"F0.wireOp",EDGE,"E2518"),sQuery(id+"F0.wireOp",EDGE,"E2519"),sQuery(id+"F0.wireOp",EDGE,"E2520"),sQuery(id+"F0.wireOp",EDGE,"E2521"),sQuery(id+"F0.wireOp",EDGE,"E2522"),sQuery(id+"F0.wireOp",EDGE,"E2523"),sQuery(id+"F0.wireOp",EDGE,"E2524"),sQuery(id+"F0.wireOp",EDGE,"E2525"),sQuery(id+"F0.wireOp",EDGE,"E2526"),sQuery(id+"F0.wireOp",EDGE,"E2527"),sQuery(id+"F0.wireOp",EDGE,"E2528"),sQuery(id+"F0.wireOp",EDGE,"E2529"),sQuery(id+"F0.wireOp",EDGE,"E2530"),sQuery(id+"F0.wireOp",EDGE,"E2531"),sQuery(id+"F0.wireOp",EDGE,"E2532"),sQuery(id+"F0.wireOp",EDGE,"E2533"),sQuery(id+"F0.wireOp",EDGE,"E2534"),sQuery(id+"F0.wireOp",EDGE,"E2535"),sQuery(id+"F0.wireOp",EDGE,"E2536"),sQuery(id+"F0.wireOp",EDGE,"E2537"),sQuery(id+"F0.wireOp",EDGE,"E2538"),sQuery(id+"F0.wireOp",EDGE,"E2539"),sQuery(id+"F0.wireOp",EDGE,"E2540"),sQuery(id+"F0.wireOp",EDGE,"E2541"),sQuery(id+"F0.wireOp",EDGE,"E2542"),sQuery(id+"F0.wireOp",EDGE,"E2543"),sQuery(id+"F0.wireOp",EDGE,"E2544"),sQuery(id+"F0.wireOp",EDGE,"E2545"),sQuery(id+"F0.wireOp",EDGE,"E2546"),sQuery(id+"F0.wireOp",EDGE,"E2547"),sQuery(id+"F0.wireOp",EDGE,"E2548"),sQuery(id+"F0.wireOp",EDGE,"E2549"),sQuery(id+"F0.wireOp",EDGE,"E2550"),sQuery(id+"F0.wireOp",EDGE,"E2551"),sQuery(id+"F0.wireOp",EDGE,"E2552"),sQuery(id+"F0.wireOp",EDGE,"E2553"),sQuery(id+"F0.wireOp",EDGE,"E2554"),sQuery(id+"F0.wireOp",EDGE,"E2555"),sQuery(id+"F0.wireOp",EDGE,"E2556"),sQuery(id+"F0.wireOp",EDGE,"E2557"),sQuery(id+"F0.wireOp",EDGE,"E2558"),sQuery(id+"F0.wireOp",EDGE,"E2559"),sQuery(id+"F0.wireOp",EDGE,"E2560"),sQuery(id+"F0.wireOp",EDGE,"E2561"),sQuery(id+"F0.wireOp",EDGE,"E2562"),sQuery(id+"F0.wireOp",EDGE,"E2563"),sQuery(id+"F0.wireOp",EDGE,"E2564"),sQuery(id+"F0.wireOp",EDGE,"E2565"),sQuery(id+"F0.wireOp",EDGE,"E2566"),sQuery(id+"F0.wireOp",EDGE,"E2567"),sQuery(id+"F0.wireOp",EDGE,"E2568"),sQuery(id+"F0.wireOp",EDGE,"E2569"),sQuery(id+"F0.wireOp",EDGE,"E2570"),sQuery(id+"F0.wireOp",EDGE,"E2571"),sQuery(id+"F0.wireOp",EDGE,"E2572"),sQuery(id+"F0.wireOp",EDGE,"E2573"),sQuery(id+"F0.wireOp",EDGE,"E2574"),sQuery(id+"F0.wireOp",EDGE,"E2575"),sQuery(id+"F0.wireOp",EDGE,"E2576"),sQuery(id+"F0.wireOp",EDGE,"E2577"),sQuery(id+"F0.wireOp",EDGE,"E2578"),sQuery(id+"F0.wireOp",EDGE,"E2579"),sQuery(id+"F0.wireOp",EDGE,"E2580"),sQuery(id+"F0.wireOp",EDGE,"E2581"),sQuery(id+"F0.wireOp",EDGE,"E2582"),sQuery(id+"F0.wireOp",EDGE,"E2583"),sQuery(id+"F0.wireOp",EDGE,"E2584"),sQuery(id+"F0.wireOp",EDGE,"E2585"),sQuery(id+"F0.wireOp",EDGE,"E2586"),sQuery(id+"F0.wireOp",EDGE,"E2587"),sQuery(id+"F0.wireOp",EDGE,"E2588"),sQuery(id+"F0.wireOp",EDGE,"E2589"),sQuery(id+"F0.wireOp",EDGE,"E2590"),sQuery(id+"F0.wireOp",EDGE,"E2591"),sQuery(id+"F0.wireOp",EDGE,"E2592"),sQuery(id+"F0.wireOp",EDGE,"E2593"),sQuery(id+"F0.wireOp",EDGE,"E2594"),sQuery(id+"F0.wireOp",EDGE,"E2595"),sQuery(id+"F0.wireOp",EDGE,"E2596"),sQuery(id+"F0.wireOp",EDGE,"E2597"),sQuery(id+"F0.wireOp",EDGE,"E2598"),sQuery(id+"F0.wireOp",EDGE,"E2599"),sQuery(id+"F0.wireOp",EDGE,"E2600"),sQuery(id+"F0.wireOp",EDGE,"E2601"),sQuery(id+"F0.wireOp",EDGE,"E2602"),sQuery(id+"F0.wireOp",EDGE,"E2603"),sQuery(id+"F0.wireOp",EDGE,"E2604"),sQuery(id+"F0.wireOp",EDGE,"E2605"),sQuery(id+"F0.wireOp",EDGE,"E2606"),sQuery(id+"F0.wireOp",EDGE,"E2607"),sQuery(id+"F0.wireOp",EDGE,"E2608"),sQuery(id+"F0.wireOp",EDGE,"E2609"),sQuery(id+"F0.wireOp",EDGE,"E2610"),sQuery(id+"F0.wireOp",EDGE,"E2611"),sQuery(id+"F0.wireOp",EDGE,"E2612"),sQuery(id+"F0.wireOp",EDGE,"E2613"),sQuery(id+"F0.wireOp",EDGE,"E2614"),sQuery(id+"F0.wireOp",EDGE,"E2615"),sQuery(id+"F0.wireOp",EDGE,"E2616"),sQuery(id+"F0.wireOp",EDGE,"E2617"),sQuery(id+"F0.wireOp",EDGE,"E2618"),sQuery(id+"F0.wireOp",EDGE,"E2619"),sQuery(id+"F0.wireOp",EDGE,"E2620"),sQuery(id+"F0.wireOp",EDGE,"E2621"),sQuery(id+"F0.wireOp",EDGE,"E2622"),sQuery(id+"F0.wireOp",EDGE,"E2623"),sQuery(id+"F0.wireOp",EDGE,"E2624"),sQuery(id+"F0.wireOp",EDGE,"E2625"),sQuery(id+"F0.wireOp",EDGE,"E2626"),sQuery(id+"F0.wireOp",EDGE,"E2627"),sQuery(id+"F0.wireOp",EDGE,"E2628"),sQuery(id+"F0.wireOp",EDGE,"E2629"),sQuery(id+"F0.wireOp",EDGE,"E2630"),sQuery(id+"F0.wireOp",EDGE,"E2631"),sQuery(id+"F0.wireOp",EDGE,"E2632"),sQuery(id+"F0.wireOp",EDGE,"E2633"),sQuery(id+"F0.wireOp",EDGE,"E2634"),sQuery(id+"F0.wireOp",EDGE,"E2635"),sQuery(id+"F0.wireOp",EDGE,"E2636"),sQuery(id+"F0.wireOp",EDGE,"E2637"),sQuery(id+"F0.wireOp",EDGE,"E2638"),sQuery(id+"F0.wireOp",EDGE,"E2639"),sQuery(id+"F0.wireOp",EDGE,"E2640"),sQuery(id+"F0.wireOp",EDGE,"E2641"),sQuery(id+"F0.wireOp",EDGE,"E2642"),sQuery(id+"F0.wireOp",EDGE,"E2643"),sQuery(id+"F0.wireOp",EDGE,"E2644"),sQuery(id+"F0.wireOp",EDGE,"E2645"),sQuery(id+"F0.wireOp",EDGE,"E2646"),sQuery(id+"F0.wireOp",EDGE,"E2647"),sQuery(id+"F0.wireOp",EDGE,"E2648"),sQuery(id+"F0.wireOp",EDGE,"E2649"),sQuery(id+"F0.wireOp",EDGE,"E2650"),sQuery(id+"F0.wireOp",EDGE,"E2651"),sQuery(id+"F0.wireOp",EDGE,"E2652"),sQuery(id+"F0.wireOp",EDGE,"E2653"),sQuery(id+"F0.wireOp",EDGE,"E2654"),sQuery(id+"F0.wireOp",EDGE,"E2655"),sQuery(id+"F0.wireOp",EDGE,"E2656"),sQuery(id+"F0.wireOp",EDGE,"E2657"),sQuery(id+"F0.wireOp",EDGE,"E2658"),sQuery(id+"F0.wireOp",EDGE,"E2659"),sQuery(id+"F0.wireOp",EDGE,"E2660"),sQuery(id+"F0.wireOp",EDGE,"E2661"),sQuery(id+"F0.wireOp",EDGE,"E2662"),sQuery(id+"F0.wireOp",EDGE,"E2663"),sQuery(id+"F0.wireOp",EDGE,"E2664"),sQuery(id+"F0.wireOp",EDGE,"E2665"),sQuery(id+"F0.wireOp",EDGE,"E2666"),sQuery(id+"F0.wireOp",EDGE,"E2667"),sQuery(id+"F0.wireOp",EDGE,"E2668"),sQuery(id+"F0.wireOp",EDGE,"E2669"),sQuery(id+"F0.wireOp",EDGE,"E2670"),sQuery(id+"F0.wireOp",EDGE,"E2671"),sQuery(id+"F0.wireOp",EDGE,"E2672"),sQuery(id+"F0.wireOp",EDGE,"E2673"),sQuery(id+"F0.wireOp",EDGE,"E2674"),sQuery(id+"F0.wireOp",EDGE,"E2675"),sQuery(id+"F0.wireOp",EDGE,"E2676"),sQuery(id+"F0.wireOp",EDGE,"E2677"),sQuery(id+"F0.wireOp",EDGE,"E2678"),sQuery(id+"F0.wireOp",EDGE,"E2679"),sQuery(id+"F0.wireOp",EDGE,"E2680"),sQuery(id+"F0.wireOp",EDGE,"E2681"),sQuery(id+"F0.wireOp",EDGE,"E2682"),sQuery(id+"F0.wireOp",EDGE,"E2683"),sQuery(id+"F0.wireOp",EDGE,"E2684"),sQuery(id+"F0.wireOp",EDGE,"E2685"),sQuery(id+"F0.wireOp",EDGE,"E2686"),sQuery(id+"F0.wireOp",EDGE,"E2687"),sQuery(id+"F0.wireOp",EDGE,"E2688"),sQuery(id+"F0.wireOp",EDGE,"E2689"),sQuery(id+"F0.wireOp",EDGE,"E2690"),sQuery(id+"F0.wireOp",EDGE,"E2691"),sQuery(id+"F0.wireOp",EDGE,"E2692"),sQuery(id+"F0.wireOp",EDGE,"E2693"),sQuery(id+"F0.wireOp",EDGE,"E2694"),sQuery(id+"F0.wireOp",EDGE,"E2695"),sQuery(id+"F0.wireOp",EDGE,"E2696"),sQuery(id+"F0.wireOp",EDGE,"E2697"),sQuery(id+"F0.wireOp",EDGE,"E2698"),sQuery(id+"F0.wireOp",EDGE,"E2699"),sQuery(id+"F0.wireOp",EDGE,"E2700"),sQuery(id+"F0.wireOp",EDGE,"E2701"),sQuery(id+"F0.wireOp",EDGE,"E2702"),sQuery(id+"F0.wireOp",EDGE,"E2703"),sQuery(id+"F0.wireOp",EDGE,"E2704"),sQuery(id+"F0.wireOp",EDGE,"E2705"),sQuery(id+"F0.wireOp",EDGE,"E2706"),sQuery(id+"F0.wireOp",EDGE,"E2707"),sQuery(id+"F0.wireOp",EDGE,"E2708"),sQuery(id+"F0.wireOp",EDGE,"E2709"),sQuery(id+"F0.wireOp",EDGE,"E2710"),sQuery(id+"F0.wireOp",EDGE,"E2711"),sQuery(id+"F0.wireOp",EDGE,"E2712"),sQuery(id+"F0.wireOp",EDGE,"E2713"),sQuery(id+"F0.wireOp",EDGE,"E2714"),sQuery(id+"F0.wireOp",EDGE,"E2715"),sQuery(id+"F0.wireOp",EDGE,"E2716"),sQuery(id+"F0.wireOp",EDGE,"E2717"),sQuery(id+"F0.wireOp",EDGE,"E2718"),sQuery(id+"F0.wireOp",EDGE,"E2719"),sQuery(id+"F0.wireOp",EDGE,"E2720"),sQuery(id+"F0.wireOp",EDGE,"E2721"),sQuery(id+"F0.wireOp",EDGE,"E2722"),sQuery(id+"F0.wireOp",EDGE,"E2723"),sQuery(id+"F0.wireOp",EDGE,"E2724"),sQuery(id+"F0.wireOp",EDGE,"E2725"),sQuery(id+"F0.wireOp",EDGE,"E2726"),sQuery(id+"F0.wireOp",EDGE,"E2727"),sQuery(id+"F0.wireOp",EDGE,"E2728"),sQuery(id+"F0.wireOp",EDGE,"E2729"),sQuery(id+"F0.wireOp",EDGE,"E2730"),sQuery(id+"F0.wireOp",EDGE,"E2731"),sQuery(id+"F0.wireOp",EDGE,"E2732"),sQuery(id+"F0.wireOp",EDGE,"E2733"),sQuery(id+"F0.wireOp",EDGE,"E2734"),sQuery(id+"F0.wireOp",EDGE,"E2735"),sQuery(id+"F0.wireOp",EDGE,"E2736"),sQuery(id+"F0.wireOp",EDGE,"E2737"),sQuery(id+"F0.wireOp",EDGE,"E2738"),sQuery(id+"F0.wireOp",EDGE,"E2739"),sQuery(id+"F0.wireOp",EDGE,"E2740"),sQuery(id+"F0.wireOp",EDGE,"E2741"),sQuery(id+"F0.wireOp",EDGE,"E2742"),sQuery(id+"F0.wireOp",EDGE,"E2743"),sQuery(id+"F0.wireOp",EDGE,"E2744"),sQuery(id+"F0.wireOp",EDGE,"E2745"),sQuery(id+"F0.wireOp",EDGE,"E2746"),sQuery(id+"F0.wireOp",EDGE,"E2747"),sQuery(id+"F0.wireOp",EDGE,"E2748"),sQuery(id+"F0.wireOp",EDGE,"E2749"),sQuery(id+"F0.wireOp",EDGE,"E2750"),sQuery(id+"F0.wireOp",EDGE,"E2751"),sQuery(id+"F0.wireOp",EDGE,"E2752"),sQuery(id+"F0.wireOp",EDGE,"E2753"),sQuery(id+"F0.wireOp",EDGE,"E2754"),sQuery(id+"F0.wireOp",EDGE,"E2755"),sQuery(id+"F0.wireOp",EDGE,"E2756"),sQuery(id+"F0.wireOp",EDGE,"E2757"),sQuery(id+"F0.wireOp",EDGE,"E2758"),sQuery(id+"F0.wireOp",EDGE,"E2759"),sQuery(id+"F0.wireOp",EDGE,"E2760"),sQuery(id+"F0.wireOp",EDGE,"E2761"),sQuery(id+"F0.wireOp",EDGE,"E2762"),sQuery(id+"F0.wireOp",EDGE,"E2763"),sQuery(id+"F0.wireOp",EDGE,"E2764"),sQuery(id+"F0.wireOp",EDGE,"E2765"),sQuery(id+"F0.wireOp",EDGE,"E2766"),sQuery(id+"F0.wireOp",EDGE,"E2767"),sQuery(id+"F0.wireOp",EDGE,"E2768"),sQuery(id+"F0.wireOp",EDGE,"E2769"),sQuery(id+"F0.wireOp",EDGE,"E2770"),sQuery(id+"F0.wireOp",EDGE,"E2771"),sQuery(id+"F0.wireOp",EDGE,"E2772"),sQuery(id+"F0.wireOp",EDGE,"E2773"),sQuery(id+"F0.wireOp",EDGE,"E2774"),sQuery(id+"F0.wireOp",EDGE,"E2775"),sQuery(id+"F0.wireOp",EDGE,"E2776"),sQuery(id+"F0.wireOp",EDGE,"E2777"),sQuery(id+"F0.wireOp",EDGE,"E2778"),sQuery(id+"F0.wireOp",EDGE,"E2779"),sQuery(id+"F0.wireOp",EDGE,"E2780"),sQuery(id+"F0.wireOp",EDGE,"E2781"),sQuery(id+"F0.wireOp",EDGE,"E2782"),sQuery(id+"F0.wireOp",EDGE,"E2783"),sQuery(id+"F0.wireOp",EDGE,"E2784"),sQuery(id+"F0.wireOp",EDGE,"E2785"),sQuery(id+"F0.wireOp",EDGE,"E2786"),sQuery(id+"F0.wireOp",EDGE,"E2787"),sQuery(id+"F0.wireOp",EDGE,"E2788"),sQuery(id+"F0.wireOp",EDGE,"E2789"),sQuery(id+"F0.wireOp",EDGE,"E2790"),sQuery(id+"F0.wireOp",EDGE,"E2791"),sQuery(id+"F0.wireOp",EDGE,"E2792"),sQuery(id+"F0.wireOp",EDGE,"E2793"),sQuery(id+"F0.wireOp",EDGE,"E2794"),sQuery(id+"F0.wireOp",EDGE,"E2795"),sQuery(id+"F0.wireOp",EDGE,"E2796"),sQuery(id+"F0.wireOp",EDGE,"E2797"),sQuery(id+"F0.wireOp",EDGE,"E2798"),sQuery(id+"F0.wireOp",EDGE,"E2799"),sQuery(id+"F0.wireOp",EDGE,"E2800"),sQuery(id+"F0.wireOp",EDGE,"E2801"),sQuery(id+"F0.wireOp",EDGE,"E2802"),sQuery(id+"F0.wireOp",EDGE,"E2803"),sQuery(id+"F0.wireOp",EDGE,"E2804"),sQuery(id+"F0.wireOp",EDGE,"E2805"),sQuery(id+"F0.wireOp",EDGE,"E2806"),sQuery(id+"F0.wireOp",EDGE,"E2807"),sQuery(id+"F0.wireOp",EDGE,"E2808"),sQuery(id+"F0.wireOp",EDGE,"E2809"),sQuery(id+"F0.wireOp",EDGE,"E2810"),sQuery(id+"F0.wireOp",EDGE,"E2811"),sQuery(id+"F0.wireOp",EDGE,"E2812"),sQuery(id+"F0.wireOp",EDGE,"E2813"),sQuery(id+"F0.wireOp",EDGE,"E2814"),sQuery(id+"F0.wireOp",EDGE,"E2815"),sQuery(id+"F0.wireOp",EDGE,"E2816"),sQuery(id+"F0.wireOp",EDGE,"E2817"),sQuery(id+"F0.wireOp",EDGE,"E2818"),sQuery(id+"F0.wireOp",EDGE,"E2819"),sQuery(id+"F0.wireOp",EDGE,"E2820"),sQuery(id+"F0.wireOp",EDGE,"E2821"),sQuery(id+"F0.wireOp",EDGE,"E2822"),sQuery(id+"F0.wireOp",EDGE,"E2823"),sQuery(id+"F0.wireOp",EDGE,"E2824"),sQuery(id+"F0.wireOp",EDGE,"E2825"),sQuery(id+"F0.wireOp",EDGE,"E2826"),sQuery(id+"F0.wireOp",EDGE,"E2827"),sQuery(id+"F0.wireOp",EDGE,"E2828"),sQuery(id+"F0.wireOp",EDGE,"E2829"),sQuery(id+"F0.wireOp",EDGE,"E2830"),sQuery(id+"F0.wireOp",EDGE,"E2831"),sQuery(id+"F0.wireOp",EDGE,"E2832"),sQuery(id+"F0.wireOp",EDGE,"E2833"),sQuery(id+"F0.wireOp",EDGE,"E2834"),sQuery(id+"F0.wireOp",EDGE,"E2835"),sQuery(id+"F0.wireOp",EDGE,"E2836"),sQuery(id+"F0.wireOp",EDGE,"E2837"),sQuery(id+"F0.wireOp",EDGE,"E2838"),sQuery(id+"F0.wireOp",EDGE,"E2839"),sQuery(id+"F0.wireOp",EDGE,"E2840"),sQuery(id+"F0.wireOp",EDGE,"E2841"),sQuery(id+"F0.wireOp",EDGE,"E2842"),sQuery(id+"F0.wireOp",EDGE,"E2843"),sQuery(id+"F0.wireOp",EDGE,"E2844"),sQuery(id+"F0.wireOp",EDGE,"E2845"),sQuery(id+"F0.wireOp",EDGE,"E2846"),sQuery(id+"F0.wireOp",EDGE,"E2847"),sQuery(id+"F0.wireOp",EDGE,"E2848"),sQuery(id+"F0.wireOp",EDGE,"E2849"),sQuery(id+"F0.wireOp",EDGE,"E2850"),sQuery(id+"F0.wireOp",EDGE,"E2851"),sQuery(id+"F0.wireOp",EDGE,"E2852"),sQuery(id+"F0.wireOp",EDGE,"E2853"),sQuery(id+"F0.wireOp",EDGE,"E2854"),sQuery(id+"F0.wireOp",EDGE,"E2855"),sQuery(id+"F0.wireOp",EDGE,"E2856"),sQuery(id+"F0.wireOp",EDGE,"E2857"),sQuery(id+"F0.wireOp",EDGE,"E2858"),sQuery(id+"F0.wireOp",EDGE,"E2859"),sQuery(id+"F0.wireOp",EDGE,"E2860"),sQuery(id+"F0.wireOp",EDGE,"E2861"),sQuery(id+"F0.wireOp",EDGE,"E2862"),sQuery(id+"F0.wireOp",EDGE,"E2863"),sQuery(id+"F0.wireOp",EDGE,"E2864"),sQuery(id+"F0.wireOp",EDGE,"E2865"),sQuery(id+"F0.wireOp",EDGE,"E2866"),sQuery(id+"F0.wireOp",EDGE,"E2867"),sQuery(id+"F0.wireOp",EDGE,"E2868"),sQuery(id+"F0.wireOp",EDGE,"E2869"),sQuery(id+"F0.wireOp",EDGE,"E2870"),sQuery(id+"F0.wireOp",EDGE,"E2871"),sQuery(id+"F0.wireOp",EDGE,"E2872"),sQuery(id+"F0.wireOp",EDGE,"E2873"),sQuery(id+"F0.wireOp",EDGE,"E2874"),sQuery(id+"F0.wireOp",EDGE,"E2875"),sQuery(id+"F0.wireOp",EDGE,"E2876"),sQuery(id+"F0.wireOp",EDGE,"E2877"),sQuery(id+"F0.wireOp",EDGE,"E2878"),sQuery(id+"F0.wireOp",EDGE,"E2879"),sQuery(id+"F0.wireOp",EDGE,"E2880"),sQuery(id+"F0.wireOp",EDGE,"E2881"),sQuery(id+"F0.wireOp",EDGE,"E2882"),sQuery(id+"F0.wireOp",EDGE,"E2883"),sQuery(id+"F0.wireOp",EDGE,"E2884"),sQuery(id+"F0.wireOp",EDGE,"E2885"),sQuery(id+"F0.wireOp",EDGE,"E2886"),sQuery(id+"F0.wireOp",EDGE,"E2887"),sQuery(id+"F0.wireOp",EDGE,"E2888"),sQuery(id+"F0.wireOp",EDGE,"E2889"),sQuery(id+"F0.wireOp",EDGE,"E2890"),sQuery(id+"F0.wireOp",EDGE,"E2891"),sQuery(id+"F0.wireOp",EDGE,"E2892"),sQuery(id+"F0.wireOp",EDGE,"E2893"),sQuery(id+"F0.wireOp",EDGE,"E2894"),sQuery(id+"F0.wireOp",EDGE,"E2895"),sQuery(id+"F0.wireOp",EDGE,"E2896"),sQuery(id+"F0.wireOp",EDGE,"E2897"),sQuery(id+"F0.wireOp",EDGE,"E2898"),sQuery(id+"F0.wireOp",EDGE,"E2899"),sQuery(id+"F0.wireOp",EDGE,"E2900"),sQuery(id+"F0.wireOp",EDGE,"E2901"),sQuery(id+"F0.wireOp",EDGE,"E2902"),sQuery(id+"F0.wireOp",EDGE,"E2903"),sQuery(id+"F0.wireOp",EDGE,"E2904"),sQuery(id+"F0.wireOp",EDGE,"E2905"),sQuery(id+"F0.wireOp",EDGE,"E2906"),sQuery(id+"F0.wireOp",EDGE,"E2907"),sQuery(id+"F0.wireOp",EDGE,"E2908"),sQuery(id+"F0.wireOp",EDGE,"E2909"),sQuery(id+"F0.wireOp",EDGE,"E2910"),sQuery(id+"F0.wireOp",EDGE,"E2911"),sQuery(id+"F0.wireOp",EDGE,"E2912"),sQuery(id+"F0.wireOp",EDGE,"E2913"),sQuery(id+"F0.wireOp",EDGE,"E2914"),sQuery(id+"F0.wireOp",EDGE,"E2915"),sQuery(id+"F0.wireOp",EDGE,"E2916"),sQuery(id+"F0.wireOp",EDGE,"E2917"),sQuery(id+"F0.wireOp",EDGE,"E2918"),sQuery(id+"F0.wireOp",EDGE,"E2919"),sQuery(id+"F0.wireOp",EDGE,"E2920"),sQuery(id+"F0.wireOp",EDGE,"E2921"),sQuery(id+"F0.wireOp",EDGE,"E2922"),sQuery(id+"F0.wireOp",EDGE,"E2923"),sQuery(id+"F0.wireOp",EDGE,"E2924"),sQuery(id+"F0.wireOp",EDGE,"E2925"),sQuery(id+"F0.wireOp",EDGE,"E2926"),sQuery(id+"F0.wireOp",EDGE,"E2927"),sQuery(id+"F0.wireOp",EDGE,"E2928"),sQuery(id+"F0.wireOp",EDGE,"E2929"),sQuery(id+"F0.wireOp",EDGE,"E2930"),sQuery(id+"F0.wireOp",EDGE,"E2931"),sQuery(id+"F0.wireOp",EDGE,"E2932"),sQuery(id+"F0.wireOp",EDGE,"E2933"),sQuery(id+"F0.wireOp",EDGE,"E2934"),sQuery(id+"F0.wireOp",EDGE,"E2935"),sQuery(id+"F0.wireOp",EDGE,"E2936"),sQuery(id+"F0.wireOp",EDGE,"E2937"),sQuery(id+"F0.wireOp",EDGE,"E2938"),sQuery(id+"F0.wireOp",EDGE,"E2939"),sQuery(id+"F0.wireOp",EDGE,"E2940"),sQuery(id+"F0.wireOp",EDGE,"E2941"),sQuery(id+"F0.wireOp",EDGE,"E2942"),sQuery(id+"F0.wireOp",EDGE,"E2943"),sQuery(id+"F0.wireOp",EDGE,"E2944"),sQuery(id+"F0.wireOp",EDGE,"E2945"),sQuery(id+"F0.wireOp",EDGE,"E2946"),sQuery(id+"F0.wireOp",EDGE,"E2947"),sQuery(id+"F0.wireOp",EDGE,"E2948"),sQuery(id+"F0.wireOp",EDGE,"E2949"),sQuery(id+"F0.wireOp",EDGE,"E2950"),sQuery(id+"F0.wireOp",EDGE,"E2951"),sQuery(id+"F0.wireOp",EDGE,"E2952"),sQuery(id+"F0.wireOp",EDGE,"E2953"),sQuery(id+"F0.wireOp",EDGE,"E2954"),sQuery(id+"F0.wireOp",EDGE,"E2955"),sQuery(id+"F0.wireOp",EDGE,"E2956"),sQuery(id+"F0.wireOp",EDGE,"E2957"),sQuery(id+"F0.wireOp",EDGE,"E2958"),sQuery(id+"F0.wireOp",EDGE,"E2959"),sQuery(id+"F0.wireOp",EDGE,"E2960"),sQuery(id+"F0.wireOp",EDGE,"E2961"),sQuery(id+"F0.wireOp",EDGE,"E2962"),sQuery(id+"F0.wireOp",EDGE,"E2963"),sQuery(id+"F0.wireOp",EDGE,"E2964"),sQuery(id+"F0.wireOp",EDGE,"E2965"),sQuery(id+"F0.wireOp",EDGE,"E2966"),sQuery(id+"F0.wireOp",EDGE,"E2967"),sQuery(id+"F0.wireOp",EDGE,"E2968"),sQuery(id+"F0.wireOp",EDGE,"E2969"),sQuery(id+"F0.wireOp",EDGE,"E2970"),sQuery(id+"F0.wireOp",EDGE,"E2971"),sQuery(id+"F0.wireOp",EDGE,"E2972"),sQuery(id+"F0.wireOp",EDGE,"E2973"),sQuery(id+"F0.wireOp",EDGE,"E2974"),sQuery(id+"F0.wireOp",EDGE,"E2975"),sQuery(id+"F0.wireOp",EDGE,"E2976"),sQuery(id+"F0.wireOp",EDGE,"E2977"),sQuery(id+"F0.wireOp",EDGE,"E2978"),sQuery(id+"F0.wireOp",EDGE,"E2979"),sQuery(id+"F0.wireOp",EDGE,"E2980"),sQuery(id+"F0.wireOp",EDGE,"E2981"),sQuery(id+"F0.wireOp",EDGE,"E2982"),sQuery(id+"F0.wireOp",EDGE,"E2983"),sQuery(id+"F0.wireOp",EDGE,"E2984"),sQuery(id+"F0.wireOp",EDGE,"E2985"),sQuery(id+"F0.wireOp",EDGE,"E2986"),sQuery(id+"F0.wireOp",EDGE,"E2987"),sQuery(id+"F0.wireOp",EDGE,"E2988"),sQuery(id+"F0.wireOp",EDGE,"E2989"),sQuery(id+"F0.wireOp",EDGE,"E2990"),sQuery(id+"F0.wireOp",EDGE,"E2991"),sQuery(id+"F0.wireOp",EDGE,"E2992"),sQuery(id+"F0.wireOp",EDGE,"E2993"),sQuery(id+"F0.wireOp",EDGE,"E2994"),sQuery(id+"F0.wireOp",EDGE,"E2995"),sQuery(id+"F0.wireOp",EDGE,"E2996"),sQuery(id+"F0.wireOp",EDGE,"E2997"),sQuery(id+"F0.wireOp",EDGE,"E2998"),sQuery(id+"F0.wireOp",EDGE,"E2999"),sQuery(id+"F0.wireOp",EDGE,"E3000"),sQuery(id+"F0.wireOp",EDGE,"E3001"),sQuery(id+"F0.wireOp",EDGE,"E3002"),sQuery(id+"F0.wireOp",EDGE,"E3003"),sQuery(id+"F0.wireOp",EDGE,"E3004"),sQuery(id+"F0.wireOp",EDGE,"E3005"),sQuery(id+"F0.wireOp",EDGE,"E3006"),sQuery(id+"F0.wireOp",EDGE,"E3007"),sQuery(id+"F0.wireOp",EDGE,"E3008"),sQuery(id+"F0.wireOp",EDGE,"E3009"),sQuery(id+"F0.wireOp",EDGE,"E3010"),sQuery(id+"F0.wireOp",EDGE,"E3011"),sQuery(id+"F0.wireOp",EDGE,"E3012"),sQuery(id+"F0.wireOp",EDGE,"E3013"),sQuery(id+"F0.wireOp",EDGE,"E3014"),sQuery(id+"F0.wireOp",EDGE,"E3015"),sQuery(id+"F0.wireOp",EDGE,"E3016"),sQuery(id+"F0.wireOp",EDGE,"E3017"),sQuery(id+"F0.wireOp",EDGE,"E3018"),sQuery(id+"F0.wireOp",EDGE,"E3019"),sQuery(id+"F0.wireOp",EDGE,"E3020"),sQuery(id+"F0.wireOp",EDGE,"E3021"),sQuery(id+"F0.wireOp",EDGE,"E3022"),sQuery(id+"F0.wireOp",EDGE,"E3023"),sQuery(id+"F0.wireOp",EDGE,"E3024"),sQuery(id+"F0.wireOp",EDGE,"E3025"),sQuery(id+"F0.wireOp",EDGE,"E3026"),sQuery(id+"F0.wireOp",EDGE,"E3027"),sQuery(id+"F0.wireOp",EDGE,"E3028"),sQuery(id+"F0.wireOp",EDGE,"E3029"),sQuery(id+"F0.wireOp",EDGE,"E3030"),sQuery(id+"F0.wireOp",EDGE,"E3031"),sQuery(id+"F0.wireOp",EDGE,"E3032"),sQuery(id+"F0.wireOp",EDGE,"E3033"),sQuery(id+"F0.wireOp",EDGE,"E3034"),sQuery(id+"F0.wireOp",EDGE,"E3035"),sQuery(id+"F0.wireOp",EDGE,"E3036"),sQuery(id+"F0.wireOp",EDGE,"E3037"),sQuery(id+"F0.wireOp",EDGE,"E3038"),sQuery(id+"F0.wireOp",EDGE,"E3039"),sQuery(id+"F0.wireOp",EDGE,"E3040"),sQuery(id+"F0.wireOp",EDGE,"E3041"),sQuery(id+"F0.wireOp",EDGE,"E3042"),sQuery(id+"F0.wireOp",EDGE,"E3043"),sQuery(id+"F0.wireOp",EDGE,"E3044"),sQuery(id+"F0.wireOp",EDGE,"E3045"),sQuery(id+"F0.wireOp",EDGE,"E3046"),sQuery(id+"F0.wireOp",EDGE,"E3047"),sQuery(id+"F0.wireOp",EDGE,"E3048"),sQuery(id+"F0.wireOp",EDGE,"E3049"),sQuery(id+"F0.wireOp",EDGE,"E3050"),sQuery(id+"F0.wireOp",EDGE,"E3051"),sQuery(id+"F0.wireOp",EDGE,"E3052"),sQuery(id+"F0.wireOp",EDGE,"E3053"),sQuery(id+"F0.wireOp",EDGE,"E3054"),sQuery(id+"F0.wireOp",EDGE,"E3055"),sQuery(id+"F0.wireOp",EDGE,"E3056"),sQuery(id+"F0.wireOp",EDGE,"E3057"),sQuery(id+"F0.wireOp",EDGE,"E3058"),sQuery(id+"F0.wireOp",EDGE,"E3059"),sQuery(id+"F0.wireOp",EDGE,"E3060"),sQuery(id+"F0.wireOp",EDGE,"E3061"),sQuery(id+"F0.wireOp",EDGE,"E3062"),sQuery(id+"F0.wireOp",EDGE,"E3063"),sQuery(id+"F0.wireOp",EDGE,"E3064"),sQuery(id+"F0.wireOp",EDGE,"E3065"),sQuery(id+"F0.wireOp",EDGE,"E3066"),sQuery(id+"F0.wireOp",EDGE,"E3067"),sQuery(id+"F0.wireOp",EDGE,"E3068"),sQuery(id+"F0.wireOp",EDGE,"E3069"),sQuery(id+"F0.wireOp",EDGE,"E3070"),sQuery(id+"F0.wireOp",EDGE,"E3071"),sQuery(id+"F0.wireOp",EDGE,"E3072"),sQuery(id+"F0.wireOp",EDGE,"E3073"),sQuery(id+"F0.wireOp",EDGE,"E3074"),sQuery(id+"F0.wireOp",EDGE,"E3075"),sQuery(id+"F0.wireOp",EDGE,"E3076"),sQuery(id+"F0.wireOp",EDGE,"E3077"),sQuery(id+"F0.wireOp",EDGE,"E3078"),sQuery(id+"F0.wireOp",EDGE,"E3079"),sQuery(id+"F0.wireOp",EDGE,"E3080"),sQuery(id+"F0.wireOp",EDGE,"E3081"),sQuery(id+"F0.wireOp",EDGE,"E3082"),sQuery(id+"F0.wireOp",EDGE,"E3083"),sQuery(id+"F0.wireOp",EDGE,"E3084"),sQuery(id+"F0.wireOp",EDGE,"E3085"),sQuery(id+"F0.wireOp",EDGE,"E3086"),sQuery(id+"F0.wireOp",EDGE,"E3087"),sQuery(id+"F0.wireOp",EDGE,"E3088"),sQuery(id+"F0.wireOp",EDGE,"E3089"),sQuery(id+"F0.wireOp",EDGE,"E3090"),sQuery(id+"F0.wireOp",EDGE,"E3091"),sQuery(id+"F0.wireOp",EDGE,"E3092"),sQuery(id+"F0.wireOp",EDGE,"E3093"),sQuery(id+"F0.wireOp",EDGE,"E3094"),sQuery(id+"F0.wireOp",EDGE,"E3095"),sQuery(id+"F0.wireOp",EDGE,"E3096"),sQuery(id+"F0.wireOp",EDGE,"E3097"),sQuery(id+"F0.wireOp",EDGE,"E3098"),sQuery(id+"F0.wireOp",EDGE,"E3099"),sQuery(id+"F0.wireOp",EDGE,"E3100"),sQuery(id+"F0.wireOp",EDGE,"E3101"),sQuery(id+"F0.wireOp",EDGE,"E3102"),sQuery(id+"F0.wireOp",EDGE,"E3103"),sQuery(id+"F0.wireOp",EDGE,"E3104"),sQuery(id+"F0.wireOp",EDGE,"E3105"),sQuery(id+"F0.wireOp",EDGE,"E3106"),sQuery(id+"F0.wireOp",EDGE,"E3107"),sQuery(id+"F0.wireOp",EDGE,"E3108"),sQuery(id+"F0.wireOp",EDGE,"E3109"),sQuery(id+"F0.wireOp",EDGE,"E3110"),sQuery(id+"F0.wireOp",EDGE,"E3111"),sQuery(id+"F0.wireOp",EDGE,"E3112"),sQuery(id+"F0.wireOp",EDGE,"E3113"),sQuery(id+"F0.wireOp",EDGE,"E3114"),sQuery(id+"F0.wireOp",EDGE,"E3115"),sQuery(id+"F0.wireOp",EDGE,"E3116"),sQuery(id+"F0.wireOp",EDGE,"E3117"),sQuery(id+"F0.wireOp",EDGE,"E3118"),sQuery(id+"F0.wireOp",EDGE,"E3119"),sQuery(id+"F0.wireOp",EDGE,"E3120"),sQuery(id+"F0.wireOp",EDGE,"E3121"),sQuery(id+"F0.wireOp",EDGE,"E3122"),sQuery(id+"F0.wireOp",EDGE,"E3123"),sQuery(id+"F0.wireOp",EDGE,"E3124"),sQuery(id+"F0.wireOp",EDGE,"E3125"),sQuery(id+"F0.wireOp",EDGE,"E3126"),sQuery(id+"F0.wireOp",EDGE,"E3127"),sQuery(id+"F0.wireOp",EDGE,"E3128"),sQuery(id+"F0.wireOp",EDGE,"E3129"),sQuery(id+"F0.wireOp",EDGE,"E3130"),sQuery(id+"F0.wireOp",EDGE,"E3131"),sQuery(id+"F0.wireOp",EDGE,"E3132"),sQuery(id+"F0.wireOp",EDGE,"E3133"),sQuery(id+"F0.wireOp",EDGE,"E3134"),sQuery(id+"F0.wireOp",EDGE,"E3135"),sQuery(id+"F0.wireOp",EDGE,"E3136"),sQuery(id+"F0.wireOp",EDGE,"E3137"),sQuery(id+"F0.wireOp",EDGE,"E3138"),sQuery(id+"F0.wireOp",EDGE,"E3139"),sQuery(id+"F0.wireOp",EDGE,"E3140"),sQuery(id+"F0.wireOp",EDGE,"E3141"),sQuery(id+"F0.wireOp",EDGE,"E3142"),sQuery(id+"F0.wireOp",EDGE,"E3143"),sQuery(id+"F0.wireOp",EDGE,"E3144"),sQuery(id+"F0.wireOp",EDGE,"E3145"),sQuery(id+"F0.wireOp",EDGE,"E3146"),sQuery(id+"F0.wireOp",EDGE,"E3147"),sQuery(id+"F0.wireOp",EDGE,"E3148"),sQuery(id+"F0.wireOp",EDGE,"E3149"),sQuery(id+"F0.wireOp",EDGE,"E3150"),sQuery(id+"F0.wireOp",EDGE,"E3151"),sQuery(id+"F0.wireOp",EDGE,"E3152"),sQuery(id+"F0.wireOp",EDGE,"E3153"),sQuery(id+"F0.wireOp",EDGE,"E3154"),sQuery(id+"F0.wireOp",EDGE,"E3155"),sQuery(id+"F0.wireOp",EDGE,"E3156"),sQuery(id+"F0.wireOp",EDGE,"E3157"),sQuery(id+"F0.wireOp",EDGE,"E3158"),sQuery(id+"F0.wireOp",EDGE,"E3159"),sQuery(id+"F0.wireOp",EDGE,"E3160"),sQuery(id+"F0.wireOp",EDGE,"E3161"),sQuery(id+"F0.wireOp",EDGE,"E3162"),sQuery(id+"F0.wireOp",EDGE,"E3163"),sQuery(id+"F0.wireOp",EDGE,"E3164"),sQuery(id+"F0.wireOp",EDGE,"E3165"),sQuery(id+"F0.wireOp",EDGE,"E3166"),sQuery(id+"F0.wireOp",EDGE,"E3167"),sQuery(id+"F0.wireOp",EDGE,"E3168"),sQuery(id+"F0.wireOp",EDGE,"E3169"),sQuery(id+"F0.wireOp",EDGE,"E3170"),sQuery(id+"F0.wireOp",EDGE,"E3171"),sQuery(id+"F0.wireOp",EDGE,"E3172"),sQuery(id+"F0.wireOp",EDGE,"E3173"),sQuery(id+"F0.wireOp",EDGE,"E3174"),sQuery(id+"F0.wireOp",EDGE,"E3175"),sQuery(id+"F0.wireOp",EDGE,"E3176"),sQuery(id+"F0.wireOp",EDGE,"E3177"),sQuery(id+"F0.wireOp",EDGE,"E3178"),sQuery(id+"F0.wireOp",EDGE,"E3179"),sQuery(id+"F0.wireOp",EDGE,"E3180"),sQuery(id+"F0.wireOp",EDGE,"E3181"),sQuery(id+"F0.wireOp",EDGE,"E3182"),sQuery(id+"F0.wireOp",EDGE,"E3183"),sQuery(id+"F0.wireOp",EDGE,"E3184"),sQuery(id+"F0.wireOp",EDGE,"E3185"),sQuery(id+"F0.wireOp",EDGE,"E3186"),sQuery(id+"F0.wireOp",EDGE,"E3187"),sQuery(id+"F0.wireOp",EDGE,"E3188"),sQuery(id+"F0.wireOp",EDGE,"E3189"),sQuery(id+"F0.wireOp",EDGE,"E3190"),sQuery(id+"F0.wireOp",EDGE,"E3191"),sQuery(id+"F0.wireOp",EDGE,"E3192"),sQuery(id+"F0.wireOp",EDGE,"E3193"),sQuery(id+"F0.wireOp",EDGE,"E3194"),sQuery(id+"F0.wireOp",EDGE,"E3195"),sQuery(id+"F0.wireOp",EDGE,"E3196"),sQuery(id+"F0.wireOp",EDGE,"E3197"),sQuery(id+"F0.wireOp",EDGE,"E3198"),sQuery(id+"F0.wireOp",EDGE,"E3199"),sQuery(id+"F0.wireOp",EDGE,"E3200"),sQuery(id+"F0.wireOp",EDGE,"E3201"),sQuery(id+"F0.wireOp",EDGE,"E3202"),sQuery(id+"F0.wireOp",EDGE,"E3203"),sQuery(id+"F0.wireOp",EDGE,"E3204"),sQuery(id+"F0.wireOp",EDGE,"E3205"),sQuery(id+"F0.wireOp",EDGE,"E3206"),sQuery(id+"F0.wireOp",EDGE,"E3207"),sQuery(id+"F0.wireOp",EDGE,"E3208"),sQuery(id+"F0.wireOp",EDGE,"E3209"),sQuery(id+"F0.wireOp",EDGE,"E3210"),sQuery(id+"F0.wireOp",EDGE,"E3211"),sQuery(id+"F0.wireOp",EDGE,"E3212"),sQuery(id+"F0.wireOp",EDGE,"E3213"),sQuery(id+"F0.wireOp",EDGE,"E3214"),sQuery(id+"F0.wireOp",EDGE,"E3215"),sQuery(id+"F0.wireOp",EDGE,"E3216"),sQuery(id+"F0.wireOp",EDGE,"E3217"),sQuery(id+"F0.wireOp",EDGE,"E3218"),sQuery(id+"F0.wireOp",EDGE,"E3219"),sQuery(id+"F0.wireOp",EDGE,"E3220"),sQuery(id+"F0.wireOp",EDGE,"E3221"),sQuery(id+"F0.wireOp",EDGE,"E3222"),sQuery(id+"F0.wireOp",EDGE,"E3223"),sQuery(id+"F0.wireOp",EDGE,"E3224"),sQuery(id+"F0.wireOp",EDGE,"E3225"),sQuery(id+"F0.wireOp",EDGE,"E3226"),sQuery(id+"F0.wireOp",EDGE,"E3227"),sQuery(id+"F0.wireOp",EDGE,"E3228"),sQuery(id+"F0.wireOp",EDGE,"E3229"),sQuery(id+"F0.wireOp",EDGE,"E3230"),sQuery(id+"F0.wireOp",EDGE,"E3231"),sQuery(id+"F0.wireOp",EDGE,"E3232"),sQuery(id+"F0.wireOp",EDGE,"E3233"),sQuery(id+"F0.wireOp",EDGE,"E3234"),sQuery(id+"F0.wireOp",EDGE,"E3235"),sQuery(id+"F0.wireOp",EDGE,"E3236"),sQuery(id+"F0.wireOp",EDGE,"E3237"),sQuery(id+"F0.wireOp",EDGE,"E3238"),sQuery(id+"F0.wireOp",EDGE,"E3239"),sQuery(id+"F0.wireOp",EDGE,"E3240"),sQuery(id+"F0.wireOp",EDGE,"E3241"),sQuery(id+"F0.wireOp",EDGE,"E3242"),sQuery(id+"F0.wireOp",EDGE,"E3243"),sQuery(id+"F0.wireOp",EDGE,"E3244"),sQuery(id+"F0.wireOp",EDGE,"E3245"),sQuery(id+"F0.wireOp",EDGE,"E3246"),sQuery(id+"F0.wireOp",EDGE,"E3247"),sQuery(id+"F0.wireOp",EDGE,"E3248"),sQuery(id+"F0.wireOp",EDGE,"E3249"),sQuery(id+"F0.wireOp",EDGE,"E3250"),sQuery(id+"F0.wireOp",EDGE,"E3251"),sQuery(id+"F0.wireOp",EDGE,"E3252"),sQuery(id+"F0.wireOp",EDGE,"E3253"),sQuery(id+"F0.wireOp",EDGE,"E3254"),sQuery(id+"F0.wireOp",EDGE,"E3255"),sQuery(id+"F0.wireOp",EDGE,"E3256"),sQuery(id+"F0.wireOp",EDGE,"E3257"),sQuery(id+"F0.wireOp",EDGE,"E3258"),sQuery(id+"F0.wireOp",EDGE,"E3259"),sQuery(id+"F0.wireOp",EDGE,"E3260"),sQuery(id+"F0.wireOp",EDGE,"E3261"),sQuery(id+"F0.wireOp",EDGE,"E3262"),sQuery(id+"F0.wireOp",EDGE,"E3263"),sQuery(id+"F0.wireOp",EDGE,"E3264"),sQuery(id+"F0.wireOp",EDGE,"E3265"),sQuery(id+"F0.wireOp",EDGE,"E3266"),sQuery(id+"F0.wireOp",EDGE,"E3267"),sQuery(id+"F0.wireOp",EDGE,"E3268"),sQuery(id+"F0.wireOp",EDGE,"E3269"),sQuery(id+"F0.wireOp",EDGE,"E3270"),sQuery(id+"F0.wireOp",EDGE,"E3271"),sQuery(id+"F0.wireOp",EDGE,"E3272"),sQuery(id+"F0.wireOp",EDGE,"E3273"),sQuery(id+"F0.wireOp",EDGE,"E3274"),sQuery(id+"F0.wireOp",EDGE,"E3275"),sQuery(id+"F0.wireOp",EDGE,"E3276"),sQuery(id+"F0.wireOp",EDGE,"E3277"),sQuery(id+"F0.wireOp",EDGE,"E3278"),sQuery(id+"F0.wireOp",EDGE,"E3279"),sQuery(id+"F0.wireOp",EDGE,"E3280"),sQuery(id+"F0.wireOp",EDGE,"E3281"),sQuery(id+"F0.wireOp",EDGE,"E3282"),sQuery(id+"F0.wireOp",EDGE,"E3283"),sQuery(id+"F0.wireOp",EDGE,"E3284"),sQuery(id+"F0.wireOp",EDGE,"E3285"),sQuery(id+"F0.wireOp",EDGE,"E3286"),sQuery(id+"F0.wireOp",EDGE,"E3287"),sQuery(id+"F0.wireOp",EDGE,"E3288"),sQuery(id+"F0.wireOp",EDGE,"E3289"),sQuery(id+"F0.wireOp",EDGE,"E3290"),sQuery(id+"F0.wireOp",EDGE,"E3291"),sQuery(id+"F0.wireOp",EDGE,"E3292"),sQuery(id+"F0.wireOp",EDGE,"E3293"),sQuery(id+"F0.wireOp",EDGE,"E3294"),sQuery(id+"F0.wireOp",EDGE,"E3295"),sQuery(id+"F0.wireOp",EDGE,"E3296"),sQuery(id+"F0.wireOp",EDGE,"E3297"),sQuery(id+"F0.wireOp",EDGE,"E3298"),sQuery(id+"F0.wireOp",EDGE,"E3299"),sQuery(id+"F0.wireOp",EDGE,"E3300"),sQuery(id+"F0.wireOp",EDGE,"E3301"),sQuery(id+"F0.wireOp",EDGE,"E3302"),sQuery(id+"F0.wireOp",EDGE,"E3303"),sQuery(id+"F0.wireOp",EDGE,"E3304"),sQuery(id+"F0.wireOp",EDGE,"E3305"),sQuery(id+"F0.wireOp",EDGE,"E3306"),sQuery(id+"F0.wireOp",EDGE,"E3307"),sQuery(id+"F0.wireOp",EDGE,"E3308"),sQuery(id+"F0.wireOp",EDGE,"E3309"),sQuery(id+"F0.wireOp",EDGE,"E3310"),sQuery(id+"F0.wireOp",EDGE,"E3311"),sQuery(id+"F0.wireOp",EDGE,"E3312"),sQuery(id+"F0.wireOp",EDGE,"E3313"),sQuery(id+"F0.wireOp",EDGE,"E3314"),sQuery(id+"F0.wireOp",EDGE,"E3315"),sQuery(id+"F0.wireOp",EDGE,"E3316"),sQuery(id+"F0.wireOp",EDGE,"E3317"),sQuery(id+"F0.wireOp",EDGE,"E3318"),sQuery(id+"F0.wireOp",EDGE,"E3319"),sQuery(id+"F0.wireOp",EDGE,"E3320"),sQuery(id+"F0.wireOp",EDGE,"E3321"),sQuery(id+"F0.wireOp",EDGE,"E3322"),sQuery(id+"F0.wireOp",EDGE,"E3323"),sQuery(id+"F0.wireOp",EDGE,"E3324"),sQuery(id+"F0.wireOp",EDGE,"E3325"),sQuery(id+"F0.wireOp",EDGE,"E3326"),sQuery(id+"F0.wireOp",EDGE,"E3327"),sQuery(id+"F0.wireOp",EDGE,"E3328"),sQuery(id+"F0.wireOp",EDGE,"E3329"),sQuery(id+"F0.wireOp",EDGE,"E3330"),sQuery(id+"F0.wireOp",EDGE,"E3331"),sQuery(id+"F0.wireOp",EDGE,"E3332"),sQuery(id+"F0.wireOp",EDGE,"E3333"),sQuery(id+"F0.wireOp",EDGE,"E3334"),sQuery(id+"F0.wireOp",EDGE,"E3335"),sQuery(id+"F0.wireOp",EDGE,"E3336"),sQuery(id+"F0.wireOp",EDGE,"E3337"),sQuery(id+"F0.wireOp",EDGE,"E3338"),sQuery(id+"F0.wireOp",EDGE,"E3339"),sQuery(id+"F0.wireOp",EDGE,"E3340"),sQuery(id+"F0.wireOp",EDGE,"E3341"),sQuery(id+"F0.wireOp",EDGE,"E3342"),sQuery(id+"F0.wireOp",EDGE,"E3343"),sQuery(id+"F0.wireOp",EDGE,"E3344"),sQuery(id+"F0.wireOp",EDGE,"E3345"),sQuery(id+"F0.wireOp",EDGE,"E3346"),sQuery(id+"F0.wireOp",EDGE,"E3347"),sQuery(id+"F0.wireOp",EDGE,"E3348"),sQuery(id+"F0.wireOp",EDGE,"E3349"),sQuery(id+"F0.wireOp",EDGE,"E3350"),sQuery(id+"F0.wireOp",EDGE,"E3351"),sQuery(id+"F0.wireOp",EDGE,"E3352"),sQuery(id+"F0.wireOp",EDGE,"E3353"),sQuery(id+"F0.wireOp",EDGE,"E3354"),sQuery(id+"F0.wireOp",EDGE,"E3355"),sQuery(id+"F0.wireOp",EDGE,"E3356"),sQuery(id+"F0.wireOp",EDGE,"E3357"),sQuery(id+"F0.wireOp",EDGE,"E3358"),sQuery(id+"F0.wireOp",EDGE,"E3359"),sQuery(id+"F0.wireOp",EDGE,"E3360"),sQuery(id+"F0.wireOp",EDGE,"E3361"),sQuery(id+"F0.wireOp",EDGE,"E3362"),sQuery(id+"F0.wireOp",EDGE,"E3363"),sQuery(id+"F0.wireOp",EDGE,"E3364"),sQuery(id+"F0.wireOp",EDGE,"E3365"),sQuery(id+"F0.wireOp",EDGE,"E3366"),sQuery(id+"F0.wireOp",EDGE,"E3367"),sQuery(id+"F0.wireOp",EDGE,"E3368"),sQuery(id+"F0.wireOp",EDGE,"E3369"),sQuery(id+"F0.wireOp",EDGE,"E3370"),sQuery(id+"F0.wireOp",EDGE,"E3371"),sQuery(id+"F0.wireOp",EDGE,"E3372"),sQuery(id+"F0.wireOp",EDGE,"E3373"),sQuery(id+"F0.wireOp",EDGE,"E3374"),sQuery(id+"F0.wireOp",EDGE,"E3375"),sQuery(id+"F0.wireOp",EDGE,"E3376"),sQuery(id+"F0.wireOp",EDGE,"E3377"),sQuery(id+"F0.wireOp",EDGE,"E3378"),sQuery(id+"F0.wireOp",EDGE,"E3379"),sQuery(id+"F0.wireOp",EDGE,"E3380"),sQuery(id+"F0.wireOp",EDGE,"E3381"),sQuery(id+"F0.wireOp",EDGE,"E3382"),sQuery(id+"F0.wireOp",EDGE,"E3383"),sQuery(id+"F0.wireOp",EDGE,"E3384"),sQuery(id+"F0.wireOp",EDGE,"E3385"),sQuery(id+"F0.wireOp",EDGE,"E3386"),sQuery(id+"F0.wireOp",EDGE,"E3387"),sQuery(id+"F0.wireOp",EDGE,"E3388"),sQuery(id+"F0.wireOp",EDGE,"E3389"),sQuery(id+"F0.wireOp",EDGE,"E3390"),sQuery(id+"F0.wireOp",EDGE,"E3391"),sQuery(id+"F0.wireOp",EDGE,"E3392"),sQuery(id+"F0.wireOp",EDGE,"E3393"),sQuery(id+"F0.wireOp",EDGE,"E3394"),sQuery(id+"F0.wireOp",EDGE,"E3395"),sQuery(id+"F0.wireOp",EDGE,"E3396"),sQuery(id+"F0.wireOp",EDGE,"E3397"),sQuery(id+"F0.wireOp",EDGE,"E3398"),sQuery(id+"F0.wireOp",EDGE,"E3399"),sQuery(id+"F0.wireOp",EDGE,"E3400"),sQuery(id+"F0.wireOp",EDGE,"E3401"),sQuery(id+"F0.wireOp",EDGE,"E3402"),sQuery(id+"F0.wireOp",EDGE,"E3403"),sQuery(id+"F0.wireOp",EDGE,"E3404"),sQuery(id+"F0.wireOp",EDGE,"E3405"),sQuery(id+"F0.wireOp",EDGE,"E3406"),sQuery(id+"F0.wireOp",EDGE,"E3407"),sQuery(id+"F0.wireOp",EDGE,"E3408"),sQuery(id+"F0.wireOp",EDGE,"E3409"),sQuery(id+"F0.wireOp",EDGE,"E3410"),sQuery(id+"F0.wireOp",EDGE,"E3411"),sQuery(id+"F0.wireOp",EDGE,"E3412"),sQuery(id+"F0.wireOp",EDGE,"E3413"),sQuery(id+"F0.wireOp",EDGE,"E3414"),sQuery(id+"F0.wireOp",EDGE,"E3415"),sQuery(id+"F0.wireOp",EDGE,"E3416"),sQuery(id+"F0.wireOp",EDGE,"E3417"),sQuery(id+"F0.wireOp",EDGE,"E3418"),sQuery(id+"F0.wireOp",EDGE,"E3419"),sQuery(id+"F0.wireOp",EDGE,"E3420"),sQuery(id+"F0.wireOp",EDGE,"E3421"),sQuery(id+"F0.wireOp",EDGE,"E3422"),sQuery(id+"F0.wireOp",EDGE,"E3423"),sQuery(id+"F0.wireOp",EDGE,"E3424"),sQuery(id+"F0.wireOp",EDGE,"E3425"),sQuery(id+"F0.wireOp",EDGE,"E3426"),sQuery(id+"F0.wireOp",EDGE,"E3427"),sQuery(id+"F0.wireOp",EDGE,"E3428"),sQuery(id+"F0.wireOp",EDGE,"E3429"),sQuery(id+"F0.wireOp",EDGE,"E3430"),sQuery(id+"F0.wireOp",EDGE,"E3431"),sQuery(id+"F0.wireOp",EDGE,"E3432"),sQuery(id+"F0.wireOp",EDGE,"E3433"),sQuery(id+"F0.wireOp",EDGE,"E3434"),sQuery(id+"F0.wireOp",EDGE,"E3435"),sQuery(id+"F0.wireOp",EDGE,"E3436"),sQuery(id+"F0.wireOp",EDGE,"E3437"),sQuery(id+"F0.wireOp",EDGE,"E3438"),sQuery(id+"F0.wireOp",EDGE,"E3439"),sQuery(id+"F0.wireOp",EDGE,"E3440"),sQuery(id+"F0.wireOp",EDGE,"E3441"),sQuery(id+"F0.wireOp",EDGE,"E3442"),sQuery(id+"F0.wireOp",EDGE,"E3443"),sQuery(id+"F0.wireOp",EDGE,"E3444"),sQuery(id+"F0.wireOp",EDGE,"E3445"),sQuery(id+"F0.wireOp",EDGE,"E3446"),sQuery(id+"F0.wireOp",EDGE,"E3447"),sQuery(id+"F0.wireOp",EDGE,"E3448"),sQuery(id+"F0.wireOp",EDGE,"E3449"),sQuery(id+"F0.wireOp",EDGE,"E3450"),sQuery(id+"F0.wireOp",EDGE,"E3451"),sQuery(id+"F0.wireOp",EDGE,"E3452"),sQuery(id+"F0.wireOp",EDGE,"E3453"),sQuery(id+"F0.wireOp",EDGE,"E3454"),sQuery(id+"F0.wireOp",EDGE,"E3455"),sQuery(id+"F0.wireOp",EDGE,"E3456"),sQuery(id+"F0.wireOp",EDGE,"E3457"),sQuery(id+"F0.wireOp",EDGE,"E3458"),sQuery(id+"F0.wireOp",EDGE,"E3459"),sQuery(id+"F0.wireOp",EDGE,"E3460"),sQuery(id+"F0.wireOp",EDGE,"E3461"),sQuery(id+"F0.wireOp",EDGE,"E3462"),sQuery(id+"F0.wireOp",EDGE,"E3463"),sQuery(id+"F0.wireOp",EDGE,"E3464"),sQuery(id+"F0.wireOp",EDGE,"E3465"),sQuery(id+"F0.wireOp",EDGE,"E3466"),sQuery(id+"F0.wireOp",EDGE,"E3467"),sQuery(id+"F0.wireOp",EDGE,"E3468"),sQuery(id+"F0.wireOp",EDGE,"E3469"),sQuery(id+"F0.wireOp",EDGE,"E3470"),sQuery(id+"F0.wireOp",EDGE,"E3471"),sQuery(id+"F0.wireOp",EDGE,"E3472"),sQuery(id+"F0.wireOp",EDGE,"E3473"),sQuery(id+"F0.wireOp",EDGE,"E3474"),sQuery(id+"F0.wireOp",EDGE,"E3475"),sQuery(id+"F0.wireOp",EDGE,"E3476"),sQuery(id+"F0.wireOp",EDGE,"E3477"),sQuery(id+"F0.wireOp",EDGE,"E3478"),sQuery(id+"F0.wireOp",EDGE,"E3479"),sQuery(id+"F0.wireOp",EDGE,"E3480"),sQuery(id+"F0.wireOp",EDGE,"E3481"),sQuery(id+"F0.wireOp",EDGE,"E3482"),sQuery(id+"F0.wireOp",EDGE,"E3483"),sQuery(id+"F0.wireOp",EDGE,"E3484"),sQuery(id+"F0.wireOp",EDGE,"E3485"),sQuery(id+"F0.wireOp",EDGE,"E3486"),sQuery(id+"F0.wireOp",EDGE,"E3487"),sQuery(id+"F0.wireOp",EDGE,"E3488"),sQuery(id+"F0.wireOp",EDGE,"E3489"),sQuery(id+"F0.wireOp",EDGE,"E3490"),sQuery(id+"F0.wireOp",EDGE,"E3491"),sQuery(id+"F0.wireOp",EDGE,"E3492"),sQuery(id+"F0.wireOp",EDGE,"E3493"),sQuery(id+"F0.wireOp",EDGE,"E3494"),sQuery(id+"F0.wireOp",EDGE,"E3495"),sQuery(id+"F0.wireOp",EDGE,"E3496"),sQuery(id+"F0.wireOp",EDGE,"E3497"),sQuery(id+"F0.wireOp",EDGE,"E3498"),sQuery(id+"F0.wireOp",EDGE,"E3499"),sQuery(id+"F0.wireOp",EDGE,"E3500"),sQuery(id+"F0.wireOp",EDGE,"E3501"),sQuery(id+"F0.wireOp",EDGE,"E3502"),sQuery(id+"F0.wireOp",EDGE,"E3503"),sQuery(id+"F0.wireOp",EDGE,"E3504"),sQuery(id+"F0.wireOp",EDGE,"E3505"),sQuery(id+"F0.wireOp",EDGE,"E3506"),sQuery(id+"F0.wireOp",EDGE,"E3507"),sQuery(id+"F0.wireOp",EDGE,"E3508"),sQuery(id+"F0.wireOp",EDGE,"E3509"),sQuery(id+"F0.wireOp",EDGE,"E3510"),sQuery(id+"F0.wireOp",EDGE,"E3511"),sQuery(id+"F0.wireOp",EDGE,"E3512"),sQuery(id+"F0.wireOp",EDGE,"E3513"),sQuery(id+"F0.wireOp",EDGE,"E3514"),sQuery(id+"F0.wireOp",EDGE,"E3515"),sQuery(id+"F0.wireOp",EDGE,"E3516"),sQuery(id+"F0.wireOp",EDGE,"E3517"),sQuery(id+"F0.wireOp",EDGE,"E3518"),sQuery(id+"F0.wireOp",EDGE,"E3519"),sQuery(id+"F0.wireOp",EDGE,"E3520"),sQuery(id+"F0.wireOp",EDGE,"E3521"),sQuery(id+"F0.wireOp",EDGE,"E3522"),sQuery(id+"F0.wireOp",EDGE,"E3523"),sQuery(id+"F0.wireOp",EDGE,"E3524"),sQuery(id+"F0.wireOp",EDGE,"E3525"),sQuery(id+"F0.wireOp",EDGE,"E3526"),sQuery(id+"F0.wireOp",EDGE,"E3527"),sQuery(id+"F0.wireOp",EDGE,"E3528"),sQuery(id+"F0.wireOp",EDGE,"E3529"),sQuery(id+"F0.wireOp",EDGE,"E3530"),sQuery(id+"F0.wireOp",EDGE,"E3531"),sQuery(id+"F0.wireOp",EDGE,"E3532"),sQuery(id+"F0.wireOp",EDGE,"E3533"),sQuery(id+"F0.wireOp",EDGE,"E3534"),sQuery(id+"F0.wireOp",EDGE,"E3535"),sQuery(id+"F0.wireOp",EDGE,"E3536"),sQuery(id+"F0.wireOp",EDGE,"E3537"),sQuery(id+"F0.wireOp",EDGE,"E3538"),sQuery(id+"F0.wireOp",EDGE,"E3539"),sQuery(id+"F0.wireOp",EDGE,"E3540"),sQuery(id+"F0.wireOp",EDGE,"E3541"),sQuery(id+"F0.wireOp",EDGE,"E3542"),sQuery(id+"F0.wireOp",EDGE,"E3543"),sQuery(id+"F0.wireOp",EDGE,"E3544"),sQuery(id+"F0.wireOp",EDGE,"E3545"),sQuery(id+"F0.wireOp",EDGE,"E3546"),sQuery(id+"F0.wireOp",EDGE,"E3547"),sQuery(id+"F0.wireOp",EDGE,"E3548"),sQuery(id+"F0.wireOp",EDGE,"E3549"),sQuery(id+"F0.wireOp",EDGE,"E3550"),sQuery(id+"F0.wireOp",EDGE,"E3551"),sQuery(id+"F0.wireOp",EDGE,"E3552"),sQuery(id+"F0.wireOp",EDGE,"E3553"),sQuery(id+"F0.wireOp",EDGE,"E3554"),sQuery(id+"F0.wireOp",EDGE,"E3555"),sQuery(id+"F0.wireOp",EDGE,"E3556"),sQuery(id+"F0.wireOp",EDGE,"E3557"),sQuery(id+"F0.wireOp",EDGE,"E3558"),sQuery(id+"F0.wireOp",EDGE,"E3559"),sQuery(id+"F0.wireOp",EDGE,"E3560"),sQuery(id+"F0.wireOp",EDGE,"E3561"),sQuery(id+"F0.wireOp",EDGE,"E3562"),sQuery(id+"F0.wireOp",EDGE,"E3563"),sQuery(id+"F0.wireOp",EDGE,"E3564"),sQuery(id+"F0.wireOp",EDGE,"E3565"),sQuery(id+"F0.wireOp",EDGE,"E3566"),sQuery(id+"F0.wireOp",EDGE,"E3567"),sQuery(id+"F0.wireOp",EDGE,"E3568"),sQuery(id+"F0.wireOp",EDGE,"E3569"),sQuery(id+"F0.wireOp",EDGE,"E3570"),sQuery(id+"F0.wireOp",EDGE,"E3571"),sQuery(id+"F0.wireOp",EDGE,"E3572"),sQuery(id+"F0.wireOp",EDGE,"E3573"),sQuery(id+"F0.wireOp",EDGE,"E3574"),sQuery(id+"F0.wireOp",EDGE,"E3575"),sQuery(id+"F0.wireOp",EDGE,"E3576"),sQuery(id+"F0.wireOp",EDGE,"E3577"),sQuery(id+"F0.wireOp",EDGE,"E3578"),sQuery(id+"F0.wireOp",EDGE,"E3579"),sQuery(id+"F0.wireOp",EDGE,"E3580"),sQuery(id+"F0.wireOp",EDGE,"E3581"),sQuery(id+"F0.wireOp",EDGE,"E3582"),sQuery(id+"F0.wireOp",EDGE,"E3583"),sQuery(id+"F0.wireOp",EDGE,"E3584"),sQuery(id+"F0.wireOp",EDGE,"E3585"),sQuery(id+"F0.wireOp",EDGE,"E3586"),sQuery(id+"F0.wireOp",EDGE,"E3587"),sQuery(id+"F0.wireOp",EDGE,"E3588"),sQuery(id+"F0.wireOp",EDGE,"E3589"),sQuery(id+"F0.wireOp",EDGE,"E3590"),sQuery(id+"F0.wireOp",EDGE,"E3591"),sQuery(id+"F0.wireOp",EDGE,"E3592"),sQuery(id+"F0.wireOp",EDGE,"E3593"),sQuery(id+"F0.wireOp",EDGE,"E3594"),sQuery(id+"F0.wireOp",EDGE,"E3595"),sQuery(id+"F0.wireOp",EDGE,"E3596"),sQuery(id+"F0.wireOp",EDGE,"E3597"),sQuery(id+"F0.wireOp",EDGE,"E3598"),sQuery(id+"F0.wireOp",EDGE,"E3599"),sQuery(id+"F0.wireOp",EDGE,"E3600"),sQuery(id+"F0.wireOp",EDGE,"E3601"),sQuery(id+"F0.wireOp",EDGE,"E3602"),sQuery(id+"F0.wireOp",EDGE,"E3603"),sQuery(id+"F0.wireOp",EDGE,"E3604"),sQuery(id+"F0.wireOp",EDGE,"E3605"),sQuery(id+"F0.wireOp",EDGE,"E3606"),sQuery(id+"F0.wireOp",EDGE,"E3607"),sQuery(id+"F0.wireOp",EDGE,"E3608"),sQuery(id+"F0.wireOp",EDGE,"E3609"),sQuery(id+"F0.wireOp",EDGE,"E3610"),sQuery(id+"F0.wireOp",EDGE,"E3611"),sQuery(id+"F0.wireOp",EDGE,"E3612"),sQuery(id+"F0.wireOp",EDGE,"E3613"),sQuery(id+"F0.wireOp",EDGE,"E3614"),sQuery(id+"F0.wireOp",EDGE,"E3615"),sQuery(id+"F0.wireOp",EDGE,"E3616"),sQuery(id+"F0.wireOp",EDGE,"E3617"),sQuery(id+"F0.wireOp",EDGE,"E3618"),sQuery(id+"F0.wireOp",EDGE,"E3619"),sQuery(id+"F0.wireOp",EDGE,"E3620"),sQuery(id+"F0.wireOp",EDGE,"E3621"),sQuery(id+"F0.wireOp",EDGE,"E3622"),sQuery(id+"F0.wireOp",EDGE,"E3623"),sQuery(id+"F0.wireOp",EDGE,"E3624"),sQuery(id+"F0.wireOp",EDGE,"E3625"),sQuery(id+"F0.wireOp",EDGE,"E3626"),sQuery(id+"F0.wireOp",EDGE,"E3627"),sQuery(id+"F0.wireOp",EDGE,"E3628"),sQuery(id+"F0.wireOp",EDGE,"E3629"),sQuery(id+"F0.wireOp",EDGE,"E3630"),sQuery(id+"F0.wireOp",EDGE,"E3631"),sQuery(id+"F0.wireOp",EDGE,"E3632"),sQuery(id+"F0.wireOp",EDGE,"E3633"),sQuery(id+"F0.wireOp",EDGE,"E3634"),sQuery(id+"F0.wireOp",EDGE,"E3635"),sQuery(id+"F0.wireOp",EDGE,"E3636"),sQuery(id+"F0.wireOp",EDGE,"E3637"),sQuery(id+"F0.wireOp",EDGE,"E3638"),sQuery(id+"F0.wireOp",EDGE,"E3639"),sQuery(id+"F0.wireOp",EDGE,"E3640"),sQuery(id+"F0.wireOp",EDGE,"E3641"),sQuery(id+"F0.wireOp",EDGE,"E3642"),sQuery(id+"F0.wireOp",EDGE,"E3643"),sQuery(id+"F0.wireOp",EDGE,"E3644"),sQuery(id+"F0.wireOp",EDGE,"E3645"),sQuery(id+"F0.wireOp",EDGE,"E3646"),sQuery(id+"F0.wireOp",EDGE,"E3647"),sQuery(id+"F0.wireOp",EDGE,"E3648"),sQuery(id+"F0.wireOp",EDGE,"E3649"),sQuery(id+"F0.wireOp",EDGE,"E3650"),sQuery(id+"F0.wireOp",EDGE,"E3651"),sQuery(id+"F0.wireOp",EDGE,"E3652"),sQuery(id+"F0.wireOp",EDGE,"E3653"),sQuery(id+"F0.wireOp",EDGE,"E3654"),sQuery(id+"F0.wireOp",EDGE,"E3655"),sQuery(id+"F0.wireOp",EDGE,"E3656"),sQuery(id+"F0.wireOp",EDGE,"E3657"),sQuery(id+"F0.wireOp",EDGE,"E3658"),sQuery(id+"F0.wireOp",EDGE,"E3659"),sQuery(id+"F0.wireOp",EDGE,"E3660"),sQuery(id+"F0.wireOp",EDGE,"E3661"),sQuery(id+"F0.wireOp",EDGE,"E3662"),sQuery(id+"F0.wireOp",EDGE,"E3663"),sQuery(id+"F0.wireOp",EDGE,"E3664"),sQuery(id+"F0.wireOp",EDGE,"E3665"),sQuery(id+"F0.wireOp",EDGE,"E3666"),sQuery(id+"F0.wireOp",EDGE,"E3667"),sQuery(id+"F0.wireOp",EDGE,"E3668"),sQuery(id+"F0.wireOp",EDGE,"E3669"),sQuery(id+"F0.wireOp",EDGE,"E3670"),sQuery(id+"F0.wireOp",EDGE,"E3671"),sQuery(id+"F0.wireOp",EDGE,"E3672"),sQuery(id+"F0.wireOp",EDGE,"E3673"),sQuery(id+"F0.wireOp",EDGE,"E3674"),sQuery(id+"F0.wireOp",EDGE,"E3675"),sQuery(id+"F0.wireOp",EDGE,"E3676"),sQuery(id+"F0.wireOp",EDGE,"E3677"),sQuery(id+"F0.wireOp",EDGE,"E3678"),sQuery(id+"F0.wireOp",EDGE,"E3679"),sQuery(id+"F0.wireOp",EDGE,"E3680"),sQuery(id+"F0.wireOp",EDGE,"E3681"),sQuery(id+"F0.wireOp",EDGE,"E3682"),sQuery(id+"F0.wireOp",EDGE,"E3683"),sQuery(id+"F0.wireOp",EDGE,"E3684"),sQuery(id+"F0.wireOp",EDGE,"E3685"),sQuery(id+"F0.wireOp",EDGE,"E3686"),sQuery(id+"F0.wireOp",EDGE,"E3687"),sQuery(id+"F0.wireOp",EDGE,"E3688"),sQuery(id+"F0.wireOp",EDGE,"E3689"),sQuery(id+"F0.wireOp",EDGE,"E3690"),sQuery(id+"F0.wireOp",EDGE,"E3691"),sQuery(id+"F0.wireOp",EDGE,"E3692"),sQuery(id+"F0.wireOp",EDGE,"E3693"),sQuery(id+"F0.wireOp",EDGE,"E3694"),sQuery(id+"F0.wireOp",EDGE,"E3695"),sQuery(id+"F0.wireOp",EDGE,"E3696"),sQuery(id+"F0.wireOp",EDGE,"E3697"),sQuery(id+"F0.wireOp",EDGE,"E3698"),sQuery(id+"F0.wireOp",EDGE,"E3699"),sQuery(id+"F0.wireOp",EDGE,"E3700"),sQuery(id+"F0.wireOp",EDGE,"E3701"),sQuery(id+"F0.wireOp",EDGE,"E3702"),sQuery(id+"F0.wireOp",EDGE,"E3703"),sQuery(id+"F0.wireOp",EDGE,"E3704"),sQuery(id+"F0.wireOp",EDGE,"E3705"),sQuery(id+"F0.wireOp",EDGE,"E3706"),sQuery(id+"F0.wireOp",EDGE,"E3707"),sQuery(id+"F0.wireOp",EDGE,"E3708"),sQuery(id+"F0.wireOp",EDGE,"E3709"),sQuery(id+"F0.wireOp",EDGE,"E3710"),sQuery(id+"F0.wireOp",EDGE,"E3711"),sQuery(id+"F0.wireOp",EDGE,"E3712"),sQuery(id+"F0.wireOp",EDGE,"E3713"),sQuery(id+"F0.wireOp",EDGE,"E3714"),sQuery(id+"F0.wireOp",EDGE,"E3715"),sQuery(id+"F0.wireOp",EDGE,"E3716"),sQuery(id+"F0.wireOp",EDGE,"E3717"),sQuery(id+"F0.wireOp",EDGE,"E3718"),sQuery(id+"F0.wireOp",EDGE,"E3719"),sQuery(id+"F0.wireOp",EDGE,"E3720"),sQuery(id+"F0.wireOp",EDGE,"E3721"),sQuery(id+"F0.wireOp",EDGE,"E3722"),sQuery(id+"F0.wireOp",EDGE,"E3723"),sQuery(id+"F0.wireOp",EDGE,"E3724"),sQuery(id+"F0.wireOp",EDGE,"E3725"),sQuery(id+"F0.wireOp",EDGE,"E3726"),sQuery(id+"F0.wireOp",EDGE,"E3727"),sQuery(id+"F0.wireOp",EDGE,"E3728"),sQuery(id+"F0.wireOp",EDGE,"E3729"),sQuery(id+"F0.wireOp",EDGE,"E3730"),sQuery(id+"F0.wireOp",EDGE,"E3731"),sQuery(id+"F0.wireOp",EDGE,"E3732"),sQuery(id+"F0.wireOp",EDGE,"E3733"),sQuery(id+"F0.wireOp",EDGE,"E3734"),sQuery(id+"F0.wireOp",EDGE,"E3735"),sQuery(id+"F0.wireOp",EDGE,"E3736"),sQuery(id+"F0.wireOp",EDGE,"E3737"),sQuery(id+"F0.wireOp",EDGE,"E3738"),sQuery(id+"F0.wireOp",EDGE,"E3739"),sQuery(id+"F0.wireOp",EDGE,"E3740"),sQuery(id+"F0.wireOp",EDGE,"E3741"),sQuery(id+"F0.wireOp",EDGE,"E3742"),sQuery(id+"F0.wireOp",EDGE,"E3743"),sQuery(id+"F0.wireOp",EDGE,"E3744"),sQuery(id+"F0.wireOp",EDGE,"E3745"),sQuery(id+"F0.wireOp",EDGE,"E3746"),sQuery(id+"F0.wireOp",EDGE,"E3747"),sQuery(id+"F0.wireOp",EDGE,"E3748"),sQuery(id+"F0.wireOp",EDGE,"E3749"),sQuery(id+"F0.wireOp",EDGE,"E3750"),sQuery(id+"F0.wireOp",EDGE,"E3751"),sQuery(id+"F0.wireOp",EDGE,"E3752"),sQuery(id+"F0.wireOp",EDGE,"E3753"),sQuery(id+"F0.wireOp",EDGE,"E3754"),sQuery(id+"F0.wireOp",EDGE,"E3755"),sQuery(id+"F0.wireOp",EDGE,"E3756"),sQuery(id+"F0.wireOp",EDGE,"E3757"),sQuery(id+"F0.wireOp",EDGE,"E3758"),sQuery(id+"F0.wireOp",EDGE,"E3759"),sQuery(id+"F0.wireOp",EDGE,"E3760"),sQuery(id+"F0.wireOp",EDGE,"E3761"),sQuery(id+"F0.wireOp",EDGE,"E3762"),sQuery(id+"F0.wireOp",EDGE,"E3763"),sQuery(id+"F0.wireOp",EDGE,"E3764"),sQuery(id+"F0.wireOp",EDGE,"E3765"),sQuery(id+"F0.wireOp",EDGE,"E3766"),sQuery(id+"F0.wireOp",EDGE,"E3767"),sQuery(id+"F0.wireOp",EDGE,"E3768"),sQuery(id+"F0.wireOp",EDGE,"E3769"),sQuery(id+"F0.wireOp",EDGE,"E3770"),sQuery(id+"F0.wireOp",EDGE,"E3771"),sQuery(id+"F0.wireOp",EDGE,"E3772"),sQuery(id+"F0.wireOp",EDGE,"E3773"),sQuery(id+"F0.wireOp",EDGE,"E3774"),sQuery(id+"F0.wireOp",EDGE,"E3775"),sQuery(id+"F0.wireOp",EDGE,"E3776"),sQuery(id+"F0.wireOp",EDGE,"E3777"),sQuery(id+"F0.wireOp",EDGE,"E3778"),sQuery(id+"F0.wireOp",EDGE,"E3779"),sQuery(id+"F0.wireOp",EDGE,"E3780"),sQuery(id+"F0.wireOp",EDGE,"E3781"),sQuery(id+"F0.wireOp",EDGE,"E3782"),sQuery(id+"F0.wireOp",EDGE,"E3783"),sQuery(id+"F0.wireOp",EDGE,"E3784"),sQuery(id+"F0.wireOp",EDGE,"E3785"),sQuery(id+"F0.wireOp",EDGE,"E3786"),sQuery(id+"F0.wireOp",EDGE,"E3787"),sQuery(id+"F0.wireOp",EDGE,"E3788"),sQuery(id+"F0.wireOp",EDGE,"E3789"),sQuery(id+"F0.wireOp",EDGE,"E3790"),sQuery(id+"F0.wireOp",EDGE,"E3791"),sQuery(id+"F0.wireOp",EDGE,"E3792"),sQuery(id+"F0.wireOp",EDGE,"E3793"),sQuery(id+"F0.wireOp",EDGE,"E3794"),sQuery(id+"F0.wireOp",EDGE,"E3795"),sQuery(id+"F0.wireOp",EDGE,"E3796"),sQuery(id+"F0.wireOp",EDGE,"E3797"),sQuery(id+"F0.wireOp",EDGE,"E3798"),sQuery(id+"F0.wireOp",EDGE,"E3799"),sQuery(id+"F0.wireOp",EDGE,"E3800"),sQuery(id+"F0.wireOp",EDGE,"E3801"),sQuery(id+"F0.wireOp",EDGE,"E3802"),sQuery(id+"F0.wireOp",EDGE,"E3803"),sQuery(id+"F0.wireOp",EDGE,"E3804"),sQuery(id+"F0.wireOp",EDGE,"E3805"),sQuery(id+"F0.wireOp",EDGE,"E3806"),sQuery(id+"F0.wireOp",EDGE,"E3807"),sQuery(id+"F0.wireOp",EDGE,"E3808"),sQuery(id+"F0.wireOp",EDGE,"E3809"),sQuery(id+"F0.wireOp",EDGE,"E3810"),sQuery(id+"F0.wireOp",EDGE,"E3811"),sQuery(id+"F0.wireOp",EDGE,"E3812"),sQuery(id+"F0.wireOp",EDGE,"E3813"),sQuery(id+"F0.wireOp",EDGE,"E3814"),sQuery(id+"F0.wireOp",EDGE,"E3815"),sQuery(id+"F0.wireOp",EDGE,"E3816"),sQuery(id+"F0.wireOp",EDGE,"E3817"),sQuery(id+"F0.wireOp",EDGE,"E3818"),sQuery(id+"F0.wireOp",EDGE,"E3819"),sQuery(id+"F0.wireOp",EDGE,"E3820"),sQuery(id+"F0.wireOp",EDGE,"E3821"),sQuery(id+"F0.wireOp",EDGE,"E3822"),sQuery(id+"F0.wireOp",EDGE,"E3823"),sQuery(id+"F0.wireOp",EDGE,"E3824"),sQuery(id+"F0.wireOp",EDGE,"E3825"),sQuery(id+"F0.wireOp",EDGE,"E3826"),sQuery(id+"F0.wireOp",EDGE,"E3827"),sQuery(id+"F0.wireOp",EDGE,"E3828"),sQuery(id+"F0.wireOp",EDGE,"E3829"),sQuery(id+"F0.wireOp",EDGE,"E3830"),sQuery(id+"F0.wireOp",EDGE,"E3831"),sQuery(id+"F0.wireOp",EDGE,"E3832"),sQuery(id+"F0.wireOp",EDGE,"E3833"),sQuery(id+"F0.wireOp",EDGE,"E3834"),sQuery(id+"F0.wireOp",EDGE,"E3835"),sQuery(id+"F0.wireOp",EDGE,"E3836"),sQuery(id+"F0.wireOp",EDGE,"E3837"),sQuery(id+"F0.wireOp",EDGE,"E3838"),sQuery(id+"F0.wireOp",EDGE,"E3839"),sQuery(id+"F0.wireOp",EDGE,"E3840"),sQuery(id+"F0.wireOp",EDGE,"E3841"),sQuery(id+"F0.wireOp",EDGE,"E3842"),sQuery(id+"F0.wireOp",EDGE,"E3843"),sQuery(id+"F0.wireOp",EDGE,"E3844"),sQuery(id+"F0.wireOp",EDGE,"E3845"),sQuery(id+"F0.wireOp",EDGE,"E3846"),sQuery(id+"F0.wireOp",EDGE,"E3847"),sQuery(id+"F0.wireOp",EDGE,"E3848"),sQuery(id+"F0.wireOp",EDGE,"E3849"),sQuery(id+"F0.wireOp",EDGE,"E3850"),sQuery(id+"F0.wireOp",EDGE,"E3851"),sQuery(id+"F0.wireOp",EDGE,"E3852"),sQuery(id+"F0.wireOp",EDGE,"E3853"),sQuery(id+"F0.wireOp",EDGE,"E3854"),sQuery(id+"F0.wireOp",EDGE,"E3855"),sQuery(id+"F0.wireOp",EDGE,"E3856"),sQuery(id+"F0.wireOp",EDGE,"E3857"),sQuery(id+"F0.wireOp",EDGE,"E3858"),sQuery(id+"F0.wireOp",EDGE,"E3859"),sQuery(id+"F0.wireOp",EDGE,"E3860"),sQuery(id+"F0.wireOp",EDGE,"E3861"),sQuery(id+"F0.wireOp",EDGE,"E3862"),sQuery(id+"F0.wireOp",EDGE,"E3863"),sQuery(id+"F0.wireOp",EDGE,"E3864"),sQuery(id+"F0.wireOp",EDGE,"E3865"),sQuery(id+"F0.wireOp",EDGE,"E3866"),sQuery(id+"F0.wireOp",EDGE,"E3867"),sQuery(id+"F0.wireOp",EDGE,"E3868"),sQuery(id+"F0.wireOp",EDGE,"E3869"),sQuery(id+"F0.wireOp",EDGE,"E3870"),sQuery(id+"F0.wireOp",EDGE,"E3871"),sQuery(id+"F0.wireOp",EDGE,"E3872"),sQuery(id+"F0.wireOp",EDGE,"E3873"),sQuery(id+"F0.wireOp",EDGE,"E3874"),sQuery(id+"F0.wireOp",EDGE,"E3875"),sQuery(id+"F0.wireOp",EDGE,"E3876"),sQuery(id+"F0.wireOp",EDGE,"E3877"),sQuery(id+"F0.wireOp",EDGE,"E3878"),sQuery(id+"F0.wireOp",EDGE,"E3879"),sQuery(id+"F0.wireOp",EDGE,"E3880"),sQuery(id+"F0.wireOp",EDGE,"E3881"),sQuery(id+"F0.wireOp",EDGE,"E3882"),sQuery(id+"F0.wireOp",EDGE,"E3883"),sQuery(id+"F0.wireOp",EDGE,"E3884"),sQuery(id+"F0.wireOp",EDGE,"E3885"),sQuery(id+"F0.wireOp",EDGE,"E3886"),sQuery(id+"F0.wireOp",EDGE,"E3887"),sQuery(id+"F0.wireOp",EDGE,"E3888"),sQuery(id+"F0.wireOp",EDGE,"E3889"),sQuery(id+"F0.wireOp",EDGE,"E3890"),sQuery(id+"F0.wireOp",EDGE,"E3891"),sQuery(id+"F0.wireOp",EDGE,"E3892"),sQuery(id+"F0.wireOp",EDGE,"E3893"),sQuery(id+"F0.wireOp",EDGE,"E3894"),sQuery(id+"F0.wireOp",EDGE,"E3895"),sQuery(id+"F0.wireOp",EDGE,"E3896"),sQuery(id+"F0.wireOp",EDGE,"E3897"),sQuery(id+"F0.wireOp",EDGE,"E3898"),sQuery(id+"F0.wireOp",EDGE,"E3899"),sQuery(id+"F0.wireOp",EDGE,"E3900"),sQuery(id+"F0.wireOp",EDGE,"E3901"),sQuery(id+"F0.wireOp",EDGE,"E3902"),sQuery(id+"F0.wireOp",EDGE,"E3903"),sQuery(id+"F0.wireOp",EDGE,"E3904"),sQuery(id+"F0.wireOp",EDGE,"E3905"),sQuery(id+"F0.wireOp",EDGE,"E3906"),sQuery(id+"F0.wireOp",EDGE,"E3907"),sQuery(id+"F0.wireOp",EDGE,"E3908"),sQuery(id+"F0.wireOp",EDGE,"E3909"),sQuery(id+"F0.wireOp",EDGE,"E3910"),sQuery(id+"F0.wireOp",EDGE,"E3911"),sQuery(id+"F0.wireOp",EDGE,"E3912"),sQuery(id+"F0.wireOp",EDGE,"E3913"),sQuery(id+"F0.wireOp",EDGE,"E3914"),sQuery(id+"F0.wireOp",EDGE,"E3915"),sQuery(id+"F0.wireOp",EDGE,"E3916"),sQuery(id+"F0.wireOp",EDGE,"E3917"),sQuery(id+"F0.wireOp",EDGE,"E3918"),sQuery(id+"F0.wireOp",EDGE,"E3919"),sQuery(id+"F0.wireOp",EDGE,"E3920"),sQuery(id+"F0.wireOp",EDGE,"E3921"),sQuery(id+"F0.wireOp",EDGE,"E3922"),sQuery(id+"F0.wireOp",EDGE,"E3923"),sQuery(id+"F0.wireOp",EDGE,"E3924"),sQuery(id+"F0.wireOp",EDGE,"E3925"),sQuery(id+"F0.wireOp",EDGE,"E3926"),sQuery(id+"F0.wireOp",EDGE,"E3927"),sQuery(id+"F0.wireOp",EDGE,"E3928"),sQuery(id+"F0.wireOp",EDGE,"E3929"),sQuery(id+"F0.wireOp",EDGE,"E3930"),sQuery(id+"F0.wireOp",EDGE,"E3931"),sQuery(id+"F0.wireOp",EDGE,"E3932"),sQuery(id+"F0.wireOp",EDGE,"E3933"),sQuery(id+"F0.wireOp",EDGE,"E3934"),sQuery(id+"F0.wireOp",EDGE,"E3935"),sQuery(id+"F0.wireOp",EDGE,"E3936"),sQuery(id+"F0.wireOp",EDGE,"E3937"),sQuery(id+"F0.wireOp",EDGE,"E3938"),sQuery(id+"F0.wireOp",EDGE,"E3939"),sQuery(id+"F0.wireOp",EDGE,"E3940"),sQuery(id+"F0.wireOp",EDGE,"E3941"),sQuery(id+"F0.wireOp",EDGE,"E3942"),sQuery(id+"F0.wireOp",EDGE,"E3943"),sQuery(id+"F0.wireOp",EDGE,"E3944"),sQuery(id+"F0.wireOp",EDGE,"E3945"),sQuery(id+"F0.wireOp",EDGE,"E3946"),sQuery(id+"F0.wireOp",EDGE,"E3947"),sQuery(id+"F0.wireOp",EDGE,"E3948"),sQuery(id+"F0.wireOp",EDGE,"E3949"),sQuery(id+"F0.wireOp",EDGE,"E3950"),sQuery(id+"F0.wireOp",EDGE,"E3951"),sQuery(id+"F0.wireOp",EDGE,"E3952"),sQuery(id+"F0.wireOp",EDGE,"E3953"),sQuery(id+"F0.wireOp",EDGE,"E3954"),sQuery(id+"F0.wireOp",EDGE,"E3955"),sQuery(id+"F0.wireOp",EDGE,"E3956"),sQuery(id+"F0.wireOp",EDGE,"E3957"),sQuery(id+"F0.wireOp",EDGE,"E3958"),sQuery(id+"F0.wireOp",EDGE,"E3959"),sQuery(id+"F0.wireOp",EDGE,"E3960"),sQuery(id+"F0.wireOp",EDGE,"E3961"),sQuery(id+"F0.wireOp",EDGE,"E3962"),sQuery(id+"F0.wireOp",EDGE,"E3963"),sQuery(id+"F0.wireOp",EDGE,"E3964"),sQuery(id+"F0.wireOp",EDGE,"E3965"),sQuery(id+"F0.wireOp",EDGE,"E3966"),sQuery(id+"F0.wireOp",EDGE,"E3967"),sQuery(id+"F0.wireOp",EDGE,"E3968"),sQuery(id+"F0.wireOp",EDGE,"E3969"),sQuery(id+"F0.wireOp",EDGE,"E3970"),sQuery(id+"F0.wireOp",EDGE,"E3971"),sQuery(id+"F0.wireOp",EDGE,"E3972"),sQuery(id+"F0.wireOp",EDGE,"E3973"),sQuery(id+"F0.wireOp",EDGE,"E3974"),sQuery(id+"F0.wireOp",EDGE,"E3975"),sQuery(id+"F0.wireOp",EDGE,"E3976"),sQuery(id+"F0.wireOp",EDGE,"E3977"),sQuery(id+"F0.wireOp",EDGE,"E3978"),sQuery(id+"F0.wireOp",EDGE,"E3979"),sQuery(id+"F0.wireOp",EDGE,"E3980"),sQuery(id+"F0.wireOp",EDGE,"E3981"),sQuery(id+"F0.wireOp",EDGE,"E3982"),sQuery(id+"F0.wireOp",EDGE,"E3983"),sQuery(id+"F0.wireOp",EDGE,"E3984"),sQuery(id+"F0.wireOp",EDGE,"E3985"),sQuery(id+"F0.wireOp",EDGE,"E3986"),sQuery(id+"F0.wireOp",EDGE,"E3987"),sQuery(id+"F0.wireOp",EDGE,"E3988"),sQuery(id+"F0.wireOp",EDGE,"E3989"),sQuery(id+"F0.wireOp",EDGE,"E3990"),sQuery(id+"F0.wireOp",EDGE,"E3991"),sQuery(id+"F0.wireOp",EDGE,"E3992"),sQuery(id+"F0.wireOp",EDGE,"E3993"),sQuery(id+"F0.wireOp",EDGE,"E3994"),sQuery(id+"F0.wireOp",EDGE,"E3995"),sQuery(id+"F0.wireOp",EDGE,"E3996"),sQuery(id+"F0.wireOp",EDGE,"E3997"),sQuery(id+"F0.wireOp",EDGE,"E3998"),sQuery(id+"F0.wireOp",EDGE,"E3999"),sQuery(id+"F0.wireOp",EDGE,"E4000"),sQuery(id+"F0.wireOp",EDGE,"E4001"),sQuery(id+"F0.wireOp",EDGE,"E4002"),sQuery(id+"F0.wireOp",EDGE,"E4003"),sQuery(id+"F0.wireOp",EDGE,"E4004"),sQuery(id+"F0.wireOp",EDGE,"E4005"),sQuery(id+"F0.wireOp",EDGE,"E4006"),sQuery(id+"F0.wireOp",EDGE,"E4007"),sQuery(id+"F0.wireOp",EDGE,"E4008"),sQuery(id+"F0.wireOp",EDGE,"E4009"),sQuery(id+"F0.wireOp",EDGE,"E4010"),sQuery(id+"F0.wireOp",EDGE,"E4011"),sQuery(id+"F0.wireOp",EDGE,"E4012"),sQuery(id+"F0.wireOp",EDGE,"E4013"),sQuery(id+"F0.wireOp",EDGE,"E4014"),sQuery(id+"F0.wireOp",EDGE,"E4015"),sQuery(id+"F0.wireOp",EDGE,"E4016"),sQuery(id+"F0.wireOp",EDGE,"E4017"),sQuery(id+"F0.wireOp",EDGE,"E4018"),sQuery(id+"F0.wireOp",EDGE,"E4019"),sQuery(id+"F0.wireOp",EDGE,"E4020"),sQuery(id+"F0.wireOp",EDGE,"E4021"),sQuery(id+"F0.wireOp",EDGE,"E4022"),sQuery(id+"F0.wireOp",EDGE,"E4023"),sQuery(id+"F0.wireOp",EDGE,"E4024"),sQuery(id+"F0.wireOp",EDGE,"E4025"),sQuery(id+"F0.wireOp",EDGE,"E4026"),sQuery(id+"F0.wireOp",EDGE,"E4027"),sQuery(id+"F0.wireOp",EDGE,"E4028"),sQuery(id+"F0.wireOp",EDGE,"E4029"),sQuery(id+"F0.wireOp",EDGE,"E4030"),sQuery(id+"F0.wireOp",EDGE,"E4031"),sQuery(id+"F0.wireOp",EDGE,"E4032"),sQuery(id+"F0.wireOp",EDGE,"E4033"),sQuery(id+"F0.wireOp",EDGE,"E4034"),sQuery(id+"F0.wireOp",EDGE,"E4035"),sQuery(id+"F0.wireOp",EDGE,"E4036"),sQuery(id+"F0.wireOp",EDGE,"E4037"),sQuery(id+"F0.wireOp",EDGE,"E4038"),sQuery(id+"F0.wireOp",EDGE,"E4039"),sQuery(id+"F0.wireOp",EDGE,"E4040"),sQuery(id+"F0.wireOp",EDGE,"E4041"),sQuery(id+"F0.wireOp",EDGE,"E4042"),sQuery(id+"F0.wireOp",EDGE,"E4043"),sQuery(id+"F0.wireOp",EDGE,"E4044"),sQuery(id+"F0.wireOp",EDGE,"E4045"),sQuery(id+"F0.wireOp",EDGE,"E4046"),sQuery(id+"F0.wireOp",EDGE,"E4047"),sQuery(id+"F0.wireOp",EDGE,"E4048"),sQuery(id+"F0.wireOp",EDGE,"E4049")])],"isStart":false});
            var sketch = newSketch(context, id + "F9", { "sketchPlane" : qUnion([Q0])});
            skLineSegment(sketch, "E4067.rect.bottom", {"start": v(152.4, 152.4) * mm, "end": v(-152.4, 152.4) * mm});
            skLineSegment(sketch, "E4067.rect.top", {"start": v(152.4, -152.4) * mm, "end": v(-152.4, -152.4) * mm});
            skLineSegment(sketch, "E4067.rect.left", {"start": v(152.4, 152.4) * mm, "end": v(152.4, -152.4) * mm});
            skLineSegment(sketch, "E4067.rect.right", {"start": v(-152.4, 152.4) * mm, "end": v(-152.4, -152.4) * mm});
            skPoint(sketch, "E4067.rect.middle", {"position": v(0, 0) * mm});
            skSolve(sketch);
        }
        {
            var Q0;
            Q0 = qSketchRegion(id + "F9", true);
            extrude(context, id + "F10", {"entities" : qUnion([Q0]), "depth" : 12.7 * mm});
        }
        {
            var Q0;
            Q0=makeQuery(id+"F10.opExtrude","SWEPT_EDGE",EDGE,{"disambiguationData":[OSD([sQuery(id+"F9.wireOp",EDGE,"E4067.rect.top"),sQuery(id+"F9.wireOp",EDGE,"E4067.rect.left")])]});
            var Q1;
            Q1=makeQuery(id+"F10.opExtrude","SWEPT_EDGE",EDGE,{"disambiguationData":[OSD([sQuery(id+"F9.wireOp",EDGE,"E4067.rect.top"),sQuery(id+"F9.wireOp",EDGE,"E4067.rect.right")])]});
            var Q2;
            Q2=makeQuery(id+"F10.opExtrude","SWEPT_EDGE",EDGE,{"disambiguationData":[OSD([sQuery(id+"F9.wireOp",EDGE,"E4067.rect.bottom"),sQuery(id+"F9.wireOp",EDGE,"E4067.rect.left")])]});
            var Q3;
            Q3=makeQuery(id+"F10.opExtrude","SWEPT_EDGE",EDGE,{"disambiguationData":[OSD([sQuery(id+"F9.wireOp",EDGE,"E4067.rect.bottom"),sQuery(id+"F9.wireOp",EDGE,"E4067.rect.right")])]});
            chamfer(context, id + "F11", {"entities" : qUnion([Q0, Q1, Q2, Q3]), "width" : 25.4 * mm, "tangentPropagation" : true});
        }
        {
            var Q0;
            Q0 = qSketchRegion(id + "F2", true);
            extrude(context, id + "F12", {"entities" : qUnion([Q0]), "operationType" : NewBodyOperationType.REMOVE, "endBound" : BoundingType.THROUGH_ALL, "depth" : 25.4 * mm});
        }
        {
            var Q0;
            Q0=makeQuery(id+"F10.opExtrude","CAP_FACE",FACE,{"disambiguationData":[OSD([sQuery(id+"F9.wireOp",EDGE,"E4067.rect.bottom"),sQuery(id+"F9.wireOp",EDGE,"E4067.rect.top"),sQuery(id+"F9.wireOp",EDGE,"E4067.rect.left"),sQuery(id+"F9.wireOp",EDGE,"E4067.rect.right")])],"isStart":true});
            var sketch = newSketch(context, id + "F13", { "sketchPlane" : qUnion([Q0])});
            skCircle(sketch, "E4068", {"center": v(-76.2, 0) * mm, "radius": 3.87 * mm});
            skCircle(sketch, "E4069", {"center": v(-38.1, 66) * mm, "radius": 3.87 * mm});
            skCircle(sketch, "E4070", {"center": v(38.1, 66) * mm, "radius": 3.87 * mm});
            skCircle(sketch, "E4071", {"center": v(76.2, 0) * mm, "radius": 3.87 * mm});
            skCircle(sketch, "E4072", {"center": v(38.1, -66) * mm, "radius": 3.87 * mm});
            skCircle(sketch, "E4073", {"center": v(-38.1, -66) * mm, "radius": 3.87 * mm});
            skSolve(sketch);
        }
        {
            var Q0;
            Q0 = qSketchRegion(id + "F13", true);
            extrude(context, id + "F14", {"entities" : qUnion([Q0]), "operationType" : NewBodyOperationType.REMOVE, "endBound" : BoundingType.THROUGH_ALL, "oppositeDirection" : true, "depth" : 25.4 * mm});
        }
        {
            var Q0;
            Q0=makeQuery(id+"F10.opExtrude","CAP_FACE",FACE,{"disambiguationData":[OSD([sQuery(id+"F9.wireOp",EDGE,"E4067.rect.bottom"),sQuery(id+"F9.wireOp",EDGE,"E4067.rect.top"),sQuery(id+"F9.wireOp",EDGE,"E4067.rect.left"),sQuery(id+"F9.wireOp",EDGE,"E4067.rect.right")])],"isStart":false});
            var sketch = newSketch(context, id + "F15", { "sketchPlane" : qUnion([Q0])});
            skCircle(sketch, "E4074", {"center": v(-127, 95.7) * mm, "radius": 3.87 * mm});
            skCircle(sketch, "E4075", {"center": v(-127, -95.7) * mm, "radius": 3.87 * mm});
            skCircle(sketch, "E4076.MirrorC", {"center": v(127, 95.7) * mm, "radius": 3.87 * mm});
            skCircle(sketch, "E4077.MirrorC", {"center": v(127, -95.7) * mm, "radius": 3.87 * mm});
            skLineSegment(sketch, "E4078.bottom", {"start": v(-127, 95.7) * mm, "end": v(127, 95.7) * mm, "construction": true});
            skLineSegment(sketch, "E4078.top", {"start": v(-127, -95.7) * mm, "end": v(127, -95.7) * mm, "construction": true});
            skLineSegment(sketch, "E4078.left", {"start": v(-127, 95.7) * mm, "end": v(-127, -95.7) * mm, "construction": true});
            skLineSegment(sketch, "E4078.right", {"start": v(127, 95.7) * mm, "end": v(127, -95.7) * mm, "construction": true});
            skLineSegment(sketch, "E4079", {"start": v(-127, -95.7) * mm, "end": v(127, 95.7) * mm, "construction": true});
            skLineSegment(sketch, "E4080", {"start": v(-127, 95.7) * mm, "end": v(127, -95.7) * mm, "construction": true});
            skSolve(sketch);
        }
        {
            var Q0;
            Q0 = qSketchRegion(id + "F15", true);
            extrude(context, id + "F16", {"entities" : qUnion([Q0]), "operationType" : NewBodyOperationType.REMOVE, "oppositeDirection" : true, "depth" : 25.4 * mm});
        }
        {
            var Q0;
            Q0=qCreatedBy(makeId("Front.planeOp"),FACE);
            var sketch = newSketch(context, id + "F17", { "sketchPlane" : qUnion([Q0])});
            skLineSegment(sketch, "E4081.bottom", {"start": v(12.7, -3.18) * mm, "end": v(15.88, -3.18) * mm});
            skLineSegment(sketch, "E4081.top", {"start": v(12.7, -2.54) * mm, "end": v(15.88, -2.54) * mm});
            skLineSegment(sketch, "E4081.left", {"start": v(12.7, -3.18) * mm, "end": v(12.7, -2.54) * mm});
            skLineSegment(sketch, "E4081.right", {"start": v(15.88, -3.18) * mm, "end": v(15.88, -2.54) * mm});
            skLineSegment(sketch, "E4082.1.0.2", {"start": v(22.23, -3.18) * mm, "end": v(25.4, -3.18) * mm});
            skLineSegment(sketch, "E4082.1.0.5", {"start": v(22.23, -2.54) * mm, "end": v(25.4, -2.54) * mm});
            skLineSegment(sketch, "E4082.1.0.10", {"start": v(22.23, -3.18) * mm, "end": v(22.23, -2.54) * mm});
            skLineSegment(sketch, "E4082.1.0.11", {"start": v(25.4, -3.18) * mm, "end": v(25.4, -2.54) * mm});
            skLineSegment(sketch, "E4082.2.0.2", {"start": v(31.75, -3.18) * mm, "end": v(34.92, -3.18) * mm});
            skLineSegment(sketch, "E4082.2.0.5", {"start": v(31.75, -2.54) * mm, "end": v(34.92, -2.54) * mm});
            skLineSegment(sketch, "E4082.2.0.10", {"start": v(31.75, -3.18) * mm, "end": v(31.75, -2.54) * mm});
            skLineSegment(sketch, "E4082.2.0.11", {"start": v(34.93, -3.18) * mm, "end": v(34.93, -2.54) * mm});
            skLineSegment(sketch, "E4082.3.0.2", {"start": v(41.28, -3.18) * mm, "end": v(44.45, -3.18) * mm});
            skLineSegment(sketch, "E4082.3.0.5", {"start": v(41.28, -2.54) * mm, "end": v(44.45, -2.54) * mm});
            skLineSegment(sketch, "E4082.3.0.10", {"start": v(41.28, -3.18) * mm, "end": v(41.28, -2.54) * mm});
            skLineSegment(sketch, "E4082.3.0.11", {"start": v(44.45, -3.18) * mm, "end": v(44.45, -2.54) * mm});
            skLineSegment(sketch, "E4082.4.0.2", {"start": v(50.8, -3.18) * mm, "end": v(53.98, -3.18) * mm});
            skLineSegment(sketch, "E4082.4.0.5", {"start": v(50.8, -2.54) * mm, "end": v(53.98, -2.54) * mm});
            skLineSegment(sketch, "E4082.4.0.10", {"start": v(50.8, -3.18) * mm, "end": v(50.8, -2.54) * mm});
            skLineSegment(sketch, "E4082.4.0.11", {"start": v(53.98, -3.18) * mm, "end": v(53.98, -2.54) * mm});
            skLineSegment(sketch, "E4082.5.0.2", {"start": v(60.33, -3.18) * mm, "end": v(63.5, -3.18) * mm});
            skLineSegment(sketch, "E4082.5.0.5", {"start": v(60.33, -2.54) * mm, "end": v(63.5, -2.54) * mm});
            skLineSegment(sketch, "E4082.5.0.10", {"start": v(60.33, -3.18) * mm, "end": v(60.33, -2.54) * mm});
            skLineSegment(sketch, "E4082.5.0.11", {"start": v(63.5, -3.18) * mm, "end": v(63.5, -2.54) * mm});
            skLineSegment(sketch, "E4082.6.0.2", {"start": v(69.85, -3.18) * mm, "end": v(73.03, -3.18) * mm});
            skLineSegment(sketch, "E4082.6.0.5", {"start": v(69.85, -2.54) * mm, "end": v(73.03, -2.54) * mm});
            skLineSegment(sketch, "E4082.6.0.10", {"start": v(69.85, -3.18) * mm, "end": v(69.85, -2.54) * mm});
            skLineSegment(sketch, "E4082.6.0.11", {"start": v(73.03, -3.18) * mm, "end": v(73.03, -2.54) * mm});
            skLineSegment(sketch, "E4082.7.0.2", {"start": v(79.38, -3.18) * mm, "end": v(82.55, -3.18) * mm});
            skLineSegment(sketch, "E4082.7.0.5", {"start": v(79.38, -2.54) * mm, "end": v(82.55, -2.54) * mm});
            skLineSegment(sketch, "E4082.7.0.10", {"start": v(79.38, -3.18) * mm, "end": v(79.38, -2.54) * mm});
            skLineSegment(sketch, "E4082.7.0.11", {"start": v(82.55, -3.18) * mm, "end": v(82.55, -2.54) * mm});
            skLineSegment(sketch, "E4082.8.0.2", {"start": v(88.9, -3.18) * mm, "end": v(92.08, -3.18) * mm});
            skLineSegment(sketch, "E4082.8.0.5", {"start": v(88.9, -2.54) * mm, "end": v(92.08, -2.54) * mm});
            skLineSegment(sketch, "E4082.8.0.10", {"start": v(88.9, -3.18) * mm, "end": v(88.9, -2.54) * mm});
            skLineSegment(sketch, "E4082.8.0.11", {"start": v(92.08, -3.18) * mm, "end": v(92.08, -2.54) * mm});
            skLineSegment(sketch, "E4082.direction1", {"start": v(12.7, -3.18) * mm, "end": v(22.23, -3.18) * mm, "construction": true});
            skSolve(sketch);
        }
        {
            var Q0;
            Q0=qCreatedBy(makeId("Front.planeOp"),FACE);
            var sketch = newSketch(context, id + "F18", { "sketchPlane" : qUnion([Q0])});
            skLineSegment(sketch, "E4083", {"start": v(0, 9.26) * mm, "end": v(0, -10.7) * mm, "construction": true});
            skSolve(sketch);
        }
        {
            var Q0;
            Q0 = qSketchRegion(id + "F17", true);
            var Q1;
            Q1=sQuery(id+"F18.wireOp",EDGE,"E4083");
            revolve(context, id + "F19", {"operationType" : NewBodyOperationType.REMOVE, "entities" : qUnion([Q0]), "axis" : qUnion([Q1]), "revolveType" : RevolveType.FULL, "oppositeDirection" : true});
        }
        {
            var Q0;
            Q0=qCreatedBy(makeId("Top.planeOp"),FACE);
            var sketch = newSketch(context, id + "F20", { "sketchPlane" : qUnion([Q0])});
            skCircle(sketch, "E4084", {"center": v(-76.2, 0) * mm, "radius": 12.7 * mm});
            skCircle(sketch, "E4085", {"center": v(-38.1, -66) * mm, "radius": 12.7 * mm});
            skCircle(sketch, "E4086", {"center": v(-38.1, 66) * mm, "radius": 12.7 * mm});
            skCircle(sketch, "E4087", {"center": v(38.1, 66) * mm, "radius": 12.7 * mm});
            skCircle(sketch, "E4088", {"center": v(76.2, 0) * mm, "radius": 12.7 * mm});
            skCircle(sketch, "E4089", {"center": v(38.1, -66) * mm, "radius": 12.7 * mm});
            skSolve(sketch);
        }
        {
            var Q0;
            Q0 = qSketchRegion(id + "F20", true);
            var Q1;
            {var subQ0=sQuery(id+"F6.wireOp",EDGE,"E4066");Q1=makeQuery(id+"F19.boolean.opBoolean","SPLIT",FACE,{"disambiguationData":[TD([makeQuery(id+"F7.opExtrude","SWEPT_FACE",FACE,{"disambiguationData":[OSD([subQ0])]})])],"derivedFrom":makeQuery(id+"F7.opExtrude","CAP_FACE",FACE,{"disambiguationData":[OSD([subQ0])],"isStart":false})});}
            extrude(context, id + "F21", {"entities" : qUnion([Q0]), "operationType" : NewBodyOperationType.ADD, "endBound" : BoundingType.UP_TO_SURFACE, "oppositeDirection" : true, "endBoundEntityFace" : qUnion([Q1]), "depth" : 25.4 * mm});
        }
        {
            var Q0;
            Q0=qCreatedBy(makeId("Top.planeOp"),FACE);
            var sketch = newSketch(context, id + "F22", { "sketchPlane" : qUnion([Q0])});
            skCircle(sketch, "E4090", {"center": v(-38.1, -66) * mm, "radius": 9.53 * mm});
            skCircle(sketch, "E4091", {"center": v(38.1, -66) * mm, "radius": 9.53 * mm});
            skCircle(sketch, "E4092", {"center": v(-76.2, 0) * mm, "radius": 9.53 * mm});
            skCircle(sketch, "E4093", {"center": v(76.2, 0) * mm, "radius": 9.53 * mm});
            skCircle(sketch, "E4094", {"center": v(38.1, 66) * mm, "radius": 9.53 * mm});
            skCircle(sketch, "E4095", {"center": v(-38.1, 66) * mm, "radius": 9.53 * mm});
            skSolve(sketch);
        }
        {
            var Q0;
            Q0 = qSketchRegion(id + "F22", true);
            extrude(context, id + "F23", {"entities" : qUnion([Q0]), "operationType" : NewBodyOperationType.REMOVE, "endBound" : BoundingType.THROUGH_ALL, "oppositeDirection" : true, "depth" : 25.4 * mm});
        }
        {
            var Q0;
            Q0=makeQuery(id+"F10.opExtrude","CAP_FACE",FACE,{"disambiguationData":[OSD([sQuery(id+"F9.wireOp",EDGE,"E4067.rect.bottom"),sQuery(id+"F9.wireOp",EDGE,"E4067.rect.top"),sQuery(id+"F9.wireOp",EDGE,"E4067.rect.left"),sQuery(id+"F9.wireOp",EDGE,"E4067.rect.right")])],"isStart":false});
            var sketch = newSketch(context, id + "F24", { "sketchPlane" : qUnion([Q0])});
            skLineSegment(sketch, "E4096", {"start": v(0, 152.4) * mm, "end": v(0, -152.4) * mm, "construction": true});
            skLineSegment(sketch, "E4097", {"start": v(-152.4, 0) * mm, "end": v(152.4, 0) * mm, "construction": true});
            skLineSegment(sketch, "E4098.bottom", {"start": v(-1.59, 152.4) * mm, "end": v(1.59, 152.4) * mm});
            skLineSegment(sketch, "E4098.top", {"start": v(-1.59, 88.9) * mm, "end": v(1.59, 88.9) * mm});
            skLineSegment(sketch, "E4098.left", {"start": v(-1.59, 152.4) * mm, "end": v(-1.59, 88.9) * mm});
            skLineSegment(sketch, "E4098.right", {"start": v(1.59, 152.4) * mm, "end": v(1.59, 88.9) * mm});
            skLineSegment(sketch, "E4099.1.0", {"start": v(-152.4, 1.59) * mm, "end": v(-88.9, 1.59) * mm});
            skLineSegment(sketch, "E4099.1.1", {"start": v(-152.4, -1.59) * mm, "end": v(-88.9, -1.59) * mm});
            skLineSegment(sketch, "E4099.1.2", {"start": v(-88.9, -1.59) * mm, "end": v(-88.9, 1.59) * mm});
            skLineSegment(sketch, "E4099.1.3", {"start": v(-152.4, -1.59) * mm, "end": v(-152.4, 1.59) * mm});
            skLineSegment(sketch, "E4099.2.0", {"start": v(-1.59, -152.4) * mm, "end": v(-1.59, -88.9) * mm});
            skLineSegment(sketch, "E4099.2.1", {"start": v(1.59, -152.4) * mm, "end": v(1.59, -88.9) * mm});
            skLineSegment(sketch, "E4099.2.2", {"start": v(1.59, -88.9) * mm, "end": v(-1.59, -88.9) * mm});
            skLineSegment(sketch, "E4099.2.3", {"start": v(1.59, -152.4) * mm, "end": v(-1.59, -152.4) * mm});
            skLineSegment(sketch, "E4099.3.0", {"start": v(152.4, -1.59) * mm, "end": v(88.9, -1.59) * mm});
            skLineSegment(sketch, "E4099.3.1", {"start": v(152.4, 1.59) * mm, "end": v(88.9, 1.59) * mm});
            skLineSegment(sketch, "E4099.3.2", {"start": v(88.9, 1.59) * mm, "end": v(88.9, -1.59) * mm});
            skLineSegment(sketch, "E4099.3.3", {"start": v(152.4, 1.59) * mm, "end": v(152.4, -1.59) * mm});
            skPoint(sketch, "E4099.center", {"position": v(0, 0) * mm});
            skSolve(sketch);
        }
        {
            var Q0;
            Q0 = qSketchRegion(id + "F24", true);
            extrude(context, id + "F25", {"entities" : qUnion([Q0]), "operationType" : NewBodyOperationType.REMOVE, "oppositeDirection" : true, "depth" : 6.35 * mm});
        }
    });
